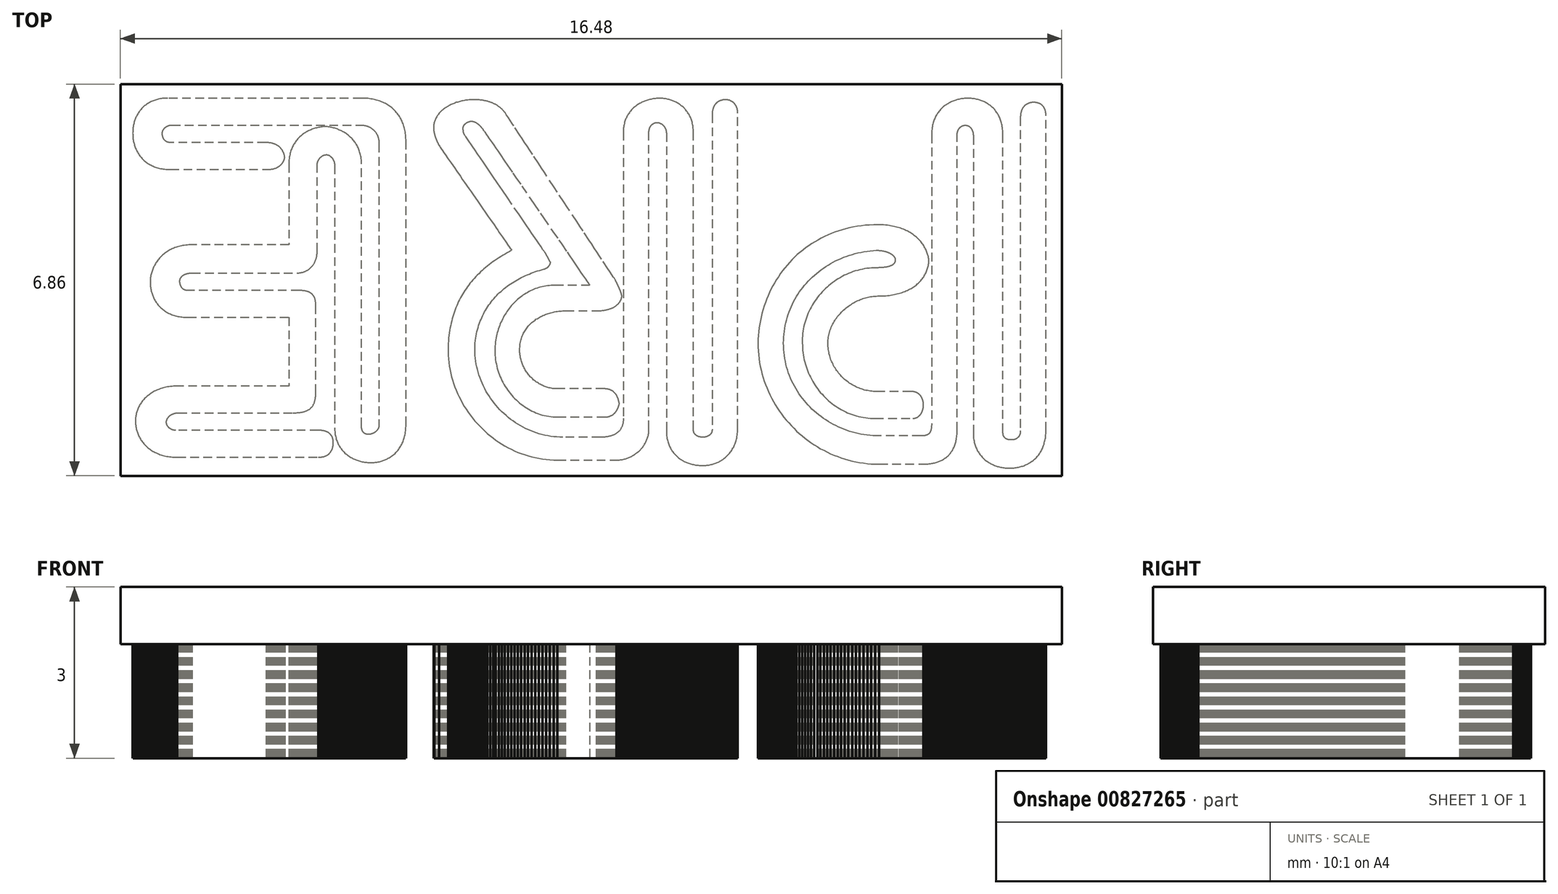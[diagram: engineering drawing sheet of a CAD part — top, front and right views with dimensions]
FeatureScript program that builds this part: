
annotation { "Feature Type Name" : "Feature", "Feature Type Description" : "" }
export const myFeature = defineFeature(function(context is Context, id is Id, definition is map)
    precondition{}
    {
        {
            var Q0;
            Q0=qCreatedBy(makeId("Top.planeOp"),FACE);
            var sketch = newSketch(context, id + "F0", { "sketchPlane" : qUnion([Q0])});
            skLineSegment(sketch, "E0", {"start": v(0.77, -0.53) * mm, "end": v(0.77, -0.53) * mm});
            skLineSegment(sketch, "E1", {"start": v(0.77, -0.53) * mm, "end": v(0.78, -0.54) * mm});
            skLineSegment(sketch, "E2", {"start": v(0.78, -0.54) * mm, "end": v(0.79, -0.55) * mm});
            skLineSegment(sketch, "E3", {"start": v(0.79, -0.55) * mm, "end": v(0.8, -0.57) * mm});
            skLineSegment(sketch, "E4", {"start": v(0.8, -0.57) * mm, "end": v(0.81, -0.59) * mm});
            skLineSegment(sketch, "E5", {"start": v(0.81, -0.59) * mm, "end": v(0.83, -0.61) * mm});
            skLineSegment(sketch, "E6", {"start": v(0.83, -0.61) * mm, "end": v(0.85, -0.64) * mm});
            skLineSegment(sketch, "E7", {"start": v(0.85, -0.64) * mm, "end": v(0.87, -0.67) * mm});
            skLineSegment(sketch, "E8", {"start": v(0.87, -0.67) * mm, "end": v(0.9, -0.7) * mm});
            skLineSegment(sketch, "E9", {"start": v(0.9, -0.7) * mm, "end": v(0.92, -0.74) * mm});
            skLineSegment(sketch, "E10", {"start": v(0.92, -0.74) * mm, "end": v(0.95, -0.79) * mm});
            skLineSegment(sketch, "E11", {"start": v(0.95, -0.79) * mm, "end": v(0.98, -0.83) * mm});
            skLineSegment(sketch, "E12", {"start": v(0.98, -0.83) * mm, "end": v(1, -0.88) * mm});
            skLineSegment(sketch, "E13", {"start": v(1, -0.88) * mm, "end": v(1.04, -0.93) * mm});
            skLineSegment(sketch, "E14", {"start": v(1.04, -0.93) * mm, "end": v(1.08, -0.98) * mm});
            skLineSegment(sketch, "E15", {"start": v(1.08, -0.98) * mm, "end": v(1.11, -1.03) * mm});
            skLineSegment(sketch, "E16", {"start": v(1.11, -1.03) * mm, "end": v(1.15, -1.08) * mm});
            skLineSegment(sketch, "E17", {"start": v(1.15, -1.08) * mm, "end": v(1.19, -1.14) * mm});
            skLineSegment(sketch, "E18", {"start": v(1.19, -1.14) * mm, "end": v(1.23, -1.2) * mm});
            skLineSegment(sketch, "E19", {"start": v(1.23, -1.2) * mm, "end": v(1.27, -1.26) * mm});
            skLineSegment(sketch, "E20", {"start": v(1.27, -1.26) * mm, "end": v(1.31, -1.32) * mm});
            skLineSegment(sketch, "E21", {"start": v(1.31, -1.32) * mm, "end": v(1.35, -1.38) * mm});
            skLineSegment(sketch, "E22", {"start": v(1.35, -1.38) * mm, "end": v(1.4, -1.44) * mm});
            skLineSegment(sketch, "E23", {"start": v(1.4, -1.44) * mm, "end": v(1.44, -1.5) * mm});
            skLineSegment(sketch, "E24", {"start": v(1.44, -1.5) * mm, "end": v(1.48, -1.57) * mm});
            skLineSegment(sketch, "E25", {"start": v(1.48, -1.57) * mm, "end": v(1.52, -1.63) * mm});
            skLineSegment(sketch, "E26", {"start": v(1.52, -1.63) * mm, "end": v(1.56, -1.69) * mm});
            skLineSegment(sketch, "E27", {"start": v(1.56, -1.69) * mm, "end": v(1.6, -1.75) * mm});
            skLineSegment(sketch, "E28", {"start": v(1.6, -1.75) * mm, "end": v(1.65, -1.81) * mm});
            skLineSegment(sketch, "E29", {"start": v(1.65, -1.81) * mm, "end": v(1.69, -1.87) * mm});
            skLineSegment(sketch, "E30", {"start": v(1.69, -1.87) * mm, "end": v(1.73, -1.93) * mm});
            skLineSegment(sketch, "E31", {"start": v(1.73, -1.93) * mm, "end": v(1.77, -1.99) * mm});
            skLineSegment(sketch, "E32", {"start": v(1.77, -1.99) * mm, "end": v(1.8, -2.05) * mm});
            skLineSegment(sketch, "E33", {"start": v(1.8, -2.05) * mm, "end": v(1.84, -2.1) * mm});
            skLineSegment(sketch, "E34", {"start": v(1.84, -2.1) * mm, "end": v(1.88, -2.15) * mm});
            skLineSegment(sketch, "E35", {"start": v(1.88, -2.15) * mm, "end": v(1.91, -2.2) * mm});
            skLineSegment(sketch, "E36", {"start": v(1.91, -2.2) * mm, "end": v(1.95, -2.25) * mm});
            skLineSegment(sketch, "E37", {"start": v(1.95, -2.25) * mm, "end": v(1.98, -2.3) * mm});
            skLineSegment(sketch, "E38", {"start": v(1.98, -2.3) * mm, "end": v(2, -2.35) * mm});
            skLineSegment(sketch, "E39", {"start": v(2, -2.35) * mm, "end": v(2.04, -2.39) * mm});
            skLineSegment(sketch, "E40", {"start": v(2.04, -2.39) * mm, "end": v(2.06, -2.42) * mm});
            skLineSegment(sketch, "E41", {"start": v(2.06, -2.42) * mm, "end": v(2.09, -2.46) * mm});
            skLineSegment(sketch, "E42", {"start": v(2.09, -2.46) * mm, "end": v(2.1, -2.5) * mm});
            skLineSegment(sketch, "E43", {"start": v(2.1, -2.5) * mm, "end": v(2.13, -2.52) * mm});
            skLineSegment(sketch, "E44", {"start": v(2.13, -2.52) * mm, "end": v(2.15, -2.54) * mm});
            skLineSegment(sketch, "E45", {"start": v(2.15, -2.54) * mm, "end": v(2.16, -2.56) * mm});
            skLineSegment(sketch, "E46", {"start": v(2.16, -2.56) * mm, "end": v(2.17, -2.58) * mm});
            skLineSegment(sketch, "E47", {"start": v(2.17, -2.58) * mm, "end": v(2.18, -2.6) * mm});
            skLineSegment(sketch, "E48", {"start": v(2.18, -2.6) * mm, "end": v(2.18, -2.6) * mm});
            skLineSegment(sketch, "E49", {"start": v(2.18, -2.6) * mm, "end": v(2.19, -2.6) * mm});
            skLineSegment(sketch, "E50", {"start": v(2.19, -2.6) * mm, "end": v(2.19, -2.6) * mm});
            skLineSegment(sketch, "E51", {"start": v(2.19, -2.6) * mm, "end": v(2.19, -2.61) * mm});
            skLineSegment(sketch, "E52", {"start": v(2.19, -2.61) * mm, "end": v(2.2, -2.61) * mm});
            skLineSegment(sketch, "E53", {"start": v(2.2, -2.61) * mm, "end": v(2.2, -2.62) * mm});
            skLineSegment(sketch, "E54", {"start": v(2.2, -2.62) * mm, "end": v(2.2, -2.62) * mm});
            skLineSegment(sketch, "E55", {"start": v(2.2, -2.62) * mm, "end": v(2.2, -2.63) * mm});
            skLineSegment(sketch, "E56", {"start": v(2.2, -2.63) * mm, "end": v(2.2, -2.63) * mm});
            skLineSegment(sketch, "E57", {"start": v(2.2, -2.63) * mm, "end": v(2.2, -2.64) * mm});
            skLineSegment(sketch, "E58", {"start": v(2.2, -2.64) * mm, "end": v(2.2, -2.64) * mm});
            skLineSegment(sketch, "E59", {"start": v(2.2, -2.64) * mm, "end": v(2.2, -2.65) * mm});
            skLineSegment(sketch, "E60", {"start": v(2.2, -2.65) * mm, "end": v(2.2, -2.65) * mm});
            skLineSegment(sketch, "E61", {"start": v(2.2, -2.65) * mm, "end": v(2.2, -2.66) * mm});
            skLineSegment(sketch, "E62", {"start": v(2.2, -2.66) * mm, "end": v(2.2, -2.66) * mm});
            skLineSegment(sketch, "E63", {"start": v(2.2, -2.66) * mm, "end": v(2.2, -2.67) * mm});
            skLineSegment(sketch, "E64", {"start": v(2.2, -2.67) * mm, "end": v(2.2, -2.67) * mm});
            skLineSegment(sketch, "E65", {"start": v(2.2, -2.67) * mm, "end": v(2.2, -2.68) * mm});
            skLineSegment(sketch, "E66", {"start": v(2.2, -2.68) * mm, "end": v(2.2, -2.68) * mm});
            skLineSegment(sketch, "E67", {"start": v(2.2, -2.68) * mm, "end": v(2.2, -2.69) * mm});
            skLineSegment(sketch, "E68", {"start": v(2.2, -2.69) * mm, "end": v(2.2, -2.69) * mm});
            skLineSegment(sketch, "E69", {"start": v(2.2, -2.69) * mm, "end": v(2.2, -2.7) * mm});
            skLineSegment(sketch, "E70", {"start": v(2.2, -2.7) * mm, "end": v(2.2, -2.7) * mm});
            skLineSegment(sketch, "E71", {"start": v(2.2, -2.7) * mm, "end": v(2.2, -2.71) * mm});
            skLineSegment(sketch, "E72", {"start": v(2.2, -2.71) * mm, "end": v(2.2, -2.71) * mm});
            skLineSegment(sketch, "E73", {"start": v(2.2, -2.71) * mm, "end": v(2.2, -2.72) * mm});
            skLineSegment(sketch, "E74", {"start": v(2.2, -2.72) * mm, "end": v(2.2, -2.72) * mm});
            skLineSegment(sketch, "E75", {"start": v(2.2, -2.72) * mm, "end": v(2.2, -2.73) * mm});
            skLineSegment(sketch, "E76", {"start": v(2.2, -2.73) * mm, "end": v(2.2, -2.73) * mm});
            skLineSegment(sketch, "E77", {"start": v(2.2, -2.73) * mm, "end": v(2.2, -2.74) * mm});
            skLineSegment(sketch, "E78", {"start": v(2.2, -2.74) * mm, "end": v(2.2, -2.74) * mm});
            skLineSegment(sketch, "E79", {"start": v(2.2, -2.74) * mm, "end": v(2.2, -2.75) * mm});
            skLineSegment(sketch, "E80", {"start": v(2.2, -2.75) * mm, "end": v(2.2, -2.75) * mm});
            skLineSegment(sketch, "E81", {"start": v(2.2, -2.75) * mm, "end": v(2.2, -2.76) * mm});
            skLineSegment(sketch, "E82", {"start": v(2.2, -2.76) * mm, "end": v(2.2, -2.76) * mm});
            skLineSegment(sketch, "E83", {"start": v(2.2, -2.76) * mm, "end": v(2.2, -2.77) * mm});
            skLineSegment(sketch, "E84", {"start": v(2.2, -2.77) * mm, "end": v(2.2, -2.77) * mm});
            skLineSegment(sketch, "E85", {"start": v(2.2, -2.77) * mm, "end": v(2.19, -2.77) * mm});
            skLineSegment(sketch, "E86", {"start": v(2.19, -2.77) * mm, "end": v(2.19, -2.78) * mm});
            skLineSegment(sketch, "E87", {"start": v(2.19, -2.78) * mm, "end": v(2.18, -2.78) * mm});
            skLineSegment(sketch, "E88", {"start": v(2.18, -2.78) * mm, "end": v(2.18, -2.78) * mm});
            skLineSegment(sketch, "E89", {"start": v(2.18, -2.78) * mm, "end": v(2.18, -2.79) * mm});
            skLineSegment(sketch, "E90", {"start": v(2.18, -2.79) * mm, "end": v(2.18, -2.79) * mm});
            skLineSegment(sketch, "E91", {"start": v(2.18, -2.79) * mm, "end": v(2.17, -2.8) * mm});
            skLineSegment(sketch, "E92", {"start": v(2.17, -2.8) * mm, "end": v(2.17, -2.8) * mm});
            skLineSegment(sketch, "E93", {"start": v(2.17, -2.8) * mm, "end": v(2.16, -2.8) * mm});
            skLineSegment(sketch, "E94", {"start": v(2.16, -2.8) * mm, "end": v(2.16, -2.8) * mm});
            skLineSegment(sketch, "E95", {"start": v(2.16, -2.8) * mm, "end": v(2.15, -2.8) * mm});
            skLineSegment(sketch, "E96", {"start": v(2.15, -2.8) * mm, "end": v(2.15, -2.81) * mm});
            skLineSegment(sketch, "E97", {"start": v(2.15, -2.81) * mm, "end": v(2.14, -2.81) * mm});
            skLineSegment(sketch, "E98", {"start": v(2.14, -2.81) * mm, "end": v(2.14, -2.81) * mm});
            skLineSegment(sketch, "E99", {"start": v(2.14, -2.81) * mm, "end": v(2.14, -2.82) * mm});
            skLineSegment(sketch, "E100", {"start": v(2.14, -2.82) * mm, "end": v(2.13, -2.82) * mm});
            skLineSegment(sketch, "E101", {"start": v(2.13, -2.82) * mm, "end": v(2.13, -2.82) * mm});
            skLineSegment(sketch, "E102", {"start": v(2.13, -2.82) * mm, "end": v(2.12, -2.82) * mm});
            skLineSegment(sketch, "E103", {"start": v(2.12, -2.82) * mm, "end": v(2.12, -2.83) * mm});
            skLineSegment(sketch, "E104", {"start": v(2.12, -2.83) * mm, "end": v(2.11, -2.83) * mm});
            skLineSegment(sketch, "E105", {"start": v(2.11, -2.83) * mm, "end": v(2.11, -2.83) * mm});
            skLineSegment(sketch, "E106", {"start": v(2.11, -2.83) * mm, "end": v(2.1, -2.83) * mm});
            skLineSegment(sketch, "E107", {"start": v(2.1, -2.83) * mm, "end": v(2.1, -2.83) * mm});
            skLineSegment(sketch, "E108", {"start": v(2.1, -2.83) * mm, "end": v(2.09, -2.83) * mm});
            skLineSegment(sketch, "E109", {"start": v(2.09, -2.83) * mm, "end": v(2.09, -2.84) * mm});
            skLineSegment(sketch, "E110", {"start": v(2.09, -2.84) * mm, "end": v(2.08, -2.84) * mm});
            skLineSegment(sketch, "E111", {"start": v(2.08, -2.84) * mm, "end": v(2.08, -2.84) * mm});
            skLineSegment(sketch, "E112", {"start": v(2.08, -2.84) * mm, "end": v(2.07, -2.84) * mm});
            skLineSegment(sketch, "E113", {"start": v(2.07, -2.84) * mm, "end": v(2.07, -2.84) * mm});
            skLineSegment(sketch, "E114", {"start": v(2.07, -2.84) * mm, "end": v(2.06, -2.84) * mm});
            skLineSegment(sketch, "E115", {"start": v(2.06, -2.84) * mm, "end": v(2.06, -2.84) * mm});
            skLineSegment(sketch, "E116", {"start": v(2.06, -2.84) * mm, "end": v(2.05, -2.84) * mm});
            skLineSegment(sketch, "E117", {"start": v(2.05, -2.84) * mm, "end": v(2.05, -2.84) * mm});
            skLineSegment(sketch, "E118", {"start": v(2.05, -2.84) * mm, "end": v(2.04, -2.84) * mm});
            skLineSegment(sketch, "E119", {"start": v(2.04, -2.84) * mm, "end": v(2.04, -2.83) * mm});
            skLineSegment(sketch, "E120", {"start": v(2.04, -2.83) * mm, "end": v(2.03, -2.83) * mm});
            skLineSegment(sketch, "E121", {"start": v(2.03, -2.83) * mm, "end": v(2.03, -2.83) * mm});
            skLineSegment(sketch, "E122", {"start": v(2.03, -2.83) * mm, "end": v(2.02, -2.83) * mm});
            skLineSegment(sketch, "E123", {"start": v(2.02, -2.83) * mm, "end": v(2.02, -2.83) * mm});
            skLineSegment(sketch, "E124", {"start": v(2.02, -2.83) * mm, "end": v(2.01, -2.83) * mm});
            skLineSegment(sketch, "E125", {"start": v(2.01, -2.83) * mm, "end": v(2, -2.83) * mm});
            skLineSegment(sketch, "E126", {"start": v(2, -2.83) * mm, "end": v(2, -2.82) * mm});
            skLineSegment(sketch, "E127", {"start": v(2, -2.82) * mm, "end": v(2, -2.82) * mm});
            skLineSegment(sketch, "E128", {"start": v(2, -2.82) * mm, "end": v(1.99, -2.82) * mm});
            skLineSegment(sketch, "E129", {"start": v(1.99, -2.82) * mm, "end": v(1.99, -2.81) * mm});
            skLineSegment(sketch, "E130", {"start": v(1.99, -2.81) * mm, "end": v(1.98, -2.81) * mm});
            skLineSegment(sketch, "E131", {"start": v(1.98, -2.81) * mm, "end": v(1.98, -2.8) * mm});
            skLineSegment(sketch, "E132", {"start": v(1.98, -2.8) * mm, "end": v(1.97, -2.8) * mm});
            skLineSegment(sketch, "E133", {"start": v(1.97, -2.8) * mm, "end": v(1.97, -2.8) * mm});
            skLineSegment(sketch, "E134", {"start": v(1.97, -2.8) * mm, "end": v(1.96, -2.8) * mm});
            skLineSegment(sketch, "E135", {"start": v(1.96, -2.8) * mm, "end": v(1.96, -2.8) * mm});
            skLineSegment(sketch, "E136", {"start": v(1.96, -2.8) * mm, "end": v(1.95, -2.8) * mm});
            skLineSegment(sketch, "E137", {"start": v(1.95, -2.8) * mm, "end": v(1.95, -2.79) * mm});
            skLineSegment(sketch, "E138", {"start": v(1.95, -2.79) * mm, "end": v(1.94, -2.79) * mm});
            skLineSegment(sketch, "E139", {"start": v(1.94, -2.79) * mm, "end": v(1.94, -2.78) * mm});
            skLineSegment(sketch, "E140", {"start": v(1.94, -2.78) * mm, "end": v(1.93, -2.78) * mm});
            skLineSegment(sketch, "E141", {"start": v(1.93, -2.78) * mm, "end": v(1.93, -2.77) * mm});
            skLineSegment(sketch, "E142", {"start": v(1.93, -2.77) * mm, "end": v(1.93, -2.77) * mm});
            skLineSegment(sketch, "E143", {"start": v(1.93, -2.77) * mm, "end": v(1.92, -2.76) * mm});
            skLineSegment(sketch, "E144", {"start": v(1.92, -2.76) * mm, "end": v(1.92, -2.76) * mm});
            skLineSegment(sketch, "E145", {"start": v(1.92, -2.76) * mm, "end": v(1.91, -2.75) * mm});
            skLineSegment(sketch, "E146", {"start": v(1.91, -2.75) * mm, "end": v(1.9, -2.75) * mm});
            skLineSegment(sketch, "E147", {"start": v(1.9, -2.75) * mm, "end": v(1.9, -2.74) * mm});
            skLineSegment(sketch, "E148", {"start": v(1.9, -2.74) * mm, "end": v(1.9, -2.74) * mm});
            skLineSegment(sketch, "E149", {"start": v(1.9, -2.74) * mm, "end": v(1.9, -2.73) * mm});
            skLineSegment(sketch, "E150", {"start": v(1.9, -2.73) * mm, "end": v(1.89, -2.72) * mm});
            skLineSegment(sketch, "E151", {"start": v(1.89, -2.72) * mm, "end": v(1.88, -2.72) * mm});
            skLineSegment(sketch, "E152", {"start": v(1.88, -2.72) * mm, "end": v(1.88, -2.7) * mm});
            skLineSegment(sketch, "E153", {"start": v(1.88, -2.7) * mm, "end": v(1.87, -2.7) * mm});
            skLineSegment(sketch, "E154", {"start": v(1.87, -2.7) * mm, "end": v(1.86, -2.7) * mm});
            skLineSegment(sketch, "E155", {"start": v(1.86, -2.7) * mm, "end": v(1.86, -2.69) * mm});
            skLineSegment(sketch, "E156", {"start": v(1.86, -2.69) * mm, "end": v(1.85, -2.68) * mm});
            skLineSegment(sketch, "E157", {"start": v(1.85, -2.68) * mm, "end": v(1.85, -2.67) * mm});
            skLineSegment(sketch, "E158", {"start": v(1.85, -2.67) * mm, "end": v(1.84, -2.67) * mm});
            skLineSegment(sketch, "E159", {"start": v(1.84, -2.67) * mm, "end": v(1.84, -2.66) * mm});
            skLineSegment(sketch, "E160", {"start": v(1.84, -2.66) * mm, "end": v(1.83, -2.65) * mm});
            skLineSegment(sketch, "E161", {"start": v(1.83, -2.65) * mm, "end": v(1.83, -2.65) * mm});
            skLineSegment(sketch, "E162", {"start": v(1.83, -2.65) * mm, "end": v(1.82, -2.64) * mm});
            skLineSegment(sketch, "E163", {"start": v(1.82, -2.64) * mm, "end": v(1.81, -2.62) * mm});
            skLineSegment(sketch, "E164", {"start": v(1.81, -2.62) * mm, "end": v(1.8, -2.6) * mm});
            skLineSegment(sketch, "E165", {"start": v(1.8, -2.6) * mm, "end": v(1.78, -2.57) * mm});
            skLineSegment(sketch, "E166", {"start": v(1.78, -2.57) * mm, "end": v(1.76, -2.54) * mm});
            skLineSegment(sketch, "E167", {"start": v(1.76, -2.54) * mm, "end": v(1.73, -2.5) * mm});
            skLineSegment(sketch, "E168", {"start": v(1.73, -2.5) * mm, "end": v(1.7, -2.46) * mm});
            skLineSegment(sketch, "E169", {"start": v(1.7, -2.46) * mm, "end": v(1.67, -2.42) * mm});
            skLineSegment(sketch, "E170", {"start": v(1.67, -2.42) * mm, "end": v(1.64, -2.37) * mm});
            skLineSegment(sketch, "E171", {"start": v(1.64, -2.37) * mm, "end": v(1.6, -2.32) * mm});
            skLineSegment(sketch, "E172", {"start": v(1.6, -2.32) * mm, "end": v(1.56, -2.26) * mm});
            skLineSegment(sketch, "E173", {"start": v(1.56, -2.26) * mm, "end": v(1.52, -2.2) * mm});
            skLineSegment(sketch, "E174", {"start": v(1.52, -2.2) * mm, "end": v(1.48, -2.14) * mm});
            skLineSegment(sketch, "E175", {"start": v(1.48, -2.14) * mm, "end": v(1.43, -2.07) * mm});
            skLineSegment(sketch, "E176", {"start": v(1.43, -2.07) * mm, "end": v(1.39, -2) * mm});
            skLineSegment(sketch, "E177", {"start": v(1.39, -2) * mm, "end": v(1.34, -1.93) * mm});
            skLineSegment(sketch, "E178", {"start": v(1.34, -1.93) * mm, "end": v(1.29, -1.86) * mm});
            skLineSegment(sketch, "E179", {"start": v(1.29, -1.86) * mm, "end": v(1.24, -1.78) * mm});
            skLineSegment(sketch, "E180", {"start": v(1.24, -1.78) * mm, "end": v(1.18, -1.7) * mm});
            skLineSegment(sketch, "E181", {"start": v(1.18, -1.7) * mm, "end": v(1.13, -1.63) * mm});
            skLineSegment(sketch, "E182", {"start": v(1.13, -1.63) * mm, "end": v(1.08, -1.55) * mm});
            skLineSegment(sketch, "E183", {"start": v(1.08, -1.55) * mm, "end": v(1.02, -1.47) * mm});
            skLineSegment(sketch, "E184", {"start": v(1.02, -1.47) * mm, "end": v(0.97, -1.39) * mm});
            skLineSegment(sketch, "E185", {"start": v(0.97, -1.39) * mm, "end": v(0.91, -1.3) * mm});
            skLineSegment(sketch, "E186", {"start": v(0.91, -1.3) * mm, "end": v(0.86, -1.23) * mm});
            skLineSegment(sketch, "E187", {"start": v(0.86, -1.23) * mm, "end": v(0.8, -1.15) * mm});
            skLineSegment(sketch, "E188", {"start": v(0.8, -1.15) * mm, "end": v(0.75, -1.07) * mm});
            skLineSegment(sketch, "E189", {"start": v(0.75, -1.07) * mm, "end": v(0.7, -0.99) * mm});
            skLineSegment(sketch, "E190", {"start": v(0.7, -0.99) * mm, "end": v(0.64, -0.9) * mm});
            skLineSegment(sketch, "E191", {"start": v(0.64, -0.9) * mm, "end": v(0.59, -0.83) * mm});
            skLineSegment(sketch, "E192", {"start": v(0.59, -0.83) * mm, "end": v(0.54, -0.76) * mm});
            skLineSegment(sketch, "E193", {"start": v(0.54, -0.76) * mm, "end": v(0.49, -0.68) * mm});
            skLineSegment(sketch, "E194", {"start": v(0.49, -0.68) * mm, "end": v(0.44, -0.61) * mm});
            skLineSegment(sketch, "E195", {"start": v(0.44, -0.61) * mm, "end": v(0.4, -0.54) * mm});
            skLineSegment(sketch, "E196", {"start": v(0.4, -0.54) * mm, "end": v(0.35, -0.48) * mm});
            skLineSegment(sketch, "E197", {"start": v(0.35, -0.48) * mm, "end": v(0.3, -0.41) * mm});
            skLineSegment(sketch, "E198", {"start": v(0.3, -0.41) * mm, "end": v(0.26, -0.35) * mm});
            skLineSegment(sketch, "E199", {"start": v(0.26, -0.35) * mm, "end": v(0.22, -0.3) * mm});
            skLineSegment(sketch, "E200", {"start": v(0.22, -0.3) * mm, "end": v(0.19, -0.24) * mm});
            skLineSegment(sketch, "E201", {"start": v(0.19, -0.24) * mm, "end": v(0.15, -0.2) * mm});
            skLineSegment(sketch, "E202", {"start": v(0.15, -0.2) * mm, "end": v(0.12, -0.15) * mm});
            skLineSegment(sketch, "E203", {"start": v(0.12, -0.15) * mm, "end": v(0.1, -0.1) * mm});
            skLineSegment(sketch, "E204", {"start": v(0.1, -0.1) * mm, "end": v(0.07, -0.07) * mm});
            skLineSegment(sketch, "E205", {"start": v(0.07, -0.07) * mm, "end": v(0.05, -0.04) * mm});
            skLineSegment(sketch, "E206", {"start": v(0.05, -0.04) * mm, "end": v(0.03, -0.01) * mm});
            skLineSegment(sketch, "E207", {"start": v(0.03, -0.01) * mm, "end": v(0.01, 0) * mm});
            skLineSegment(sketch, "E208", {"start": v(0.01, 0) * mm, "end": v(0, 0.02) * mm});
            skLineSegment(sketch, "E209", {"start": v(0, 0.02) * mm, "end": v(0, 0.03) * mm});
            skLineSegment(sketch, "E210", {"start": v(0, 0.03) * mm, "end": v(0, 0.04) * mm});
            skLineSegment(sketch, "E211", {"start": v(0, 0.04) * mm, "end": v(0, 0.04) * mm});
            skLineSegment(sketch, "E212", {"start": v(0, 0.04) * mm, "end": v(0.01, 0.04) * mm});
            skLineSegment(sketch, "E213", {"start": v(0.01, 0.04) * mm, "end": v(0.02, 0.04) * mm});
            skLineSegment(sketch, "E214", {"start": v(0.02, 0.04) * mm, "end": v(0.03, 0.04) * mm});
            skLineSegment(sketch, "E215", {"start": v(0.03, 0.04) * mm, "end": v(0.04, 0.04) * mm});
            skLineSegment(sketch, "E216", {"start": v(0.04, 0.04) * mm, "end": v(0.05, 0.04) * mm});
            skLineSegment(sketch, "E217", {"start": v(0.05, 0.04) * mm, "end": v(0.06, 0.04) * mm});
            skLineSegment(sketch, "E218", {"start": v(0.06, 0.04) * mm, "end": v(0.07, 0.04) * mm});
            skLineSegment(sketch, "E219", {"start": v(0.07, 0.04) * mm, "end": v(0.08, 0.04) * mm});
            skLineSegment(sketch, "E220", {"start": v(0.08, 0.04) * mm, "end": v(0.1, 0.04) * mm});
            skLineSegment(sketch, "E221", {"start": v(0.1, 0.04) * mm, "end": v(0.11, 0.04) * mm});
            skLineSegment(sketch, "E222", {"start": v(0.11, 0.04) * mm, "end": v(0.13, 0.04) * mm});
            skLineSegment(sketch, "E223", {"start": v(0.13, 0.04) * mm, "end": v(0.14, 0.04) * mm});
            skLineSegment(sketch, "E224", {"start": v(0.14, 0.04) * mm, "end": v(0.16, 0.04) * mm});
            skLineSegment(sketch, "E225", {"start": v(0.16, 0.04) * mm, "end": v(0.17, 0.04) * mm});
            skLineSegment(sketch, "E226", {"start": v(0.17, 0.04) * mm, "end": v(0.2, 0.04) * mm});
            skLineSegment(sketch, "E227", {"start": v(0.2, 0.04) * mm, "end": v(0.2, 0.04) * mm});
            skLineSegment(sketch, "E228", {"start": v(0.2, 0.04) * mm, "end": v(0.23, 0.04) * mm});
            skLineSegment(sketch, "E229", {"start": v(0.23, 0.04) * mm, "end": v(0.25, 0.04) * mm});
            skLineSegment(sketch, "E230", {"start": v(0.25, 0.04) * mm, "end": v(0.26, 0.04) * mm});
            skLineSegment(sketch, "E231", {"start": v(0.26, 0.04) * mm, "end": v(0.28, 0.04) * mm});
            skLineSegment(sketch, "E232", {"start": v(0.28, 0.04) * mm, "end": v(0.3, 0.04) * mm});
            skLineSegment(sketch, "E233", {"start": v(0.3, 0.04) * mm, "end": v(0.32, 0.04) * mm});
            skLineSegment(sketch, "E234", {"start": v(0.32, 0.04) * mm, "end": v(0.34, 0.04) * mm});
            skLineSegment(sketch, "E235", {"start": v(0.34, 0.04) * mm, "end": v(0.36, 0.04) * mm});
            skLineSegment(sketch, "E236", {"start": v(0.36, 0.04) * mm, "end": v(0.37, 0.04) * mm});
            skLineSegment(sketch, "E237", {"start": v(0.37, 0.04) * mm, "end": v(0.4, 0.04) * mm});
            skLineSegment(sketch, "E238", {"start": v(0.4, 0.04) * mm, "end": v(0.4, 0.04) * mm});
            skLineSegment(sketch, "E239", {"start": v(0.4, 0.04) * mm, "end": v(0.43, 0.04) * mm});
            skLineSegment(sketch, "E240", {"start": v(0.43, 0.04) * mm, "end": v(0.44, 0.04) * mm});
            skLineSegment(sketch, "E241", {"start": v(0.44, 0.04) * mm, "end": v(0.46, 0.04) * mm});
            skLineSegment(sketch, "E242", {"start": v(0.46, 0.04) * mm, "end": v(0.47, 0.04) * mm});
            skLineSegment(sketch, "E243", {"start": v(0.47, 0.04) * mm, "end": v(0.49, 0.04) * mm});
            skLineSegment(sketch, "E244", {"start": v(0.49, 0.04) * mm, "end": v(0.5, 0.04) * mm});
            skLineSegment(sketch, "E245", {"start": v(0.5, 0.04) * mm, "end": v(0.52, 0.04) * mm});
            skLineSegment(sketch, "E246", {"start": v(0.52, 0.04) * mm, "end": v(0.53, 0.04) * mm});
            skLineSegment(sketch, "E247", {"start": v(0.53, 0.04) * mm, "end": v(0.54, 0.04) * mm});
            skLineSegment(sketch, "E248", {"start": v(0.54, 0.04) * mm, "end": v(0.55, 0.04) * mm});
            skLineSegment(sketch, "E249", {"start": v(0.55, 0.04) * mm, "end": v(0.56, 0.04) * mm});
            skLineSegment(sketch, "E250", {"start": v(0.56, 0.04) * mm, "end": v(0.57, 0.04) * mm});
            skLineSegment(sketch, "E251", {"start": v(0.57, 0.04) * mm, "end": v(0.58, 0.04) * mm});
            skLineSegment(sketch, "E252", {"start": v(0.58, 0.04) * mm, "end": v(0.59, 0.04) * mm});
            skLineSegment(sketch, "E253", {"start": v(0.59, 0.04) * mm, "end": v(0.6, 0.04) * mm});
            skLineSegment(sketch, "E254", {"start": v(0.6, 0.04) * mm, "end": v(0.6, 0.04) * mm});
            skLineSegment(sketch, "E255", {"start": v(0.6, 0.04) * mm, "end": v(0.64, 0.04) * mm});
            skLineSegment(sketch, "E256", {"start": v(0.64, 0.04) * mm, "end": v(0.67, 0.04) * mm});
            skLineSegment(sketch, "E257", {"start": v(0.67, 0.04) * mm, "end": v(0.7, 0.04) * mm});
            skLineSegment(sketch, "E258", {"start": v(0.7, 0.04) * mm, "end": v(0.73, 0.05) * mm});
            skLineSegment(sketch, "E259", {"start": v(0.73, 0.05) * mm, "end": v(0.77, 0.05) * mm});
            skLineSegment(sketch, "E260", {"start": v(0.77, 0.05) * mm, "end": v(0.8, 0.06) * mm});
            skLineSegment(sketch, "E261", {"start": v(0.8, 0.06) * mm, "end": v(0.83, 0.06) * mm});
            skLineSegment(sketch, "E262", {"start": v(0.83, 0.06) * mm, "end": v(0.86, 0.07) * mm});
            skLineSegment(sketch, "E263", {"start": v(0.86, 0.07) * mm, "end": v(0.89, 0.08) * mm});
            skLineSegment(sketch, "E264", {"start": v(0.89, 0.08) * mm, "end": v(0.92, 0.09) * mm});
            skLineSegment(sketch, "E265", {"start": v(0.92, 0.09) * mm, "end": v(0.94, 0.1) * mm});
            skLineSegment(sketch, "E266", {"start": v(0.94, 0.1) * mm, "end": v(0.97, 0.1) * mm});
            skLineSegment(sketch, "E267", {"start": v(0.97, 0.1) * mm, "end": v(1, 0.12) * mm});
            skLineSegment(sketch, "E268", {"start": v(1, 0.12) * mm, "end": v(1.03, 0.13) * mm});
            skLineSegment(sketch, "E269", {"start": v(1.03, 0.13) * mm, "end": v(1.06, 0.15) * mm});
            skLineSegment(sketch, "E270", {"start": v(1.06, 0.15) * mm, "end": v(1.08, 0.16) * mm});
            skLineSegment(sketch, "E271", {"start": v(1.08, 0.16) * mm, "end": v(1.1, 0.18) * mm});
            skLineSegment(sketch, "E272", {"start": v(1.1, 0.18) * mm, "end": v(1.13, 0.2) * mm});
            skLineSegment(sketch, "E273", {"start": v(1.13, 0.2) * mm, "end": v(1.16, 0.21) * mm});
            skLineSegment(sketch, "E274", {"start": v(1.16, 0.21) * mm, "end": v(1.19, 0.23) * mm});
            skLineSegment(sketch, "E275", {"start": v(1.19, 0.23) * mm, "end": v(1.2, 0.25) * mm});
            skLineSegment(sketch, "E276", {"start": v(1.2, 0.25) * mm, "end": v(1.23, 0.27) * mm});
            skLineSegment(sketch, "E277", {"start": v(1.23, 0.27) * mm, "end": v(1.26, 0.29) * mm});
            skLineSegment(sketch, "E278", {"start": v(1.26, 0.29) * mm, "end": v(1.28, 0.3) * mm});
            skLineSegment(sketch, "E279", {"start": v(1.28, 0.3) * mm, "end": v(1.3, 0.33) * mm});
            skLineSegment(sketch, "E280", {"start": v(1.3, 0.33) * mm, "end": v(1.32, 0.35) * mm});
            skLineSegment(sketch, "E281", {"start": v(1.32, 0.35) * mm, "end": v(1.34, 0.37) * mm});
            skLineSegment(sketch, "E282", {"start": v(1.34, 0.37) * mm, "end": v(1.36, 0.4) * mm});
            skLineSegment(sketch, "E283", {"start": v(1.36, 0.4) * mm, "end": v(1.38, 0.42) * mm});
            skLineSegment(sketch, "E284", {"start": v(1.38, 0.42) * mm, "end": v(1.4, 0.44) * mm});
            skLineSegment(sketch, "E285", {"start": v(1.4, 0.44) * mm, "end": v(1.42, 0.47) * mm});
            skLineSegment(sketch, "E286", {"start": v(1.42, 0.47) * mm, "end": v(1.44, 0.5) * mm});
            skLineSegment(sketch, "E287", {"start": v(1.44, 0.5) * mm, "end": v(1.46, 0.52) * mm});
            skLineSegment(sketch, "E288", {"start": v(1.46, 0.52) * mm, "end": v(1.47, 0.55) * mm});
            skLineSegment(sketch, "E289", {"start": v(1.47, 0.55) * mm, "end": v(1.5, 0.57) * mm});
            skLineSegment(sketch, "E290", {"start": v(1.5, 0.57) * mm, "end": v(1.5, 0.6) * mm});
            skLineSegment(sketch, "E291", {"start": v(1.5, 0.6) * mm, "end": v(1.52, 0.63) * mm});
            skLineSegment(sketch, "E292", {"start": v(1.52, 0.63) * mm, "end": v(1.53, 0.66) * mm});
            skLineSegment(sketch, "E293", {"start": v(1.53, 0.66) * mm, "end": v(1.55, 0.69) * mm});
            skLineSegment(sketch, "E294", {"start": v(1.55, 0.69) * mm, "end": v(1.56, 0.72) * mm});
            skLineSegment(sketch, "E295", {"start": v(1.56, 0.72) * mm, "end": v(1.57, 0.74) * mm});
            skLineSegment(sketch, "E296", {"start": v(1.57, 0.74) * mm, "end": v(1.58, 0.77) * mm});
            skLineSegment(sketch, "E297", {"start": v(1.58, 0.77) * mm, "end": v(1.6, 0.8) * mm});
            skLineSegment(sketch, "E298", {"start": v(1.6, 0.8) * mm, "end": v(1.6, 0.84) * mm});
            skLineSegment(sketch, "E299", {"start": v(1.6, 0.84) * mm, "end": v(1.61, 0.87) * mm});
            skLineSegment(sketch, "E300", {"start": v(1.61, 0.87) * mm, "end": v(1.62, 0.9) * mm});
            skLineSegment(sketch, "E301", {"start": v(1.62, 0.9) * mm, "end": v(1.63, 0.93) * mm});
            skLineSegment(sketch, "E302", {"start": v(1.63, 0.93) * mm, "end": v(1.63, 0.96) * mm});
            skLineSegment(sketch, "E303", {"start": v(1.63, 0.96) * mm, "end": v(1.64, 1) * mm});
            skLineSegment(sketch, "E304", {"start": v(1.64, 1) * mm, "end": v(1.64, 1.03) * mm});
            skLineSegment(sketch, "E305", {"start": v(1.64, 1.03) * mm, "end": v(1.65, 1.07) * mm});
            skLineSegment(sketch, "E306", {"start": v(1.65, 1.07) * mm, "end": v(1.65, 1.1) * mm});
            skLineSegment(sketch, "E307", {"start": v(1.65, 1.1) * mm, "end": v(1.65, 1.14) * mm});
            skLineSegment(sketch, "E308", {"start": v(1.65, 1.14) * mm, "end": v(1.65, 1.18) * mm});
            skLineSegment(sketch, "E309", {"start": v(1.65, 1.18) * mm, "end": v(1.65, 1.22) * mm});
            skLineSegment(sketch, "E310", {"start": v(1.65, 1.22) * mm, "end": v(1.65, 1.26) * mm});
            skLineSegment(sketch, "E311", {"start": v(1.65, 1.26) * mm, "end": v(1.65, 1.3) * mm});
            skLineSegment(sketch, "E312", {"start": v(1.65, 1.3) * mm, "end": v(1.64, 1.34) * mm});
            skLineSegment(sketch, "E313", {"start": v(1.64, 1.34) * mm, "end": v(1.64, 1.38) * mm});
            skLineSegment(sketch, "E314", {"start": v(1.64, 1.38) * mm, "end": v(1.63, 1.42) * mm});
            skLineSegment(sketch, "E315", {"start": v(1.63, 1.42) * mm, "end": v(1.62, 1.45) * mm});
            skLineSegment(sketch, "E316", {"start": v(1.62, 1.45) * mm, "end": v(1.61, 1.5) * mm});
            skLineSegment(sketch, "E317", {"start": v(1.61, 1.5) * mm, "end": v(1.6, 1.53) * mm});
            skLineSegment(sketch, "E318", {"start": v(1.6, 1.53) * mm, "end": v(1.59, 1.57) * mm});
            skLineSegment(sketch, "E319", {"start": v(1.59, 1.57) * mm, "end": v(1.58, 1.6) * mm});
            skLineSegment(sketch, "E320", {"start": v(1.58, 1.6) * mm, "end": v(1.56, 1.64) * mm});
            skLineSegment(sketch, "E321", {"start": v(1.56, 1.64) * mm, "end": v(1.55, 1.67) * mm});
            skLineSegment(sketch, "E322", {"start": v(1.55, 1.67) * mm, "end": v(1.53, 1.7) * mm});
            skLineSegment(sketch, "E323", {"start": v(1.53, 1.7) * mm, "end": v(1.51, 1.74) * mm});
            skLineSegment(sketch, "E324", {"start": v(1.51, 1.74) * mm, "end": v(1.5, 1.78) * mm});
            skLineSegment(sketch, "E325", {"start": v(1.5, 1.78) * mm, "end": v(1.47, 1.8) * mm});
            skLineSegment(sketch, "E326", {"start": v(1.47, 1.8) * mm, "end": v(1.45, 1.84) * mm});
            skLineSegment(sketch, "E327", {"start": v(1.45, 1.84) * mm, "end": v(1.43, 1.87) * mm});
            skLineSegment(sketch, "E328", {"start": v(1.43, 1.87) * mm, "end": v(1.4, 1.9) * mm});
            skLineSegment(sketch, "E329", {"start": v(1.4, 1.9) * mm, "end": v(1.38, 1.93) * mm});
            skLineSegment(sketch, "E330", {"start": v(1.38, 1.93) * mm, "end": v(1.36, 1.96) * mm});
            skLineSegment(sketch, "E331", {"start": v(1.36, 1.96) * mm, "end": v(1.33, 2) * mm});
            skLineSegment(sketch, "E332", {"start": v(1.33, 2) * mm, "end": v(1.3, 2.02) * mm});
            skLineSegment(sketch, "E333", {"start": v(1.3, 2.02) * mm, "end": v(1.28, 2.05) * mm});
            skLineSegment(sketch, "E334", {"start": v(1.28, 2.05) * mm, "end": v(1.25, 2.07) * mm});
            skLineSegment(sketch, "E335", {"start": v(1.25, 2.07) * mm, "end": v(1.22, 2.1) * mm});
            skLineSegment(sketch, "E336", {"start": v(1.22, 2.1) * mm, "end": v(1.2, 2.12) * mm});
            skLineSegment(sketch, "E337", {"start": v(1.2, 2.12) * mm, "end": v(1.16, 2.14) * mm});
            skLineSegment(sketch, "E338", {"start": v(1.16, 2.14) * mm, "end": v(1.13, 2.16) * mm});
            skLineSegment(sketch, "E339", {"start": v(1.13, 2.16) * mm, "end": v(1.1, 2.19) * mm});
            skLineSegment(sketch, "E340", {"start": v(1.1, 2.19) * mm, "end": v(1.07, 2.2) * mm});
            skLineSegment(sketch, "E341", {"start": v(1.07, 2.2) * mm, "end": v(1.04, 2.22) * mm});
            skLineSegment(sketch, "E342", {"start": v(1.04, 2.22) * mm, "end": v(1, 2.24) * mm});
            skLineSegment(sketch, "E343", {"start": v(1, 2.24) * mm, "end": v(0.97, 2.26) * mm});
            skLineSegment(sketch, "E344", {"start": v(0.97, 2.26) * mm, "end": v(0.93, 2.27) * mm});
            skLineSegment(sketch, "E345", {"start": v(0.93, 2.27) * mm, "end": v(0.9, 2.29) * mm});
            skLineSegment(sketch, "E346", {"start": v(0.9, 2.29) * mm, "end": v(0.86, 2.3) * mm});
            skLineSegment(sketch, "E347", {"start": v(0.86, 2.3) * mm, "end": v(0.83, 2.3) * mm});
            skLineSegment(sketch, "E348", {"start": v(0.83, 2.3) * mm, "end": v(0.79, 2.32) * mm});
            skLineSegment(sketch, "E349", {"start": v(0.79, 2.32) * mm, "end": v(0.75, 2.33) * mm});
            skLineSegment(sketch, "E350", {"start": v(0.75, 2.33) * mm, "end": v(0.71, 2.33) * mm});
            skLineSegment(sketch, "E351", {"start": v(0.71, 2.33) * mm, "end": v(0.68, 2.34) * mm});
            skLineSegment(sketch, "E352", {"start": v(0.68, 2.34) * mm, "end": v(0.64, 2.34) * mm});
            skLineSegment(sketch, "E353", {"start": v(0.64, 2.34) * mm, "end": v(0.6, 2.34) * mm});
            skLineSegment(sketch, "E354", {"start": v(0.6, 2.34) * mm, "end": v(0.56, 2.35) * mm});
            skLineSegment(sketch, "E355", {"start": v(0.56, 2.35) * mm, "end": v(0.56, 2.35) * mm});
            skLineSegment(sketch, "E356", {"start": v(0.56, 2.35) * mm, "end": v(0.55, 2.35) * mm});
            skLineSegment(sketch, "E357", {"start": v(0.55, 2.35) * mm, "end": v(0.54, 2.35) * mm});
            skLineSegment(sketch, "E358", {"start": v(0.54, 2.35) * mm, "end": v(0.54, 2.35) * mm});
            skLineSegment(sketch, "E359", {"start": v(0.54, 2.35) * mm, "end": v(0.53, 2.35) * mm});
            skLineSegment(sketch, "E360", {"start": v(0.53, 2.35) * mm, "end": v(0.52, 2.35) * mm});
            skLineSegment(sketch, "E361", {"start": v(0.52, 2.35) * mm, "end": v(0.5, 2.35) * mm});
            skLineSegment(sketch, "E362", {"start": v(0.5, 2.35) * mm, "end": v(0.49, 2.35) * mm});
            skLineSegment(sketch, "E363", {"start": v(0.49, 2.35) * mm, "end": v(0.47, 2.35) * mm});
            skLineSegment(sketch, "E364", {"start": v(0.47, 2.35) * mm, "end": v(0.46, 2.35) * mm});
            skLineSegment(sketch, "E365", {"start": v(0.46, 2.35) * mm, "end": v(0.44, 2.35) * mm});
            skLineSegment(sketch, "E366", {"start": v(0.44, 2.35) * mm, "end": v(0.42, 2.35) * mm});
            skLineSegment(sketch, "E367", {"start": v(0.42, 2.35) * mm, "end": v(0.4, 2.35) * mm});
            skLineSegment(sketch, "E368", {"start": v(0.4, 2.35) * mm, "end": v(0.38, 2.35) * mm});
            skLineSegment(sketch, "E369", {"start": v(0.38, 2.35) * mm, "end": v(0.36, 2.35) * mm});
            skLineSegment(sketch, "E370", {"start": v(0.36, 2.35) * mm, "end": v(0.34, 2.35) * mm});
            skLineSegment(sketch, "E371", {"start": v(0.34, 2.35) * mm, "end": v(0.32, 2.35) * mm});
            skLineSegment(sketch, "E372", {"start": v(0.32, 2.35) * mm, "end": v(0.3, 2.35) * mm});
            skLineSegment(sketch, "E373", {"start": v(0.3, 2.35) * mm, "end": v(0.27, 2.35) * mm});
            skLineSegment(sketch, "E374", {"start": v(0.27, 2.35) * mm, "end": v(0.25, 2.35) * mm});
            skLineSegment(sketch, "E375", {"start": v(0.25, 2.35) * mm, "end": v(0.22, 2.35) * mm});
            skLineSegment(sketch, "E376", {"start": v(0.22, 2.35) * mm, "end": v(0.2, 2.35) * mm});
            skLineSegment(sketch, "E377", {"start": v(0.2, 2.35) * mm, "end": v(0.17, 2.35) * mm});
            skLineSegment(sketch, "E378", {"start": v(0.17, 2.35) * mm, "end": v(0.15, 2.35) * mm});
            skLineSegment(sketch, "E379", {"start": v(0.15, 2.35) * mm, "end": v(0.12, 2.35) * mm});
            skLineSegment(sketch, "E380", {"start": v(0.12, 2.35) * mm, "end": v(0.1, 2.35) * mm});
            skLineSegment(sketch, "E381", {"start": v(0.1, 2.35) * mm, "end": v(0.07, 2.35) * mm});
            skLineSegment(sketch, "E382", {"start": v(0.07, 2.35) * mm, "end": v(0.05, 2.35) * mm});
            skLineSegment(sketch, "E383", {"start": v(0.05, 2.35) * mm, "end": v(0.03, 2.35) * mm});
            skLineSegment(sketch, "E384", {"start": v(0.03, 2.35) * mm, "end": v(0, 2.35) * mm});
            skLineSegment(sketch, "E385", {"start": v(0, 2.35) * mm, "end": v(-0.02, 2.35) * mm});
            skLineSegment(sketch, "E386", {"start": v(-0.02, 2.35) * mm, "end": v(-0.04, 2.35) * mm});
            skLineSegment(sketch, "E387", {"start": v(-0.04, 2.35) * mm, "end": v(-0.07, 2.35) * mm});
            skLineSegment(sketch, "E388", {"start": v(-0.07, 2.35) * mm, "end": v(-0.09, 2.35) * mm});
            skLineSegment(sketch, "E389", {"start": v(-0.09, 2.35) * mm, "end": v(-0.1, 2.35) * mm});
            skLineSegment(sketch, "E390", {"start": v(-0.1, 2.35) * mm, "end": v(-0.13, 2.35) * mm});
            skLineSegment(sketch, "E391", {"start": v(-0.13, 2.35) * mm, "end": v(-0.15, 2.35) * mm});
            skLineSegment(sketch, "E392", {"start": v(-0.15, 2.35) * mm, "end": v(-0.16, 2.35) * mm});
            skLineSegment(sketch, "E393", {"start": v(-0.16, 2.35) * mm, "end": v(-0.18, 2.35) * mm});
            skLineSegment(sketch, "E394", {"start": v(-0.18, 2.35) * mm, "end": v(-0.2, 2.35) * mm});
            skLineSegment(sketch, "E395", {"start": v(-0.2, 2.35) * mm, "end": v(-0.2, 2.35) * mm});
            skLineSegment(sketch, "E396", {"start": v(-0.2, 2.35) * mm, "end": v(-0.22, 2.35) * mm});
            skLineSegment(sketch, "E397", {"start": v(-0.22, 2.35) * mm, "end": v(-0.23, 2.35) * mm});
            skLineSegment(sketch, "E398", {"start": v(-0.23, 2.35) * mm, "end": v(-0.24, 2.35) * mm});
            skLineSegment(sketch, "E399", {"start": v(-0.24, 2.35) * mm, "end": v(-0.25, 2.35) * mm});
            skLineSegment(sketch, "E400", {"start": v(-0.25, 2.35) * mm, "end": v(-0.26, 2.35) * mm});
            skLineSegment(sketch, "E401", {"start": v(-0.26, 2.35) * mm, "end": v(-0.26, 2.35) * mm});
            skLineSegment(sketch, "E402", {"start": v(-0.26, 2.35) * mm, "end": v(-0.27, 2.35) * mm});
            skLineSegment(sketch, "E403", {"start": v(-0.27, 2.35) * mm, "end": v(-0.28, 2.35) * mm});
            skLineSegment(sketch, "E404", {"start": v(-0.28, 2.35) * mm, "end": v(-0.28, 2.35) * mm});
            skLineSegment(sketch, "E405", {"start": v(-0.28, 2.35) * mm, "end": v(-0.3, 2.34) * mm});
            skLineSegment(sketch, "E406", {"start": v(-0.3, 2.34) * mm, "end": v(-0.3, 2.34) * mm});
            skLineSegment(sketch, "E407", {"start": v(-0.3, 2.34) * mm, "end": v(-0.31, 2.34) * mm});
            skLineSegment(sketch, "E408", {"start": v(-0.31, 2.34) * mm, "end": v(-0.32, 2.34) * mm});
            skLineSegment(sketch, "E409", {"start": v(-0.32, 2.34) * mm, "end": v(-0.33, 2.34) * mm});
            skLineSegment(sketch, "E410", {"start": v(-0.33, 2.34) * mm, "end": v(-0.34, 2.34) * mm});
            skLineSegment(sketch, "E411", {"start": v(-0.34, 2.34) * mm, "end": v(-0.35, 2.33) * mm});
            skLineSegment(sketch, "E412", {"start": v(-0.35, 2.33) * mm, "end": v(-0.35, 2.33) * mm});
            skLineSegment(sketch, "E413", {"start": v(-0.35, 2.33) * mm, "end": v(-0.36, 2.33) * mm});
            skLineSegment(sketch, "E414", {"start": v(-0.36, 2.33) * mm, "end": v(-0.37, 2.33) * mm});
            skLineSegment(sketch, "E415", {"start": v(-0.37, 2.33) * mm, "end": v(-0.38, 2.32) * mm});
            skLineSegment(sketch, "E416", {"start": v(-0.38, 2.32) * mm, "end": v(-0.38, 2.32) * mm});
            skLineSegment(sketch, "E417", {"start": v(-0.38, 2.32) * mm, "end": v(-0.39, 2.32) * mm});
            skLineSegment(sketch, "E418", {"start": v(-0.39, 2.32) * mm, "end": v(-0.4, 2.31) * mm});
            skLineSegment(sketch, "E419", {"start": v(-0.4, 2.31) * mm, "end": v(-0.4, 2.3) * mm});
            skLineSegment(sketch, "E420", {"start": v(-0.4, 2.3) * mm, "end": v(-0.4, 2.3) * mm});
            skLineSegment(sketch, "E421", {"start": v(-0.4, 2.3) * mm, "end": v(-0.41, 2.3) * mm});
            skLineSegment(sketch, "E422", {"start": v(-0.41, 2.3) * mm, "end": v(-0.42, 2.3) * mm});
            skLineSegment(sketch, "E423", {"start": v(-0.42, 2.3) * mm, "end": v(-0.43, 2.3) * mm});
            skLineSegment(sketch, "E424", {"start": v(-0.43, 2.3) * mm, "end": v(-0.43, 2.29) * mm});
            skLineSegment(sketch, "E425", {"start": v(-0.43, 2.29) * mm, "end": v(-0.44, 2.28) * mm});
            skLineSegment(sketch, "E426", {"start": v(-0.44, 2.28) * mm, "end": v(-0.44, 2.28) * mm});
            skLineSegment(sketch, "E427", {"start": v(-0.44, 2.28) * mm, "end": v(-0.45, 2.27) * mm});
            skLineSegment(sketch, "E428", {"start": v(-0.45, 2.27) * mm, "end": v(-0.45, 2.27) * mm});
            skLineSegment(sketch, "E429", {"start": v(-0.45, 2.27) * mm, "end": v(-0.46, 2.26) * mm});
            skLineSegment(sketch, "E430", {"start": v(-0.46, 2.26) * mm, "end": v(-0.46, 2.26) * mm});
            skLineSegment(sketch, "E431", {"start": v(-0.46, 2.26) * mm, "end": v(-0.47, 2.25) * mm});
            skLineSegment(sketch, "E432", {"start": v(-0.47, 2.25) * mm, "end": v(-0.47, 2.24) * mm});
            skLineSegment(sketch, "E433", {"start": v(-0.47, 2.24) * mm, "end": v(-0.47, 2.24) * mm});
            skLineSegment(sketch, "E434", {"start": v(-0.47, 2.24) * mm, "end": v(-0.48, 2.23) * mm});
            skLineSegment(sketch, "E435", {"start": v(-0.48, 2.23) * mm, "end": v(-0.48, 2.23) * mm});
            skLineSegment(sketch, "E436", {"start": v(-0.48, 2.23) * mm, "end": v(-0.49, 2.22) * mm});
            skLineSegment(sketch, "E437", {"start": v(-0.49, 2.22) * mm, "end": v(-0.49, 2.21) * mm});
            skLineSegment(sketch, "E438", {"start": v(-0.49, 2.21) * mm, "end": v(-0.5, 2.2) * mm});
            skLineSegment(sketch, "E439", {"start": v(-0.5, 2.2) * mm, "end": v(-0.5, 2.2) * mm});
            skLineSegment(sketch, "E440", {"start": v(-0.5, 2.2) * mm, "end": v(-0.5, 2.19) * mm});
            skLineSegment(sketch, "E441", {"start": v(-0.5, 2.19) * mm, "end": v(-0.5, 2.18) * mm});
            skLineSegment(sketch, "E442", {"start": v(-0.5, 2.18) * mm, "end": v(-0.5, 2.17) * mm});
            skLineSegment(sketch, "E443", {"start": v(-0.5, 2.17) * mm, "end": v(-0.5, 2.17) * mm});
            skLineSegment(sketch, "E444", {"start": v(-0.5, 2.17) * mm, "end": v(-0.51, 2.16) * mm});
            skLineSegment(sketch, "E445", {"start": v(-0.51, 2.16) * mm, "end": v(-0.51, 2.15) * mm});
            skLineSegment(sketch, "E446", {"start": v(-0.51, 2.15) * mm, "end": v(-0.52, 2.15) * mm});
            skLineSegment(sketch, "E447", {"start": v(-0.52, 2.15) * mm, "end": v(-0.52, 2.14) * mm});
            skLineSegment(sketch, "E448", {"start": v(-0.52, 2.14) * mm, "end": v(-0.52, 2.13) * mm});
            skLineSegment(sketch, "E449", {"start": v(-0.52, 2.13) * mm, "end": v(-0.52, 2.12) * mm});
            skLineSegment(sketch, "E450", {"start": v(-0.52, 2.12) * mm, "end": v(-0.52, 2.12) * mm});
            skLineSegment(sketch, "E451", {"start": v(-0.52, 2.12) * mm, "end": v(-0.52, 2.11) * mm});
            skLineSegment(sketch, "E452", {"start": v(-0.52, 2.11) * mm, "end": v(-0.52, 2.1) * mm});
            skLineSegment(sketch, "E453", {"start": v(-0.52, 2.1) * mm, "end": v(-0.52, 2.1) * mm});
            skLineSegment(sketch, "E454", {"start": v(-0.52, 2.1) * mm, "end": v(-0.52, 2.08) * mm});
            skLineSegment(sketch, "E455", {"start": v(-0.52, 2.08) * mm, "end": v(-0.52, 2.08) * mm});
            skLineSegment(sketch, "E456", {"start": v(-0.52, 2.08) * mm, "end": v(-0.52, 2.07) * mm});
            skLineSegment(sketch, "E457", {"start": v(-0.52, 2.07) * mm, "end": v(-0.51, 2.06) * mm});
            skLineSegment(sketch, "E458", {"start": v(-0.51, 2.06) * mm, "end": v(-0.51, 2.05) * mm});
            skLineSegment(sketch, "E459", {"start": v(-0.51, 2.05) * mm, "end": v(-0.5, 2.04) * mm});
            skLineSegment(sketch, "E460", {"start": v(-0.5, 2.04) * mm, "end": v(-0.5, 2.04) * mm});
            skLineSegment(sketch, "E461", {"start": v(-0.5, 2.04) * mm, "end": v(-0.5, 2.03) * mm});
            skLineSegment(sketch, "E462", {"start": v(-0.5, 2.03) * mm, "end": v(-0.5, 2.02) * mm});
            skLineSegment(sketch, "E463", {"start": v(-0.5, 2.02) * mm, "end": v(-0.5, 2.01) * mm});
            skLineSegment(sketch, "E464", {"start": v(-0.5, 2.01) * mm, "end": v(-0.5, 2) * mm});
            skLineSegment(sketch, "E465", {"start": v(-0.5, 2) * mm, "end": v(-0.5, 2) * mm});
            skLineSegment(sketch, "E466", {"start": v(-0.5, 2) * mm, "end": v(-0.49, 2) * mm});
            skLineSegment(sketch, "E467", {"start": v(-0.49, 2) * mm, "end": v(-0.49, 1.98) * mm});
            skLineSegment(sketch, "E468", {"start": v(-0.49, 1.98) * mm, "end": v(-0.48, 1.98) * mm});
            skLineSegment(sketch, "E469", {"start": v(-0.48, 1.98) * mm, "end": v(-0.48, 1.97) * mm});
            skLineSegment(sketch, "E470", {"start": v(-0.48, 1.97) * mm, "end": v(-0.47, 1.96) * mm});
            skLineSegment(sketch, "E471", {"start": v(-0.47, 1.96) * mm, "end": v(-0.47, 1.96) * mm});
            skLineSegment(sketch, "E472", {"start": v(-0.47, 1.96) * mm, "end": v(-0.47, 1.95) * mm});
            skLineSegment(sketch, "E473", {"start": v(-0.47, 1.95) * mm, "end": v(-0.46, 1.95) * mm});
            skLineSegment(sketch, "E474", {"start": v(-0.46, 1.95) * mm, "end": v(-0.46, 1.94) * mm});
            skLineSegment(sketch, "E475", {"start": v(-0.46, 1.94) * mm, "end": v(-0.45, 1.93) * mm});
            skLineSegment(sketch, "E476", {"start": v(-0.45, 1.93) * mm, "end": v(-0.45, 1.93) * mm});
            skLineSegment(sketch, "E477", {"start": v(-0.45, 1.93) * mm, "end": v(-0.44, 1.92) * mm});
            skLineSegment(sketch, "E478", {"start": v(-0.44, 1.92) * mm, "end": v(-0.44, 1.92) * mm});
            skLineSegment(sketch, "E479", {"start": v(-0.44, 1.92) * mm, "end": v(-0.43, 1.91) * mm});
            skLineSegment(sketch, "E480", {"start": v(-0.43, 1.91) * mm, "end": v(-0.43, 1.9) * mm});
            skLineSegment(sketch, "E481", {"start": v(-0.43, 1.9) * mm, "end": v(-0.42, 1.9) * mm});
            skLineSegment(sketch, "E482", {"start": v(-0.42, 1.9) * mm, "end": v(-0.41, 1.9) * mm});
            skLineSegment(sketch, "E483", {"start": v(-0.41, 1.9) * mm, "end": v(-0.4, 1.9) * mm});
            skLineSegment(sketch, "E484", {"start": v(-0.4, 1.9) * mm, "end": v(-0.4, 1.89) * mm});
            skLineSegment(sketch, "E485", {"start": v(-0.4, 1.89) * mm, "end": v(-0.4, 1.88) * mm});
            skLineSegment(sketch, "E486", {"start": v(-0.4, 1.88) * mm, "end": v(-0.39, 1.88) * mm});
            skLineSegment(sketch, "E487", {"start": v(-0.39, 1.88) * mm, "end": v(-0.38, 1.88) * mm});
            skLineSegment(sketch, "E488", {"start": v(-0.38, 1.88) * mm, "end": v(-0.38, 1.87) * mm});
            skLineSegment(sketch, "E489", {"start": v(-0.38, 1.87) * mm, "end": v(-0.37, 1.87) * mm});
            skLineSegment(sketch, "E490", {"start": v(-0.37, 1.87) * mm, "end": v(-0.36, 1.87) * mm});
            skLineSegment(sketch, "E491", {"start": v(-0.36, 1.87) * mm, "end": v(-0.35, 1.86) * mm});
            skLineSegment(sketch, "E492", {"start": v(-0.35, 1.86) * mm, "end": v(-0.35, 1.86) * mm});
            skLineSegment(sketch, "E493", {"start": v(-0.35, 1.86) * mm, "end": v(-0.34, 1.86) * mm});
            skLineSegment(sketch, "E494", {"start": v(-0.34, 1.86) * mm, "end": v(-0.33, 1.86) * mm});
            skLineSegment(sketch, "E495", {"start": v(-0.33, 1.86) * mm, "end": v(-0.32, 1.86) * mm});
            skLineSegment(sketch, "E496", {"start": v(-0.32, 1.86) * mm, "end": v(-0.31, 1.85) * mm});
            skLineSegment(sketch, "E497", {"start": v(-0.31, 1.85) * mm, "end": v(-0.3, 1.85) * mm});
            skLineSegment(sketch, "E498", {"start": v(-0.3, 1.85) * mm, "end": v(-0.3, 1.85) * mm});
            skLineSegment(sketch, "E499", {"start": v(-0.3, 1.85) * mm, "end": v(-0.28, 1.85) * mm});
            skLineSegment(sketch, "E500", {"start": v(-0.28, 1.85) * mm, "end": v(-0.28, 1.85) * mm});
            skLineSegment(sketch, "E501", {"start": v(-0.28, 1.85) * mm, "end": v(-0.27, 1.85) * mm});
            skLineSegment(sketch, "E502", {"start": v(-0.27, 1.85) * mm, "end": v(-0.26, 1.85) * mm});
            skLineSegment(sketch, "E503", {"start": v(-0.26, 1.85) * mm, "end": v(-0.26, 1.85) * mm});
            skLineSegment(sketch, "E504", {"start": v(-0.26, 1.85) * mm, "end": v(-0.25, 1.85) * mm});
            skLineSegment(sketch, "E505", {"start": v(-0.25, 1.85) * mm, "end": v(-0.24, 1.85) * mm});
            skLineSegment(sketch, "E506", {"start": v(-0.24, 1.85) * mm, "end": v(-0.23, 1.85) * mm});
            skLineSegment(sketch, "E507", {"start": v(-0.23, 1.85) * mm, "end": v(-0.22, 1.85) * mm});
            skLineSegment(sketch, "E508", {"start": v(-0.22, 1.85) * mm, "end": v(-0.2, 1.85) * mm});
            skLineSegment(sketch, "E509", {"start": v(-0.2, 1.85) * mm, "end": v(-0.2, 1.85) * mm});
            skLineSegment(sketch, "E510", {"start": v(-0.2, 1.85) * mm, "end": v(-0.18, 1.85) * mm});
            skLineSegment(sketch, "E511", {"start": v(-0.18, 1.85) * mm, "end": v(-0.16, 1.85) * mm});
            skLineSegment(sketch, "E512", {"start": v(-0.16, 1.85) * mm, "end": v(-0.15, 1.85) * mm});
            skLineSegment(sketch, "E513", {"start": v(-0.15, 1.85) * mm, "end": v(-0.13, 1.85) * mm});
            skLineSegment(sketch, "E514", {"start": v(-0.13, 1.85) * mm, "end": v(-0.1, 1.85) * mm});
            skLineSegment(sketch, "E515", {"start": v(-0.1, 1.85) * mm, "end": v(-0.09, 1.85) * mm});
            skLineSegment(sketch, "E516", {"start": v(-0.09, 1.85) * mm, "end": v(-0.07, 1.85) * mm});
            skLineSegment(sketch, "E517", {"start": v(-0.07, 1.85) * mm, "end": v(-0.04, 1.85) * mm});
            skLineSegment(sketch, "E518", {"start": v(-0.04, 1.85) * mm, "end": v(-0.02, 1.85) * mm});
            skLineSegment(sketch, "E519", {"start": v(-0.02, 1.85) * mm, "end": v(0, 1.85) * mm});
            skLineSegment(sketch, "E520", {"start": v(0, 1.85) * mm, "end": v(0.03, 1.85) * mm});
            skLineSegment(sketch, "E521", {"start": v(0.03, 1.85) * mm, "end": v(0.05, 1.85) * mm});
            skLineSegment(sketch, "E522", {"start": v(0.05, 1.85) * mm, "end": v(0.07, 1.85) * mm});
            skLineSegment(sketch, "E523", {"start": v(0.07, 1.85) * mm, "end": v(0.1, 1.85) * mm});
            skLineSegment(sketch, "E524", {"start": v(0.1, 1.85) * mm, "end": v(0.12, 1.85) * mm});
            skLineSegment(sketch, "E525", {"start": v(0.12, 1.85) * mm, "end": v(0.15, 1.85) * mm});
            skLineSegment(sketch, "E526", {"start": v(0.15, 1.85) * mm, "end": v(0.17, 1.85) * mm});
            skLineSegment(sketch, "E527", {"start": v(0.17, 1.85) * mm, "end": v(0.2, 1.85) * mm});
            skLineSegment(sketch, "E528", {"start": v(0.2, 1.85) * mm, "end": v(0.22, 1.85) * mm});
            skLineSegment(sketch, "E529", {"start": v(0.22, 1.85) * mm, "end": v(0.25, 1.85) * mm});
            skLineSegment(sketch, "E530", {"start": v(0.25, 1.85) * mm, "end": v(0.27, 1.85) * mm});
            skLineSegment(sketch, "E531", {"start": v(0.27, 1.85) * mm, "end": v(0.3, 1.85) * mm});
            skLineSegment(sketch, "E532", {"start": v(0.3, 1.85) * mm, "end": v(0.32, 1.85) * mm});
            skLineSegment(sketch, "E533", {"start": v(0.32, 1.85) * mm, "end": v(0.34, 1.85) * mm});
            skLineSegment(sketch, "E534", {"start": v(0.34, 1.85) * mm, "end": v(0.36, 1.85) * mm});
            skLineSegment(sketch, "E535", {"start": v(0.36, 1.85) * mm, "end": v(0.38, 1.85) * mm});
            skLineSegment(sketch, "E536", {"start": v(0.38, 1.85) * mm, "end": v(0.4, 1.85) * mm});
            skLineSegment(sketch, "E537", {"start": v(0.4, 1.85) * mm, "end": v(0.42, 1.85) * mm});
            skLineSegment(sketch, "E538", {"start": v(0.42, 1.85) * mm, "end": v(0.44, 1.85) * mm});
            skLineSegment(sketch, "E539", {"start": v(0.44, 1.85) * mm, "end": v(0.46, 1.85) * mm});
            skLineSegment(sketch, "E540", {"start": v(0.46, 1.85) * mm, "end": v(0.47, 1.85) * mm});
            skLineSegment(sketch, "E541", {"start": v(0.47, 1.85) * mm, "end": v(0.49, 1.85) * mm});
            skLineSegment(sketch, "E542", {"start": v(0.49, 1.85) * mm, "end": v(0.5, 1.85) * mm});
            skLineSegment(sketch, "E543", {"start": v(0.5, 1.85) * mm, "end": v(0.52, 1.85) * mm});
            skLineSegment(sketch, "E544", {"start": v(0.52, 1.85) * mm, "end": v(0.53, 1.85) * mm});
            skLineSegment(sketch, "E545", {"start": v(0.53, 1.85) * mm, "end": v(0.54, 1.85) * mm});
            skLineSegment(sketch, "E546", {"start": v(0.54, 1.85) * mm, "end": v(0.54, 1.85) * mm});
            skLineSegment(sketch, "E547", {"start": v(0.54, 1.85) * mm, "end": v(0.55, 1.85) * mm});
            skLineSegment(sketch, "E548", {"start": v(0.55, 1.85) * mm, "end": v(0.56, 1.85) * mm});
            skLineSegment(sketch, "E549", {"start": v(0.56, 1.85) * mm, "end": v(0.56, 1.85) * mm});
            skLineSegment(sketch, "E550", {"start": v(0.56, 1.85) * mm, "end": v(0.58, 1.85) * mm});
            skLineSegment(sketch, "E551", {"start": v(0.58, 1.85) * mm, "end": v(0.6, 1.85) * mm});
            skLineSegment(sketch, "E552", {"start": v(0.6, 1.85) * mm, "end": v(0.62, 1.85) * mm});
            skLineSegment(sketch, "E553", {"start": v(0.62, 1.85) * mm, "end": v(0.64, 1.85) * mm});
            skLineSegment(sketch, "E554", {"start": v(0.64, 1.85) * mm, "end": v(0.66, 1.84) * mm});
            skLineSegment(sketch, "E555", {"start": v(0.66, 1.84) * mm, "end": v(0.68, 1.84) * mm});
            skLineSegment(sketch, "E556", {"start": v(0.68, 1.84) * mm, "end": v(0.7, 1.83) * mm});
            skLineSegment(sketch, "E557", {"start": v(0.7, 1.83) * mm, "end": v(0.72, 1.83) * mm});
            skLineSegment(sketch, "E558", {"start": v(0.72, 1.83) * mm, "end": v(0.74, 1.82) * mm});
            skLineSegment(sketch, "E559", {"start": v(0.74, 1.82) * mm, "end": v(0.76, 1.82) * mm});
            skLineSegment(sketch, "E560", {"start": v(0.76, 1.82) * mm, "end": v(0.78, 1.8) * mm});
            skLineSegment(sketch, "E561", {"start": v(0.78, 1.8) * mm, "end": v(0.8, 1.8) * mm});
            skLineSegment(sketch, "E562", {"start": v(0.8, 1.8) * mm, "end": v(0.82, 1.8) * mm});
            skLineSegment(sketch, "E563", {"start": v(0.82, 1.8) * mm, "end": v(0.84, 1.78) * mm});
            skLineSegment(sketch, "E564", {"start": v(0.84, 1.78) * mm, "end": v(0.86, 1.77) * mm});
            skLineSegment(sketch, "E565", {"start": v(0.86, 1.77) * mm, "end": v(0.88, 1.76) * mm});
            skLineSegment(sketch, "E566", {"start": v(0.88, 1.76) * mm, "end": v(0.9, 1.75) * mm});
            skLineSegment(sketch, "E567", {"start": v(0.9, 1.75) * mm, "end": v(0.91, 1.74) * mm});
            skLineSegment(sketch, "E568", {"start": v(0.91, 1.74) * mm, "end": v(0.93, 1.73) * mm});
            skLineSegment(sketch, "E569", {"start": v(0.93, 1.73) * mm, "end": v(0.94, 1.72) * mm});
            skLineSegment(sketch, "E570", {"start": v(0.94, 1.72) * mm, "end": v(0.96, 1.7) * mm});
            skLineSegment(sketch, "E571", {"start": v(0.96, 1.7) * mm, "end": v(0.98, 1.7) * mm});
            skLineSegment(sketch, "E572", {"start": v(0.98, 1.7) * mm, "end": v(1, 1.68) * mm});
            skLineSegment(sketch, "E573", {"start": v(1, 1.68) * mm, "end": v(1, 1.67) * mm});
            skLineSegment(sketch, "E574", {"start": v(1, 1.67) * mm, "end": v(1.02, 1.65) * mm});
            skLineSegment(sketch, "E575", {"start": v(1.02, 1.65) * mm, "end": v(1.04, 1.64) * mm});
            skLineSegment(sketch, "E576", {"start": v(1.04, 1.64) * mm, "end": v(1.05, 1.62) * mm});
            skLineSegment(sketch, "E577", {"start": v(1.05, 1.62) * mm, "end": v(1.06, 1.6) * mm});
            skLineSegment(sketch, "E578", {"start": v(1.06, 1.6) * mm, "end": v(1.08, 1.59) * mm});
            skLineSegment(sketch, "E579", {"start": v(1.08, 1.59) * mm, "end": v(1.09, 1.57) * mm});
            skLineSegment(sketch, "E580", {"start": v(1.09, 1.57) * mm, "end": v(1.1, 1.55) * mm});
            skLineSegment(sketch, "E581", {"start": v(1.1, 1.55) * mm, "end": v(1.11, 1.54) * mm});
            skLineSegment(sketch, "E582", {"start": v(1.11, 1.54) * mm, "end": v(1.12, 1.52) * mm});
            skLineSegment(sketch, "E583", {"start": v(1.12, 1.52) * mm, "end": v(1.13, 1.5) * mm});
            skLineSegment(sketch, "E584", {"start": v(1.13, 1.5) * mm, "end": v(1.14, 1.48) * mm});
            skLineSegment(sketch, "E585", {"start": v(1.14, 1.48) * mm, "end": v(1.15, 1.46) * mm});
            skLineSegment(sketch, "E586", {"start": v(1.15, 1.46) * mm, "end": v(1.16, 1.44) * mm});
            skLineSegment(sketch, "E587", {"start": v(1.16, 1.44) * mm, "end": v(1.17, 1.42) * mm});
            skLineSegment(sketch, "E588", {"start": v(1.17, 1.42) * mm, "end": v(1.18, 1.4) * mm});
            skLineSegment(sketch, "E589", {"start": v(1.18, 1.4) * mm, "end": v(1.18, 1.38) * mm});
            skLineSegment(sketch, "E590", {"start": v(1.18, 1.38) * mm, "end": v(1.2, 1.36) * mm});
            skLineSegment(sketch, "E591", {"start": v(1.2, 1.36) * mm, "end": v(1.2, 1.34) * mm});
            skLineSegment(sketch, "E592", {"start": v(1.2, 1.34) * mm, "end": v(1.2, 1.32) * mm});
            skLineSegment(sketch, "E593", {"start": v(1.2, 1.32) * mm, "end": v(1.2, 1.3) * mm});
            skLineSegment(sketch, "E594", {"start": v(1.2, 1.3) * mm, "end": v(1.21, 1.28) * mm});
            skLineSegment(sketch, "E595", {"start": v(1.21, 1.28) * mm, "end": v(1.21, 1.26) * mm});
            skLineSegment(sketch, "E596", {"start": v(1.21, 1.26) * mm, "end": v(1.22, 1.23) * mm});
            skLineSegment(sketch, "E597", {"start": v(1.22, 1.23) * mm, "end": v(1.22, 1.21) * mm});
            skLineSegment(sketch, "E598", {"start": v(1.22, 1.21) * mm, "end": v(1.22, 1.2) * mm});
            skLineSegment(sketch, "E599", {"start": v(1.22, 1.2) * mm, "end": v(1.22, 1.17) * mm});
            skLineSegment(sketch, "E600", {"start": v(1.22, 1.17) * mm, "end": v(1.22, 1.14) * mm});
            skLineSegment(sketch, "E601", {"start": v(1.22, 1.14) * mm, "end": v(1.22, 1.11) * mm});
            skLineSegment(sketch, "E602", {"start": v(1.22, 1.11) * mm, "end": v(1.21, 1.09) * mm});
            skLineSegment(sketch, "E603", {"start": v(1.21, 1.09) * mm, "end": v(1.21, 1.06) * mm});
            skLineSegment(sketch, "E604", {"start": v(1.21, 1.06) * mm, "end": v(1.2, 1.04) * mm});
            skLineSegment(sketch, "E605", {"start": v(1.2, 1.04) * mm, "end": v(1.2, 1.02) * mm});
            skLineSegment(sketch, "E606", {"start": v(1.2, 1.02) * mm, "end": v(1.2, 1) * mm});
            skLineSegment(sketch, "E607", {"start": v(1.2, 1) * mm, "end": v(1.19, 0.97) * mm});
            skLineSegment(sketch, "E608", {"start": v(1.19, 0.97) * mm, "end": v(1.18, 0.95) * mm});
            skLineSegment(sketch, "E609", {"start": v(1.18, 0.95) * mm, "end": v(1.17, 0.92) * mm});
            skLineSegment(sketch, "E610", {"start": v(1.17, 0.92) * mm, "end": v(1.17, 0.9) * mm});
            skLineSegment(sketch, "E611", {"start": v(1.17, 0.9) * mm, "end": v(1.16, 0.88) * mm});
            skLineSegment(sketch, "E612", {"start": v(1.16, 0.88) * mm, "end": v(1.14, 0.86) * mm});
            skLineSegment(sketch, "E613", {"start": v(1.14, 0.86) * mm, "end": v(1.13, 0.84) * mm});
            skLineSegment(sketch, "E614", {"start": v(1.13, 0.84) * mm, "end": v(1.12, 0.82) * mm});
            skLineSegment(sketch, "E615", {"start": v(1.12, 0.82) * mm, "end": v(1.1, 0.8) * mm});
            skLineSegment(sketch, "E616", {"start": v(1.1, 0.8) * mm, "end": v(1.1, 0.79) * mm});
            skLineSegment(sketch, "E617", {"start": v(1.1, 0.79) * mm, "end": v(1.08, 0.77) * mm});
            skLineSegment(sketch, "E618", {"start": v(1.08, 0.77) * mm, "end": v(1.07, 0.75) * mm});
            skLineSegment(sketch, "E619", {"start": v(1.07, 0.75) * mm, "end": v(1.05, 0.73) * mm});
            skLineSegment(sketch, "E620", {"start": v(1.05, 0.73) * mm, "end": v(1.04, 0.72) * mm});
            skLineSegment(sketch, "E621", {"start": v(1.04, 0.72) * mm, "end": v(1.02, 0.7) * mm});
            skLineSegment(sketch, "E622", {"start": v(1.02, 0.7) * mm, "end": v(1, 0.69) * mm});
            skLineSegment(sketch, "E623", {"start": v(1, 0.69) * mm, "end": v(0.99, 0.67) * mm});
            skLineSegment(sketch, "E624", {"start": v(0.99, 0.67) * mm, "end": v(0.97, 0.66) * mm});
            skLineSegment(sketch, "E625", {"start": v(0.97, 0.66) * mm, "end": v(0.95, 0.64) * mm});
            skLineSegment(sketch, "E626", {"start": v(0.95, 0.64) * mm, "end": v(0.93, 0.63) * mm});
            skLineSegment(sketch, "E627", {"start": v(0.93, 0.63) * mm, "end": v(0.91, 0.62) * mm});
            skLineSegment(sketch, "E628", {"start": v(0.91, 0.62) * mm, "end": v(0.9, 0.6) * mm});
            skLineSegment(sketch, "E629", {"start": v(0.9, 0.6) * mm, "end": v(0.87, 0.6) * mm});
            skLineSegment(sketch, "E630", {"start": v(0.87, 0.6) * mm, "end": v(0.85, 0.59) * mm});
            skLineSegment(sketch, "E631", {"start": v(0.85, 0.59) * mm, "end": v(0.83, 0.57) * mm});
            skLineSegment(sketch, "E632", {"start": v(0.83, 0.57) * mm, "end": v(0.81, 0.57) * mm});
            skLineSegment(sketch, "E633", {"start": v(0.81, 0.57) * mm, "end": v(0.79, 0.56) * mm});
            skLineSegment(sketch, "E634", {"start": v(0.79, 0.56) * mm, "end": v(0.77, 0.55) * mm});
            skLineSegment(sketch, "E635", {"start": v(0.77, 0.55) * mm, "end": v(0.75, 0.54) * mm});
            skLineSegment(sketch, "E636", {"start": v(0.75, 0.54) * mm, "end": v(0.72, 0.53) * mm});
            skLineSegment(sketch, "E637", {"start": v(0.72, 0.53) * mm, "end": v(0.7, 0.52) * mm});
            skLineSegment(sketch, "E638", {"start": v(0.7, 0.52) * mm, "end": v(0.68, 0.52) * mm});
            skLineSegment(sketch, "E639", {"start": v(0.68, 0.52) * mm, "end": v(0.66, 0.51) * mm});
            skLineSegment(sketch, "E640", {"start": v(0.66, 0.51) * mm, "end": v(0.63, 0.5) * mm});
            skLineSegment(sketch, "E641", {"start": v(0.63, 0.5) * mm, "end": v(0.6, 0.5) * mm});
            skLineSegment(sketch, "E642", {"start": v(0.6, 0.5) * mm, "end": v(0.59, 0.5) * mm});
            skLineSegment(sketch, "E643", {"start": v(0.59, 0.5) * mm, "end": v(0.56, 0.5) * mm});
            skLineSegment(sketch, "E644", {"start": v(0.56, 0.5) * mm, "end": v(0.54, 0.5) * mm});
            skLineSegment(sketch, "E645", {"start": v(0.54, 0.5) * mm, "end": v(0.51, 0.49) * mm});
            skLineSegment(sketch, "E646", {"start": v(0.51, 0.49) * mm, "end": v(0.5, 0.49) * mm});
            skLineSegment(sketch, "E647", {"start": v(0.5, 0.49) * mm, "end": v(0.47, 0.49) * mm});
            skLineSegment(sketch, "E648", {"start": v(0.47, 0.49) * mm, "end": v(0.44, 0.48) * mm});
            skLineSegment(sketch, "E649", {"start": v(0.44, 0.48) * mm, "end": v(0.42, 0.48) * mm});
            skLineSegment(sketch, "E650", {"start": v(0.42, 0.48) * mm, "end": v(0.42, 0.48) * mm});
            skLineSegment(sketch, "E651", {"start": v(0.42, 0.48) * mm, "end": v(0.41, 0.48) * mm});
            skLineSegment(sketch, "E652", {"start": v(0.41, 0.48) * mm, "end": v(0.4, 0.48) * mm});
            skLineSegment(sketch, "E653", {"start": v(0.4, 0.48) * mm, "end": v(0.4, 0.48) * mm});
            skLineSegment(sketch, "E654", {"start": v(0.4, 0.48) * mm, "end": v(0.38, 0.48) * mm});
            skLineSegment(sketch, "E655", {"start": v(0.38, 0.48) * mm, "end": v(0.37, 0.48) * mm});
            skLineSegment(sketch, "E656", {"start": v(0.37, 0.48) * mm, "end": v(0.36, 0.48) * mm});
            skLineSegment(sketch, "E657", {"start": v(0.36, 0.48) * mm, "end": v(0.35, 0.48) * mm});
            skLineSegment(sketch, "E658", {"start": v(0.35, 0.48) * mm, "end": v(0.34, 0.48) * mm});
            skLineSegment(sketch, "E659", {"start": v(0.34, 0.48) * mm, "end": v(0.33, 0.48) * mm});
            skLineSegment(sketch, "E660", {"start": v(0.33, 0.48) * mm, "end": v(0.32, 0.48) * mm});
            skLineSegment(sketch, "E661", {"start": v(0.32, 0.48) * mm, "end": v(0.3, 0.48) * mm});
            skLineSegment(sketch, "E662", {"start": v(0.3, 0.48) * mm, "end": v(0.3, 0.48) * mm});
            skLineSegment(sketch, "E663", {"start": v(0.3, 0.48) * mm, "end": v(0.28, 0.48) * mm});
            skLineSegment(sketch, "E664", {"start": v(0.28, 0.48) * mm, "end": v(0.26, 0.48) * mm});
            skLineSegment(sketch, "E665", {"start": v(0.26, 0.48) * mm, "end": v(0.25, 0.48) * mm});
            skLineSegment(sketch, "E666", {"start": v(0.25, 0.48) * mm, "end": v(0.24, 0.48) * mm});
            skLineSegment(sketch, "E667", {"start": v(0.24, 0.48) * mm, "end": v(0.22, 0.48) * mm});
            skLineSegment(sketch, "E668", {"start": v(0.22, 0.48) * mm, "end": v(0.2, 0.48) * mm});
            skLineSegment(sketch, "E669", {"start": v(0.2, 0.48) * mm, "end": v(0.19, 0.48) * mm});
            skLineSegment(sketch, "E670", {"start": v(0.19, 0.48) * mm, "end": v(0.17, 0.48) * mm});
            skLineSegment(sketch, "E671", {"start": v(0.17, 0.48) * mm, "end": v(0.16, 0.48) * mm});
            skLineSegment(sketch, "E672", {"start": v(0.16, 0.48) * mm, "end": v(0.14, 0.48) * mm});
            skLineSegment(sketch, "E673", {"start": v(0.14, 0.48) * mm, "end": v(0.13, 0.48) * mm});
            skLineSegment(sketch, "E674", {"start": v(0.13, 0.48) * mm, "end": v(0.11, 0.48) * mm});
            skLineSegment(sketch, "E675", {"start": v(0.11, 0.48) * mm, "end": v(0.1, 0.48) * mm});
            skLineSegment(sketch, "E676", {"start": v(0.1, 0.48) * mm, "end": v(0.08, 0.48) * mm});
            skLineSegment(sketch, "E677", {"start": v(0.08, 0.48) * mm, "end": v(0.07, 0.48) * mm});
            skLineSegment(sketch, "E678", {"start": v(0.07, 0.48) * mm, "end": v(0.05, 0.48) * mm});
            skLineSegment(sketch, "E679", {"start": v(0.05, 0.48) * mm, "end": v(0.04, 0.48) * mm});
            skLineSegment(sketch, "E680", {"start": v(0.04, 0.48) * mm, "end": v(0.02, 0.48) * mm});
            skLineSegment(sketch, "E681", {"start": v(0.02, 0.48) * mm, "end": v(0.01, 0.48) * mm});
            skLineSegment(sketch, "E682", {"start": v(0.01, 0.48) * mm, "end": v(0, 0.48) * mm});
            skLineSegment(sketch, "E683", {"start": v(0, 0.48) * mm, "end": v(-0.01, 0.48) * mm});
            skLineSegment(sketch, "E684", {"start": v(-0.01, 0.48) * mm, "end": v(-0.03, 0.48) * mm});
            skLineSegment(sketch, "E685", {"start": v(-0.03, 0.48) * mm, "end": v(-0.04, 0.48) * mm});
            skLineSegment(sketch, "E686", {"start": v(-0.04, 0.48) * mm, "end": v(-0.05, 0.48) * mm});
            skLineSegment(sketch, "E687", {"start": v(-0.05, 0.48) * mm, "end": v(-0.06, 0.48) * mm});
            skLineSegment(sketch, "E688", {"start": v(-0.06, 0.48) * mm, "end": v(-0.06, 0.48) * mm});
            skLineSegment(sketch, "E689", {"start": v(-0.06, 0.48) * mm, "end": v(-0.07, 0.48) * mm});
            skLineSegment(sketch, "E690", {"start": v(-0.07, 0.48) * mm, "end": v(-0.08, 0.48) * mm});
            skLineSegment(sketch, "E691", {"start": v(-0.08, 0.48) * mm, "end": v(-0.09, 0.48) * mm});
            skLineSegment(sketch, "E692", {"start": v(-0.09, 0.48) * mm, "end": v(-0.1, 0.48) * mm});
            skLineSegment(sketch, "E693", {"start": v(-0.1, 0.48) * mm, "end": v(-0.1, 0.48) * mm});
            skLineSegment(sketch, "E694", {"start": v(-0.1, 0.48) * mm, "end": v(-0.12, 0.48) * mm});
            skLineSegment(sketch, "E695", {"start": v(-0.12, 0.48) * mm, "end": v(-0.14, 0.48) * mm});
            skLineSegment(sketch, "E696", {"start": v(-0.14, 0.48) * mm, "end": v(-0.16, 0.48) * mm});
            skLineSegment(sketch, "E697", {"start": v(-0.16, 0.48) * mm, "end": v(-0.18, 0.48) * mm});
            skLineSegment(sketch, "E698", {"start": v(-0.18, 0.48) * mm, "end": v(-0.2, 0.48) * mm});
            skLineSegment(sketch, "E699", {"start": v(-0.2, 0.48) * mm, "end": v(-0.21, 0.48) * mm});
            skLineSegment(sketch, "E700", {"start": v(-0.21, 0.48) * mm, "end": v(-0.23, 0.48) * mm});
            skLineSegment(sketch, "E701", {"start": v(-0.23, 0.48) * mm, "end": v(-0.24, 0.48) * mm});
            skLineSegment(sketch, "E702", {"start": v(-0.24, 0.48) * mm, "end": v(-0.26, 0.47) * mm});
            skLineSegment(sketch, "E703", {"start": v(-0.26, 0.47) * mm, "end": v(-0.27, 0.47) * mm});
            skLineSegment(sketch, "E704", {"start": v(-0.27, 0.47) * mm, "end": v(-0.29, 0.47) * mm});
            skLineSegment(sketch, "E705", {"start": v(-0.29, 0.47) * mm, "end": v(-0.3, 0.47) * mm});
            skLineSegment(sketch, "E706", {"start": v(-0.3, 0.47) * mm, "end": v(-0.32, 0.46) * mm});
            skLineSegment(sketch, "E707", {"start": v(-0.32, 0.46) * mm, "end": v(-0.33, 0.46) * mm});
            skLineSegment(sketch, "E708", {"start": v(-0.33, 0.46) * mm, "end": v(-0.34, 0.46) * mm});
            skLineSegment(sketch, "E709", {"start": v(-0.34, 0.46) * mm, "end": v(-0.36, 0.45) * mm});
            skLineSegment(sketch, "E710", {"start": v(-0.36, 0.45) * mm, "end": v(-0.37, 0.45) * mm});
            skLineSegment(sketch, "E711", {"start": v(-0.37, 0.45) * mm, "end": v(-0.38, 0.44) * mm});
            skLineSegment(sketch, "E712", {"start": v(-0.38, 0.44) * mm, "end": v(-0.4, 0.44) * mm});
            skLineSegment(sketch, "E713", {"start": v(-0.4, 0.44) * mm, "end": v(-0.4, 0.43) * mm});
            skLineSegment(sketch, "E714", {"start": v(-0.4, 0.43) * mm, "end": v(-0.41, 0.43) * mm});
            skLineSegment(sketch, "E715", {"start": v(-0.41, 0.43) * mm, "end": v(-0.42, 0.42) * mm});
            skLineSegment(sketch, "E716", {"start": v(-0.42, 0.42) * mm, "end": v(-0.43, 0.42) * mm});
            skLineSegment(sketch, "E717", {"start": v(-0.43, 0.42) * mm, "end": v(-0.44, 0.41) * mm});
            skLineSegment(sketch, "E718", {"start": v(-0.44, 0.41) * mm, "end": v(-0.45, 0.4) * mm});
            skLineSegment(sketch, "E719", {"start": v(-0.45, 0.4) * mm, "end": v(-0.46, 0.4) * mm});
            skLineSegment(sketch, "E720", {"start": v(-0.46, 0.4) * mm, "end": v(-0.47, 0.4) * mm});
            skLineSegment(sketch, "E721", {"start": v(-0.47, 0.4) * mm, "end": v(-0.48, 0.4) * mm});
            skLineSegment(sketch, "E722", {"start": v(-0.48, 0.4) * mm, "end": v(-0.48, 0.38) * mm});
            skLineSegment(sketch, "E723", {"start": v(-0.48, 0.38) * mm, "end": v(-0.5, 0.38) * mm});
            skLineSegment(sketch, "E724", {"start": v(-0.5, 0.38) * mm, "end": v(-0.5, 0.37) * mm});
            skLineSegment(sketch, "E725", {"start": v(-0.5, 0.37) * mm, "end": v(-0.5, 0.36) * mm});
            skLineSegment(sketch, "E726", {"start": v(-0.5, 0.36) * mm, "end": v(-0.51, 0.36) * mm});
            skLineSegment(sketch, "E727", {"start": v(-0.51, 0.36) * mm, "end": v(-0.52, 0.35) * mm});
            skLineSegment(sketch, "E728", {"start": v(-0.52, 0.35) * mm, "end": v(-0.52, 0.34) * mm});
            skLineSegment(sketch, "E729", {"start": v(-0.52, 0.34) * mm, "end": v(-0.53, 0.34) * mm});
            skLineSegment(sketch, "E730", {"start": v(-0.53, 0.34) * mm, "end": v(-0.53, 0.33) * mm});
            skLineSegment(sketch, "E731", {"start": v(-0.53, 0.33) * mm, "end": v(-0.54, 0.32) * mm});
            skLineSegment(sketch, "E732", {"start": v(-0.54, 0.32) * mm, "end": v(-0.54, 0.31) * mm});
            skLineSegment(sketch, "E733", {"start": v(-0.54, 0.31) * mm, "end": v(-0.55, 0.3) * mm});
            skLineSegment(sketch, "E734", {"start": v(-0.55, 0.3) * mm, "end": v(-0.55, 0.3) * mm});
            skLineSegment(sketch, "E735", {"start": v(-0.55, 0.3) * mm, "end": v(-0.56, 0.28) * mm});
            skLineSegment(sketch, "E736", {"start": v(-0.56, 0.28) * mm, "end": v(-0.56, 0.27) * mm});
            skLineSegment(sketch, "E737", {"start": v(-0.56, 0.27) * mm, "end": v(-0.56, 0.27) * mm});
            skLineSegment(sketch, "E738", {"start": v(-0.56, 0.27) * mm, "end": v(-0.56, 0.26) * mm});
            skLineSegment(sketch, "E739", {"start": v(-0.56, 0.26) * mm, "end": v(-0.57, 0.25) * mm});
            skLineSegment(sketch, "E740", {"start": v(-0.57, 0.25) * mm, "end": v(-0.57, 0.24) * mm});
            skLineSegment(sketch, "E741", {"start": v(-0.57, 0.24) * mm, "end": v(-0.57, 0.23) * mm});
            skLineSegment(sketch, "E742", {"start": v(-0.57, 0.23) * mm, "end": v(-0.57, 0.23) * mm});
            skLineSegment(sketch, "E743", {"start": v(-0.57, 0.23) * mm, "end": v(-0.57, 0.22) * mm});
            skLineSegment(sketch, "E744", {"start": v(-0.57, 0.22) * mm, "end": v(-0.57, 0.21) * mm});
            skLineSegment(sketch, "E745", {"start": v(-0.57, 0.21) * mm, "end": v(-0.57, 0.2) * mm});
            skLineSegment(sketch, "E746", {"start": v(-0.57, 0.2) * mm, "end": v(-0.57, 0.2) * mm});
            skLineSegment(sketch, "E747", {"start": v(-0.57, 0.2) * mm, "end": v(-0.56, 0.2) * mm});
            skLineSegment(sketch, "E748", {"start": v(-0.56, 0.2) * mm, "end": v(-0.56, 0.2) * mm});
            skLineSegment(sketch, "E749", {"start": v(-0.56, 0.2) * mm, "end": v(-0.56, 0.19) * mm});
            skLineSegment(sketch, "E750", {"start": v(-0.56, 0.19) * mm, "end": v(-0.56, 0.18) * mm});
            skLineSegment(sketch, "E751", {"start": v(-0.56, 0.18) * mm, "end": v(-0.56, 0.17) * mm});
            skLineSegment(sketch, "E752", {"start": v(-0.56, 0.17) * mm, "end": v(-0.55, 0.17) * mm});
            skLineSegment(sketch, "E753", {"start": v(-0.55, 0.17) * mm, "end": v(-0.55, 0.16) * mm});
            skLineSegment(sketch, "E754", {"start": v(-0.55, 0.16) * mm, "end": v(-0.55, 0.16) * mm});
            skLineSegment(sketch, "E755", {"start": v(-0.55, 0.16) * mm, "end": v(-0.55, 0.15) * mm});
            skLineSegment(sketch, "E756", {"start": v(-0.55, 0.15) * mm, "end": v(-0.55, 0.15) * mm});
            skLineSegment(sketch, "E757", {"start": v(-0.55, 0.15) * mm, "end": v(-0.54, 0.14) * mm});
            skLineSegment(sketch, "E758", {"start": v(-0.54, 0.14) * mm, "end": v(-0.54, 0.13) * mm});
            skLineSegment(sketch, "E759", {"start": v(-0.54, 0.13) * mm, "end": v(-0.54, 0.13) * mm});
            skLineSegment(sketch, "E760", {"start": v(-0.54, 0.13) * mm, "end": v(-0.54, 0.12) * mm});
            skLineSegment(sketch, "E761", {"start": v(-0.54, 0.12) * mm, "end": v(-0.54, 0.12) * mm});
            skLineSegment(sketch, "E762", {"start": v(-0.54, 0.12) * mm, "end": v(-0.53, 0.11) * mm});
            skLineSegment(sketch, "E763", {"start": v(-0.53, 0.11) * mm, "end": v(-0.53, 0.1) * mm});
            skLineSegment(sketch, "E764", {"start": v(-0.53, 0.1) * mm, "end": v(-0.53, 0.1) * mm});
            skLineSegment(sketch, "E765", {"start": v(-0.53, 0.1) * mm, "end": v(-0.52, 0.09) * mm});
            skLineSegment(sketch, "E766", {"start": v(-0.52, 0.09) * mm, "end": v(-0.52, 0.08) * mm});
            skLineSegment(sketch, "E767", {"start": v(-0.52, 0.08) * mm, "end": v(-0.52, 0.08) * mm});
            skLineSegment(sketch, "E768", {"start": v(-0.52, 0.08) * mm, "end": v(-0.52, 0.07) * mm});
            skLineSegment(sketch, "E769", {"start": v(-0.52, 0.07) * mm, "end": v(-0.51, 0.07) * mm});
            skLineSegment(sketch, "E770", {"start": v(-0.51, 0.07) * mm, "end": v(-0.51, 0.06) * mm});
            skLineSegment(sketch, "E771", {"start": v(-0.51, 0.06) * mm, "end": v(-0.5, 0.06) * mm});
            skLineSegment(sketch, "E772", {"start": v(-0.5, 0.06) * mm, "end": v(-0.5, 0.05) * mm});
            skLineSegment(sketch, "E773", {"start": v(-0.5, 0.05) * mm, "end": v(-0.5, 0.04) * mm});
            skLineSegment(sketch, "E774", {"start": v(-0.5, 0.04) * mm, "end": v(-0.5, 0.04) * mm});
            skLineSegment(sketch, "E775", {"start": v(-0.5, 0.04) * mm, "end": v(-0.5, 0.03) * mm});
            skLineSegment(sketch, "E776", {"start": v(-0.5, 0.03) * mm, "end": v(-0.5, 0.03) * mm});
            skLineSegment(sketch, "E777", {"start": v(-0.5, 0.03) * mm, "end": v(-0.5, 0.02) * mm});
            skLineSegment(sketch, "E778", {"start": v(-0.5, 0.02) * mm, "end": v(-0.5, 0.02) * mm});
            skLineSegment(sketch, "E779", {"start": v(-0.5, 0.02) * mm, "end": v(-0.49, 0.01) * mm});
            skLineSegment(sketch, "E780", {"start": v(-0.49, 0.01) * mm, "end": v(-0.48, 0) * mm});
            skLineSegment(sketch, "E781", {"start": v(-0.48, 0) * mm, "end": v(-0.48, 0) * mm});
            skLineSegment(sketch, "E782", {"start": v(-0.48, 0) * mm, "end": v(-0.48, -0.01) * mm});
            skLineSegment(sketch, "E783", {"start": v(-0.48, -0.01) * mm, "end": v(-0.47, -0.02) * mm});
            skLineSegment(sketch, "E784", {"start": v(-0.47, -0.02) * mm, "end": v(-0.47, -0.02) * mm});
            skLineSegment(sketch, "E785", {"start": v(-0.47, -0.02) * mm, "end": v(-0.47, -0.03) * mm});
            skLineSegment(sketch, "E786", {"start": v(-0.47, -0.03) * mm, "end": v(-0.47, -0.03) * mm});
            skLineSegment(sketch, "E787", {"start": v(-0.47, -0.03) * mm, "end": v(-0.46, -0.04) * mm});
            skLineSegment(sketch, "E788", {"start": v(-0.46, -0.04) * mm, "end": v(-0.46, -0.05) * mm});
            skLineSegment(sketch, "E789", {"start": v(-0.46, -0.05) * mm, "end": v(-0.46, -0.05) * mm});
            skLineSegment(sketch, "E790", {"start": v(-0.46, -0.05) * mm, "end": v(-0.45, -0.06) * mm});
            skLineSegment(sketch, "E791", {"start": v(-0.45, -0.06) * mm, "end": v(-0.45, -0.06) * mm});
            skLineSegment(sketch, "E792", {"start": v(-0.45, -0.06) * mm, "end": v(-0.44, -0.07) * mm});
            skLineSegment(sketch, "E793", {"start": v(-0.44, -0.07) * mm, "end": v(-0.43, -0.09) * mm});
            skLineSegment(sketch, "E794", {"start": v(-0.43, -0.09) * mm, "end": v(-0.42, -0.11) * mm});
            skLineSegment(sketch, "E795", {"start": v(-0.42, -0.11) * mm, "end": v(-0.4, -0.14) * mm});
            skLineSegment(sketch, "E796", {"start": v(-0.4, -0.14) * mm, "end": v(-0.38, -0.17) * mm});
            skLineSegment(sketch, "E797", {"start": v(-0.38, -0.17) * mm, "end": v(-0.35, -0.21) * mm});
            skLineSegment(sketch, "E798", {"start": v(-0.35, -0.21) * mm, "end": v(-0.32, -0.26) * mm});
            skLineSegment(sketch, "E799", {"start": v(-0.32, -0.26) * mm, "end": v(-0.3, -0.3) * mm});
            skLineSegment(sketch, "E800", {"start": v(-0.3, -0.3) * mm, "end": v(-0.26, -0.36) * mm});
            skLineSegment(sketch, "E801", {"start": v(-0.26, -0.36) * mm, "end": v(-0.22, -0.42) * mm});
            skLineSegment(sketch, "E802", {"start": v(-0.22, -0.42) * mm, "end": v(-0.18, -0.48) * mm});
            skLineSegment(sketch, "E803", {"start": v(-0.18, -0.48) * mm, "end": v(-0.13, -0.54) * mm});
            skLineSegment(sketch, "E804", {"start": v(-0.13, -0.54) * mm, "end": v(-0.09, -0.61) * mm});
            skLineSegment(sketch, "E805", {"start": v(-0.09, -0.61) * mm, "end": v(-0.04, -0.68) * mm});
            skLineSegment(sketch, "E806", {"start": v(-0.04, -0.68) * mm, "end": v(0, -0.76) * mm});
            skLineSegment(sketch, "E807", {"start": v(0, -0.76) * mm, "end": v(0.06, -0.83) * mm});
            skLineSegment(sketch, "E808", {"start": v(0.06, -0.83) * mm, "end": v(0.11, -0.91) * mm});
            skLineSegment(sketch, "E809", {"start": v(0.11, -0.91) * mm, "end": v(0.16, -1) * mm});
            skLineSegment(sketch, "E810", {"start": v(0.16, -1) * mm, "end": v(0.22, -1.08) * mm});
            skLineSegment(sketch, "E811", {"start": v(0.22, -1.08) * mm, "end": v(0.27, -1.16) * mm});
            skLineSegment(sketch, "E812", {"start": v(0.27, -1.16) * mm, "end": v(0.33, -1.25) * mm});
            skLineSegment(sketch, "E813", {"start": v(0.33, -1.25) * mm, "end": v(0.39, -1.33) * mm});
            skLineSegment(sketch, "E814", {"start": v(0.39, -1.33) * mm, "end": v(0.44, -1.42) * mm});
            skLineSegment(sketch, "E815", {"start": v(0.44, -1.42) * mm, "end": v(0.5, -1.5) * mm});
            skLineSegment(sketch, "E816", {"start": v(0.5, -1.5) * mm, "end": v(0.56, -1.6) * mm});
            skLineSegment(sketch, "E817", {"start": v(0.56, -1.6) * mm, "end": v(0.61, -1.68) * mm});
            skLineSegment(sketch, "E818", {"start": v(0.61, -1.68) * mm, "end": v(0.67, -1.77) * mm});
            skLineSegment(sketch, "E819", {"start": v(0.67, -1.77) * mm, "end": v(0.73, -1.85) * mm});
            skLineSegment(sketch, "E820", {"start": v(0.73, -1.85) * mm, "end": v(0.78, -1.94) * mm});
            skLineSegment(sketch, "E821", {"start": v(0.78, -1.94) * mm, "end": v(0.84, -2.02) * mm});
            skLineSegment(sketch, "E822", {"start": v(0.84, -2.02) * mm, "end": v(0.9, -2.1) * mm});
            skLineSegment(sketch, "E823", {"start": v(0.9, -2.1) * mm, "end": v(0.94, -2.18) * mm});
            skLineSegment(sketch, "E824", {"start": v(0.94, -2.18) * mm, "end": v(1, -2.26) * mm});
            skLineSegment(sketch, "E825", {"start": v(1, -2.26) * mm, "end": v(1.04, -2.33) * mm});
            skLineSegment(sketch, "E826", {"start": v(1.04, -2.33) * mm, "end": v(1.09, -2.4) * mm});
            skLineSegment(sketch, "E827", {"start": v(1.09, -2.4) * mm, "end": v(1.13, -2.47) * mm});
            skLineSegment(sketch, "E828", {"start": v(1.13, -2.47) * mm, "end": v(1.18, -2.53) * mm});
            skLineSegment(sketch, "E829", {"start": v(1.18, -2.53) * mm, "end": v(1.22, -2.6) * mm});
            skLineSegment(sketch, "E830", {"start": v(1.22, -2.6) * mm, "end": v(1.26, -2.65) * mm});
            skLineSegment(sketch, "E831", {"start": v(1.26, -2.65) * mm, "end": v(1.3, -2.7) * mm});
            skLineSegment(sketch, "E832", {"start": v(1.3, -2.7) * mm, "end": v(1.32, -2.76) * mm});
            skLineSegment(sketch, "E833", {"start": v(1.32, -2.76) * mm, "end": v(1.35, -2.8) * mm});
            skLineSegment(sketch, "E834", {"start": v(1.35, -2.8) * mm, "end": v(1.38, -2.84) * mm});
            skLineSegment(sketch, "E835", {"start": v(1.38, -2.84) * mm, "end": v(1.4, -2.87) * mm});
            skLineSegment(sketch, "E836", {"start": v(1.4, -2.87) * mm, "end": v(1.42, -2.9) * mm});
            skLineSegment(sketch, "E837", {"start": v(1.42, -2.9) * mm, "end": v(1.43, -2.93) * mm});
            skLineSegment(sketch, "E838", {"start": v(1.43, -2.93) * mm, "end": v(1.45, -2.94) * mm});
            skLineSegment(sketch, "E839", {"start": v(1.45, -2.94) * mm, "end": v(1.45, -2.95) * mm});
            skLineSegment(sketch, "E840", {"start": v(1.45, -2.95) * mm, "end": v(1.45, -2.96) * mm});
            skLineSegment(sketch, "E841", {"start": v(1.45, -2.96) * mm, "end": v(1.46, -2.97) * mm});
            skLineSegment(sketch, "E842", {"start": v(1.46, -2.97) * mm, "end": v(1.47, -2.98) * mm});
            skLineSegment(sketch, "E843", {"start": v(1.47, -2.98) * mm, "end": v(1.48, -2.99) * mm});
            skLineSegment(sketch, "E844", {"start": v(1.48, -2.99) * mm, "end": v(1.48, -3) * mm});
            skLineSegment(sketch, "E845", {"start": v(1.48, -3) * mm, "end": v(1.5, -3) * mm});
            skLineSegment(sketch, "E846", {"start": v(1.5, -3) * mm, "end": v(1.5, -3.02) * mm});
            skLineSegment(sketch, "E847", {"start": v(1.5, -3.02) * mm, "end": v(1.5, -3.03) * mm});
            skLineSegment(sketch, "E848", {"start": v(1.5, -3.03) * mm, "end": v(1.52, -3.04) * mm});
            skLineSegment(sketch, "E849", {"start": v(1.52, -3.04) * mm, "end": v(1.53, -3.05) * mm});
            skLineSegment(sketch, "E850", {"start": v(1.53, -3.05) * mm, "end": v(1.54, -3.05) * mm});
            skLineSegment(sketch, "E851", {"start": v(1.54, -3.05) * mm, "end": v(1.55, -3.06) * mm});
            skLineSegment(sketch, "E852", {"start": v(1.55, -3.06) * mm, "end": v(1.55, -3.07) * mm});
            skLineSegment(sketch, "E853", {"start": v(1.55, -3.07) * mm, "end": v(1.56, -3.08) * mm});
            skLineSegment(sketch, "E854", {"start": v(1.56, -3.08) * mm, "end": v(1.57, -3.09) * mm});
            skLineSegment(sketch, "E855", {"start": v(1.57, -3.09) * mm, "end": v(1.58, -3.1) * mm});
            skLineSegment(sketch, "E856", {"start": v(1.58, -3.1) * mm, "end": v(1.6, -3.1) * mm});
            skLineSegment(sketch, "E857", {"start": v(1.6, -3.1) * mm, "end": v(1.6, -3.1) * mm});
            skLineSegment(sketch, "E858", {"start": v(1.6, -3.1) * mm, "end": v(1.62, -3.12) * mm});
            skLineSegment(sketch, "E859", {"start": v(1.62, -3.12) * mm, "end": v(1.63, -3.12) * mm});
            skLineSegment(sketch, "E860", {"start": v(1.63, -3.12) * mm, "end": v(1.64, -3.13) * mm});
            skLineSegment(sketch, "E861", {"start": v(1.64, -3.13) * mm, "end": v(1.65, -3.13) * mm});
            skLineSegment(sketch, "E862", {"start": v(1.65, -3.13) * mm, "end": v(1.66, -3.14) * mm});
            skLineSegment(sketch, "E863", {"start": v(1.66, -3.14) * mm, "end": v(1.67, -3.15) * mm});
            skLineSegment(sketch, "E864", {"start": v(1.67, -3.15) * mm, "end": v(1.68, -3.15) * mm});
            skLineSegment(sketch, "E865", {"start": v(1.68, -3.15) * mm, "end": v(1.7, -3.16) * mm});
            skLineSegment(sketch, "E866", {"start": v(1.7, -3.16) * mm, "end": v(1.7, -3.16) * mm});
            skLineSegment(sketch, "E867", {"start": v(1.7, -3.16) * mm, "end": v(1.72, -3.17) * mm});
            skLineSegment(sketch, "E868", {"start": v(1.72, -3.17) * mm, "end": v(1.73, -3.17) * mm});
            skLineSegment(sketch, "E869", {"start": v(1.73, -3.17) * mm, "end": v(1.74, -3.17) * mm});
            skLineSegment(sketch, "E870", {"start": v(1.74, -3.17) * mm, "end": v(1.75, -3.18) * mm});
            skLineSegment(sketch, "E871", {"start": v(1.75, -3.18) * mm, "end": v(1.77, -3.18) * mm});
            skLineSegment(sketch, "E872", {"start": v(1.77, -3.18) * mm, "end": v(1.78, -3.18) * mm});
            skLineSegment(sketch, "E873", {"start": v(1.78, -3.18) * mm, "end": v(1.8, -3.19) * mm});
            skLineSegment(sketch, "E874", {"start": v(1.8, -3.19) * mm, "end": v(1.8, -3.2) * mm});
            skLineSegment(sketch, "E875", {"start": v(1.8, -3.2) * mm, "end": v(1.82, -3.2) * mm});
            skLineSegment(sketch, "E876", {"start": v(1.82, -3.2) * mm, "end": v(1.83, -3.2) * mm});
            skLineSegment(sketch, "E877", {"start": v(1.83, -3.2) * mm, "end": v(1.84, -3.2) * mm});
            skLineSegment(sketch, "E878", {"start": v(1.84, -3.2) * mm, "end": v(1.86, -3.2) * mm});
            skLineSegment(sketch, "E879", {"start": v(1.86, -3.2) * mm, "end": v(1.87, -3.2) * mm});
            skLineSegment(sketch, "E880", {"start": v(1.87, -3.2) * mm, "end": v(1.88, -3.2) * mm});
            skLineSegment(sketch, "E881", {"start": v(1.88, -3.2) * mm, "end": v(1.9, -3.2) * mm});
            skLineSegment(sketch, "E882", {"start": v(1.9, -3.2) * mm, "end": v(1.9, -3.2) * mm});
            skLineSegment(sketch, "E883", {"start": v(1.9, -3.2) * mm, "end": v(1.92, -3.21) * mm});
            skLineSegment(sketch, "E884", {"start": v(1.92, -3.21) * mm, "end": v(1.94, -3.21) * mm});
            skLineSegment(sketch, "E885", {"start": v(1.94, -3.21) * mm, "end": v(1.95, -3.21) * mm});
            skLineSegment(sketch, "E886", {"start": v(1.95, -3.21) * mm, "end": v(1.96, -3.21) * mm});
            skLineSegment(sketch, "E887", {"start": v(1.96, -3.21) * mm, "end": v(1.98, -3.21) * mm});
            skLineSegment(sketch, "E888", {"start": v(1.98, -3.21) * mm, "end": v(2, -3.21) * mm});
            skLineSegment(sketch, "E889", {"start": v(2, -3.21) * mm, "end": v(2, -3.21) * mm});
            skLineSegment(sketch, "E890", {"start": v(2, -3.21) * mm, "end": v(2.02, -3.21) * mm});
            skLineSegment(sketch, "E891", {"start": v(2.02, -3.21) * mm, "end": v(2.04, -3.21) * mm});
            skLineSegment(sketch, "E892", {"start": v(2.04, -3.21) * mm, "end": v(2.06, -3.21) * mm});
            skLineSegment(sketch, "E893", {"start": v(2.06, -3.21) * mm, "end": v(2.08, -3.21) * mm});
            skLineSegment(sketch, "E894", {"start": v(2.08, -3.21) * mm, "end": v(2.1, -3.21) * mm});
            skLineSegment(sketch, "E895", {"start": v(2.1, -3.21) * mm, "end": v(2.13, -3.2) * mm});
            skLineSegment(sketch, "E896", {"start": v(2.13, -3.2) * mm, "end": v(2.15, -3.2) * mm});
            skLineSegment(sketch, "E897", {"start": v(2.15, -3.2) * mm, "end": v(2.17, -3.2) * mm});
            skLineSegment(sketch, "E898", {"start": v(2.17, -3.2) * mm, "end": v(2.19, -3.2) * mm});
            skLineSegment(sketch, "E899", {"start": v(2.19, -3.2) * mm, "end": v(2.2, -3.2) * mm});
            skLineSegment(sketch, "E900", {"start": v(2.2, -3.2) * mm, "end": v(2.23, -3.2) * mm});
            skLineSegment(sketch, "E901", {"start": v(2.23, -3.2) * mm, "end": v(2.25, -3.19) * mm});
            skLineSegment(sketch, "E902", {"start": v(2.25, -3.19) * mm, "end": v(2.27, -3.18) * mm});
            skLineSegment(sketch, "E903", {"start": v(2.27, -3.18) * mm, "end": v(2.29, -3.18) * mm});
            skLineSegment(sketch, "E904", {"start": v(2.29, -3.18) * mm, "end": v(2.3, -3.17) * mm});
            skLineSegment(sketch, "E905", {"start": v(2.3, -3.17) * mm, "end": v(2.33, -3.17) * mm});
            skLineSegment(sketch, "E906", {"start": v(2.33, -3.17) * mm, "end": v(2.35, -3.16) * mm});
            skLineSegment(sketch, "E907", {"start": v(2.35, -3.16) * mm, "end": v(2.37, -3.15) * mm});
            skLineSegment(sketch, "E908", {"start": v(2.37, -3.15) * mm, "end": v(2.39, -3.14) * mm});
            skLineSegment(sketch, "E909", {"start": v(2.39, -3.14) * mm, "end": v(2.4, -3.14) * mm});
            skLineSegment(sketch, "E910", {"start": v(2.4, -3.14) * mm, "end": v(2.42, -3.13) * mm});
            skLineSegment(sketch, "E911", {"start": v(2.42, -3.13) * mm, "end": v(2.44, -3.12) * mm});
            skLineSegment(sketch, "E912", {"start": v(2.44, -3.12) * mm, "end": v(2.46, -3.11) * mm});
            skLineSegment(sketch, "E913", {"start": v(2.46, -3.11) * mm, "end": v(2.47, -3.1) * mm});
            skLineSegment(sketch, "E914", {"start": v(2.47, -3.1) * mm, "end": v(2.49, -3.1) * mm});
            skLineSegment(sketch, "E915", {"start": v(2.49, -3.1) * mm, "end": v(2.5, -3.08) * mm});
            skLineSegment(sketch, "E916", {"start": v(2.5, -3.08) * mm, "end": v(2.52, -3.07) * mm});
            skLineSegment(sketch, "E917", {"start": v(2.52, -3.07) * mm, "end": v(2.54, -3.06) * mm});
            skLineSegment(sketch, "E918", {"start": v(2.54, -3.06) * mm, "end": v(2.55, -3.05) * mm});
            skLineSegment(sketch, "E919", {"start": v(2.55, -3.05) * mm, "end": v(2.57, -3.04) * mm});
            skLineSegment(sketch, "E920", {"start": v(2.57, -3.04) * mm, "end": v(2.58, -3.03) * mm});
            skLineSegment(sketch, "E921", {"start": v(2.58, -3.03) * mm, "end": v(2.6, -3.01) * mm});
            skLineSegment(sketch, "E922", {"start": v(2.6, -3.01) * mm, "end": v(2.6, -3) * mm});
            skLineSegment(sketch, "E923", {"start": v(2.6, -3) * mm, "end": v(2.62, -2.99) * mm});
            skLineSegment(sketch, "E924", {"start": v(2.62, -2.99) * mm, "end": v(2.63, -2.98) * mm});
            skLineSegment(sketch, "E925", {"start": v(2.63, -2.98) * mm, "end": v(2.64, -2.96) * mm});
            skLineSegment(sketch, "E926", {"start": v(2.64, -2.96) * mm, "end": v(2.65, -2.95) * mm});
            skLineSegment(sketch, "E927", {"start": v(2.65, -2.95) * mm, "end": v(2.66, -2.93) * mm});
            skLineSegment(sketch, "E928", {"start": v(2.66, -2.93) * mm, "end": v(2.67, -2.92) * mm});
            skLineSegment(sketch, "E929", {"start": v(2.67, -2.92) * mm, "end": v(2.68, -2.9) * mm});
            skLineSegment(sketch, "E930", {"start": v(2.68, -2.9) * mm, "end": v(2.69, -2.89) * mm});
            skLineSegment(sketch, "E931", {"start": v(2.69, -2.89) * mm, "end": v(2.7, -2.87) * mm});
            skLineSegment(sketch, "E932", {"start": v(2.7, -2.87) * mm, "end": v(2.7, -2.86) * mm});
            skLineSegment(sketch, "E933", {"start": v(2.7, -2.86) * mm, "end": v(2.7, -2.84) * mm});
            skLineSegment(sketch, "E934", {"start": v(2.7, -2.84) * mm, "end": v(2.71, -2.82) * mm});
            skLineSegment(sketch, "E935", {"start": v(2.71, -2.82) * mm, "end": v(2.72, -2.8) * mm});
            skLineSegment(sketch, "E936", {"start": v(2.72, -2.8) * mm, "end": v(2.72, -2.8) * mm});
            skLineSegment(sketch, "E937", {"start": v(2.72, -2.8) * mm, "end": v(2.72, -2.77) * mm});
            skLineSegment(sketch, "E938", {"start": v(2.72, -2.77) * mm, "end": v(2.73, -2.76) * mm});
            skLineSegment(sketch, "E939", {"start": v(2.73, -2.76) * mm, "end": v(2.73, -2.74) * mm});
            skLineSegment(sketch, "E940", {"start": v(2.73, -2.74) * mm, "end": v(2.73, -2.72) * mm});
            skLineSegment(sketch, "E941", {"start": v(2.73, -2.72) * mm, "end": v(2.73, -2.71) * mm});
            skLineSegment(sketch, "E942", {"start": v(2.73, -2.71) * mm, "end": v(2.73, -2.7) * mm});
            skLineSegment(sketch, "E943", {"start": v(2.73, -2.7) * mm, "end": v(2.73, -2.7) * mm});
            skLineSegment(sketch, "E944", {"start": v(2.73, -2.7) * mm, "end": v(2.73, -2.68) * mm});
            skLineSegment(sketch, "E945", {"start": v(2.73, -2.68) * mm, "end": v(2.72, -2.68) * mm});
            skLineSegment(sketch, "E946", {"start": v(2.72, -2.68) * mm, "end": v(2.72, -2.67) * mm});
            skLineSegment(sketch, "E947", {"start": v(2.72, -2.67) * mm, "end": v(2.72, -2.67) * mm});
            skLineSegment(sketch, "E948", {"start": v(2.72, -2.67) * mm, "end": v(2.72, -2.66) * mm});
            skLineSegment(sketch, "E949", {"start": v(2.72, -2.66) * mm, "end": v(2.72, -2.65) * mm});
            skLineSegment(sketch, "E950", {"start": v(2.72, -2.65) * mm, "end": v(2.72, -2.65) * mm});
            skLineSegment(sketch, "E951", {"start": v(2.72, -2.65) * mm, "end": v(2.72, -2.64) * mm});
            skLineSegment(sketch, "E952", {"start": v(2.72, -2.64) * mm, "end": v(2.72, -2.64) * mm});
            skLineSegment(sketch, "E953", {"start": v(2.72, -2.64) * mm, "end": v(2.72, -2.63) * mm});
            skLineSegment(sketch, "E954", {"start": v(2.72, -2.63) * mm, "end": v(2.71, -2.62) * mm});
            skLineSegment(sketch, "E955", {"start": v(2.71, -2.62) * mm, "end": v(2.71, -2.62) * mm});
            skLineSegment(sketch, "E956", {"start": v(2.71, -2.62) * mm, "end": v(2.71, -2.61) * mm});
            skLineSegment(sketch, "E957", {"start": v(2.71, -2.61) * mm, "end": v(2.7, -2.6) * mm});
            skLineSegment(sketch, "E958", {"start": v(2.7, -2.6) * mm, "end": v(2.7, -2.6) * mm});
            skLineSegment(sketch, "E959", {"start": v(2.7, -2.6) * mm, "end": v(2.7, -2.59) * mm});
            skLineSegment(sketch, "E960", {"start": v(2.7, -2.59) * mm, "end": v(2.7, -2.58) * mm});
            skLineSegment(sketch, "E961", {"start": v(2.7, -2.58) * mm, "end": v(2.7, -2.57) * mm});
            skLineSegment(sketch, "E962", {"start": v(2.7, -2.57) * mm, "end": v(2.7, -2.57) * mm});
            skLineSegment(sketch, "E963", {"start": v(2.7, -2.57) * mm, "end": v(2.7, -2.56) * mm});
            skLineSegment(sketch, "E964", {"start": v(2.7, -2.56) * mm, "end": v(2.7, -2.55) * mm});
            skLineSegment(sketch, "E965", {"start": v(2.7, -2.55) * mm, "end": v(2.7, -2.55) * mm});
            skLineSegment(sketch, "E966", {"start": v(2.7, -2.55) * mm, "end": v(2.69, -2.54) * mm});
            skLineSegment(sketch, "E967", {"start": v(2.69, -2.54) * mm, "end": v(2.69, -2.53) * mm});
            skLineSegment(sketch, "E968", {"start": v(2.69, -2.53) * mm, "end": v(2.68, -2.53) * mm});
            skLineSegment(sketch, "E969", {"start": v(2.68, -2.53) * mm, "end": v(2.68, -2.52) * mm});
            skLineSegment(sketch, "E970", {"start": v(2.68, -2.52) * mm, "end": v(2.68, -2.52) * mm});
            skLineSegment(sketch, "E971", {"start": v(2.68, -2.52) * mm, "end": v(2.68, -2.5) * mm});
            skLineSegment(sketch, "E972", {"start": v(2.68, -2.5) * mm, "end": v(2.67, -2.5) * mm});
            skLineSegment(sketch, "E973", {"start": v(2.67, -2.5) * mm, "end": v(2.67, -2.5) * mm});
            skLineSegment(sketch, "E974", {"start": v(2.67, -2.5) * mm, "end": v(2.67, -2.48) * mm});
            skLineSegment(sketch, "E975", {"start": v(2.67, -2.48) * mm, "end": v(2.66, -2.48) * mm});
            skLineSegment(sketch, "E976", {"start": v(2.66, -2.48) * mm, "end": v(2.66, -2.47) * mm});
            skLineSegment(sketch, "E977", {"start": v(2.66, -2.47) * mm, "end": v(2.66, -2.47) * mm});
            skLineSegment(sketch, "E978", {"start": v(2.66, -2.47) * mm, "end": v(2.66, -2.46) * mm});
            skLineSegment(sketch, "E979", {"start": v(2.66, -2.46) * mm, "end": v(2.65, -2.45) * mm});
            skLineSegment(sketch, "E980", {"start": v(2.65, -2.45) * mm, "end": v(2.65, -2.45) * mm});
            skLineSegment(sketch, "E981", {"start": v(2.65, -2.45) * mm, "end": v(2.65, -2.44) * mm});
            skLineSegment(sketch, "E982", {"start": v(2.65, -2.44) * mm, "end": v(2.64, -2.44) * mm});
            skLineSegment(sketch, "E983", {"start": v(2.64, -2.44) * mm, "end": v(2.64, -2.43) * mm});
            skLineSegment(sketch, "E984", {"start": v(2.64, -2.43) * mm, "end": v(2.64, -2.42) * mm});
            skLineSegment(sketch, "E985", {"start": v(2.64, -2.42) * mm, "end": v(2.64, -2.42) * mm});
            skLineSegment(sketch, "E986", {"start": v(2.64, -2.42) * mm, "end": v(2.63, -2.41) * mm});
            skLineSegment(sketch, "E987", {"start": v(2.63, -2.41) * mm, "end": v(2.63, -2.41) * mm});
            skLineSegment(sketch, "E988", {"start": v(2.63, -2.41) * mm, "end": v(2.63, -2.4) * mm});
            skLineSegment(sketch, "E989", {"start": v(2.63, -2.4) * mm, "end": v(2.62, -2.4) * mm});
            skLineSegment(sketch, "E990", {"start": v(2.62, -2.4) * mm, "end": v(2.6, -2.38) * mm});
            skLineSegment(sketch, "E991", {"start": v(2.6, -2.38) * mm, "end": v(2.6, -2.36) * mm});
            skLineSegment(sketch, "E992", {"start": v(2.6, -2.36) * mm, "end": v(2.58, -2.34) * mm});
            skLineSegment(sketch, "E993", {"start": v(2.58, -2.34) * mm, "end": v(2.56, -2.32) * mm});
            skLineSegment(sketch, "E994", {"start": v(2.56, -2.32) * mm, "end": v(2.55, -2.29) * mm});
            skLineSegment(sketch, "E995", {"start": v(2.55, -2.29) * mm, "end": v(2.52, -2.26) * mm});
            skLineSegment(sketch, "E996", {"start": v(2.52, -2.26) * mm, "end": v(2.5, -2.22) * mm});
            skLineSegment(sketch, "E997", {"start": v(2.5, -2.22) * mm, "end": v(2.48, -2.19) * mm});
            skLineSegment(sketch, "E998", {"start": v(2.48, -2.19) * mm, "end": v(2.45, -2.15) * mm});
            skLineSegment(sketch, "E999", {"start": v(2.45, -2.15) * mm, "end": v(2.42, -2.1) * mm});
            skLineSegment(sketch, "E1000", {"start": v(2.42, -2.1) * mm, "end": v(2.39, -2.06) * mm});
            skLineSegment(sketch, "E1001", {"start": v(2.39, -2.06) * mm, "end": v(2.36, -2.02) * mm});
            skLineSegment(sketch, "E1002", {"start": v(2.36, -2.02) * mm, "end": v(2.33, -1.97) * mm});
            skLineSegment(sketch, "E1003", {"start": v(2.33, -1.97) * mm, "end": v(2.3, -1.92) * mm});
            skLineSegment(sketch, "E1004", {"start": v(2.3, -1.92) * mm, "end": v(2.26, -1.87) * mm});
            skLineSegment(sketch, "E1005", {"start": v(2.26, -1.87) * mm, "end": v(2.22, -1.82) * mm});
            skLineSegment(sketch, "E1006", {"start": v(2.22, -1.82) * mm, "end": v(2.18, -1.77) * mm});
            skLineSegment(sketch, "E1007", {"start": v(2.18, -1.77) * mm, "end": v(2.15, -1.71) * mm});
            skLineSegment(sketch, "E1008", {"start": v(2.15, -1.71) * mm, "end": v(2.11, -1.66) * mm});
            skLineSegment(sketch, "E1009", {"start": v(2.11, -1.66) * mm, "end": v(2.07, -1.6) * mm});
            skLineSegment(sketch, "E1010", {"start": v(2.07, -1.6) * mm, "end": v(2.03, -1.55) * mm});
            skLineSegment(sketch, "E1011", {"start": v(2.03, -1.55) * mm, "end": v(2, -1.5) * mm});
            skLineSegment(sketch, "E1012", {"start": v(2, -1.5) * mm, "end": v(1.96, -1.44) * mm});
            skLineSegment(sketch, "E1013", {"start": v(1.96, -1.44) * mm, "end": v(1.92, -1.38) * mm});
            skLineSegment(sketch, "E1014", {"start": v(1.92, -1.38) * mm, "end": v(1.88, -1.33) * mm});
            skLineSegment(sketch, "E1015", {"start": v(1.88, -1.33) * mm, "end": v(1.85, -1.28) * mm});
            skLineSegment(sketch, "E1016", {"start": v(1.85, -1.28) * mm, "end": v(1.8, -1.22) * mm});
            skLineSegment(sketch, "E1017", {"start": v(1.8, -1.22) * mm, "end": v(1.77, -1.17) * mm});
            skLineSegment(sketch, "E1018", {"start": v(1.77, -1.17) * mm, "end": v(1.74, -1.12) * mm});
            skLineSegment(sketch, "E1019", {"start": v(1.74, -1.12) * mm, "end": v(1.7, -1.07) * mm});
            skLineSegment(sketch, "E1020", {"start": v(1.7, -1.07) * mm, "end": v(1.67, -1.02) * mm});
            skLineSegment(sketch, "E1021", {"start": v(1.67, -1.02) * mm, "end": v(1.64, -0.97) * mm});
            skLineSegment(sketch, "E1022", {"start": v(1.64, -0.97) * mm, "end": v(1.6, -0.93) * mm});
            skLineSegment(sketch, "E1023", {"start": v(1.6, -0.93) * mm, "end": v(1.57, -0.88) * mm});
            skLineSegment(sketch, "E1024", {"start": v(1.57, -0.88) * mm, "end": v(1.55, -0.84) * mm});
            skLineSegment(sketch, "E1025", {"start": v(1.55, -0.84) * mm, "end": v(1.52, -0.8) * mm});
            skLineSegment(sketch, "E1026", {"start": v(1.52, -0.8) * mm, "end": v(1.5, -0.77) * mm});
            skLineSegment(sketch, "E1027", {"start": v(1.5, -0.77) * mm, "end": v(1.47, -0.73) * mm});
            skLineSegment(sketch, "E1028", {"start": v(1.47, -0.73) * mm, "end": v(1.45, -0.7) * mm});
            skLineSegment(sketch, "E1029", {"start": v(1.45, -0.7) * mm, "end": v(1.43, -0.67) * mm});
            skLineSegment(sketch, "E1030", {"start": v(1.43, -0.67) * mm, "end": v(1.41, -0.65) * mm});
            skLineSegment(sketch, "E1031", {"start": v(1.41, -0.65) * mm, "end": v(1.4, -0.63) * mm});
            skLineSegment(sketch, "E1032", {"start": v(1.4, -0.63) * mm, "end": v(1.38, -0.6) * mm});
            skLineSegment(sketch, "E1033", {"start": v(1.38, -0.6) * mm, "end": v(1.37, -0.6) * mm});
            skLineSegment(sketch, "E1034", {"start": v(1.37, -0.6) * mm, "end": v(1.37, -0.58) * mm});
            skLineSegment(sketch, "E1035", {"start": v(1.37, -0.58) * mm, "end": v(1.36, -0.58) * mm});
            skLineSegment(sketch, "E1036", {"start": v(1.36, -0.58) * mm, "end": v(1.36, -0.58) * mm});
            skLineSegment(sketch, "E1037", {"start": v(1.36, -0.58) * mm, "end": v(1.4, -0.55) * mm});
            skLineSegment(sketch, "E1038", {"start": v(1.4, -0.55) * mm, "end": v(1.44, -0.53) * mm});
            skLineSegment(sketch, "E1039", {"start": v(1.44, -0.53) * mm, "end": v(1.48, -0.51) * mm});
            skLineSegment(sketch, "E1040", {"start": v(1.48, -0.51) * mm, "end": v(1.51, -0.49) * mm});
            skLineSegment(sketch, "E1041", {"start": v(1.51, -0.49) * mm, "end": v(1.55, -0.47) * mm});
            skLineSegment(sketch, "E1042", {"start": v(1.55, -0.47) * mm, "end": v(1.59, -0.44) * mm});
            skLineSegment(sketch, "E1043", {"start": v(1.59, -0.44) * mm, "end": v(1.62, -0.42) * mm});
            skLineSegment(sketch, "E1044", {"start": v(1.62, -0.42) * mm, "end": v(1.66, -0.4) * mm});
            skLineSegment(sketch, "E1045", {"start": v(1.66, -0.4) * mm, "end": v(1.69, -0.37) * mm});
            skLineSegment(sketch, "E1046", {"start": v(1.69, -0.37) * mm, "end": v(1.72, -0.35) * mm});
            skLineSegment(sketch, "E1047", {"start": v(1.72, -0.35) * mm, "end": v(1.75, -0.32) * mm});
            skLineSegment(sketch, "E1048", {"start": v(1.75, -0.32) * mm, "end": v(1.79, -0.3) * mm});
            skLineSegment(sketch, "E1049", {"start": v(1.79, -0.3) * mm, "end": v(1.82, -0.27) * mm});
            skLineSegment(sketch, "E1050", {"start": v(1.82, -0.27) * mm, "end": v(1.85, -0.25) * mm});
            skLineSegment(sketch, "E1051", {"start": v(1.85, -0.25) * mm, "end": v(1.88, -0.22) * mm});
            skLineSegment(sketch, "E1052", {"start": v(1.88, -0.22) * mm, "end": v(1.9, -0.2) * mm});
            skLineSegment(sketch, "E1053", {"start": v(1.9, -0.2) * mm, "end": v(1.93, -0.17) * mm});
            skLineSegment(sketch, "E1054", {"start": v(1.93, -0.17) * mm, "end": v(1.96, -0.14) * mm});
            skLineSegment(sketch, "E1055", {"start": v(1.96, -0.14) * mm, "end": v(1.99, -0.11) * mm});
            skLineSegment(sketch, "E1056", {"start": v(1.99, -0.11) * mm, "end": v(2.01, -0.08) * mm});
            skLineSegment(sketch, "E1057", {"start": v(2.01, -0.08) * mm, "end": v(2.04, -0.06) * mm});
            skLineSegment(sketch, "E1058", {"start": v(2.04, -0.06) * mm, "end": v(2.07, -0.03) * mm});
            skLineSegment(sketch, "E1059", {"start": v(2.07, -0.03) * mm, "end": v(2.09, 0) * mm});
            skLineSegment(sketch, "E1060", {"start": v(2.09, 0) * mm, "end": v(2.11, 0.03) * mm});
            skLineSegment(sketch, "E1061", {"start": v(2.11, 0.03) * mm, "end": v(2.14, 0.06) * mm});
            skLineSegment(sketch, "E1062", {"start": v(2.14, 0.06) * mm, "end": v(2.16, 0.1) * mm});
            skLineSegment(sketch, "E1063", {"start": v(2.16, 0.1) * mm, "end": v(2.18, 0.13) * mm});
            skLineSegment(sketch, "E1064", {"start": v(2.18, 0.13) * mm, "end": v(2.2, 0.16) * mm});
            skLineSegment(sketch, "E1065", {"start": v(2.2, 0.16) * mm, "end": v(2.22, 0.2) * mm});
            skLineSegment(sketch, "E1066", {"start": v(2.22, 0.2) * mm, "end": v(2.24, 0.22) * mm});
            skLineSegment(sketch, "E1067", {"start": v(2.24, 0.22) * mm, "end": v(2.26, 0.26) * mm});
            skLineSegment(sketch, "E1068", {"start": v(2.26, 0.26) * mm, "end": v(2.27, 0.3) * mm});
            skLineSegment(sketch, "E1069", {"start": v(2.27, 0.3) * mm, "end": v(2.3, 0.33) * mm});
            skLineSegment(sketch, "E1070", {"start": v(2.3, 0.33) * mm, "end": v(2.3, 0.36) * mm});
            skLineSegment(sketch, "E1071", {"start": v(2.3, 0.36) * mm, "end": v(2.32, 0.4) * mm});
            skLineSegment(sketch, "E1072", {"start": v(2.32, 0.4) * mm, "end": v(2.34, 0.43) * mm});
            skLineSegment(sketch, "E1073", {"start": v(2.34, 0.43) * mm, "end": v(2.35, 0.47) * mm});
            skLineSegment(sketch, "E1074", {"start": v(2.35, 0.47) * mm, "end": v(2.36, 0.5) * mm});
            skLineSegment(sketch, "E1075", {"start": v(2.36, 0.5) * mm, "end": v(2.38, 0.54) * mm});
            skLineSegment(sketch, "E1076", {"start": v(2.38, 0.54) * mm, "end": v(2.39, 0.58) * mm});
            skLineSegment(sketch, "E1077", {"start": v(2.39, 0.58) * mm, "end": v(2.4, 0.62) * mm});
            skLineSegment(sketch, "E1078", {"start": v(2.4, 0.62) * mm, "end": v(2.41, 0.66) * mm});
            skLineSegment(sketch, "E1079", {"start": v(2.41, 0.66) * mm, "end": v(2.42, 0.7) * mm});
            skLineSegment(sketch, "E1080", {"start": v(2.42, 0.7) * mm, "end": v(2.43, 0.74) * mm});
            skLineSegment(sketch, "E1081", {"start": v(2.43, 0.74) * mm, "end": v(2.44, 0.78) * mm});
            skLineSegment(sketch, "E1082", {"start": v(2.44, 0.78) * mm, "end": v(2.44, 0.83) * mm});
            skLineSegment(sketch, "E1083", {"start": v(2.44, 0.83) * mm, "end": v(2.45, 0.87) * mm});
            skLineSegment(sketch, "E1084", {"start": v(2.45, 0.87) * mm, "end": v(2.46, 0.91) * mm});
            skLineSegment(sketch, "E1085", {"start": v(2.46, 0.91) * mm, "end": v(2.46, 0.96) * mm});
            skLineSegment(sketch, "E1086", {"start": v(2.46, 0.96) * mm, "end": v(2.47, 1) * mm});
            skLineSegment(sketch, "E1087", {"start": v(2.47, 1) * mm, "end": v(2.47, 1.07) * mm});
            skLineSegment(sketch, "E1088", {"start": v(2.47, 1.07) * mm, "end": v(2.47, 1.13) * mm});
            skLineSegment(sketch, "E1089", {"start": v(2.47, 1.13) * mm, "end": v(2.47, 1.2) * mm});
            skLineSegment(sketch, "E1090", {"start": v(2.47, 1.2) * mm, "end": v(2.47, 1.26) * mm});
            skLineSegment(sketch, "E1091", {"start": v(2.47, 1.26) * mm, "end": v(2.47, 1.32) * mm});
            skLineSegment(sketch, "E1092", {"start": v(2.47, 1.32) * mm, "end": v(2.46, 1.39) * mm});
            skLineSegment(sketch, "E1093", {"start": v(2.46, 1.39) * mm, "end": v(2.45, 1.45) * mm});
            skLineSegment(sketch, "E1094", {"start": v(2.45, 1.45) * mm, "end": v(2.44, 1.51) * mm});
            skLineSegment(sketch, "E1095", {"start": v(2.44, 1.51) * mm, "end": v(2.43, 1.58) * mm});
            skLineSegment(sketch, "E1096", {"start": v(2.43, 1.58) * mm, "end": v(2.41, 1.64) * mm});
            skLineSegment(sketch, "E1097", {"start": v(2.41, 1.64) * mm, "end": v(2.4, 1.7) * mm});
            skLineSegment(sketch, "E1098", {"start": v(2.4, 1.7) * mm, "end": v(2.38, 1.76) * mm});
            skLineSegment(sketch, "E1099", {"start": v(2.38, 1.76) * mm, "end": v(2.35, 1.82) * mm});
            skLineSegment(sketch, "E1100", {"start": v(2.35, 1.82) * mm, "end": v(2.33, 1.88) * mm});
            skLineSegment(sketch, "E1101", {"start": v(2.33, 1.88) * mm, "end": v(2.3, 1.93) * mm});
            skLineSegment(sketch, "E1102", {"start": v(2.3, 1.93) * mm, "end": v(2.28, 2) * mm});
            skLineSegment(sketch, "E1103", {"start": v(2.28, 2) * mm, "end": v(2.25, 2.05) * mm});
            skLineSegment(sketch, "E1104", {"start": v(2.25, 2.05) * mm, "end": v(2.22, 2.1) * mm});
            skLineSegment(sketch, "E1105", {"start": v(2.22, 2.1) * mm, "end": v(2.19, 2.16) * mm});
            skLineSegment(sketch, "E1106", {"start": v(2.19, 2.16) * mm, "end": v(2.16, 2.2) * mm});
            skLineSegment(sketch, "E1107", {"start": v(2.16, 2.2) * mm, "end": v(2.12, 2.26) * mm});
            skLineSegment(sketch, "E1108", {"start": v(2.12, 2.26) * mm, "end": v(2.08, 2.31) * mm});
            skLineSegment(sketch, "E1109", {"start": v(2.08, 2.31) * mm, "end": v(2.05, 2.36) * mm});
            skLineSegment(sketch, "E1110", {"start": v(2.05, 2.36) * mm, "end": v(2, 2.41) * mm});
            skLineSegment(sketch, "E1111", {"start": v(2, 2.41) * mm, "end": v(1.96, 2.46) * mm});
            skLineSegment(sketch, "E1112", {"start": v(1.96, 2.46) * mm, "end": v(1.92, 2.5) * mm});
            skLineSegment(sketch, "E1113", {"start": v(1.92, 2.5) * mm, "end": v(1.88, 2.55) * mm});
            skLineSegment(sketch, "E1114", {"start": v(1.88, 2.55) * mm, "end": v(1.83, 2.6) * mm});
            skLineSegment(sketch, "E1115", {"start": v(1.83, 2.6) * mm, "end": v(1.78, 2.63) * mm});
            skLineSegment(sketch, "E1116", {"start": v(1.78, 2.63) * mm, "end": v(1.74, 2.67) * mm});
            skLineSegment(sketch, "E1117", {"start": v(1.74, 2.67) * mm, "end": v(1.69, 2.71) * mm});
            skLineSegment(sketch, "E1118", {"start": v(1.69, 2.71) * mm, "end": v(1.64, 2.75) * mm});
            skLineSegment(sketch, "E1119", {"start": v(1.64, 2.75) * mm, "end": v(1.58, 2.79) * mm});
            skLineSegment(sketch, "E1120", {"start": v(1.58, 2.79) * mm, "end": v(1.53, 2.82) * mm});
            skLineSegment(sketch, "E1121", {"start": v(1.53, 2.82) * mm, "end": v(1.48, 2.85) * mm});
            skLineSegment(sketch, "E1122", {"start": v(1.48, 2.85) * mm, "end": v(1.42, 2.88) * mm});
            skLineSegment(sketch, "E1123", {"start": v(1.42, 2.88) * mm, "end": v(1.37, 2.91) * mm});
            skLineSegment(sketch, "E1124", {"start": v(1.37, 2.91) * mm, "end": v(1.3, 2.94) * mm});
            skLineSegment(sketch, "E1125", {"start": v(1.3, 2.94) * mm, "end": v(1.25, 2.96) * mm});
            skLineSegment(sketch, "E1126", {"start": v(1.25, 2.96) * mm, "end": v(1.2, 2.99) * mm});
            skLineSegment(sketch, "E1127", {"start": v(1.2, 2.99) * mm, "end": v(1.13, 3) * mm});
            skLineSegment(sketch, "E1128", {"start": v(1.13, 3) * mm, "end": v(1.07, 3.03) * mm});
            skLineSegment(sketch, "E1129", {"start": v(1.07, 3.03) * mm, "end": v(1, 3.04) * mm});
            skLineSegment(sketch, "E1130", {"start": v(1, 3.04) * mm, "end": v(0.95, 3.06) * mm});
            skLineSegment(sketch, "E1131", {"start": v(0.95, 3.06) * mm, "end": v(0.88, 3.07) * mm});
            skLineSegment(sketch, "E1132", {"start": v(0.88, 3.07) * mm, "end": v(0.82, 3.08) * mm});
            skLineSegment(sketch, "E1133", {"start": v(0.82, 3.08) * mm, "end": v(0.76, 3.09) * mm});
            skLineSegment(sketch, "E1134", {"start": v(0.76, 3.09) * mm, "end": v(0.7, 3.1) * mm});
            skLineSegment(sketch, "E1135", {"start": v(0.7, 3.1) * mm, "end": v(0.63, 3.1) * mm});
            skLineSegment(sketch, "E1136", {"start": v(0.63, 3.1) * mm, "end": v(0.56, 3.1) * mm});
            skLineSegment(sketch, "E1137", {"start": v(0.56, 3.1) * mm, "end": v(0.56, 3.1) * mm});
            skLineSegment(sketch, "E1138", {"start": v(0.56, 3.1) * mm, "end": v(0.55, 3.1) * mm});
            skLineSegment(sketch, "E1139", {"start": v(0.55, 3.1) * mm, "end": v(0.55, 3.1) * mm});
            skLineSegment(sketch, "E1140", {"start": v(0.55, 3.1) * mm, "end": v(0.54, 3.1) * mm});
            skLineSegment(sketch, "E1141", {"start": v(0.54, 3.1) * mm, "end": v(0.53, 3.1) * mm});
            skLineSegment(sketch, "E1142", {"start": v(0.53, 3.1) * mm, "end": v(0.52, 3.1) * mm});
            skLineSegment(sketch, "E1143", {"start": v(0.52, 3.1) * mm, "end": v(0.5, 3.1) * mm});
            skLineSegment(sketch, "E1144", {"start": v(0.5, 3.1) * mm, "end": v(0.49, 3.1) * mm});
            skLineSegment(sketch, "E1145", {"start": v(0.49, 3.1) * mm, "end": v(0.47, 3.1) * mm});
            skLineSegment(sketch, "E1146", {"start": v(0.47, 3.1) * mm, "end": v(0.45, 3.1) * mm});
            skLineSegment(sketch, "E1147", {"start": v(0.45, 3.1) * mm, "end": v(0.43, 3.1) * mm});
            skLineSegment(sketch, "E1148", {"start": v(0.43, 3.1) * mm, "end": v(0.4, 3.1) * mm});
            skLineSegment(sketch, "E1149", {"start": v(0.4, 3.1) * mm, "end": v(0.39, 3.1) * mm});
            skLineSegment(sketch, "E1150", {"start": v(0.39, 3.1) * mm, "end": v(0.36, 3.1) * mm});
            skLineSegment(sketch, "E1151", {"start": v(0.36, 3.1) * mm, "end": v(0.34, 3.1) * mm});
            skLineSegment(sketch, "E1152", {"start": v(0.34, 3.1) * mm, "end": v(0.3, 3.1) * mm});
            skLineSegment(sketch, "E1153", {"start": v(0.3, 3.1) * mm, "end": v(0.28, 3.1) * mm});
            skLineSegment(sketch, "E1154", {"start": v(0.28, 3.1) * mm, "end": v(0.25, 3.1) * mm});
            skLineSegment(sketch, "E1155", {"start": v(0.25, 3.1) * mm, "end": v(0.22, 3.1) * mm});
            skLineSegment(sketch, "E1156", {"start": v(0.22, 3.1) * mm, "end": v(0.2, 3.1) * mm});
            skLineSegment(sketch, "E1157", {"start": v(0.2, 3.1) * mm, "end": v(0.16, 3.1) * mm});
            skLineSegment(sketch, "E1158", {"start": v(0.16, 3.1) * mm, "end": v(0.13, 3.1) * mm});
            skLineSegment(sketch, "E1159", {"start": v(0.13, 3.1) * mm, "end": v(0.1, 3.1) * mm});
            skLineSegment(sketch, "E1160", {"start": v(0.1, 3.1) * mm, "end": v(0.07, 3.1) * mm});
            skLineSegment(sketch, "E1161", {"start": v(0.07, 3.1) * mm, "end": v(0.04, 3.1) * mm});
            skLineSegment(sketch, "E1162", {"start": v(0.04, 3.1) * mm, "end": v(0, 3.1) * mm});
            skLineSegment(sketch, "E1163", {"start": v(0, 3.1) * mm, "end": v(-0.02, 3.1) * mm});
            skLineSegment(sketch, "E1164", {"start": v(-0.02, 3.1) * mm, "end": v(-0.05, 3.1) * mm});
            skLineSegment(sketch, "E1165", {"start": v(-0.05, 3.1) * mm, "end": v(-0.08, 3.1) * mm});
            skLineSegment(sketch, "E1166", {"start": v(-0.08, 3.1) * mm, "end": v(-0.11, 3.1) * mm});
            skLineSegment(sketch, "E1167", {"start": v(-0.11, 3.1) * mm, "end": v(-0.14, 3.1) * mm});
            skLineSegment(sketch, "E1168", {"start": v(-0.14, 3.1) * mm, "end": v(-0.17, 3.1) * mm});
            skLineSegment(sketch, "E1169", {"start": v(-0.17, 3.1) * mm, "end": v(-0.2, 3.1) * mm});
            skLineSegment(sketch, "E1170", {"start": v(-0.2, 3.1) * mm, "end": v(-0.23, 3.1) * mm});
            skLineSegment(sketch, "E1171", {"start": v(-0.23, 3.1) * mm, "end": v(-0.25, 3.1) * mm});
            skLineSegment(sketch, "E1172", {"start": v(-0.25, 3.1) * mm, "end": v(-0.28, 3.1) * mm});
            skLineSegment(sketch, "E1173", {"start": v(-0.28, 3.1) * mm, "end": v(-0.3, 3.1) * mm});
            skLineSegment(sketch, "E1174", {"start": v(-0.3, 3.1) * mm, "end": v(-0.33, 3.1) * mm});
            skLineSegment(sketch, "E1175", {"start": v(-0.33, 3.1) * mm, "end": v(-0.35, 3.1) * mm});
            skLineSegment(sketch, "E1176", {"start": v(-0.35, 3.1) * mm, "end": v(-0.37, 3.1) * mm});
            skLineSegment(sketch, "E1177", {"start": v(-0.37, 3.1) * mm, "end": v(-0.39, 3.1) * mm});
            skLineSegment(sketch, "E1178", {"start": v(-0.39, 3.1) * mm, "end": v(-0.4, 3.1) * mm});
            skLineSegment(sketch, "E1179", {"start": v(-0.4, 3.1) * mm, "end": v(-0.42, 3.1) * mm});
            skLineSegment(sketch, "E1180", {"start": v(-0.42, 3.1) * mm, "end": v(-0.44, 3.1) * mm});
            skLineSegment(sketch, "E1181", {"start": v(-0.44, 3.1) * mm, "end": v(-0.45, 3.1) * mm});
            skLineSegment(sketch, "E1182", {"start": v(-0.45, 3.1) * mm, "end": v(-0.46, 3.1) * mm});
            skLineSegment(sketch, "E1183", {"start": v(-0.46, 3.1) * mm, "end": v(-0.47, 3.1) * mm});
            skLineSegment(sketch, "E1184", {"start": v(-0.47, 3.1) * mm, "end": v(-0.47, 3.1) * mm});
            skLineSegment(sketch, "E1185", {"start": v(-0.47, 3.1) * mm, "end": v(-0.48, 3.1) * mm});
            skLineSegment(sketch, "E1186", {"start": v(-0.48, 3.1) * mm, "end": v(-0.48, 3.1) * mm});
            skLineSegment(sketch, "E1187", {"start": v(-0.48, 3.1) * mm, "end": v(-0.5, 3.1) * mm});
            skLineSegment(sketch, "E1188", {"start": v(-0.5, 3.1) * mm, "end": v(-0.51, 3.1) * mm});
            skLineSegment(sketch, "E1189", {"start": v(-0.51, 3.1) * mm, "end": v(-0.53, 3.1) * mm});
            skLineSegment(sketch, "E1190", {"start": v(-0.53, 3.1) * mm, "end": v(-0.54, 3.1) * mm});
            skLineSegment(sketch, "E1191", {"start": v(-0.54, 3.1) * mm, "end": v(-0.56, 3.1) * mm});
            skLineSegment(sketch, "E1192", {"start": v(-0.56, 3.1) * mm, "end": v(-0.58, 3.09) * mm});
            skLineSegment(sketch, "E1193", {"start": v(-0.58, 3.09) * mm, "end": v(-0.6, 3.09) * mm});
            skLineSegment(sketch, "E1194", {"start": v(-0.6, 3.09) * mm, "end": v(-0.61, 3.08) * mm});
            skLineSegment(sketch, "E1195", {"start": v(-0.61, 3.08) * mm, "end": v(-0.63, 3.08) * mm});
            skLineSegment(sketch, "E1196", {"start": v(-0.63, 3.08) * mm, "end": v(-0.64, 3.07) * mm});
            skLineSegment(sketch, "E1197", {"start": v(-0.64, 3.07) * mm, "end": v(-0.66, 3.07) * mm});
            skLineSegment(sketch, "E1198", {"start": v(-0.66, 3.07) * mm, "end": v(-0.68, 3.06) * mm});
            skLineSegment(sketch, "E1199", {"start": v(-0.68, 3.06) * mm, "end": v(-0.7, 3.05) * mm});
            skLineSegment(sketch, "E1200", {"start": v(-0.7, 3.05) * mm, "end": v(-0.7, 3.05) * mm});
            skLineSegment(sketch, "E1201", {"start": v(-0.7, 3.05) * mm, "end": v(-0.72, 3.04) * mm});
            skLineSegment(sketch, "E1202", {"start": v(-0.72, 3.04) * mm, "end": v(-0.74, 3.03) * mm});
            skLineSegment(sketch, "E1203", {"start": v(-0.74, 3.03) * mm, "end": v(-0.75, 3.02) * mm});
            skLineSegment(sketch, "E1204", {"start": v(-0.75, 3.02) * mm, "end": v(-0.77, 3.02) * mm});
            skLineSegment(sketch, "E1205", {"start": v(-0.77, 3.02) * mm, "end": v(-0.78, 3) * mm});
            skLineSegment(sketch, "E1206", {"start": v(-0.78, 3) * mm, "end": v(-0.8, 3) * mm});
            skLineSegment(sketch, "E1207", {"start": v(-0.8, 3) * mm, "end": v(-0.81, 2.99) * mm});
            skLineSegment(sketch, "E1208", {"start": v(-0.81, 2.99) * mm, "end": v(-0.83, 2.98) * mm});
            skLineSegment(sketch, "E1209", {"start": v(-0.83, 2.98) * mm, "end": v(-0.84, 2.97) * mm});
            skLineSegment(sketch, "E1210", {"start": v(-0.84, 2.97) * mm, "end": v(-0.85, 2.95) * mm});
            skLineSegment(sketch, "E1211", {"start": v(-0.85, 2.95) * mm, "end": v(-0.87, 2.94) * mm});
            skLineSegment(sketch, "E1212", {"start": v(-0.87, 2.94) * mm, "end": v(-0.88, 2.93) * mm});
            skLineSegment(sketch, "E1213", {"start": v(-0.88, 2.93) * mm, "end": v(-0.9, 2.92) * mm});
            skLineSegment(sketch, "E1214", {"start": v(-0.9, 2.92) * mm, "end": v(-0.9, 2.9) * mm});
            skLineSegment(sketch, "E1215", {"start": v(-0.9, 2.9) * mm, "end": v(-0.91, 2.9) * mm});
            skLineSegment(sketch, "E1216", {"start": v(-0.91, 2.9) * mm, "end": v(-0.93, 2.88) * mm});
            skLineSegment(sketch, "E1217", {"start": v(-0.93, 2.88) * mm, "end": v(-0.94, 2.87) * mm});
            skLineSegment(sketch, "E1218", {"start": v(-0.94, 2.87) * mm, "end": v(-0.95, 2.85) * mm});
            skLineSegment(sketch, "E1219", {"start": v(-0.95, 2.85) * mm, "end": v(-0.96, 2.84) * mm});
            skLineSegment(sketch, "E1220", {"start": v(-0.96, 2.84) * mm, "end": v(-0.97, 2.82) * mm});
            skLineSegment(sketch, "E1221", {"start": v(-0.97, 2.82) * mm, "end": v(-0.97, 2.8) * mm});
            skLineSegment(sketch, "E1222", {"start": v(-0.97, 2.8) * mm, "end": v(-0.98, 2.8) * mm});
            skLineSegment(sketch, "E1223", {"start": v(-0.98, 2.8) * mm, "end": v(-1, 2.78) * mm});
            skLineSegment(sketch, "E1224", {"start": v(-1, 2.78) * mm, "end": v(-1, 2.76) * mm});
            skLineSegment(sketch, "E1225", {"start": v(-1, 2.76) * mm, "end": v(-1, 2.75) * mm});
            skLineSegment(sketch, "E1226", {"start": v(-1, 2.75) * mm, "end": v(-1.01, 2.73) * mm});
            skLineSegment(sketch, "E1227", {"start": v(-1.01, 2.73) * mm, "end": v(-1.02, 2.72) * mm});
            skLineSegment(sketch, "E1228", {"start": v(-1.02, 2.72) * mm, "end": v(-1.02, 2.7) * mm});
            skLineSegment(sketch, "E1229", {"start": v(-1.02, 2.7) * mm, "end": v(-1.03, 2.68) * mm});
            skLineSegment(sketch, "E1230", {"start": v(-1.03, 2.68) * mm, "end": v(-1.03, 2.66) * mm});
            skLineSegment(sketch, "E1231", {"start": v(-1.03, 2.66) * mm, "end": v(-1.03, 2.65) * mm});
            skLineSegment(sketch, "E1232", {"start": v(-1.03, 2.65) * mm, "end": v(-1.04, 2.63) * mm});
            skLineSegment(sketch, "E1233", {"start": v(-1.04, 2.63) * mm, "end": v(-1.04, 2.61) * mm});
            skLineSegment(sketch, "E1234", {"start": v(-1.04, 2.61) * mm, "end": v(-1.04, 2.6) * mm});
            skLineSegment(sketch, "E1235", {"start": v(-1.04, 2.6) * mm, "end": v(-1.04, 2.58) * mm});
            skLineSegment(sketch, "E1236", {"start": v(-1.04, 2.58) * mm, "end": v(-1.04, 2.56) * mm});
            skLineSegment(sketch, "E1237", {"start": v(-1.04, 2.56) * mm, "end": v(-1.04, 2.55) * mm});
            skLineSegment(sketch, "E1238", {"start": v(-1.04, 2.55) * mm, "end": v(-1.04, 2.53) * mm});
            skLineSegment(sketch, "E1239", {"start": v(-1.04, 2.53) * mm, "end": v(-1.04, 2.5) * mm});
            skLineSegment(sketch, "E1240", {"start": v(-1.04, 2.5) * mm, "end": v(-1.04, 2.46) * mm});
            skLineSegment(sketch, "E1241", {"start": v(-1.04, 2.46) * mm, "end": v(-1.04, 2.41) * mm});
            skLineSegment(sketch, "E1242", {"start": v(-1.04, 2.41) * mm, "end": v(-1.04, 2.35) * mm});
            skLineSegment(sketch, "E1243", {"start": v(-1.04, 2.35) * mm, "end": v(-1.04, 2.28) * mm});
            skLineSegment(sketch, "E1244", {"start": v(-1.04, 2.28) * mm, "end": v(-1.04, 2.2) * mm});
            skLineSegment(sketch, "E1245", {"start": v(-1.04, 2.2) * mm, "end": v(-1.04, 2.11) * mm});
            skLineSegment(sketch, "E1246", {"start": v(-1.04, 2.11) * mm, "end": v(-1.04, 2.02) * mm});
            skLineSegment(sketch, "E1247", {"start": v(-1.04, 2.02) * mm, "end": v(-1.04, 1.91) * mm});
            skLineSegment(sketch, "E1248", {"start": v(-1.04, 1.91) * mm, "end": v(-1.04, 1.8) * mm});
            skLineSegment(sketch, "E1249", {"start": v(-1.04, 1.8) * mm, "end": v(-1.04, 1.68) * mm});
            skLineSegment(sketch, "E1250", {"start": v(-1.04, 1.68) * mm, "end": v(-1.04, 1.56) * mm});
            skLineSegment(sketch, "E1251", {"start": v(-1.04, 1.56) * mm, "end": v(-1.04, 1.43) * mm});
            skLineSegment(sketch, "E1252", {"start": v(-1.04, 1.43) * mm, "end": v(-1.04, 1.3) * mm});
            skLineSegment(sketch, "E1253", {"start": v(-1.04, 1.3) * mm, "end": v(-1.04, 1.16) * mm});
            skLineSegment(sketch, "E1254", {"start": v(-1.04, 1.16) * mm, "end": v(-1.04, 1.02) * mm});
            skLineSegment(sketch, "E1255", {"start": v(-1.04, 1.02) * mm, "end": v(-1.04, 0.87) * mm});
            skLineSegment(sketch, "E1256", {"start": v(-1.04, 0.87) * mm, "end": v(-1.04, 0.72) * mm});
            skLineSegment(sketch, "E1257", {"start": v(-1.04, 0.72) * mm, "end": v(-1.04, 0.57) * mm});
            skLineSegment(sketch, "E1258", {"start": v(-1.04, 0.57) * mm, "end": v(-1.04, 0.42) * mm});
            skLineSegment(sketch, "E1259", {"start": v(-1.04, 0.42) * mm, "end": v(-1.04, 0.27) * mm});
            skLineSegment(sketch, "E1260", {"start": v(-1.04, 0.27) * mm, "end": v(-1.04, 0.11) * mm});
            skLineSegment(sketch, "E1261", {"start": v(-1.04, 0.11) * mm, "end": v(-1.04, -0.05) * mm});
            skLineSegment(sketch, "E1262", {"start": v(-1.04, -0.05) * mm, "end": v(-1.04, -0.2) * mm});
            skLineSegment(sketch, "E1263", {"start": v(-1.04, -0.2) * mm, "end": v(-1.04, -0.36) * mm});
            skLineSegment(sketch, "E1264", {"start": v(-1.04, -0.36) * mm, "end": v(-1.04, -0.51) * mm});
            skLineSegment(sketch, "E1265", {"start": v(-1.04, -0.51) * mm, "end": v(-1.04, -0.67) * mm});
            skLineSegment(sketch, "E1266", {"start": v(-1.04, -0.67) * mm, "end": v(-1.04, -0.82) * mm});
            skLineSegment(sketch, "E1267", {"start": v(-1.04, -0.82) * mm, "end": v(-1.04, -0.96) * mm});
            skLineSegment(sketch, "E1268", {"start": v(-1.04, -0.96) * mm, "end": v(-1.04, -1.11) * mm});
            skLineSegment(sketch, "E1269", {"start": v(-1.04, -1.11) * mm, "end": v(-1.04, -1.25) * mm});
            skLineSegment(sketch, "E1270", {"start": v(-1.04, -1.25) * mm, "end": v(-1.04, -1.4) * mm});
            skLineSegment(sketch, "E1271", {"start": v(-1.04, -1.4) * mm, "end": v(-1.04, -1.52) * mm});
            skLineSegment(sketch, "E1272", {"start": v(-1.04, -1.52) * mm, "end": v(-1.04, -1.65) * mm});
            skLineSegment(sketch, "E1273", {"start": v(-1.04, -1.65) * mm, "end": v(-1.04, -1.78) * mm});
            skLineSegment(sketch, "E1274", {"start": v(-1.04, -1.78) * mm, "end": v(-1.04, -1.9) * mm});
            skLineSegment(sketch, "E1275", {"start": v(-1.04, -1.9) * mm, "end": v(-1.04, -2) * mm});
            skLineSegment(sketch, "E1276", {"start": v(-1.04, -2) * mm, "end": v(-1.04, -2.1) * mm});
            skLineSegment(sketch, "E1277", {"start": v(-1.04, -2.1) * mm, "end": v(-1.04, -2.2) * mm});
            skLineSegment(sketch, "E1278", {"start": v(-1.04, -2.2) * mm, "end": v(-1.04, -2.3) * mm});
            skLineSegment(sketch, "E1279", {"start": v(-1.04, -2.3) * mm, "end": v(-1.04, -2.37) * mm});
            skLineSegment(sketch, "E1280", {"start": v(-1.04, -2.37) * mm, "end": v(-1.04, -2.44) * mm});
            skLineSegment(sketch, "E1281", {"start": v(-1.04, -2.44) * mm, "end": v(-1.04, -2.5) * mm});
            skLineSegment(sketch, "E1282", {"start": v(-1.04, -2.5) * mm, "end": v(-1.04, -2.55) * mm});
            skLineSegment(sketch, "E1283", {"start": v(-1.04, -2.55) * mm, "end": v(-1.04, -2.6) * mm});
            skLineSegment(sketch, "E1284", {"start": v(-1.04, -2.6) * mm, "end": v(-1.04, -2.62) * mm});
            skLineSegment(sketch, "E1285", {"start": v(-1.04, -2.62) * mm, "end": v(-1.04, -2.64) * mm});
            skLineSegment(sketch, "E1286", {"start": v(-1.04, -2.64) * mm, "end": v(-1.04, -2.65) * mm});
            skLineSegment(sketch, "E1287", {"start": v(-1.04, -2.65) * mm, "end": v(-1.04, -2.65) * mm});
            skLineSegment(sketch, "E1288", {"start": v(-1.04, -2.65) * mm, "end": v(-1.04, -2.66) * mm});
            skLineSegment(sketch, "E1289", {"start": v(-1.04, -2.66) * mm, "end": v(-1.04, -2.66) * mm});
            skLineSegment(sketch, "E1290", {"start": v(-1.04, -2.66) * mm, "end": v(-1.04, -2.67) * mm});
            skLineSegment(sketch, "E1291", {"start": v(-1.04, -2.67) * mm, "end": v(-1.04, -2.67) * mm});
            skLineSegment(sketch, "E1292", {"start": v(-1.04, -2.67) * mm, "end": v(-1.04, -2.68) * mm});
            skLineSegment(sketch, "E1293", {"start": v(-1.04, -2.68) * mm, "end": v(-1.05, -2.68) * mm});
            skLineSegment(sketch, "E1294", {"start": v(-1.05, -2.68) * mm, "end": v(-1.05, -2.68) * mm});
            skLineSegment(sketch, "E1295", {"start": v(-1.05, -2.68) * mm, "end": v(-1.05, -2.69) * mm});
            skLineSegment(sketch, "E1296", {"start": v(-1.05, -2.69) * mm, "end": v(-1.05, -2.7) * mm});
            skLineSegment(sketch, "E1297", {"start": v(-1.05, -2.7) * mm, "end": v(-1.05, -2.7) * mm});
            skLineSegment(sketch, "E1298", {"start": v(-1.05, -2.7) * mm, "end": v(-1.05, -2.71) * mm});
            skLineSegment(sketch, "E1299", {"start": v(-1.05, -2.71) * mm, "end": v(-1.06, -2.72) * mm});
            skLineSegment(sketch, "E1300", {"start": v(-1.06, -2.72) * mm, "end": v(-1.06, -2.72) * mm});
            skLineSegment(sketch, "E1301", {"start": v(-1.06, -2.72) * mm, "end": v(-1.06, -2.73) * mm});
            skLineSegment(sketch, "E1302", {"start": v(-1.06, -2.73) * mm, "end": v(-1.06, -2.73) * mm});
            skLineSegment(sketch, "E1303", {"start": v(-1.06, -2.73) * mm, "end": v(-1.07, -2.74) * mm});
            skLineSegment(sketch, "E1304", {"start": v(-1.07, -2.74) * mm, "end": v(-1.07, -2.74) * mm});
            skLineSegment(sketch, "E1305", {"start": v(-1.07, -2.74) * mm, "end": v(-1.07, -2.75) * mm});
            skLineSegment(sketch, "E1306", {"start": v(-1.07, -2.75) * mm, "end": v(-1.07, -2.75) * mm});
            skLineSegment(sketch, "E1307", {"start": v(-1.07, -2.75) * mm, "end": v(-1.08, -2.75) * mm});
            skLineSegment(sketch, "E1308", {"start": v(-1.08, -2.75) * mm, "end": v(-1.08, -2.76) * mm});
            skLineSegment(sketch, "E1309", {"start": v(-1.08, -2.76) * mm, "end": v(-1.08, -2.76) * mm});
            skLineSegment(sketch, "E1310", {"start": v(-1.08, -2.76) * mm, "end": v(-1.08, -2.77) * mm});
            skLineSegment(sketch, "E1311", {"start": v(-1.08, -2.77) * mm, "end": v(-1.09, -2.77) * mm});
            skLineSegment(sketch, "E1312", {"start": v(-1.09, -2.77) * mm, "end": v(-1.1, -2.77) * mm});
            skLineSegment(sketch, "E1313", {"start": v(-1.1, -2.77) * mm, "end": v(-1.1, -2.78) * mm});
            skLineSegment(sketch, "E1314", {"start": v(-1.1, -2.78) * mm, "end": v(-1.1, -2.78) * mm});
            skLineSegment(sketch, "E1315", {"start": v(-1.1, -2.78) * mm, "end": v(-1.1, -2.79) * mm});
            skLineSegment(sketch, "E1316", {"start": v(-1.1, -2.79) * mm, "end": v(-1.1, -2.79) * mm});
            skLineSegment(sketch, "E1317", {"start": v(-1.1, -2.79) * mm, "end": v(-1.11, -2.8) * mm});
            skLineSegment(sketch, "E1318", {"start": v(-1.11, -2.8) * mm, "end": v(-1.12, -2.8) * mm});
            skLineSegment(sketch, "E1319", {"start": v(-1.12, -2.8) * mm, "end": v(-1.12, -2.8) * mm});
            skLineSegment(sketch, "E1320", {"start": v(-1.12, -2.8) * mm, "end": v(-1.13, -2.8) * mm});
            skLineSegment(sketch, "E1321", {"start": v(-1.13, -2.8) * mm, "end": v(-1.13, -2.8) * mm});
            skLineSegment(sketch, "E1322", {"start": v(-1.13, -2.8) * mm, "end": v(-1.14, -2.8) * mm});
            skLineSegment(sketch, "E1323", {"start": v(-1.14, -2.8) * mm, "end": v(-1.14, -2.8) * mm});
            skLineSegment(sketch, "E1324", {"start": v(-1.14, -2.8) * mm, "end": v(-1.15, -2.8) * mm});
            skLineSegment(sketch, "E1325", {"start": v(-1.15, -2.8) * mm, "end": v(-1.15, -2.81) * mm});
            skLineSegment(sketch, "E1326", {"start": v(-1.15, -2.81) * mm, "end": v(-1.16, -2.81) * mm});
            skLineSegment(sketch, "E1327", {"start": v(-1.16, -2.81) * mm, "end": v(-1.16, -2.81) * mm});
            skLineSegment(sketch, "E1328", {"start": v(-1.16, -2.81) * mm, "end": v(-1.17, -2.81) * mm});
            skLineSegment(sketch, "E1329", {"start": v(-1.17, -2.81) * mm, "end": v(-1.17, -2.81) * mm});
            skLineSegment(sketch, "E1330", {"start": v(-1.17, -2.81) * mm, "end": v(-1.18, -2.81) * mm});
            skLineSegment(sketch, "E1331", {"start": v(-1.18, -2.81) * mm, "end": v(-1.18, -2.81) * mm});
            skLineSegment(sketch, "E1332", {"start": v(-1.18, -2.81) * mm, "end": v(-1.19, -2.81) * mm});
            skLineSegment(sketch, "E1333", {"start": v(-1.19, -2.81) * mm, "end": v(-1.2, -2.81) * mm});
            skLineSegment(sketch, "E1334", {"start": v(-1.2, -2.81) * mm, "end": v(-1.2, -2.81) * mm});
            skLineSegment(sketch, "E1335", {"start": v(-1.2, -2.81) * mm, "end": v(-1.21, -2.81) * mm});
            skLineSegment(sketch, "E1336", {"start": v(-1.21, -2.81) * mm, "end": v(-1.22, -2.81) * mm});
            skLineSegment(sketch, "E1337", {"start": v(-1.22, -2.81) * mm, "end": v(-1.22, -2.8) * mm});
            skLineSegment(sketch, "E1338", {"start": v(-1.22, -2.8) * mm, "end": v(-1.23, -2.8) * mm});
            skLineSegment(sketch, "E1339", {"start": v(-1.23, -2.8) * mm, "end": v(-1.23, -2.8) * mm});
            skLineSegment(sketch, "E1340", {"start": v(-1.23, -2.8) * mm, "end": v(-1.24, -2.8) * mm});
            skLineSegment(sketch, "E1341", {"start": v(-1.24, -2.8) * mm, "end": v(-1.24, -2.8) * mm});
            skLineSegment(sketch, "E1342", {"start": v(-1.24, -2.8) * mm, "end": v(-1.25, -2.8) * mm});
            skLineSegment(sketch, "E1343", {"start": v(-1.25, -2.8) * mm, "end": v(-1.25, -2.8) * mm});
            skLineSegment(sketch, "E1344", {"start": v(-1.25, -2.8) * mm, "end": v(-1.26, -2.8) * mm});
            skLineSegment(sketch, "E1345", {"start": v(-1.26, -2.8) * mm, "end": v(-1.26, -2.8) * mm});
            skLineSegment(sketch, "E1346", {"start": v(-1.26, -2.8) * mm, "end": v(-1.27, -2.79) * mm});
            skLineSegment(sketch, "E1347", {"start": v(-1.27, -2.79) * mm, "end": v(-1.27, -2.79) * mm});
            skLineSegment(sketch, "E1348", {"start": v(-1.27, -2.79) * mm, "end": v(-1.27, -2.78) * mm});
            skLineSegment(sketch, "E1349", {"start": v(-1.27, -2.78) * mm, "end": v(-1.28, -2.78) * mm});
            skLineSegment(sketch, "E1350", {"start": v(-1.28, -2.78) * mm, "end": v(-1.28, -2.77) * mm});
            skLineSegment(sketch, "E1351", {"start": v(-1.28, -2.77) * mm, "end": v(-1.29, -2.77) * mm});
            skLineSegment(sketch, "E1352", {"start": v(-1.29, -2.77) * mm, "end": v(-1.3, -2.77) * mm});
            skLineSegment(sketch, "E1353", {"start": v(-1.3, -2.77) * mm, "end": v(-1.3, -2.76) * mm});
            skLineSegment(sketch, "E1354", {"start": v(-1.3, -2.76) * mm, "end": v(-1.3, -2.76) * mm});
            skLineSegment(sketch, "E1355", {"start": v(-1.3, -2.76) * mm, "end": v(-1.3, -2.75) * mm});
            skLineSegment(sketch, "E1356", {"start": v(-1.3, -2.75) * mm, "end": v(-1.3, -2.75) * mm});
            skLineSegment(sketch, "E1357", {"start": v(-1.3, -2.75) * mm, "end": v(-1.31, -2.74) * mm});
            skLineSegment(sketch, "E1358", {"start": v(-1.31, -2.74) * mm, "end": v(-1.32, -2.74) * mm});
            skLineSegment(sketch, "E1359", {"start": v(-1.32, -2.74) * mm, "end": v(-1.32, -2.73) * mm});
            skLineSegment(sketch, "E1360", {"start": v(-1.32, -2.73) * mm, "end": v(-1.32, -2.73) * mm});
            skLineSegment(sketch, "E1361", {"start": v(-1.32, -2.73) * mm, "end": v(-1.32, -2.72) * mm});
            skLineSegment(sketch, "E1362", {"start": v(-1.32, -2.72) * mm, "end": v(-1.33, -2.72) * mm});
            skLineSegment(sketch, "E1363", {"start": v(-1.33, -2.72) * mm, "end": v(-1.33, -2.71) * mm});
            skLineSegment(sketch, "E1364", {"start": v(-1.33, -2.71) * mm, "end": v(-1.33, -2.7) * mm});
            skLineSegment(sketch, "E1365", {"start": v(-1.33, -2.7) * mm, "end": v(-1.33, -2.7) * mm});
            skLineSegment(sketch, "E1366", {"start": v(-1.33, -2.7) * mm, "end": v(-1.34, -2.7) * mm});
            skLineSegment(sketch, "E1367", {"start": v(-1.34, -2.7) * mm, "end": v(-1.34, -2.7) * mm});
            skLineSegment(sketch, "E1368", {"start": v(-1.34, -2.7) * mm, "end": v(-1.34, -2.69) * mm});
            skLineSegment(sketch, "E1369", {"start": v(-1.34, -2.69) * mm, "end": v(-1.34, -2.68) * mm});
            skLineSegment(sketch, "E1370", {"start": v(-1.34, -2.68) * mm, "end": v(-1.34, -2.68) * mm});
            skLineSegment(sketch, "E1371", {"start": v(-1.34, -2.68) * mm, "end": v(-1.34, -2.67) * mm});
            skLineSegment(sketch, "E1372", {"start": v(-1.34, -2.67) * mm, "end": v(-1.34, -2.66) * mm});
            skLineSegment(sketch, "E1373", {"start": v(-1.34, -2.66) * mm, "end": v(-1.35, -2.66) * mm});
            skLineSegment(sketch, "E1374", {"start": v(-1.35, -2.66) * mm, "end": v(-1.35, -2.65) * mm});
            skLineSegment(sketch, "E1375", {"start": v(-1.35, -2.65) * mm, "end": v(-1.35, -2.65) * mm});
            skLineSegment(sketch, "E1376", {"start": v(-1.35, -2.65) * mm, "end": v(-1.35, -2.64) * mm});
            skLineSegment(sketch, "E1377", {"start": v(-1.35, -2.64) * mm, "end": v(-1.35, -2.64) * mm});
            skLineSegment(sketch, "E1378", {"start": v(-1.35, -2.64) * mm, "end": v(-1.35, -2.63) * mm});
            skLineSegment(sketch, "E1379", {"start": v(-1.35, -2.63) * mm, "end": v(-1.35, -2.63) * mm});
            skLineSegment(sketch, "E1380", {"start": v(-1.35, -2.63) * mm, "end": v(-1.35, -2.62) * mm});
            skLineSegment(sketch, "E1381", {"start": v(-1.35, -2.62) * mm, "end": v(-1.35, -2.6) * mm});
            skLineSegment(sketch, "E1382", {"start": v(-1.35, -2.6) * mm, "end": v(-1.35, -2.57) * mm});
            skLineSegment(sketch, "E1383", {"start": v(-1.35, -2.57) * mm, "end": v(-1.35, -2.53) * mm});
            skLineSegment(sketch, "E1384", {"start": v(-1.35, -2.53) * mm, "end": v(-1.35, -2.48) * mm});
            skLineSegment(sketch, "E1385", {"start": v(-1.35, -2.48) * mm, "end": v(-1.35, -2.42) * mm});
            skLineSegment(sketch, "E1386", {"start": v(-1.35, -2.42) * mm, "end": v(-1.35, -2.35) * mm});
            skLineSegment(sketch, "E1387", {"start": v(-1.35, -2.35) * mm, "end": v(-1.35, -2.27) * mm});
            skLineSegment(sketch, "E1388", {"start": v(-1.35, -2.27) * mm, "end": v(-1.35, -2.18) * mm});
            skLineSegment(sketch, "E1389", {"start": v(-1.35, -2.18) * mm, "end": v(-1.35, -2.08) * mm});
            skLineSegment(sketch, "E1390", {"start": v(-1.35, -2.08) * mm, "end": v(-1.35, -1.98) * mm});
            skLineSegment(sketch, "E1391", {"start": v(-1.35, -1.98) * mm, "end": v(-1.35, -1.87) * mm});
            skLineSegment(sketch, "E1392", {"start": v(-1.35, -1.87) * mm, "end": v(-1.35, -1.75) * mm});
            skLineSegment(sketch, "E1393", {"start": v(-1.35, -1.75) * mm, "end": v(-1.35, -1.63) * mm});
            skLineSegment(sketch, "E1394", {"start": v(-1.35, -1.63) * mm, "end": v(-1.35, -1.5) * mm});
            skLineSegment(sketch, "E1395", {"start": v(-1.35, -1.5) * mm, "end": v(-1.35, -1.37) * mm});
            skLineSegment(sketch, "E1396", {"start": v(-1.35, -1.37) * mm, "end": v(-1.35, -1.23) * mm});
            skLineSegment(sketch, "E1397", {"start": v(-1.35, -1.23) * mm, "end": v(-1.35, -1.09) * mm});
            skLineSegment(sketch, "E1398", {"start": v(-1.35, -1.09) * mm, "end": v(-1.35, -0.94) * mm});
            skLineSegment(sketch, "E1399", {"start": v(-1.35, -0.94) * mm, "end": v(-1.35, -0.8) * mm});
            skLineSegment(sketch, "E1400", {"start": v(-1.35, -0.8) * mm, "end": v(-1.35, -0.64) * mm});
            skLineSegment(sketch, "E1401", {"start": v(-1.35, -0.64) * mm, "end": v(-1.35, -0.49) * mm});
            skLineSegment(sketch, "E1402", {"start": v(-1.35, -0.49) * mm, "end": v(-1.35, -0.33) * mm});
            skLineSegment(sketch, "E1403", {"start": v(-1.35, -0.33) * mm, "end": v(-1.35, -0.18) * mm});
            skLineSegment(sketch, "E1404", {"start": v(-1.35, -0.18) * mm, "end": v(-1.35, -0.02) * mm});
            skLineSegment(sketch, "E1405", {"start": v(-1.35, -0.02) * mm, "end": v(-1.35, 0.13) * mm});
            skLineSegment(sketch, "E1406", {"start": v(-1.35, 0.13) * mm, "end": v(-1.35, 0.29) * mm});
            skLineSegment(sketch, "E1407", {"start": v(-1.35, 0.29) * mm, "end": v(-1.35, 0.44) * mm});
            skLineSegment(sketch, "E1408", {"start": v(-1.35, 0.44) * mm, "end": v(-1.35, 0.6) * mm});
            skLineSegment(sketch, "E1409", {"start": v(-1.35, 0.6) * mm, "end": v(-1.35, 0.75) * mm});
            skLineSegment(sketch, "E1410", {"start": v(-1.35, 0.75) * mm, "end": v(-1.35, 0.9) * mm});
            skLineSegment(sketch, "E1411", {"start": v(-1.35, 0.9) * mm, "end": v(-1.35, 1.04) * mm});
            skLineSegment(sketch, "E1412", {"start": v(-1.35, 1.04) * mm, "end": v(-1.35, 1.18) * mm});
            skLineSegment(sketch, "E1413", {"start": v(-1.35, 1.18) * mm, "end": v(-1.35, 1.32) * mm});
            skLineSegment(sketch, "E1414", {"start": v(-1.35, 1.32) * mm, "end": v(-1.35, 1.46) * mm});
            skLineSegment(sketch, "E1415", {"start": v(-1.35, 1.46) * mm, "end": v(-1.35, 1.59) * mm});
            skLineSegment(sketch, "E1416", {"start": v(-1.35, 1.59) * mm, "end": v(-1.35, 1.7) * mm});
            skLineSegment(sketch, "E1417", {"start": v(-1.35, 1.7) * mm, "end": v(-1.35, 1.83) * mm});
            skLineSegment(sketch, "E1418", {"start": v(-1.35, 1.83) * mm, "end": v(-1.35, 1.94) * mm});
            skLineSegment(sketch, "E1419", {"start": v(-1.35, 1.94) * mm, "end": v(-1.35, 2.04) * mm});
            skLineSegment(sketch, "E1420", {"start": v(-1.35, 2.04) * mm, "end": v(-1.35, 2.14) * mm});
            skLineSegment(sketch, "E1421", {"start": v(-1.35, 2.14) * mm, "end": v(-1.35, 2.22) * mm});
            skLineSegment(sketch, "E1422", {"start": v(-1.35, 2.22) * mm, "end": v(-1.35, 2.3) * mm});
            skLineSegment(sketch, "E1423", {"start": v(-1.35, 2.3) * mm, "end": v(-1.35, 2.37) * mm});
            skLineSegment(sketch, "E1424", {"start": v(-1.35, 2.37) * mm, "end": v(-1.35, 2.44) * mm});
            skLineSegment(sketch, "E1425", {"start": v(-1.35, 2.44) * mm, "end": v(-1.35, 2.49) * mm});
            skLineSegment(sketch, "E1426", {"start": v(-1.35, 2.49) * mm, "end": v(-1.35, 2.53) * mm});
            skLineSegment(sketch, "E1427", {"start": v(-1.35, 2.53) * mm, "end": v(-1.35, 2.56) * mm});
            skLineSegment(sketch, "E1428", {"start": v(-1.35, 2.56) * mm, "end": v(-1.35, 2.58) * mm});
            skLineSegment(sketch, "E1429", {"start": v(-1.35, 2.58) * mm, "end": v(-1.35, 2.58) * mm});
            skLineSegment(sketch, "E1430", {"start": v(-1.35, 2.58) * mm, "end": v(-1.35, 2.6) * mm});
            skLineSegment(sketch, "E1431", {"start": v(-1.35, 2.6) * mm, "end": v(-1.35, 2.63) * mm});
            skLineSegment(sketch, "E1432", {"start": v(-1.35, 2.63) * mm, "end": v(-1.35, 2.65) * mm});
            skLineSegment(sketch, "E1433", {"start": v(-1.35, 2.65) * mm, "end": v(-1.35, 2.67) * mm});
            skLineSegment(sketch, "E1434", {"start": v(-1.35, 2.67) * mm, "end": v(-1.36, 2.7) * mm});
            skLineSegment(sketch, "E1435", {"start": v(-1.36, 2.7) * mm, "end": v(-1.36, 2.72) * mm});
            skLineSegment(sketch, "E1436", {"start": v(-1.36, 2.72) * mm, "end": v(-1.37, 2.74) * mm});
            skLineSegment(sketch, "E1437", {"start": v(-1.37, 2.74) * mm, "end": v(-1.37, 2.76) * mm});
            skLineSegment(sketch, "E1438", {"start": v(-1.37, 2.76) * mm, "end": v(-1.38, 2.78) * mm});
            skLineSegment(sketch, "E1439", {"start": v(-1.38, 2.78) * mm, "end": v(-1.38, 2.8) * mm});
            skLineSegment(sketch, "E1440", {"start": v(-1.38, 2.8) * mm, "end": v(-1.39, 2.82) * mm});
            skLineSegment(sketch, "E1441", {"start": v(-1.39, 2.82) * mm, "end": v(-1.4, 2.84) * mm});
            skLineSegment(sketch, "E1442", {"start": v(-1.4, 2.84) * mm, "end": v(-1.4, 2.86) * mm});
            skLineSegment(sketch, "E1443", {"start": v(-1.4, 2.86) * mm, "end": v(-1.41, 2.87) * mm});
            skLineSegment(sketch, "E1444", {"start": v(-1.41, 2.87) * mm, "end": v(-1.42, 2.9) * mm});
            skLineSegment(sketch, "E1445", {"start": v(-1.42, 2.9) * mm, "end": v(-1.43, 2.9) * mm});
            skLineSegment(sketch, "E1446", {"start": v(-1.43, 2.9) * mm, "end": v(-1.44, 2.92) * mm});
            skLineSegment(sketch, "E1447", {"start": v(-1.44, 2.92) * mm, "end": v(-1.45, 2.94) * mm});
            skLineSegment(sketch, "E1448", {"start": v(-1.45, 2.94) * mm, "end": v(-1.46, 2.95) * mm});
            skLineSegment(sketch, "E1449", {"start": v(-1.46, 2.95) * mm, "end": v(-1.47, 2.97) * mm});
            skLineSegment(sketch, "E1450", {"start": v(-1.47, 2.97) * mm, "end": v(-1.48, 2.98) * mm});
            skLineSegment(sketch, "E1451", {"start": v(-1.48, 2.98) * mm, "end": v(-1.5, 3) * mm});
            skLineSegment(sketch, "E1452", {"start": v(-1.5, 3) * mm, "end": v(-1.5, 3.01) * mm});
            skLineSegment(sketch, "E1453", {"start": v(-1.5, 3.01) * mm, "end": v(-1.52, 3.03) * mm});
            skLineSegment(sketch, "E1454", {"start": v(-1.52, 3.03) * mm, "end": v(-1.53, 3.04) * mm});
            skLineSegment(sketch, "E1455", {"start": v(-1.53, 3.04) * mm, "end": v(-1.55, 3.05) * mm});
            skLineSegment(sketch, "E1456", {"start": v(-1.55, 3.05) * mm, "end": v(-1.56, 3.06) * mm});
            skLineSegment(sketch, "E1457", {"start": v(-1.56, 3.06) * mm, "end": v(-1.58, 3.07) * mm});
            skLineSegment(sketch, "E1458", {"start": v(-1.58, 3.07) * mm, "end": v(-1.6, 3.08) * mm});
            skLineSegment(sketch, "E1459", {"start": v(-1.6, 3.08) * mm, "end": v(-1.6, 3.1) * mm});
            skLineSegment(sketch, "E1460", {"start": v(-1.6, 3.1) * mm, "end": v(-1.62, 3.1) * mm});
            skLineSegment(sketch, "E1461", {"start": v(-1.62, 3.1) * mm, "end": v(-1.64, 3.11) * mm});
            skLineSegment(sketch, "E1462", {"start": v(-1.64, 3.11) * mm, "end": v(-1.66, 3.12) * mm});
            skLineSegment(sketch, "E1463", {"start": v(-1.66, 3.12) * mm, "end": v(-1.67, 3.13) * mm});
            skLineSegment(sketch, "E1464", {"start": v(-1.67, 3.13) * mm, "end": v(-1.7, 3.14) * mm});
            skLineSegment(sketch, "E1465", {"start": v(-1.7, 3.14) * mm, "end": v(-1.7, 3.14) * mm});
            skLineSegment(sketch, "E1466", {"start": v(-1.7, 3.14) * mm, "end": v(-1.73, 3.15) * mm});
            skLineSegment(sketch, "E1467", {"start": v(-1.73, 3.15) * mm, "end": v(-1.75, 3.16) * mm});
            skLineSegment(sketch, "E1468", {"start": v(-1.75, 3.16) * mm, "end": v(-1.76, 3.16) * mm});
            skLineSegment(sketch, "E1469", {"start": v(-1.76, 3.16) * mm, "end": v(-1.78, 3.17) * mm});
            skLineSegment(sketch, "E1470", {"start": v(-1.78, 3.17) * mm, "end": v(-1.8, 3.17) * mm});
            skLineSegment(sketch, "E1471", {"start": v(-1.8, 3.17) * mm, "end": v(-1.82, 3.18) * mm});
            skLineSegment(sketch, "E1472", {"start": v(-1.82, 3.18) * mm, "end": v(-1.84, 3.18) * mm});
            skLineSegment(sketch, "E1473", {"start": v(-1.84, 3.18) * mm, "end": v(-1.86, 3.18) * mm});
            skLineSegment(sketch, "E1474", {"start": v(-1.86, 3.18) * mm, "end": v(-1.88, 3.19) * mm});
            skLineSegment(sketch, "E1475", {"start": v(-1.88, 3.19) * mm, "end": v(-1.9, 3.19) * mm});
            skLineSegment(sketch, "E1476", {"start": v(-1.9, 3.19) * mm, "end": v(-1.92, 3.2) * mm});
            skLineSegment(sketch, "E1477", {"start": v(-1.92, 3.2) * mm, "end": v(-1.94, 3.2) * mm});
            skLineSegment(sketch, "E1478", {"start": v(-1.94, 3.2) * mm, "end": v(-1.96, 3.2) * mm});
            skLineSegment(sketch, "E1479", {"start": v(-1.96, 3.2) * mm, "end": v(-1.99, 3.2) * mm});
            skLineSegment(sketch, "E1480", {"start": v(-1.99, 3.2) * mm, "end": v(-2, 3.2) * mm});
            skLineSegment(sketch, "E1481", {"start": v(-2, 3.2) * mm, "end": v(-2.02, 3.2) * mm});
            skLineSegment(sketch, "E1482", {"start": v(-2.02, 3.2) * mm, "end": v(-2.04, 3.2) * mm});
            skLineSegment(sketch, "E1483", {"start": v(-2.04, 3.2) * mm, "end": v(-2.06, 3.19) * mm});
            skLineSegment(sketch, "E1484", {"start": v(-2.06, 3.19) * mm, "end": v(-2.08, 3.19) * mm});
            skLineSegment(sketch, "E1485", {"start": v(-2.08, 3.19) * mm, "end": v(-2.1, 3.18) * mm});
            skLineSegment(sketch, "E1486", {"start": v(-2.1, 3.18) * mm, "end": v(-2.11, 3.18) * mm});
            skLineSegment(sketch, "E1487", {"start": v(-2.11, 3.18) * mm, "end": v(-2.13, 3.18) * mm});
            skLineSegment(sketch, "E1488", {"start": v(-2.13, 3.18) * mm, "end": v(-2.15, 3.17) * mm});
            skLineSegment(sketch, "E1489", {"start": v(-2.15, 3.17) * mm, "end": v(-2.17, 3.17) * mm});
            skLineSegment(sketch, "E1490", {"start": v(-2.17, 3.17) * mm, "end": v(-2.18, 3.16) * mm});
            skLineSegment(sketch, "E1491", {"start": v(-2.18, 3.16) * mm, "end": v(-2.2, 3.16) * mm});
            skLineSegment(sketch, "E1492", {"start": v(-2.2, 3.16) * mm, "end": v(-2.22, 3.15) * mm});
            skLineSegment(sketch, "E1493", {"start": v(-2.22, 3.15) * mm, "end": v(-2.24, 3.14) * mm});
            skLineSegment(sketch, "E1494", {"start": v(-2.24, 3.14) * mm, "end": v(-2.25, 3.14) * mm});
            skLineSegment(sketch, "E1495", {"start": v(-2.25, 3.14) * mm, "end": v(-2.27, 3.13) * mm});
            skLineSegment(sketch, "E1496", {"start": v(-2.27, 3.13) * mm, "end": v(-2.29, 3.12) * mm});
            skLineSegment(sketch, "E1497", {"start": v(-2.29, 3.12) * mm, "end": v(-2.3, 3.11) * mm});
            skLineSegment(sketch, "E1498", {"start": v(-2.3, 3.11) * mm, "end": v(-2.32, 3.1) * mm});
            skLineSegment(sketch, "E1499", {"start": v(-2.32, 3.1) * mm, "end": v(-2.33, 3.1) * mm});
            skLineSegment(sketch, "E1500", {"start": v(-2.33, 3.1) * mm, "end": v(-2.35, 3.08) * mm});
            skLineSegment(sketch, "E1501", {"start": v(-2.35, 3.08) * mm, "end": v(-2.36, 3.07) * mm});
            skLineSegment(sketch, "E1502", {"start": v(-2.36, 3.07) * mm, "end": v(-2.38, 3.06) * mm});
            skLineSegment(sketch, "E1503", {"start": v(-2.38, 3.06) * mm, "end": v(-2.4, 3.04) * mm});
            skLineSegment(sketch, "E1504", {"start": v(-2.4, 3.04) * mm, "end": v(-2.4, 3.03) * mm});
            skLineSegment(sketch, "E1505", {"start": v(-2.4, 3.03) * mm, "end": v(-2.42, 3.02) * mm});
            skLineSegment(sketch, "E1506", {"start": v(-2.42, 3.02) * mm, "end": v(-2.43, 3) * mm});
            skLineSegment(sketch, "E1507", {"start": v(-2.43, 3) * mm, "end": v(-2.45, 3) * mm});
            skLineSegment(sketch, "E1508", {"start": v(-2.45, 3) * mm, "end": v(-2.46, 2.98) * mm});
            skLineSegment(sketch, "E1509", {"start": v(-2.46, 2.98) * mm, "end": v(-2.47, 2.96) * mm});
            skLineSegment(sketch, "E1510", {"start": v(-2.47, 2.96) * mm, "end": v(-2.48, 2.94) * mm});
            skLineSegment(sketch, "E1511", {"start": v(-2.48, 2.94) * mm, "end": v(-2.5, 2.93) * mm});
            skLineSegment(sketch, "E1512", {"start": v(-2.5, 2.93) * mm, "end": v(-2.5, 2.9) * mm});
            skLineSegment(sketch, "E1513", {"start": v(-2.5, 2.9) * mm, "end": v(-2.51, 2.9) * mm});
            skLineSegment(sketch, "E1514", {"start": v(-2.51, 2.9) * mm, "end": v(-2.52, 2.87) * mm});
            skLineSegment(sketch, "E1515", {"start": v(-2.52, 2.87) * mm, "end": v(-2.53, 2.86) * mm});
            skLineSegment(sketch, "E1516", {"start": v(-2.53, 2.86) * mm, "end": v(-2.54, 2.84) * mm});
            skLineSegment(sketch, "E1517", {"start": v(-2.54, 2.84) * mm, "end": v(-2.55, 2.82) * mm});
            skLineSegment(sketch, "E1518", {"start": v(-2.55, 2.82) * mm, "end": v(-2.56, 2.8) * mm});
            skLineSegment(sketch, "E1519", {"start": v(-2.56, 2.8) * mm, "end": v(-2.56, 2.77) * mm});
            skLineSegment(sketch, "E1520", {"start": v(-2.56, 2.77) * mm, "end": v(-2.57, 2.75) * mm});
            skLineSegment(sketch, "E1521", {"start": v(-2.57, 2.75) * mm, "end": v(-2.58, 2.73) * mm});
            skLineSegment(sketch, "E1522", {"start": v(-2.58, 2.73) * mm, "end": v(-2.58, 2.7) * mm});
            skLineSegment(sketch, "E1523", {"start": v(-2.58, 2.7) * mm, "end": v(-2.59, 2.69) * mm});
            skLineSegment(sketch, "E1524", {"start": v(-2.59, 2.69) * mm, "end": v(-2.59, 2.66) * mm});
            skLineSegment(sketch, "E1525", {"start": v(-2.59, 2.66) * mm, "end": v(-2.6, 2.64) * mm});
            skLineSegment(sketch, "E1526", {"start": v(-2.6, 2.64) * mm, "end": v(-2.6, 2.61) * mm});
            skLineSegment(sketch, "E1527", {"start": v(-2.6, 2.61) * mm, "end": v(-2.6, 2.59) * mm});
            skLineSegment(sketch, "E1528", {"start": v(-2.6, 2.59) * mm, "end": v(-2.6, 2.56) * mm});
            skLineSegment(sketch, "E1529", {"start": v(-2.6, 2.56) * mm, "end": v(-2.6, 2.53) * mm});
            skLineSegment(sketch, "E1530", {"start": v(-2.6, 2.53) * mm, "end": v(-2.6, 2.53) * mm});
            skLineSegment(sketch, "E1531", {"start": v(-2.6, 2.53) * mm, "end": v(-2.6, 2.5) * mm});
            skLineSegment(sketch, "E1532", {"start": v(-2.6, 2.5) * mm, "end": v(-2.6, 2.48) * mm});
            skLineSegment(sketch, "E1533", {"start": v(-2.6, 2.48) * mm, "end": v(-2.6, 2.43) * mm});
            skLineSegment(sketch, "E1534", {"start": v(-2.6, 2.43) * mm, "end": v(-2.6, 2.38) * mm});
            skLineSegment(sketch, "E1535", {"start": v(-2.6, 2.38) * mm, "end": v(-2.6, 2.32) * mm});
            skLineSegment(sketch, "E1536", {"start": v(-2.6, 2.32) * mm, "end": v(-2.6, 2.24) * mm});
            skLineSegment(sketch, "E1537", {"start": v(-2.6, 2.24) * mm, "end": v(-2.6, 2.16) * mm});
            skLineSegment(sketch, "E1538", {"start": v(-2.6, 2.16) * mm, "end": v(-2.6, 2.06) * mm});
            skLineSegment(sketch, "E1539", {"start": v(-2.6, 2.06) * mm, "end": v(-2.6, 1.96) * mm});
            skLineSegment(sketch, "E1540", {"start": v(-2.6, 1.96) * mm, "end": v(-2.6, 1.85) * mm});
            skLineSegment(sketch, "E1541", {"start": v(-2.6, 1.85) * mm, "end": v(-2.6, 1.73) * mm});
            skLineSegment(sketch, "E1542", {"start": v(-2.6, 1.73) * mm, "end": v(-2.6, 1.6) * mm});
            skLineSegment(sketch, "E1543", {"start": v(-2.6, 1.6) * mm, "end": v(-2.6, 1.48) * mm});
            skLineSegment(sketch, "E1544", {"start": v(-2.6, 1.48) * mm, "end": v(-2.6, 1.34) * mm});
            skLineSegment(sketch, "E1545", {"start": v(-2.6, 1.34) * mm, "end": v(-2.6, 1.2) * mm});
            skLineSegment(sketch, "E1546", {"start": v(-2.6, 1.2) * mm, "end": v(-2.6, 1.06) * mm});
            skLineSegment(sketch, "E1547", {"start": v(-2.6, 1.06) * mm, "end": v(-2.6, 0.9) * mm});
            skLineSegment(sketch, "E1548", {"start": v(-2.6, 0.9) * mm, "end": v(-2.6, 0.75) * mm});
            skLineSegment(sketch, "E1549", {"start": v(-2.6, 0.75) * mm, "end": v(-2.6, 0.6) * mm});
            skLineSegment(sketch, "E1550", {"start": v(-2.6, 0.6) * mm, "end": v(-2.6, 0.43) * mm});
            skLineSegment(sketch, "E1551", {"start": v(-2.6, 0.43) * mm, "end": v(-2.6, 0.27) * mm});
            skLineSegment(sketch, "E1552", {"start": v(-2.6, 0.27) * mm, "end": v(-2.6, 0.1) * mm});
            skLineSegment(sketch, "E1553", {"start": v(-2.6, 0.1) * mm, "end": v(-2.6, -0.06) * mm});
            skLineSegment(sketch, "E1554", {"start": v(-2.6, -0.06) * mm, "end": v(-2.6, -0.22) * mm});
            skLineSegment(sketch, "E1555", {"start": v(-2.6, -0.22) * mm, "end": v(-2.6, -0.39) * mm});
            skLineSegment(sketch, "E1556", {"start": v(-2.6, -0.39) * mm, "end": v(-2.6, -0.55) * mm});
            skLineSegment(sketch, "E1557", {"start": v(-2.6, -0.55) * mm, "end": v(-2.6, -0.72) * mm});
            skLineSegment(sketch, "E1558", {"start": v(-2.6, -0.72) * mm, "end": v(-2.6, -0.88) * mm});
            skLineSegment(sketch, "E1559", {"start": v(-2.6, -0.88) * mm, "end": v(-2.6, -1.04) * mm});
            skLineSegment(sketch, "E1560", {"start": v(-2.6, -1.04) * mm, "end": v(-2.6, -1.2) * mm});
            skLineSegment(sketch, "E1561", {"start": v(-2.6, -1.2) * mm, "end": v(-2.6, -1.35) * mm});
            skLineSegment(sketch, "E1562", {"start": v(-2.6, -1.35) * mm, "end": v(-2.6, -1.5) * mm});
            skLineSegment(sketch, "E1563", {"start": v(-2.6, -1.5) * mm, "end": v(-2.6, -1.65) * mm});
            skLineSegment(sketch, "E1564", {"start": v(-2.6, -1.65) * mm, "end": v(-2.6, -1.79) * mm});
            skLineSegment(sketch, "E1565", {"start": v(-2.6, -1.79) * mm, "end": v(-2.6, -1.92) * mm});
            skLineSegment(sketch, "E1566", {"start": v(-2.6, -1.92) * mm, "end": v(-2.6, -2.05) * mm});
            skLineSegment(sketch, "E1567", {"start": v(-2.6, -2.05) * mm, "end": v(-2.6, -2.18) * mm});
            skLineSegment(sketch, "E1568", {"start": v(-2.6, -2.18) * mm, "end": v(-2.6, -2.3) * mm});
            skLineSegment(sketch, "E1569", {"start": v(-2.6, -2.3) * mm, "end": v(-2.6, -2.4) * mm});
            skLineSegment(sketch, "E1570", {"start": v(-2.6, -2.4) * mm, "end": v(-2.6, -2.5) * mm});
            skLineSegment(sketch, "E1571", {"start": v(-2.6, -2.5) * mm, "end": v(-2.6, -2.6) * mm});
            skLineSegment(sketch, "E1572", {"start": v(-2.6, -2.6) * mm, "end": v(-2.6, -2.69) * mm});
            skLineSegment(sketch, "E1573", {"start": v(-2.6, -2.69) * mm, "end": v(-2.6, -2.76) * mm});
            skLineSegment(sketch, "E1574", {"start": v(-2.6, -2.76) * mm, "end": v(-2.6, -2.82) * mm});
            skLineSegment(sketch, "E1575", {"start": v(-2.6, -2.82) * mm, "end": v(-2.6, -2.88) * mm});
            skLineSegment(sketch, "E1576", {"start": v(-2.6, -2.88) * mm, "end": v(-2.6, -2.92) * mm});
            skLineSegment(sketch, "E1577", {"start": v(-2.6, -2.92) * mm, "end": v(-2.6, -2.95) * mm});
            skLineSegment(sketch, "E1578", {"start": v(-2.6, -2.95) * mm, "end": v(-2.6, -2.97) * mm});
            skLineSegment(sketch, "E1579", {"start": v(-2.6, -2.97) * mm, "end": v(-2.6, -2.98) * mm});
            skLineSegment(sketch, "E1580", {"start": v(-2.6, -2.98) * mm, "end": v(-2.6, -2.99) * mm});
            skLineSegment(sketch, "E1581", {"start": v(-2.6, -2.99) * mm, "end": v(-2.6, -3) * mm});
            skLineSegment(sketch, "E1582", {"start": v(-2.6, -3) * mm, "end": v(-2.6, -3) * mm});
            skLineSegment(sketch, "E1583", {"start": v(-2.6, -3) * mm, "end": v(-2.6, -3.01) * mm});
            skLineSegment(sketch, "E1584", {"start": v(-2.6, -3.01) * mm, "end": v(-2.6, -3.02) * mm});
            skLineSegment(sketch, "E1585", {"start": v(-2.6, -3.02) * mm, "end": v(-2.6, -3.03) * mm});
            skLineSegment(sketch, "E1586", {"start": v(-2.6, -3.03) * mm, "end": v(-2.6, -3.04) * mm});
            skLineSegment(sketch, "E1587", {"start": v(-2.6, -3.04) * mm, "end": v(-2.6, -3.04) * mm});
            skLineSegment(sketch, "E1588", {"start": v(-2.6, -3.04) * mm, "end": v(-2.59, -3.05) * mm});
            skLineSegment(sketch, "E1589", {"start": v(-2.59, -3.05) * mm, "end": v(-2.59, -3.06) * mm});
            skLineSegment(sketch, "E1590", {"start": v(-2.59, -3.06) * mm, "end": v(-2.58, -3.06) * mm});
            skLineSegment(sketch, "E1591", {"start": v(-2.58, -3.06) * mm, "end": v(-2.58, -3.07) * mm});
            skLineSegment(sketch, "E1592", {"start": v(-2.58, -3.07) * mm, "end": v(-2.58, -3.08) * mm});
            skLineSegment(sketch, "E1593", {"start": v(-2.58, -3.08) * mm, "end": v(-2.58, -3.09) * mm});
            skLineSegment(sketch, "E1594", {"start": v(-2.58, -3.09) * mm, "end": v(-2.57, -3.1) * mm});
            skLineSegment(sketch, "E1595", {"start": v(-2.57, -3.1) * mm, "end": v(-2.57, -3.1) * mm});
            skLineSegment(sketch, "E1596", {"start": v(-2.57, -3.1) * mm, "end": v(-2.56, -3.11) * mm});
            skLineSegment(sketch, "E1597", {"start": v(-2.56, -3.11) * mm, "end": v(-2.56, -3.12) * mm});
            skLineSegment(sketch, "E1598", {"start": v(-2.56, -3.12) * mm, "end": v(-2.56, -3.12) * mm});
            skLineSegment(sketch, "E1599", {"start": v(-2.56, -3.12) * mm, "end": v(-2.55, -3.13) * mm});
            skLineSegment(sketch, "E1600", {"start": v(-2.55, -3.13) * mm, "end": v(-2.55, -3.13) * mm});
            skLineSegment(sketch, "E1601", {"start": v(-2.55, -3.13) * mm, "end": v(-2.54, -3.14) * mm});
            skLineSegment(sketch, "E1602", {"start": v(-2.54, -3.14) * mm, "end": v(-2.54, -3.14) * mm});
            skLineSegment(sketch, "E1603", {"start": v(-2.54, -3.14) * mm, "end": v(-2.54, -3.15) * mm});
            skLineSegment(sketch, "E1604", {"start": v(-2.54, -3.15) * mm, "end": v(-2.53, -3.15) * mm});
            skLineSegment(sketch, "E1605", {"start": v(-2.53, -3.15) * mm, "end": v(-2.53, -3.16) * mm});
            skLineSegment(sketch, "E1606", {"start": v(-2.53, -3.16) * mm, "end": v(-2.52, -3.16) * mm});
            skLineSegment(sketch, "E1607", {"start": v(-2.52, -3.16) * mm, "end": v(-2.52, -3.17) * mm});
            skLineSegment(sketch, "E1608", {"start": v(-2.52, -3.17) * mm, "end": v(-2.51, -3.17) * mm});
            skLineSegment(sketch, "E1609", {"start": v(-2.51, -3.17) * mm, "end": v(-2.5, -3.18) * mm});
            skLineSegment(sketch, "E1610", {"start": v(-2.5, -3.18) * mm, "end": v(-2.5, -3.18) * mm});
            skLineSegment(sketch, "E1611", {"start": v(-2.5, -3.18) * mm, "end": v(-2.49, -3.19) * mm});
            skLineSegment(sketch, "E1612", {"start": v(-2.49, -3.19) * mm, "end": v(-2.48, -3.2) * mm});
            skLineSegment(sketch, "E1613", {"start": v(-2.48, -3.2) * mm, "end": v(-2.48, -3.2) * mm});
            skLineSegment(sketch, "E1614", {"start": v(-2.48, -3.2) * mm, "end": v(-2.47, -3.2) * mm});
            skLineSegment(sketch, "E1615", {"start": v(-2.47, -3.2) * mm, "end": v(-2.47, -3.2) * mm});
            skLineSegment(sketch, "E1616", {"start": v(-2.47, -3.2) * mm, "end": v(-2.46, -3.2) * mm});
            skLineSegment(sketch, "E1617", {"start": v(-2.46, -3.2) * mm, "end": v(-2.45, -3.2) * mm});
            skLineSegment(sketch, "E1618", {"start": v(-2.45, -3.2) * mm, "end": v(-2.45, -3.2) * mm});
            skLineSegment(sketch, "E1619", {"start": v(-2.45, -3.2) * mm, "end": v(-2.44, -3.2) * mm});
            skLineSegment(sketch, "E1620", {"start": v(-2.44, -3.2) * mm, "end": v(-2.43, -3.2) * mm});
            skLineSegment(sketch, "E1621", {"start": v(-2.43, -3.2) * mm, "end": v(-2.43, -3.21) * mm});
            skLineSegment(sketch, "E1622", {"start": v(-2.43, -3.21) * mm, "end": v(-2.42, -3.21) * mm});
            skLineSegment(sketch, "E1623", {"start": v(-2.42, -3.21) * mm, "end": v(-2.41, -3.21) * mm});
            skLineSegment(sketch, "E1624", {"start": v(-2.41, -3.21) * mm, "end": v(-2.4, -3.21) * mm});
            skLineSegment(sketch, "E1625", {"start": v(-2.4, -3.21) * mm, "end": v(-2.4, -3.21) * mm});
            skLineSegment(sketch, "E1626", {"start": v(-2.4, -3.21) * mm, "end": v(-2.39, -3.21) * mm});
            skLineSegment(sketch, "E1627", {"start": v(-2.39, -3.21) * mm, "end": v(-2.38, -3.21) * mm});
            skLineSegment(sketch, "E1628", {"start": v(-2.38, -3.21) * mm, "end": v(-2.37, -3.21) * mm});
            skLineSegment(sketch, "E1629", {"start": v(-2.37, -3.21) * mm, "end": v(-2.36, -3.21) * mm});
            skLineSegment(sketch, "E1630", {"start": v(-2.36, -3.21) * mm, "end": v(-2.35, -3.21) * mm});
            skLineSegment(sketch, "E1631", {"start": v(-2.35, -3.21) * mm, "end": v(-2.34, -3.21) * mm});
            skLineSegment(sketch, "E1632", {"start": v(-2.34, -3.21) * mm, "end": v(-2.34, -3.21) * mm});
            skLineSegment(sketch, "E1633", {"start": v(-2.34, -3.21) * mm, "end": v(-2.33, -3.2) * mm});
            skLineSegment(sketch, "E1634", {"start": v(-2.33, -3.2) * mm, "end": v(-2.32, -3.2) * mm});
            skLineSegment(sketch, "E1635", {"start": v(-2.32, -3.2) * mm, "end": v(-2.31, -3.2) * mm});
            skLineSegment(sketch, "E1636", {"start": v(-2.31, -3.2) * mm, "end": v(-2.3, -3.2) * mm});
            skLineSegment(sketch, "E1637", {"start": v(-2.3, -3.2) * mm, "end": v(-2.3, -3.2) * mm});
            skLineSegment(sketch, "E1638", {"start": v(-2.3, -3.2) * mm, "end": v(-2.29, -3.2) * mm});
            skLineSegment(sketch, "E1639", {"start": v(-2.29, -3.2) * mm, "end": v(-2.28, -3.2) * mm});
            skLineSegment(sketch, "E1640", {"start": v(-2.28, -3.2) * mm, "end": v(-2.27, -3.19) * mm});
            skLineSegment(sketch, "E1641", {"start": v(-2.27, -3.19) * mm, "end": v(-2.27, -3.19) * mm});
            skLineSegment(sketch, "E1642", {"start": v(-2.27, -3.19) * mm, "end": v(-2.26, -3.18) * mm});
            skLineSegment(sketch, "E1643", {"start": v(-2.26, -3.18) * mm, "end": v(-2.25, -3.18) * mm});
            skLineSegment(sketch, "E1644", {"start": v(-2.25, -3.18) * mm, "end": v(-2.25, -3.18) * mm});
            skLineSegment(sketch, "E1645", {"start": v(-2.25, -3.18) * mm, "end": v(-2.24, -3.17) * mm});
            skLineSegment(sketch, "E1646", {"start": v(-2.24, -3.17) * mm, "end": v(-2.24, -3.17) * mm});
            skLineSegment(sketch, "E1647", {"start": v(-2.24, -3.17) * mm, "end": v(-2.23, -3.16) * mm});
            skLineSegment(sketch, "E1648", {"start": v(-2.23, -3.16) * mm, "end": v(-2.23, -3.16) * mm});
            skLineSegment(sketch, "E1649", {"start": v(-2.23, -3.16) * mm, "end": v(-2.22, -3.15) * mm});
            skLineSegment(sketch, "E1650", {"start": v(-2.22, -3.15) * mm, "end": v(-2.21, -3.15) * mm});
            skLineSegment(sketch, "E1651", {"start": v(-2.21, -3.15) * mm, "end": v(-2.2, -3.14) * mm});
            skLineSegment(sketch, "E1652", {"start": v(-2.2, -3.14) * mm, "end": v(-2.2, -3.14) * mm});
            skLineSegment(sketch, "E1653", {"start": v(-2.2, -3.14) * mm, "end": v(-2.2, -3.13) * mm});
            skLineSegment(sketch, "E1654", {"start": v(-2.2, -3.13) * mm, "end": v(-2.2, -3.12) * mm});
            skLineSegment(sketch, "E1655", {"start": v(-2.2, -3.12) * mm, "end": v(-2.2, -3.12) * mm});
            skLineSegment(sketch, "E1656", {"start": v(-2.2, -3.12) * mm, "end": v(-2.19, -3.11) * mm});
            skLineSegment(sketch, "E1657", {"start": v(-2.19, -3.11) * mm, "end": v(-2.18, -3.1) * mm});
            skLineSegment(sketch, "E1658", {"start": v(-2.18, -3.1) * mm, "end": v(-2.18, -3.1) * mm});
            skLineSegment(sketch, "E1659", {"start": v(-2.18, -3.1) * mm, "end": v(-2.17, -3.08) * mm});
            skLineSegment(sketch, "E1660", {"start": v(-2.17, -3.08) * mm, "end": v(-2.17, -3.08) * mm});
            skLineSegment(sketch, "E1661", {"start": v(-2.17, -3.08) * mm, "end": v(-2.17, -3.07) * mm});
            skLineSegment(sketch, "E1662", {"start": v(-2.17, -3.07) * mm, "end": v(-2.17, -3.06) * mm});
            skLineSegment(sketch, "E1663", {"start": v(-2.17, -3.06) * mm, "end": v(-2.16, -3.05) * mm});
            skLineSegment(sketch, "E1664", {"start": v(-2.16, -3.05) * mm, "end": v(-2.16, -3.05) * mm});
            skLineSegment(sketch, "E1665", {"start": v(-2.16, -3.05) * mm, "end": v(-2.16, -3.04) * mm});
            skLineSegment(sketch, "E1666", {"start": v(-2.16, -3.04) * mm, "end": v(-2.16, -3.03) * mm});
            skLineSegment(sketch, "E1667", {"start": v(-2.16, -3.03) * mm, "end": v(-2.16, -3.02) * mm});
            skLineSegment(sketch, "E1668", {"start": v(-2.16, -3.02) * mm, "end": v(-2.15, -3.01) * mm});
            skLineSegment(sketch, "E1669", {"start": v(-2.15, -3.01) * mm, "end": v(-2.15, -3) * mm});
            skLineSegment(sketch, "E1670", {"start": v(-2.15, -3) * mm, "end": v(-2.15, -3) * mm});
            skLineSegment(sketch, "E1671", {"start": v(-2.15, -3) * mm, "end": v(-2.15, -2.98) * mm});
            skLineSegment(sketch, "E1672", {"start": v(-2.15, -2.98) * mm, "end": v(-2.15, -2.97) * mm});
            skLineSegment(sketch, "E1673", {"start": v(-2.15, -2.97) * mm, "end": v(-2.15, -2.97) * mm});
            skLineSegment(sketch, "E1674", {"start": v(-2.15, -2.97) * mm, "end": v(-2.15, -2.96) * mm});
            skLineSegment(sketch, "E1675", {"start": v(-2.15, -2.96) * mm, "end": v(-2.15, -2.95) * mm});
            skLineSegment(sketch, "E1676", {"start": v(-2.15, -2.95) * mm, "end": v(-2.15, -2.93) * mm});
            skLineSegment(sketch, "E1677", {"start": v(-2.15, -2.93) * mm, "end": v(-2.15, -2.9) * mm});
            skLineSegment(sketch, "E1678", {"start": v(-2.15, -2.9) * mm, "end": v(-2.15, -2.86) * mm});
            skLineSegment(sketch, "E1679", {"start": v(-2.15, -2.86) * mm, "end": v(-2.15, -2.8) * mm});
            skLineSegment(sketch, "E1680", {"start": v(-2.15, -2.8) * mm, "end": v(-2.15, -2.74) * mm});
            skLineSegment(sketch, "E1681", {"start": v(-2.15, -2.74) * mm, "end": v(-2.15, -2.66) * mm});
            skLineSegment(sketch, "E1682", {"start": v(-2.15, -2.66) * mm, "end": v(-2.15, -2.58) * mm});
            skLineSegment(sketch, "E1683", {"start": v(-2.15, -2.58) * mm, "end": v(-2.15, -2.48) * mm});
            skLineSegment(sketch, "E1684", {"start": v(-2.15, -2.48) * mm, "end": v(-2.15, -2.38) * mm});
            skLineSegment(sketch, "E1685", {"start": v(-2.15, -2.38) * mm, "end": v(-2.15, -2.27) * mm});
            skLineSegment(sketch, "E1686", {"start": v(-2.15, -2.27) * mm, "end": v(-2.15, -2.16) * mm});
            skLineSegment(sketch, "E1687", {"start": v(-2.15, -2.16) * mm, "end": v(-2.15, -2.03) * mm});
            skLineSegment(sketch, "E1688", {"start": v(-2.15, -2.03) * mm, "end": v(-2.15, -1.9) * mm});
            skLineSegment(sketch, "E1689", {"start": v(-2.15, -1.9) * mm, "end": v(-2.15, -1.76) * mm});
            skLineSegment(sketch, "E1690", {"start": v(-2.15, -1.76) * mm, "end": v(-2.15, -1.62) * mm});
            skLineSegment(sketch, "E1691", {"start": v(-2.15, -1.62) * mm, "end": v(-2.15, -1.48) * mm});
            skLineSegment(sketch, "E1692", {"start": v(-2.15, -1.48) * mm, "end": v(-2.15, -1.33) * mm});
            skLineSegment(sketch, "E1693", {"start": v(-2.15, -1.33) * mm, "end": v(-2.15, -1.17) * mm});
            skLineSegment(sketch, "E1694", {"start": v(-2.15, -1.17) * mm, "end": v(-2.15, -1.01) * mm});
            skLineSegment(sketch, "E1695", {"start": v(-2.15, -1.01) * mm, "end": v(-2.15, -0.85) * mm});
            skLineSegment(sketch, "E1696", {"start": v(-2.15, -0.85) * mm, "end": v(-2.15, -0.7) * mm});
            skLineSegment(sketch, "E1697", {"start": v(-2.15, -0.7) * mm, "end": v(-2.15, -0.53) * mm});
            skLineSegment(sketch, "E1698", {"start": v(-2.15, -0.53) * mm, "end": v(-2.15, -0.36) * mm});
            skLineSegment(sketch, "E1699", {"start": v(-2.15, -0.36) * mm, "end": v(-2.15, -0.2) * mm});
            skLineSegment(sketch, "E1700", {"start": v(-2.15, -0.2) * mm, "end": v(-2.15, -0.03) * mm});
            skLineSegment(sketch, "E1701", {"start": v(-2.15, -0.03) * mm, "end": v(-2.15, 0.13) * mm});
            skLineSegment(sketch, "E1702", {"start": v(-2.15, 0.13) * mm, "end": v(-2.15, 0.3) * mm});
            skLineSegment(sketch, "E1703", {"start": v(-2.15, 0.3) * mm, "end": v(-2.15, 0.46) * mm});
            skLineSegment(sketch, "E1704", {"start": v(-2.15, 0.46) * mm, "end": v(-2.15, 0.62) * mm});
            skLineSegment(sketch, "E1705", {"start": v(-2.15, 0.62) * mm, "end": v(-2.15, 0.77) * mm});
            skLineSegment(sketch, "E1706", {"start": v(-2.15, 0.77) * mm, "end": v(-2.15, 0.93) * mm});
            skLineSegment(sketch, "E1707", {"start": v(-2.15, 0.93) * mm, "end": v(-2.15, 1.08) * mm});
            skLineSegment(sketch, "E1708", {"start": v(-2.15, 1.08) * mm, "end": v(-2.15, 1.23) * mm});
            skLineSegment(sketch, "E1709", {"start": v(-2.15, 1.23) * mm, "end": v(-2.15, 1.37) * mm});
            skLineSegment(sketch, "E1710", {"start": v(-2.15, 1.37) * mm, "end": v(-2.15, 1.5) * mm});
            skLineSegment(sketch, "E1711", {"start": v(-2.15, 1.5) * mm, "end": v(-2.15, 1.63) * mm});
            skLineSegment(sketch, "E1712", {"start": v(-2.15, 1.63) * mm, "end": v(-2.15, 1.76) * mm});
            skLineSegment(sketch, "E1713", {"start": v(-2.15, 1.76) * mm, "end": v(-2.15, 1.87) * mm});
            skLineSegment(sketch, "E1714", {"start": v(-2.15, 1.87) * mm, "end": v(-2.15, 1.98) * mm});
            skLineSegment(sketch, "E1715", {"start": v(-2.15, 1.98) * mm, "end": v(-2.15, 2.09) * mm});
            skLineSegment(sketch, "E1716", {"start": v(-2.15, 2.09) * mm, "end": v(-2.15, 2.18) * mm});
            skLineSegment(sketch, "E1717", {"start": v(-2.15, 2.18) * mm, "end": v(-2.15, 2.26) * mm});
            skLineSegment(sketch, "E1718", {"start": v(-2.15, 2.26) * mm, "end": v(-2.15, 2.34) * mm});
            skLineSegment(sketch, "E1719", {"start": v(-2.15, 2.34) * mm, "end": v(-2.15, 2.4) * mm});
            skLineSegment(sketch, "E1720", {"start": v(-2.15, 2.4) * mm, "end": v(-2.15, 2.46) * mm});
            skLineSegment(sketch, "E1721", {"start": v(-2.15, 2.46) * mm, "end": v(-2.15, 2.5) * mm});
            skLineSegment(sketch, "E1722", {"start": v(-2.15, 2.5) * mm, "end": v(-2.15, 2.53) * mm});
            skLineSegment(sketch, "E1723", {"start": v(-2.15, 2.53) * mm, "end": v(-2.15, 2.55) * mm});
            skLineSegment(sketch, "E1724", {"start": v(-2.15, 2.55) * mm, "end": v(-2.15, 2.56) * mm});
            skLineSegment(sketch, "E1725", {"start": v(-2.15, 2.56) * mm, "end": v(-2.15, 2.56) * mm});
            skLineSegment(sketch, "E1726", {"start": v(-2.15, 2.56) * mm, "end": v(-2.15, 2.57) * mm});
            skLineSegment(sketch, "E1727", {"start": v(-2.15, 2.57) * mm, "end": v(-2.15, 2.57) * mm});
            skLineSegment(sketch, "E1728", {"start": v(-2.15, 2.57) * mm, "end": v(-2.15, 2.58) * mm});
            skLineSegment(sketch, "E1729", {"start": v(-2.15, 2.58) * mm, "end": v(-2.15, 2.58) * mm});
            skLineSegment(sketch, "E1730", {"start": v(-2.15, 2.58) * mm, "end": v(-2.15, 2.59) * mm});
            skLineSegment(sketch, "E1731", {"start": v(-2.15, 2.59) * mm, "end": v(-2.15, 2.6) * mm});
            skLineSegment(sketch, "E1732", {"start": v(-2.15, 2.6) * mm, "end": v(-2.14, 2.6) * mm});
            skLineSegment(sketch, "E1733", {"start": v(-2.14, 2.6) * mm, "end": v(-2.14, 2.6) * mm});
            skLineSegment(sketch, "E1734", {"start": v(-2.14, 2.6) * mm, "end": v(-2.14, 2.61) * mm});
            skLineSegment(sketch, "E1735", {"start": v(-2.14, 2.61) * mm, "end": v(-2.14, 2.62) * mm});
            skLineSegment(sketch, "E1736", {"start": v(-2.14, 2.62) * mm, "end": v(-2.14, 2.62) * mm});
            skLineSegment(sketch, "E1737", {"start": v(-2.14, 2.62) * mm, "end": v(-2.13, 2.63) * mm});
            skLineSegment(sketch, "E1738", {"start": v(-2.13, 2.63) * mm, "end": v(-2.13, 2.63) * mm});
            skLineSegment(sketch, "E1739", {"start": v(-2.13, 2.63) * mm, "end": v(-2.13, 2.64) * mm});
            skLineSegment(sketch, "E1740", {"start": v(-2.13, 2.64) * mm, "end": v(-2.12, 2.64) * mm});
            skLineSegment(sketch, "E1741", {"start": v(-2.12, 2.64) * mm, "end": v(-2.12, 2.64) * mm});
            skLineSegment(sketch, "E1742", {"start": v(-2.12, 2.64) * mm, "end": v(-2.12, 2.65) * mm});
            skLineSegment(sketch, "E1743", {"start": v(-2.12, 2.65) * mm, "end": v(-2.12, 2.65) * mm});
            skLineSegment(sketch, "E1744", {"start": v(-2.12, 2.65) * mm, "end": v(-2.11, 2.65) * mm});
            skLineSegment(sketch, "E1745", {"start": v(-2.11, 2.65) * mm, "end": v(-2.1, 2.66) * mm});
            skLineSegment(sketch, "E1746", {"start": v(-2.1, 2.66) * mm, "end": v(-2.1, 2.66) * mm});
            skLineSegment(sketch, "E1747", {"start": v(-2.1, 2.66) * mm, "end": v(-2.1, 2.67) * mm});
            skLineSegment(sketch, "E1748", {"start": v(-2.1, 2.67) * mm, "end": v(-2.1, 2.67) * mm});
            skLineSegment(sketch, "E1749", {"start": v(-2.1, 2.67) * mm, "end": v(-2.09, 2.67) * mm});
            skLineSegment(sketch, "E1750", {"start": v(-2.09, 2.67) * mm, "end": v(-2.08, 2.68) * mm});
            skLineSegment(sketch, "E1751", {"start": v(-2.08, 2.68) * mm, "end": v(-2.08, 2.68) * mm});
            skLineSegment(sketch, "E1752", {"start": v(-2.08, 2.68) * mm, "end": v(-2.07, 2.68) * mm});
            skLineSegment(sketch, "E1753", {"start": v(-2.07, 2.68) * mm, "end": v(-2.07, 2.68) * mm});
            skLineSegment(sketch, "E1754", {"start": v(-2.07, 2.68) * mm, "end": v(-2.06, 2.69) * mm});
            skLineSegment(sketch, "E1755", {"start": v(-2.06, 2.69) * mm, "end": v(-2.06, 2.69) * mm});
            skLineSegment(sketch, "E1756", {"start": v(-2.06, 2.69) * mm, "end": v(-2.05, 2.69) * mm});
            skLineSegment(sketch, "E1757", {"start": v(-2.05, 2.69) * mm, "end": v(-2.05, 2.7) * mm});
            skLineSegment(sketch, "E1758", {"start": v(-2.05, 2.7) * mm, "end": v(-2.04, 2.7) * mm});
            skLineSegment(sketch, "E1759", {"start": v(-2.04, 2.7) * mm, "end": v(-2.04, 2.7) * mm});
            skLineSegment(sketch, "E1760", {"start": v(-2.04, 2.7) * mm, "end": v(-2.03, 2.7) * mm});
            skLineSegment(sketch, "E1761", {"start": v(-2.03, 2.7) * mm, "end": v(-2.03, 2.7) * mm});
            skLineSegment(sketch, "E1762", {"start": v(-2.03, 2.7) * mm, "end": v(-2.02, 2.7) * mm});
            skLineSegment(sketch, "E1763", {"start": v(-2.02, 2.7) * mm, "end": v(-2.02, 2.7) * mm});
            skLineSegment(sketch, "E1764", {"start": v(-2.02, 2.7) * mm, "end": v(-2.01, 2.7) * mm});
            skLineSegment(sketch, "E1765", {"start": v(-2.01, 2.7) * mm, "end": v(-2, 2.7) * mm});
            skLineSegment(sketch, "E1766", {"start": v(-2, 2.7) * mm, "end": v(-2, 2.7) * mm});
            skLineSegment(sketch, "E1767", {"start": v(-2, 2.7) * mm, "end": v(-1.99, 2.7) * mm});
            skLineSegment(sketch, "E1768", {"start": v(-1.99, 2.7) * mm, "end": v(-1.98, 2.7) * mm});
            skLineSegment(sketch, "E1769", {"start": v(-1.98, 2.7) * mm, "end": v(-1.97, 2.7) * mm});
            skLineSegment(sketch, "E1770", {"start": v(-1.97, 2.7) * mm, "end": v(-1.97, 2.7) * mm});
            skLineSegment(sketch, "E1771", {"start": v(-1.97, 2.7) * mm, "end": v(-1.96, 2.7) * mm});
            skLineSegment(sketch, "E1772", {"start": v(-1.96, 2.7) * mm, "end": v(-1.96, 2.7) * mm});
            skLineSegment(sketch, "E1773", {"start": v(-1.96, 2.7) * mm, "end": v(-1.95, 2.7) * mm});
            skLineSegment(sketch, "E1774", {"start": v(-1.95, 2.7) * mm, "end": v(-1.95, 2.7) * mm});
            skLineSegment(sketch, "E1775", {"start": v(-1.95, 2.7) * mm, "end": v(-1.94, 2.7) * mm});
            skLineSegment(sketch, "E1776", {"start": v(-1.94, 2.7) * mm, "end": v(-1.94, 2.7) * mm});
            skLineSegment(sketch, "E1777", {"start": v(-1.94, 2.7) * mm, "end": v(-1.93, 2.7) * mm});
            skLineSegment(sketch, "E1778", {"start": v(-1.93, 2.7) * mm, "end": v(-1.93, 2.7) * mm});
            skLineSegment(sketch, "E1779", {"start": v(-1.93, 2.7) * mm, "end": v(-1.92, 2.7) * mm});
            skLineSegment(sketch, "E1780", {"start": v(-1.92, 2.7) * mm, "end": v(-1.92, 2.69) * mm});
            skLineSegment(sketch, "E1781", {"start": v(-1.92, 2.69) * mm, "end": v(-1.91, 2.69) * mm});
            skLineSegment(sketch, "E1782", {"start": v(-1.91, 2.69) * mm, "end": v(-1.9, 2.69) * mm});
            skLineSegment(sketch, "E1783", {"start": v(-1.9, 2.69) * mm, "end": v(-1.9, 2.68) * mm});
            skLineSegment(sketch, "E1784", {"start": v(-1.9, 2.68) * mm, "end": v(-1.9, 2.68) * mm});
            skLineSegment(sketch, "E1785", {"start": v(-1.9, 2.68) * mm, "end": v(-1.89, 2.68) * mm});
            skLineSegment(sketch, "E1786", {"start": v(-1.89, 2.68) * mm, "end": v(-1.88, 2.67) * mm});
            skLineSegment(sketch, "E1787", {"start": v(-1.88, 2.67) * mm, "end": v(-1.88, 2.67) * mm});
            skLineSegment(sketch, "E1788", {"start": v(-1.88, 2.67) * mm, "end": v(-1.87, 2.67) * mm});
            skLineSegment(sketch, "E1789", {"start": v(-1.87, 2.67) * mm, "end": v(-1.87, 2.67) * mm});
            skLineSegment(sketch, "E1790", {"start": v(-1.87, 2.67) * mm, "end": v(-1.87, 2.66) * mm});
            skLineSegment(sketch, "E1791", {"start": v(-1.87, 2.66) * mm, "end": v(-1.86, 2.66) * mm});
            skLineSegment(sketch, "E1792", {"start": v(-1.86, 2.66) * mm, "end": v(-1.86, 2.66) * mm});
            skLineSegment(sketch, "E1793", {"start": v(-1.86, 2.66) * mm, "end": v(-1.86, 2.65) * mm});
            skLineSegment(sketch, "E1794", {"start": v(-1.86, 2.65) * mm, "end": v(-1.85, 2.65) * mm});
            skLineSegment(sketch, "E1795", {"start": v(-1.85, 2.65) * mm, "end": v(-1.85, 2.65) * mm});
            skLineSegment(sketch, "E1796", {"start": v(-1.85, 2.65) * mm, "end": v(-1.85, 2.64) * mm});
            skLineSegment(sketch, "E1797", {"start": v(-1.85, 2.64) * mm, "end": v(-1.85, 2.64) * mm});
            skLineSegment(sketch, "E1798", {"start": v(-1.85, 2.64) * mm, "end": v(-1.84, 2.64) * mm});
            skLineSegment(sketch, "E1799", {"start": v(-1.84, 2.64) * mm, "end": v(-1.84, 2.63) * mm});
            skLineSegment(sketch, "E1800", {"start": v(-1.84, 2.63) * mm, "end": v(-1.84, 2.63) * mm});
            skLineSegment(sketch, "E1801", {"start": v(-1.84, 2.63) * mm, "end": v(-1.83, 2.62) * mm});
            skLineSegment(sketch, "E1802", {"start": v(-1.83, 2.62) * mm, "end": v(-1.83, 2.62) * mm});
            skLineSegment(sketch, "E1803", {"start": v(-1.83, 2.62) * mm, "end": v(-1.83, 2.61) * mm});
            skLineSegment(sketch, "E1804", {"start": v(-1.83, 2.61) * mm, "end": v(-1.83, 2.6) * mm});
            skLineSegment(sketch, "E1805", {"start": v(-1.83, 2.6) * mm, "end": v(-1.83, 2.6) * mm});
            skLineSegment(sketch, "E1806", {"start": v(-1.83, 2.6) * mm, "end": v(-1.82, 2.6) * mm});
            skLineSegment(sketch, "E1807", {"start": v(-1.82, 2.6) * mm, "end": v(-1.82, 2.59) * mm});
            skLineSegment(sketch, "E1808", {"start": v(-1.82, 2.59) * mm, "end": v(-1.82, 2.58) * mm});
            skLineSegment(sketch, "E1809", {"start": v(-1.82, 2.58) * mm, "end": v(-1.82, 2.58) * mm});
            skLineSegment(sketch, "E1810", {"start": v(-1.82, 2.58) * mm, "end": v(-1.82, 2.57) * mm});
            skLineSegment(sketch, "E1811", {"start": v(-1.82, 2.57) * mm, "end": v(-1.82, 2.57) * mm});
            skLineSegment(sketch, "E1812", {"start": v(-1.82, 2.57) * mm, "end": v(-1.82, 2.56) * mm});
            skLineSegment(sketch, "E1813", {"start": v(-1.82, 2.56) * mm, "end": v(-1.82, 2.56) * mm});
            skLineSegment(sketch, "E1814", {"start": v(-1.82, 2.56) * mm, "end": v(-1.82, 2.55) * mm});
            skLineSegment(sketch, "E1815", {"start": v(-1.82, 2.55) * mm, "end": v(-1.82, 2.53) * mm});
            skLineSegment(sketch, "E1816", {"start": v(-1.82, 2.53) * mm, "end": v(-1.82, 2.5) * mm});
            skLineSegment(sketch, "E1817", {"start": v(-1.82, 2.5) * mm, "end": v(-1.82, 2.46) * mm});
            skLineSegment(sketch, "E1818", {"start": v(-1.82, 2.46) * mm, "end": v(-1.82, 2.41) * mm});
            skLineSegment(sketch, "E1819", {"start": v(-1.82, 2.41) * mm, "end": v(-1.82, 2.35) * mm});
            skLineSegment(sketch, "E1820", {"start": v(-1.82, 2.35) * mm, "end": v(-1.82, 2.28) * mm});
            skLineSegment(sketch, "E1821", {"start": v(-1.82, 2.28) * mm, "end": v(-1.82, 2.2) * mm});
            skLineSegment(sketch, "E1822", {"start": v(-1.82, 2.2) * mm, "end": v(-1.82, 2.11) * mm});
            skLineSegment(sketch, "E1823", {"start": v(-1.82, 2.11) * mm, "end": v(-1.82, 2.02) * mm});
            skLineSegment(sketch, "E1824", {"start": v(-1.82, 2.02) * mm, "end": v(-1.82, 1.91) * mm});
            skLineSegment(sketch, "E1825", {"start": v(-1.82, 1.91) * mm, "end": v(-1.82, 1.8) * mm});
            skLineSegment(sketch, "E1826", {"start": v(-1.82, 1.8) * mm, "end": v(-1.82, 1.68) * mm});
            skLineSegment(sketch, "E1827", {"start": v(-1.82, 1.68) * mm, "end": v(-1.82, 1.56) * mm});
            skLineSegment(sketch, "E1828", {"start": v(-1.82, 1.56) * mm, "end": v(-1.82, 1.43) * mm});
            skLineSegment(sketch, "E1829", {"start": v(-1.82, 1.43) * mm, "end": v(-1.82, 1.3) * mm});
            skLineSegment(sketch, "E1830", {"start": v(-1.82, 1.3) * mm, "end": v(-1.82, 1.16) * mm});
            skLineSegment(sketch, "E1831", {"start": v(-1.82, 1.16) * mm, "end": v(-1.82, 1.02) * mm});
            skLineSegment(sketch, "E1832", {"start": v(-1.82, 1.02) * mm, "end": v(-1.82, 0.87) * mm});
            skLineSegment(sketch, "E1833", {"start": v(-1.82, 0.87) * mm, "end": v(-1.82, 0.72) * mm});
            skLineSegment(sketch, "E1834", {"start": v(-1.82, 0.72) * mm, "end": v(-1.82, 0.57) * mm});
            skLineSegment(sketch, "E1835", {"start": v(-1.82, 0.57) * mm, "end": v(-1.82, 0.42) * mm});
            skLineSegment(sketch, "E1836", {"start": v(-1.82, 0.42) * mm, "end": v(-1.82, 0.27) * mm});
            skLineSegment(sketch, "E1837", {"start": v(-1.82, 0.27) * mm, "end": v(-1.82, 0.11) * mm});
            skLineSegment(sketch, "E1838", {"start": v(-1.82, 0.11) * mm, "end": v(-1.82, -0.05) * mm});
            skLineSegment(sketch, "E1839", {"start": v(-1.82, -0.05) * mm, "end": v(-1.82, -0.2) * mm});
            skLineSegment(sketch, "E1840", {"start": v(-1.82, -0.2) * mm, "end": v(-1.82, -0.36) * mm});
            skLineSegment(sketch, "E1841", {"start": v(-1.82, -0.36) * mm, "end": v(-1.82, -0.51) * mm});
            skLineSegment(sketch, "E1842", {"start": v(-1.82, -0.51) * mm, "end": v(-1.82, -0.67) * mm});
            skLineSegment(sketch, "E1843", {"start": v(-1.82, -0.67) * mm, "end": v(-1.82, -0.82) * mm});
            skLineSegment(sketch, "E1844", {"start": v(-1.82, -0.82) * mm, "end": v(-1.82, -0.96) * mm});
            skLineSegment(sketch, "E1845", {"start": v(-1.82, -0.96) * mm, "end": v(-1.82, -1.11) * mm});
            skLineSegment(sketch, "E1846", {"start": v(-1.82, -1.11) * mm, "end": v(-1.82, -1.25) * mm});
            skLineSegment(sketch, "E1847", {"start": v(-1.82, -1.25) * mm, "end": v(-1.82, -1.4) * mm});
            skLineSegment(sketch, "E1848", {"start": v(-1.82, -1.4) * mm, "end": v(-1.82, -1.52) * mm});
            skLineSegment(sketch, "E1849", {"start": v(-1.82, -1.52) * mm, "end": v(-1.82, -1.65) * mm});
            skLineSegment(sketch, "E1850", {"start": v(-1.82, -1.65) * mm, "end": v(-1.82, -1.78) * mm});
            skLineSegment(sketch, "E1851", {"start": v(-1.82, -1.78) * mm, "end": v(-1.82, -1.9) * mm});
            skLineSegment(sketch, "E1852", {"start": v(-1.82, -1.9) * mm, "end": v(-1.82, -2) * mm});
            skLineSegment(sketch, "E1853", {"start": v(-1.82, -2) * mm, "end": v(-1.82, -2.1) * mm});
            skLineSegment(sketch, "E1854", {"start": v(-1.82, -2.1) * mm, "end": v(-1.82, -2.2) * mm});
            skLineSegment(sketch, "E1855", {"start": v(-1.82, -2.2) * mm, "end": v(-1.82, -2.3) * mm});
            skLineSegment(sketch, "E1856", {"start": v(-1.82, -2.3) * mm, "end": v(-1.82, -2.37) * mm});
            skLineSegment(sketch, "E1857", {"start": v(-1.82, -2.37) * mm, "end": v(-1.82, -2.44) * mm});
            skLineSegment(sketch, "E1858", {"start": v(-1.82, -2.44) * mm, "end": v(-1.82, -2.5) * mm});
            skLineSegment(sketch, "E1859", {"start": v(-1.82, -2.5) * mm, "end": v(-1.82, -2.55) * mm});
            skLineSegment(sketch, "E1860", {"start": v(-1.82, -2.55) * mm, "end": v(-1.82, -2.6) * mm});
            skLineSegment(sketch, "E1861", {"start": v(-1.82, -2.6) * mm, "end": v(-1.82, -2.62) * mm});
            skLineSegment(sketch, "E1862", {"start": v(-1.82, -2.62) * mm, "end": v(-1.82, -2.64) * mm});
            skLineSegment(sketch, "E1863", {"start": v(-1.82, -2.64) * mm, "end": v(-1.82, -2.65) * mm});
            skLineSegment(sketch, "E1864", {"start": v(-1.82, -2.65) * mm, "end": v(-1.82, -2.67) * mm});
            skLineSegment(sketch, "E1865", {"start": v(-1.82, -2.67) * mm, "end": v(-1.82, -2.7) * mm});
            skLineSegment(sketch, "E1866", {"start": v(-1.82, -2.7) * mm, "end": v(-1.82, -2.72) * mm});
            skLineSegment(sketch, "E1867", {"start": v(-1.82, -2.72) * mm, "end": v(-1.81, -2.74) * mm});
            skLineSegment(sketch, "E1868", {"start": v(-1.81, -2.74) * mm, "end": v(-1.81, -2.76) * mm});
            skLineSegment(sketch, "E1869", {"start": v(-1.81, -2.76) * mm, "end": v(-1.8, -2.78) * mm});
            skLineSegment(sketch, "E1870", {"start": v(-1.8, -2.78) * mm, "end": v(-1.8, -2.8) * mm});
            skLineSegment(sketch, "E1871", {"start": v(-1.8, -2.8) * mm, "end": v(-1.8, -2.82) * mm});
            skLineSegment(sketch, "E1872", {"start": v(-1.8, -2.82) * mm, "end": v(-1.8, -2.84) * mm});
            skLineSegment(sketch, "E1873", {"start": v(-1.8, -2.84) * mm, "end": v(-1.79, -2.86) * mm});
            skLineSegment(sketch, "E1874", {"start": v(-1.79, -2.86) * mm, "end": v(-1.78, -2.87) * mm});
            skLineSegment(sketch, "E1875", {"start": v(-1.78, -2.87) * mm, "end": v(-1.77, -2.9) * mm});
            skLineSegment(sketch, "E1876", {"start": v(-1.77, -2.9) * mm, "end": v(-1.77, -2.9) * mm});
            skLineSegment(sketch, "E1877", {"start": v(-1.77, -2.9) * mm, "end": v(-1.76, -2.93) * mm});
            skLineSegment(sketch, "E1878", {"start": v(-1.76, -2.93) * mm, "end": v(-1.75, -2.94) * mm});
            skLineSegment(sketch, "E1879", {"start": v(-1.75, -2.94) * mm, "end": v(-1.74, -2.96) * mm});
            skLineSegment(sketch, "E1880", {"start": v(-1.74, -2.96) * mm, "end": v(-1.73, -2.97) * mm});
            skLineSegment(sketch, "E1881", {"start": v(-1.73, -2.97) * mm, "end": v(-1.72, -2.99) * mm});
            skLineSegment(sketch, "E1882", {"start": v(-1.72, -2.99) * mm, "end": v(-1.71, -3) * mm});
            skLineSegment(sketch, "E1883", {"start": v(-1.71, -3) * mm, "end": v(-1.7, -3.02) * mm});
            skLineSegment(sketch, "E1884", {"start": v(-1.7, -3.02) * mm, "end": v(-1.69, -3.03) * mm});
            skLineSegment(sketch, "E1885", {"start": v(-1.69, -3.03) * mm, "end": v(-1.68, -3.05) * mm});
            skLineSegment(sketch, "E1886", {"start": v(-1.68, -3.05) * mm, "end": v(-1.67, -3.06) * mm});
            skLineSegment(sketch, "E1887", {"start": v(-1.67, -3.06) * mm, "end": v(-1.65, -3.07) * mm});
            skLineSegment(sketch, "E1888", {"start": v(-1.65, -3.07) * mm, "end": v(-1.64, -3.09) * mm});
            skLineSegment(sketch, "E1889", {"start": v(-1.64, -3.09) * mm, "end": v(-1.63, -3.1) * mm});
            skLineSegment(sketch, "E1890", {"start": v(-1.63, -3.1) * mm, "end": v(-1.61, -3.1) * mm});
            skLineSegment(sketch, "E1891", {"start": v(-1.61, -3.1) * mm, "end": v(-1.6, -3.12) * mm});
            skLineSegment(sketch, "E1892", {"start": v(-1.6, -3.12) * mm, "end": v(-1.59, -3.13) * mm});
            skLineSegment(sketch, "E1893", {"start": v(-1.59, -3.13) * mm, "end": v(-1.57, -3.14) * mm});
            skLineSegment(sketch, "E1894", {"start": v(-1.57, -3.14) * mm, "end": v(-1.56, -3.15) * mm});
            skLineSegment(sketch, "E1895", {"start": v(-1.56, -3.15) * mm, "end": v(-1.54, -3.16) * mm});
            skLineSegment(sketch, "E1896", {"start": v(-1.54, -3.16) * mm, "end": v(-1.53, -3.17) * mm});
            skLineSegment(sketch, "E1897", {"start": v(-1.53, -3.17) * mm, "end": v(-1.5, -3.17) * mm});
            skLineSegment(sketch, "E1898", {"start": v(-1.5, -3.17) * mm, "end": v(-1.5, -3.18) * mm});
            skLineSegment(sketch, "E1899", {"start": v(-1.5, -3.18) * mm, "end": v(-1.48, -3.19) * mm});
            skLineSegment(sketch, "E1900", {"start": v(-1.48, -3.19) * mm, "end": v(-1.46, -3.2) * mm});
            skLineSegment(sketch, "E1901", {"start": v(-1.46, -3.2) * mm, "end": v(-1.44, -3.2) * mm});
            skLineSegment(sketch, "E1902", {"start": v(-1.44, -3.2) * mm, "end": v(-1.43, -3.2) * mm});
            skLineSegment(sketch, "E1903", {"start": v(-1.43, -3.2) * mm, "end": v(-1.41, -3.21) * mm});
            skLineSegment(sketch, "E1904", {"start": v(-1.41, -3.21) * mm, "end": v(-1.4, -3.22) * mm});
            skLineSegment(sketch, "E1905", {"start": v(-1.4, -3.22) * mm, "end": v(-1.38, -3.22) * mm});
            skLineSegment(sketch, "E1906", {"start": v(-1.38, -3.22) * mm, "end": v(-1.36, -3.23) * mm});
            skLineSegment(sketch, "E1907", {"start": v(-1.36, -3.23) * mm, "end": v(-1.34, -3.23) * mm});
            skLineSegment(sketch, "E1908", {"start": v(-1.34, -3.23) * mm, "end": v(-1.32, -3.23) * mm});
            skLineSegment(sketch, "E1909", {"start": v(-1.32, -3.23) * mm, "end": v(-1.3, -3.23) * mm});
            skLineSegment(sketch, "E1910", {"start": v(-1.3, -3.23) * mm, "end": v(-1.29, -3.24) * mm});
            skLineSegment(sketch, "E1911", {"start": v(-1.29, -3.24) * mm, "end": v(-1.27, -3.24) * mm});
            skLineSegment(sketch, "E1912", {"start": v(-1.27, -3.24) * mm, "end": v(-1.25, -3.24) * mm});
            skLineSegment(sketch, "E1913", {"start": v(-1.25, -3.24) * mm, "end": v(-1.23, -3.24) * mm});
            skLineSegment(sketch, "E1914", {"start": v(-1.23, -3.24) * mm, "end": v(-1.21, -3.24) * mm});
            skLineSegment(sketch, "E1915", {"start": v(-1.21, -3.24) * mm, "end": v(-1.2, -3.24) * mm});
            skLineSegment(sketch, "E1916", {"start": v(-1.2, -3.24) * mm, "end": v(-1.17, -3.24) * mm});
            skLineSegment(sketch, "E1917", {"start": v(-1.17, -3.24) * mm, "end": v(-1.15, -3.23) * mm});
            skLineSegment(sketch, "E1918", {"start": v(-1.15, -3.23) * mm, "end": v(-1.13, -3.23) * mm});
            skLineSegment(sketch, "E1919", {"start": v(-1.13, -3.23) * mm, "end": v(-1.11, -3.23) * mm});
            skLineSegment(sketch, "E1920", {"start": v(-1.11, -3.23) * mm, "end": v(-1.1, -3.23) * mm});
            skLineSegment(sketch, "E1921", {"start": v(-1.1, -3.23) * mm, "end": v(-1.08, -3.22) * mm});
            skLineSegment(sketch, "E1922", {"start": v(-1.08, -3.22) * mm, "end": v(-1.06, -3.22) * mm});
            skLineSegment(sketch, "E1923", {"start": v(-1.06, -3.22) * mm, "end": v(-1.04, -3.21) * mm});
            skLineSegment(sketch, "E1924", {"start": v(-1.04, -3.21) * mm, "end": v(-1.02, -3.2) * mm});
            skLineSegment(sketch, "E1925", {"start": v(-1.02, -3.2) * mm, "end": v(-1, -3.2) * mm});
            skLineSegment(sketch, "E1926", {"start": v(-1, -3.2) * mm, "end": v(-0.98, -3.2) * mm});
            skLineSegment(sketch, "E1927", {"start": v(-0.98, -3.2) * mm, "end": v(-0.97, -3.19) * mm});
            skLineSegment(sketch, "E1928", {"start": v(-0.97, -3.19) * mm, "end": v(-0.95, -3.18) * mm});
            skLineSegment(sketch, "E1929", {"start": v(-0.95, -3.18) * mm, "end": v(-0.93, -3.17) * mm});
            skLineSegment(sketch, "E1930", {"start": v(-0.93, -3.17) * mm, "end": v(-0.91, -3.17) * mm});
            skLineSegment(sketch, "E1931", {"start": v(-0.91, -3.17) * mm, "end": v(-0.9, -3.16) * mm});
            skLineSegment(sketch, "E1932", {"start": v(-0.9, -3.16) * mm, "end": v(-0.88, -3.15) * mm});
            skLineSegment(sketch, "E1933", {"start": v(-0.88, -3.15) * mm, "end": v(-0.86, -3.14) * mm});
            skLineSegment(sketch, "E1934", {"start": v(-0.86, -3.14) * mm, "end": v(-0.85, -3.13) * mm});
            skLineSegment(sketch, "E1935", {"start": v(-0.85, -3.13) * mm, "end": v(-0.83, -3.12) * mm});
            skLineSegment(sketch, "E1936", {"start": v(-0.83, -3.12) * mm, "end": v(-0.82, -3.1) * mm});
            skLineSegment(sketch, "E1937", {"start": v(-0.82, -3.1) * mm, "end": v(-0.8, -3.1) * mm});
            skLineSegment(sketch, "E1938", {"start": v(-0.8, -3.1) * mm, "end": v(-0.79, -3.09) * mm});
            skLineSegment(sketch, "E1939", {"start": v(-0.79, -3.09) * mm, "end": v(-0.78, -3.07) * mm});
            skLineSegment(sketch, "E1940", {"start": v(-0.78, -3.07) * mm, "end": v(-0.76, -3.06) * mm});
            skLineSegment(sketch, "E1941", {"start": v(-0.76, -3.06) * mm, "end": v(-0.75, -3.05) * mm});
            skLineSegment(sketch, "E1942", {"start": v(-0.75, -3.05) * mm, "end": v(-0.74, -3.03) * mm});
            skLineSegment(sketch, "E1943", {"start": v(-0.74, -3.03) * mm, "end": v(-0.72, -3.02) * mm});
            skLineSegment(sketch, "E1944", {"start": v(-0.72, -3.02) * mm, "end": v(-0.71, -3) * mm});
            skLineSegment(sketch, "E1945", {"start": v(-0.71, -3) * mm, "end": v(-0.7, -2.99) * mm});
            skLineSegment(sketch, "E1946", {"start": v(-0.7, -2.99) * mm, "end": v(-0.7, -2.97) * mm});
            skLineSegment(sketch, "E1947", {"start": v(-0.7, -2.97) * mm, "end": v(-0.68, -2.96) * mm});
            skLineSegment(sketch, "E1948", {"start": v(-0.68, -2.96) * mm, "end": v(-0.67, -2.94) * mm});
            skLineSegment(sketch, "E1949", {"start": v(-0.67, -2.94) * mm, "end": v(-0.66, -2.93) * mm});
            skLineSegment(sketch, "E1950", {"start": v(-0.66, -2.93) * mm, "end": v(-0.65, -2.9) * mm});
            skLineSegment(sketch, "E1951", {"start": v(-0.65, -2.9) * mm, "end": v(-0.64, -2.9) * mm});
            skLineSegment(sketch, "E1952", {"start": v(-0.64, -2.9) * mm, "end": v(-0.64, -2.87) * mm});
            skLineSegment(sketch, "E1953", {"start": v(-0.64, -2.87) * mm, "end": v(-0.63, -2.86) * mm});
            skLineSegment(sketch, "E1954", {"start": v(-0.63, -2.86) * mm, "end": v(-0.62, -2.84) * mm});
            skLineSegment(sketch, "E1955", {"start": v(-0.62, -2.84) * mm, "end": v(-0.62, -2.82) * mm});
            skLineSegment(sketch, "E1956", {"start": v(-0.62, -2.82) * mm, "end": v(-0.61, -2.8) * mm});
            skLineSegment(sketch, "E1957", {"start": v(-0.61, -2.8) * mm, "end": v(-0.6, -2.78) * mm});
            skLineSegment(sketch, "E1958", {"start": v(-0.6, -2.78) * mm, "end": v(-0.6, -2.76) * mm});
            skLineSegment(sketch, "E1959", {"start": v(-0.6, -2.76) * mm, "end": v(-0.6, -2.74) * mm});
            skLineSegment(sketch, "E1960", {"start": v(-0.6, -2.74) * mm, "end": v(-0.6, -2.72) * mm});
            skLineSegment(sketch, "E1961", {"start": v(-0.6, -2.72) * mm, "end": v(-0.6, -2.7) * mm});
            skLineSegment(sketch, "E1962", {"start": v(-0.6, -2.7) * mm, "end": v(-0.6, -2.67) * mm});
            skLineSegment(sketch, "E1963", {"start": v(-0.6, -2.67) * mm, "end": v(-0.6, -2.65) * mm});
            skLineSegment(sketch, "E1964", {"start": v(-0.6, -2.65) * mm, "end": v(-0.6, -2.64) * mm});
            skLineSegment(sketch, "E1965", {"start": v(-0.6, -2.64) * mm, "end": v(-0.6, -2.63) * mm});
            skLineSegment(sketch, "E1966", {"start": v(-0.6, -2.63) * mm, "end": v(-0.6, -2.6) * mm});
            skLineSegment(sketch, "E1967", {"start": v(-0.6, -2.6) * mm, "end": v(-0.6, -2.56) * mm});
            skLineSegment(sketch, "E1968", {"start": v(-0.6, -2.56) * mm, "end": v(-0.6, -2.5) * mm});
            skLineSegment(sketch, "E1969", {"start": v(-0.6, -2.5) * mm, "end": v(-0.6, -2.45) * mm});
            skLineSegment(sketch, "E1970", {"start": v(-0.6, -2.45) * mm, "end": v(-0.6, -2.38) * mm});
            skLineSegment(sketch, "E1971", {"start": v(-0.6, -2.38) * mm, "end": v(-0.6, -2.3) * mm});
            skLineSegment(sketch, "E1972", {"start": v(-0.6, -2.3) * mm, "end": v(-0.6, -2.22) * mm});
            skLineSegment(sketch, "E1973", {"start": v(-0.6, -2.22) * mm, "end": v(-0.6, -2.13) * mm});
            skLineSegment(sketch, "E1974", {"start": v(-0.6, -2.13) * mm, "end": v(-0.6, -2.03) * mm});
            skLineSegment(sketch, "E1975", {"start": v(-0.6, -2.03) * mm, "end": v(-0.6, -1.92) * mm});
            skLineSegment(sketch, "E1976", {"start": v(-0.6, -1.92) * mm, "end": v(-0.6, -1.8) * mm});
            skLineSegment(sketch, "E1977", {"start": v(-0.6, -1.8) * mm, "end": v(-0.6, -1.69) * mm});
            skLineSegment(sketch, "E1978", {"start": v(-0.6, -1.69) * mm, "end": v(-0.6, -1.57) * mm});
            skLineSegment(sketch, "E1979", {"start": v(-0.6, -1.57) * mm, "end": v(-0.6, -1.44) * mm});
            skLineSegment(sketch, "E1980", {"start": v(-0.6, -1.44) * mm, "end": v(-0.6, -1.3) * mm});
            skLineSegment(sketch, "E1981", {"start": v(-0.6, -1.3) * mm, "end": v(-0.6, -1.17) * mm});
            skLineSegment(sketch, "E1982", {"start": v(-0.6, -1.17) * mm, "end": v(-0.6, -1.03) * mm});
            skLineSegment(sketch, "E1983", {"start": v(-0.6, -1.03) * mm, "end": v(-0.6, -0.88) * mm});
            skLineSegment(sketch, "E1984", {"start": v(-0.6, -0.88) * mm, "end": v(-0.6, -0.74) * mm});
            skLineSegment(sketch, "E1985", {"start": v(-0.6, -0.74) * mm, "end": v(-0.6, -0.59) * mm});
            skLineSegment(sketch, "E1986", {"start": v(-0.6, -0.59) * mm, "end": v(-0.6, -0.44) * mm});
            skLineSegment(sketch, "E1987", {"start": v(-0.6, -0.44) * mm, "end": v(-0.6, -0.3) * mm});
            skLineSegment(sketch, "E1988", {"start": v(-0.6, -0.3) * mm, "end": v(-0.6, -0.14) * mm});
            skLineSegment(sketch, "E1989", {"start": v(-0.6, -0.14) * mm, "end": v(-0.6, 0.01) * mm});
            skLineSegment(sketch, "E1990", {"start": v(-0.6, 0.01) * mm, "end": v(-0.6, 0.16) * mm});
            skLineSegment(sketch, "E1991", {"start": v(-0.6, 0.16) * mm, "end": v(-0.6, 0.3) * mm});
            skLineSegment(sketch, "E1992", {"start": v(-0.6, 0.3) * mm, "end": v(-0.6, 0.46) * mm});
            skLineSegment(sketch, "E1993", {"start": v(-0.6, 0.46) * mm, "end": v(-0.6, 0.6) * mm});
            skLineSegment(sketch, "E1994", {"start": v(-0.6, 0.6) * mm, "end": v(-0.6, 0.75) * mm});
            skLineSegment(sketch, "E1995", {"start": v(-0.6, 0.75) * mm, "end": v(-0.6, 0.89) * mm});
            skLineSegment(sketch, "E1996", {"start": v(-0.6, 0.89) * mm, "end": v(-0.6, 1.02) * mm});
            skLineSegment(sketch, "E1997", {"start": v(-0.6, 1.02) * mm, "end": v(-0.6, 1.16) * mm});
            skLineSegment(sketch, "E1998", {"start": v(-0.6, 1.16) * mm, "end": v(-0.6, 1.29) * mm});
            skLineSegment(sketch, "E1999", {"start": v(-0.6, 1.29) * mm, "end": v(-0.6, 1.4) * mm});
            skLineSegment(sketch, "E2000", {"start": v(-0.6, 1.4) * mm, "end": v(-0.6, 1.53) * mm});
            skLineSegment(sketch, "E2001", {"start": v(-0.6, 1.53) * mm, "end": v(-0.6, 1.64) * mm});
            skLineSegment(sketch, "E2002", {"start": v(-0.6, 1.64) * mm, "end": v(-0.6, 1.75) * mm});
            skLineSegment(sketch, "E2003", {"start": v(-0.6, 1.75) * mm, "end": v(-0.6, 1.85) * mm});
            skLineSegment(sketch, "E2004", {"start": v(-0.6, 1.85) * mm, "end": v(-0.6, 1.94) * mm});
            skLineSegment(sketch, "E2005", {"start": v(-0.6, 1.94) * mm, "end": v(-0.6, 2.02) * mm});
            skLineSegment(sketch, "E2006", {"start": v(-0.6, 2.02) * mm, "end": v(-0.6, 2.1) * mm});
            skLineSegment(sketch, "E2007", {"start": v(-0.6, 2.1) * mm, "end": v(-0.6, 2.17) * mm});
            skLineSegment(sketch, "E2008", {"start": v(-0.6, 2.17) * mm, "end": v(-0.6, 2.23) * mm});
            skLineSegment(sketch, "E2009", {"start": v(-0.6, 2.23) * mm, "end": v(-0.6, 2.28) * mm});
            skLineSegment(sketch, "E2010", {"start": v(-0.6, 2.28) * mm, "end": v(-0.6, 2.32) * mm});
            skLineSegment(sketch, "E2011", {"start": v(-0.6, 2.32) * mm, "end": v(-0.6, 2.35) * mm});
            skLineSegment(sketch, "E2012", {"start": v(-0.6, 2.35) * mm, "end": v(-0.6, 2.36) * mm});
            skLineSegment(sketch, "E2013", {"start": v(-0.6, 2.36) * mm, "end": v(-0.6, 2.37) * mm});
            skLineSegment(sketch, "E2014", {"start": v(-0.6, 2.37) * mm, "end": v(-0.6, 2.38) * mm});
            skLineSegment(sketch, "E2015", {"start": v(-0.6, 2.38) * mm, "end": v(-0.6, 2.4) * mm});
            skLineSegment(sketch, "E2016", {"start": v(-0.6, 2.4) * mm, "end": v(-0.6, 2.41) * mm});
            skLineSegment(sketch, "E2017", {"start": v(-0.6, 2.41) * mm, "end": v(-0.6, 2.43) * mm});
            skLineSegment(sketch, "E2018", {"start": v(-0.6, 2.43) * mm, "end": v(-0.59, 2.44) * mm});
            skLineSegment(sketch, "E2019", {"start": v(-0.59, 2.44) * mm, "end": v(-0.59, 2.45) * mm});
            skLineSegment(sketch, "E2020", {"start": v(-0.59, 2.45) * mm, "end": v(-0.58, 2.47) * mm});
            skLineSegment(sketch, "E2021", {"start": v(-0.58, 2.47) * mm, "end": v(-0.58, 2.48) * mm});
            skLineSegment(sketch, "E2022", {"start": v(-0.58, 2.48) * mm, "end": v(-0.58, 2.5) * mm});
            skLineSegment(sketch, "E2023", {"start": v(-0.58, 2.5) * mm, "end": v(-0.57, 2.5) * mm});
            skLineSegment(sketch, "E2024", {"start": v(-0.57, 2.5) * mm, "end": v(-0.57, 2.51) * mm});
            skLineSegment(sketch, "E2025", {"start": v(-0.57, 2.51) * mm, "end": v(-0.56, 2.52) * mm});
            skLineSegment(sketch, "E2026", {"start": v(-0.56, 2.52) * mm, "end": v(-0.56, 2.54) * mm});
            skLineSegment(sketch, "E2027", {"start": v(-0.56, 2.54) * mm, "end": v(-0.55, 2.55) * mm});
            skLineSegment(sketch, "E2028", {"start": v(-0.55, 2.55) * mm, "end": v(-0.55, 2.55) * mm});
            skLineSegment(sketch, "E2029", {"start": v(-0.55, 2.55) * mm, "end": v(-0.54, 2.56) * mm});
            skLineSegment(sketch, "E2030", {"start": v(-0.54, 2.56) * mm, "end": v(-0.54, 2.57) * mm});
            skLineSegment(sketch, "E2031", {"start": v(-0.54, 2.57) * mm, "end": v(-0.53, 2.58) * mm});
            skLineSegment(sketch, "E2032", {"start": v(-0.53, 2.58) * mm, "end": v(-0.52, 2.59) * mm});
            skLineSegment(sketch, "E2033", {"start": v(-0.52, 2.59) * mm, "end": v(-0.52, 2.6) * mm});
            skLineSegment(sketch, "E2034", {"start": v(-0.52, 2.6) * mm, "end": v(-0.5, 2.6) * mm});
            skLineSegment(sketch, "E2035", {"start": v(-0.5, 2.6) * mm, "end": v(-0.5, 2.61) * mm});
            skLineSegment(sketch, "E2036", {"start": v(-0.5, 2.61) * mm, "end": v(-0.5, 2.62) * mm});
            skLineSegment(sketch, "E2037", {"start": v(-0.5, 2.62) * mm, "end": v(-0.48, 2.63) * mm});
            skLineSegment(sketch, "E2038", {"start": v(-0.48, 2.63) * mm, "end": v(-0.47, 2.63) * mm});
            skLineSegment(sketch, "E2039", {"start": v(-0.47, 2.63) * mm, "end": v(-0.47, 2.64) * mm});
            skLineSegment(sketch, "E2040", {"start": v(-0.47, 2.64) * mm, "end": v(-0.46, 2.64) * mm});
            skLineSegment(sketch, "E2041", {"start": v(-0.46, 2.64) * mm, "end": v(-0.45, 2.65) * mm});
            skLineSegment(sketch, "E2042", {"start": v(-0.45, 2.65) * mm, "end": v(-0.44, 2.65) * mm});
            skLineSegment(sketch, "E2043", {"start": v(-0.44, 2.65) * mm, "end": v(-0.43, 2.66) * mm});
            skLineSegment(sketch, "E2044", {"start": v(-0.43, 2.66) * mm, "end": v(-0.42, 2.66) * mm});
            skLineSegment(sketch, "E2045", {"start": v(-0.42, 2.66) * mm, "end": v(-0.4, 2.67) * mm});
            skLineSegment(sketch, "E2046", {"start": v(-0.4, 2.67) * mm, "end": v(-0.4, 2.67) * mm});
            skLineSegment(sketch, "E2047", {"start": v(-0.4, 2.67) * mm, "end": v(-0.39, 2.67) * mm});
            skLineSegment(sketch, "E2048", {"start": v(-0.39, 2.67) * mm, "end": v(-0.37, 2.68) * mm});
            skLineSegment(sketch, "E2049", {"start": v(-0.37, 2.68) * mm, "end": v(-0.36, 2.68) * mm});
            skLineSegment(sketch, "E2050", {"start": v(-0.36, 2.68) * mm, "end": v(-0.35, 2.68) * mm});
            skLineSegment(sketch, "E2051", {"start": v(-0.35, 2.68) * mm, "end": v(-0.34, 2.69) * mm});
            skLineSegment(sketch, "E2052", {"start": v(-0.34, 2.69) * mm, "end": v(-0.33, 2.69) * mm});
            skLineSegment(sketch, "E2053", {"start": v(-0.33, 2.69) * mm, "end": v(-0.32, 2.69) * mm});
            skLineSegment(sketch, "E2054", {"start": v(-0.32, 2.69) * mm, "end": v(-0.3, 2.7) * mm});
            skLineSegment(sketch, "E2055", {"start": v(-0.3, 2.7) * mm, "end": v(-0.3, 2.7) * mm});
            skLineSegment(sketch, "E2056", {"start": v(-0.3, 2.7) * mm, "end": v(-0.28, 2.7) * mm});
            skLineSegment(sketch, "E2057", {"start": v(-0.28, 2.7) * mm, "end": v(-0.27, 2.7) * mm});
            skLineSegment(sketch, "E2058", {"start": v(-0.27, 2.7) * mm, "end": v(-0.26, 2.7) * mm});
            skLineSegment(sketch, "E2059", {"start": v(-0.26, 2.7) * mm, "end": v(-0.24, 2.7) * mm});
            skLineSegment(sketch, "E2060", {"start": v(-0.24, 2.7) * mm, "end": v(-0.23, 2.7) * mm});
            skLineSegment(sketch, "E2061", {"start": v(-0.23, 2.7) * mm, "end": v(-0.22, 2.7) * mm});
            skLineSegment(sketch, "E2062", {"start": v(-0.22, 2.7) * mm, "end": v(-0.2, 2.7) * mm});
            skLineSegment(sketch, "E2063", {"start": v(-0.2, 2.7) * mm, "end": v(-0.2, 2.7) * mm});
            skLineSegment(sketch, "E2064", {"start": v(-0.2, 2.7) * mm, "end": v(-0.19, 2.7) * mm});
            skLineSegment(sketch, "E2065", {"start": v(-0.19, 2.7) * mm, "end": v(-0.18, 2.7) * mm});
            skLineSegment(sketch, "E2066", {"start": v(-0.18, 2.7) * mm, "end": v(-0.18, 2.7) * mm});
            skLineSegment(sketch, "E2067", {"start": v(-0.18, 2.7) * mm, "end": v(-0.17, 2.7) * mm});
            skLineSegment(sketch, "E2068", {"start": v(-0.17, 2.7) * mm, "end": v(-0.16, 2.7) * mm});
            skLineSegment(sketch, "E2069", {"start": v(-0.16, 2.7) * mm, "end": v(-0.15, 2.7) * mm});
            skLineSegment(sketch, "E2070", {"start": v(-0.15, 2.7) * mm, "end": v(-0.14, 2.7) * mm});
            skLineSegment(sketch, "E2071", {"start": v(-0.14, 2.7) * mm, "end": v(-0.13, 2.7) * mm});
            skLineSegment(sketch, "E2072", {"start": v(-0.13, 2.7) * mm, "end": v(-0.11, 2.7) * mm});
            skLineSegment(sketch, "E2073", {"start": v(-0.11, 2.7) * mm, "end": v(-0.1, 2.7) * mm});
            skLineSegment(sketch, "E2074", {"start": v(-0.1, 2.7) * mm, "end": v(-0.08, 2.7) * mm});
            skLineSegment(sketch, "E2075", {"start": v(-0.08, 2.7) * mm, "end": v(-0.07, 2.7) * mm});
            skLineSegment(sketch, "E2076", {"start": v(-0.07, 2.7) * mm, "end": v(-0.05, 2.7) * mm});
            skLineSegment(sketch, "E2077", {"start": v(-0.05, 2.7) * mm, "end": v(-0.04, 2.7) * mm});
            skLineSegment(sketch, "E2078", {"start": v(-0.04, 2.7) * mm, "end": v(-0.02, 2.7) * mm});
            skLineSegment(sketch, "E2079", {"start": v(-0.02, 2.7) * mm, "end": v(0, 2.7) * mm});
            skLineSegment(sketch, "E2080", {"start": v(0, 2.7) * mm, "end": v(0.02, 2.7) * mm});
            skLineSegment(sketch, "E2081", {"start": v(0.02, 2.7) * mm, "end": v(0.04, 2.7) * mm});
            skLineSegment(sketch, "E2082", {"start": v(0.04, 2.7) * mm, "end": v(0.06, 2.7) * mm});
            skLineSegment(sketch, "E2083", {"start": v(0.06, 2.7) * mm, "end": v(0.08, 2.7) * mm});
            skLineSegment(sketch, "E2084", {"start": v(0.08, 2.7) * mm, "end": v(0.1, 2.7) * mm});
            skLineSegment(sketch, "E2085", {"start": v(0.1, 2.7) * mm, "end": v(0.12, 2.7) * mm});
            skLineSegment(sketch, "E2086", {"start": v(0.12, 2.7) * mm, "end": v(0.14, 2.7) * mm});
            skLineSegment(sketch, "E2087", {"start": v(0.14, 2.7) * mm, "end": v(0.16, 2.7) * mm});
            skLineSegment(sketch, "E2088", {"start": v(0.16, 2.7) * mm, "end": v(0.17, 2.7) * mm});
            skLineSegment(sketch, "E2089", {"start": v(0.17, 2.7) * mm, "end": v(0.2, 2.7) * mm});
            skLineSegment(sketch, "E2090", {"start": v(0.2, 2.7) * mm, "end": v(0.21, 2.7) * mm});
            skLineSegment(sketch, "E2091", {"start": v(0.21, 2.7) * mm, "end": v(0.23, 2.7) * mm});
            skLineSegment(sketch, "E2092", {"start": v(0.23, 2.7) * mm, "end": v(0.25, 2.7) * mm});
            skLineSegment(sketch, "E2093", {"start": v(0.25, 2.7) * mm, "end": v(0.27, 2.7) * mm});
            skLineSegment(sketch, "E2094", {"start": v(0.27, 2.7) * mm, "end": v(0.29, 2.7) * mm});
            skLineSegment(sketch, "E2095", {"start": v(0.29, 2.7) * mm, "end": v(0.3, 2.7) * mm});
            skLineSegment(sketch, "E2096", {"start": v(0.3, 2.7) * mm, "end": v(0.32, 2.7) * mm});
            skLineSegment(sketch, "E2097", {"start": v(0.32, 2.7) * mm, "end": v(0.34, 2.7) * mm});
            skLineSegment(sketch, "E2098", {"start": v(0.34, 2.7) * mm, "end": v(0.35, 2.7) * mm});
            skLineSegment(sketch, "E2099", {"start": v(0.35, 2.7) * mm, "end": v(0.37, 2.7) * mm});
            skLineSegment(sketch, "E2100", {"start": v(0.37, 2.7) * mm, "end": v(0.38, 2.7) * mm});
            skLineSegment(sketch, "E2101", {"start": v(0.38, 2.7) * mm, "end": v(0.4, 2.7) * mm});
            skLineSegment(sketch, "E2102", {"start": v(0.4, 2.7) * mm, "end": v(0.4, 2.7) * mm});
            skLineSegment(sketch, "E2103", {"start": v(0.4, 2.7) * mm, "end": v(0.42, 2.7) * mm});
            skLineSegment(sketch, "E2104", {"start": v(0.42, 2.7) * mm, "end": v(0.43, 2.7) * mm});
            skLineSegment(sketch, "E2105", {"start": v(0.43, 2.7) * mm, "end": v(0.44, 2.7) * mm});
            skLineSegment(sketch, "E2106", {"start": v(0.44, 2.7) * mm, "end": v(0.45, 2.7) * mm});
            skLineSegment(sketch, "E2107", {"start": v(0.45, 2.7) * mm, "end": v(0.45, 2.7) * mm});
            skLineSegment(sketch, "E2108", {"start": v(0.45, 2.7) * mm, "end": v(0.46, 2.7) * mm});
            skLineSegment(sketch, "E2109", {"start": v(0.46, 2.7) * mm, "end": v(0.46, 2.7) * mm});
            skLineSegment(sketch, "E2110", {"start": v(0.46, 2.7) * mm, "end": v(0.47, 2.7) * mm});
            skLineSegment(sketch, "E2111", {"start": v(0.47, 2.7) * mm, "end": v(0.52, 2.7) * mm});
            skLineSegment(sketch, "E2112", {"start": v(0.52, 2.7) * mm, "end": v(0.57, 2.7) * mm});
            skLineSegment(sketch, "E2113", {"start": v(0.57, 2.7) * mm, "end": v(0.62, 2.7) * mm});
            skLineSegment(sketch, "E2114", {"start": v(0.62, 2.7) * mm, "end": v(0.68, 2.68) * mm});
            skLineSegment(sketch, "E2115", {"start": v(0.68, 2.68) * mm, "end": v(0.73, 2.68) * mm});
            skLineSegment(sketch, "E2116", {"start": v(0.73, 2.68) * mm, "end": v(0.78, 2.66) * mm});
            skLineSegment(sketch, "E2117", {"start": v(0.78, 2.66) * mm, "end": v(0.83, 2.65) * mm});
            skLineSegment(sketch, "E2118", {"start": v(0.83, 2.65) * mm, "end": v(0.88, 2.64) * mm});
            skLineSegment(sketch, "E2119", {"start": v(0.88, 2.64) * mm, "end": v(0.93, 2.62) * mm});
            skLineSegment(sketch, "E2120", {"start": v(0.93, 2.62) * mm, "end": v(0.98, 2.6) * mm});
            skLineSegment(sketch, "E2121", {"start": v(0.98, 2.6) * mm, "end": v(1.03, 2.59) * mm});
            skLineSegment(sketch, "E2122", {"start": v(1.03, 2.59) * mm, "end": v(1.07, 2.57) * mm});
            skLineSegment(sketch, "E2123", {"start": v(1.07, 2.57) * mm, "end": v(1.12, 2.55) * mm});
            skLineSegment(sketch, "E2124", {"start": v(1.12, 2.55) * mm, "end": v(1.16, 2.52) * mm});
            skLineSegment(sketch, "E2125", {"start": v(1.16, 2.52) * mm, "end": v(1.2, 2.5) * mm});
            skLineSegment(sketch, "E2126", {"start": v(1.2, 2.5) * mm, "end": v(1.25, 2.47) * mm});
            skLineSegment(sketch, "E2127", {"start": v(1.25, 2.47) * mm, "end": v(1.3, 2.44) * mm});
            skLineSegment(sketch, "E2128", {"start": v(1.3, 2.44) * mm, "end": v(1.34, 2.41) * mm});
            skLineSegment(sketch, "E2129", {"start": v(1.34, 2.41) * mm, "end": v(1.38, 2.38) * mm});
            skLineSegment(sketch, "E2130", {"start": v(1.38, 2.38) * mm, "end": v(1.42, 2.35) * mm});
            skLineSegment(sketch, "E2131", {"start": v(1.42, 2.35) * mm, "end": v(1.46, 2.32) * mm});
            skLineSegment(sketch, "E2132", {"start": v(1.46, 2.32) * mm, "end": v(1.5, 2.29) * mm});
            skLineSegment(sketch, "E2133", {"start": v(1.5, 2.29) * mm, "end": v(1.53, 2.25) * mm});
            skLineSegment(sketch, "E2134", {"start": v(1.53, 2.25) * mm, "end": v(1.57, 2.22) * mm});
            skLineSegment(sketch, "E2135", {"start": v(1.57, 2.22) * mm, "end": v(1.6, 2.18) * mm});
            skLineSegment(sketch, "E2136", {"start": v(1.6, 2.18) * mm, "end": v(1.64, 2.14) * mm});
            skLineSegment(sketch, "E2137", {"start": v(1.64, 2.14) * mm, "end": v(1.67, 2.1) * mm});
            skLineSegment(sketch, "E2138", {"start": v(1.67, 2.1) * mm, "end": v(1.7, 2.06) * mm});
            skLineSegment(sketch, "E2139", {"start": v(1.7, 2.06) * mm, "end": v(1.73, 2.02) * mm});
            skLineSegment(sketch, "E2140", {"start": v(1.73, 2.02) * mm, "end": v(1.76, 1.98) * mm});
            skLineSegment(sketch, "E2141", {"start": v(1.76, 1.98) * mm, "end": v(1.78, 1.93) * mm});
            skLineSegment(sketch, "E2142", {"start": v(1.78, 1.93) * mm, "end": v(1.8, 1.89) * mm});
            skLineSegment(sketch, "E2143", {"start": v(1.8, 1.89) * mm, "end": v(1.83, 1.84) * mm});
            skLineSegment(sketch, "E2144", {"start": v(1.83, 1.84) * mm, "end": v(1.86, 1.8) * mm});
            skLineSegment(sketch, "E2145", {"start": v(1.86, 1.8) * mm, "end": v(1.88, 1.75) * mm});
            skLineSegment(sketch, "E2146", {"start": v(1.88, 1.75) * mm, "end": v(1.9, 1.7) * mm});
            skLineSegment(sketch, "E2147", {"start": v(1.9, 1.7) * mm, "end": v(1.91, 1.66) * mm});
            skLineSegment(sketch, "E2148", {"start": v(1.91, 1.66) * mm, "end": v(1.93, 1.61) * mm});
            skLineSegment(sketch, "E2149", {"start": v(1.93, 1.61) * mm, "end": v(1.95, 1.56) * mm});
            skLineSegment(sketch, "E2150", {"start": v(1.95, 1.56) * mm, "end": v(1.96, 1.51) * mm});
            skLineSegment(sketch, "E2151", {"start": v(1.96, 1.51) * mm, "end": v(1.97, 1.46) * mm});
            skLineSegment(sketch, "E2152", {"start": v(1.97, 1.46) * mm, "end": v(1.98, 1.41) * mm});
            skLineSegment(sketch, "E2153", {"start": v(1.98, 1.41) * mm, "end": v(1.99, 1.36) * mm});
            skLineSegment(sketch, "E2154", {"start": v(1.99, 1.36) * mm, "end": v(2, 1.31) * mm});
            skLineSegment(sketch, "E2155", {"start": v(2, 1.31) * mm, "end": v(2, 1.26) * mm});
            skLineSegment(sketch, "E2156", {"start": v(2, 1.26) * mm, "end": v(2, 1.21) * mm});
            skLineSegment(sketch, "E2157", {"start": v(2, 1.21) * mm, "end": v(2, 1.16) * mm});
            skLineSegment(sketch, "E2158", {"start": v(2, 1.16) * mm, "end": v(2, 1.1) * mm});
            skLineSegment(sketch, "E2159", {"start": v(2, 1.1) * mm, "end": v(2, 1.05) * mm});
            skLineSegment(sketch, "E2160", {"start": v(2, 1.05) * mm, "end": v(2, 1) * mm});
            skLineSegment(sketch, "E2161", {"start": v(2, 1) * mm, "end": v(2, 0.96) * mm});
            skLineSegment(sketch, "E2162", {"start": v(2, 0.96) * mm, "end": v(1.98, 0.92) * mm});
            skLineSegment(sketch, "E2163", {"start": v(1.98, 0.92) * mm, "end": v(1.98, 0.89) * mm});
            skLineSegment(sketch, "E2164", {"start": v(1.98, 0.89) * mm, "end": v(1.97, 0.85) * mm});
            skLineSegment(sketch, "E2165", {"start": v(1.97, 0.85) * mm, "end": v(1.96, 0.81) * mm});
            skLineSegment(sketch, "E2166", {"start": v(1.96, 0.81) * mm, "end": v(1.95, 0.78) * mm});
            skLineSegment(sketch, "E2167", {"start": v(1.95, 0.78) * mm, "end": v(1.94, 0.74) * mm});
            skLineSegment(sketch, "E2168", {"start": v(1.94, 0.74) * mm, "end": v(1.92, 0.7) * mm});
            skLineSegment(sketch, "E2169", {"start": v(1.92, 0.7) * mm, "end": v(1.91, 0.67) * mm});
            skLineSegment(sketch, "E2170", {"start": v(1.91, 0.67) * mm, "end": v(1.9, 0.64) * mm});
            skLineSegment(sketch, "E2171", {"start": v(1.9, 0.64) * mm, "end": v(1.88, 0.6) * mm});
            skLineSegment(sketch, "E2172", {"start": v(1.88, 0.6) * mm, "end": v(1.87, 0.57) * mm});
            skLineSegment(sketch, "E2173", {"start": v(1.87, 0.57) * mm, "end": v(1.85, 0.54) * mm});
            skLineSegment(sketch, "E2174", {"start": v(1.85, 0.54) * mm, "end": v(1.83, 0.5) * mm});
            skLineSegment(sketch, "E2175", {"start": v(1.83, 0.5) * mm, "end": v(1.82, 0.47) * mm});
            skLineSegment(sketch, "E2176", {"start": v(1.82, 0.47) * mm, "end": v(1.8, 0.44) * mm});
            skLineSegment(sketch, "E2177", {"start": v(1.8, 0.44) * mm, "end": v(1.78, 0.41) * mm});
            skLineSegment(sketch, "E2178", {"start": v(1.78, 0.41) * mm, "end": v(1.76, 0.38) * mm});
            skLineSegment(sketch, "E2179", {"start": v(1.76, 0.38) * mm, "end": v(1.74, 0.35) * mm});
            skLineSegment(sketch, "E2180", {"start": v(1.74, 0.35) * mm, "end": v(1.72, 0.33) * mm});
            skLineSegment(sketch, "E2181", {"start": v(1.72, 0.33) * mm, "end": v(1.7, 0.3) * mm});
            skLineSegment(sketch, "E2182", {"start": v(1.7, 0.3) * mm, "end": v(1.67, 0.27) * mm});
            skLineSegment(sketch, "E2183", {"start": v(1.67, 0.27) * mm, "end": v(1.65, 0.24) * mm});
            skLineSegment(sketch, "E2184", {"start": v(1.65, 0.24) * mm, "end": v(1.62, 0.22) * mm});
            skLineSegment(sketch, "E2185", {"start": v(1.62, 0.22) * mm, "end": v(1.6, 0.2) * mm});
            skLineSegment(sketch, "E2186", {"start": v(1.6, 0.2) * mm, "end": v(1.57, 0.17) * mm});
            skLineSegment(sketch, "E2187", {"start": v(1.57, 0.17) * mm, "end": v(1.55, 0.14) * mm});
            skLineSegment(sketch, "E2188", {"start": v(1.55, 0.14) * mm, "end": v(1.52, 0.12) * mm});
            skLineSegment(sketch, "E2189", {"start": v(1.52, 0.12) * mm, "end": v(1.5, 0.1) * mm});
            skLineSegment(sketch, "E2190", {"start": v(1.5, 0.1) * mm, "end": v(1.47, 0.07) * mm});
            skLineSegment(sketch, "E2191", {"start": v(1.47, 0.07) * mm, "end": v(1.44, 0.05) * mm});
            skLineSegment(sketch, "E2192", {"start": v(1.44, 0.05) * mm, "end": v(1.4, 0.03) * mm});
            skLineSegment(sketch, "E2193", {"start": v(1.4, 0.03) * mm, "end": v(1.38, 0.01) * mm});
            skLineSegment(sketch, "E2194", {"start": v(1.38, 0.01) * mm, "end": v(1.35, 0) * mm});
            skLineSegment(sketch, "E2195", {"start": v(1.35, 0) * mm, "end": v(1.32, -0.03) * mm});
            skLineSegment(sketch, "E2196", {"start": v(1.32, -0.03) * mm, "end": v(1.29, -0.05) * mm});
            skLineSegment(sketch, "E2197", {"start": v(1.29, -0.05) * mm, "end": v(1.25, -0.07) * mm});
            skLineSegment(sketch, "E2198", {"start": v(1.25, -0.07) * mm, "end": v(1.22, -0.08) * mm});
            skLineSegment(sketch, "E2199", {"start": v(1.22, -0.08) * mm, "end": v(1.19, -0.1) * mm});
            skLineSegment(sketch, "E2200", {"start": v(1.19, -0.1) * mm, "end": v(1.16, -0.12) * mm});
            skLineSegment(sketch, "E2201", {"start": v(1.16, -0.12) * mm, "end": v(1.12, -0.13) * mm});
            skLineSegment(sketch, "E2202", {"start": v(1.12, -0.13) * mm, "end": v(1.09, -0.15) * mm});
            skLineSegment(sketch, "E2203", {"start": v(1.09, -0.15) * mm, "end": v(1.05, -0.16) * mm});
            skLineSegment(sketch, "E2204", {"start": v(1.05, -0.16) * mm, "end": v(1.02, -0.18) * mm});
            skLineSegment(sketch, "E2205", {"start": v(1.02, -0.18) * mm, "end": v(0.98, -0.19) * mm});
            skLineSegment(sketch, "E2206", {"start": v(0.98, -0.19) * mm, "end": v(0.94, -0.2) * mm});
            skLineSegment(sketch, "E2207", {"start": v(0.94, -0.2) * mm, "end": v(0.9, -0.21) * mm});
            skLineSegment(sketch, "E2208", {"start": v(0.9, -0.21) * mm, "end": v(0.87, -0.22) * mm});
            skLineSegment(sketch, "E2209", {"start": v(0.87, -0.22) * mm, "end": v(0.83, -0.24) * mm});
            skLineSegment(sketch, "E2210", {"start": v(0.83, -0.24) * mm, "end": v(0.8, -0.25) * mm});
            skLineSegment(sketch, "E2211", {"start": v(0.8, -0.25) * mm, "end": v(0.8, -0.25) * mm});
            skLineSegment(sketch, "E2212", {"start": v(0.8, -0.25) * mm, "end": v(0.79, -0.25) * mm});
            skLineSegment(sketch, "E2213", {"start": v(0.79, -0.25) * mm, "end": v(0.78, -0.25) * mm});
            skLineSegment(sketch, "E2214", {"start": v(0.78, -0.25) * mm, "end": v(0.78, -0.25) * mm});
            skLineSegment(sketch, "E2215", {"start": v(0.78, -0.25) * mm, "end": v(0.77, -0.25) * mm});
            skLineSegment(sketch, "E2216", {"start": v(0.77, -0.25) * mm, "end": v(0.77, -0.26) * mm});
            skLineSegment(sketch, "E2217", {"start": v(0.77, -0.26) * mm, "end": v(0.76, -0.26) * mm});
            skLineSegment(sketch, "E2218", {"start": v(0.76, -0.26) * mm, "end": v(0.76, -0.26) * mm});
            skLineSegment(sketch, "E2219", {"start": v(0.76, -0.26) * mm, "end": v(0.75, -0.26) * mm});
            skLineSegment(sketch, "E2220", {"start": v(0.75, -0.26) * mm, "end": v(0.75, -0.26) * mm});
            skLineSegment(sketch, "E2221", {"start": v(0.75, -0.26) * mm, "end": v(0.75, -0.27) * mm});
            skLineSegment(sketch, "E2222", {"start": v(0.75, -0.27) * mm, "end": v(0.75, -0.27) * mm});
            skLineSegment(sketch, "E2223", {"start": v(0.75, -0.27) * mm, "end": v(0.74, -0.27) * mm});
            skLineSegment(sketch, "E2224", {"start": v(0.74, -0.27) * mm, "end": v(0.74, -0.27) * mm});
            skLineSegment(sketch, "E2225", {"start": v(0.74, -0.27) * mm, "end": v(0.73, -0.27) * mm});
            skLineSegment(sketch, "E2226", {"start": v(0.73, -0.27) * mm, "end": v(0.73, -0.28) * mm});
            skLineSegment(sketch, "E2227", {"start": v(0.73, -0.28) * mm, "end": v(0.73, -0.28) * mm});
            skLineSegment(sketch, "E2228", {"start": v(0.73, -0.28) * mm, "end": v(0.72, -0.28) * mm});
            skLineSegment(sketch, "E2229", {"start": v(0.72, -0.28) * mm, "end": v(0.72, -0.29) * mm});
            skLineSegment(sketch, "E2230", {"start": v(0.72, -0.29) * mm, "end": v(0.72, -0.29) * mm});
            skLineSegment(sketch, "E2231", {"start": v(0.72, -0.29) * mm, "end": v(0.71, -0.3) * mm});
            skLineSegment(sketch, "E2232", {"start": v(0.71, -0.3) * mm, "end": v(0.71, -0.3) * mm});
            skLineSegment(sketch, "E2233", {"start": v(0.71, -0.3) * mm, "end": v(0.7, -0.3) * mm});
            skLineSegment(sketch, "E2234", {"start": v(0.7, -0.3) * mm, "end": v(0.7, -0.3) * mm});
            skLineSegment(sketch, "E2235", {"start": v(0.7, -0.3) * mm, "end": v(0.7, -0.31) * mm});
            skLineSegment(sketch, "E2236", {"start": v(0.7, -0.31) * mm, "end": v(0.7, -0.31) * mm});
            skLineSegment(sketch, "E2237", {"start": v(0.7, -0.31) * mm, "end": v(0.7, -0.32) * mm});
            skLineSegment(sketch, "E2238", {"start": v(0.7, -0.32) * mm, "end": v(0.7, -0.32) * mm});
            skLineSegment(sketch, "E2239", {"start": v(0.7, -0.32) * mm, "end": v(0.7, -0.33) * mm});
            skLineSegment(sketch, "E2240", {"start": v(0.7, -0.33) * mm, "end": v(0.7, -0.33) * mm});
            skLineSegment(sketch, "E2241", {"start": v(0.7, -0.33) * mm, "end": v(0.69, -0.33) * mm});
            skLineSegment(sketch, "E2242", {"start": v(0.69, -0.33) * mm, "end": v(0.69, -0.34) * mm});
            skLineSegment(sketch, "E2243", {"start": v(0.69, -0.34) * mm, "end": v(0.69, -0.34) * mm});
            skLineSegment(sketch, "E2244", {"start": v(0.69, -0.34) * mm, "end": v(0.68, -0.34) * mm});
            skLineSegment(sketch, "E2245", {"start": v(0.68, -0.34) * mm, "end": v(0.68, -0.35) * mm});
            skLineSegment(sketch, "E2246", {"start": v(0.68, -0.35) * mm, "end": v(0.68, -0.35) * mm});
            skLineSegment(sketch, "E2247", {"start": v(0.68, -0.35) * mm, "end": v(0.68, -0.36) * mm});
            skLineSegment(sketch, "E2248", {"start": v(0.68, -0.36) * mm, "end": v(0.68, -0.36) * mm});
            skLineSegment(sketch, "E2249", {"start": v(0.68, -0.36) * mm, "end": v(0.68, -0.37) * mm});
            skLineSegment(sketch, "E2250", {"start": v(0.68, -0.37) * mm, "end": v(0.68, -0.37) * mm});
            skLineSegment(sketch, "E2251", {"start": v(0.68, -0.37) * mm, "end": v(0.69, -0.37) * mm});
            skLineSegment(sketch, "E2252", {"start": v(0.69, -0.37) * mm, "end": v(0.69, -0.38) * mm});
            skLineSegment(sketch, "E2253", {"start": v(0.69, -0.38) * mm, "end": v(0.69, -0.38) * mm});
            skLineSegment(sketch, "E2254", {"start": v(0.69, -0.38) * mm, "end": v(0.7, -0.38) * mm});
            skLineSegment(sketch, "E2255", {"start": v(0.7, -0.38) * mm, "end": v(0.7, -0.38) * mm});
            skLineSegment(sketch, "E2256", {"start": v(0.7, -0.38) * mm, "end": v(0.7, -0.39) * mm});
            skLineSegment(sketch, "E2257", {"start": v(0.7, -0.39) * mm, "end": v(0.7, -0.39) * mm});
            skLineSegment(sketch, "E2258", {"start": v(0.7, -0.39) * mm, "end": v(0.7, -0.4) * mm});
            skLineSegment(sketch, "E2259", {"start": v(0.7, -0.4) * mm, "end": v(0.7, -0.4) * mm});
            skLineSegment(sketch, "E2260", {"start": v(0.7, -0.4) * mm, "end": v(0.7, -0.41) * mm});
            skLineSegment(sketch, "E2261", {"start": v(0.7, -0.41) * mm, "end": v(0.7, -0.41) * mm});
            skLineSegment(sketch, "E2262", {"start": v(0.7, -0.41) * mm, "end": v(0.71, -0.42) * mm});
            skLineSegment(sketch, "E2263", {"start": v(0.71, -0.42) * mm, "end": v(0.71, -0.42) * mm});
            skLineSegment(sketch, "E2264", {"start": v(0.71, -0.42) * mm, "end": v(0.71, -0.43) * mm});
            skLineSegment(sketch, "E2265", {"start": v(0.71, -0.43) * mm, "end": v(0.72, -0.43) * mm});
            skLineSegment(sketch, "E2266", {"start": v(0.72, -0.43) * mm, "end": v(0.72, -0.43) * mm});
            skLineSegment(sketch, "E2267", {"start": v(0.72, -0.43) * mm, "end": v(0.72, -0.44) * mm});
            skLineSegment(sketch, "E2268", {"start": v(0.72, -0.44) * mm, "end": v(0.72, -0.44) * mm});
            skLineSegment(sketch, "E2269", {"start": v(0.72, -0.44) * mm, "end": v(0.72, -0.45) * mm});
            skLineSegment(sketch, "E2270", {"start": v(0.72, -0.45) * mm, "end": v(0.73, -0.45) * mm});
            skLineSegment(sketch, "E2271", {"start": v(0.73, -0.45) * mm, "end": v(0.73, -0.45) * mm});
            skLineSegment(sketch, "E2272", {"start": v(0.73, -0.45) * mm, "end": v(0.73, -0.46) * mm});
            skLineSegment(sketch, "E2273", {"start": v(0.73, -0.46) * mm, "end": v(0.73, -0.46) * mm});
            skLineSegment(sketch, "E2274", {"start": v(0.73, -0.46) * mm, "end": v(0.73, -0.47) * mm});
            skLineSegment(sketch, "E2275", {"start": v(0.73, -0.47) * mm, "end": v(0.74, -0.47) * mm});
            skLineSegment(sketch, "E2276", {"start": v(0.74, -0.47) * mm, "end": v(0.74, -0.47) * mm});
            skLineSegment(sketch, "E2277", {"start": v(0.74, -0.47) * mm, "end": v(0.74, -0.48) * mm});
            skLineSegment(sketch, "E2278", {"start": v(0.74, -0.48) * mm, "end": v(0.74, -0.48) * mm});
            skLineSegment(sketch, "E2279", {"start": v(0.74, -0.48) * mm, "end": v(0.75, -0.49) * mm});
            skLineSegment(sketch, "E2280", {"start": v(0.75, -0.49) * mm, "end": v(0.75, -0.5) * mm});
            skLineSegment(sketch, "E2281", {"start": v(0.75, -0.5) * mm, "end": v(0.75, -0.5) * mm});
            skLineSegment(sketch, "E2282", {"start": v(0.75, -0.5) * mm, "end": v(0.76, -0.5) * mm});
            skLineSegment(sketch, "E2283", {"start": v(0.76, -0.5) * mm, "end": v(0.76, -0.5) * mm});
            skLineSegment(sketch, "E2284", {"start": v(0.76, -0.5) * mm, "end": v(0.76, -0.51) * mm});
            skLineSegment(sketch, "E2285", {"start": v(0.76, -0.51) * mm, "end": v(0.76, -0.52) * mm});
            skLineSegment(sketch, "E2286", {"start": v(0.76, -0.52) * mm, "end": v(0.77, -0.52) * mm});
            skLineSegment(sketch, "E2287", {"start": v(0.77, -0.52) * mm, "end": v(0.77, -0.52) * mm});
            skLineSegment(sketch, "E2288", {"start": v(0.77, -0.52) * mm, "end": v(0.77, -0.53) * mm});
            skLineSegment(sketch, "E2289", {"start": v(-6.44, 2.58) * mm, "end": v(-6.44, 2.58) * mm});
            skLineSegment(sketch, "E2290", {"start": v(-6.44, 2.58) * mm, "end": v(-6.44, 2.56) * mm});
            skLineSegment(sketch, "E2291", {"start": v(-6.44, 2.56) * mm, "end": v(-6.44, 2.53) * mm});
            skLineSegment(sketch, "E2292", {"start": v(-6.44, 2.53) * mm, "end": v(-6.44, 2.49) * mm});
            skLineSegment(sketch, "E2293", {"start": v(-6.44, 2.49) * mm, "end": v(-6.44, 2.44) * mm});
            skLineSegment(sketch, "E2294", {"start": v(-6.44, 2.44) * mm, "end": v(-6.44, 2.38) * mm});
            skLineSegment(sketch, "E2295", {"start": v(-6.44, 2.38) * mm, "end": v(-6.44, 2.3) * mm});
            skLineSegment(sketch, "E2296", {"start": v(-6.44, 2.3) * mm, "end": v(-6.44, 2.23) * mm});
            skLineSegment(sketch, "E2297", {"start": v(-6.44, 2.23) * mm, "end": v(-6.44, 2.14) * mm});
            skLineSegment(sketch, "E2298", {"start": v(-6.44, 2.14) * mm, "end": v(-6.44, 2.04) * mm});
            skLineSegment(sketch, "E2299", {"start": v(-6.44, 2.04) * mm, "end": v(-6.44, 1.94) * mm});
            skLineSegment(sketch, "E2300", {"start": v(-6.44, 1.94) * mm, "end": v(-6.44, 1.83) * mm});
            skLineSegment(sketch, "E2301", {"start": v(-6.44, 1.83) * mm, "end": v(-6.44, 1.71) * mm});
            skLineSegment(sketch, "E2302", {"start": v(-6.44, 1.71) * mm, "end": v(-6.44, 1.59) * mm});
            skLineSegment(sketch, "E2303", {"start": v(-6.44, 1.59) * mm, "end": v(-6.44, 1.46) * mm});
            skLineSegment(sketch, "E2304", {"start": v(-6.44, 1.46) * mm, "end": v(-6.44, 1.33) * mm});
            skLineSegment(sketch, "E2305", {"start": v(-6.44, 1.33) * mm, "end": v(-6.44, 1.2) * mm});
            skLineSegment(sketch, "E2306", {"start": v(-6.44, 1.2) * mm, "end": v(-6.44, 1.05) * mm});
            skLineSegment(sketch, "E2307", {"start": v(-6.44, 1.05) * mm, "end": v(-6.44, 0.9) * mm});
            skLineSegment(sketch, "E2308", {"start": v(-6.44, 0.9) * mm, "end": v(-6.44, 0.76) * mm});
            skLineSegment(sketch, "E2309", {"start": v(-6.44, 0.76) * mm, "end": v(-6.44, 0.6) * mm});
            skLineSegment(sketch, "E2310", {"start": v(-6.44, 0.6) * mm, "end": v(-6.44, 0.45) * mm});
            skLineSegment(sketch, "E2311", {"start": v(-6.44, 0.45) * mm, "end": v(-6.44, 0.3) * mm});
            skLineSegment(sketch, "E2312", {"start": v(-6.44, 0.3) * mm, "end": v(-6.44, 0.15) * mm});
            skLineSegment(sketch, "E2313", {"start": v(-6.44, 0.15) * mm, "end": v(-6.44, -0.01) * mm});
            skLineSegment(sketch, "E2314", {"start": v(-6.44, -0.01) * mm, "end": v(-6.44, -0.17) * mm});
            skLineSegment(sketch, "E2315", {"start": v(-6.44, -0.17) * mm, "end": v(-6.44, -0.32) * mm});
            skLineSegment(sketch, "E2316", {"start": v(-6.44, -0.32) * mm, "end": v(-6.44, -0.47) * mm});
            skLineSegment(sketch, "E2317", {"start": v(-6.44, -0.47) * mm, "end": v(-6.44, -0.63) * mm});
            skLineSegment(sketch, "E2318", {"start": v(-6.44, -0.63) * mm, "end": v(-6.44, -0.78) * mm});
            skLineSegment(sketch, "E2319", {"start": v(-6.44, -0.78) * mm, "end": v(-6.44, -0.93) * mm});
            skLineSegment(sketch, "E2320", {"start": v(-6.44, -0.93) * mm, "end": v(-6.44, -1.07) * mm});
            skLineSegment(sketch, "E2321", {"start": v(-6.44, -1.07) * mm, "end": v(-6.44, -1.21) * mm});
            skLineSegment(sketch, "E2322", {"start": v(-6.44, -1.21) * mm, "end": v(-6.44, -1.35) * mm});
            skLineSegment(sketch, "E2323", {"start": v(-6.44, -1.35) * mm, "end": v(-6.44, -1.48) * mm});
            skLineSegment(sketch, "E2324", {"start": v(-6.44, -1.48) * mm, "end": v(-6.44, -1.61) * mm});
            skLineSegment(sketch, "E2325", {"start": v(-6.44, -1.61) * mm, "end": v(-6.44, -1.73) * mm});
            skLineSegment(sketch, "E2326", {"start": v(-6.44, -1.73) * mm, "end": v(-6.44, -1.85) * mm});
            skLineSegment(sketch, "E2327", {"start": v(-6.44, -1.85) * mm, "end": v(-6.44, -1.96) * mm});
            skLineSegment(sketch, "E2328", {"start": v(-6.44, -1.96) * mm, "end": v(-6.44, -2.06) * mm});
            skLineSegment(sketch, "E2329", {"start": v(-6.44, -2.06) * mm, "end": v(-6.44, -2.16) * mm});
            skLineSegment(sketch, "E2330", {"start": v(-6.44, -2.16) * mm, "end": v(-6.44, -2.25) * mm});
            skLineSegment(sketch, "E2331", {"start": v(-6.44, -2.25) * mm, "end": v(-6.44, -2.33) * mm});
            skLineSegment(sketch, "E2332", {"start": v(-6.44, -2.33) * mm, "end": v(-6.44, -2.4) * mm});
            skLineSegment(sketch, "E2333", {"start": v(-6.44, -2.4) * mm, "end": v(-6.44, -2.46) * mm});
            skLineSegment(sketch, "E2334", {"start": v(-6.44, -2.46) * mm, "end": v(-6.44, -2.5) * mm});
            skLineSegment(sketch, "E2335", {"start": v(-6.44, -2.5) * mm, "end": v(-6.44, -2.55) * mm});
            skLineSegment(sketch, "E2336", {"start": v(-6.44, -2.55) * mm, "end": v(-6.44, -2.58) * mm});
            skLineSegment(sketch, "E2337", {"start": v(-6.44, -2.58) * mm, "end": v(-6.44, -2.6) * mm});
            skLineSegment(sketch, "E2338", {"start": v(-6.44, -2.6) * mm, "end": v(-6.44, -2.6) * mm});
            skLineSegment(sketch, "E2339", {"start": v(-6.44, -2.6) * mm, "end": v(-6.44, -2.61) * mm});
            skLineSegment(sketch, "E2340", {"start": v(-6.44, -2.61) * mm, "end": v(-6.44, -2.61) * mm});
            skLineSegment(sketch, "E2341", {"start": v(-6.44, -2.61) * mm, "end": v(-6.44, -2.62) * mm});
            skLineSegment(sketch, "E2342", {"start": v(-6.44, -2.62) * mm, "end": v(-6.44, -2.62) * mm});
            skLineSegment(sketch, "E2343", {"start": v(-6.44, -2.62) * mm, "end": v(-6.44, -2.63) * mm});
            skLineSegment(sketch, "E2344", {"start": v(-6.44, -2.63) * mm, "end": v(-6.44, -2.63) * mm});
            skLineSegment(sketch, "E2345", {"start": v(-6.44, -2.63) * mm, "end": v(-6.44, -2.64) * mm});
            skLineSegment(sketch, "E2346", {"start": v(-6.44, -2.64) * mm, "end": v(-6.44, -2.64) * mm});
            skLineSegment(sketch, "E2347", {"start": v(-6.44, -2.64) * mm, "end": v(-6.44, -2.65) * mm});
            skLineSegment(sketch, "E2348", {"start": v(-6.44, -2.65) * mm, "end": v(-6.44, -2.65) * mm});
            skLineSegment(sketch, "E2349", {"start": v(-6.44, -2.65) * mm, "end": v(-6.45, -2.66) * mm});
            skLineSegment(sketch, "E2350", {"start": v(-6.45, -2.66) * mm, "end": v(-6.45, -2.66) * mm});
            skLineSegment(sketch, "E2351", {"start": v(-6.45, -2.66) * mm, "end": v(-6.45, -2.67) * mm});
            skLineSegment(sketch, "E2352", {"start": v(-6.45, -2.67) * mm, "end": v(-6.45, -2.67) * mm});
            skLineSegment(sketch, "E2353", {"start": v(-6.45, -2.67) * mm, "end": v(-6.45, -2.68) * mm});
            skLineSegment(sketch, "E2354", {"start": v(-6.45, -2.68) * mm, "end": v(-6.46, -2.68) * mm});
            skLineSegment(sketch, "E2355", {"start": v(-6.46, -2.68) * mm, "end": v(-6.46, -2.69) * mm});
            skLineSegment(sketch, "E2356", {"start": v(-6.46, -2.69) * mm, "end": v(-6.46, -2.7) * mm});
            skLineSegment(sketch, "E2357", {"start": v(-6.46, -2.7) * mm, "end": v(-6.46, -2.7) * mm});
            skLineSegment(sketch, "E2358", {"start": v(-6.46, -2.7) * mm, "end": v(-6.47, -2.7) * mm});
            skLineSegment(sketch, "E2359", {"start": v(-6.47, -2.7) * mm, "end": v(-6.47, -2.7) * mm});
            skLineSegment(sketch, "E2360", {"start": v(-6.47, -2.7) * mm, "end": v(-6.47, -2.71) * mm});
            skLineSegment(sketch, "E2361", {"start": v(-6.47, -2.71) * mm, "end": v(-6.48, -2.71) * mm});
            skLineSegment(sketch, "E2362", {"start": v(-6.48, -2.71) * mm, "end": v(-6.48, -2.72) * mm});
            skLineSegment(sketch, "E2363", {"start": v(-6.48, -2.72) * mm, "end": v(-6.48, -2.72) * mm});
            skLineSegment(sketch, "E2364", {"start": v(-6.48, -2.72) * mm, "end": v(-6.49, -2.73) * mm});
            skLineSegment(sketch, "E2365", {"start": v(-6.49, -2.73) * mm, "end": v(-6.49, -2.73) * mm});
            skLineSegment(sketch, "E2366", {"start": v(-6.49, -2.73) * mm, "end": v(-6.5, -2.73) * mm});
            skLineSegment(sketch, "E2367", {"start": v(-6.5, -2.73) * mm, "end": v(-6.5, -2.74) * mm});
            skLineSegment(sketch, "E2368", {"start": v(-6.5, -2.74) * mm, "end": v(-6.5, -2.74) * mm});
            skLineSegment(sketch, "E2369", {"start": v(-6.5, -2.74) * mm, "end": v(-6.51, -2.75) * mm});
            skLineSegment(sketch, "E2370", {"start": v(-6.51, -2.75) * mm, "end": v(-6.52, -2.75) * mm});
            skLineSegment(sketch, "E2371", {"start": v(-6.52, -2.75) * mm, "end": v(-6.52, -2.75) * mm});
            skLineSegment(sketch, "E2372", {"start": v(-6.52, -2.75) * mm, "end": v(-6.53, -2.76) * mm});
            skLineSegment(sketch, "E2373", {"start": v(-6.53, -2.76) * mm, "end": v(-6.53, -2.76) * mm});
            skLineSegment(sketch, "E2374", {"start": v(-6.53, -2.76) * mm, "end": v(-6.54, -2.76) * mm});
            skLineSegment(sketch, "E2375", {"start": v(-6.54, -2.76) * mm, "end": v(-6.54, -2.76) * mm});
            skLineSegment(sketch, "E2376", {"start": v(-6.54, -2.76) * mm, "end": v(-6.55, -2.76) * mm});
            skLineSegment(sketch, "E2377", {"start": v(-6.55, -2.76) * mm, "end": v(-6.55, -2.76) * mm});
            skLineSegment(sketch, "E2378", {"start": v(-6.55, -2.76) * mm, "end": v(-6.56, -2.77) * mm});
            skLineSegment(sketch, "E2379", {"start": v(-6.56, -2.77) * mm, "end": v(-6.56, -2.77) * mm});
            skLineSegment(sketch, "E2380", {"start": v(-6.56, -2.77) * mm, "end": v(-6.57, -2.77) * mm});
            skLineSegment(sketch, "E2381", {"start": v(-6.57, -2.77) * mm, "end": v(-6.57, -2.77) * mm});
            skLineSegment(sketch, "E2382", {"start": v(-6.57, -2.77) * mm, "end": v(-6.58, -2.77) * mm});
            skLineSegment(sketch, "E2383", {"start": v(-6.58, -2.77) * mm, "end": v(-6.59, -2.77) * mm});
            skLineSegment(sketch, "E2384", {"start": v(-6.59, -2.77) * mm, "end": v(-6.6, -2.77) * mm});
            skLineSegment(sketch, "E2385", {"start": v(-6.6, -2.77) * mm, "end": v(-6.6, -2.77) * mm});
            skLineSegment(sketch, "E2386", {"start": v(-6.6, -2.77) * mm, "end": v(-6.6, -2.76) * mm});
            skLineSegment(sketch, "E2387", {"start": v(-6.6, -2.76) * mm, "end": v(-6.61, -2.76) * mm});
            skLineSegment(sketch, "E2388", {"start": v(-6.61, -2.76) * mm, "end": v(-6.62, -2.76) * mm});
            skLineSegment(sketch, "E2389", {"start": v(-6.62, -2.76) * mm, "end": v(-6.62, -2.76) * mm});
            skLineSegment(sketch, "E2390", {"start": v(-6.62, -2.76) * mm, "end": v(-6.63, -2.76) * mm});
            skLineSegment(sketch, "E2391", {"start": v(-6.63, -2.76) * mm, "end": v(-6.63, -2.76) * mm});
            skLineSegment(sketch, "E2392", {"start": v(-6.63, -2.76) * mm, "end": v(-6.63, -2.75) * mm});
            skLineSegment(sketch, "E2393", {"start": v(-6.63, -2.75) * mm, "end": v(-6.64, -2.75) * mm});
            skLineSegment(sketch, "E2394", {"start": v(-6.64, -2.75) * mm, "end": v(-6.64, -2.75) * mm});
            skLineSegment(sketch, "E2395", {"start": v(-6.64, -2.75) * mm, "end": v(-6.65, -2.75) * mm});
            skLineSegment(sketch, "E2396", {"start": v(-6.65, -2.75) * mm, "end": v(-6.65, -2.74) * mm});
            skLineSegment(sketch, "E2397", {"start": v(-6.65, -2.74) * mm, "end": v(-6.66, -2.74) * mm});
            skLineSegment(sketch, "E2398", {"start": v(-6.66, -2.74) * mm, "end": v(-6.66, -2.74) * mm});
            skLineSegment(sketch, "E2399", {"start": v(-6.66, -2.74) * mm, "end": v(-6.66, -2.73) * mm});
            skLineSegment(sketch, "E2400", {"start": v(-6.66, -2.73) * mm, "end": v(-6.67, -2.73) * mm});
            skLineSegment(sketch, "E2401", {"start": v(-6.67, -2.73) * mm, "end": v(-6.67, -2.73) * mm});
            skLineSegment(sketch, "E2402", {"start": v(-6.67, -2.73) * mm, "end": v(-6.67, -2.72) * mm});
            skLineSegment(sketch, "E2403", {"start": v(-6.67, -2.72) * mm, "end": v(-6.68, -2.72) * mm});
            skLineSegment(sketch, "E2404", {"start": v(-6.68, -2.72) * mm, "end": v(-6.68, -2.72) * mm});
            skLineSegment(sketch, "E2405", {"start": v(-6.68, -2.72) * mm, "end": v(-6.68, -2.71) * mm});
            skLineSegment(sketch, "E2406", {"start": v(-6.68, -2.71) * mm, "end": v(-6.69, -2.7) * mm});
            skLineSegment(sketch, "E2407", {"start": v(-6.69, -2.7) * mm, "end": v(-6.69, -2.7) * mm});
            skLineSegment(sketch, "E2408", {"start": v(-6.69, -2.7) * mm, "end": v(-6.7, -2.7) * mm});
            skLineSegment(sketch, "E2409", {"start": v(-6.7, -2.7) * mm, "end": v(-6.7, -2.7) * mm});
            skLineSegment(sketch, "E2410", {"start": v(-6.7, -2.7) * mm, "end": v(-6.7, -2.69) * mm});
            skLineSegment(sketch, "E2411", {"start": v(-6.7, -2.69) * mm, "end": v(-6.7, -2.68) * mm});
            skLineSegment(sketch, "E2412", {"start": v(-6.7, -2.68) * mm, "end": v(-6.7, -2.68) * mm});
            skLineSegment(sketch, "E2413", {"start": v(-6.7, -2.68) * mm, "end": v(-6.7, -2.67) * mm});
            skLineSegment(sketch, "E2414", {"start": v(-6.7, -2.67) * mm, "end": v(-6.7, -2.67) * mm});
            skLineSegment(sketch, "E2415", {"start": v(-6.7, -2.67) * mm, "end": v(-6.7, -2.66) * mm});
            skLineSegment(sketch, "E2416", {"start": v(-6.7, -2.66) * mm, "end": v(-6.7, -2.66) * mm});
            skLineSegment(sketch, "E2417", {"start": v(-6.7, -2.66) * mm, "end": v(-6.71, -2.65) * mm});
            skLineSegment(sketch, "E2418", {"start": v(-6.71, -2.65) * mm, "end": v(-6.71, -2.65) * mm});
            skLineSegment(sketch, "E2419", {"start": v(-6.71, -2.65) * mm, "end": v(-6.71, -2.64) * mm});
            skLineSegment(sketch, "E2420", {"start": v(-6.71, -2.64) * mm, "end": v(-6.72, -2.63) * mm});
            skLineSegment(sketch, "E2421", {"start": v(-6.72, -2.63) * mm, "end": v(-6.72, -2.63) * mm});
            skLineSegment(sketch, "E2422", {"start": v(-6.72, -2.63) * mm, "end": v(-6.72, -2.62) * mm});
            skLineSegment(sketch, "E2423", {"start": v(-6.72, -2.62) * mm, "end": v(-6.72, -2.62) * mm});
            skLineSegment(sketch, "E2424", {"start": v(-6.72, -2.62) * mm, "end": v(-6.72, -2.61) * mm});
            skLineSegment(sketch, "E2425", {"start": v(-6.72, -2.61) * mm, "end": v(-6.72, -2.6) * mm});
            skLineSegment(sketch, "E2426", {"start": v(-6.72, -2.6) * mm, "end": v(-6.72, -2.6) * mm});
            skLineSegment(sketch, "E2427", {"start": v(-6.72, -2.6) * mm, "end": v(-6.72, -2.59) * mm});
            skLineSegment(sketch, "E2428", {"start": v(-6.72, -2.59) * mm, "end": v(-6.72, -2.58) * mm});
            skLineSegment(sketch, "E2429", {"start": v(-6.72, -2.58) * mm, "end": v(-6.72, -2.58) * mm});
            skLineSegment(sketch, "E2430", {"start": v(-6.72, -2.58) * mm, "end": v(-6.72, -2.57) * mm});
            skLineSegment(sketch, "E2431", {"start": v(-6.72, -2.57) * mm, "end": v(-6.72, -2.55) * mm});
            skLineSegment(sketch, "E2432", {"start": v(-6.72, -2.55) * mm, "end": v(-6.72, -2.52) * mm});
            skLineSegment(sketch, "E2433", {"start": v(-6.72, -2.52) * mm, "end": v(-6.72, -2.48) * mm});
            skLineSegment(sketch, "E2434", {"start": v(-6.72, -2.48) * mm, "end": v(-6.72, -2.43) * mm});
            skLineSegment(sketch, "E2435", {"start": v(-6.72, -2.43) * mm, "end": v(-6.72, -2.37) * mm});
            skLineSegment(sketch, "E2436", {"start": v(-6.72, -2.37) * mm, "end": v(-6.72, -2.3) * mm});
            skLineSegment(sketch, "E2437", {"start": v(-6.72, -2.3) * mm, "end": v(-6.72, -2.22) * mm});
            skLineSegment(sketch, "E2438", {"start": v(-6.72, -2.22) * mm, "end": v(-6.72, -2.13) * mm});
            skLineSegment(sketch, "E2439", {"start": v(-6.72, -2.13) * mm, "end": v(-6.72, -2.04) * mm});
            skLineSegment(sketch, "E2440", {"start": v(-6.72, -2.04) * mm, "end": v(-6.72, -1.93) * mm});
            skLineSegment(sketch, "E2441", {"start": v(-6.72, -1.93) * mm, "end": v(-6.72, -1.82) * mm});
            skLineSegment(sketch, "E2442", {"start": v(-6.72, -1.82) * mm, "end": v(-6.72, -1.7) * mm});
            skLineSegment(sketch, "E2443", {"start": v(-6.72, -1.7) * mm, "end": v(-6.72, -1.58) * mm});
            skLineSegment(sketch, "E2444", {"start": v(-6.72, -1.58) * mm, "end": v(-6.72, -1.45) * mm});
            skLineSegment(sketch, "E2445", {"start": v(-6.72, -1.45) * mm, "end": v(-6.72, -1.32) * mm});
            skLineSegment(sketch, "E2446", {"start": v(-6.72, -1.32) * mm, "end": v(-6.72, -1.18) * mm});
            skLineSegment(sketch, "E2447", {"start": v(-6.72, -1.18) * mm, "end": v(-6.72, -1.04) * mm});
            skLineSegment(sketch, "E2448", {"start": v(-6.72, -1.04) * mm, "end": v(-6.72, -0.9) * mm});
            skLineSegment(sketch, "E2449", {"start": v(-6.72, -0.9) * mm, "end": v(-6.72, -0.75) * mm});
            skLineSegment(sketch, "E2450", {"start": v(-6.72, -0.75) * mm, "end": v(-6.72, -0.6) * mm});
            skLineSegment(sketch, "E2451", {"start": v(-6.72, -0.6) * mm, "end": v(-6.72, -0.44) * mm});
            skLineSegment(sketch, "E2452", {"start": v(-6.72, -0.44) * mm, "end": v(-6.72, -0.29) * mm});
            skLineSegment(sketch, "E2453", {"start": v(-6.72, -0.29) * mm, "end": v(-6.72, -0.13) * mm});
            skLineSegment(sketch, "E2454", {"start": v(-6.72, -0.13) * mm, "end": v(-6.72, 0.02) * mm});
            skLineSegment(sketch, "E2455", {"start": v(-6.72, 0.02) * mm, "end": v(-6.72, 0.18) * mm});
            skLineSegment(sketch, "E2456", {"start": v(-6.72, 0.18) * mm, "end": v(-6.72, 0.34) * mm});
            skLineSegment(sketch, "E2457", {"start": v(-6.72, 0.34) * mm, "end": v(-6.72, 0.5) * mm});
            skLineSegment(sketch, "E2458", {"start": v(-6.72, 0.5) * mm, "end": v(-6.72, 0.64) * mm});
            skLineSegment(sketch, "E2459", {"start": v(-6.72, 0.64) * mm, "end": v(-6.72, 0.8) * mm});
            skLineSegment(sketch, "E2460", {"start": v(-6.72, 0.8) * mm, "end": v(-6.72, 0.94) * mm});
            skLineSegment(sketch, "E2461", {"start": v(-6.72, 0.94) * mm, "end": v(-6.72, 1.09) * mm});
            skLineSegment(sketch, "E2462", {"start": v(-6.72, 1.09) * mm, "end": v(-6.72, 1.23) * mm});
            skLineSegment(sketch, "E2463", {"start": v(-6.72, 1.23) * mm, "end": v(-6.72, 1.37) * mm});
            skLineSegment(sketch, "E2464", {"start": v(-6.72, 1.37) * mm, "end": v(-6.72, 1.5) * mm});
            skLineSegment(sketch, "E2465", {"start": v(-6.72, 1.5) * mm, "end": v(-6.72, 1.63) * mm});
            skLineSegment(sketch, "E2466", {"start": v(-6.72, 1.63) * mm, "end": v(-6.72, 1.76) * mm});
            skLineSegment(sketch, "E2467", {"start": v(-6.72, 1.76) * mm, "end": v(-6.72, 1.87) * mm});
            skLineSegment(sketch, "E2468", {"start": v(-6.72, 1.87) * mm, "end": v(-6.72, 1.98) * mm});
            skLineSegment(sketch, "E2469", {"start": v(-6.72, 1.98) * mm, "end": v(-6.72, 2.09) * mm});
            skLineSegment(sketch, "E2470", {"start": v(-6.72, 2.09) * mm, "end": v(-6.72, 2.18) * mm});
            skLineSegment(sketch, "E2471", {"start": v(-6.72, 2.18) * mm, "end": v(-6.72, 2.27) * mm});
            skLineSegment(sketch, "E2472", {"start": v(-6.72, 2.27) * mm, "end": v(-6.72, 2.35) * mm});
            skLineSegment(sketch, "E2473", {"start": v(-6.72, 2.35) * mm, "end": v(-6.72, 2.42) * mm});
            skLineSegment(sketch, "E2474", {"start": v(-6.72, 2.42) * mm, "end": v(-6.72, 2.48) * mm});
            skLineSegment(sketch, "E2475", {"start": v(-6.72, 2.48) * mm, "end": v(-6.72, 2.53) * mm});
            skLineSegment(sketch, "E2476", {"start": v(-6.72, 2.53) * mm, "end": v(-6.72, 2.57) * mm});
            skLineSegment(sketch, "E2477", {"start": v(-6.72, 2.57) * mm, "end": v(-6.72, 2.6) * mm});
            skLineSegment(sketch, "E2478", {"start": v(-6.72, 2.6) * mm, "end": v(-6.72, 2.62) * mm});
            skLineSegment(sketch, "E2479", {"start": v(-6.72, 2.62) * mm, "end": v(-6.72, 2.63) * mm});
            skLineSegment(sketch, "E2480", {"start": v(-6.72, 2.63) * mm, "end": v(-6.72, 2.65) * mm});
            skLineSegment(sketch, "E2481", {"start": v(-6.72, 2.65) * mm, "end": v(-6.72, 2.68) * mm});
            skLineSegment(sketch, "E2482", {"start": v(-6.72, 2.68) * mm, "end": v(-6.72, 2.7) * mm});
            skLineSegment(sketch, "E2483", {"start": v(-6.72, 2.7) * mm, "end": v(-6.73, 2.72) * mm});
            skLineSegment(sketch, "E2484", {"start": v(-6.73, 2.72) * mm, "end": v(-6.73, 2.74) * mm});
            skLineSegment(sketch, "E2485", {"start": v(-6.73, 2.74) * mm, "end": v(-6.73, 2.76) * mm});
            skLineSegment(sketch, "E2486", {"start": v(-6.73, 2.76) * mm, "end": v(-6.74, 2.79) * mm});
            skLineSegment(sketch, "E2487", {"start": v(-6.74, 2.79) * mm, "end": v(-6.74, 2.8) * mm});
            skLineSegment(sketch, "E2488", {"start": v(-6.74, 2.8) * mm, "end": v(-6.75, 2.83) * mm});
            skLineSegment(sketch, "E2489", {"start": v(-6.75, 2.83) * mm, "end": v(-6.76, 2.85) * mm});
            skLineSegment(sketch, "E2490", {"start": v(-6.76, 2.85) * mm, "end": v(-6.76, 2.87) * mm});
            skLineSegment(sketch, "E2491", {"start": v(-6.76, 2.87) * mm, "end": v(-6.77, 2.88) * mm});
            skLineSegment(sketch, "E2492", {"start": v(-6.77, 2.88) * mm, "end": v(-6.78, 2.9) * mm});
            skLineSegment(sketch, "E2493", {"start": v(-6.78, 2.9) * mm, "end": v(-6.79, 2.92) * mm});
            skLineSegment(sketch, "E2494", {"start": v(-6.79, 2.92) * mm, "end": v(-6.8, 2.94) * mm});
            skLineSegment(sketch, "E2495", {"start": v(-6.8, 2.94) * mm, "end": v(-6.8, 2.95) * mm});
            skLineSegment(sketch, "E2496", {"start": v(-6.8, 2.95) * mm, "end": v(-6.82, 2.97) * mm});
            skLineSegment(sketch, "E2497", {"start": v(-6.82, 2.97) * mm, "end": v(-6.83, 2.99) * mm});
            skLineSegment(sketch, "E2498", {"start": v(-6.83, 2.99) * mm, "end": v(-6.84, 3) * mm});
            skLineSegment(sketch, "E2499", {"start": v(-6.84, 3) * mm, "end": v(-6.85, 3.02) * mm});
            skLineSegment(sketch, "E2500", {"start": v(-6.85, 3.02) * mm, "end": v(-6.86, 3.03) * mm});
            skLineSegment(sketch, "E2501", {"start": v(-6.86, 3.03) * mm, "end": v(-6.87, 3.05) * mm});
            skLineSegment(sketch, "E2502", {"start": v(-6.87, 3.05) * mm, "end": v(-6.89, 3.06) * mm});
            skLineSegment(sketch, "E2503", {"start": v(-6.89, 3.06) * mm, "end": v(-6.9, 3.07) * mm});
            skLineSegment(sketch, "E2504", {"start": v(-6.9, 3.07) * mm, "end": v(-6.92, 3.08) * mm});
            skLineSegment(sketch, "E2505", {"start": v(-6.92, 3.08) * mm, "end": v(-6.93, 3.1) * mm});
            skLineSegment(sketch, "E2506", {"start": v(-6.93, 3.1) * mm, "end": v(-6.94, 3.1) * mm});
            skLineSegment(sketch, "E2507", {"start": v(-6.94, 3.1) * mm, "end": v(-6.96, 3.12) * mm});
            skLineSegment(sketch, "E2508", {"start": v(-6.96, 3.12) * mm, "end": v(-6.97, 3.13) * mm});
            skLineSegment(sketch, "E2509", {"start": v(-6.97, 3.13) * mm, "end": v(-7, 3.14) * mm});
            skLineSegment(sketch, "E2510", {"start": v(-7, 3.14) * mm, "end": v(-7, 3.15) * mm});
            skLineSegment(sketch, "E2511", {"start": v(-7, 3.15) * mm, "end": v(-7.02, 3.16) * mm});
            skLineSegment(sketch, "E2512", {"start": v(-7.02, 3.16) * mm, "end": v(-7.04, 3.17) * mm});
            skLineSegment(sketch, "E2513", {"start": v(-7.04, 3.17) * mm, "end": v(-7.06, 3.18) * mm});
            skLineSegment(sketch, "E2514", {"start": v(-7.06, 3.18) * mm, "end": v(-7.07, 3.18) * mm});
            skLineSegment(sketch, "E2515", {"start": v(-7.07, 3.18) * mm, "end": v(-7.1, 3.2) * mm});
            skLineSegment(sketch, "E2516", {"start": v(-7.1, 3.2) * mm, "end": v(-7.1, 3.2) * mm});
            skLineSegment(sketch, "E2517", {"start": v(-7.1, 3.2) * mm, "end": v(-7.13, 3.2) * mm});
            skLineSegment(sketch, "E2518", {"start": v(-7.13, 3.2) * mm, "end": v(-7.15, 3.21) * mm});
            skLineSegment(sketch, "E2519", {"start": v(-7.15, 3.21) * mm, "end": v(-7.16, 3.22) * mm});
            skLineSegment(sketch, "E2520", {"start": v(-7.16, 3.22) * mm, "end": v(-7.18, 3.22) * mm});
            skLineSegment(sketch, "E2521", {"start": v(-7.18, 3.22) * mm, "end": v(-7.2, 3.22) * mm});
            skLineSegment(sketch, "E2522", {"start": v(-7.2, 3.22) * mm, "end": v(-7.22, 3.23) * mm});
            skLineSegment(sketch, "E2523", {"start": v(-7.22, 3.23) * mm, "end": v(-7.24, 3.23) * mm});
            skLineSegment(sketch, "E2524", {"start": v(-7.24, 3.23) * mm, "end": v(-7.26, 3.23) * mm});
            skLineSegment(sketch, "E2525", {"start": v(-7.26, 3.23) * mm, "end": v(-7.28, 3.24) * mm});
            skLineSegment(sketch, "E2526", {"start": v(-7.28, 3.24) * mm, "end": v(-7.3, 3.24) * mm});
            skLineSegment(sketch, "E2527", {"start": v(-7.3, 3.24) * mm, "end": v(-7.32, 3.24) * mm});
            skLineSegment(sketch, "E2528", {"start": v(-7.32, 3.24) * mm, "end": v(-7.34, 3.24) * mm});
            skLineSegment(sketch, "E2529", {"start": v(-7.34, 3.24) * mm, "end": v(-7.36, 3.24) * mm});
            skLineSegment(sketch, "E2530", {"start": v(-7.36, 3.24) * mm, "end": v(-7.38, 3.24) * mm});
            skLineSegment(sketch, "E2531", {"start": v(-7.38, 3.24) * mm, "end": v(-7.4, 3.24) * mm});
            skLineSegment(sketch, "E2532", {"start": v(-7.4, 3.24) * mm, "end": v(-7.42, 3.24) * mm});
            skLineSegment(sketch, "E2533", {"start": v(-7.42, 3.24) * mm, "end": v(-7.44, 3.24) * mm});
            skLineSegment(sketch, "E2534", {"start": v(-7.44, 3.24) * mm, "end": v(-7.45, 3.23) * mm});
            skLineSegment(sketch, "E2535", {"start": v(-7.45, 3.23) * mm, "end": v(-7.47, 3.23) * mm});
            skLineSegment(sketch, "E2536", {"start": v(-7.47, 3.23) * mm, "end": v(-7.5, 3.23) * mm});
            skLineSegment(sketch, "E2537", {"start": v(-7.5, 3.23) * mm, "end": v(-7.51, 3.22) * mm});
            skLineSegment(sketch, "E2538", {"start": v(-7.51, 3.22) * mm, "end": v(-7.53, 3.22) * mm});
            skLineSegment(sketch, "E2539", {"start": v(-7.53, 3.22) * mm, "end": v(-7.55, 3.22) * mm});
            skLineSegment(sketch, "E2540", {"start": v(-7.55, 3.22) * mm, "end": v(-7.57, 3.2) * mm});
            skLineSegment(sketch, "E2541", {"start": v(-7.57, 3.2) * mm, "end": v(-7.59, 3.2) * mm});
            skLineSegment(sketch, "E2542", {"start": v(-7.59, 3.2) * mm, "end": v(-7.6, 3.2) * mm});
            skLineSegment(sketch, "E2543", {"start": v(-7.6, 3.2) * mm, "end": v(-7.62, 3.2) * mm});
            skLineSegment(sketch, "E2544", {"start": v(-7.62, 3.2) * mm, "end": v(-7.64, 3.18) * mm});
            skLineSegment(sketch, "E2545", {"start": v(-7.64, 3.18) * mm, "end": v(-7.66, 3.18) * mm});
            skLineSegment(sketch, "E2546", {"start": v(-7.66, 3.18) * mm, "end": v(-7.67, 3.17) * mm});
            skLineSegment(sketch, "E2547", {"start": v(-7.67, 3.17) * mm, "end": v(-7.7, 3.16) * mm});
            skLineSegment(sketch, "E2548", {"start": v(-7.7, 3.16) * mm, "end": v(-7.7, 3.15) * mm});
            skLineSegment(sketch, "E2549", {"start": v(-7.7, 3.15) * mm, "end": v(-7.72, 3.14) * mm});
            skLineSegment(sketch, "E2550", {"start": v(-7.72, 3.14) * mm, "end": v(-7.74, 3.13) * mm});
            skLineSegment(sketch, "E2551", {"start": v(-7.74, 3.13) * mm, "end": v(-7.75, 3.12) * mm});
            skLineSegment(sketch, "E2552", {"start": v(-7.75, 3.12) * mm, "end": v(-7.77, 3.1) * mm});
            skLineSegment(sketch, "E2553", {"start": v(-7.77, 3.1) * mm, "end": v(-7.78, 3.1) * mm});
            skLineSegment(sketch, "E2554", {"start": v(-7.78, 3.1) * mm, "end": v(-7.8, 3.08) * mm});
            skLineSegment(sketch, "E2555", {"start": v(-7.8, 3.08) * mm, "end": v(-7.81, 3.07) * mm});
            skLineSegment(sketch, "E2556", {"start": v(-7.81, 3.07) * mm, "end": v(-7.83, 3.05) * mm});
            skLineSegment(sketch, "E2557", {"start": v(-7.83, 3.05) * mm, "end": v(-7.84, 3.04) * mm});
            skLineSegment(sketch, "E2558", {"start": v(-7.84, 3.04) * mm, "end": v(-7.85, 3.02) * mm});
            skLineSegment(sketch, "E2559", {"start": v(-7.85, 3.02) * mm, "end": v(-7.86, 3) * mm});
            skLineSegment(sketch, "E2560", {"start": v(-7.86, 3) * mm, "end": v(-7.88, 3) * mm});
            skLineSegment(sketch, "E2561", {"start": v(-7.88, 3) * mm, "end": v(-7.89, 2.97) * mm});
            skLineSegment(sketch, "E2562", {"start": v(-7.89, 2.97) * mm, "end": v(-7.9, 2.96) * mm});
            skLineSegment(sketch, "E2563", {"start": v(-7.9, 2.96) * mm, "end": v(-7.9, 2.94) * mm});
            skLineSegment(sketch, "E2564", {"start": v(-7.9, 2.94) * mm, "end": v(-7.92, 2.92) * mm});
            skLineSegment(sketch, "E2565", {"start": v(-7.92, 2.92) * mm, "end": v(-7.93, 2.9) * mm});
            skLineSegment(sketch, "E2566", {"start": v(-7.93, 2.9) * mm, "end": v(-7.94, 2.88) * mm});
            skLineSegment(sketch, "E2567", {"start": v(-7.94, 2.88) * mm, "end": v(-7.94, 2.86) * mm});
            skLineSegment(sketch, "E2568", {"start": v(-7.94, 2.86) * mm, "end": v(-7.95, 2.84) * mm});
            skLineSegment(sketch, "E2569", {"start": v(-7.95, 2.84) * mm, "end": v(-7.96, 2.82) * mm});
            skLineSegment(sketch, "E2570", {"start": v(-7.96, 2.82) * mm, "end": v(-7.96, 2.8) * mm});
            skLineSegment(sketch, "E2571", {"start": v(-7.96, 2.8) * mm, "end": v(-7.97, 2.78) * mm});
            skLineSegment(sketch, "E2572", {"start": v(-7.97, 2.78) * mm, "end": v(-7.98, 2.76) * mm});
            skLineSegment(sketch, "E2573", {"start": v(-7.98, 2.76) * mm, "end": v(-7.98, 2.73) * mm});
            skLineSegment(sketch, "E2574", {"start": v(-7.98, 2.73) * mm, "end": v(-7.98, 2.7) * mm});
            skLineSegment(sketch, "E2575", {"start": v(-7.98, 2.7) * mm, "end": v(-7.99, 2.68) * mm});
            skLineSegment(sketch, "E2576", {"start": v(-7.99, 2.68) * mm, "end": v(-7.99, 2.66) * mm});
            skLineSegment(sketch, "E2577", {"start": v(-7.99, 2.66) * mm, "end": v(-8, 2.63) * mm});
            skLineSegment(sketch, "E2578", {"start": v(-8, 2.63) * mm, "end": v(-8, 2.6) * mm});
            skLineSegment(sketch, "E2579", {"start": v(-8, 2.6) * mm, "end": v(-8, 2.58) * mm});
            skLineSegment(sketch, "E2580", {"start": v(-8, 2.58) * mm, "end": v(-8, 2.57) * mm});
            skLineSegment(sketch, "E2581", {"start": v(-8, 2.57) * mm, "end": v(-8, 2.56) * mm});
            skLineSegment(sketch, "E2582", {"start": v(-8, 2.56) * mm, "end": v(-8, 2.52) * mm});
            skLineSegment(sketch, "E2583", {"start": v(-8, 2.52) * mm, "end": v(-8, 2.48) * mm});
            skLineSegment(sketch, "E2584", {"start": v(-8, 2.48) * mm, "end": v(-8, 2.43) * mm});
            skLineSegment(sketch, "E2585", {"start": v(-8, 2.43) * mm, "end": v(-8, 2.36) * mm});
            skLineSegment(sketch, "E2586", {"start": v(-8, 2.36) * mm, "end": v(-8, 2.29) * mm});
            skLineSegment(sketch, "E2587", {"start": v(-8, 2.29) * mm, "end": v(-8, 2.2) * mm});
            skLineSegment(sketch, "E2588", {"start": v(-8, 2.2) * mm, "end": v(-8, 2.1) * mm});
            skLineSegment(sketch, "E2589", {"start": v(-8, 2.1) * mm, "end": v(-8, 2) * mm});
            skLineSegment(sketch, "E2590", {"start": v(-8, 2) * mm, "end": v(-8, 1.9) * mm});
            skLineSegment(sketch, "E2591", {"start": v(-8, 1.9) * mm, "end": v(-8, 1.78) * mm});
            skLineSegment(sketch, "E2592", {"start": v(-8, 1.78) * mm, "end": v(-8, 1.66) * mm});
            skLineSegment(sketch, "E2593", {"start": v(-8, 1.66) * mm, "end": v(-8, 1.53) * mm});
            skLineSegment(sketch, "E2594", {"start": v(-8, 1.53) * mm, "end": v(-8, 1.4) * mm});
            skLineSegment(sketch, "E2595", {"start": v(-8, 1.4) * mm, "end": v(-8, 1.25) * mm});
            skLineSegment(sketch, "E2596", {"start": v(-8, 1.25) * mm, "end": v(-8, 1.1) * mm});
            skLineSegment(sketch, "E2597", {"start": v(-8, 1.1) * mm, "end": v(-8, 0.95) * mm});
            skLineSegment(sketch, "E2598", {"start": v(-8, 0.95) * mm, "end": v(-8, 0.8) * mm});
            skLineSegment(sketch, "E2599", {"start": v(-8, 0.8) * mm, "end": v(-8, 0.64) * mm});
            skLineSegment(sketch, "E2600", {"start": v(-8, 0.64) * mm, "end": v(-8, 0.48) * mm});
            skLineSegment(sketch, "E2601", {"start": v(-8, 0.48) * mm, "end": v(-8, 0.32) * mm});
            skLineSegment(sketch, "E2602", {"start": v(-8, 0.32) * mm, "end": v(-8, 0.15) * mm});
            skLineSegment(sketch, "E2603", {"start": v(-8, 0.15) * mm, "end": v(-8, -0.01) * mm});
            skLineSegment(sketch, "E2604", {"start": v(-8, -0.01) * mm, "end": v(-8, -0.18) * mm});
            skLineSegment(sketch, "E2605", {"start": v(-8, -0.18) * mm, "end": v(-8, -0.34) * mm});
            skLineSegment(sketch, "E2606", {"start": v(-8, -0.34) * mm, "end": v(-8, -0.5) * mm});
            skLineSegment(sketch, "E2607", {"start": v(-8, -0.5) * mm, "end": v(-8, -0.67) * mm});
            skLineSegment(sketch, "E2608", {"start": v(-8, -0.67) * mm, "end": v(-8, -0.83) * mm});
            skLineSegment(sketch, "E2609", {"start": v(-8, -0.83) * mm, "end": v(-8, -1) * mm});
            skLineSegment(sketch, "E2610", {"start": v(-8, -1) * mm, "end": v(-8, -1.15) * mm});
            skLineSegment(sketch, "E2611", {"start": v(-8, -1.15) * mm, "end": v(-8, -1.3) * mm});
            skLineSegment(sketch, "E2612", {"start": v(-8, -1.3) * mm, "end": v(-8, -1.45) * mm});
            skLineSegment(sketch, "E2613", {"start": v(-8, -1.45) * mm, "end": v(-8, -1.6) * mm});
            skLineSegment(sketch, "E2614", {"start": v(-8, -1.6) * mm, "end": v(-8, -1.74) * mm});
            skLineSegment(sketch, "E2615", {"start": v(-8, -1.74) * mm, "end": v(-8, -1.88) * mm});
            skLineSegment(sketch, "E2616", {"start": v(-8, -1.88) * mm, "end": v(-8, -2) * mm});
            skLineSegment(sketch, "E2617", {"start": v(-8, -2) * mm, "end": v(-8, -2.13) * mm});
            skLineSegment(sketch, "E2618", {"start": v(-8, -2.13) * mm, "end": v(-8, -2.25) * mm});
            skLineSegment(sketch, "E2619", {"start": v(-8, -2.25) * mm, "end": v(-8, -2.36) * mm});
            skLineSegment(sketch, "E2620", {"start": v(-8, -2.36) * mm, "end": v(-8, -2.46) * mm});
            skLineSegment(sketch, "E2621", {"start": v(-8, -2.46) * mm, "end": v(-8, -2.55) * mm});
            skLineSegment(sketch, "E2622", {"start": v(-8, -2.55) * mm, "end": v(-8, -2.64) * mm});
            skLineSegment(sketch, "E2623", {"start": v(-8, -2.64) * mm, "end": v(-8, -2.71) * mm});
            skLineSegment(sketch, "E2624", {"start": v(-8, -2.71) * mm, "end": v(-8, -2.78) * mm});
            skLineSegment(sketch, "E2625", {"start": v(-8, -2.78) * mm, "end": v(-8, -2.83) * mm});
            skLineSegment(sketch, "E2626", {"start": v(-8, -2.83) * mm, "end": v(-8, -2.87) * mm});
            skLineSegment(sketch, "E2627", {"start": v(-8, -2.87) * mm, "end": v(-8, -2.9) * mm});
            skLineSegment(sketch, "E2628", {"start": v(-8, -2.9) * mm, "end": v(-8, -2.93) * mm});
            skLineSegment(sketch, "E2629", {"start": v(-8, -2.93) * mm, "end": v(-8, -2.93) * mm});
            skLineSegment(sketch, "E2630", {"start": v(-8, -2.93) * mm, "end": v(-8, -2.94) * mm});
            skLineSegment(sketch, "E2631", {"start": v(-8, -2.94) * mm, "end": v(-8, -2.95) * mm});
            skLineSegment(sketch, "E2632", {"start": v(-8, -2.95) * mm, "end": v(-8, -2.96) * mm});
            skLineSegment(sketch, "E2633", {"start": v(-8, -2.96) * mm, "end": v(-8, -2.97) * mm});
            skLineSegment(sketch, "E2634", {"start": v(-8, -2.97) * mm, "end": v(-8, -2.98) * mm});
            skLineSegment(sketch, "E2635", {"start": v(-8, -2.98) * mm, "end": v(-7.99, -2.99) * mm});
            skLineSegment(sketch, "E2636", {"start": v(-7.99, -2.99) * mm, "end": v(-7.99, -3) * mm});
            skLineSegment(sketch, "E2637", {"start": v(-7.99, -3) * mm, "end": v(-7.99, -3) * mm});
            skLineSegment(sketch, "E2638", {"start": v(-7.99, -3) * mm, "end": v(-7.98, -3.01) * mm});
            skLineSegment(sketch, "E2639", {"start": v(-7.98, -3.01) * mm, "end": v(-7.98, -3.02) * mm});
            skLineSegment(sketch, "E2640", {"start": v(-7.98, -3.02) * mm, "end": v(-7.98, -3.03) * mm});
            skLineSegment(sketch, "E2641", {"start": v(-7.98, -3.03) * mm, "end": v(-7.98, -3.03) * mm});
            skLineSegment(sketch, "E2642", {"start": v(-7.98, -3.03) * mm, "end": v(-7.98, -3.04) * mm});
            skLineSegment(sketch, "E2643", {"start": v(-7.98, -3.04) * mm, "end": v(-7.97, -3.05) * mm});
            skLineSegment(sketch, "E2644", {"start": v(-7.97, -3.05) * mm, "end": v(-7.97, -3.06) * mm});
            skLineSegment(sketch, "E2645", {"start": v(-7.97, -3.06) * mm, "end": v(-7.97, -3.06) * mm});
            skLineSegment(sketch, "E2646", {"start": v(-7.97, -3.06) * mm, "end": v(-7.96, -3.07) * mm});
            skLineSegment(sketch, "E2647", {"start": v(-7.96, -3.07) * mm, "end": v(-7.96, -3.07) * mm});
            skLineSegment(sketch, "E2648", {"start": v(-7.96, -3.07) * mm, "end": v(-7.96, -3.08) * mm});
            skLineSegment(sketch, "E2649", {"start": v(-7.96, -3.08) * mm, "end": v(-7.95, -3.09) * mm});
            skLineSegment(sketch, "E2650", {"start": v(-7.95, -3.09) * mm, "end": v(-7.95, -3.1) * mm});
            skLineSegment(sketch, "E2651", {"start": v(-7.95, -3.1) * mm, "end": v(-7.94, -3.1) * mm});
            skLineSegment(sketch, "E2652", {"start": v(-7.94, -3.1) * mm, "end": v(-7.94, -3.1) * mm});
            skLineSegment(sketch, "E2653", {"start": v(-7.94, -3.1) * mm, "end": v(-7.93, -3.11) * mm});
            skLineSegment(sketch, "E2654", {"start": v(-7.93, -3.11) * mm, "end": v(-7.93, -3.12) * mm});
            skLineSegment(sketch, "E2655", {"start": v(-7.93, -3.12) * mm, "end": v(-7.92, -3.12) * mm});
            skLineSegment(sketch, "E2656", {"start": v(-7.92, -3.12) * mm, "end": v(-7.92, -3.12) * mm});
            skLineSegment(sketch, "E2657", {"start": v(-7.92, -3.12) * mm, "end": v(-7.91, -3.13) * mm});
            skLineSegment(sketch, "E2658", {"start": v(-7.91, -3.13) * mm, "end": v(-7.9, -3.13) * mm});
            skLineSegment(sketch, "E2659", {"start": v(-7.9, -3.13) * mm, "end": v(-7.9, -3.14) * mm});
            skLineSegment(sketch, "E2660", {"start": v(-7.9, -3.14) * mm, "end": v(-7.9, -3.14) * mm});
            skLineSegment(sketch, "E2661", {"start": v(-7.9, -3.14) * mm, "end": v(-7.88, -3.14) * mm});
            skLineSegment(sketch, "E2662", {"start": v(-7.88, -3.14) * mm, "end": v(-7.88, -3.15) * mm});
            skLineSegment(sketch, "E2663", {"start": v(-7.88, -3.15) * mm, "end": v(-7.87, -3.15) * mm});
            skLineSegment(sketch, "E2664", {"start": v(-7.87, -3.15) * mm, "end": v(-7.87, -3.15) * mm});
            skLineSegment(sketch, "E2665", {"start": v(-7.87, -3.15) * mm, "end": v(-7.86, -3.15) * mm});
            skLineSegment(sketch, "E2666", {"start": v(-7.86, -3.15) * mm, "end": v(-7.85, -3.16) * mm});
            skLineSegment(sketch, "E2667", {"start": v(-7.85, -3.16) * mm, "end": v(-7.85, -3.16) * mm});
            skLineSegment(sketch, "E2668", {"start": v(-7.85, -3.16) * mm, "end": v(-7.84, -3.16) * mm});
            skLineSegment(sketch, "E2669", {"start": v(-7.84, -3.16) * mm, "end": v(-7.84, -3.16) * mm});
            skLineSegment(sketch, "E2670", {"start": v(-7.84, -3.16) * mm, "end": v(-7.83, -3.16) * mm});
            skLineSegment(sketch, "E2671", {"start": v(-7.83, -3.16) * mm, "end": v(-7.82, -3.16) * mm});
            skLineSegment(sketch, "E2672", {"start": v(-7.82, -3.16) * mm, "end": v(-7.82, -3.17) * mm});
            skLineSegment(sketch, "E2673", {"start": v(-7.82, -3.17) * mm, "end": v(-7.8, -3.17) * mm});
            skLineSegment(sketch, "E2674", {"start": v(-7.8, -3.17) * mm, "end": v(-7.8, -3.17) * mm});
            skLineSegment(sketch, "E2675", {"start": v(-7.8, -3.17) * mm, "end": v(-7.79, -3.17) * mm});
            skLineSegment(sketch, "E2676", {"start": v(-7.79, -3.17) * mm, "end": v(-7.78, -3.17) * mm});
            skLineSegment(sketch, "E2677", {"start": v(-7.78, -3.17) * mm, "end": v(-7.77, -3.17) * mm});
            skLineSegment(sketch, "E2678", {"start": v(-7.77, -3.17) * mm, "end": v(-7.76, -3.17) * mm});
            skLineSegment(sketch, "E2679", {"start": v(-7.76, -3.17) * mm, "end": v(-7.76, -3.17) * mm});
            skLineSegment(sketch, "E2680", {"start": v(-7.76, -3.17) * mm, "end": v(-7.75, -3.17) * mm});
            skLineSegment(sketch, "E2681", {"start": v(-7.75, -3.17) * mm, "end": v(-7.74, -3.16) * mm});
            skLineSegment(sketch, "E2682", {"start": v(-7.74, -3.16) * mm, "end": v(-7.73, -3.16) * mm});
            skLineSegment(sketch, "E2683", {"start": v(-7.73, -3.16) * mm, "end": v(-7.72, -3.16) * mm});
            skLineSegment(sketch, "E2684", {"start": v(-7.72, -3.16) * mm, "end": v(-7.72, -3.16) * mm});
            skLineSegment(sketch, "E2685", {"start": v(-7.72, -3.16) * mm, "end": v(-7.7, -3.16) * mm});
            skLineSegment(sketch, "E2686", {"start": v(-7.7, -3.16) * mm, "end": v(-7.7, -3.16) * mm});
            skLineSegment(sketch, "E2687", {"start": v(-7.7, -3.16) * mm, "end": v(-7.7, -3.15) * mm});
            skLineSegment(sketch, "E2688", {"start": v(-7.7, -3.15) * mm, "end": v(-7.69, -3.15) * mm});
            skLineSegment(sketch, "E2689", {"start": v(-7.69, -3.15) * mm, "end": v(-7.68, -3.15) * mm});
            skLineSegment(sketch, "E2690", {"start": v(-7.68, -3.15) * mm, "end": v(-7.67, -3.15) * mm});
            skLineSegment(sketch, "E2691", {"start": v(-7.67, -3.15) * mm, "end": v(-7.67, -3.14) * mm});
            skLineSegment(sketch, "E2692", {"start": v(-7.67, -3.14) * mm, "end": v(-7.66, -3.14) * mm});
            skLineSegment(sketch, "E2693", {"start": v(-7.66, -3.14) * mm, "end": v(-7.66, -3.14) * mm});
            skLineSegment(sketch, "E2694", {"start": v(-7.66, -3.14) * mm, "end": v(-7.65, -3.13) * mm});
            skLineSegment(sketch, "E2695", {"start": v(-7.65, -3.13) * mm, "end": v(-7.64, -3.13) * mm});
            skLineSegment(sketch, "E2696", {"start": v(-7.64, -3.13) * mm, "end": v(-7.64, -3.12) * mm});
            skLineSegment(sketch, "E2697", {"start": v(-7.64, -3.12) * mm, "end": v(-7.63, -3.12) * mm});
            skLineSegment(sketch, "E2698", {"start": v(-7.63, -3.12) * mm, "end": v(-7.63, -3.11) * mm});
            skLineSegment(sketch, "E2699", {"start": v(-7.63, -3.11) * mm, "end": v(-7.62, -3.1) * mm});
            skLineSegment(sketch, "E2700", {"start": v(-7.62, -3.1) * mm, "end": v(-7.62, -3.1) * mm});
            skLineSegment(sketch, "E2701", {"start": v(-7.62, -3.1) * mm, "end": v(-7.61, -3.1) * mm});
            skLineSegment(sketch, "E2702", {"start": v(-7.61, -3.1) * mm, "end": v(-7.6, -3.1) * mm});
            skLineSegment(sketch, "E2703", {"start": v(-7.6, -3.1) * mm, "end": v(-7.6, -3.09) * mm});
            skLineSegment(sketch, "E2704", {"start": v(-7.6, -3.09) * mm, "end": v(-7.6, -3.08) * mm});
            skLineSegment(sketch, "E2705", {"start": v(-7.6, -3.08) * mm, "end": v(-7.6, -3.08) * mm});
            skLineSegment(sketch, "E2706", {"start": v(-7.6, -3.08) * mm, "end": v(-7.59, -3.07) * mm});
            skLineSegment(sketch, "E2707", {"start": v(-7.59, -3.07) * mm, "end": v(-7.58, -3.06) * mm});
            skLineSegment(sketch, "E2708", {"start": v(-7.58, -3.06) * mm, "end": v(-7.58, -3.06) * mm});
            skLineSegment(sketch, "E2709", {"start": v(-7.58, -3.06) * mm, "end": v(-7.58, -3.05) * mm});
            skLineSegment(sketch, "E2710", {"start": v(-7.58, -3.05) * mm, "end": v(-7.57, -3.04) * mm});
            skLineSegment(sketch, "E2711", {"start": v(-7.57, -3.04) * mm, "end": v(-7.57, -3.04) * mm});
            skLineSegment(sketch, "E2712", {"start": v(-7.57, -3.04) * mm, "end": v(-7.57, -3.03) * mm});
            skLineSegment(sketch, "E2713", {"start": v(-7.57, -3.03) * mm, "end": v(-7.56, -3.02) * mm});
            skLineSegment(sketch, "E2714", {"start": v(-7.56, -3.02) * mm, "end": v(-7.56, -3.01) * mm});
            skLineSegment(sketch, "E2715", {"start": v(-7.56, -3.01) * mm, "end": v(-7.56, -3) * mm});
            skLineSegment(sketch, "E2716", {"start": v(-7.56, -3) * mm, "end": v(-7.56, -3) * mm});
            skLineSegment(sketch, "E2717", {"start": v(-7.56, -3) * mm, "end": v(-7.55, -3) * mm});
            skLineSegment(sketch, "E2718", {"start": v(-7.55, -3) * mm, "end": v(-7.55, -2.98) * mm});
            skLineSegment(sketch, "E2719", {"start": v(-7.55, -2.98) * mm, "end": v(-7.55, -2.97) * mm});
            skLineSegment(sketch, "E2720", {"start": v(-7.55, -2.97) * mm, "end": v(-7.55, -2.96) * mm});
            skLineSegment(sketch, "E2721", {"start": v(-7.55, -2.96) * mm, "end": v(-7.55, -2.96) * mm});
            skLineSegment(sketch, "E2722", {"start": v(-7.55, -2.96) * mm, "end": v(-7.55, -2.95) * mm});
            skLineSegment(sketch, "E2723", {"start": v(-7.55, -2.95) * mm, "end": v(-7.55, -2.94) * mm});
            skLineSegment(sketch, "E2724", {"start": v(-7.55, -2.94) * mm, "end": v(-7.55, -2.93) * mm});
            skLineSegment(sketch, "E2725", {"start": v(-7.55, -2.93) * mm, "end": v(-7.55, -2.92) * mm});
            skLineSegment(sketch, "E2726", {"start": v(-7.55, -2.92) * mm, "end": v(-7.55, -2.9) * mm});
            skLineSegment(sketch, "E2727", {"start": v(-7.55, -2.9) * mm, "end": v(-7.55, -2.9) * mm});
            skLineSegment(sketch, "E2728", {"start": v(-7.55, -2.9) * mm, "end": v(-7.55, -2.88) * mm});
            skLineSegment(sketch, "E2729", {"start": v(-7.55, -2.88) * mm, "end": v(-7.55, -2.85) * mm});
            skLineSegment(sketch, "E2730", {"start": v(-7.55, -2.85) * mm, "end": v(-7.55, -2.8) * mm});
            skLineSegment(sketch, "E2731", {"start": v(-7.55, -2.8) * mm, "end": v(-7.55, -2.75) * mm});
            skLineSegment(sketch, "E2732", {"start": v(-7.55, -2.75) * mm, "end": v(-7.55, -2.7) * mm});
            skLineSegment(sketch, "E2733", {"start": v(-7.55, -2.7) * mm, "end": v(-7.55, -2.62) * mm});
            skLineSegment(sketch, "E2734", {"start": v(-7.55, -2.62) * mm, "end": v(-7.55, -2.53) * mm});
            skLineSegment(sketch, "E2735", {"start": v(-7.55, -2.53) * mm, "end": v(-7.55, -2.44) * mm});
            skLineSegment(sketch, "E2736", {"start": v(-7.55, -2.44) * mm, "end": v(-7.55, -2.34) * mm});
            skLineSegment(sketch, "E2737", {"start": v(-7.55, -2.34) * mm, "end": v(-7.55, -2.23) * mm});
            skLineSegment(sketch, "E2738", {"start": v(-7.55, -2.23) * mm, "end": v(-7.55, -2.11) * mm});
            skLineSegment(sketch, "E2739", {"start": v(-7.55, -2.11) * mm, "end": v(-7.55, -1.99) * mm});
            skLineSegment(sketch, "E2740", {"start": v(-7.55, -1.99) * mm, "end": v(-7.55, -1.86) * mm});
            skLineSegment(sketch, "E2741", {"start": v(-7.55, -1.86) * mm, "end": v(-7.55, -1.72) * mm});
            skLineSegment(sketch, "E2742", {"start": v(-7.55, -1.72) * mm, "end": v(-7.55, -1.58) * mm});
            skLineSegment(sketch, "E2743", {"start": v(-7.55, -1.58) * mm, "end": v(-7.55, -1.44) * mm});
            skLineSegment(sketch, "E2744", {"start": v(-7.55, -1.44) * mm, "end": v(-7.55, -1.29) * mm});
            skLineSegment(sketch, "E2745", {"start": v(-7.55, -1.29) * mm, "end": v(-7.55, -1.13) * mm});
            skLineSegment(sketch, "E2746", {"start": v(-7.55, -1.13) * mm, "end": v(-7.55, -0.98) * mm});
            skLineSegment(sketch, "E2747", {"start": v(-7.55, -0.98) * mm, "end": v(-7.55, -0.82) * mm});
            skLineSegment(sketch, "E2748", {"start": v(-7.55, -0.82) * mm, "end": v(-7.55, -0.66) * mm});
            skLineSegment(sketch, "E2749", {"start": v(-7.55, -0.66) * mm, "end": v(-7.55, -0.5) * mm});
            skLineSegment(sketch, "E2750", {"start": v(-7.55, -0.5) * mm, "end": v(-7.55, -0.33) * mm});
            skLineSegment(sketch, "E2751", {"start": v(-7.55, -0.33) * mm, "end": v(-7.55, -0.16) * mm});
            skLineSegment(sketch, "E2752", {"start": v(-7.55, -0.16) * mm, "end": v(-7.55, 0) * mm});
            skLineSegment(sketch, "E2753", {"start": v(-7.55, 0) * mm, "end": v(-7.55, 0.17) * mm});
            skLineSegment(sketch, "E2754", {"start": v(-7.55, 0.17) * mm, "end": v(-7.55, 0.33) * mm});
            skLineSegment(sketch, "E2755", {"start": v(-7.55, 0.33) * mm, "end": v(-7.55, 0.49) * mm});
            skLineSegment(sketch, "E2756", {"start": v(-7.55, 0.49) * mm, "end": v(-7.55, 0.65) * mm});
            skLineSegment(sketch, "E2757", {"start": v(-7.55, 0.65) * mm, "end": v(-7.55, 0.8) * mm});
            skLineSegment(sketch, "E2758", {"start": v(-7.55, 0.8) * mm, "end": v(-7.55, 0.96) * mm});
            skLineSegment(sketch, "E2759", {"start": v(-7.55, 0.96) * mm, "end": v(-7.55, 1.1) * mm});
            skLineSegment(sketch, "E2760", {"start": v(-7.55, 1.1) * mm, "end": v(-7.55, 1.25) * mm});
            skLineSegment(sketch, "E2761", {"start": v(-7.55, 1.25) * mm, "end": v(-7.55, 1.4) * mm});
            skLineSegment(sketch, "E2762", {"start": v(-7.55, 1.4) * mm, "end": v(-7.55, 1.53) * mm});
            skLineSegment(sketch, "E2763", {"start": v(-7.55, 1.53) * mm, "end": v(-7.55, 1.66) * mm});
            skLineSegment(sketch, "E2764", {"start": v(-7.55, 1.66) * mm, "end": v(-7.55, 1.78) * mm});
            skLineSegment(sketch, "E2765", {"start": v(-7.55, 1.78) * mm, "end": v(-7.55, 1.9) * mm});
            skLineSegment(sketch, "E2766", {"start": v(-7.55, 1.9) * mm, "end": v(-7.55, 2.01) * mm});
            skLineSegment(sketch, "E2767", {"start": v(-7.55, 2.01) * mm, "end": v(-7.55, 2.11) * mm});
            skLineSegment(sketch, "E2768", {"start": v(-7.55, 2.11) * mm, "end": v(-7.55, 2.2) * mm});
            skLineSegment(sketch, "E2769", {"start": v(-7.55, 2.2) * mm, "end": v(-7.55, 2.29) * mm});
            skLineSegment(sketch, "E2770", {"start": v(-7.55, 2.29) * mm, "end": v(-7.55, 2.36) * mm});
            skLineSegment(sketch, "E2771", {"start": v(-7.55, 2.36) * mm, "end": v(-7.55, 2.43) * mm});
            skLineSegment(sketch, "E2772", {"start": v(-7.55, 2.43) * mm, "end": v(-7.55, 2.48) * mm});
            skLineSegment(sketch, "E2773", {"start": v(-7.55, 2.48) * mm, "end": v(-7.55, 2.52) * mm});
            skLineSegment(sketch, "E2774", {"start": v(-7.55, 2.52) * mm, "end": v(-7.55, 2.56) * mm});
            skLineSegment(sketch, "E2775", {"start": v(-7.55, 2.56) * mm, "end": v(-7.55, 2.57) * mm});
            skLineSegment(sketch, "E2776", {"start": v(-7.55, 2.57) * mm, "end": v(-7.55, 2.58) * mm});
            skLineSegment(sketch, "E2777", {"start": v(-7.55, 2.58) * mm, "end": v(-7.55, 2.59) * mm});
            skLineSegment(sketch, "E2778", {"start": v(-7.55, 2.59) * mm, "end": v(-7.55, 2.6) * mm});
            skLineSegment(sketch, "E2779", {"start": v(-7.55, 2.6) * mm, "end": v(-7.54, 2.6) * mm});
            skLineSegment(sketch, "E2780", {"start": v(-7.54, 2.6) * mm, "end": v(-7.54, 2.6) * mm});
            skLineSegment(sketch, "E2781", {"start": v(-7.54, 2.6) * mm, "end": v(-7.54, 2.61) * mm});
            skLineSegment(sketch, "E2782", {"start": v(-7.54, 2.61) * mm, "end": v(-7.54, 2.62) * mm});
            skLineSegment(sketch, "E2783", {"start": v(-7.54, 2.62) * mm, "end": v(-7.54, 2.63) * mm});
            skLineSegment(sketch, "E2784", {"start": v(-7.54, 2.63) * mm, "end": v(-7.54, 2.63) * mm});
            skLineSegment(sketch, "E2785", {"start": v(-7.54, 2.63) * mm, "end": v(-7.54, 2.64) * mm});
            skLineSegment(sketch, "E2786", {"start": v(-7.54, 2.64) * mm, "end": v(-7.54, 2.64) * mm});
            skLineSegment(sketch, "E2787", {"start": v(-7.54, 2.64) * mm, "end": v(-7.54, 2.65) * mm});
            skLineSegment(sketch, "E2788", {"start": v(-7.54, 2.65) * mm, "end": v(-7.53, 2.65) * mm});
            skLineSegment(sketch, "E2789", {"start": v(-7.53, 2.65) * mm, "end": v(-7.53, 2.66) * mm});
            skLineSegment(sketch, "E2790", {"start": v(-7.53, 2.66) * mm, "end": v(-7.53, 2.66) * mm});
            skLineSegment(sketch, "E2791", {"start": v(-7.53, 2.66) * mm, "end": v(-7.53, 2.67) * mm});
            skLineSegment(sketch, "E2792", {"start": v(-7.53, 2.67) * mm, "end": v(-7.53, 2.67) * mm});
            skLineSegment(sketch, "E2793", {"start": v(-7.53, 2.67) * mm, "end": v(-7.52, 2.68) * mm});
            skLineSegment(sketch, "E2794", {"start": v(-7.52, 2.68) * mm, "end": v(-7.52, 2.68) * mm});
            skLineSegment(sketch, "E2795", {"start": v(-7.52, 2.68) * mm, "end": v(-7.52, 2.69) * mm});
            skLineSegment(sketch, "E2796", {"start": v(-7.52, 2.69) * mm, "end": v(-7.51, 2.7) * mm});
            skLineSegment(sketch, "E2797", {"start": v(-7.51, 2.7) * mm, "end": v(-7.51, 2.7) * mm});
            skLineSegment(sketch, "E2798", {"start": v(-7.51, 2.7) * mm, "end": v(-7.5, 2.7) * mm});
            skLineSegment(sketch, "E2799", {"start": v(-7.5, 2.7) * mm, "end": v(-7.5, 2.7) * mm});
            skLineSegment(sketch, "E2800", {"start": v(-7.5, 2.7) * mm, "end": v(-7.5, 2.71) * mm});
            skLineSegment(sketch, "E2801", {"start": v(-7.5, 2.71) * mm, "end": v(-7.5, 2.71) * mm});
            skLineSegment(sketch, "E2802", {"start": v(-7.5, 2.71) * mm, "end": v(-7.49, 2.72) * mm});
            skLineSegment(sketch, "E2803", {"start": v(-7.49, 2.72) * mm, "end": v(-7.48, 2.72) * mm});
            skLineSegment(sketch, "E2804", {"start": v(-7.48, 2.72) * mm, "end": v(-7.48, 2.72) * mm});
            skLineSegment(sketch, "E2805", {"start": v(-7.48, 2.72) * mm, "end": v(-7.47, 2.73) * mm});
            skLineSegment(sketch, "E2806", {"start": v(-7.47, 2.73) * mm, "end": v(-7.47, 2.73) * mm});
            skLineSegment(sketch, "E2807", {"start": v(-7.47, 2.73) * mm, "end": v(-7.46, 2.73) * mm});
            skLineSegment(sketch, "E2808", {"start": v(-7.46, 2.73) * mm, "end": v(-7.46, 2.73) * mm});
            skLineSegment(sketch, "E2809", {"start": v(-7.46, 2.73) * mm, "end": v(-7.45, 2.73) * mm});
            skLineSegment(sketch, "E2810", {"start": v(-7.45, 2.73) * mm, "end": v(-7.45, 2.74) * mm});
            skLineSegment(sketch, "E2811", {"start": v(-7.45, 2.74) * mm, "end": v(-7.44, 2.74) * mm});
            skLineSegment(sketch, "E2812", {"start": v(-7.44, 2.74) * mm, "end": v(-7.44, 2.74) * mm});
            skLineSegment(sketch, "E2813", {"start": v(-7.44, 2.74) * mm, "end": v(-7.43, 2.74) * mm});
            skLineSegment(sketch, "E2814", {"start": v(-7.43, 2.74) * mm, "end": v(-7.43, 2.74) * mm});
            skLineSegment(sketch, "E2815", {"start": v(-7.43, 2.74) * mm, "end": v(-7.42, 2.74) * mm});
            skLineSegment(sketch, "E2816", {"start": v(-7.42, 2.74) * mm, "end": v(-7.42, 2.74) * mm});
            skLineSegment(sketch, "E2817", {"start": v(-7.42, 2.74) * mm, "end": v(-7.41, 2.74) * mm});
            skLineSegment(sketch, "E2818", {"start": v(-7.41, 2.74) * mm, "end": v(-7.4, 2.74) * mm});
            skLineSegment(sketch, "E2819", {"start": v(-7.4, 2.74) * mm, "end": v(-7.4, 2.75) * mm});
            skLineSegment(sketch, "E2820", {"start": v(-7.4, 2.75) * mm, "end": v(-7.4, 2.75) * mm});
            skLineSegment(sketch, "E2821", {"start": v(-7.4, 2.75) * mm, "end": v(-7.39, 2.75) * mm});
            skLineSegment(sketch, "E2822", {"start": v(-7.39, 2.75) * mm, "end": v(-7.38, 2.75) * mm});
            skLineSegment(sketch, "E2823", {"start": v(-7.38, 2.75) * mm, "end": v(-7.37, 2.75) * mm});
            skLineSegment(sketch, "E2824", {"start": v(-7.37, 2.75) * mm, "end": v(-7.37, 2.75) * mm});
            skLineSegment(sketch, "E2825", {"start": v(-7.37, 2.75) * mm, "end": v(-7.36, 2.75) * mm});
            skLineSegment(sketch, "E2826", {"start": v(-7.36, 2.75) * mm, "end": v(-7.36, 2.75) * mm});
            skLineSegment(sketch, "E2827", {"start": v(-7.36, 2.75) * mm, "end": v(-7.35, 2.74) * mm});
            skLineSegment(sketch, "E2828", {"start": v(-7.35, 2.74) * mm, "end": v(-7.35, 2.74) * mm});
            skLineSegment(sketch, "E2829", {"start": v(-7.35, 2.74) * mm, "end": v(-7.34, 2.74) * mm});
            skLineSegment(sketch, "E2830", {"start": v(-7.34, 2.74) * mm, "end": v(-7.34, 2.74) * mm});
            skLineSegment(sketch, "E2831", {"start": v(-7.34, 2.74) * mm, "end": v(-7.33, 2.74) * mm});
            skLineSegment(sketch, "E2832", {"start": v(-7.33, 2.74) * mm, "end": v(-7.33, 2.74) * mm});
            skLineSegment(sketch, "E2833", {"start": v(-7.33, 2.74) * mm, "end": v(-7.32, 2.74) * mm});
            skLineSegment(sketch, "E2834", {"start": v(-7.32, 2.74) * mm, "end": v(-7.32, 2.74) * mm});
            skLineSegment(sketch, "E2835", {"start": v(-7.32, 2.74) * mm, "end": v(-7.31, 2.74) * mm});
            skLineSegment(sketch, "E2836", {"start": v(-7.31, 2.74) * mm, "end": v(-7.3, 2.73) * mm});
            skLineSegment(sketch, "E2837", {"start": v(-7.3, 2.73) * mm, "end": v(-7.3, 2.73) * mm});
            skLineSegment(sketch, "E2838", {"start": v(-7.3, 2.73) * mm, "end": v(-7.3, 2.72) * mm});
            skLineSegment(sketch, "E2839", {"start": v(-7.3, 2.72) * mm, "end": v(-7.29, 2.72) * mm});
            skLineSegment(sketch, "E2840", {"start": v(-7.29, 2.72) * mm, "end": v(-7.28, 2.72) * mm});
            skLineSegment(sketch, "E2841", {"start": v(-7.28, 2.72) * mm, "end": v(-7.28, 2.72) * mm});
            skLineSegment(sketch, "E2842", {"start": v(-7.28, 2.72) * mm, "end": v(-7.28, 2.71) * mm});
            skLineSegment(sketch, "E2843", {"start": v(-7.28, 2.71) * mm, "end": v(-7.27, 2.71) * mm});
            skLineSegment(sketch, "E2844", {"start": v(-7.27, 2.71) * mm, "end": v(-7.27, 2.7) * mm});
            skLineSegment(sketch, "E2845", {"start": v(-7.27, 2.7) * mm, "end": v(-7.27, 2.7) * mm});
            skLineSegment(sketch, "E2846", {"start": v(-7.27, 2.7) * mm, "end": v(-7.26, 2.7) * mm});
            skLineSegment(sketch, "E2847", {"start": v(-7.26, 2.7) * mm, "end": v(-7.26, 2.7) * mm});
            skLineSegment(sketch, "E2848", {"start": v(-7.26, 2.7) * mm, "end": v(-7.26, 2.69) * mm});
            skLineSegment(sketch, "E2849", {"start": v(-7.26, 2.69) * mm, "end": v(-7.26, 2.68) * mm});
            skLineSegment(sketch, "E2850", {"start": v(-7.26, 2.68) * mm, "end": v(-7.25, 2.68) * mm});
            skLineSegment(sketch, "E2851", {"start": v(-7.25, 2.68) * mm, "end": v(-7.25, 2.68) * mm});
            skLineSegment(sketch, "E2852", {"start": v(-7.25, 2.68) * mm, "end": v(-7.25, 2.67) * mm});
            skLineSegment(sketch, "E2853", {"start": v(-7.25, 2.67) * mm, "end": v(-7.25, 2.67) * mm});
            skLineSegment(sketch, "E2854", {"start": v(-7.25, 2.67) * mm, "end": v(-7.25, 2.66) * mm});
            skLineSegment(sketch, "E2855", {"start": v(-7.25, 2.66) * mm, "end": v(-7.25, 2.66) * mm});
            skLineSegment(sketch, "E2856", {"start": v(-7.25, 2.66) * mm, "end": v(-7.24, 2.66) * mm});
            skLineSegment(sketch, "E2857", {"start": v(-7.24, 2.66) * mm, "end": v(-7.24, 2.65) * mm});
            skLineSegment(sketch, "E2858", {"start": v(-7.24, 2.65) * mm, "end": v(-7.24, 2.65) * mm});
            skLineSegment(sketch, "E2859", {"start": v(-7.24, 2.65) * mm, "end": v(-7.24, 2.64) * mm});
            skLineSegment(sketch, "E2860", {"start": v(-7.24, 2.64) * mm, "end": v(-7.24, 2.64) * mm});
            skLineSegment(sketch, "E2861", {"start": v(-7.24, 2.64) * mm, "end": v(-7.24, 2.63) * mm});
            skLineSegment(sketch, "E2862", {"start": v(-7.24, 2.63) * mm, "end": v(-7.24, 2.63) * mm});
            skLineSegment(sketch, "E2863", {"start": v(-7.24, 2.63) * mm, "end": v(-7.24, 2.62) * mm});
            skLineSegment(sketch, "E2864", {"start": v(-7.24, 2.62) * mm, "end": v(-7.24, 2.62) * mm});
            skLineSegment(sketch, "E2865", {"start": v(-7.24, 2.62) * mm, "end": v(-7.24, 2.61) * mm});
            skLineSegment(sketch, "E2866", {"start": v(-7.24, 2.61) * mm, "end": v(-7.24, 2.6) * mm});
            skLineSegment(sketch, "E2867", {"start": v(-7.24, 2.6) * mm, "end": v(-7.24, 2.6) * mm});
            skLineSegment(sketch, "E2868", {"start": v(-7.24, 2.6) * mm, "end": v(-7.24, 2.58) * mm});
            skLineSegment(sketch, "E2869", {"start": v(-7.24, 2.58) * mm, "end": v(-7.24, 2.55) * mm});
            skLineSegment(sketch, "E2870", {"start": v(-7.24, 2.55) * mm, "end": v(-7.24, 2.51) * mm});
            skLineSegment(sketch, "E2871", {"start": v(-7.24, 2.51) * mm, "end": v(-7.24, 2.46) * mm});
            skLineSegment(sketch, "E2872", {"start": v(-7.24, 2.46) * mm, "end": v(-7.24, 2.4) * mm});
            skLineSegment(sketch, "E2873", {"start": v(-7.24, 2.4) * mm, "end": v(-7.24, 2.33) * mm});
            skLineSegment(sketch, "E2874", {"start": v(-7.24, 2.33) * mm, "end": v(-7.24, 2.25) * mm});
            skLineSegment(sketch, "E2875", {"start": v(-7.24, 2.25) * mm, "end": v(-7.24, 2.16) * mm});
            skLineSegment(sketch, "E2876", {"start": v(-7.24, 2.16) * mm, "end": v(-7.24, 2.06) * mm});
            skLineSegment(sketch, "E2877", {"start": v(-7.24, 2.06) * mm, "end": v(-7.24, 1.96) * mm});
            skLineSegment(sketch, "E2878", {"start": v(-7.24, 1.96) * mm, "end": v(-7.24, 1.85) * mm});
            skLineSegment(sketch, "E2879", {"start": v(-7.24, 1.85) * mm, "end": v(-7.24, 1.73) * mm});
            skLineSegment(sketch, "E2880", {"start": v(-7.24, 1.73) * mm, "end": v(-7.24, 1.6) * mm});
            skLineSegment(sketch, "E2881", {"start": v(-7.24, 1.6) * mm, "end": v(-7.24, 1.48) * mm});
            skLineSegment(sketch, "E2882", {"start": v(-7.24, 1.48) * mm, "end": v(-7.24, 1.35) * mm});
            skLineSegment(sketch, "E2883", {"start": v(-7.24, 1.35) * mm, "end": v(-7.24, 1.2) * mm});
            skLineSegment(sketch, "E2884", {"start": v(-7.24, 1.2) * mm, "end": v(-7.24, 1.07) * mm});
            skLineSegment(sketch, "E2885", {"start": v(-7.24, 1.07) * mm, "end": v(-7.24, 0.92) * mm});
            skLineSegment(sketch, "E2886", {"start": v(-7.24, 0.92) * mm, "end": v(-7.24, 0.77) * mm});
            skLineSegment(sketch, "E2887", {"start": v(-7.24, 0.77) * mm, "end": v(-7.24, 0.62) * mm});
            skLineSegment(sketch, "E2888", {"start": v(-7.24, 0.62) * mm, "end": v(-7.24, 0.47) * mm});
            skLineSegment(sketch, "E2889", {"start": v(-7.24, 0.47) * mm, "end": v(-7.24, 0.31) * mm});
            skLineSegment(sketch, "E2890", {"start": v(-7.24, 0.31) * mm, "end": v(-7.24, 0.16) * mm});
            skLineSegment(sketch, "E2891", {"start": v(-7.24, 0.16) * mm, "end": v(-7.24, 0) * mm});
            skLineSegment(sketch, "E2892", {"start": v(-7.24, 0) * mm, "end": v(-7.24, -0.15) * mm});
            skLineSegment(sketch, "E2893", {"start": v(-7.24, -0.15) * mm, "end": v(-7.24, -0.31) * mm});
            skLineSegment(sketch, "E2894", {"start": v(-7.24, -0.31) * mm, "end": v(-7.24, -0.46) * mm});
            skLineSegment(sketch, "E2895", {"start": v(-7.24, -0.46) * mm, "end": v(-7.24, -0.62) * mm});
            skLineSegment(sketch, "E2896", {"start": v(-7.24, -0.62) * mm, "end": v(-7.24, -0.77) * mm});
            skLineSegment(sketch, "E2897", {"start": v(-7.24, -0.77) * mm, "end": v(-7.24, -0.92) * mm});
            skLineSegment(sketch, "E2898", {"start": v(-7.24, -0.92) * mm, "end": v(-7.24, -1.06) * mm});
            skLineSegment(sketch, "E2899", {"start": v(-7.24, -1.06) * mm, "end": v(-7.24, -1.2) * mm});
            skLineSegment(sketch, "E2900", {"start": v(-7.24, -1.2) * mm, "end": v(-7.24, -1.34) * mm});
            skLineSegment(sketch, "E2901", {"start": v(-7.24, -1.34) * mm, "end": v(-7.24, -1.48) * mm});
            skLineSegment(sketch, "E2902", {"start": v(-7.24, -1.48) * mm, "end": v(-7.24, -1.6) * mm});
            skLineSegment(sketch, "E2903", {"start": v(-7.24, -1.6) * mm, "end": v(-7.24, -1.73) * mm});
            skLineSegment(sketch, "E2904", {"start": v(-7.24, -1.73) * mm, "end": v(-7.24, -1.85) * mm});
            skLineSegment(sketch, "E2905", {"start": v(-7.24, -1.85) * mm, "end": v(-7.24, -1.96) * mm});
            skLineSegment(sketch, "E2906", {"start": v(-7.24, -1.96) * mm, "end": v(-7.24, -2.06) * mm});
            skLineSegment(sketch, "E2907", {"start": v(-7.24, -2.06) * mm, "end": v(-7.24, -2.16) * mm});
            skLineSegment(sketch, "E2908", {"start": v(-7.24, -2.16) * mm, "end": v(-7.24, -2.24) * mm});
            skLineSegment(sketch, "E2909", {"start": v(-7.24, -2.24) * mm, "end": v(-7.24, -2.32) * mm});
            skLineSegment(sketch, "E2910", {"start": v(-7.24, -2.32) * mm, "end": v(-7.24, -2.4) * mm});
            skLineSegment(sketch, "E2911", {"start": v(-7.24, -2.4) * mm, "end": v(-7.24, -2.46) * mm});
            skLineSegment(sketch, "E2912", {"start": v(-7.24, -2.46) * mm, "end": v(-7.24, -2.5) * mm});
            skLineSegment(sketch, "E2913", {"start": v(-7.24, -2.5) * mm, "end": v(-7.24, -2.55) * mm});
            skLineSegment(sketch, "E2914", {"start": v(-7.24, -2.55) * mm, "end": v(-7.24, -2.58) * mm});
            skLineSegment(sketch, "E2915", {"start": v(-7.24, -2.58) * mm, "end": v(-7.24, -2.6) * mm});
            skLineSegment(sketch, "E2916", {"start": v(-7.24, -2.6) * mm, "end": v(-7.24, -2.6) * mm});
            skLineSegment(sketch, "E2917", {"start": v(-7.24, -2.6) * mm, "end": v(-7.24, -2.63) * mm});
            skLineSegment(sketch, "E2918", {"start": v(-7.24, -2.63) * mm, "end": v(-7.24, -2.65) * mm});
            skLineSegment(sketch, "E2919", {"start": v(-7.24, -2.65) * mm, "end": v(-7.24, -2.68) * mm});
            skLineSegment(sketch, "E2920", {"start": v(-7.24, -2.68) * mm, "end": v(-7.23, -2.7) * mm});
            skLineSegment(sketch, "E2921", {"start": v(-7.23, -2.7) * mm, "end": v(-7.23, -2.72) * mm});
            skLineSegment(sketch, "E2922", {"start": v(-7.23, -2.72) * mm, "end": v(-7.23, -2.75) * mm});
            skLineSegment(sketch, "E2923", {"start": v(-7.23, -2.75) * mm, "end": v(-7.22, -2.77) * mm});
            skLineSegment(sketch, "E2924", {"start": v(-7.22, -2.77) * mm, "end": v(-7.22, -2.79) * mm});
            skLineSegment(sketch, "E2925", {"start": v(-7.22, -2.79) * mm, "end": v(-7.21, -2.81) * mm});
            skLineSegment(sketch, "E2926", {"start": v(-7.21, -2.81) * mm, "end": v(-7.2, -2.83) * mm});
            skLineSegment(sketch, "E2927", {"start": v(-7.2, -2.83) * mm, "end": v(-7.2, -2.85) * mm});
            skLineSegment(sketch, "E2928", {"start": v(-7.2, -2.85) * mm, "end": v(-7.2, -2.87) * mm});
            skLineSegment(sketch, "E2929", {"start": v(-7.2, -2.87) * mm, "end": v(-7.19, -2.89) * mm});
            skLineSegment(sketch, "E2930", {"start": v(-7.19, -2.89) * mm, "end": v(-7.18, -2.9) * mm});
            skLineSegment(sketch, "E2931", {"start": v(-7.18, -2.9) * mm, "end": v(-7.17, -2.93) * mm});
            skLineSegment(sketch, "E2932", {"start": v(-7.17, -2.93) * mm, "end": v(-7.16, -2.94) * mm});
            skLineSegment(sketch, "E2933", {"start": v(-7.16, -2.94) * mm, "end": v(-7.15, -2.96) * mm});
            skLineSegment(sketch, "E2934", {"start": v(-7.15, -2.96) * mm, "end": v(-7.14, -2.98) * mm});
            skLineSegment(sketch, "E2935", {"start": v(-7.14, -2.98) * mm, "end": v(-7.13, -3) * mm});
            skLineSegment(sketch, "E2936", {"start": v(-7.13, -3) * mm, "end": v(-7.12, -3) * mm});
            skLineSegment(sketch, "E2937", {"start": v(-7.12, -3) * mm, "end": v(-7.1, -3.02) * mm});
            skLineSegment(sketch, "E2938", {"start": v(-7.1, -3.02) * mm, "end": v(-7.1, -3.04) * mm});
            skLineSegment(sketch, "E2939", {"start": v(-7.1, -3.04) * mm, "end": v(-7.08, -3.05) * mm});
            skLineSegment(sketch, "E2940", {"start": v(-7.08, -3.05) * mm, "end": v(-7.07, -3.07) * mm});
            skLineSegment(sketch, "E2941", {"start": v(-7.07, -3.07) * mm, "end": v(-7.06, -3.08) * mm});
            skLineSegment(sketch, "E2942", {"start": v(-7.06, -3.08) * mm, "end": v(-7.04, -3.1) * mm});
            skLineSegment(sketch, "E2943", {"start": v(-7.04, -3.1) * mm, "end": v(-7.03, -3.1) * mm});
            skLineSegment(sketch, "E2944", {"start": v(-7.03, -3.1) * mm, "end": v(-7.01, -3.11) * mm});
            skLineSegment(sketch, "E2945", {"start": v(-7.01, -3.11) * mm, "end": v(-7, -3.13) * mm});
            skLineSegment(sketch, "E2946", {"start": v(-7, -3.13) * mm, "end": v(-6.98, -3.14) * mm});
            skLineSegment(sketch, "E2947", {"start": v(-6.98, -3.14) * mm, "end": v(-6.97, -3.15) * mm});
            skLineSegment(sketch, "E2948", {"start": v(-6.97, -3.15) * mm, "end": v(-6.95, -3.16) * mm});
            skLineSegment(sketch, "E2949", {"start": v(-6.95, -3.16) * mm, "end": v(-6.94, -3.16) * mm});
            skLineSegment(sketch, "E2950", {"start": v(-6.94, -3.16) * mm, "end": v(-6.92, -3.17) * mm});
            skLineSegment(sketch, "E2951", {"start": v(-6.92, -3.17) * mm, "end": v(-6.9, -3.18) * mm});
            skLineSegment(sketch, "E2952", {"start": v(-6.9, -3.18) * mm, "end": v(-6.89, -3.19) * mm});
            skLineSegment(sketch, "E2953", {"start": v(-6.89, -3.19) * mm, "end": v(-6.87, -3.2) * mm});
            skLineSegment(sketch, "E2954", {"start": v(-6.87, -3.2) * mm, "end": v(-6.85, -3.2) * mm});
            skLineSegment(sketch, "E2955", {"start": v(-6.85, -3.2) * mm, "end": v(-6.83, -3.2) * mm});
            skLineSegment(sketch, "E2956", {"start": v(-6.83, -3.2) * mm, "end": v(-6.82, -3.21) * mm});
            skLineSegment(sketch, "E2957", {"start": v(-6.82, -3.21) * mm, "end": v(-6.8, -3.22) * mm});
            skLineSegment(sketch, "E2958", {"start": v(-6.8, -3.22) * mm, "end": v(-6.78, -3.22) * mm});
            skLineSegment(sketch, "E2959", {"start": v(-6.78, -3.22) * mm, "end": v(-6.76, -3.23) * mm});
            skLineSegment(sketch, "E2960", {"start": v(-6.76, -3.23) * mm, "end": v(-6.74, -3.23) * mm});
            skLineSegment(sketch, "E2961", {"start": v(-6.74, -3.23) * mm, "end": v(-6.72, -3.23) * mm});
            skLineSegment(sketch, "E2962", {"start": v(-6.72, -3.23) * mm, "end": v(-6.7, -3.23) * mm});
            skLineSegment(sketch, "E2963", {"start": v(-6.7, -3.23) * mm, "end": v(-6.69, -3.24) * mm});
            skLineSegment(sketch, "E2964", {"start": v(-6.69, -3.24) * mm, "end": v(-6.67, -3.24) * mm});
            skLineSegment(sketch, "E2965", {"start": v(-6.67, -3.24) * mm, "end": v(-6.65, -3.24) * mm});
            skLineSegment(sketch, "E2966", {"start": v(-6.65, -3.24) * mm, "end": v(-6.63, -3.24) * mm});
            skLineSegment(sketch, "E2967", {"start": v(-6.63, -3.24) * mm, "end": v(-6.6, -3.24) * mm});
            skLineSegment(sketch, "E2968", {"start": v(-6.6, -3.24) * mm, "end": v(-6.59, -3.24) * mm});
            skLineSegment(sketch, "E2969", {"start": v(-6.59, -3.24) * mm, "end": v(-6.57, -3.24) * mm});
            skLineSegment(sketch, "E2970", {"start": v(-6.57, -3.24) * mm, "end": v(-6.55, -3.23) * mm});
            skLineSegment(sketch, "E2971", {"start": v(-6.55, -3.23) * mm, "end": v(-6.53, -3.23) * mm});
            skLineSegment(sketch, "E2972", {"start": v(-6.53, -3.23) * mm, "end": v(-6.5, -3.23) * mm});
            skLineSegment(sketch, "E2973", {"start": v(-6.5, -3.23) * mm, "end": v(-6.5, -3.23) * mm});
            skLineSegment(sketch, "E2974", {"start": v(-6.5, -3.23) * mm, "end": v(-6.47, -3.22) * mm});
            skLineSegment(sketch, "E2975", {"start": v(-6.47, -3.22) * mm, "end": v(-6.45, -3.22) * mm});
            skLineSegment(sketch, "E2976", {"start": v(-6.45, -3.22) * mm, "end": v(-6.43, -3.21) * mm});
            skLineSegment(sketch, "E2977", {"start": v(-6.43, -3.21) * mm, "end": v(-6.42, -3.2) * mm});
            skLineSegment(sketch, "E2978", {"start": v(-6.42, -3.2) * mm, "end": v(-6.4, -3.2) * mm});
            skLineSegment(sketch, "E2979", {"start": v(-6.4, -3.2) * mm, "end": v(-6.38, -3.2) * mm});
            skLineSegment(sketch, "E2980", {"start": v(-6.38, -3.2) * mm, "end": v(-6.36, -3.19) * mm});
            skLineSegment(sketch, "E2981", {"start": v(-6.36, -3.19) * mm, "end": v(-6.34, -3.18) * mm});
            skLineSegment(sketch, "E2982", {"start": v(-6.34, -3.18) * mm, "end": v(-6.33, -3.17) * mm});
            skLineSegment(sketch, "E2983", {"start": v(-6.33, -3.17) * mm, "end": v(-6.3, -3.16) * mm});
            skLineSegment(sketch, "E2984", {"start": v(-6.3, -3.16) * mm, "end": v(-6.3, -3.16) * mm});
            skLineSegment(sketch, "E2985", {"start": v(-6.3, -3.16) * mm, "end": v(-6.28, -3.15) * mm});
            skLineSegment(sketch, "E2986", {"start": v(-6.28, -3.15) * mm, "end": v(-6.26, -3.14) * mm});
            skLineSegment(sketch, "E2987", {"start": v(-6.26, -3.14) * mm, "end": v(-6.24, -3.13) * mm});
            skLineSegment(sketch, "E2988", {"start": v(-6.24, -3.13) * mm, "end": v(-6.23, -3.11) * mm});
            skLineSegment(sketch, "E2989", {"start": v(-6.23, -3.11) * mm, "end": v(-6.21, -3.1) * mm});
            skLineSegment(sketch, "E2990", {"start": v(-6.21, -3.1) * mm, "end": v(-6.2, -3.1) * mm});
            skLineSegment(sketch, "E2991", {"start": v(-6.2, -3.1) * mm, "end": v(-6.18, -3.08) * mm});
            skLineSegment(sketch, "E2992", {"start": v(-6.18, -3.08) * mm, "end": v(-6.17, -3.07) * mm});
            skLineSegment(sketch, "E2993", {"start": v(-6.17, -3.07) * mm, "end": v(-6.16, -3.05) * mm});
            skLineSegment(sketch, "E2994", {"start": v(-6.16, -3.05) * mm, "end": v(-6.14, -3.04) * mm});
            skLineSegment(sketch, "E2995", {"start": v(-6.14, -3.04) * mm, "end": v(-6.13, -3.02) * mm});
            skLineSegment(sketch, "E2996", {"start": v(-6.13, -3.02) * mm, "end": v(-6.12, -3) * mm});
            skLineSegment(sketch, "E2997", {"start": v(-6.12, -3) * mm, "end": v(-6.1, -3) * mm});
            skLineSegment(sketch, "E2998", {"start": v(-6.1, -3) * mm, "end": v(-6.1, -2.98) * mm});
            skLineSegment(sketch, "E2999", {"start": v(-6.1, -2.98) * mm, "end": v(-6.09, -2.96) * mm});
            skLineSegment(sketch, "E3000", {"start": v(-6.09, -2.96) * mm, "end": v(-6.08, -2.94) * mm});
            skLineSegment(sketch, "E3001", {"start": v(-6.08, -2.94) * mm, "end": v(-6.07, -2.93) * mm});
            skLineSegment(sketch, "E3002", {"start": v(-6.07, -2.93) * mm, "end": v(-6.06, -2.9) * mm});
            skLineSegment(sketch, "E3003", {"start": v(-6.06, -2.9) * mm, "end": v(-6.05, -2.89) * mm});
            skLineSegment(sketch, "E3004", {"start": v(-6.05, -2.89) * mm, "end": v(-6.04, -2.87) * mm});
            skLineSegment(sketch, "E3005", {"start": v(-6.04, -2.87) * mm, "end": v(-6.03, -2.85) * mm});
            skLineSegment(sketch, "E3006", {"start": v(-6.03, -2.85) * mm, "end": v(-6.02, -2.83) * mm});
            skLineSegment(sketch, "E3007", {"start": v(-6.02, -2.83) * mm, "end": v(-6.02, -2.81) * mm});
            skLineSegment(sketch, "E3008", {"start": v(-6.02, -2.81) * mm, "end": v(-6.01, -2.79) * mm});
            skLineSegment(sketch, "E3009", {"start": v(-6.01, -2.79) * mm, "end": v(-6, -2.77) * mm});
            skLineSegment(sketch, "E3010", {"start": v(-6, -2.77) * mm, "end": v(-6, -2.75) * mm});
            skLineSegment(sketch, "E3011", {"start": v(-6, -2.75) * mm, "end": v(-6, -2.72) * mm});
            skLineSegment(sketch, "E3012", {"start": v(-6, -2.72) * mm, "end": v(-6, -2.7) * mm});
            skLineSegment(sketch, "E3013", {"start": v(-6, -2.7) * mm, "end": v(-6, -2.68) * mm});
            skLineSegment(sketch, "E3014", {"start": v(-6, -2.68) * mm, "end": v(-6, -2.65) * mm});
            skLineSegment(sketch, "E3015", {"start": v(-6, -2.65) * mm, "end": v(-6, -2.63) * mm});
            skLineSegment(sketch, "E3016", {"start": v(-6, -2.63) * mm, "end": v(-6, -2.6) * mm});
            skLineSegment(sketch, "E3017", {"start": v(-6, -2.6) * mm, "end": v(-6, -2.6) * mm});
            skLineSegment(sketch, "E3018", {"start": v(-6, -2.6) * mm, "end": v(-6, -2.58) * mm});
            skLineSegment(sketch, "E3019", {"start": v(-6, -2.58) * mm, "end": v(-6, -2.55) * mm});
            skLineSegment(sketch, "E3020", {"start": v(-6, -2.55) * mm, "end": v(-6, -2.5) * mm});
            skLineSegment(sketch, "E3021", {"start": v(-6, -2.5) * mm, "end": v(-6, -2.46) * mm});
            skLineSegment(sketch, "E3022", {"start": v(-6, -2.46) * mm, "end": v(-6, -2.4) * mm});
            skLineSegment(sketch, "E3023", {"start": v(-6, -2.4) * mm, "end": v(-6, -2.33) * mm});
            skLineSegment(sketch, "E3024", {"start": v(-6, -2.33) * mm, "end": v(-6, -2.25) * mm});
            skLineSegment(sketch, "E3025", {"start": v(-6, -2.25) * mm, "end": v(-6, -2.17) * mm});
            skLineSegment(sketch, "E3026", {"start": v(-6, -2.17) * mm, "end": v(-6, -2.08) * mm});
            skLineSegment(sketch, "E3027", {"start": v(-6, -2.08) * mm, "end": v(-6, -1.97) * mm});
            skLineSegment(sketch, "E3028", {"start": v(-6, -1.97) * mm, "end": v(-6, -1.87) * mm});
            skLineSegment(sketch, "E3029", {"start": v(-6, -1.87) * mm, "end": v(-6, -1.75) * mm});
            skLineSegment(sketch, "E3030", {"start": v(-6, -1.75) * mm, "end": v(-6, -1.63) * mm});
            skLineSegment(sketch, "E3031", {"start": v(-6, -1.63) * mm, "end": v(-6, -1.5) * mm});
            skLineSegment(sketch, "E3032", {"start": v(-6, -1.5) * mm, "end": v(-6, -1.38) * mm});
            skLineSegment(sketch, "E3033", {"start": v(-6, -1.38) * mm, "end": v(-6, -1.24) * mm});
            skLineSegment(sketch, "E3034", {"start": v(-6, -1.24) * mm, "end": v(-6, -1.1) * mm});
            skLineSegment(sketch, "E3035", {"start": v(-6, -1.1) * mm, "end": v(-6, -0.96) * mm});
            skLineSegment(sketch, "E3036", {"start": v(-6, -0.96) * mm, "end": v(-6, -0.82) * mm});
            skLineSegment(sketch, "E3037", {"start": v(-6, -0.82) * mm, "end": v(-6, -0.67) * mm});
            skLineSegment(sketch, "E3038", {"start": v(-6, -0.67) * mm, "end": v(-6, -0.52) * mm});
            skLineSegment(sketch, "E3039", {"start": v(-6, -0.52) * mm, "end": v(-6, -0.37) * mm});
            skLineSegment(sketch, "E3040", {"start": v(-6, -0.37) * mm, "end": v(-6, -0.22) * mm});
            skLineSegment(sketch, "E3041", {"start": v(-6, -0.22) * mm, "end": v(-6, -0.07) * mm});
            skLineSegment(sketch, "E3042", {"start": v(-6, -0.07) * mm, "end": v(-6, 0.08) * mm});
            skLineSegment(sketch, "E3043", {"start": v(-6, 0.08) * mm, "end": v(-6, 0.23) * mm});
            skLineSegment(sketch, "E3044", {"start": v(-6, 0.23) * mm, "end": v(-6, 0.38) * mm});
            skLineSegment(sketch, "E3045", {"start": v(-6, 0.38) * mm, "end": v(-6, 0.53) * mm});
            skLineSegment(sketch, "E3046", {"start": v(-6, 0.53) * mm, "end": v(-6, 0.68) * mm});
            skLineSegment(sketch, "E3047", {"start": v(-6, 0.68) * mm, "end": v(-6, 0.82) * mm});
            skLineSegment(sketch, "E3048", {"start": v(-6, 0.82) * mm, "end": v(-6, 0.97) * mm});
            skLineSegment(sketch, "E3049", {"start": v(-6, 0.97) * mm, "end": v(-6, 1.1) * mm});
            skLineSegment(sketch, "E3050", {"start": v(-6, 1.1) * mm, "end": v(-6, 1.24) * mm});
            skLineSegment(sketch, "E3051", {"start": v(-6, 1.24) * mm, "end": v(-6, 1.37) * mm});
            skLineSegment(sketch, "E3052", {"start": v(-6, 1.37) * mm, "end": v(-6, 1.5) * mm});
            skLineSegment(sketch, "E3053", {"start": v(-6, 1.5) * mm, "end": v(-6, 1.61) * mm});
            skLineSegment(sketch, "E3054", {"start": v(-6, 1.61) * mm, "end": v(-6, 1.73) * mm});
            skLineSegment(sketch, "E3055", {"start": v(-6, 1.73) * mm, "end": v(-6, 1.84) * mm});
            skLineSegment(sketch, "E3056", {"start": v(-6, 1.84) * mm, "end": v(-6, 1.94) * mm});
            skLineSegment(sketch, "E3057", {"start": v(-6, 1.94) * mm, "end": v(-6, 2.03) * mm});
            skLineSegment(sketch, "E3058", {"start": v(-6, 2.03) * mm, "end": v(-6, 2.12) * mm});
            skLineSegment(sketch, "E3059", {"start": v(-6, 2.12) * mm, "end": v(-6, 2.2) * mm});
            skLineSegment(sketch, "E3060", {"start": v(-6, 2.2) * mm, "end": v(-6, 2.26) * mm});
            skLineSegment(sketch, "E3061", {"start": v(-6, 2.26) * mm, "end": v(-6, 2.32) * mm});
            skLineSegment(sketch, "E3062", {"start": v(-6, 2.32) * mm, "end": v(-6, 2.37) * mm});
            skLineSegment(sketch, "E3063", {"start": v(-6, 2.37) * mm, "end": v(-6, 2.41) * mm});
            skLineSegment(sketch, "E3064", {"start": v(-6, 2.41) * mm, "end": v(-6, 2.44) * mm});
            skLineSegment(sketch, "E3065", {"start": v(-6, 2.44) * mm, "end": v(-6, 2.46) * mm});
            skLineSegment(sketch, "E3066", {"start": v(-6, 2.46) * mm, "end": v(-6, 2.46) * mm});
            skLineSegment(sketch, "E3067", {"start": v(-6, 2.46) * mm, "end": v(-6, 2.47) * mm});
            skLineSegment(sketch, "E3068", {"start": v(-6, 2.47) * mm, "end": v(-6, 2.48) * mm});
            skLineSegment(sketch, "E3069", {"start": v(-6, 2.48) * mm, "end": v(-5.99, 2.5) * mm});
            skLineSegment(sketch, "E3070", {"start": v(-5.99, 2.5) * mm, "end": v(-5.99, 2.5) * mm});
            skLineSegment(sketch, "E3071", {"start": v(-5.99, 2.5) * mm, "end": v(-5.99, 2.52) * mm});
            skLineSegment(sketch, "E3072", {"start": v(-5.99, 2.52) * mm, "end": v(-5.99, 2.53) * mm});
            skLineSegment(sketch, "E3073", {"start": v(-5.99, 2.53) * mm, "end": v(-5.99, 2.53) * mm});
            skLineSegment(sketch, "E3074", {"start": v(-5.99, 2.53) * mm, "end": v(-5.99, 2.54) * mm});
            skLineSegment(sketch, "E3075", {"start": v(-5.99, 2.54) * mm, "end": v(-5.98, 2.55) * mm});
            skLineSegment(sketch, "E3076", {"start": v(-5.98, 2.55) * mm, "end": v(-5.98, 2.56) * mm});
            skLineSegment(sketch, "E3077", {"start": v(-5.98, 2.56) * mm, "end": v(-5.98, 2.56) * mm});
            skLineSegment(sketch, "E3078", {"start": v(-5.98, 2.56) * mm, "end": v(-5.98, 2.57) * mm});
            skLineSegment(sketch, "E3079", {"start": v(-5.98, 2.57) * mm, "end": v(-5.98, 2.58) * mm});
            skLineSegment(sketch, "E3080", {"start": v(-5.98, 2.58) * mm, "end": v(-5.98, 2.58) * mm});
            skLineSegment(sketch, "E3081", {"start": v(-5.98, 2.58) * mm, "end": v(-5.97, 2.59) * mm});
            skLineSegment(sketch, "E3082", {"start": v(-5.97, 2.59) * mm, "end": v(-5.97, 2.6) * mm});
            skLineSegment(sketch, "E3083", {"start": v(-5.97, 2.6) * mm, "end": v(-5.97, 2.6) * mm});
            skLineSegment(sketch, "E3084", {"start": v(-5.97, 2.6) * mm, "end": v(-5.96, 2.6) * mm});
            skLineSegment(sketch, "E3085", {"start": v(-5.96, 2.6) * mm, "end": v(-5.96, 2.61) * mm});
            skLineSegment(sketch, "E3086", {"start": v(-5.96, 2.61) * mm, "end": v(-5.96, 2.62) * mm});
            skLineSegment(sketch, "E3087", {"start": v(-5.96, 2.62) * mm, "end": v(-5.96, 2.62) * mm});
            skLineSegment(sketch, "E3088", {"start": v(-5.96, 2.62) * mm, "end": v(-5.95, 2.63) * mm});
            skLineSegment(sketch, "E3089", {"start": v(-5.95, 2.63) * mm, "end": v(-5.95, 2.63) * mm});
            skLineSegment(sketch, "E3090", {"start": v(-5.95, 2.63) * mm, "end": v(-5.95, 2.64) * mm});
            skLineSegment(sketch, "E3091", {"start": v(-5.95, 2.64) * mm, "end": v(-5.94, 2.64) * mm});
            skLineSegment(sketch, "E3092", {"start": v(-5.94, 2.64) * mm, "end": v(-5.94, 2.64) * mm});
            skLineSegment(sketch, "E3093", {"start": v(-5.94, 2.64) * mm, "end": v(-5.93, 2.65) * mm});
            skLineSegment(sketch, "E3094", {"start": v(-5.93, 2.65) * mm, "end": v(-5.93, 2.65) * mm});
            skLineSegment(sketch, "E3095", {"start": v(-5.93, 2.65) * mm, "end": v(-5.92, 2.65) * mm});
            skLineSegment(sketch, "E3096", {"start": v(-5.92, 2.65) * mm, "end": v(-5.92, 2.65) * mm});
            skLineSegment(sketch, "E3097", {"start": v(-5.92, 2.65) * mm, "end": v(-5.92, 2.66) * mm});
            skLineSegment(sketch, "E3098", {"start": v(-5.92, 2.66) * mm, "end": v(-5.91, 2.66) * mm});
            skLineSegment(sketch, "E3099", {"start": v(-5.91, 2.66) * mm, "end": v(-5.9, 2.66) * mm});
            skLineSegment(sketch, "E3100", {"start": v(-5.9, 2.66) * mm, "end": v(-5.9, 2.66) * mm});
            skLineSegment(sketch, "E3101", {"start": v(-5.9, 2.66) * mm, "end": v(-5.89, 2.67) * mm});
            skLineSegment(sketch, "E3102", {"start": v(-5.89, 2.67) * mm, "end": v(-5.88, 2.67) * mm});
            skLineSegment(sketch, "E3103", {"start": v(-5.88, 2.67) * mm, "end": v(-5.88, 2.67) * mm});
            skLineSegment(sketch, "E3104", {"start": v(-5.88, 2.67) * mm, "end": v(-5.87, 2.67) * mm});
            skLineSegment(sketch, "E3105", {"start": v(-5.87, 2.67) * mm, "end": v(-5.86, 2.67) * mm});
            skLineSegment(sketch, "E3106", {"start": v(-5.86, 2.67) * mm, "end": v(-5.86, 2.67) * mm});
            skLineSegment(sketch, "E3107", {"start": v(-5.86, 2.67) * mm, "end": v(-5.85, 2.67) * mm});
            skLineSegment(sketch, "E3108", {"start": v(-5.85, 2.67) * mm, "end": v(-5.84, 2.67) * mm});
            skLineSegment(sketch, "E3109", {"start": v(-5.84, 2.67) * mm, "end": v(-5.83, 2.67) * mm});
            skLineSegment(sketch, "E3110", {"start": v(-5.83, 2.67) * mm, "end": v(-5.83, 2.67) * mm});
            skLineSegment(sketch, "E3111", {"start": v(-5.83, 2.67) * mm, "end": v(-5.82, 2.68) * mm});
            skLineSegment(sketch, "E3112", {"start": v(-5.82, 2.68) * mm, "end": v(-5.81, 2.68) * mm});
            skLineSegment(sketch, "E3113", {"start": v(-5.81, 2.68) * mm, "end": v(-5.8, 2.68) * mm});
            skLineSegment(sketch, "E3114", {"start": v(-5.8, 2.68) * mm, "end": v(-5.8, 2.68) * mm});
            skLineSegment(sketch, "E3115", {"start": v(-5.8, 2.68) * mm, "end": v(-5.79, 2.68) * mm});
            skLineSegment(sketch, "E3116", {"start": v(-5.79, 2.68) * mm, "end": v(-5.78, 2.68) * mm});
            skLineSegment(sketch, "E3117", {"start": v(-5.78, 2.68) * mm, "end": v(-5.77, 2.68) * mm});
            skLineSegment(sketch, "E3118", {"start": v(-5.77, 2.68) * mm, "end": v(-5.76, 2.68) * mm});
            skLineSegment(sketch, "E3119", {"start": v(-5.76, 2.68) * mm, "end": v(-5.75, 2.68) * mm});
            skLineSegment(sketch, "E3120", {"start": v(-5.75, 2.68) * mm, "end": v(-5.74, 2.68) * mm});
            skLineSegment(sketch, "E3121", {"start": v(-5.74, 2.68) * mm, "end": v(-5.73, 2.68) * mm});
            skLineSegment(sketch, "E3122", {"start": v(-5.73, 2.68) * mm, "end": v(-5.71, 2.68) * mm});
            skLineSegment(sketch, "E3123", {"start": v(-5.71, 2.68) * mm, "end": v(-5.7, 2.68) * mm});
            skLineSegment(sketch, "E3124", {"start": v(-5.7, 2.68) * mm, "end": v(-5.68, 2.68) * mm});
            skLineSegment(sketch, "E3125", {"start": v(-5.68, 2.68) * mm, "end": v(-5.66, 2.68) * mm});
            skLineSegment(sketch, "E3126", {"start": v(-5.66, 2.68) * mm, "end": v(-5.64, 2.68) * mm});
            skLineSegment(sketch, "E3127", {"start": v(-5.64, 2.68) * mm, "end": v(-5.63, 2.68) * mm});
            skLineSegment(sketch, "E3128", {"start": v(-5.63, 2.68) * mm, "end": v(-5.6, 2.68) * mm});
            skLineSegment(sketch, "E3129", {"start": v(-5.6, 2.68) * mm, "end": v(-5.59, 2.68) * mm});
            skLineSegment(sketch, "E3130", {"start": v(-5.59, 2.68) * mm, "end": v(-5.57, 2.68) * mm});
            skLineSegment(sketch, "E3131", {"start": v(-5.57, 2.68) * mm, "end": v(-5.54, 2.68) * mm});
            skLineSegment(sketch, "E3132", {"start": v(-5.54, 2.68) * mm, "end": v(-5.52, 2.68) * mm});
            skLineSegment(sketch, "E3133", {"start": v(-5.52, 2.68) * mm, "end": v(-5.5, 2.68) * mm});
            skLineSegment(sketch, "E3134", {"start": v(-5.5, 2.68) * mm, "end": v(-5.48, 2.68) * mm});
            skLineSegment(sketch, "E3135", {"start": v(-5.48, 2.68) * mm, "end": v(-5.46, 2.68) * mm});
            skLineSegment(sketch, "E3136", {"start": v(-5.46, 2.68) * mm, "end": v(-5.44, 2.68) * mm});
            skLineSegment(sketch, "E3137", {"start": v(-5.44, 2.68) * mm, "end": v(-5.41, 2.68) * mm});
            skLineSegment(sketch, "E3138", {"start": v(-5.41, 2.68) * mm, "end": v(-5.4, 2.68) * mm});
            skLineSegment(sketch, "E3139", {"start": v(-5.4, 2.68) * mm, "end": v(-5.37, 2.68) * mm});
            skLineSegment(sketch, "E3140", {"start": v(-5.37, 2.68) * mm, "end": v(-5.35, 2.68) * mm});
            skLineSegment(sketch, "E3141", {"start": v(-5.35, 2.68) * mm, "end": v(-5.33, 2.68) * mm});
            skLineSegment(sketch, "E3142", {"start": v(-5.33, 2.68) * mm, "end": v(-5.3, 2.68) * mm});
            skLineSegment(sketch, "E3143", {"start": v(-5.3, 2.68) * mm, "end": v(-5.29, 2.68) * mm});
            skLineSegment(sketch, "E3144", {"start": v(-5.29, 2.68) * mm, "end": v(-5.27, 2.68) * mm});
            skLineSegment(sketch, "E3145", {"start": v(-5.27, 2.68) * mm, "end": v(-5.25, 2.68) * mm});
            skLineSegment(sketch, "E3146", {"start": v(-5.25, 2.68) * mm, "end": v(-5.23, 2.68) * mm});
            skLineSegment(sketch, "E3147", {"start": v(-5.23, 2.68) * mm, "end": v(-5.21, 2.68) * mm});
            skLineSegment(sketch, "E3148", {"start": v(-5.21, 2.68) * mm, "end": v(-5.2, 2.68) * mm});
            skLineSegment(sketch, "E3149", {"start": v(-5.2, 2.68) * mm, "end": v(-5.18, 2.68) * mm});
            skLineSegment(sketch, "E3150", {"start": v(-5.18, 2.68) * mm, "end": v(-5.16, 2.68) * mm});
            skLineSegment(sketch, "E3151", {"start": v(-5.16, 2.68) * mm, "end": v(-5.15, 2.68) * mm});
            skLineSegment(sketch, "E3152", {"start": v(-5.15, 2.68) * mm, "end": v(-5.13, 2.68) * mm});
            skLineSegment(sketch, "E3153", {"start": v(-5.13, 2.68) * mm, "end": v(-5.12, 2.68) * mm});
            skLineSegment(sketch, "E3154", {"start": v(-5.12, 2.68) * mm, "end": v(-5.11, 2.68) * mm});
            skLineSegment(sketch, "E3155", {"start": v(-5.11, 2.68) * mm, "end": v(-5.1, 2.68) * mm});
            skLineSegment(sketch, "E3156", {"start": v(-5.1, 2.68) * mm, "end": v(-5.1, 2.68) * mm});
            skLineSegment(sketch, "E3157", {"start": v(-5.1, 2.68) * mm, "end": v(-5.08, 2.68) * mm});
            skLineSegment(sketch, "E3158", {"start": v(-5.08, 2.68) * mm, "end": v(-5.08, 2.68) * mm});
            skLineSegment(sketch, "E3159", {"start": v(-5.08, 2.68) * mm, "end": v(-5.07, 2.68) * mm});
            skLineSegment(sketch, "E3160", {"start": v(-5.07, 2.68) * mm, "end": v(-5.07, 2.68) * mm});
            skLineSegment(sketch, "E3161", {"start": v(-5.07, 2.68) * mm, "end": v(-5.02, 2.67) * mm});
            skLineSegment(sketch, "E3162", {"start": v(-5.02, 2.67) * mm, "end": v(-4.96, 2.67) * mm});
            skLineSegment(sketch, "E3163", {"start": v(-4.96, 2.67) * mm, "end": v(-4.91, 2.67) * mm});
            skLineSegment(sketch, "E3164", {"start": v(-4.91, 2.67) * mm, "end": v(-4.86, 2.66) * mm});
            skLineSegment(sketch, "E3165", {"start": v(-4.86, 2.66) * mm, "end": v(-4.8, 2.65) * mm});
            skLineSegment(sketch, "E3166", {"start": v(-4.8, 2.65) * mm, "end": v(-4.76, 2.65) * mm});
            skLineSegment(sketch, "E3167", {"start": v(-4.76, 2.65) * mm, "end": v(-4.7, 2.64) * mm});
            skLineSegment(sketch, "E3168", {"start": v(-4.7, 2.64) * mm, "end": v(-4.65, 2.62) * mm});
            skLineSegment(sketch, "E3169", {"start": v(-4.65, 2.62) * mm, "end": v(-4.6, 2.6) * mm});
            skLineSegment(sketch, "E3170", {"start": v(-4.6, 2.6) * mm, "end": v(-4.55, 2.6) * mm});
            skLineSegment(sketch, "E3171", {"start": v(-4.55, 2.6) * mm, "end": v(-4.5, 2.58) * mm});
            skLineSegment(sketch, "E3172", {"start": v(-4.5, 2.58) * mm, "end": v(-4.46, 2.56) * mm});
            skLineSegment(sketch, "E3173", {"start": v(-4.46, 2.56) * mm, "end": v(-4.4, 2.54) * mm});
            skLineSegment(sketch, "E3174", {"start": v(-4.4, 2.54) * mm, "end": v(-4.36, 2.52) * mm});
            skLineSegment(sketch, "E3175", {"start": v(-4.36, 2.52) * mm, "end": v(-4.32, 2.5) * mm});
            skLineSegment(sketch, "E3176", {"start": v(-4.32, 2.5) * mm, "end": v(-4.27, 2.47) * mm});
            skLineSegment(sketch, "E3177", {"start": v(-4.27, 2.47) * mm, "end": v(-4.23, 2.45) * mm});
            skLineSegment(sketch, "E3178", {"start": v(-4.23, 2.45) * mm, "end": v(-4.18, 2.42) * mm});
            skLineSegment(sketch, "E3179", {"start": v(-4.18, 2.42) * mm, "end": v(-4.14, 2.4) * mm});
            skLineSegment(sketch, "E3180", {"start": v(-4.14, 2.4) * mm, "end": v(-4.1, 2.37) * mm});
            skLineSegment(sketch, "E3181", {"start": v(-4.1, 2.37) * mm, "end": v(-4.05, 2.34) * mm});
            skLineSegment(sketch, "E3182", {"start": v(-4.05, 2.34) * mm, "end": v(-4.01, 2.3) * mm});
            skLineSegment(sketch, "E3183", {"start": v(-4.01, 2.3) * mm, "end": v(-3.98, 2.27) * mm});
            skLineSegment(sketch, "E3184", {"start": v(-3.98, 2.27) * mm, "end": v(-3.94, 2.24) * mm});
            skLineSegment(sketch, "E3185", {"start": v(-3.94, 2.24) * mm, "end": v(-3.9, 2.2) * mm});
            skLineSegment(sketch, "E3186", {"start": v(-3.9, 2.2) * mm, "end": v(-3.86, 2.17) * mm});
            skLineSegment(sketch, "E3187", {"start": v(-3.86, 2.17) * mm, "end": v(-3.83, 2.14) * mm});
            skLineSegment(sketch, "E3188", {"start": v(-3.83, 2.14) * mm, "end": v(-3.8, 2.1) * mm});
            skLineSegment(sketch, "E3189", {"start": v(-3.8, 2.1) * mm, "end": v(-3.76, 2.06) * mm});
            skLineSegment(sketch, "E3190", {"start": v(-3.76, 2.06) * mm, "end": v(-3.73, 2.02) * mm});
            skLineSegment(sketch, "E3191", {"start": v(-3.73, 2.02) * mm, "end": v(-3.7, 1.98) * mm});
            skLineSegment(sketch, "E3192", {"start": v(-3.7, 1.98) * mm, "end": v(-3.67, 1.94) * mm});
            skLineSegment(sketch, "E3193", {"start": v(-3.67, 1.94) * mm, "end": v(-3.64, 1.9) * mm});
            skLineSegment(sketch, "E3194", {"start": v(-3.64, 1.9) * mm, "end": v(-3.62, 1.85) * mm});
            skLineSegment(sketch, "E3195", {"start": v(-3.62, 1.85) * mm, "end": v(-3.6, 1.8) * mm});
            skLineSegment(sketch, "E3196", {"start": v(-3.6, 1.8) * mm, "end": v(-3.57, 1.76) * mm});
            skLineSegment(sketch, "E3197", {"start": v(-3.57, 1.76) * mm, "end": v(-3.54, 1.71) * mm});
            skLineSegment(sketch, "E3198", {"start": v(-3.54, 1.71) * mm, "end": v(-3.52, 1.67) * mm});
            skLineSegment(sketch, "E3199", {"start": v(-3.52, 1.67) * mm, "end": v(-3.5, 1.62) * mm});
            skLineSegment(sketch, "E3200", {"start": v(-3.5, 1.62) * mm, "end": v(-3.49, 1.57) * mm});
            skLineSegment(sketch, "E3201", {"start": v(-3.49, 1.57) * mm, "end": v(-3.47, 1.52) * mm});
            skLineSegment(sketch, "E3202", {"start": v(-3.47, 1.52) * mm, "end": v(-3.46, 1.47) * mm});
            skLineSegment(sketch, "E3203", {"start": v(-3.46, 1.47) * mm, "end": v(-3.44, 1.42) * mm});
            skLineSegment(sketch, "E3204", {"start": v(-3.44, 1.42) * mm, "end": v(-3.43, 1.37) * mm});
            skLineSegment(sketch, "E3205", {"start": v(-3.43, 1.37) * mm, "end": v(-3.42, 1.32) * mm});
            skLineSegment(sketch, "E3206", {"start": v(-3.42, 1.32) * mm, "end": v(-3.41, 1.27) * mm});
            skLineSegment(sketch, "E3207", {"start": v(-3.41, 1.27) * mm, "end": v(-3.4, 1.21) * mm});
            skLineSegment(sketch, "E3208", {"start": v(-3.4, 1.21) * mm, "end": v(-3.4, 1.16) * mm});
            skLineSegment(sketch, "E3209", {"start": v(-3.4, 1.16) * mm, "end": v(-3.4, 1.1) * mm});
            skLineSegment(sketch, "E3210", {"start": v(-3.4, 1.1) * mm, "end": v(-3.4, 1.05) * mm});
            skLineSegment(sketch, "E3211", {"start": v(-3.4, 1.05) * mm, "end": v(-3.4, 1) * mm});
            skLineSegment(sketch, "E3212", {"start": v(-3.4, 1) * mm, "end": v(-3.4, 0.95) * mm});
            skLineSegment(sketch, "E3213", {"start": v(-3.4, 0.95) * mm, "end": v(-3.4, 0.9) * mm});
            skLineSegment(sketch, "E3214", {"start": v(-3.4, 0.9) * mm, "end": v(-3.41, 0.84) * mm});
            skLineSegment(sketch, "E3215", {"start": v(-3.41, 0.84) * mm, "end": v(-3.42, 0.8) * mm});
            skLineSegment(sketch, "E3216", {"start": v(-3.42, 0.8) * mm, "end": v(-3.43, 0.74) * mm});
            skLineSegment(sketch, "E3217", {"start": v(-3.43, 0.74) * mm, "end": v(-3.44, 0.7) * mm});
            skLineSegment(sketch, "E3218", {"start": v(-3.44, 0.7) * mm, "end": v(-3.45, 0.65) * mm});
            skLineSegment(sketch, "E3219", {"start": v(-3.45, 0.65) * mm, "end": v(-3.46, 0.6) * mm});
            skLineSegment(sketch, "E3220", {"start": v(-3.46, 0.6) * mm, "end": v(-3.48, 0.55) * mm});
            skLineSegment(sketch, "E3221", {"start": v(-3.48, 0.55) * mm, "end": v(-3.5, 0.5) * mm});
            skLineSegment(sketch, "E3222", {"start": v(-3.5, 0.5) * mm, "end": v(-3.51, 0.46) * mm});
            skLineSegment(sketch, "E3223", {"start": v(-3.51, 0.46) * mm, "end": v(-3.53, 0.41) * mm});
            skLineSegment(sketch, "E3224", {"start": v(-3.53, 0.41) * mm, "end": v(-3.55, 0.37) * mm});
            skLineSegment(sketch, "E3225", {"start": v(-3.55, 0.37) * mm, "end": v(-3.58, 0.32) * mm});
            skLineSegment(sketch, "E3226", {"start": v(-3.58, 0.32) * mm, "end": v(-3.6, 0.28) * mm});
            skLineSegment(sketch, "E3227", {"start": v(-3.6, 0.28) * mm, "end": v(-3.62, 0.24) * mm});
            skLineSegment(sketch, "E3228", {"start": v(-3.62, 0.24) * mm, "end": v(-3.65, 0.2) * mm});
            skLineSegment(sketch, "E3229", {"start": v(-3.65, 0.2) * mm, "end": v(-3.68, 0.15) * mm});
            skLineSegment(sketch, "E3230", {"start": v(-3.68, 0.15) * mm, "end": v(-3.7, 0.11) * mm});
            skLineSegment(sketch, "E3231", {"start": v(-3.7, 0.11) * mm, "end": v(-3.74, 0.08) * mm});
            skLineSegment(sketch, "E3232", {"start": v(-3.74, 0.08) * mm, "end": v(-3.77, 0.04) * mm});
            skLineSegment(sketch, "E3233", {"start": v(-3.77, 0.04) * mm, "end": v(-3.8, 0) * mm});
            skLineSegment(sketch, "E3234", {"start": v(-3.8, 0) * mm, "end": v(-3.83, -0.04) * mm});
            skLineSegment(sketch, "E3235", {"start": v(-3.83, -0.04) * mm, "end": v(-3.87, -0.07) * mm});
            skLineSegment(sketch, "E3236", {"start": v(-3.87, -0.07) * mm, "end": v(-3.9, -0.1) * mm});
            skLineSegment(sketch, "E3237", {"start": v(-3.9, -0.1) * mm, "end": v(-3.94, -0.14) * mm});
            skLineSegment(sketch, "E3238", {"start": v(-3.94, -0.14) * mm, "end": v(-3.98, -0.17) * mm});
            skLineSegment(sketch, "E3239", {"start": v(-3.98, -0.17) * mm, "end": v(-4.02, -0.2) * mm});
            skLineSegment(sketch, "E3240", {"start": v(-4.02, -0.2) * mm, "end": v(-4.06, -0.23) * mm});
            skLineSegment(sketch, "E3241", {"start": v(-4.06, -0.23) * mm, "end": v(-4.1, -0.26) * mm});
            skLineSegment(sketch, "E3242", {"start": v(-4.1, -0.26) * mm, "end": v(-4.14, -0.3) * mm});
            skLineSegment(sketch, "E3243", {"start": v(-4.14, -0.3) * mm, "end": v(-4.18, -0.32) * mm});
            skLineSegment(sketch, "E3244", {"start": v(-4.18, -0.32) * mm, "end": v(-4.22, -0.34) * mm});
            skLineSegment(sketch, "E3245", {"start": v(-4.22, -0.34) * mm, "end": v(-4.27, -0.37) * mm});
            skLineSegment(sketch, "E3246", {"start": v(-4.27, -0.37) * mm, "end": v(-4.31, -0.4) * mm});
            skLineSegment(sketch, "E3247", {"start": v(-4.31, -0.4) * mm, "end": v(-4.36, -0.41) * mm});
            skLineSegment(sketch, "E3248", {"start": v(-4.36, -0.41) * mm, "end": v(-4.4, -0.43) * mm});
            skLineSegment(sketch, "E3249", {"start": v(-4.4, -0.43) * mm, "end": v(-4.45, -0.45) * mm});
            skLineSegment(sketch, "E3250", {"start": v(-4.45, -0.45) * mm, "end": v(-4.5, -0.47) * mm});
            skLineSegment(sketch, "E3251", {"start": v(-4.5, -0.47) * mm, "end": v(-4.55, -0.49) * mm});
            skLineSegment(sketch, "E3252", {"start": v(-4.55, -0.49) * mm, "end": v(-4.6, -0.5) * mm});
            skLineSegment(sketch, "E3253", {"start": v(-4.6, -0.5) * mm, "end": v(-4.65, -0.52) * mm});
            skLineSegment(sketch, "E3254", {"start": v(-4.65, -0.52) * mm, "end": v(-4.7, -0.53) * mm});
            skLineSegment(sketch, "E3255", {"start": v(-4.7, -0.53) * mm, "end": v(-4.76, -0.54) * mm});
            skLineSegment(sketch, "E3256", {"start": v(-4.76, -0.54) * mm, "end": v(-4.8, -0.55) * mm});
            skLineSegment(sketch, "E3257", {"start": v(-4.8, -0.55) * mm, "end": v(-4.86, -0.56) * mm});
            skLineSegment(sketch, "E3258", {"start": v(-4.86, -0.56) * mm, "end": v(-4.92, -0.57) * mm});
            skLineSegment(sketch, "E3259", {"start": v(-4.92, -0.57) * mm, "end": v(-4.97, -0.57) * mm});
            skLineSegment(sketch, "E3260", {"start": v(-4.97, -0.57) * mm, "end": v(-5.02, -0.58) * mm});
            skLineSegment(sketch, "E3261", {"start": v(-5.02, -0.58) * mm, "end": v(-5.04, -0.58) * mm});
            skLineSegment(sketch, "E3262", {"start": v(-5.04, -0.58) * mm, "end": v(-5.05, -0.58) * mm});
            skLineSegment(sketch, "E3263", {"start": v(-5.05, -0.58) * mm, "end": v(-5.06, -0.57) * mm});
            skLineSegment(sketch, "E3264", {"start": v(-5.06, -0.57) * mm, "end": v(-5.07, -0.57) * mm});
            skLineSegment(sketch, "E3265", {"start": v(-5.07, -0.57) * mm, "end": v(-5.09, -0.57) * mm});
            skLineSegment(sketch, "E3266", {"start": v(-5.09, -0.57) * mm, "end": v(-5.1, -0.57) * mm});
            skLineSegment(sketch, "E3267", {"start": v(-5.1, -0.57) * mm, "end": v(-5.1, -0.57) * mm});
            skLineSegment(sketch, "E3268", {"start": v(-5.1, -0.57) * mm, "end": v(-5.12, -0.57) * mm});
            skLineSegment(sketch, "E3269", {"start": v(-5.12, -0.57) * mm, "end": v(-5.13, -0.57) * mm});
            skLineSegment(sketch, "E3270", {"start": v(-5.13, -0.57) * mm, "end": v(-5.14, -0.57) * mm});
            skLineSegment(sketch, "E3271", {"start": v(-5.14, -0.57) * mm, "end": v(-5.15, -0.56) * mm});
            skLineSegment(sketch, "E3272", {"start": v(-5.15, -0.56) * mm, "end": v(-5.16, -0.56) * mm});
            skLineSegment(sketch, "E3273", {"start": v(-5.16, -0.56) * mm, "end": v(-5.17, -0.56) * mm});
            skLineSegment(sketch, "E3274", {"start": v(-5.17, -0.56) * mm, "end": v(-5.18, -0.56) * mm});
            skLineSegment(sketch, "E3275", {"start": v(-5.18, -0.56) * mm, "end": v(-5.19, -0.55) * mm});
            skLineSegment(sketch, "E3276", {"start": v(-5.19, -0.55) * mm, "end": v(-5.2, -0.55) * mm});
            skLineSegment(sketch, "E3277", {"start": v(-5.2, -0.55) * mm, "end": v(-5.2, -0.55) * mm});
            skLineSegment(sketch, "E3278", {"start": v(-5.2, -0.55) * mm, "end": v(-5.22, -0.54) * mm});
            skLineSegment(sketch, "E3279", {"start": v(-5.22, -0.54) * mm, "end": v(-5.22, -0.54) * mm});
            skLineSegment(sketch, "E3280", {"start": v(-5.22, -0.54) * mm, "end": v(-5.23, -0.54) * mm});
            skLineSegment(sketch, "E3281", {"start": v(-5.23, -0.54) * mm, "end": v(-5.24, -0.53) * mm});
            skLineSegment(sketch, "E3282", {"start": v(-5.24, -0.53) * mm, "end": v(-5.25, -0.53) * mm});
            skLineSegment(sketch, "E3283", {"start": v(-5.25, -0.53) * mm, "end": v(-5.25, -0.53) * mm});
            skLineSegment(sketch, "E3284", {"start": v(-5.25, -0.53) * mm, "end": v(-5.26, -0.52) * mm});
            skLineSegment(sketch, "E3285", {"start": v(-5.26, -0.52) * mm, "end": v(-5.27, -0.52) * mm});
            skLineSegment(sketch, "E3286", {"start": v(-5.27, -0.52) * mm, "end": v(-5.28, -0.52) * mm});
            skLineSegment(sketch, "E3287", {"start": v(-5.28, -0.52) * mm, "end": v(-5.28, -0.51) * mm});
            skLineSegment(sketch, "E3288", {"start": v(-5.28, -0.51) * mm, "end": v(-5.29, -0.5) * mm});
            skLineSegment(sketch, "E3289", {"start": v(-5.29, -0.5) * mm, "end": v(-5.3, -0.5) * mm});
            skLineSegment(sketch, "E3290", {"start": v(-5.3, -0.5) * mm, "end": v(-5.3, -0.5) * mm});
            skLineSegment(sketch, "E3291", {"start": v(-5.3, -0.5) * mm, "end": v(-5.31, -0.49) * mm});
            skLineSegment(sketch, "E3292", {"start": v(-5.31, -0.49) * mm, "end": v(-5.32, -0.48) * mm});
            skLineSegment(sketch, "E3293", {"start": v(-5.32, -0.48) * mm, "end": v(-5.32, -0.48) * mm});
            skLineSegment(sketch, "E3294", {"start": v(-5.32, -0.48) * mm, "end": v(-5.33, -0.47) * mm});
            skLineSegment(sketch, "E3295", {"start": v(-5.33, -0.47) * mm, "end": v(-5.33, -0.47) * mm});
            skLineSegment(sketch, "E3296", {"start": v(-5.33, -0.47) * mm, "end": v(-5.33, -0.46) * mm});
            skLineSegment(sketch, "E3297", {"start": v(-5.33, -0.46) * mm, "end": v(-5.34, -0.46) * mm});
            skLineSegment(sketch, "E3298", {"start": v(-5.34, -0.46) * mm, "end": v(-5.34, -0.46) * mm});
            skLineSegment(sketch, "E3299", {"start": v(-5.34, -0.46) * mm, "end": v(-5.34, -0.45) * mm});
            skLineSegment(sketch, "E3300", {"start": v(-5.34, -0.45) * mm, "end": v(-5.35, -0.45) * mm});
            skLineSegment(sketch, "E3301", {"start": v(-5.35, -0.45) * mm, "end": v(-5.35, -0.44) * mm});
            skLineSegment(sketch, "E3302", {"start": v(-5.35, -0.44) * mm, "end": v(-5.35, -0.44) * mm});
            skLineSegment(sketch, "E3303", {"start": v(-5.35, -0.44) * mm, "end": v(-5.35, -0.43) * mm});
            skLineSegment(sketch, "E3304", {"start": v(-5.35, -0.43) * mm, "end": v(-5.35, -0.43) * mm});
            skLineSegment(sketch, "E3305", {"start": v(-5.35, -0.43) * mm, "end": v(-5.35, -0.42) * mm});
            skLineSegment(sketch, "E3306", {"start": v(-5.35, -0.42) * mm, "end": v(-5.35, -0.42) * mm});
            skLineSegment(sketch, "E3307", {"start": v(-5.35, -0.42) * mm, "end": v(-5.35, -0.41) * mm});
            skLineSegment(sketch, "E3308", {"start": v(-5.35, -0.41) * mm, "end": v(-5.35, -0.4) * mm});
            skLineSegment(sketch, "E3309", {"start": v(-5.35, -0.4) * mm, "end": v(-5.35, -0.4) * mm});
            skLineSegment(sketch, "E3310", {"start": v(-5.35, -0.4) * mm, "end": v(-5.35, -0.39) * mm});
            skLineSegment(sketch, "E3311", {"start": v(-5.35, -0.39) * mm, "end": v(-5.35, -0.38) * mm});
            skLineSegment(sketch, "E3312", {"start": v(-5.35, -0.38) * mm, "end": v(-5.35, -0.38) * mm});
            skLineSegment(sketch, "E3313", {"start": v(-5.35, -0.38) * mm, "end": v(-5.35, -0.37) * mm});
            skLineSegment(sketch, "E3314", {"start": v(-5.35, -0.37) * mm, "end": v(-5.35, -0.37) * mm});
            skLineSegment(sketch, "E3315", {"start": v(-5.35, -0.37) * mm, "end": v(-5.34, -0.36) * mm});
            skLineSegment(sketch, "E3316", {"start": v(-5.34, -0.36) * mm, "end": v(-5.34, -0.36) * mm});
            skLineSegment(sketch, "E3317", {"start": v(-5.34, -0.36) * mm, "end": v(-5.34, -0.35) * mm});
            skLineSegment(sketch, "E3318", {"start": v(-5.34, -0.35) * mm, "end": v(-5.33, -0.35) * mm});
            skLineSegment(sketch, "E3319", {"start": v(-5.33, -0.35) * mm, "end": v(-5.33, -0.34) * mm});
            skLineSegment(sketch, "E3320", {"start": v(-5.33, -0.34) * mm, "end": v(-5.33, -0.34) * mm});
            skLineSegment(sketch, "E3321", {"start": v(-5.33, -0.34) * mm, "end": v(-5.32, -0.33) * mm});
            skLineSegment(sketch, "E3322", {"start": v(-5.32, -0.33) * mm, "end": v(-5.32, -0.33) * mm});
            skLineSegment(sketch, "E3323", {"start": v(-5.32, -0.33) * mm, "end": v(-5.31, -0.32) * mm});
            skLineSegment(sketch, "E3324", {"start": v(-5.31, -0.32) * mm, "end": v(-5.3, -0.32) * mm});
            skLineSegment(sketch, "E3325", {"start": v(-5.3, -0.32) * mm, "end": v(-5.3, -0.32) * mm});
            skLineSegment(sketch, "E3326", {"start": v(-5.3, -0.32) * mm, "end": v(-5.3, -0.31) * mm});
            skLineSegment(sketch, "E3327", {"start": v(-5.3, -0.31) * mm, "end": v(-5.29, -0.31) * mm});
            skLineSegment(sketch, "E3328", {"start": v(-5.29, -0.31) * mm, "end": v(-5.28, -0.3) * mm});
            skLineSegment(sketch, "E3329", {"start": v(-5.28, -0.3) * mm, "end": v(-5.28, -0.3) * mm});
            skLineSegment(sketch, "E3330", {"start": v(-5.28, -0.3) * mm, "end": v(-5.27, -0.3) * mm});
            skLineSegment(sketch, "E3331", {"start": v(-5.27, -0.3) * mm, "end": v(-5.26, -0.3) * mm});
            skLineSegment(sketch, "E3332", {"start": v(-5.26, -0.3) * mm, "end": v(-5.26, -0.3) * mm});
            skLineSegment(sketch, "E3333", {"start": v(-5.26, -0.3) * mm, "end": v(-5.25, -0.3) * mm});
            skLineSegment(sketch, "E3334", {"start": v(-5.25, -0.3) * mm, "end": v(-5.24, -0.3) * mm});
            skLineSegment(sketch, "E3335", {"start": v(-5.24, -0.3) * mm, "end": v(-5.23, -0.29) * mm});
            skLineSegment(sketch, "E3336", {"start": v(-5.23, -0.29) * mm, "end": v(-5.23, -0.29) * mm});
            skLineSegment(sketch, "E3337", {"start": v(-5.23, -0.29) * mm, "end": v(-5.22, -0.29) * mm});
            skLineSegment(sketch, "E3338", {"start": v(-5.22, -0.29) * mm, "end": v(-5.2, -0.28) * mm});
            skLineSegment(sketch, "E3339", {"start": v(-5.2, -0.28) * mm, "end": v(-5.2, -0.28) * mm});
            skLineSegment(sketch, "E3340", {"start": v(-5.2, -0.28) * mm, "end": v(-5.18, -0.28) * mm});
            skLineSegment(sketch, "E3341", {"start": v(-5.18, -0.28) * mm, "end": v(-5.17, -0.28) * mm});
            skLineSegment(sketch, "E3342", {"start": v(-5.17, -0.28) * mm, "end": v(-5.16, -0.28) * mm});
            skLineSegment(sketch, "E3343", {"start": v(-5.16, -0.28) * mm, "end": v(-5.15, -0.28) * mm});
            skLineSegment(sketch, "E3344", {"start": v(-5.15, -0.28) * mm, "end": v(-5.14, -0.27) * mm});
            skLineSegment(sketch, "E3345", {"start": v(-5.14, -0.27) * mm, "end": v(-5.13, -0.27) * mm});
            skLineSegment(sketch, "E3346", {"start": v(-5.13, -0.27) * mm, "end": v(-5.12, -0.27) * mm});
            skLineSegment(sketch, "E3347", {"start": v(-5.12, -0.27) * mm, "end": v(-5.1, -0.27) * mm});
            skLineSegment(sketch, "E3348", {"start": v(-5.1, -0.27) * mm, "end": v(-5.1, -0.27) * mm});
            skLineSegment(sketch, "E3349", {"start": v(-5.1, -0.27) * mm, "end": v(-5.08, -0.27) * mm});
            skLineSegment(sketch, "E3350", {"start": v(-5.08, -0.27) * mm, "end": v(-5.07, -0.27) * mm});
            skLineSegment(sketch, "E3351", {"start": v(-5.07, -0.27) * mm, "end": v(-5.05, -0.27) * mm});
            skLineSegment(sketch, "E3352", {"start": v(-5.05, -0.27) * mm, "end": v(-5.04, -0.27) * mm});
            skLineSegment(sketch, "E3353", {"start": v(-5.04, -0.27) * mm, "end": v(-5.02, -0.27) * mm});
            skLineSegment(sketch, "E3354", {"start": v(-5.02, -0.27) * mm, "end": v(-4.98, -0.27) * mm});
            skLineSegment(sketch, "E3355", {"start": v(-4.98, -0.27) * mm, "end": v(-4.94, -0.27) * mm});
            skLineSegment(sketch, "E3356", {"start": v(-4.94, -0.27) * mm, "end": v(-4.9, -0.26) * mm});
            skLineSegment(sketch, "E3357", {"start": v(-4.9, -0.26) * mm, "end": v(-4.86, -0.26) * mm});
            skLineSegment(sketch, "E3358", {"start": v(-4.86, -0.26) * mm, "end": v(-4.82, -0.25) * mm});
            skLineSegment(sketch, "E3359", {"start": v(-4.82, -0.25) * mm, "end": v(-4.78, -0.24) * mm});
            skLineSegment(sketch, "E3360", {"start": v(-4.78, -0.24) * mm, "end": v(-4.73, -0.23) * mm});
            skLineSegment(sketch, "E3361", {"start": v(-4.73, -0.23) * mm, "end": v(-4.7, -0.22) * mm});
            skLineSegment(sketch, "E3362", {"start": v(-4.7, -0.22) * mm, "end": v(-4.66, -0.21) * mm});
            skLineSegment(sketch, "E3363", {"start": v(-4.66, -0.21) * mm, "end": v(-4.62, -0.2) * mm});
            skLineSegment(sketch, "E3364", {"start": v(-4.62, -0.2) * mm, "end": v(-4.58, -0.19) * mm});
            skLineSegment(sketch, "E3365", {"start": v(-4.58, -0.19) * mm, "end": v(-4.54, -0.17) * mm});
            skLineSegment(sketch, "E3366", {"start": v(-4.54, -0.17) * mm, "end": v(-4.5, -0.15) * mm});
            skLineSegment(sketch, "E3367", {"start": v(-4.5, -0.15) * mm, "end": v(-4.46, -0.14) * mm});
            skLineSegment(sketch, "E3368", {"start": v(-4.46, -0.14) * mm, "end": v(-4.43, -0.12) * mm});
            skLineSegment(sketch, "E3369", {"start": v(-4.43, -0.12) * mm, "end": v(-4.4, -0.1) * mm});
            skLineSegment(sketch, "E3370", {"start": v(-4.4, -0.1) * mm, "end": v(-4.36, -0.08) * mm});
            skLineSegment(sketch, "E3371", {"start": v(-4.36, -0.08) * mm, "end": v(-4.32, -0.06) * mm});
            skLineSegment(sketch, "E3372", {"start": v(-4.32, -0.06) * mm, "end": v(-4.29, -0.03) * mm});
            skLineSegment(sketch, "E3373", {"start": v(-4.29, -0.03) * mm, "end": v(-4.26, 0) * mm});
            skLineSegment(sketch, "E3374", {"start": v(-4.26, 0) * mm, "end": v(-4.22, 0.02) * mm});
            skLineSegment(sketch, "E3375", {"start": v(-4.22, 0.02) * mm, "end": v(-4.2, 0.04) * mm});
            skLineSegment(sketch, "E3376", {"start": v(-4.2, 0.04) * mm, "end": v(-4.16, 0.07) * mm});
            skLineSegment(sketch, "E3377", {"start": v(-4.16, 0.07) * mm, "end": v(-4.13, 0.1) * mm});
            skLineSegment(sketch, "E3378", {"start": v(-4.13, 0.1) * mm, "end": v(-4.1, 0.13) * mm});
            skLineSegment(sketch, "E3379", {"start": v(-4.1, 0.13) * mm, "end": v(-4.07, 0.15) * mm});
            skLineSegment(sketch, "E3380", {"start": v(-4.07, 0.15) * mm, "end": v(-4.05, 0.18) * mm});
            skLineSegment(sketch, "E3381", {"start": v(-4.05, 0.18) * mm, "end": v(-4.02, 0.22) * mm});
            skLineSegment(sketch, "E3382", {"start": v(-4.02, 0.22) * mm, "end": v(-4, 0.25) * mm});
            skLineSegment(sketch, "E3383", {"start": v(-4, 0.25) * mm, "end": v(-3.97, 0.28) * mm});
            skLineSegment(sketch, "E3384", {"start": v(-3.97, 0.28) * mm, "end": v(-3.95, 0.31) * mm});
            skLineSegment(sketch, "E3385", {"start": v(-3.95, 0.31) * mm, "end": v(-3.93, 0.35) * mm});
            skLineSegment(sketch, "E3386", {"start": v(-3.93, 0.35) * mm, "end": v(-3.9, 0.38) * mm});
            skLineSegment(sketch, "E3387", {"start": v(-3.9, 0.38) * mm, "end": v(-3.88, 0.42) * mm});
            skLineSegment(sketch, "E3388", {"start": v(-3.88, 0.42) * mm, "end": v(-3.86, 0.45) * mm});
            skLineSegment(sketch, "E3389", {"start": v(-3.86, 0.45) * mm, "end": v(-3.85, 0.49) * mm});
            skLineSegment(sketch, "E3390", {"start": v(-3.85, 0.49) * mm, "end": v(-3.83, 0.53) * mm});
            skLineSegment(sketch, "E3391", {"start": v(-3.83, 0.53) * mm, "end": v(-3.81, 0.56) * mm});
            skLineSegment(sketch, "E3392", {"start": v(-3.81, 0.56) * mm, "end": v(-3.8, 0.6) * mm});
            skLineSegment(sketch, "E3393", {"start": v(-3.8, 0.6) * mm, "end": v(-3.79, 0.64) * mm});
            skLineSegment(sketch, "E3394", {"start": v(-3.79, 0.64) * mm, "end": v(-3.77, 0.68) * mm});
            skLineSegment(sketch, "E3395", {"start": v(-3.77, 0.68) * mm, "end": v(-3.76, 0.72) * mm});
            skLineSegment(sketch, "E3396", {"start": v(-3.76, 0.72) * mm, "end": v(-3.75, 0.76) * mm});
            skLineSegment(sketch, "E3397", {"start": v(-3.75, 0.76) * mm, "end": v(-3.75, 0.8) * mm});
            skLineSegment(sketch, "E3398", {"start": v(-3.75, 0.8) * mm, "end": v(-3.74, 0.84) * mm});
            skLineSegment(sketch, "E3399", {"start": v(-3.74, 0.84) * mm, "end": v(-3.73, 0.88) * mm});
            skLineSegment(sketch, "E3400", {"start": v(-3.73, 0.88) * mm, "end": v(-3.73, 0.92) * mm});
            skLineSegment(sketch, "E3401", {"start": v(-3.73, 0.92) * mm, "end": v(-3.73, 0.97) * mm});
            skLineSegment(sketch, "E3402", {"start": v(-3.73, 0.97) * mm, "end": v(-3.73, 1) * mm});
            skLineSegment(sketch, "E3403", {"start": v(-3.73, 1) * mm, "end": v(-3.73, 1.05) * mm});
            skLineSegment(sketch, "E3404", {"start": v(-3.73, 1.05) * mm, "end": v(-3.73, 1.1) * mm});
            skLineSegment(sketch, "E3405", {"start": v(-3.73, 1.1) * mm, "end": v(-3.73, 1.13) * mm});
            skLineSegment(sketch, "E3406", {"start": v(-3.73, 1.13) * mm, "end": v(-3.73, 1.18) * mm});
            skLineSegment(sketch, "E3407", {"start": v(-3.73, 1.18) * mm, "end": v(-3.74, 1.22) * mm});
            skLineSegment(sketch, "E3408", {"start": v(-3.74, 1.22) * mm, "end": v(-3.75, 1.26) * mm});
            skLineSegment(sketch, "E3409", {"start": v(-3.75, 1.26) * mm, "end": v(-3.75, 1.3) * mm});
            skLineSegment(sketch, "E3410", {"start": v(-3.75, 1.3) * mm, "end": v(-3.76, 1.34) * mm});
            skLineSegment(sketch, "E3411", {"start": v(-3.76, 1.34) * mm, "end": v(-3.77, 1.38) * mm});
            skLineSegment(sketch, "E3412", {"start": v(-3.77, 1.38) * mm, "end": v(-3.78, 1.42) * mm});
            skLineSegment(sketch, "E3413", {"start": v(-3.78, 1.42) * mm, "end": v(-3.8, 1.46) * mm});
            skLineSegment(sketch, "E3414", {"start": v(-3.8, 1.46) * mm, "end": v(-3.8, 1.5) * mm});
            skLineSegment(sketch, "E3415", {"start": v(-3.8, 1.5) * mm, "end": v(-3.82, 1.54) * mm});
            skLineSegment(sketch, "E3416", {"start": v(-3.82, 1.54) * mm, "end": v(-3.84, 1.57) * mm});
            skLineSegment(sketch, "E3417", {"start": v(-3.84, 1.57) * mm, "end": v(-3.85, 1.6) * mm});
            skLineSegment(sketch, "E3418", {"start": v(-3.85, 1.6) * mm, "end": v(-3.87, 1.65) * mm});
            skLineSegment(sketch, "E3419", {"start": v(-3.87, 1.65) * mm, "end": v(-3.89, 1.68) * mm});
            skLineSegment(sketch, "E3420", {"start": v(-3.89, 1.68) * mm, "end": v(-3.9, 1.72) * mm});
            skLineSegment(sketch, "E3421", {"start": v(-3.9, 1.72) * mm, "end": v(-3.93, 1.75) * mm});
            skLineSegment(sketch, "E3422", {"start": v(-3.93, 1.75) * mm, "end": v(-3.95, 1.79) * mm});
            skLineSegment(sketch, "E3423", {"start": v(-3.95, 1.79) * mm, "end": v(-3.97, 1.82) * mm});
            skLineSegment(sketch, "E3424", {"start": v(-3.97, 1.82) * mm, "end": v(-4, 1.85) * mm});
            skLineSegment(sketch, "E3425", {"start": v(-4, 1.85) * mm, "end": v(-4.02, 1.88) * mm});
            skLineSegment(sketch, "E3426", {"start": v(-4.02, 1.88) * mm, "end": v(-4.05, 1.91) * mm});
            skLineSegment(sketch, "E3427", {"start": v(-4.05, 1.91) * mm, "end": v(-4.07, 1.95) * mm});
            skLineSegment(sketch, "E3428", {"start": v(-4.07, 1.95) * mm, "end": v(-4.1, 1.97) * mm});
            skLineSegment(sketch, "E3429", {"start": v(-4.1, 1.97) * mm, "end": v(-4.13, 2) * mm});
            skLineSegment(sketch, "E3430", {"start": v(-4.13, 2) * mm, "end": v(-4.16, 2.03) * mm});
            skLineSegment(sketch, "E3431", {"start": v(-4.16, 2.03) * mm, "end": v(-4.19, 2.06) * mm});
            skLineSegment(sketch, "E3432", {"start": v(-4.19, 2.06) * mm, "end": v(-4.22, 2.08) * mm});
            skLineSegment(sketch, "E3433", {"start": v(-4.22, 2.08) * mm, "end": v(-4.25, 2.1) * mm});
            skLineSegment(sketch, "E3434", {"start": v(-4.25, 2.1) * mm, "end": v(-4.28, 2.13) * mm});
            skLineSegment(sketch, "E3435", {"start": v(-4.28, 2.13) * mm, "end": v(-4.31, 2.16) * mm});
            skLineSegment(sketch, "E3436", {"start": v(-4.31, 2.16) * mm, "end": v(-4.35, 2.18) * mm});
            skLineSegment(sketch, "E3437", {"start": v(-4.35, 2.18) * mm, "end": v(-4.38, 2.2) * mm});
            skLineSegment(sketch, "E3438", {"start": v(-4.38, 2.2) * mm, "end": v(-4.41, 2.22) * mm});
            skLineSegment(sketch, "E3439", {"start": v(-4.41, 2.22) * mm, "end": v(-4.45, 2.24) * mm});
            skLineSegment(sketch, "E3440", {"start": v(-4.45, 2.24) * mm, "end": v(-4.49, 2.25) * mm});
            skLineSegment(sketch, "E3441", {"start": v(-4.49, 2.25) * mm, "end": v(-4.52, 2.27) * mm});
            skLineSegment(sketch, "E3442", {"start": v(-4.52, 2.27) * mm, "end": v(-4.56, 2.29) * mm});
            skLineSegment(sketch, "E3443", {"start": v(-4.56, 2.29) * mm, "end": v(-4.6, 2.3) * mm});
            skLineSegment(sketch, "E3444", {"start": v(-4.6, 2.3) * mm, "end": v(-4.64, 2.31) * mm});
            skLineSegment(sketch, "E3445", {"start": v(-4.64, 2.31) * mm, "end": v(-4.67, 2.32) * mm});
            skLineSegment(sketch, "E3446", {"start": v(-4.67, 2.32) * mm, "end": v(-4.71, 2.33) * mm});
            skLineSegment(sketch, "E3447", {"start": v(-4.71, 2.33) * mm, "end": v(-4.75, 2.34) * mm});
            skLineSegment(sketch, "E3448", {"start": v(-4.75, 2.34) * mm, "end": v(-4.8, 2.35) * mm});
            skLineSegment(sketch, "E3449", {"start": v(-4.8, 2.35) * mm, "end": v(-4.83, 2.36) * mm});
            skLineSegment(sketch, "E3450", {"start": v(-4.83, 2.36) * mm, "end": v(-4.88, 2.36) * mm});
            skLineSegment(sketch, "E3451", {"start": v(-4.88, 2.36) * mm, "end": v(-4.92, 2.37) * mm});
            skLineSegment(sketch, "E3452", {"start": v(-4.92, 2.37) * mm, "end": v(-4.96, 2.37) * mm});
            skLineSegment(sketch, "E3453", {"start": v(-4.96, 2.37) * mm, "end": v(-5, 2.37) * mm});
            skLineSegment(sketch, "E3454", {"start": v(-5, 2.37) * mm, "end": v(-5, 2.37) * mm});
            skLineSegment(sketch, "E3455", {"start": v(-5, 2.37) * mm, "end": v(-5.01, 2.37) * mm});
            skLineSegment(sketch, "E3456", {"start": v(-5.01, 2.37) * mm, "end": v(-5.02, 2.37) * mm});
            skLineSegment(sketch, "E3457", {"start": v(-5.02, 2.37) * mm, "end": v(-5.03, 2.37) * mm});
            skLineSegment(sketch, "E3458", {"start": v(-5.03, 2.37) * mm, "end": v(-5.04, 2.37) * mm});
            skLineSegment(sketch, "E3459", {"start": v(-5.04, 2.37) * mm, "end": v(-5.05, 2.37) * mm});
            skLineSegment(sketch, "E3460", {"start": v(-5.05, 2.37) * mm, "end": v(-5.06, 2.37) * mm});
            skLineSegment(sketch, "E3461", {"start": v(-5.06, 2.37) * mm, "end": v(-5.07, 2.37) * mm});
            skLineSegment(sketch, "E3462", {"start": v(-5.07, 2.37) * mm, "end": v(-5.08, 2.37) * mm});
            skLineSegment(sketch, "E3463", {"start": v(-5.08, 2.37) * mm, "end": v(-5.1, 2.37) * mm});
            skLineSegment(sketch, "E3464", {"start": v(-5.1, 2.37) * mm, "end": v(-5.11, 2.37) * mm});
            skLineSegment(sketch, "E3465", {"start": v(-5.11, 2.37) * mm, "end": v(-5.13, 2.37) * mm});
            skLineSegment(sketch, "E3466", {"start": v(-5.13, 2.37) * mm, "end": v(-5.14, 2.37) * mm});
            skLineSegment(sketch, "E3467", {"start": v(-5.14, 2.37) * mm, "end": v(-5.16, 2.37) * mm});
            skLineSegment(sketch, "E3468", {"start": v(-5.16, 2.37) * mm, "end": v(-5.18, 2.37) * mm});
            skLineSegment(sketch, "E3469", {"start": v(-5.18, 2.37) * mm, "end": v(-5.2, 2.37) * mm});
            skLineSegment(sketch, "E3470", {"start": v(-5.2, 2.37) * mm, "end": v(-5.21, 2.37) * mm});
            skLineSegment(sketch, "E3471", {"start": v(-5.21, 2.37) * mm, "end": v(-5.23, 2.37) * mm});
            skLineSegment(sketch, "E3472", {"start": v(-5.23, 2.37) * mm, "end": v(-5.25, 2.37) * mm});
            skLineSegment(sketch, "E3473", {"start": v(-5.25, 2.37) * mm, "end": v(-5.27, 2.37) * mm});
            skLineSegment(sketch, "E3474", {"start": v(-5.27, 2.37) * mm, "end": v(-5.3, 2.37) * mm});
            skLineSegment(sketch, "E3475", {"start": v(-5.3, 2.37) * mm, "end": v(-5.31, 2.37) * mm});
            skLineSegment(sketch, "E3476", {"start": v(-5.31, 2.37) * mm, "end": v(-5.33, 2.37) * mm});
            skLineSegment(sketch, "E3477", {"start": v(-5.33, 2.37) * mm, "end": v(-5.35, 2.37) * mm});
            skLineSegment(sketch, "E3478", {"start": v(-5.35, 2.37) * mm, "end": v(-5.37, 2.37) * mm});
            skLineSegment(sketch, "E3479", {"start": v(-5.37, 2.37) * mm, "end": v(-5.39, 2.37) * mm});
            skLineSegment(sketch, "E3480", {"start": v(-5.39, 2.37) * mm, "end": v(-5.4, 2.37) * mm});
            skLineSegment(sketch, "E3481", {"start": v(-5.4, 2.37) * mm, "end": v(-5.43, 2.37) * mm});
            skLineSegment(sketch, "E3482", {"start": v(-5.43, 2.37) * mm, "end": v(-5.45, 2.37) * mm});
            skLineSegment(sketch, "E3483", {"start": v(-5.45, 2.37) * mm, "end": v(-5.47, 2.37) * mm});
            skLineSegment(sketch, "E3484", {"start": v(-5.47, 2.37) * mm, "end": v(-5.48, 2.37) * mm});
            skLineSegment(sketch, "E3485", {"start": v(-5.48, 2.37) * mm, "end": v(-5.5, 2.37) * mm});
            skLineSegment(sketch, "E3486", {"start": v(-5.5, 2.37) * mm, "end": v(-5.52, 2.37) * mm});
            skLineSegment(sketch, "E3487", {"start": v(-5.52, 2.37) * mm, "end": v(-5.53, 2.37) * mm});
            skLineSegment(sketch, "E3488", {"start": v(-5.53, 2.37) * mm, "end": v(-5.55, 2.37) * mm});
            skLineSegment(sketch, "E3489", {"start": v(-5.55, 2.37) * mm, "end": v(-5.56, 2.37) * mm});
            skLineSegment(sketch, "E3490", {"start": v(-5.56, 2.37) * mm, "end": v(-5.58, 2.37) * mm});
            skLineSegment(sketch, "E3491", {"start": v(-5.58, 2.37) * mm, "end": v(-5.6, 2.37) * mm});
            skLineSegment(sketch, "E3492", {"start": v(-5.6, 2.37) * mm, "end": v(-5.6, 2.37) * mm});
            skLineSegment(sketch, "E3493", {"start": v(-5.6, 2.37) * mm, "end": v(-5.62, 2.37) * mm});
            skLineSegment(sketch, "E3494", {"start": v(-5.62, 2.37) * mm, "end": v(-5.63, 2.37) * mm});
            skLineSegment(sketch, "E3495", {"start": v(-5.63, 2.37) * mm, "end": v(-5.63, 2.37) * mm});
            skLineSegment(sketch, "E3496", {"start": v(-5.63, 2.37) * mm, "end": v(-5.64, 2.37) * mm});
            skLineSegment(sketch, "E3497", {"start": v(-5.64, 2.37) * mm, "end": v(-5.65, 2.37) * mm});
            skLineSegment(sketch, "E3498", {"start": v(-5.65, 2.37) * mm, "end": v(-5.65, 2.37) * mm});
            skLineSegment(sketch, "E3499", {"start": v(-5.65, 2.37) * mm, "end": v(-5.66, 2.37) * mm});
            skLineSegment(sketch, "E3500", {"start": v(-5.66, 2.37) * mm, "end": v(-5.66, 2.37) * mm});
            skLineSegment(sketch, "E3501", {"start": v(-5.66, 2.37) * mm, "end": v(-5.67, 2.37) * mm});
            skLineSegment(sketch, "E3502", {"start": v(-5.67, 2.37) * mm, "end": v(-5.67, 2.37) * mm});
            skLineSegment(sketch, "E3503", {"start": v(-5.67, 2.37) * mm, "end": v(-5.68, 2.37) * mm});
            skLineSegment(sketch, "E3504", {"start": v(-5.68, 2.37) * mm, "end": v(-5.69, 2.37) * mm});
            skLineSegment(sketch, "E3505", {"start": v(-5.69, 2.37) * mm, "end": v(-5.7, 2.37) * mm});
            skLineSegment(sketch, "E3506", {"start": v(-5.7, 2.37) * mm, "end": v(-5.7, 2.36) * mm});
            skLineSegment(sketch, "E3507", {"start": v(-5.7, 2.36) * mm, "end": v(-5.7, 2.36) * mm});
            skLineSegment(sketch, "E3508", {"start": v(-5.7, 2.36) * mm, "end": v(-5.71, 2.36) * mm});
            skLineSegment(sketch, "E3509", {"start": v(-5.71, 2.36) * mm, "end": v(-5.72, 2.36) * mm});
            skLineSegment(sketch, "E3510", {"start": v(-5.72, 2.36) * mm, "end": v(-5.73, 2.36) * mm});
            skLineSegment(sketch, "E3511", {"start": v(-5.73, 2.36) * mm, "end": v(-5.73, 2.35) * mm});
            skLineSegment(sketch, "E3512", {"start": v(-5.73, 2.35) * mm, "end": v(-5.74, 2.35) * mm});
            skLineSegment(sketch, "E3513", {"start": v(-5.74, 2.35) * mm, "end": v(-5.74, 2.35) * mm});
            skLineSegment(sketch, "E3514", {"start": v(-5.74, 2.35) * mm, "end": v(-5.75, 2.34) * mm});
            skLineSegment(sketch, "E3515", {"start": v(-5.75, 2.34) * mm, "end": v(-5.75, 2.34) * mm});
            skLineSegment(sketch, "E3516", {"start": v(-5.75, 2.34) * mm, "end": v(-5.76, 2.34) * mm});
            skLineSegment(sketch, "E3517", {"start": v(-5.76, 2.34) * mm, "end": v(-5.76, 2.33) * mm});
            skLineSegment(sketch, "E3518", {"start": v(-5.76, 2.33) * mm, "end": v(-5.77, 2.33) * mm});
            skLineSegment(sketch, "E3519", {"start": v(-5.77, 2.33) * mm, "end": v(-5.77, 2.32) * mm});
            skLineSegment(sketch, "E3520", {"start": v(-5.77, 2.32) * mm, "end": v(-5.78, 2.32) * mm});
            skLineSegment(sketch, "E3521", {"start": v(-5.78, 2.32) * mm, "end": v(-5.78, 2.32) * mm});
            skLineSegment(sketch, "E3522", {"start": v(-5.78, 2.32) * mm, "end": v(-5.79, 2.31) * mm});
            skLineSegment(sketch, "E3523", {"start": v(-5.79, 2.31) * mm, "end": v(-5.8, 2.3) * mm});
            skLineSegment(sketch, "E3524", {"start": v(-5.8, 2.3) * mm, "end": v(-5.8, 2.3) * mm});
            skLineSegment(sketch, "E3525", {"start": v(-5.8, 2.3) * mm, "end": v(-5.8, 2.28) * mm});
            skLineSegment(sketch, "E3526", {"start": v(-5.8, 2.28) * mm, "end": v(-5.81, 2.28) * mm});
            skLineSegment(sketch, "E3527", {"start": v(-5.81, 2.28) * mm, "end": v(-5.81, 2.27) * mm});
            skLineSegment(sketch, "E3528", {"start": v(-5.81, 2.27) * mm, "end": v(-5.82, 2.27) * mm});
            skLineSegment(sketch, "E3529", {"start": v(-5.82, 2.27) * mm, "end": v(-5.82, 2.26) * mm});
            skLineSegment(sketch, "E3530", {"start": v(-5.82, 2.26) * mm, "end": v(-5.82, 2.26) * mm});
            skLineSegment(sketch, "E3531", {"start": v(-5.82, 2.26) * mm, "end": v(-5.83, 2.25) * mm});
            skLineSegment(sketch, "E3532", {"start": v(-5.83, 2.25) * mm, "end": v(-5.83, 2.24) * mm});
            skLineSegment(sketch, "E3533", {"start": v(-5.83, 2.24) * mm, "end": v(-5.83, 2.24) * mm});
            skLineSegment(sketch, "E3534", {"start": v(-5.83, 2.24) * mm, "end": v(-5.83, 2.23) * mm});
            skLineSegment(sketch, "E3535", {"start": v(-5.83, 2.23) * mm, "end": v(-5.84, 2.22) * mm});
            skLineSegment(sketch, "E3536", {"start": v(-5.84, 2.22) * mm, "end": v(-5.84, 2.22) * mm});
            skLineSegment(sketch, "E3537", {"start": v(-5.84, 2.22) * mm, "end": v(-5.84, 2.21) * mm});
            skLineSegment(sketch, "E3538", {"start": v(-5.84, 2.21) * mm, "end": v(-5.84, 2.2) * mm});
            skLineSegment(sketch, "E3539", {"start": v(-5.84, 2.2) * mm, "end": v(-5.84, 2.2) * mm});
            skLineSegment(sketch, "E3540", {"start": v(-5.84, 2.2) * mm, "end": v(-5.84, 2.19) * mm});
            skLineSegment(sketch, "E3541", {"start": v(-5.84, 2.19) * mm, "end": v(-5.84, 2.18) * mm});
            skLineSegment(sketch, "E3542", {"start": v(-5.84, 2.18) * mm, "end": v(-5.85, 2.18) * mm});
            skLineSegment(sketch, "E3543", {"start": v(-5.85, 2.18) * mm, "end": v(-5.85, 2.17) * mm});
            skLineSegment(sketch, "E3544", {"start": v(-5.85, 2.17) * mm, "end": v(-5.85, 2.16) * mm});
            skLineSegment(sketch, "E3545", {"start": v(-5.85, 2.16) * mm, "end": v(-5.85, 2.15) * mm});
            skLineSegment(sketch, "E3546", {"start": v(-5.85, 2.15) * mm, "end": v(-5.85, 2.15) * mm});
            skLineSegment(sketch, "E3547", {"start": v(-5.85, 2.15) * mm, "end": v(-5.85, 2.14) * mm});
            skLineSegment(sketch, "E3548", {"start": v(-5.85, 2.14) * mm, "end": v(-5.85, 2.13) * mm});
            skLineSegment(sketch, "E3549", {"start": v(-5.85, 2.13) * mm, "end": v(-5.85, 2.13) * mm});
            skLineSegment(sketch, "E3550", {"start": v(-5.85, 2.13) * mm, "end": v(-5.85, 2.12) * mm});
            skLineSegment(sketch, "E3551", {"start": v(-5.85, 2.12) * mm, "end": v(-5.85, 2.11) * mm});
            skLineSegment(sketch, "E3552", {"start": v(-5.85, 2.11) * mm, "end": v(-5.85, 2.1) * mm});
            skLineSegment(sketch, "E3553", {"start": v(-5.85, 2.1) * mm, "end": v(-5.85, 2.1) * mm});
            skLineSegment(sketch, "E3554", {"start": v(-5.85, 2.1) * mm, "end": v(-5.84, 2.08) * mm});
            skLineSegment(sketch, "E3555", {"start": v(-5.84, 2.08) * mm, "end": v(-5.84, 2.08) * mm});
            skLineSegment(sketch, "E3556", {"start": v(-5.84, 2.08) * mm, "end": v(-5.84, 2.07) * mm});
            skLineSegment(sketch, "E3557", {"start": v(-5.84, 2.07) * mm, "end": v(-5.84, 2.06) * mm});
            skLineSegment(sketch, "E3558", {"start": v(-5.84, 2.06) * mm, "end": v(-5.84, 2.06) * mm});
            skLineSegment(sketch, "E3559", {"start": v(-5.84, 2.06) * mm, "end": v(-5.84, 2.05) * mm});
            skLineSegment(sketch, "E3560", {"start": v(-5.84, 2.05) * mm, "end": v(-5.83, 2.04) * mm});
            skLineSegment(sketch, "E3561", {"start": v(-5.83, 2.04) * mm, "end": v(-5.83, 2.04) * mm});
            skLineSegment(sketch, "E3562", {"start": v(-5.83, 2.04) * mm, "end": v(-5.83, 2.03) * mm});
            skLineSegment(sketch, "E3563", {"start": v(-5.83, 2.03) * mm, "end": v(-5.83, 2.02) * mm});
            skLineSegment(sketch, "E3564", {"start": v(-5.83, 2.02) * mm, "end": v(-5.82, 2.02) * mm});
            skLineSegment(sketch, "E3565", {"start": v(-5.82, 2.02) * mm, "end": v(-5.82, 2.01) * mm});
            skLineSegment(sketch, "E3566", {"start": v(-5.82, 2.01) * mm, "end": v(-5.82, 2) * mm});
            skLineSegment(sketch, "E3567", {"start": v(-5.82, 2) * mm, "end": v(-5.82, 2) * mm});
            skLineSegment(sketch, "E3568", {"start": v(-5.82, 2) * mm, "end": v(-5.81, 2) * mm});
            skLineSegment(sketch, "E3569", {"start": v(-5.81, 2) * mm, "end": v(-5.8, 1.99) * mm});
            skLineSegment(sketch, "E3570", {"start": v(-5.8, 1.99) * mm, "end": v(-5.8, 1.98) * mm});
            skLineSegment(sketch, "E3571", {"start": v(-5.8, 1.98) * mm, "end": v(-5.8, 1.98) * mm});
            skLineSegment(sketch, "E3572", {"start": v(-5.8, 1.98) * mm, "end": v(-5.8, 1.97) * mm});
            skLineSegment(sketch, "E3573", {"start": v(-5.8, 1.97) * mm, "end": v(-5.8, 1.97) * mm});
            skLineSegment(sketch, "E3574", {"start": v(-5.8, 1.97) * mm, "end": v(-5.79, 1.96) * mm});
            skLineSegment(sketch, "E3575", {"start": v(-5.79, 1.96) * mm, "end": v(-5.78, 1.96) * mm});
            skLineSegment(sketch, "E3576", {"start": v(-5.78, 1.96) * mm, "end": v(-5.78, 1.95) * mm});
            skLineSegment(sketch, "E3577", {"start": v(-5.78, 1.95) * mm, "end": v(-5.77, 1.95) * mm});
            skLineSegment(sketch, "E3578", {"start": v(-5.77, 1.95) * mm, "end": v(-5.77, 1.94) * mm});
            skLineSegment(sketch, "E3579", {"start": v(-5.77, 1.94) * mm, "end": v(-5.76, 1.94) * mm});
            skLineSegment(sketch, "E3580", {"start": v(-5.76, 1.94) * mm, "end": v(-5.76, 1.93) * mm});
            skLineSegment(sketch, "E3581", {"start": v(-5.76, 1.93) * mm, "end": v(-5.75, 1.93) * mm});
            skLineSegment(sketch, "E3582", {"start": v(-5.75, 1.93) * mm, "end": v(-5.75, 1.93) * mm});
            skLineSegment(sketch, "E3583", {"start": v(-5.75, 1.93) * mm, "end": v(-5.74, 1.92) * mm});
            skLineSegment(sketch, "E3584", {"start": v(-5.74, 1.92) * mm, "end": v(-5.73, 1.92) * mm});
            skLineSegment(sketch, "E3585", {"start": v(-5.73, 1.92) * mm, "end": v(-5.73, 1.92) * mm});
            skLineSegment(sketch, "E3586", {"start": v(-5.73, 1.92) * mm, "end": v(-5.72, 1.91) * mm});
            skLineSegment(sketch, "E3587", {"start": v(-5.72, 1.91) * mm, "end": v(-5.71, 1.91) * mm});
            skLineSegment(sketch, "E3588", {"start": v(-5.71, 1.91) * mm, "end": v(-5.7, 1.9) * mm});
            skLineSegment(sketch, "E3589", {"start": v(-5.7, 1.9) * mm, "end": v(-5.7, 1.9) * mm});
            skLineSegment(sketch, "E3590", {"start": v(-5.7, 1.9) * mm, "end": v(-5.68, 1.9) * mm});
            skLineSegment(sketch, "E3591", {"start": v(-5.68, 1.9) * mm, "end": v(-5.68, 1.9) * mm});
            skLineSegment(sketch, "E3592", {"start": v(-5.68, 1.9) * mm, "end": v(-5.67, 1.9) * mm});
            skLineSegment(sketch, "E3593", {"start": v(-5.67, 1.9) * mm, "end": v(-5.66, 1.9) * mm});
            skLineSegment(sketch, "E3594", {"start": v(-5.66, 1.9) * mm, "end": v(-5.65, 1.9) * mm});
            skLineSegment(sketch, "E3595", {"start": v(-5.65, 1.9) * mm, "end": v(-5.65, 1.9) * mm});
            skLineSegment(sketch, "E3596", {"start": v(-5.65, 1.9) * mm, "end": v(-5.64, 1.9) * mm});
            skLineSegment(sketch, "E3597", {"start": v(-5.64, 1.9) * mm, "end": v(-5.64, 1.9) * mm});
            skLineSegment(sketch, "E3598", {"start": v(-5.64, 1.9) * mm, "end": v(-5.63, 1.9) * mm});
            skLineSegment(sketch, "E3599", {"start": v(-5.63, 1.9) * mm, "end": v(-5.63, 1.9) * mm});
            skLineSegment(sketch, "E3600", {"start": v(-5.63, 1.9) * mm, "end": v(-5.62, 1.9) * mm});
            skLineSegment(sketch, "E3601", {"start": v(-5.62, 1.9) * mm, "end": v(-5.61, 1.9) * mm});
            skLineSegment(sketch, "E3602", {"start": v(-5.61, 1.9) * mm, "end": v(-5.6, 1.9) * mm});
            skLineSegment(sketch, "E3603", {"start": v(-5.6, 1.9) * mm, "end": v(-5.6, 1.9) * mm});
            skLineSegment(sketch, "E3604", {"start": v(-5.6, 1.9) * mm, "end": v(-5.58, 1.9) * mm});
            skLineSegment(sketch, "E3605", {"start": v(-5.58, 1.9) * mm, "end": v(-5.57, 1.9) * mm});
            skLineSegment(sketch, "E3606", {"start": v(-5.57, 1.9) * mm, "end": v(-5.56, 1.9) * mm});
            skLineSegment(sketch, "E3607", {"start": v(-5.56, 1.9) * mm, "end": v(-5.55, 1.9) * mm});
            skLineSegment(sketch, "E3608", {"start": v(-5.55, 1.9) * mm, "end": v(-5.53, 1.9) * mm});
            skLineSegment(sketch, "E3609", {"start": v(-5.53, 1.9) * mm, "end": v(-5.52, 1.9) * mm});
            skLineSegment(sketch, "E3610", {"start": v(-5.52, 1.9) * mm, "end": v(-5.5, 1.9) * mm});
            skLineSegment(sketch, "E3611", {"start": v(-5.5, 1.9) * mm, "end": v(-5.49, 1.9) * mm});
            skLineSegment(sketch, "E3612", {"start": v(-5.49, 1.9) * mm, "end": v(-5.47, 1.9) * mm});
            skLineSegment(sketch, "E3613", {"start": v(-5.47, 1.9) * mm, "end": v(-5.46, 1.9) * mm});
            skLineSegment(sketch, "E3614", {"start": v(-5.46, 1.9) * mm, "end": v(-5.44, 1.9) * mm});
            skLineSegment(sketch, "E3615", {"start": v(-5.44, 1.9) * mm, "end": v(-5.42, 1.9) * mm});
            skLineSegment(sketch, "E3616", {"start": v(-5.42, 1.9) * mm, "end": v(-5.4, 1.9) * mm});
            skLineSegment(sketch, "E3617", {"start": v(-5.4, 1.9) * mm, "end": v(-5.39, 1.9) * mm});
            skLineSegment(sketch, "E3618", {"start": v(-5.39, 1.9) * mm, "end": v(-5.37, 1.9) * mm});
            skLineSegment(sketch, "E3619", {"start": v(-5.37, 1.9) * mm, "end": v(-5.35, 1.9) * mm});
            skLineSegment(sketch, "E3620", {"start": v(-5.35, 1.9) * mm, "end": v(-5.33, 1.9) * mm});
            skLineSegment(sketch, "E3621", {"start": v(-5.33, 1.9) * mm, "end": v(-5.31, 1.9) * mm});
            skLineSegment(sketch, "E3622", {"start": v(-5.31, 1.9) * mm, "end": v(-5.3, 1.9) * mm});
            skLineSegment(sketch, "E3623", {"start": v(-5.3, 1.9) * mm, "end": v(-5.28, 1.9) * mm});
            skLineSegment(sketch, "E3624", {"start": v(-5.28, 1.9) * mm, "end": v(-5.26, 1.9) * mm});
            skLineSegment(sketch, "E3625", {"start": v(-5.26, 1.9) * mm, "end": v(-5.24, 1.9) * mm});
            skLineSegment(sketch, "E3626", {"start": v(-5.24, 1.9) * mm, "end": v(-5.22, 1.9) * mm});
            skLineSegment(sketch, "E3627", {"start": v(-5.22, 1.9) * mm, "end": v(-5.2, 1.9) * mm});
            skLineSegment(sketch, "E3628", {"start": v(-5.2, 1.9) * mm, "end": v(-5.19, 1.9) * mm});
            skLineSegment(sketch, "E3629", {"start": v(-5.19, 1.9) * mm, "end": v(-5.17, 1.9) * mm});
            skLineSegment(sketch, "E3630", {"start": v(-5.17, 1.9) * mm, "end": v(-5.16, 1.9) * mm});
            skLineSegment(sketch, "E3631", {"start": v(-5.16, 1.9) * mm, "end": v(-5.14, 1.9) * mm});
            skLineSegment(sketch, "E3632", {"start": v(-5.14, 1.9) * mm, "end": v(-5.13, 1.9) * mm});
            skLineSegment(sketch, "E3633", {"start": v(-5.13, 1.9) * mm, "end": v(-5.11, 1.9) * mm});
            skLineSegment(sketch, "E3634", {"start": v(-5.11, 1.9) * mm, "end": v(-5.1, 1.9) * mm});
            skLineSegment(sketch, "E3635", {"start": v(-5.1, 1.9) * mm, "end": v(-5.09, 1.9) * mm});
            skLineSegment(sketch, "E3636", {"start": v(-5.09, 1.9) * mm, "end": v(-5.08, 1.9) * mm});
            skLineSegment(sketch, "E3637", {"start": v(-5.08, 1.9) * mm, "end": v(-5.07, 1.9) * mm});
            skLineSegment(sketch, "E3638", {"start": v(-5.07, 1.9) * mm, "end": v(-5.06, 1.9) * mm});
            skLineSegment(sketch, "E3639", {"start": v(-5.06, 1.9) * mm, "end": v(-5.05, 1.9) * mm});
            skLineSegment(sketch, "E3640", {"start": v(-5.05, 1.9) * mm, "end": v(-5.04, 1.9) * mm});
            skLineSegment(sketch, "E3641", {"start": v(-5.04, 1.9) * mm, "end": v(-5.04, 1.9) * mm});
            skLineSegment(sketch, "E3642", {"start": v(-5.04, 1.9) * mm, "end": v(-5.03, 1.9) * mm});
            skLineSegment(sketch, "E3643", {"start": v(-5.03, 1.9) * mm, "end": v(-5.03, 1.9) * mm});
            skLineSegment(sketch, "E3644", {"start": v(-5.03, 1.9) * mm, "end": v(-5.02, 1.9) * mm});
            skLineSegment(sketch, "E3645", {"start": v(-5.02, 1.9) * mm, "end": v(-5, 1.9) * mm});
            skLineSegment(sketch, "E3646", {"start": v(-5, 1.9) * mm, "end": v(-4.97, 1.9) * mm});
            skLineSegment(sketch, "E3647", {"start": v(-4.97, 1.9) * mm, "end": v(-4.94, 1.9) * mm});
            skLineSegment(sketch, "E3648", {"start": v(-4.94, 1.9) * mm, "end": v(-4.92, 1.9) * mm});
            skLineSegment(sketch, "E3649", {"start": v(-4.92, 1.9) * mm, "end": v(-4.9, 1.89) * mm});
            skLineSegment(sketch, "E3650", {"start": v(-4.9, 1.89) * mm, "end": v(-4.87, 1.88) * mm});
            skLineSegment(sketch, "E3651", {"start": v(-4.87, 1.88) * mm, "end": v(-4.84, 1.88) * mm});
            skLineSegment(sketch, "E3652", {"start": v(-4.84, 1.88) * mm, "end": v(-4.81, 1.87) * mm});
            skLineSegment(sketch, "E3653", {"start": v(-4.81, 1.87) * mm, "end": v(-4.79, 1.86) * mm});
            skLineSegment(sketch, "E3654", {"start": v(-4.79, 1.86) * mm, "end": v(-4.76, 1.86) * mm});
            skLineSegment(sketch, "E3655", {"start": v(-4.76, 1.86) * mm, "end": v(-4.74, 1.85) * mm});
            skLineSegment(sketch, "E3656", {"start": v(-4.74, 1.85) * mm, "end": v(-4.72, 1.84) * mm});
            skLineSegment(sketch, "E3657", {"start": v(-4.72, 1.84) * mm, "end": v(-4.7, 1.83) * mm});
            skLineSegment(sketch, "E3658", {"start": v(-4.7, 1.83) * mm, "end": v(-4.67, 1.82) * mm});
            skLineSegment(sketch, "E3659", {"start": v(-4.67, 1.82) * mm, "end": v(-4.64, 1.8) * mm});
            skLineSegment(sketch, "E3660", {"start": v(-4.64, 1.8) * mm, "end": v(-4.62, 1.8) * mm});
            skLineSegment(sketch, "E3661", {"start": v(-4.62, 1.8) * mm, "end": v(-4.6, 1.78) * mm});
            skLineSegment(sketch, "E3662", {"start": v(-4.6, 1.78) * mm, "end": v(-4.58, 1.76) * mm});
            skLineSegment(sketch, "E3663", {"start": v(-4.58, 1.76) * mm, "end": v(-4.55, 1.75) * mm});
            skLineSegment(sketch, "E3664", {"start": v(-4.55, 1.75) * mm, "end": v(-4.53, 1.74) * mm});
            skLineSegment(sketch, "E3665", {"start": v(-4.53, 1.74) * mm, "end": v(-4.51, 1.72) * mm});
            skLineSegment(sketch, "E3666", {"start": v(-4.51, 1.72) * mm, "end": v(-4.5, 1.7) * mm});
            skLineSegment(sketch, "E3667", {"start": v(-4.5, 1.7) * mm, "end": v(-4.47, 1.69) * mm});
            skLineSegment(sketch, "E3668", {"start": v(-4.47, 1.69) * mm, "end": v(-4.45, 1.67) * mm});
            skLineSegment(sketch, "E3669", {"start": v(-4.45, 1.67) * mm, "end": v(-4.43, 1.65) * mm});
            skLineSegment(sketch, "E3670", {"start": v(-4.43, 1.65) * mm, "end": v(-4.41, 1.63) * mm});
            skLineSegment(sketch, "E3671", {"start": v(-4.41, 1.63) * mm, "end": v(-4.4, 1.61) * mm});
            skLineSegment(sketch, "E3672", {"start": v(-4.4, 1.61) * mm, "end": v(-4.38, 1.6) * mm});
            skLineSegment(sketch, "E3673", {"start": v(-4.38, 1.6) * mm, "end": v(-4.36, 1.57) * mm});
            skLineSegment(sketch, "E3674", {"start": v(-4.36, 1.57) * mm, "end": v(-4.35, 1.55) * mm});
            skLineSegment(sketch, "E3675", {"start": v(-4.35, 1.55) * mm, "end": v(-4.33, 1.53) * mm});
            skLineSegment(sketch, "E3676", {"start": v(-4.33, 1.53) * mm, "end": v(-4.32, 1.5) * mm});
            skLineSegment(sketch, "E3677", {"start": v(-4.32, 1.5) * mm, "end": v(-4.3, 1.49) * mm});
            skLineSegment(sketch, "E3678", {"start": v(-4.3, 1.49) * mm, "end": v(-4.29, 1.46) * mm});
            skLineSegment(sketch, "E3679", {"start": v(-4.29, 1.46) * mm, "end": v(-4.27, 1.44) * mm});
            skLineSegment(sketch, "E3680", {"start": v(-4.27, 1.44) * mm, "end": v(-4.26, 1.42) * mm});
            skLineSegment(sketch, "E3681", {"start": v(-4.26, 1.42) * mm, "end": v(-4.25, 1.4) * mm});
            skLineSegment(sketch, "E3682", {"start": v(-4.25, 1.4) * mm, "end": v(-4.24, 1.37) * mm});
            skLineSegment(sketch, "E3683", {"start": v(-4.24, 1.37) * mm, "end": v(-4.23, 1.34) * mm});
            skLineSegment(sketch, "E3684", {"start": v(-4.23, 1.34) * mm, "end": v(-4.22, 1.32) * mm});
            skLineSegment(sketch, "E3685", {"start": v(-4.22, 1.32) * mm, "end": v(-4.21, 1.3) * mm});
            skLineSegment(sketch, "E3686", {"start": v(-4.21, 1.3) * mm, "end": v(-4.2, 1.27) * mm});
            skLineSegment(sketch, "E3687", {"start": v(-4.2, 1.27) * mm, "end": v(-4.2, 1.24) * mm});
            skLineSegment(sketch, "E3688", {"start": v(-4.2, 1.24) * mm, "end": v(-4.2, 1.21) * mm});
            skLineSegment(sketch, "E3689", {"start": v(-4.2, 1.21) * mm, "end": v(-4.19, 1.19) * mm});
            skLineSegment(sketch, "E3690", {"start": v(-4.19, 1.19) * mm, "end": v(-4.18, 1.16) * mm});
            skLineSegment(sketch, "E3691", {"start": v(-4.18, 1.16) * mm, "end": v(-4.18, 1.13) * mm});
            skLineSegment(sketch, "E3692", {"start": v(-4.18, 1.13) * mm, "end": v(-4.18, 1.1) * mm});
            skLineSegment(sketch, "E3693", {"start": v(-4.18, 1.1) * mm, "end": v(-4.18, 1.08) * mm});
            skLineSegment(sketch, "E3694", {"start": v(-4.18, 1.08) * mm, "end": v(-4.18, 1.05) * mm});
            skLineSegment(sketch, "E3695", {"start": v(-4.18, 1.05) * mm, "end": v(-4.18, 1.02) * mm});
            skLineSegment(sketch, "E3696", {"start": v(-4.18, 1.02) * mm, "end": v(-4.18, 1) * mm});
            skLineSegment(sketch, "E3697", {"start": v(-4.18, 1) * mm, "end": v(-4.18, 0.97) * mm});
            skLineSegment(sketch, "E3698", {"start": v(-4.18, 0.97) * mm, "end": v(-4.18, 0.94) * mm});
            skLineSegment(sketch, "E3699", {"start": v(-4.18, 0.94) * mm, "end": v(-4.19, 0.92) * mm});
            skLineSegment(sketch, "E3700", {"start": v(-4.19, 0.92) * mm, "end": v(-4.2, 0.9) * mm});
            skLineSegment(sketch, "E3701", {"start": v(-4.2, 0.9) * mm, "end": v(-4.2, 0.87) * mm});
            skLineSegment(sketch, "E3702", {"start": v(-4.2, 0.87) * mm, "end": v(-4.2, 0.84) * mm});
            skLineSegment(sketch, "E3703", {"start": v(-4.2, 0.84) * mm, "end": v(-4.22, 0.82) * mm});
            skLineSegment(sketch, "E3704", {"start": v(-4.22, 0.82) * mm, "end": v(-4.23, 0.8) * mm});
            skLineSegment(sketch, "E3705", {"start": v(-4.23, 0.8) * mm, "end": v(-4.24, 0.77) * mm});
            skLineSegment(sketch, "E3706", {"start": v(-4.24, 0.77) * mm, "end": v(-4.25, 0.74) * mm});
            skLineSegment(sketch, "E3707", {"start": v(-4.25, 0.74) * mm, "end": v(-4.26, 0.72) * mm});
            skLineSegment(sketch, "E3708", {"start": v(-4.26, 0.72) * mm, "end": v(-4.27, 0.7) * mm});
            skLineSegment(sketch, "E3709", {"start": v(-4.27, 0.7) * mm, "end": v(-4.28, 0.67) * mm});
            skLineSegment(sketch, "E3710", {"start": v(-4.28, 0.67) * mm, "end": v(-4.3, 0.65) * mm});
            skLineSegment(sketch, "E3711", {"start": v(-4.3, 0.65) * mm, "end": v(-4.31, 0.63) * mm});
            skLineSegment(sketch, "E3712", {"start": v(-4.31, 0.63) * mm, "end": v(-4.33, 0.6) * mm});
            skLineSegment(sketch, "E3713", {"start": v(-4.33, 0.6) * mm, "end": v(-4.34, 0.59) * mm});
            skLineSegment(sketch, "E3714", {"start": v(-4.34, 0.59) * mm, "end": v(-4.36, 0.57) * mm});
            skLineSegment(sketch, "E3715", {"start": v(-4.36, 0.57) * mm, "end": v(-4.38, 0.55) * mm});
            skLineSegment(sketch, "E3716", {"start": v(-4.38, 0.55) * mm, "end": v(-4.4, 0.53) * mm});
            skLineSegment(sketch, "E3717", {"start": v(-4.4, 0.53) * mm, "end": v(-4.41, 0.5) * mm});
            skLineSegment(sketch, "E3718", {"start": v(-4.41, 0.5) * mm, "end": v(-4.43, 0.49) * mm});
            skLineSegment(sketch, "E3719", {"start": v(-4.43, 0.49) * mm, "end": v(-4.45, 0.47) * mm});
            skLineSegment(sketch, "E3720", {"start": v(-4.45, 0.47) * mm, "end": v(-4.47, 0.45) * mm});
            skLineSegment(sketch, "E3721", {"start": v(-4.47, 0.45) * mm, "end": v(-4.5, 0.43) * mm});
            skLineSegment(sketch, "E3722", {"start": v(-4.5, 0.43) * mm, "end": v(-4.51, 0.42) * mm});
            skLineSegment(sketch, "E3723", {"start": v(-4.51, 0.42) * mm, "end": v(-4.54, 0.4) * mm});
            skLineSegment(sketch, "E3724", {"start": v(-4.54, 0.4) * mm, "end": v(-4.56, 0.39) * mm});
            skLineSegment(sketch, "E3725", {"start": v(-4.56, 0.39) * mm, "end": v(-4.58, 0.37) * mm});
            skLineSegment(sketch, "E3726", {"start": v(-4.58, 0.37) * mm, "end": v(-4.6, 0.36) * mm});
            skLineSegment(sketch, "E3727", {"start": v(-4.6, 0.36) * mm, "end": v(-4.63, 0.34) * mm});
            skLineSegment(sketch, "E3728", {"start": v(-4.63, 0.34) * mm, "end": v(-4.65, 0.33) * mm});
            skLineSegment(sketch, "E3729", {"start": v(-4.65, 0.33) * mm, "end": v(-4.67, 0.32) * mm});
            skLineSegment(sketch, "E3730", {"start": v(-4.67, 0.32) * mm, "end": v(-4.7, 0.3) * mm});
            skLineSegment(sketch, "E3731", {"start": v(-4.7, 0.3) * mm, "end": v(-4.72, 0.3) * mm});
            skLineSegment(sketch, "E3732", {"start": v(-4.72, 0.3) * mm, "end": v(-4.75, 0.29) * mm});
            skLineSegment(sketch, "E3733", {"start": v(-4.75, 0.29) * mm, "end": v(-4.77, 0.28) * mm});
            skLineSegment(sketch, "E3734", {"start": v(-4.77, 0.28) * mm, "end": v(-4.8, 0.27) * mm});
            skLineSegment(sketch, "E3735", {"start": v(-4.8, 0.27) * mm, "end": v(-4.82, 0.26) * mm});
            skLineSegment(sketch, "E3736", {"start": v(-4.82, 0.26) * mm, "end": v(-4.84, 0.25) * mm});
            skLineSegment(sketch, "E3737", {"start": v(-4.84, 0.25) * mm, "end": v(-4.87, 0.25) * mm});
            skLineSegment(sketch, "E3738", {"start": v(-4.87, 0.25) * mm, "end": v(-4.9, 0.24) * mm});
            skLineSegment(sketch, "E3739", {"start": v(-4.9, 0.24) * mm, "end": v(-4.92, 0.24) * mm});
            skLineSegment(sketch, "E3740", {"start": v(-4.92, 0.24) * mm, "end": v(-4.95, 0.23) * mm});
            skLineSegment(sketch, "E3741", {"start": v(-4.95, 0.23) * mm, "end": v(-4.97, 0.23) * mm});
            skLineSegment(sketch, "E3742", {"start": v(-4.97, 0.23) * mm, "end": v(-5, 0.23) * mm});
            skLineSegment(sketch, "E3743", {"start": v(-5, 0.23) * mm, "end": v(-5.02, 0.23) * mm});
            skLineSegment(sketch, "E3744", {"start": v(-5.02, 0.23) * mm, "end": v(-5.05, 0.23) * mm});
            skLineSegment(sketch, "E3745", {"start": v(-5.05, 0.23) * mm, "end": v(-5.08, 0.22) * mm});
            skLineSegment(sketch, "E3746", {"start": v(-5.08, 0.22) * mm, "end": v(-5.12, 0.22) * mm});
            skLineSegment(sketch, "E3747", {"start": v(-5.12, 0.22) * mm, "end": v(-5.15, 0.22) * mm});
            skLineSegment(sketch, "E3748", {"start": v(-5.15, 0.22) * mm, "end": v(-5.18, 0.22) * mm});
            skLineSegment(sketch, "E3749", {"start": v(-5.18, 0.22) * mm, "end": v(-5.22, 0.22) * mm});
            skLineSegment(sketch, "E3750", {"start": v(-5.22, 0.22) * mm, "end": v(-5.25, 0.21) * mm});
            skLineSegment(sketch, "E3751", {"start": v(-5.25, 0.21) * mm, "end": v(-5.28, 0.2) * mm});
            skLineSegment(sketch, "E3752", {"start": v(-5.28, 0.2) * mm, "end": v(-5.3, 0.2) * mm});
            skLineSegment(sketch, "E3753", {"start": v(-5.3, 0.2) * mm, "end": v(-5.34, 0.2) * mm});
            skLineSegment(sketch, "E3754", {"start": v(-5.34, 0.2) * mm, "end": v(-5.37, 0.2) * mm});
            skLineSegment(sketch, "E3755", {"start": v(-5.37, 0.2) * mm, "end": v(-5.4, 0.19) * mm});
            skLineSegment(sketch, "E3756", {"start": v(-5.4, 0.19) * mm, "end": v(-5.42, 0.18) * mm});
            skLineSegment(sketch, "E3757", {"start": v(-5.42, 0.18) * mm, "end": v(-5.45, 0.17) * mm});
            skLineSegment(sketch, "E3758", {"start": v(-5.45, 0.17) * mm, "end": v(-5.47, 0.16) * mm});
            skLineSegment(sketch, "E3759", {"start": v(-5.47, 0.16) * mm, "end": v(-5.5, 0.16) * mm});
            skLineSegment(sketch, "E3760", {"start": v(-5.5, 0.16) * mm, "end": v(-5.52, 0.15) * mm});
            skLineSegment(sketch, "E3761", {"start": v(-5.52, 0.15) * mm, "end": v(-5.54, 0.14) * mm});
            skLineSegment(sketch, "E3762", {"start": v(-5.54, 0.14) * mm, "end": v(-5.57, 0.13) * mm});
            skLineSegment(sketch, "E3763", {"start": v(-5.57, 0.13) * mm, "end": v(-5.59, 0.12) * mm});
            skLineSegment(sketch, "E3764", {"start": v(-5.59, 0.12) * mm, "end": v(-5.61, 0.1) * mm});
            skLineSegment(sketch, "E3765", {"start": v(-5.61, 0.1) * mm, "end": v(-5.63, 0.1) * mm});
            skLineSegment(sketch, "E3766", {"start": v(-5.63, 0.1) * mm, "end": v(-5.65, 0.08) * mm});
            skLineSegment(sketch, "E3767", {"start": v(-5.65, 0.08) * mm, "end": v(-5.67, 0.07) * mm});
            skLineSegment(sketch, "E3768", {"start": v(-5.67, 0.07) * mm, "end": v(-5.69, 0.06) * mm});
            skLineSegment(sketch, "E3769", {"start": v(-5.69, 0.06) * mm, "end": v(-5.7, 0.04) * mm});
            skLineSegment(sketch, "E3770", {"start": v(-5.7, 0.04) * mm, "end": v(-5.73, 0.03) * mm});
            skLineSegment(sketch, "E3771", {"start": v(-5.73, 0.03) * mm, "end": v(-5.74, 0.01) * mm});
            skLineSegment(sketch, "E3772", {"start": v(-5.74, 0.01) * mm, "end": v(-5.76, 0) * mm});
            skLineSegment(sketch, "E3773", {"start": v(-5.76, 0) * mm, "end": v(-5.77, -0.01) * mm});
            skLineSegment(sketch, "E3774", {"start": v(-5.77, -0.01) * mm, "end": v(-5.79, -0.03) * mm});
            skLineSegment(sketch, "E3775", {"start": v(-5.79, -0.03) * mm, "end": v(-5.8, -0.04) * mm});
            skLineSegment(sketch, "E3776", {"start": v(-5.8, -0.04) * mm, "end": v(-5.81, -0.06) * mm});
            skLineSegment(sketch, "E3777", {"start": v(-5.81, -0.06) * mm, "end": v(-5.83, -0.08) * mm});
            skLineSegment(sketch, "E3778", {"start": v(-5.83, -0.08) * mm, "end": v(-5.84, -0.1) * mm});
            skLineSegment(sketch, "E3779", {"start": v(-5.84, -0.1) * mm, "end": v(-5.85, -0.1) * mm});
            skLineSegment(sketch, "E3780", {"start": v(-5.85, -0.1) * mm, "end": v(-5.86, -0.13) * mm});
            skLineSegment(sketch, "E3781", {"start": v(-5.86, -0.13) * mm, "end": v(-5.87, -0.14) * mm});
            skLineSegment(sketch, "E3782", {"start": v(-5.87, -0.14) * mm, "end": v(-5.88, -0.16) * mm});
            skLineSegment(sketch, "E3783", {"start": v(-5.88, -0.16) * mm, "end": v(-5.89, -0.18) * mm});
            skLineSegment(sketch, "E3784", {"start": v(-5.89, -0.18) * mm, "end": v(-5.9, -0.2) * mm});
            skLineSegment(sketch, "E3785", {"start": v(-5.9, -0.2) * mm, "end": v(-5.9, -0.22) * mm});
            skLineSegment(sketch, "E3786", {"start": v(-5.9, -0.22) * mm, "end": v(-5.91, -0.23) * mm});
            skLineSegment(sketch, "E3787", {"start": v(-5.91, -0.23) * mm, "end": v(-5.92, -0.25) * mm});
            skLineSegment(sketch, "E3788", {"start": v(-5.92, -0.25) * mm, "end": v(-5.92, -0.27) * mm});
            skLineSegment(sketch, "E3789", {"start": v(-5.92, -0.27) * mm, "end": v(-5.93, -0.3) * mm});
            skLineSegment(sketch, "E3790", {"start": v(-5.93, -0.3) * mm, "end": v(-5.93, -0.3) * mm});
            skLineSegment(sketch, "E3791", {"start": v(-5.93, -0.3) * mm, "end": v(-5.94, -0.33) * mm});
            skLineSegment(sketch, "E3792", {"start": v(-5.94, -0.33) * mm, "end": v(-5.94, -0.35) * mm});
            skLineSegment(sketch, "E3793", {"start": v(-5.94, -0.35) * mm, "end": v(-5.94, -0.37) * mm});
            skLineSegment(sketch, "E3794", {"start": v(-5.94, -0.37) * mm, "end": v(-5.94, -0.39) * mm});
            skLineSegment(sketch, "E3795", {"start": v(-5.94, -0.39) * mm, "end": v(-5.94, -0.4) * mm});
            skLineSegment(sketch, "E3796", {"start": v(-5.94, -0.4) * mm, "end": v(-5.94, -0.42) * mm});
            skLineSegment(sketch, "E3797", {"start": v(-5.94, -0.42) * mm, "end": v(-5.94, -0.44) * mm});
            skLineSegment(sketch, "E3798", {"start": v(-5.94, -0.44) * mm, "end": v(-5.93, -0.46) * mm});
            skLineSegment(sketch, "E3799", {"start": v(-5.93, -0.46) * mm, "end": v(-5.93, -0.48) * mm});
            skLineSegment(sketch, "E3800", {"start": v(-5.93, -0.48) * mm, "end": v(-5.92, -0.5) * mm});
            skLineSegment(sketch, "E3801", {"start": v(-5.92, -0.5) * mm, "end": v(-5.92, -0.52) * mm});
            skLineSegment(sketch, "E3802", {"start": v(-5.92, -0.52) * mm, "end": v(-5.91, -0.53) * mm});
            skLineSegment(sketch, "E3803", {"start": v(-5.91, -0.53) * mm, "end": v(-5.9, -0.55) * mm});
            skLineSegment(sketch, "E3804", {"start": v(-5.9, -0.55) * mm, "end": v(-5.9, -0.57) * mm});
            skLineSegment(sketch, "E3805", {"start": v(-5.9, -0.57) * mm, "end": v(-5.89, -0.59) * mm});
            skLineSegment(sketch, "E3806", {"start": v(-5.89, -0.59) * mm, "end": v(-5.88, -0.6) * mm});
            skLineSegment(sketch, "E3807", {"start": v(-5.88, -0.6) * mm, "end": v(-5.87, -0.62) * mm});
            skLineSegment(sketch, "E3808", {"start": v(-5.87, -0.62) * mm, "end": v(-5.86, -0.64) * mm});
            skLineSegment(sketch, "E3809", {"start": v(-5.86, -0.64) * mm, "end": v(-5.85, -0.66) * mm});
            skLineSegment(sketch, "E3810", {"start": v(-5.85, -0.66) * mm, "end": v(-5.84, -0.68) * mm});
            skLineSegment(sketch, "E3811", {"start": v(-5.84, -0.68) * mm, "end": v(-5.83, -0.7) * mm});
            skLineSegment(sketch, "E3812", {"start": v(-5.83, -0.7) * mm, "end": v(-5.81, -0.71) * mm});
            skLineSegment(sketch, "E3813", {"start": v(-5.81, -0.71) * mm, "end": v(-5.8, -0.73) * mm});
            skLineSegment(sketch, "E3814", {"start": v(-5.8, -0.73) * mm, "end": v(-5.79, -0.74) * mm});
            skLineSegment(sketch, "E3815", {"start": v(-5.79, -0.74) * mm, "end": v(-5.77, -0.76) * mm});
            skLineSegment(sketch, "E3816", {"start": v(-5.77, -0.76) * mm, "end": v(-5.76, -0.78) * mm});
            skLineSegment(sketch, "E3817", {"start": v(-5.76, -0.78) * mm, "end": v(-5.74, -0.8) * mm});
            skLineSegment(sketch, "E3818", {"start": v(-5.74, -0.8) * mm, "end": v(-5.73, -0.8) * mm});
            skLineSegment(sketch, "E3819", {"start": v(-5.73, -0.8) * mm, "end": v(-5.7, -0.82) * mm});
            skLineSegment(sketch, "E3820", {"start": v(-5.7, -0.82) * mm, "end": v(-5.69, -0.83) * mm});
            skLineSegment(sketch, "E3821", {"start": v(-5.69, -0.83) * mm, "end": v(-5.67, -0.85) * mm});
            skLineSegment(sketch, "E3822", {"start": v(-5.67, -0.85) * mm, "end": v(-5.65, -0.86) * mm});
            skLineSegment(sketch, "E3823", {"start": v(-5.65, -0.86) * mm, "end": v(-5.63, -0.88) * mm});
            skLineSegment(sketch, "E3824", {"start": v(-5.63, -0.88) * mm, "end": v(-5.61, -0.89) * mm});
            skLineSegment(sketch, "E3825", {"start": v(-5.61, -0.89) * mm, "end": v(-5.59, -0.9) * mm});
            skLineSegment(sketch, "E3826", {"start": v(-5.59, -0.9) * mm, "end": v(-5.57, -0.91) * mm});
            skLineSegment(sketch, "E3827", {"start": v(-5.57, -0.91) * mm, "end": v(-5.54, -0.92) * mm});
            skLineSegment(sketch, "E3828", {"start": v(-5.54, -0.92) * mm, "end": v(-5.52, -0.93) * mm});
            skLineSegment(sketch, "E3829", {"start": v(-5.52, -0.93) * mm, "end": v(-5.5, -0.94) * mm});
            skLineSegment(sketch, "E3830", {"start": v(-5.5, -0.94) * mm, "end": v(-5.47, -0.95) * mm});
            skLineSegment(sketch, "E3831", {"start": v(-5.47, -0.95) * mm, "end": v(-5.45, -0.96) * mm});
            skLineSegment(sketch, "E3832", {"start": v(-5.45, -0.96) * mm, "end": v(-5.42, -0.97) * mm});
            skLineSegment(sketch, "E3833", {"start": v(-5.42, -0.97) * mm, "end": v(-5.4, -0.98) * mm});
            skLineSegment(sketch, "E3834", {"start": v(-5.4, -0.98) * mm, "end": v(-5.37, -0.99) * mm});
            skLineSegment(sketch, "E3835", {"start": v(-5.37, -0.99) * mm, "end": v(-5.34, -1) * mm});
            skLineSegment(sketch, "E3836", {"start": v(-5.34, -1) * mm, "end": v(-5.3, -1) * mm});
            skLineSegment(sketch, "E3837", {"start": v(-5.3, -1) * mm, "end": v(-5.28, -1) * mm});
            skLineSegment(sketch, "E3838", {"start": v(-5.28, -1) * mm, "end": v(-5.25, -1) * mm});
            skLineSegment(sketch, "E3839", {"start": v(-5.25, -1) * mm, "end": v(-5.22, -1.01) * mm});
            skLineSegment(sketch, "E3840", {"start": v(-5.22, -1.01) * mm, "end": v(-5.18, -1.02) * mm});
            skLineSegment(sketch, "E3841", {"start": v(-5.18, -1.02) * mm, "end": v(-5.15, -1.02) * mm});
            skLineSegment(sketch, "E3842", {"start": v(-5.15, -1.02) * mm, "end": v(-5.12, -1.02) * mm});
            skLineSegment(sketch, "E3843", {"start": v(-5.12, -1.02) * mm, "end": v(-5.08, -1.02) * mm});
            skLineSegment(sketch, "E3844", {"start": v(-5.08, -1.02) * mm, "end": v(-5.05, -1.02) * mm});
            skLineSegment(sketch, "E3845", {"start": v(-5.05, -1.02) * mm, "end": v(-4.97, -1.02) * mm});
            skLineSegment(sketch, "E3846", {"start": v(-4.97, -1.02) * mm, "end": v(-4.9, -1.02) * mm});
            skLineSegment(sketch, "E3847", {"start": v(-4.9, -1.02) * mm, "end": v(-4.83, -1.01) * mm});
            skLineSegment(sketch, "E3848", {"start": v(-4.83, -1.01) * mm, "end": v(-4.76, -1) * mm});
            skLineSegment(sketch, "E3849", {"start": v(-4.76, -1) * mm, "end": v(-4.7, -1) * mm});
            skLineSegment(sketch, "E3850", {"start": v(-4.7, -1) * mm, "end": v(-4.62, -0.98) * mm});
            skLineSegment(sketch, "E3851", {"start": v(-4.62, -0.98) * mm, "end": v(-4.56, -0.97) * mm});
            skLineSegment(sketch, "E3852", {"start": v(-4.56, -0.97) * mm, "end": v(-4.5, -0.95) * mm});
            skLineSegment(sketch, "E3853", {"start": v(-4.5, -0.95) * mm, "end": v(-4.43, -0.94) * mm});
            skLineSegment(sketch, "E3854", {"start": v(-4.43, -0.94) * mm, "end": v(-4.36, -0.92) * mm});
            skLineSegment(sketch, "E3855", {"start": v(-4.36, -0.92) * mm, "end": v(-4.3, -0.9) * mm});
            skLineSegment(sketch, "E3856", {"start": v(-4.3, -0.9) * mm, "end": v(-4.24, -0.87) * mm});
            skLineSegment(sketch, "E3857", {"start": v(-4.24, -0.87) * mm, "end": v(-4.18, -0.85) * mm});
            skLineSegment(sketch, "E3858", {"start": v(-4.18, -0.85) * mm, "end": v(-4.12, -0.82) * mm});
            skLineSegment(sketch, "E3859", {"start": v(-4.12, -0.82) * mm, "end": v(-4.06, -0.79) * mm});
            skLineSegment(sketch, "E3860", {"start": v(-4.06, -0.79) * mm, "end": v(-4, -0.76) * mm});
            skLineSegment(sketch, "E3861", {"start": v(-4, -0.76) * mm, "end": v(-3.95, -0.73) * mm});
            skLineSegment(sketch, "E3862", {"start": v(-3.95, -0.73) * mm, "end": v(-3.9, -0.7) * mm});
            skLineSegment(sketch, "E3863", {"start": v(-3.9, -0.7) * mm, "end": v(-3.84, -0.66) * mm});
            skLineSegment(sketch, "E3864", {"start": v(-3.84, -0.66) * mm, "end": v(-3.79, -0.62) * mm});
            skLineSegment(sketch, "E3865", {"start": v(-3.79, -0.62) * mm, "end": v(-3.74, -0.58) * mm});
            skLineSegment(sketch, "E3866", {"start": v(-3.74, -0.58) * mm, "end": v(-3.69, -0.54) * mm});
            skLineSegment(sketch, "E3867", {"start": v(-3.69, -0.54) * mm, "end": v(-3.64, -0.5) * mm});
            skLineSegment(sketch, "E3868", {"start": v(-3.64, -0.5) * mm, "end": v(-3.6, -0.46) * mm});
            skLineSegment(sketch, "E3869", {"start": v(-3.6, -0.46) * mm, "end": v(-3.55, -0.41) * mm});
            skLineSegment(sketch, "E3870", {"start": v(-3.55, -0.41) * mm, "end": v(-3.5, -0.37) * mm});
            skLineSegment(sketch, "E3871", {"start": v(-3.5, -0.37) * mm, "end": v(-3.46, -0.32) * mm});
            skLineSegment(sketch, "E3872", {"start": v(-3.46, -0.32) * mm, "end": v(-3.42, -0.27) * mm});
            skLineSegment(sketch, "E3873", {"start": v(-3.42, -0.27) * mm, "end": v(-3.38, -0.22) * mm});
            skLineSegment(sketch, "E3874", {"start": v(-3.38, -0.22) * mm, "end": v(-3.35, -0.17) * mm});
            skLineSegment(sketch, "E3875", {"start": v(-3.35, -0.17) * mm, "end": v(-3.31, -0.12) * mm});
            skLineSegment(sketch, "E3876", {"start": v(-3.31, -0.12) * mm, "end": v(-3.28, -0.06) * mm});
            skLineSegment(sketch, "E3877", {"start": v(-3.28, -0.06) * mm, "end": v(-3.24, 0) * mm});
            skLineSegment(sketch, "E3878", {"start": v(-3.24, 0) * mm, "end": v(-3.21, 0.05) * mm});
            skLineSegment(sketch, "E3879", {"start": v(-3.21, 0.05) * mm, "end": v(-3.18, 0.1) * mm});
            skLineSegment(sketch, "E3880", {"start": v(-3.18, 0.1) * mm, "end": v(-3.16, 0.16) * mm});
            skLineSegment(sketch, "E3881", {"start": v(-3.16, 0.16) * mm, "end": v(-3.13, 0.22) * mm});
            skLineSegment(sketch, "E3882", {"start": v(-3.13, 0.22) * mm, "end": v(-3.1, 0.28) * mm});
            skLineSegment(sketch, "E3883", {"start": v(-3.1, 0.28) * mm, "end": v(-3.08, 0.34) * mm});
            skLineSegment(sketch, "E3884", {"start": v(-3.08, 0.34) * mm, "end": v(-3.06, 0.4) * mm});
            skLineSegment(sketch, "E3885", {"start": v(-3.06, 0.4) * mm, "end": v(-3.04, 0.46) * mm});
            skLineSegment(sketch, "E3886", {"start": v(-3.04, 0.46) * mm, "end": v(-3.02, 0.52) * mm});
            skLineSegment(sketch, "E3887", {"start": v(-3.02, 0.52) * mm, "end": v(-3, 0.59) * mm});
            skLineSegment(sketch, "E3888", {"start": v(-3, 0.59) * mm, "end": v(-3, 0.65) * mm});
            skLineSegment(sketch, "E3889", {"start": v(-3, 0.65) * mm, "end": v(-2.98, 0.72) * mm});
            skLineSegment(sketch, "E3890", {"start": v(-2.98, 0.72) * mm, "end": v(-2.97, 0.78) * mm});
            skLineSegment(sketch, "E3891", {"start": v(-2.97, 0.78) * mm, "end": v(-2.96, 0.85) * mm});
            skLineSegment(sketch, "E3892", {"start": v(-2.96, 0.85) * mm, "end": v(-2.96, 0.92) * mm});
            skLineSegment(sketch, "E3893", {"start": v(-2.96, 0.92) * mm, "end": v(-2.95, 0.98) * mm});
            skLineSegment(sketch, "E3894", {"start": v(-2.95, 0.98) * mm, "end": v(-2.95, 1.05) * mm});
            skLineSegment(sketch, "E3895", {"start": v(-2.95, 1.05) * mm, "end": v(-2.95, 1.12) * mm});
            skLineSegment(sketch, "E3896", {"start": v(-2.95, 1.12) * mm, "end": v(-2.96, 1.19) * mm});
            skLineSegment(sketch, "E3897", {"start": v(-2.96, 1.19) * mm, "end": v(-2.96, 1.26) * mm});
            skLineSegment(sketch, "E3898", {"start": v(-2.96, 1.26) * mm, "end": v(-2.97, 1.32) * mm});
            skLineSegment(sketch, "E3899", {"start": v(-2.97, 1.32) * mm, "end": v(-2.98, 1.39) * mm});
            skLineSegment(sketch, "E3900", {"start": v(-2.98, 1.39) * mm, "end": v(-3, 1.46) * mm});
            skLineSegment(sketch, "E3901", {"start": v(-3, 1.46) * mm, "end": v(-3, 1.52) * mm});
            skLineSegment(sketch, "E3902", {"start": v(-3, 1.52) * mm, "end": v(-3.02, 1.59) * mm});
            skLineSegment(sketch, "E3903", {"start": v(-3.02, 1.59) * mm, "end": v(-3.04, 1.65) * mm});
            skLineSegment(sketch, "E3904", {"start": v(-3.04, 1.65) * mm, "end": v(-3.06, 1.71) * mm});
            skLineSegment(sketch, "E3905", {"start": v(-3.06, 1.71) * mm, "end": v(-3.08, 1.78) * mm});
            skLineSegment(sketch, "E3906", {"start": v(-3.08, 1.78) * mm, "end": v(-3.1, 1.84) * mm});
            skLineSegment(sketch, "E3907", {"start": v(-3.1, 1.84) * mm, "end": v(-3.13, 1.9) * mm});
            skLineSegment(sketch, "E3908", {"start": v(-3.13, 1.9) * mm, "end": v(-3.16, 1.96) * mm});
            skLineSegment(sketch, "E3909", {"start": v(-3.16, 1.96) * mm, "end": v(-3.2, 2.02) * mm});
            skLineSegment(sketch, "E3910", {"start": v(-3.2, 2.02) * mm, "end": v(-3.22, 2.07) * mm});
            skLineSegment(sketch, "E3911", {"start": v(-3.22, 2.07) * mm, "end": v(-3.26, 2.13) * mm});
            skLineSegment(sketch, "E3912", {"start": v(-3.26, 2.13) * mm, "end": v(-3.3, 2.19) * mm});
            skLineSegment(sketch, "E3913", {"start": v(-3.3, 2.19) * mm, "end": v(-3.33, 2.24) * mm});
            skLineSegment(sketch, "E3914", {"start": v(-3.33, 2.24) * mm, "end": v(-3.37, 2.3) * mm});
            skLineSegment(sketch, "E3915", {"start": v(-3.37, 2.3) * mm, "end": v(-3.4, 2.35) * mm});
            skLineSegment(sketch, "E3916", {"start": v(-3.4, 2.35) * mm, "end": v(-3.45, 2.4) * mm});
            skLineSegment(sketch, "E3917", {"start": v(-3.45, 2.4) * mm, "end": v(-3.49, 2.45) * mm});
            skLineSegment(sketch, "E3918", {"start": v(-3.49, 2.45) * mm, "end": v(-3.53, 2.5) * mm});
            skLineSegment(sketch, "E3919", {"start": v(-3.53, 2.5) * mm, "end": v(-3.58, 2.54) * mm});
            skLineSegment(sketch, "E3920", {"start": v(-3.58, 2.54) * mm, "end": v(-3.63, 2.59) * mm});
            skLineSegment(sketch, "E3921", {"start": v(-3.63, 2.59) * mm, "end": v(-3.67, 2.63) * mm});
            skLineSegment(sketch, "E3922", {"start": v(-3.67, 2.63) * mm, "end": v(-3.72, 2.68) * mm});
            skLineSegment(sketch, "E3923", {"start": v(-3.72, 2.68) * mm, "end": v(-3.77, 2.72) * mm});
            skLineSegment(sketch, "E3924", {"start": v(-3.77, 2.72) * mm, "end": v(-3.83, 2.76) * mm});
            skLineSegment(sketch, "E3925", {"start": v(-3.83, 2.76) * mm, "end": v(-3.88, 2.8) * mm});
            skLineSegment(sketch, "E3926", {"start": v(-3.88, 2.8) * mm, "end": v(-3.93, 2.83) * mm});
            skLineSegment(sketch, "E3927", {"start": v(-3.93, 2.83) * mm, "end": v(-3.99, 2.87) * mm});
            skLineSegment(sketch, "E3928", {"start": v(-3.99, 2.87) * mm, "end": v(-4.05, 2.9) * mm});
            skLineSegment(sketch, "E3929", {"start": v(-4.05, 2.9) * mm, "end": v(-4.1, 2.93) * mm});
            skLineSegment(sketch, "E3930", {"start": v(-4.1, 2.93) * mm, "end": v(-4.16, 2.96) * mm});
            skLineSegment(sketch, "E3931", {"start": v(-4.16, 2.96) * mm, "end": v(-4.22, 2.99) * mm});
            skLineSegment(sketch, "E3932", {"start": v(-4.22, 2.99) * mm, "end": v(-4.28, 3.01) * mm});
            skLineSegment(sketch, "E3933", {"start": v(-4.28, 3.01) * mm, "end": v(-4.35, 3.04) * mm});
            skLineSegment(sketch, "E3934", {"start": v(-4.35, 3.04) * mm, "end": v(-4.4, 3.06) * mm});
            skLineSegment(sketch, "E3935", {"start": v(-4.4, 3.06) * mm, "end": v(-4.47, 3.08) * mm});
            skLineSegment(sketch, "E3936", {"start": v(-4.47, 3.08) * mm, "end": v(-4.54, 3.1) * mm});
            skLineSegment(sketch, "E3937", {"start": v(-4.54, 3.1) * mm, "end": v(-4.6, 3.12) * mm});
            skLineSegment(sketch, "E3938", {"start": v(-4.6, 3.12) * mm, "end": v(-4.67, 3.13) * mm});
            skLineSegment(sketch, "E3939", {"start": v(-4.67, 3.13) * mm, "end": v(-4.73, 3.14) * mm});
            skLineSegment(sketch, "E3940", {"start": v(-4.73, 3.14) * mm, "end": v(-4.8, 3.15) * mm});
            skLineSegment(sketch, "E3941", {"start": v(-4.8, 3.15) * mm, "end": v(-4.87, 3.16) * mm});
            skLineSegment(sketch, "E3942", {"start": v(-4.87, 3.16) * mm, "end": v(-4.93, 3.17) * mm});
            skLineSegment(sketch, "E3943", {"start": v(-4.93, 3.17) * mm, "end": v(-5, 3.17) * mm});
            skLineSegment(sketch, "E3944", {"start": v(-5, 3.17) * mm, "end": v(-5.07, 3.17) * mm});
            skLineSegment(sketch, "E3945", {"start": v(-5.07, 3.17) * mm, "end": v(-5.07, 3.17) * mm});
            skLineSegment(sketch, "E3946", {"start": v(-5.07, 3.17) * mm, "end": v(-5.08, 3.17) * mm});
            skLineSegment(sketch, "E3947", {"start": v(-5.08, 3.17) * mm, "end": v(-5.08, 3.17) * mm});
            skLineSegment(sketch, "E3948", {"start": v(-5.08, 3.17) * mm, "end": v(-5.09, 3.17) * mm});
            skLineSegment(sketch, "E3949", {"start": v(-5.09, 3.17) * mm, "end": v(-5.1, 3.17) * mm});
            skLineSegment(sketch, "E3950", {"start": v(-5.1, 3.17) * mm, "end": v(-5.1, 3.17) * mm});
            skLineSegment(sketch, "E3951", {"start": v(-5.1, 3.17) * mm, "end": v(-5.11, 3.17) * mm});
            skLineSegment(sketch, "E3952", {"start": v(-5.11, 3.17) * mm, "end": v(-5.12, 3.17) * mm});
            skLineSegment(sketch, "E3953", {"start": v(-5.12, 3.17) * mm, "end": v(-5.14, 3.17) * mm});
            skLineSegment(sketch, "E3954", {"start": v(-5.14, 3.17) * mm, "end": v(-5.15, 3.17) * mm});
            skLineSegment(sketch, "E3955", {"start": v(-5.15, 3.17) * mm, "end": v(-5.17, 3.17) * mm});
            skLineSegment(sketch, "E3956", {"start": v(-5.17, 3.17) * mm, "end": v(-5.18, 3.17) * mm});
            skLineSegment(sketch, "E3957", {"start": v(-5.18, 3.17) * mm, "end": v(-5.2, 3.17) * mm});
            skLineSegment(sketch, "E3958", {"start": v(-5.2, 3.17) * mm, "end": v(-5.22, 3.17) * mm});
            skLineSegment(sketch, "E3959", {"start": v(-5.22, 3.17) * mm, "end": v(-5.24, 3.17) * mm});
            skLineSegment(sketch, "E3960", {"start": v(-5.24, 3.17) * mm, "end": v(-5.26, 3.17) * mm});
            skLineSegment(sketch, "E3961", {"start": v(-5.26, 3.17) * mm, "end": v(-5.28, 3.17) * mm});
            skLineSegment(sketch, "E3962", {"start": v(-5.28, 3.17) * mm, "end": v(-5.3, 3.17) * mm});
            skLineSegment(sketch, "E3963", {"start": v(-5.3, 3.17) * mm, "end": v(-5.32, 3.17) * mm});
            skLineSegment(sketch, "E3964", {"start": v(-5.32, 3.17) * mm, "end": v(-5.35, 3.17) * mm});
            skLineSegment(sketch, "E3965", {"start": v(-5.35, 3.17) * mm, "end": v(-5.37, 3.17) * mm});
            skLineSegment(sketch, "E3966", {"start": v(-5.37, 3.17) * mm, "end": v(-5.4, 3.17) * mm});
            skLineSegment(sketch, "E3967", {"start": v(-5.4, 3.17) * mm, "end": v(-5.41, 3.17) * mm});
            skLineSegment(sketch, "E3968", {"start": v(-5.41, 3.17) * mm, "end": v(-5.44, 3.17) * mm});
            skLineSegment(sketch, "E3969", {"start": v(-5.44, 3.17) * mm, "end": v(-5.46, 3.17) * mm});
            skLineSegment(sketch, "E3970", {"start": v(-5.46, 3.17) * mm, "end": v(-5.48, 3.17) * mm});
            skLineSegment(sketch, "E3971", {"start": v(-5.48, 3.17) * mm, "end": v(-5.5, 3.17) * mm});
            skLineSegment(sketch, "E3972", {"start": v(-5.5, 3.17) * mm, "end": v(-5.53, 3.17) * mm});
            skLineSegment(sketch, "E3973", {"start": v(-5.53, 3.17) * mm, "end": v(-5.55, 3.17) * mm});
            skLineSegment(sketch, "E3974", {"start": v(-5.55, 3.17) * mm, "end": v(-5.58, 3.17) * mm});
            skLineSegment(sketch, "E3975", {"start": v(-5.58, 3.17) * mm, "end": v(-5.6, 3.17) * mm});
            skLineSegment(sketch, "E3976", {"start": v(-5.6, 3.17) * mm, "end": v(-5.62, 3.17) * mm});
            skLineSegment(sketch, "E3977", {"start": v(-5.62, 3.17) * mm, "end": v(-5.64, 3.17) * mm});
            skLineSegment(sketch, "E3978", {"start": v(-5.64, 3.17) * mm, "end": v(-5.66, 3.17) * mm});
            skLineSegment(sketch, "E3979", {"start": v(-5.66, 3.17) * mm, "end": v(-5.68, 3.17) * mm});
            skLineSegment(sketch, "E3980", {"start": v(-5.68, 3.17) * mm, "end": v(-5.7, 3.17) * mm});
            skLineSegment(sketch, "E3981", {"start": v(-5.7, 3.17) * mm, "end": v(-5.72, 3.17) * mm});
            skLineSegment(sketch, "E3982", {"start": v(-5.72, 3.17) * mm, "end": v(-5.74, 3.17) * mm});
            skLineSegment(sketch, "E3983", {"start": v(-5.74, 3.17) * mm, "end": v(-5.75, 3.17) * mm});
            skLineSegment(sketch, "E3984", {"start": v(-5.75, 3.17) * mm, "end": v(-5.77, 3.17) * mm});
            skLineSegment(sketch, "E3985", {"start": v(-5.77, 3.17) * mm, "end": v(-5.78, 3.17) * mm});
            skLineSegment(sketch, "E3986", {"start": v(-5.78, 3.17) * mm, "end": v(-5.8, 3.17) * mm});
            skLineSegment(sketch, "E3987", {"start": v(-5.8, 3.17) * mm, "end": v(-5.8, 3.17) * mm});
            skLineSegment(sketch, "E3988", {"start": v(-5.8, 3.17) * mm, "end": v(-5.82, 3.17) * mm});
            skLineSegment(sketch, "E3989", {"start": v(-5.82, 3.17) * mm, "end": v(-5.83, 3.17) * mm});
            skLineSegment(sketch, "E3990", {"start": v(-5.83, 3.17) * mm, "end": v(-5.83, 3.17) * mm});
            skLineSegment(sketch, "E3991", {"start": v(-5.83, 3.17) * mm, "end": v(-5.84, 3.17) * mm});
            skLineSegment(sketch, "E3992", {"start": v(-5.84, 3.17) * mm, "end": v(-5.85, 3.17) * mm});
            skLineSegment(sketch, "E3993", {"start": v(-5.85, 3.17) * mm, "end": v(-5.85, 3.17) * mm});
            skLineSegment(sketch, "E3994", {"start": v(-5.85, 3.17) * mm, "end": v(-5.87, 3.17) * mm});
            skLineSegment(sketch, "E3995", {"start": v(-5.87, 3.17) * mm, "end": v(-5.9, 3.17) * mm});
            skLineSegment(sketch, "E3996", {"start": v(-5.9, 3.17) * mm, "end": v(-5.91, 3.17) * mm});
            skLineSegment(sketch, "E3997", {"start": v(-5.91, 3.17) * mm, "end": v(-5.93, 3.17) * mm});
            skLineSegment(sketch, "E3998", {"start": v(-5.93, 3.17) * mm, "end": v(-5.95, 3.16) * mm});
            skLineSegment(sketch, "E3999", {"start": v(-5.95, 3.16) * mm, "end": v(-5.97, 3.16) * mm});
            skLineSegment(sketch, "E4000", {"start": v(-5.97, 3.16) * mm, "end": v(-6, 3.16) * mm});
            skLineSegment(sketch, "E4001", {"start": v(-6, 3.16) * mm, "end": v(-6, 3.16) * mm});
            skLineSegment(sketch, "E4002", {"start": v(-6, 3.16) * mm, "end": v(-6.03, 3.15) * mm});
            skLineSegment(sketch, "E4003", {"start": v(-6.03, 3.15) * mm, "end": v(-6.05, 3.15) * mm});
            skLineSegment(sketch, "E4004", {"start": v(-6.05, 3.15) * mm, "end": v(-6.06, 3.14) * mm});
            skLineSegment(sketch, "E4005", {"start": v(-6.06, 3.14) * mm, "end": v(-6.08, 3.14) * mm});
            skLineSegment(sketch, "E4006", {"start": v(-6.08, 3.14) * mm, "end": v(-6.1, 3.13) * mm});
            skLineSegment(sketch, "E4007", {"start": v(-6.1, 3.13) * mm, "end": v(-6.12, 3.13) * mm});
            skLineSegment(sketch, "E4008", {"start": v(-6.12, 3.13) * mm, "end": v(-6.13, 3.12) * mm});
            skLineSegment(sketch, "E4009", {"start": v(-6.13, 3.12) * mm, "end": v(-6.15, 3.11) * mm});
            skLineSegment(sketch, "E4010", {"start": v(-6.15, 3.11) * mm, "end": v(-6.16, 3.1) * mm});
            skLineSegment(sketch, "E4011", {"start": v(-6.16, 3.1) * mm, "end": v(-6.18, 3.1) * mm});
            skLineSegment(sketch, "E4012", {"start": v(-6.18, 3.1) * mm, "end": v(-6.2, 3.09) * mm});
            skLineSegment(sketch, "E4013", {"start": v(-6.2, 3.09) * mm, "end": v(-6.2, 3.08) * mm});
            skLineSegment(sketch, "E4014", {"start": v(-6.2, 3.08) * mm, "end": v(-6.22, 3.07) * mm});
            skLineSegment(sketch, "E4015", {"start": v(-6.22, 3.07) * mm, "end": v(-6.24, 3.06) * mm});
            skLineSegment(sketch, "E4016", {"start": v(-6.24, 3.06) * mm, "end": v(-6.25, 3.05) * mm});
            skLineSegment(sketch, "E4017", {"start": v(-6.25, 3.05) * mm, "end": v(-6.26, 3.04) * mm});
            skLineSegment(sketch, "E4018", {"start": v(-6.26, 3.04) * mm, "end": v(-6.28, 3.03) * mm});
            skLineSegment(sketch, "E4019", {"start": v(-6.28, 3.03) * mm, "end": v(-6.29, 3.01) * mm});
            skLineSegment(sketch, "E4020", {"start": v(-6.29, 3.01) * mm, "end": v(-6.3, 3) * mm});
            skLineSegment(sketch, "E4021", {"start": v(-6.3, 3) * mm, "end": v(-6.31, 2.99) * mm});
            skLineSegment(sketch, "E4022", {"start": v(-6.31, 2.99) * mm, "end": v(-6.32, 2.98) * mm});
            skLineSegment(sketch, "E4023", {"start": v(-6.32, 2.98) * mm, "end": v(-6.33, 2.96) * mm});
            skLineSegment(sketch, "E4024", {"start": v(-6.33, 2.96) * mm, "end": v(-6.34, 2.95) * mm});
            skLineSegment(sketch, "E4025", {"start": v(-6.34, 2.95) * mm, "end": v(-6.35, 2.93) * mm});
            skLineSegment(sketch, "E4026", {"start": v(-6.35, 2.93) * mm, "end": v(-6.36, 2.92) * mm});
            skLineSegment(sketch, "E4027", {"start": v(-6.36, 2.92) * mm, "end": v(-6.37, 2.9) * mm});
            skLineSegment(sketch, "E4028", {"start": v(-6.37, 2.9) * mm, "end": v(-6.38, 2.89) * mm});
            skLineSegment(sketch, "E4029", {"start": v(-6.38, 2.89) * mm, "end": v(-6.39, 2.87) * mm});
            skLineSegment(sketch, "E4030", {"start": v(-6.39, 2.87) * mm, "end": v(-6.4, 2.85) * mm});
            skLineSegment(sketch, "E4031", {"start": v(-6.4, 2.85) * mm, "end": v(-6.4, 2.83) * mm});
            skLineSegment(sketch, "E4032", {"start": v(-6.4, 2.83) * mm, "end": v(-6.4, 2.82) * mm});
            skLineSegment(sketch, "E4033", {"start": v(-6.4, 2.82) * mm, "end": v(-6.41, 2.8) * mm});
            skLineSegment(sketch, "E4034", {"start": v(-6.41, 2.8) * mm, "end": v(-6.42, 2.78) * mm});
            skLineSegment(sketch, "E4035", {"start": v(-6.42, 2.78) * mm, "end": v(-6.42, 2.76) * mm});
            skLineSegment(sketch, "E4036", {"start": v(-6.42, 2.76) * mm, "end": v(-6.42, 2.74) * mm});
            skLineSegment(sketch, "E4037", {"start": v(-6.42, 2.74) * mm, "end": v(-6.43, 2.72) * mm});
            skLineSegment(sketch, "E4038", {"start": v(-6.43, 2.72) * mm, "end": v(-6.43, 2.7) * mm});
            skLineSegment(sketch, "E4039", {"start": v(-6.43, 2.7) * mm, "end": v(-6.43, 2.67) * mm});
            skLineSegment(sketch, "E4040", {"start": v(-6.43, 2.67) * mm, "end": v(-6.44, 2.65) * mm});
            skLineSegment(sketch, "E4041", {"start": v(-6.44, 2.65) * mm, "end": v(-6.44, 2.63) * mm});
            skLineSegment(sketch, "E4042", {"start": v(-6.44, 2.63) * mm, "end": v(-6.44, 2.6) * mm});
            skLineSegment(sketch, "E4043", {"start": v(-6.44, 2.6) * mm, "end": v(-6.44, 2.58) * mm});
            skLineSegment(sketch, "E4044", {"start": v(4.01, -2.77) * mm, "end": v(4, -2.77) * mm});
            skLineSegment(sketch, "E4045", {"start": v(4, -2.77) * mm, "end": v(3.99, -2.77) * mm});
            skLineSegment(sketch, "E4046", {"start": v(3.99, -2.77) * mm, "end": v(3.97, -2.77) * mm});
            skLineSegment(sketch, "E4047", {"start": v(3.97, -2.77) * mm, "end": v(3.96, -2.77) * mm});
            skLineSegment(sketch, "E4048", {"start": v(3.96, -2.77) * mm, "end": v(3.95, -2.77) * mm});
            skLineSegment(sketch, "E4049", {"start": v(3.95, -2.77) * mm, "end": v(3.94, -2.76) * mm});
            skLineSegment(sketch, "E4050", {"start": v(3.94, -2.76) * mm, "end": v(3.93, -2.76) * mm});
            skLineSegment(sketch, "E4051", {"start": v(3.93, -2.76) * mm, "end": v(3.92, -2.76) * mm});
            skLineSegment(sketch, "E4052", {"start": v(3.92, -2.76) * mm, "end": v(3.9, -2.76) * mm});
            skLineSegment(sketch, "E4053", {"start": v(3.9, -2.76) * mm, "end": v(3.9, -2.75) * mm});
            skLineSegment(sketch, "E4054", {"start": v(3.9, -2.75) * mm, "end": v(3.89, -2.75) * mm});
            skLineSegment(sketch, "E4055", {"start": v(3.89, -2.75) * mm, "end": v(3.88, -2.75) * mm});
            skLineSegment(sketch, "E4056", {"start": v(3.88, -2.75) * mm, "end": v(3.87, -2.74) * mm});
            skLineSegment(sketch, "E4057", {"start": v(3.87, -2.74) * mm, "end": v(3.86, -2.74) * mm});
            skLineSegment(sketch, "E4058", {"start": v(3.86, -2.74) * mm, "end": v(3.85, -2.73) * mm});
            skLineSegment(sketch, "E4059", {"start": v(3.85, -2.73) * mm, "end": v(3.84, -2.73) * mm});
            skLineSegment(sketch, "E4060", {"start": v(3.84, -2.73) * mm, "end": v(3.83, -2.72) * mm});
            skLineSegment(sketch, "E4061", {"start": v(3.83, -2.72) * mm, "end": v(3.82, -2.72) * mm});
            skLineSegment(sketch, "E4062", {"start": v(3.82, -2.72) * mm, "end": v(3.81, -2.71) * mm});
            skLineSegment(sketch, "E4063", {"start": v(3.81, -2.71) * mm, "end": v(3.8, -2.7) * mm});
            skLineSegment(sketch, "E4064", {"start": v(3.8, -2.7) * mm, "end": v(3.8, -2.7) * mm});
            skLineSegment(sketch, "E4065", {"start": v(3.8, -2.7) * mm, "end": v(3.79, -2.7) * mm});
            skLineSegment(sketch, "E4066", {"start": v(3.79, -2.7) * mm, "end": v(3.78, -2.69) * mm});
            skLineSegment(sketch, "E4067", {"start": v(3.78, -2.69) * mm, "end": v(3.77, -2.68) * mm});
            skLineSegment(sketch, "E4068", {"start": v(3.77, -2.68) * mm, "end": v(3.77, -2.68) * mm});
            skLineSegment(sketch, "E4069", {"start": v(3.77, -2.68) * mm, "end": v(3.76, -2.67) * mm});
            skLineSegment(sketch, "E4070", {"start": v(3.76, -2.67) * mm, "end": v(3.75, -2.66) * mm});
            skLineSegment(sketch, "E4071", {"start": v(3.75, -2.66) * mm, "end": v(3.75, -2.65) * mm});
            skLineSegment(sketch, "E4072", {"start": v(3.75, -2.65) * mm, "end": v(3.74, -2.65) * mm});
            skLineSegment(sketch, "E4073", {"start": v(3.74, -2.65) * mm, "end": v(3.74, -2.64) * mm});
            skLineSegment(sketch, "E4074", {"start": v(3.74, -2.64) * mm, "end": v(3.73, -2.63) * mm});
            skLineSegment(sketch, "E4075", {"start": v(3.73, -2.63) * mm, "end": v(3.73, -2.62) * mm});
            skLineSegment(sketch, "E4076", {"start": v(3.73, -2.62) * mm, "end": v(3.72, -2.61) * mm});
            skLineSegment(sketch, "E4077", {"start": v(3.72, -2.61) * mm, "end": v(3.72, -2.6) * mm});
            skLineSegment(sketch, "E4078", {"start": v(3.72, -2.6) * mm, "end": v(3.71, -2.6) * mm});
            skLineSegment(sketch, "E4079", {"start": v(3.71, -2.6) * mm, "end": v(3.7, -2.59) * mm});
            skLineSegment(sketch, "E4080", {"start": v(3.7, -2.59) * mm, "end": v(3.7, -2.58) * mm});
            skLineSegment(sketch, "E4081", {"start": v(3.7, -2.58) * mm, "end": v(3.7, -2.57) * mm});
            skLineSegment(sketch, "E4082", {"start": v(3.7, -2.57) * mm, "end": v(3.7, -2.56) * mm});
            skLineSegment(sketch, "E4083", {"start": v(3.7, -2.56) * mm, "end": v(3.7, -2.55) * mm});
            skLineSegment(sketch, "E4084", {"start": v(3.7, -2.55) * mm, "end": v(3.7, -2.54) * mm});
            skLineSegment(sketch, "E4085", {"start": v(3.7, -2.54) * mm, "end": v(3.7, -2.53) * mm});
            skLineSegment(sketch, "E4086", {"start": v(3.7, -2.53) * mm, "end": v(3.69, -2.52) * mm});
            skLineSegment(sketch, "E4087", {"start": v(3.69, -2.52) * mm, "end": v(3.69, -2.5) * mm});
            skLineSegment(sketch, "E4088", {"start": v(3.69, -2.5) * mm, "end": v(3.69, -2.5) * mm});
            skLineSegment(sketch, "E4089", {"start": v(3.69, -2.5) * mm, "end": v(3.68, -2.48) * mm});
            skLineSegment(sketch, "E4090", {"start": v(3.68, -2.48) * mm, "end": v(3.68, -2.47) * mm});
            skLineSegment(sketch, "E4091", {"start": v(3.68, -2.47) * mm, "end": v(3.68, -2.46) * mm});
            skLineSegment(sketch, "E4092", {"start": v(3.68, -2.46) * mm, "end": v(3.68, -2.45) * mm});
            skLineSegment(sketch, "E4093", {"start": v(3.68, -2.45) * mm, "end": v(3.68, -2.44) * mm});
            skLineSegment(sketch, "E4094", {"start": v(3.68, -2.44) * mm, "end": v(3.68, -2.43) * mm});
            skLineSegment(sketch, "E4095", {"start": v(3.68, -2.43) * mm, "end": v(3.68, -2.42) * mm});
            skLineSegment(sketch, "E4096", {"start": v(3.68, -2.42) * mm, "end": v(3.68, -2.39) * mm});
            skLineSegment(sketch, "E4097", {"start": v(3.68, -2.39) * mm, "end": v(3.68, -2.35) * mm});
            skLineSegment(sketch, "E4098", {"start": v(3.68, -2.35) * mm, "end": v(3.68, -2.3) * mm});
            skLineSegment(sketch, "E4099", {"start": v(3.68, -2.3) * mm, "end": v(3.68, -2.24) * mm});
            skLineSegment(sketch, "E4100", {"start": v(3.68, -2.24) * mm, "end": v(3.68, -2.18) * mm});
            skLineSegment(sketch, "E4101", {"start": v(3.68, -2.18) * mm, "end": v(3.68, -2.1) * mm});
            skLineSegment(sketch, "E4102", {"start": v(3.68, -2.1) * mm, "end": v(3.68, -2.02) * mm});
            skLineSegment(sketch, "E4103", {"start": v(3.68, -2.02) * mm, "end": v(3.68, -1.93) * mm});
            skLineSegment(sketch, "E4104", {"start": v(3.68, -1.93) * mm, "end": v(3.68, -1.83) * mm});
            skLineSegment(sketch, "E4105", {"start": v(3.68, -1.83) * mm, "end": v(3.68, -1.73) * mm});
            skLineSegment(sketch, "E4106", {"start": v(3.68, -1.73) * mm, "end": v(3.68, -1.61) * mm});
            skLineSegment(sketch, "E4107", {"start": v(3.68, -1.61) * mm, "end": v(3.68, -1.5) * mm});
            skLineSegment(sketch, "E4108", {"start": v(3.68, -1.5) * mm, "end": v(3.68, -1.38) * mm});
            skLineSegment(sketch, "E4109", {"start": v(3.68, -1.38) * mm, "end": v(3.68, -1.25) * mm});
            skLineSegment(sketch, "E4110", {"start": v(3.68, -1.25) * mm, "end": v(3.68, -1.12) * mm});
            skLineSegment(sketch, "E4111", {"start": v(3.68, -1.12) * mm, "end": v(3.68, -0.98) * mm});
            skLineSegment(sketch, "E4112", {"start": v(3.68, -0.98) * mm, "end": v(3.68, -0.85) * mm});
            skLineSegment(sketch, "E4113", {"start": v(3.68, -0.85) * mm, "end": v(3.68, -0.7) * mm});
            skLineSegment(sketch, "E4114", {"start": v(3.68, -0.7) * mm, "end": v(3.68, -0.56) * mm});
            skLineSegment(sketch, "E4115", {"start": v(3.68, -0.56) * mm, "end": v(3.68, -0.42) * mm});
            skLineSegment(sketch, "E4116", {"start": v(3.68, -0.42) * mm, "end": v(3.68, -0.27) * mm});
            skLineSegment(sketch, "E4117", {"start": v(3.68, -0.27) * mm, "end": v(3.68, -0.13) * mm});
            skLineSegment(sketch, "E4118", {"start": v(3.68, -0.13) * mm, "end": v(3.68, 0.02) * mm});
            skLineSegment(sketch, "E4119", {"start": v(3.68, 0.02) * mm, "end": v(3.68, 0.17) * mm});
            skLineSegment(sketch, "E4120", {"start": v(3.68, 0.17) * mm, "end": v(3.68, 0.32) * mm});
            skLineSegment(sketch, "E4121", {"start": v(3.68, 0.32) * mm, "end": v(3.68, 0.46) * mm});
            skLineSegment(sketch, "E4122", {"start": v(3.68, 0.46) * mm, "end": v(3.68, 0.6) * mm});
            skLineSegment(sketch, "E4123", {"start": v(3.68, 0.6) * mm, "end": v(3.68, 0.75) * mm});
            skLineSegment(sketch, "E4124", {"start": v(3.68, 0.75) * mm, "end": v(3.68, 0.9) * mm});
            skLineSegment(sketch, "E4125", {"start": v(3.68, 0.9) * mm, "end": v(3.68, 1.03) * mm});
            skLineSegment(sketch, "E4126", {"start": v(3.68, 1.03) * mm, "end": v(3.68, 1.16) * mm});
            skLineSegment(sketch, "E4127", {"start": v(3.68, 1.16) * mm, "end": v(3.68, 1.3) * mm});
            skLineSegment(sketch, "E4128", {"start": v(3.68, 1.3) * mm, "end": v(3.68, 1.42) * mm});
            skLineSegment(sketch, "E4129", {"start": v(3.68, 1.42) * mm, "end": v(3.68, 1.54) * mm});
            skLineSegment(sketch, "E4130", {"start": v(3.68, 1.54) * mm, "end": v(3.68, 1.66) * mm});
            skLineSegment(sketch, "E4131", {"start": v(3.68, 1.66) * mm, "end": v(3.68, 1.77) * mm});
            skLineSegment(sketch, "E4132", {"start": v(3.68, 1.77) * mm, "end": v(3.68, 1.87) * mm});
            skLineSegment(sketch, "E4133", {"start": v(3.68, 1.87) * mm, "end": v(3.68, 1.97) * mm});
            skLineSegment(sketch, "E4134", {"start": v(3.68, 1.97) * mm, "end": v(3.68, 2.06) * mm});
            skLineSegment(sketch, "E4135", {"start": v(3.68, 2.06) * mm, "end": v(3.68, 2.15) * mm});
            skLineSegment(sketch, "E4136", {"start": v(3.68, 2.15) * mm, "end": v(3.68, 2.22) * mm});
            skLineSegment(sketch, "E4137", {"start": v(3.68, 2.22) * mm, "end": v(3.68, 2.29) * mm});
            skLineSegment(sketch, "E4138", {"start": v(3.68, 2.29) * mm, "end": v(3.68, 2.35) * mm});
            skLineSegment(sketch, "E4139", {"start": v(3.68, 2.35) * mm, "end": v(3.68, 2.4) * mm});
            skLineSegment(sketch, "E4140", {"start": v(3.68, 2.4) * mm, "end": v(3.68, 2.43) * mm});
            skLineSegment(sketch, "E4141", {"start": v(3.68, 2.43) * mm, "end": v(3.68, 2.46) * mm});
            skLineSegment(sketch, "E4142", {"start": v(3.68, 2.46) * mm, "end": v(3.68, 2.48) * mm});
            skLineSegment(sketch, "E4143", {"start": v(3.68, 2.48) * mm, "end": v(3.68, 2.48) * mm});
            skLineSegment(sketch, "E4144", {"start": v(3.68, 2.48) * mm, "end": v(3.68, 2.49) * mm});
            skLineSegment(sketch, "E4145", {"start": v(3.68, 2.49) * mm, "end": v(3.68, 2.5) * mm});
            skLineSegment(sketch, "E4146", {"start": v(3.68, 2.5) * mm, "end": v(3.68, 2.5) * mm});
            skLineSegment(sketch, "E4147", {"start": v(3.68, 2.5) * mm, "end": v(3.68, 2.51) * mm});
            skLineSegment(sketch, "E4148", {"start": v(3.68, 2.51) * mm, "end": v(3.69, 2.52) * mm});
            skLineSegment(sketch, "E4149", {"start": v(3.69, 2.52) * mm, "end": v(3.69, 2.52) * mm});
            skLineSegment(sketch, "E4150", {"start": v(3.69, 2.52) * mm, "end": v(3.69, 2.53) * mm});
            skLineSegment(sketch, "E4151", {"start": v(3.69, 2.53) * mm, "end": v(3.7, 2.53) * mm});
            skLineSegment(sketch, "E4152", {"start": v(3.7, 2.53) * mm, "end": v(3.7, 2.54) * mm});
            skLineSegment(sketch, "E4153", {"start": v(3.7, 2.54) * mm, "end": v(3.7, 2.54) * mm});
            skLineSegment(sketch, "E4154", {"start": v(3.7, 2.54) * mm, "end": v(3.7, 2.55) * mm});
            skLineSegment(sketch, "E4155", {"start": v(3.7, 2.55) * mm, "end": v(3.7, 2.55) * mm});
            skLineSegment(sketch, "E4156", {"start": v(3.7, 2.55) * mm, "end": v(3.7, 2.56) * mm});
            skLineSegment(sketch, "E4157", {"start": v(3.7, 2.56) * mm, "end": v(3.7, 2.56) * mm});
            skLineSegment(sketch, "E4158", {"start": v(3.7, 2.56) * mm, "end": v(3.7, 2.57) * mm});
            skLineSegment(sketch, "E4159", {"start": v(3.7, 2.57) * mm, "end": v(3.71, 2.57) * mm});
            skLineSegment(sketch, "E4160", {"start": v(3.71, 2.57) * mm, "end": v(3.71, 2.57) * mm});
            skLineSegment(sketch, "E4161", {"start": v(3.71, 2.57) * mm, "end": v(3.72, 2.58) * mm});
            skLineSegment(sketch, "E4162", {"start": v(3.72, 2.58) * mm, "end": v(3.72, 2.58) * mm});
            skLineSegment(sketch, "E4163", {"start": v(3.72, 2.58) * mm, "end": v(3.72, 2.59) * mm});
            skLineSegment(sketch, "E4164", {"start": v(3.72, 2.59) * mm, "end": v(3.73, 2.6) * mm});
            skLineSegment(sketch, "E4165", {"start": v(3.73, 2.6) * mm, "end": v(3.73, 2.6) * mm});
            skLineSegment(sketch, "E4166", {"start": v(3.73, 2.6) * mm, "end": v(3.74, 2.6) * mm});
            skLineSegment(sketch, "E4167", {"start": v(3.74, 2.6) * mm, "end": v(3.74, 2.6) * mm});
            skLineSegment(sketch, "E4168", {"start": v(3.74, 2.6) * mm, "end": v(3.75, 2.6) * mm});
            skLineSegment(sketch, "E4169", {"start": v(3.75, 2.6) * mm, "end": v(3.75, 2.61) * mm});
            skLineSegment(sketch, "E4170", {"start": v(3.75, 2.61) * mm, "end": v(3.76, 2.62) * mm});
            skLineSegment(sketch, "E4171", {"start": v(3.76, 2.62) * mm, "end": v(3.76, 2.62) * mm});
            skLineSegment(sketch, "E4172", {"start": v(3.76, 2.62) * mm, "end": v(3.77, 2.62) * mm});
            skLineSegment(sketch, "E4173", {"start": v(3.77, 2.62) * mm, "end": v(3.77, 2.62) * mm});
            skLineSegment(sketch, "E4174", {"start": v(3.77, 2.62) * mm, "end": v(3.78, 2.63) * mm});
            skLineSegment(sketch, "E4175", {"start": v(3.78, 2.63) * mm, "end": v(3.78, 2.63) * mm});
            skLineSegment(sketch, "E4176", {"start": v(3.78, 2.63) * mm, "end": v(3.79, 2.63) * mm});
            skLineSegment(sketch, "E4177", {"start": v(3.79, 2.63) * mm, "end": v(3.8, 2.63) * mm});
            skLineSegment(sketch, "E4178", {"start": v(3.8, 2.63) * mm, "end": v(3.8, 2.64) * mm});
            skLineSegment(sketch, "E4179", {"start": v(3.8, 2.64) * mm, "end": v(3.8, 2.64) * mm});
            skLineSegment(sketch, "E4180", {"start": v(3.8, 2.64) * mm, "end": v(3.81, 2.64) * mm});
            skLineSegment(sketch, "E4181", {"start": v(3.81, 2.64) * mm, "end": v(3.82, 2.64) * mm});
            skLineSegment(sketch, "E4182", {"start": v(3.82, 2.64) * mm, "end": v(3.83, 2.64) * mm});
            skLineSegment(sketch, "E4183", {"start": v(3.83, 2.64) * mm, "end": v(3.83, 2.65) * mm});
            skLineSegment(sketch, "E4184", {"start": v(3.83, 2.65) * mm, "end": v(3.84, 2.65) * mm});
            skLineSegment(sketch, "E4185", {"start": v(3.84, 2.65) * mm, "end": v(3.84, 2.65) * mm});
            skLineSegment(sketch, "E4186", {"start": v(3.84, 2.65) * mm, "end": v(3.85, 2.65) * mm});
            skLineSegment(sketch, "E4187", {"start": v(3.85, 2.65) * mm, "end": v(3.85, 2.65) * mm});
            skLineSegment(sketch, "E4188", {"start": v(3.85, 2.65) * mm, "end": v(3.86, 2.65) * mm});
            skLineSegment(sketch, "E4189", {"start": v(3.86, 2.65) * mm, "end": v(3.86, 2.65) * mm});
            skLineSegment(sketch, "E4190", {"start": v(3.86, 2.65) * mm, "end": v(3.87, 2.65) * mm});
            skLineSegment(sketch, "E4191", {"start": v(3.87, 2.65) * mm, "end": v(3.87, 2.65) * mm});
            skLineSegment(sketch, "E4192", {"start": v(3.87, 2.65) * mm, "end": v(3.88, 2.65) * mm});
            skLineSegment(sketch, "E4193", {"start": v(3.88, 2.65) * mm, "end": v(3.88, 2.65) * mm});
            skLineSegment(sketch, "E4194", {"start": v(3.88, 2.65) * mm, "end": v(3.89, 2.65) * mm});
            skLineSegment(sketch, "E4195", {"start": v(3.89, 2.65) * mm, "end": v(3.9, 2.65) * mm});
            skLineSegment(sketch, "E4196", {"start": v(3.9, 2.65) * mm, "end": v(3.9, 2.65) * mm});
            skLineSegment(sketch, "E4197", {"start": v(3.9, 2.65) * mm, "end": v(3.9, 2.64) * mm});
            skLineSegment(sketch, "E4198", {"start": v(3.9, 2.64) * mm, "end": v(3.9, 2.64) * mm});
            skLineSegment(sketch, "E4199", {"start": v(3.9, 2.64) * mm, "end": v(3.91, 2.64) * mm});
            skLineSegment(sketch, "E4200", {"start": v(3.91, 2.64) * mm, "end": v(3.92, 2.64) * mm});
            skLineSegment(sketch, "E4201", {"start": v(3.92, 2.64) * mm, "end": v(3.92, 2.64) * mm});
            skLineSegment(sketch, "E4202", {"start": v(3.92, 2.64) * mm, "end": v(3.93, 2.64) * mm});
            skLineSegment(sketch, "E4203", {"start": v(3.93, 2.64) * mm, "end": v(3.93, 2.63) * mm});
            skLineSegment(sketch, "E4204", {"start": v(3.93, 2.63) * mm, "end": v(3.93, 2.63) * mm});
            skLineSegment(sketch, "E4205", {"start": v(3.93, 2.63) * mm, "end": v(3.94, 2.63) * mm});
            skLineSegment(sketch, "E4206", {"start": v(3.94, 2.63) * mm, "end": v(3.94, 2.63) * mm});
            skLineSegment(sketch, "E4207", {"start": v(3.94, 2.63) * mm, "end": v(3.94, 2.62) * mm});
            skLineSegment(sketch, "E4208", {"start": v(3.94, 2.62) * mm, "end": v(3.95, 2.62) * mm});
            skLineSegment(sketch, "E4209", {"start": v(3.95, 2.62) * mm, "end": v(3.95, 2.62) * mm});
            skLineSegment(sketch, "E4210", {"start": v(3.95, 2.62) * mm, "end": v(3.96, 2.61) * mm});
            skLineSegment(sketch, "E4211", {"start": v(3.96, 2.61) * mm, "end": v(3.96, 2.61) * mm});
            skLineSegment(sketch, "E4212", {"start": v(3.96, 2.61) * mm, "end": v(3.96, 2.6) * mm});
            skLineSegment(sketch, "E4213", {"start": v(3.96, 2.6) * mm, "end": v(3.96, 2.6) * mm});
            skLineSegment(sketch, "E4214", {"start": v(3.96, 2.6) * mm, "end": v(3.97, 2.6) * mm});
            skLineSegment(sketch, "E4215", {"start": v(3.97, 2.6) * mm, "end": v(3.97, 2.6) * mm});
            skLineSegment(sketch, "E4216", {"start": v(3.97, 2.6) * mm, "end": v(3.97, 2.59) * mm});
            skLineSegment(sketch, "E4217", {"start": v(3.97, 2.59) * mm, "end": v(3.97, 2.58) * mm});
            skLineSegment(sketch, "E4218", {"start": v(3.97, 2.58) * mm, "end": v(3.98, 2.58) * mm});
            skLineSegment(sketch, "E4219", {"start": v(3.98, 2.58) * mm, "end": v(3.98, 2.58) * mm});
            skLineSegment(sketch, "E4220", {"start": v(3.98, 2.58) * mm, "end": v(3.98, 2.57) * mm});
            skLineSegment(sketch, "E4221", {"start": v(3.98, 2.57) * mm, "end": v(3.98, 2.57) * mm});
            skLineSegment(sketch, "E4222", {"start": v(3.98, 2.57) * mm, "end": v(3.98, 2.56) * mm});
            skLineSegment(sketch, "E4223", {"start": v(3.98, 2.56) * mm, "end": v(3.98, 2.56) * mm});
            skLineSegment(sketch, "E4224", {"start": v(3.98, 2.56) * mm, "end": v(3.98, 2.55) * mm});
            skLineSegment(sketch, "E4225", {"start": v(3.98, 2.55) * mm, "end": v(3.98, 2.55) * mm});
            skLineSegment(sketch, "E4226", {"start": v(3.98, 2.55) * mm, "end": v(3.99, 2.54) * mm});
            skLineSegment(sketch, "E4227", {"start": v(3.99, 2.54) * mm, "end": v(3.99, 2.54) * mm});
            skLineSegment(sketch, "E4228", {"start": v(3.99, 2.54) * mm, "end": v(3.99, 2.53) * mm});
            skLineSegment(sketch, "E4229", {"start": v(3.99, 2.53) * mm, "end": v(3.99, 2.53) * mm});
            skLineSegment(sketch, "E4230", {"start": v(3.99, 2.53) * mm, "end": v(3.99, 2.52) * mm});
            skLineSegment(sketch, "E4231", {"start": v(3.99, 2.52) * mm, "end": v(3.99, 2.52) * mm});
            skLineSegment(sketch, "E4232", {"start": v(3.99, 2.52) * mm, "end": v(3.99, 2.51) * mm});
            skLineSegment(sketch, "E4233", {"start": v(3.99, 2.51) * mm, "end": v(3.99, 2.5) * mm});
            skLineSegment(sketch, "E4234", {"start": v(3.99, 2.5) * mm, "end": v(3.99, 2.5) * mm});
            skLineSegment(sketch, "E4235", {"start": v(3.99, 2.5) * mm, "end": v(3.99, 2.49) * mm});
            skLineSegment(sketch, "E4236", {"start": v(3.99, 2.49) * mm, "end": v(3.99, 2.46) * mm});
            skLineSegment(sketch, "E4237", {"start": v(3.99, 2.46) * mm, "end": v(3.99, 2.42) * mm});
            skLineSegment(sketch, "E4238", {"start": v(3.99, 2.42) * mm, "end": v(3.99, 2.38) * mm});
            skLineSegment(sketch, "E4239", {"start": v(3.99, 2.38) * mm, "end": v(3.99, 2.33) * mm});
            skLineSegment(sketch, "E4240", {"start": v(3.99, 2.33) * mm, "end": v(3.99, 2.26) * mm});
            skLineSegment(sketch, "E4241", {"start": v(3.99, 2.26) * mm, "end": v(3.99, 2.2) * mm});
            skLineSegment(sketch, "E4242", {"start": v(3.99, 2.2) * mm, "end": v(3.99, 2.11) * mm});
            skLineSegment(sketch, "E4243", {"start": v(3.99, 2.11) * mm, "end": v(3.99, 2.03) * mm});
            skLineSegment(sketch, "E4244", {"start": v(3.99, 2.03) * mm, "end": v(3.99, 1.94) * mm});
            skLineSegment(sketch, "E4245", {"start": v(3.99, 1.94) * mm, "end": v(3.99, 1.84) * mm});
            skLineSegment(sketch, "E4246", {"start": v(3.99, 1.84) * mm, "end": v(3.99, 1.74) * mm});
            skLineSegment(sketch, "E4247", {"start": v(3.99, 1.74) * mm, "end": v(3.99, 1.63) * mm});
            skLineSegment(sketch, "E4248", {"start": v(3.99, 1.63) * mm, "end": v(3.99, 1.52) * mm});
            skLineSegment(sketch, "E4249", {"start": v(3.99, 1.52) * mm, "end": v(3.99, 1.4) * mm});
            skLineSegment(sketch, "E4250", {"start": v(3.99, 1.4) * mm, "end": v(3.99, 1.28) * mm});
            skLineSegment(sketch, "E4251", {"start": v(3.99, 1.28) * mm, "end": v(3.99, 1.15) * mm});
            skLineSegment(sketch, "E4252", {"start": v(3.99, 1.15) * mm, "end": v(3.99, 1.02) * mm});
            skLineSegment(sketch, "E4253", {"start": v(3.99, 1.02) * mm, "end": v(3.99, 0.9) * mm});
            skLineSegment(sketch, "E4254", {"start": v(3.99, 0.9) * mm, "end": v(3.99, 0.76) * mm});
            skLineSegment(sketch, "E4255", {"start": v(3.99, 0.76) * mm, "end": v(3.99, 0.62) * mm});
            skLineSegment(sketch, "E4256", {"start": v(3.99, 0.62) * mm, "end": v(3.99, 0.49) * mm});
            skLineSegment(sketch, "E4257", {"start": v(3.99, 0.49) * mm, "end": v(3.99, 0.35) * mm});
            skLineSegment(sketch, "E4258", {"start": v(3.99, 0.35) * mm, "end": v(3.99, 0.21) * mm});
            skLineSegment(sketch, "E4259", {"start": v(3.99, 0.21) * mm, "end": v(3.99, 0.07) * mm});
            skLineSegment(sketch, "E4260", {"start": v(3.99, 0.07) * mm, "end": v(3.99, -0.06) * mm});
            skLineSegment(sketch, "E4261", {"start": v(3.99, -0.06) * mm, "end": v(3.99, -0.2) * mm});
            skLineSegment(sketch, "E4262", {"start": v(3.99, -0.2) * mm, "end": v(3.99, -0.34) * mm});
            skLineSegment(sketch, "E4263", {"start": v(3.99, -0.34) * mm, "end": v(3.99, -0.47) * mm});
            skLineSegment(sketch, "E4264", {"start": v(3.99, -0.47) * mm, "end": v(3.99, -0.6) * mm});
            skLineSegment(sketch, "E4265", {"start": v(3.99, -0.6) * mm, "end": v(3.99, -0.73) * mm});
            skLineSegment(sketch, "E4266", {"start": v(3.99, -0.73) * mm, "end": v(3.99, -0.85) * mm});
            skLineSegment(sketch, "E4267", {"start": v(3.99, -0.85) * mm, "end": v(3.99, -0.98) * mm});
            skLineSegment(sketch, "E4268", {"start": v(3.99, -0.98) * mm, "end": v(3.99, -1.1) * mm});
            skLineSegment(sketch, "E4269", {"start": v(3.99, -1.1) * mm, "end": v(3.99, -1.2) * mm});
            skLineSegment(sketch, "E4270", {"start": v(3.99, -1.2) * mm, "end": v(3.99, -1.32) * mm});
            skLineSegment(sketch, "E4271", {"start": v(3.99, -1.32) * mm, "end": v(3.99, -1.42) * mm});
            skLineSegment(sketch, "E4272", {"start": v(3.99, -1.42) * mm, "end": v(3.99, -1.52) * mm});
            skLineSegment(sketch, "E4273", {"start": v(3.99, -1.52) * mm, "end": v(3.99, -1.6) * mm});
            skLineSegment(sketch, "E4274", {"start": v(3.99, -1.6) * mm, "end": v(3.99, -1.7) * mm});
            skLineSegment(sketch, "E4275", {"start": v(3.99, -1.7) * mm, "end": v(3.99, -1.77) * mm});
            skLineSegment(sketch, "E4276", {"start": v(3.99, -1.77) * mm, "end": v(3.99, -1.84) * mm});
            skLineSegment(sketch, "E4277", {"start": v(3.99, -1.84) * mm, "end": v(3.99, -1.9) * mm});
            skLineSegment(sketch, "E4278", {"start": v(3.99, -1.9) * mm, "end": v(3.99, -1.96) * mm});
            skLineSegment(sketch, "E4279", {"start": v(3.99, -1.96) * mm, "end": v(3.99, -2) * mm});
            skLineSegment(sketch, "E4280", {"start": v(3.99, -2) * mm, "end": v(3.99, -2.04) * mm});
            skLineSegment(sketch, "E4281", {"start": v(3.99, -2.04) * mm, "end": v(3.99, -2.07) * mm});
            skLineSegment(sketch, "E4282", {"start": v(3.99, -2.07) * mm, "end": v(3.99, -2.08) * mm});
            skLineSegment(sketch, "E4283", {"start": v(3.99, -2.08) * mm, "end": v(3.99, -2.09) * mm});
            skLineSegment(sketch, "E4284", {"start": v(3.99, -2.09) * mm, "end": v(3.99, -2.11) * mm});
            skLineSegment(sketch, "E4285", {"start": v(3.99, -2.11) * mm, "end": v(3.99, -2.14) * mm});
            skLineSegment(sketch, "E4286", {"start": v(3.99, -2.14) * mm, "end": v(4, -2.16) * mm});
            skLineSegment(sketch, "E4287", {"start": v(4, -2.16) * mm, "end": v(4, -2.18) * mm});
            skLineSegment(sketch, "E4288", {"start": v(4, -2.18) * mm, "end": v(4, -2.2) * mm});
            skLineSegment(sketch, "E4289", {"start": v(4, -2.2) * mm, "end": v(4, -2.23) * mm});
            skLineSegment(sketch, "E4290", {"start": v(4, -2.23) * mm, "end": v(4, -2.25) * mm});
            skLineSegment(sketch, "E4291", {"start": v(4, -2.25) * mm, "end": v(4.01, -2.27) * mm});
            skLineSegment(sketch, "E4292", {"start": v(4.01, -2.27) * mm, "end": v(4.02, -2.3) * mm});
            skLineSegment(sketch, "E4293", {"start": v(4.02, -2.3) * mm, "end": v(4.02, -2.32) * mm});
            skLineSegment(sketch, "E4294", {"start": v(4.02, -2.32) * mm, "end": v(4.03, -2.34) * mm});
            skLineSegment(sketch, "E4295", {"start": v(4.03, -2.34) * mm, "end": v(4.04, -2.36) * mm});
            skLineSegment(sketch, "E4296", {"start": v(4.04, -2.36) * mm, "end": v(4.05, -2.37) * mm});
            skLineSegment(sketch, "E4297", {"start": v(4.05, -2.37) * mm, "end": v(4.06, -2.4) * mm});
            skLineSegment(sketch, "E4298", {"start": v(4.06, -2.4) * mm, "end": v(4.07, -2.41) * mm});
            skLineSegment(sketch, "E4299", {"start": v(4.07, -2.41) * mm, "end": v(4.08, -2.43) * mm});
            skLineSegment(sketch, "E4300", {"start": v(4.08, -2.43) * mm, "end": v(4.09, -2.45) * mm});
            skLineSegment(sketch, "E4301", {"start": v(4.09, -2.45) * mm, "end": v(4.1, -2.46) * mm});
            skLineSegment(sketch, "E4302", {"start": v(4.1, -2.46) * mm, "end": v(4.11, -2.48) * mm});
            skLineSegment(sketch, "E4303", {"start": v(4.11, -2.48) * mm, "end": v(4.12, -2.5) * mm});
            skLineSegment(sketch, "E4304", {"start": v(4.12, -2.5) * mm, "end": v(4.14, -2.51) * mm});
            skLineSegment(sketch, "E4305", {"start": v(4.14, -2.51) * mm, "end": v(4.15, -2.53) * mm});
            skLineSegment(sketch, "E4306", {"start": v(4.15, -2.53) * mm, "end": v(4.16, -2.54) * mm});
            skLineSegment(sketch, "E4307", {"start": v(4.16, -2.54) * mm, "end": v(4.18, -2.55) * mm});
            skLineSegment(sketch, "E4308", {"start": v(4.18, -2.55) * mm, "end": v(4.2, -2.57) * mm});
            skLineSegment(sketch, "E4309", {"start": v(4.2, -2.57) * mm, "end": v(4.2, -2.58) * mm});
            skLineSegment(sketch, "E4310", {"start": v(4.2, -2.58) * mm, "end": v(4.22, -2.6) * mm});
            skLineSegment(sketch, "E4311", {"start": v(4.22, -2.6) * mm, "end": v(4.24, -2.6) * mm});
            skLineSegment(sketch, "E4312", {"start": v(4.24, -2.6) * mm, "end": v(4.25, -2.61) * mm});
            skLineSegment(sketch, "E4313", {"start": v(4.25, -2.61) * mm, "end": v(4.27, -2.63) * mm});
            skLineSegment(sketch, "E4314", {"start": v(4.27, -2.63) * mm, "end": v(4.28, -2.64) * mm});
            skLineSegment(sketch, "E4315", {"start": v(4.28, -2.64) * mm, "end": v(4.3, -2.65) * mm});
            skLineSegment(sketch, "E4316", {"start": v(4.3, -2.65) * mm, "end": v(4.32, -2.66) * mm});
            skLineSegment(sketch, "E4317", {"start": v(4.32, -2.66) * mm, "end": v(4.33, -2.66) * mm});
            skLineSegment(sketch, "E4318", {"start": v(4.33, -2.66) * mm, "end": v(4.35, -2.67) * mm});
            skLineSegment(sketch, "E4319", {"start": v(4.35, -2.67) * mm, "end": v(4.37, -2.68) * mm});
            skLineSegment(sketch, "E4320", {"start": v(4.37, -2.68) * mm, "end": v(4.39, -2.69) * mm});
            skLineSegment(sketch, "E4321", {"start": v(4.39, -2.69) * mm, "end": v(4.4, -2.7) * mm});
            skLineSegment(sketch, "E4322", {"start": v(4.4, -2.7) * mm, "end": v(4.42, -2.7) * mm});
            skLineSegment(sketch, "E4323", {"start": v(4.42, -2.7) * mm, "end": v(4.44, -2.7) * mm});
            skLineSegment(sketch, "E4324", {"start": v(4.44, -2.7) * mm, "end": v(4.46, -2.71) * mm});
            skLineSegment(sketch, "E4325", {"start": v(4.46, -2.71) * mm, "end": v(4.48, -2.72) * mm});
            skLineSegment(sketch, "E4326", {"start": v(4.48, -2.72) * mm, "end": v(4.5, -2.73) * mm});
            skLineSegment(sketch, "E4327", {"start": v(4.5, -2.73) * mm, "end": v(4.51, -2.73) * mm});
            skLineSegment(sketch, "E4328", {"start": v(4.51, -2.73) * mm, "end": v(4.53, -2.73) * mm});
            skLineSegment(sketch, "E4329", {"start": v(4.53, -2.73) * mm, "end": v(4.55, -2.74) * mm});
            skLineSegment(sketch, "E4330", {"start": v(4.55, -2.74) * mm, "end": v(4.57, -2.74) * mm});
            skLineSegment(sketch, "E4331", {"start": v(4.57, -2.74) * mm, "end": v(4.59, -2.74) * mm});
            skLineSegment(sketch, "E4332", {"start": v(4.59, -2.74) * mm, "end": v(4.6, -2.74) * mm});
            skLineSegment(sketch, "E4333", {"start": v(4.6, -2.74) * mm, "end": v(4.62, -2.75) * mm});
            skLineSegment(sketch, "E4334", {"start": v(4.62, -2.75) * mm, "end": v(4.64, -2.74) * mm});
            skLineSegment(sketch, "E4335", {"start": v(4.64, -2.74) * mm, "end": v(4.66, -2.74) * mm});
            skLineSegment(sketch, "E4336", {"start": v(4.66, -2.74) * mm, "end": v(4.68, -2.74) * mm});
            skLineSegment(sketch, "E4337", {"start": v(4.68, -2.74) * mm, "end": v(4.7, -2.74) * mm});
            skLineSegment(sketch, "E4338", {"start": v(4.7, -2.74) * mm, "end": v(4.72, -2.73) * mm});
            skLineSegment(sketch, "E4339", {"start": v(4.72, -2.73) * mm, "end": v(4.74, -2.73) * mm});
            skLineSegment(sketch, "E4340", {"start": v(4.74, -2.73) * mm, "end": v(4.76, -2.73) * mm});
            skLineSegment(sketch, "E4341", {"start": v(4.76, -2.73) * mm, "end": v(4.78, -2.72) * mm});
            skLineSegment(sketch, "E4342", {"start": v(4.78, -2.72) * mm, "end": v(4.8, -2.71) * mm});
            skLineSegment(sketch, "E4343", {"start": v(4.8, -2.71) * mm, "end": v(4.82, -2.7) * mm});
            skLineSegment(sketch, "E4344", {"start": v(4.82, -2.7) * mm, "end": v(4.84, -2.7) * mm});
            skLineSegment(sketch, "E4345", {"start": v(4.84, -2.7) * mm, "end": v(4.85, -2.7) * mm});
            skLineSegment(sketch, "E4346", {"start": v(4.85, -2.7) * mm, "end": v(4.87, -2.69) * mm});
            skLineSegment(sketch, "E4347", {"start": v(4.87, -2.69) * mm, "end": v(4.89, -2.68) * mm});
            skLineSegment(sketch, "E4348", {"start": v(4.89, -2.68) * mm, "end": v(4.9, -2.67) * mm});
            skLineSegment(sketch, "E4349", {"start": v(4.9, -2.67) * mm, "end": v(4.92, -2.66) * mm});
            skLineSegment(sketch, "E4350", {"start": v(4.92, -2.66) * mm, "end": v(4.94, -2.66) * mm});
            skLineSegment(sketch, "E4351", {"start": v(4.94, -2.66) * mm, "end": v(4.96, -2.65) * mm});
            skLineSegment(sketch, "E4352", {"start": v(4.96, -2.65) * mm, "end": v(4.97, -2.64) * mm});
            skLineSegment(sketch, "E4353", {"start": v(4.97, -2.64) * mm, "end": v(5, -2.63) * mm});
            skLineSegment(sketch, "E4354", {"start": v(5, -2.63) * mm, "end": v(5, -2.61) * mm});
            skLineSegment(sketch, "E4355", {"start": v(5, -2.61) * mm, "end": v(5.02, -2.6) * mm});
            skLineSegment(sketch, "E4356", {"start": v(5.02, -2.6) * mm, "end": v(5.04, -2.6) * mm});
            skLineSegment(sketch, "E4357", {"start": v(5.04, -2.6) * mm, "end": v(5.05, -2.58) * mm});
            skLineSegment(sketch, "E4358", {"start": v(5.05, -2.58) * mm, "end": v(5.07, -2.57) * mm});
            skLineSegment(sketch, "E4359", {"start": v(5.07, -2.57) * mm, "end": v(5.08, -2.55) * mm});
            skLineSegment(sketch, "E4360", {"start": v(5.08, -2.55) * mm, "end": v(5.1, -2.54) * mm});
            skLineSegment(sketch, "E4361", {"start": v(5.1, -2.54) * mm, "end": v(5.1, -2.53) * mm});
            skLineSegment(sketch, "E4362", {"start": v(5.1, -2.53) * mm, "end": v(5.12, -2.51) * mm});
            skLineSegment(sketch, "E4363", {"start": v(5.12, -2.51) * mm, "end": v(5.13, -2.5) * mm});
            skLineSegment(sketch, "E4364", {"start": v(5.13, -2.5) * mm, "end": v(5.14, -2.48) * mm});
            skLineSegment(sketch, "E4365", {"start": v(5.14, -2.48) * mm, "end": v(5.15, -2.46) * mm});
            skLineSegment(sketch, "E4366", {"start": v(5.15, -2.46) * mm, "end": v(5.16, -2.45) * mm});
            skLineSegment(sketch, "E4367", {"start": v(5.16, -2.45) * mm, "end": v(5.18, -2.43) * mm});
            skLineSegment(sketch, "E4368", {"start": v(5.18, -2.43) * mm, "end": v(5.18, -2.41) * mm});
            skLineSegment(sketch, "E4369", {"start": v(5.18, -2.41) * mm, "end": v(5.2, -2.4) * mm});
            skLineSegment(sketch, "E4370", {"start": v(5.2, -2.4) * mm, "end": v(5.2, -2.37) * mm});
            skLineSegment(sketch, "E4371", {"start": v(5.2, -2.37) * mm, "end": v(5.21, -2.36) * mm});
            skLineSegment(sketch, "E4372", {"start": v(5.21, -2.36) * mm, "end": v(5.22, -2.34) * mm});
            skLineSegment(sketch, "E4373", {"start": v(5.22, -2.34) * mm, "end": v(5.23, -2.32) * mm});
            skLineSegment(sketch, "E4374", {"start": v(5.23, -2.32) * mm, "end": v(5.23, -2.3) * mm});
            skLineSegment(sketch, "E4375", {"start": v(5.23, -2.3) * mm, "end": v(5.24, -2.27) * mm});
            skLineSegment(sketch, "E4376", {"start": v(5.24, -2.27) * mm, "end": v(5.24, -2.25) * mm});
            skLineSegment(sketch, "E4377", {"start": v(5.24, -2.25) * mm, "end": v(5.25, -2.23) * mm});
            skLineSegment(sketch, "E4378", {"start": v(5.25, -2.23) * mm, "end": v(5.25, -2.2) * mm});
            skLineSegment(sketch, "E4379", {"start": v(5.25, -2.2) * mm, "end": v(5.25, -2.18) * mm});
            skLineSegment(sketch, "E4380", {"start": v(5.25, -2.18) * mm, "end": v(5.26, -2.16) * mm});
            skLineSegment(sketch, "E4381", {"start": v(5.26, -2.16) * mm, "end": v(5.26, -2.14) * mm});
            skLineSegment(sketch, "E4382", {"start": v(5.26, -2.14) * mm, "end": v(5.26, -2.11) * mm});
            skLineSegment(sketch, "E4383", {"start": v(5.26, -2.11) * mm, "end": v(5.26, -2.09) * mm});
            skLineSegment(sketch, "E4384", {"start": v(5.26, -2.09) * mm, "end": v(5.26, -2.08) * mm});
            skLineSegment(sketch, "E4385", {"start": v(5.26, -2.08) * mm, "end": v(5.26, -2.08) * mm});
            skLineSegment(sketch, "E4386", {"start": v(5.26, -2.08) * mm, "end": v(5.26, -2.07) * mm});
            skLineSegment(sketch, "E4387", {"start": v(5.26, -2.07) * mm, "end": v(5.26, -2.06) * mm});
            skLineSegment(sketch, "E4388", {"start": v(5.26, -2.06) * mm, "end": v(5.26, -2.05) * mm});
            skLineSegment(sketch, "E4389", {"start": v(5.26, -2.05) * mm, "end": v(5.26, -2.03) * mm});
            skLineSegment(sketch, "E4390", {"start": v(5.26, -2.03) * mm, "end": v(5.26, -2.01) * mm});
            skLineSegment(sketch, "E4391", {"start": v(5.26, -2.01) * mm, "end": v(5.26, -1.99) * mm});
            skLineSegment(sketch, "E4392", {"start": v(5.26, -1.99) * mm, "end": v(5.26, -1.97) * mm});
            skLineSegment(sketch, "E4393", {"start": v(5.26, -1.97) * mm, "end": v(5.26, -1.94) * mm});
            skLineSegment(sketch, "E4394", {"start": v(5.26, -1.94) * mm, "end": v(5.26, -1.91) * mm});
            skLineSegment(sketch, "E4395", {"start": v(5.26, -1.91) * mm, "end": v(5.26, -1.88) * mm});
            skLineSegment(sketch, "E4396", {"start": v(5.26, -1.88) * mm, "end": v(5.26, -1.85) * mm});
            skLineSegment(sketch, "E4397", {"start": v(5.26, -1.85) * mm, "end": v(5.26, -1.82) * mm});
            skLineSegment(sketch, "E4398", {"start": v(5.26, -1.82) * mm, "end": v(5.26, -1.78) * mm});
            skLineSegment(sketch, "E4399", {"start": v(5.26, -1.78) * mm, "end": v(5.26, -1.74) * mm});
            skLineSegment(sketch, "E4400", {"start": v(5.26, -1.74) * mm, "end": v(5.26, -1.7) * mm});
            skLineSegment(sketch, "E4401", {"start": v(5.26, -1.7) * mm, "end": v(5.26, -1.67) * mm});
            skLineSegment(sketch, "E4402", {"start": v(5.26, -1.67) * mm, "end": v(5.26, -1.63) * mm});
            skLineSegment(sketch, "E4403", {"start": v(5.26, -1.63) * mm, "end": v(5.26, -1.59) * mm});
            skLineSegment(sketch, "E4404", {"start": v(5.26, -1.59) * mm, "end": v(5.26, -1.55) * mm});
            skLineSegment(sketch, "E4405", {"start": v(5.26, -1.55) * mm, "end": v(5.26, -1.5) * mm});
            skLineSegment(sketch, "E4406", {"start": v(5.26, -1.5) * mm, "end": v(5.26, -1.46) * mm});
            skLineSegment(sketch, "E4407", {"start": v(5.26, -1.46) * mm, "end": v(5.26, -1.42) * mm});
            skLineSegment(sketch, "E4408", {"start": v(5.26, -1.42) * mm, "end": v(5.26, -1.38) * mm});
            skLineSegment(sketch, "E4409", {"start": v(5.26, -1.38) * mm, "end": v(5.26, -1.34) * mm});
            skLineSegment(sketch, "E4410", {"start": v(5.26, -1.34) * mm, "end": v(5.26, -1.3) * mm});
            skLineSegment(sketch, "E4411", {"start": v(5.26, -1.3) * mm, "end": v(5.26, -1.25) * mm});
            skLineSegment(sketch, "E4412", {"start": v(5.26, -1.25) * mm, "end": v(5.26, -1.21) * mm});
            skLineSegment(sketch, "E4413", {"start": v(5.26, -1.21) * mm, "end": v(5.26, -1.17) * mm});
            skLineSegment(sketch, "E4414", {"start": v(5.26, -1.17) * mm, "end": v(5.26, -1.13) * mm});
            skLineSegment(sketch, "E4415", {"start": v(5.26, -1.13) * mm, "end": v(5.26, -1.1) * mm});
            skLineSegment(sketch, "E4416", {"start": v(5.26, -1.1) * mm, "end": v(5.26, -1.05) * mm});
            skLineSegment(sketch, "E4417", {"start": v(5.26, -1.05) * mm, "end": v(5.26, -1.01) * mm});
            skLineSegment(sketch, "E4418", {"start": v(5.26, -1.01) * mm, "end": v(5.26, -0.98) * mm});
            skLineSegment(sketch, "E4419", {"start": v(5.26, -0.98) * mm, "end": v(5.26, -0.94) * mm});
            skLineSegment(sketch, "E4420", {"start": v(5.26, -0.94) * mm, "end": v(5.26, -0.9) * mm});
            skLineSegment(sketch, "E4421", {"start": v(5.26, -0.9) * mm, "end": v(5.26, -0.88) * mm});
            skLineSegment(sketch, "E4422", {"start": v(5.26, -0.88) * mm, "end": v(5.26, -0.85) * mm});
            skLineSegment(sketch, "E4423", {"start": v(5.26, -0.85) * mm, "end": v(5.26, -0.82) * mm});
            skLineSegment(sketch, "E4424", {"start": v(5.26, -0.82) * mm, "end": v(5.26, -0.8) * mm});
            skLineSegment(sketch, "E4425", {"start": v(5.26, -0.8) * mm, "end": v(5.26, -0.77) * mm});
            skLineSegment(sketch, "E4426", {"start": v(5.26, -0.77) * mm, "end": v(5.26, -0.75) * mm});
            skLineSegment(sketch, "E4427", {"start": v(5.26, -0.75) * mm, "end": v(5.26, -0.73) * mm});
            skLineSegment(sketch, "E4428", {"start": v(5.26, -0.73) * mm, "end": v(5.26, -0.71) * mm});
            skLineSegment(sketch, "E4429", {"start": v(5.26, -0.71) * mm, "end": v(5.26, -0.7) * mm});
            skLineSegment(sketch, "E4430", {"start": v(5.26, -0.7) * mm, "end": v(5.26, -0.69) * mm});
            skLineSegment(sketch, "E4431", {"start": v(5.26, -0.69) * mm, "end": v(5.26, -0.68) * mm});
            skLineSegment(sketch, "E4432", {"start": v(5.26, -0.68) * mm, "end": v(5.26, -0.67) * mm});
            skLineSegment(sketch, "E4433", {"start": v(5.26, -0.67) * mm, "end": v(5.26, -0.67) * mm});
            skLineSegment(sketch, "E4434", {"start": v(5.26, -0.67) * mm, "end": v(5.27, -0.67) * mm});
            skLineSegment(sketch, "E4435", {"start": v(5.27, -0.67) * mm, "end": v(5.28, -0.67) * mm});
            skLineSegment(sketch, "E4436", {"start": v(5.28, -0.67) * mm, "end": v(5.3, -0.67) * mm});
            skLineSegment(sketch, "E4437", {"start": v(5.3, -0.67) * mm, "end": v(5.3, -0.67) * mm});
            skLineSegment(sketch, "E4438", {"start": v(5.3, -0.67) * mm, "end": v(5.33, -0.67) * mm});
            skLineSegment(sketch, "E4439", {"start": v(5.33, -0.67) * mm, "end": v(5.35, -0.67) * mm});
            skLineSegment(sketch, "E4440", {"start": v(5.35, -0.67) * mm, "end": v(5.38, -0.67) * mm});
            skLineSegment(sketch, "E4441", {"start": v(5.38, -0.67) * mm, "end": v(5.4, -0.67) * mm});
            skLineSegment(sketch, "E4442", {"start": v(5.4, -0.67) * mm, "end": v(5.44, -0.67) * mm});
            skLineSegment(sketch, "E4443", {"start": v(5.44, -0.67) * mm, "end": v(5.47, -0.67) * mm});
            skLineSegment(sketch, "E4444", {"start": v(5.47, -0.67) * mm, "end": v(5.5, -0.67) * mm});
            skLineSegment(sketch, "E4445", {"start": v(5.5, -0.67) * mm, "end": v(5.54, -0.67) * mm});
            skLineSegment(sketch, "E4446", {"start": v(5.54, -0.67) * mm, "end": v(5.58, -0.67) * mm});
            skLineSegment(sketch, "E4447", {"start": v(5.58, -0.67) * mm, "end": v(5.63, -0.67) * mm});
            skLineSegment(sketch, "E4448", {"start": v(5.63, -0.67) * mm, "end": v(5.67, -0.67) * mm});
            skLineSegment(sketch, "E4449", {"start": v(5.67, -0.67) * mm, "end": v(5.71, -0.67) * mm});
            skLineSegment(sketch, "E4450", {"start": v(5.71, -0.67) * mm, "end": v(5.76, -0.67) * mm});
            skLineSegment(sketch, "E4451", {"start": v(5.76, -0.67) * mm, "end": v(5.8, -0.67) * mm});
            skLineSegment(sketch, "E4452", {"start": v(5.8, -0.67) * mm, "end": v(5.86, -0.67) * mm});
            skLineSegment(sketch, "E4453", {"start": v(5.86, -0.67) * mm, "end": v(5.9, -0.67) * mm});
            skLineSegment(sketch, "E4454", {"start": v(5.9, -0.67) * mm, "end": v(5.96, -0.67) * mm});
            skLineSegment(sketch, "E4455", {"start": v(5.96, -0.67) * mm, "end": v(6, -0.67) * mm});
            skLineSegment(sketch, "E4456", {"start": v(6, -0.67) * mm, "end": v(6.06, -0.67) * mm});
            skLineSegment(sketch, "E4457", {"start": v(6.06, -0.67) * mm, "end": v(6.1, -0.67) * mm});
            skLineSegment(sketch, "E4458", {"start": v(6.1, -0.67) * mm, "end": v(6.16, -0.67) * mm});
            skLineSegment(sketch, "E4459", {"start": v(6.16, -0.67) * mm, "end": v(6.2, -0.67) * mm});
            skLineSegment(sketch, "E4460", {"start": v(6.2, -0.67) * mm, "end": v(6.26, -0.67) * mm});
            skLineSegment(sketch, "E4461", {"start": v(6.26, -0.67) * mm, "end": v(6.31, -0.67) * mm});
            skLineSegment(sketch, "E4462", {"start": v(6.31, -0.67) * mm, "end": v(6.36, -0.67) * mm});
            skLineSegment(sketch, "E4463", {"start": v(6.36, -0.67) * mm, "end": v(6.4, -0.67) * mm});
            skLineSegment(sketch, "E4464", {"start": v(6.4, -0.67) * mm, "end": v(6.46, -0.67) * mm});
            skLineSegment(sketch, "E4465", {"start": v(6.46, -0.67) * mm, "end": v(6.5, -0.67) * mm});
            skLineSegment(sketch, "E4466", {"start": v(6.5, -0.67) * mm, "end": v(6.55, -0.67) * mm});
            skLineSegment(sketch, "E4467", {"start": v(6.55, -0.67) * mm, "end": v(6.59, -0.67) * mm});
            skLineSegment(sketch, "E4468", {"start": v(6.59, -0.67) * mm, "end": v(6.63, -0.67) * mm});
            skLineSegment(sketch, "E4469", {"start": v(6.63, -0.67) * mm, "end": v(6.67, -0.67) * mm});
            skLineSegment(sketch, "E4470", {"start": v(6.67, -0.67) * mm, "end": v(6.71, -0.67) * mm});
            skLineSegment(sketch, "E4471", {"start": v(6.71, -0.67) * mm, "end": v(6.75, -0.67) * mm});
            skLineSegment(sketch, "E4472", {"start": v(6.75, -0.67) * mm, "end": v(6.78, -0.67) * mm});
            skLineSegment(sketch, "E4473", {"start": v(6.78, -0.67) * mm, "end": v(6.81, -0.67) * mm});
            skLineSegment(sketch, "E4474", {"start": v(6.81, -0.67) * mm, "end": v(6.84, -0.67) * mm});
            skLineSegment(sketch, "E4475", {"start": v(6.84, -0.67) * mm, "end": v(6.87, -0.67) * mm});
            skLineSegment(sketch, "E4476", {"start": v(6.87, -0.67) * mm, "end": v(6.89, -0.67) * mm});
            skLineSegment(sketch, "E4477", {"start": v(6.89, -0.67) * mm, "end": v(6.9, -0.67) * mm});
            skLineSegment(sketch, "E4478", {"start": v(6.9, -0.67) * mm, "end": v(6.93, -0.67) * mm});
            skLineSegment(sketch, "E4479", {"start": v(6.93, -0.67) * mm, "end": v(6.94, -0.67) * mm});
            skLineSegment(sketch, "E4480", {"start": v(6.94, -0.67) * mm, "end": v(6.95, -0.67) * mm});
            skLineSegment(sketch, "E4481", {"start": v(6.95, -0.67) * mm, "end": v(6.95, -0.67) * mm});
            skLineSegment(sketch, "E4482", {"start": v(6.95, -0.67) * mm, "end": v(6.96, -0.67) * mm});
            skLineSegment(sketch, "E4483", {"start": v(6.96, -0.67) * mm, "end": v(6.98, -0.67) * mm});
            skLineSegment(sketch, "E4484", {"start": v(6.98, -0.67) * mm, "end": v(7.01, -0.67) * mm});
            skLineSegment(sketch, "E4485", {"start": v(7.01, -0.67) * mm, "end": v(7.04, -0.67) * mm});
            skLineSegment(sketch, "E4486", {"start": v(7.04, -0.67) * mm, "end": v(7.07, -0.67) * mm});
            skLineSegment(sketch, "E4487", {"start": v(7.07, -0.67) * mm, "end": v(7.1, -0.66) * mm});
            skLineSegment(sketch, "E4488", {"start": v(7.1, -0.66) * mm, "end": v(7.12, -0.66) * mm});
            skLineSegment(sketch, "E4489", {"start": v(7.12, -0.66) * mm, "end": v(7.14, -0.65) * mm});
            skLineSegment(sketch, "E4490", {"start": v(7.14, -0.65) * mm, "end": v(7.17, -0.65) * mm});
            skLineSegment(sketch, "E4491", {"start": v(7.17, -0.65) * mm, "end": v(7.19, -0.64) * mm});
            skLineSegment(sketch, "E4492", {"start": v(7.19, -0.64) * mm, "end": v(7.21, -0.64) * mm});
            skLineSegment(sketch, "E4493", {"start": v(7.21, -0.64) * mm, "end": v(7.24, -0.63) * mm});
            skLineSegment(sketch, "E4494", {"start": v(7.24, -0.63) * mm, "end": v(7.26, -0.62) * mm});
            skLineSegment(sketch, "E4495", {"start": v(7.26, -0.62) * mm, "end": v(7.28, -0.61) * mm});
            skLineSegment(sketch, "E4496", {"start": v(7.28, -0.61) * mm, "end": v(7.3, -0.6) * mm});
            skLineSegment(sketch, "E4497", {"start": v(7.3, -0.6) * mm, "end": v(7.32, -0.6) * mm});
            skLineSegment(sketch, "E4498", {"start": v(7.32, -0.6) * mm, "end": v(7.34, -0.58) * mm});
            skLineSegment(sketch, "E4499", {"start": v(7.34, -0.58) * mm, "end": v(7.36, -0.57) * mm});
            skLineSegment(sketch, "E4500", {"start": v(7.36, -0.57) * mm, "end": v(7.38, -0.56) * mm});
            skLineSegment(sketch, "E4501", {"start": v(7.38, -0.56) * mm, "end": v(7.4, -0.55) * mm});
            skLineSegment(sketch, "E4502", {"start": v(7.4, -0.55) * mm, "end": v(7.42, -0.54) * mm});
            skLineSegment(sketch, "E4503", {"start": v(7.42, -0.54) * mm, "end": v(7.43, -0.52) * mm});
            skLineSegment(sketch, "E4504", {"start": v(7.43, -0.52) * mm, "end": v(7.45, -0.5) * mm});
            skLineSegment(sketch, "E4505", {"start": v(7.45, -0.5) * mm, "end": v(7.47, -0.5) * mm});
            skLineSegment(sketch, "E4506", {"start": v(7.47, -0.5) * mm, "end": v(7.48, -0.48) * mm});
            skLineSegment(sketch, "E4507", {"start": v(7.48, -0.48) * mm, "end": v(7.5, -0.47) * mm});
            skLineSegment(sketch, "E4508", {"start": v(7.5, -0.47) * mm, "end": v(7.51, -0.45) * mm});
            skLineSegment(sketch, "E4509", {"start": v(7.51, -0.45) * mm, "end": v(7.53, -0.44) * mm});
            skLineSegment(sketch, "E4510", {"start": v(7.53, -0.44) * mm, "end": v(7.54, -0.42) * mm});
            skLineSegment(sketch, "E4511", {"start": v(7.54, -0.42) * mm, "end": v(7.55, -0.4) * mm});
            skLineSegment(sketch, "E4512", {"start": v(7.55, -0.4) * mm, "end": v(7.57, -0.39) * mm});
            skLineSegment(sketch, "E4513", {"start": v(7.57, -0.39) * mm, "end": v(7.58, -0.37) * mm});
            skLineSegment(sketch, "E4514", {"start": v(7.58, -0.37) * mm, "end": v(7.59, -0.35) * mm});
            skLineSegment(sketch, "E4515", {"start": v(7.59, -0.35) * mm, "end": v(7.6, -0.34) * mm});
            skLineSegment(sketch, "E4516", {"start": v(7.6, -0.34) * mm, "end": v(7.6, -0.32) * mm});
            skLineSegment(sketch, "E4517", {"start": v(7.6, -0.32) * mm, "end": v(7.62, -0.3) * mm});
            skLineSegment(sketch, "E4518", {"start": v(7.62, -0.3) * mm, "end": v(7.63, -0.28) * mm});
            skLineSegment(sketch, "E4519", {"start": v(7.63, -0.28) * mm, "end": v(7.64, -0.26) * mm});
            skLineSegment(sketch, "E4520", {"start": v(7.64, -0.26) * mm, "end": v(7.64, -0.25) * mm});
            skLineSegment(sketch, "E4521", {"start": v(7.64, -0.25) * mm, "end": v(7.65, -0.23) * mm});
            skLineSegment(sketch, "E4522", {"start": v(7.65, -0.23) * mm, "end": v(7.66, -0.2) * mm});
            skLineSegment(sketch, "E4523", {"start": v(7.66, -0.2) * mm, "end": v(7.66, -0.19) * mm});
            skLineSegment(sketch, "E4524", {"start": v(7.66, -0.19) * mm, "end": v(7.67, -0.17) * mm});
            skLineSegment(sketch, "E4525", {"start": v(7.67, -0.17) * mm, "end": v(7.67, -0.15) * mm});
            skLineSegment(sketch, "E4526", {"start": v(7.67, -0.15) * mm, "end": v(7.68, -0.13) * mm});
            skLineSegment(sketch, "E4527", {"start": v(7.68, -0.13) * mm, "end": v(7.68, -0.11) * mm});
            skLineSegment(sketch, "E4528", {"start": v(7.68, -0.11) * mm, "end": v(7.68, -0.1) * mm});
            skLineSegment(sketch, "E4529", {"start": v(7.68, -0.1) * mm, "end": v(7.68, -0.07) * mm});
            skLineSegment(sketch, "E4530", {"start": v(7.68, -0.07) * mm, "end": v(7.69, -0.05) * mm});
            skLineSegment(sketch, "E4531", {"start": v(7.69, -0.05) * mm, "end": v(7.69, -0.03) * mm});
            skLineSegment(sketch, "E4532", {"start": v(7.69, -0.03) * mm, "end": v(7.69, -0.01) * mm});
            skLineSegment(sketch, "E4533", {"start": v(7.69, -0.01) * mm, "end": v(7.69, 0) * mm});
            skLineSegment(sketch, "E4534", {"start": v(7.69, 0) * mm, "end": v(7.69, 0.02) * mm});
            skLineSegment(sketch, "E4535", {"start": v(7.69, 0.02) * mm, "end": v(7.68, 0.04) * mm});
            skLineSegment(sketch, "E4536", {"start": v(7.68, 0.04) * mm, "end": v(7.68, 0.06) * mm});
            skLineSegment(sketch, "E4537", {"start": v(7.68, 0.06) * mm, "end": v(7.68, 0.08) * mm});
            skLineSegment(sketch, "E4538", {"start": v(7.68, 0.08) * mm, "end": v(7.68, 0.1) * mm});
            skLineSegment(sketch, "E4539", {"start": v(7.68, 0.1) * mm, "end": v(7.67, 0.11) * mm});
            skLineSegment(sketch, "E4540", {"start": v(7.67, 0.11) * mm, "end": v(7.67, 0.13) * mm});
            skLineSegment(sketch, "E4541", {"start": v(7.67, 0.13) * mm, "end": v(7.67, 0.15) * mm});
            skLineSegment(sketch, "E4542", {"start": v(7.67, 0.15) * mm, "end": v(7.66, 0.17) * mm});
            skLineSegment(sketch, "E4543", {"start": v(7.66, 0.17) * mm, "end": v(7.66, 0.19) * mm});
            skLineSegment(sketch, "E4544", {"start": v(7.66, 0.19) * mm, "end": v(7.65, 0.2) * mm});
            skLineSegment(sketch, "E4545", {"start": v(7.65, 0.2) * mm, "end": v(7.64, 0.22) * mm});
            skLineSegment(sketch, "E4546", {"start": v(7.64, 0.22) * mm, "end": v(7.64, 0.24) * mm});
            skLineSegment(sketch, "E4547", {"start": v(7.64, 0.24) * mm, "end": v(7.63, 0.25) * mm});
            skLineSegment(sketch, "E4548", {"start": v(7.63, 0.25) * mm, "end": v(7.62, 0.27) * mm});
            skLineSegment(sketch, "E4549", {"start": v(7.62, 0.27) * mm, "end": v(7.61, 0.29) * mm});
            skLineSegment(sketch, "E4550", {"start": v(7.61, 0.29) * mm, "end": v(7.6, 0.3) * mm});
            skLineSegment(sketch, "E4551", {"start": v(7.6, 0.3) * mm, "end": v(7.6, 0.32) * mm});
            skLineSegment(sketch, "E4552", {"start": v(7.6, 0.32) * mm, "end": v(7.58, 0.33) * mm});
            skLineSegment(sketch, "E4553", {"start": v(7.58, 0.33) * mm, "end": v(7.57, 0.35) * mm});
            skLineSegment(sketch, "E4554", {"start": v(7.57, 0.35) * mm, "end": v(7.56, 0.37) * mm});
            skLineSegment(sketch, "E4555", {"start": v(7.56, 0.37) * mm, "end": v(7.55, 0.38) * mm});
            skLineSegment(sketch, "E4556", {"start": v(7.55, 0.38) * mm, "end": v(7.54, 0.4) * mm});
            skLineSegment(sketch, "E4557", {"start": v(7.54, 0.4) * mm, "end": v(7.52, 0.4) * mm});
            skLineSegment(sketch, "E4558", {"start": v(7.52, 0.4) * mm, "end": v(7.51, 0.42) * mm});
            skLineSegment(sketch, "E4559", {"start": v(7.51, 0.42) * mm, "end": v(7.5, 0.43) * mm});
            skLineSegment(sketch, "E4560", {"start": v(7.5, 0.43) * mm, "end": v(7.48, 0.45) * mm});
            skLineSegment(sketch, "E4561", {"start": v(7.48, 0.45) * mm, "end": v(7.47, 0.46) * mm});
            skLineSegment(sketch, "E4562", {"start": v(7.47, 0.46) * mm, "end": v(7.45, 0.47) * mm});
            skLineSegment(sketch, "E4563", {"start": v(7.45, 0.47) * mm, "end": v(7.44, 0.48) * mm});
            skLineSegment(sketch, "E4564", {"start": v(7.44, 0.48) * mm, "end": v(7.42, 0.5) * mm});
            skLineSegment(sketch, "E4565", {"start": v(7.42, 0.5) * mm, "end": v(7.4, 0.5) * mm});
            skLineSegment(sketch, "E4566", {"start": v(7.4, 0.5) * mm, "end": v(7.39, 0.52) * mm});
            skLineSegment(sketch, "E4567", {"start": v(7.39, 0.52) * mm, "end": v(7.37, 0.52) * mm});
            skLineSegment(sketch, "E4568", {"start": v(7.37, 0.52) * mm, "end": v(7.35, 0.53) * mm});
            skLineSegment(sketch, "E4569", {"start": v(7.35, 0.53) * mm, "end": v(7.33, 0.54) * mm});
            skLineSegment(sketch, "E4570", {"start": v(7.33, 0.54) * mm, "end": v(7.3, 0.55) * mm});
            skLineSegment(sketch, "E4571", {"start": v(7.3, 0.55) * mm, "end": v(7.29, 0.56) * mm});
            skLineSegment(sketch, "E4572", {"start": v(7.29, 0.56) * mm, "end": v(7.27, 0.57) * mm});
            skLineSegment(sketch, "E4573", {"start": v(7.27, 0.57) * mm, "end": v(7.25, 0.57) * mm});
            skLineSegment(sketch, "E4574", {"start": v(7.25, 0.57) * mm, "end": v(7.22, 0.58) * mm});
            skLineSegment(sketch, "E4575", {"start": v(7.22, 0.58) * mm, "end": v(7.2, 0.58) * mm});
            skLineSegment(sketch, "E4576", {"start": v(7.2, 0.58) * mm, "end": v(7.18, 0.59) * mm});
            skLineSegment(sketch, "E4577", {"start": v(7.18, 0.59) * mm, "end": v(7.15, 0.6) * mm});
            skLineSegment(sketch, "E4578", {"start": v(7.15, 0.6) * mm, "end": v(7.13, 0.6) * mm});
            skLineSegment(sketch, "E4579", {"start": v(7.13, 0.6) * mm, "end": v(7.1, 0.6) * mm});
            skLineSegment(sketch, "E4580", {"start": v(7.1, 0.6) * mm, "end": v(7.08, 0.6) * mm});
            skLineSegment(sketch, "E4581", {"start": v(7.08, 0.6) * mm, "end": v(7.05, 0.6) * mm});
            skLineSegment(sketch, "E4582", {"start": v(7.05, 0.6) * mm, "end": v(7.03, 0.6) * mm});
            skLineSegment(sketch, "E4583", {"start": v(7.03, 0.6) * mm, "end": v(7.02, 0.6) * mm});
            skLineSegment(sketch, "E4584", {"start": v(7.02, 0.6) * mm, "end": v(7.02, 0.6) * mm});
            skLineSegment(sketch, "E4585", {"start": v(7.02, 0.6) * mm, "end": v(7, 0.6) * mm});
            skLineSegment(sketch, "E4586", {"start": v(7, 0.6) * mm, "end": v(7, 0.6) * mm});
            skLineSegment(sketch, "E4587", {"start": v(7, 0.6) * mm, "end": v(6.98, 0.6) * mm});
            skLineSegment(sketch, "E4588", {"start": v(6.98, 0.6) * mm, "end": v(6.96, 0.6) * mm});
            skLineSegment(sketch, "E4589", {"start": v(6.96, 0.6) * mm, "end": v(6.93, 0.6) * mm});
            skLineSegment(sketch, "E4590", {"start": v(6.93, 0.6) * mm, "end": v(6.9, 0.6) * mm});
            skLineSegment(sketch, "E4591", {"start": v(6.9, 0.6) * mm, "end": v(6.88, 0.6) * mm});
            skLineSegment(sketch, "E4592", {"start": v(6.88, 0.6) * mm, "end": v(6.84, 0.6) * mm});
            skLineSegment(sketch, "E4593", {"start": v(6.84, 0.6) * mm, "end": v(6.8, 0.6) * mm});
            skLineSegment(sketch, "E4594", {"start": v(6.8, 0.6) * mm, "end": v(6.77, 0.6) * mm});
            skLineSegment(sketch, "E4595", {"start": v(6.77, 0.6) * mm, "end": v(6.73, 0.6) * mm});
            skLineSegment(sketch, "E4596", {"start": v(6.73, 0.6) * mm, "end": v(6.69, 0.6) * mm});
            skLineSegment(sketch, "E4597", {"start": v(6.69, 0.6) * mm, "end": v(6.65, 0.6) * mm});
            skLineSegment(sketch, "E4598", {"start": v(6.65, 0.6) * mm, "end": v(6.6, 0.6) * mm});
            skLineSegment(sketch, "E4599", {"start": v(6.6, 0.6) * mm, "end": v(6.55, 0.6) * mm});
            skLineSegment(sketch, "E4600", {"start": v(6.55, 0.6) * mm, "end": v(6.5, 0.6) * mm});
            skLineSegment(sketch, "E4601", {"start": v(6.5, 0.6) * mm, "end": v(6.46, 0.6) * mm});
            skLineSegment(sketch, "E4602", {"start": v(6.46, 0.6) * mm, "end": v(6.4, 0.6) * mm});
            skLineSegment(sketch, "E4603", {"start": v(6.4, 0.6) * mm, "end": v(6.35, 0.6) * mm});
            skLineSegment(sketch, "E4604", {"start": v(6.35, 0.6) * mm, "end": v(6.3, 0.6) * mm});
            skLineSegment(sketch, "E4605", {"start": v(6.3, 0.6) * mm, "end": v(6.25, 0.6) * mm});
            skLineSegment(sketch, "E4606", {"start": v(6.25, 0.6) * mm, "end": v(6.2, 0.6) * mm});
            skLineSegment(sketch, "E4607", {"start": v(6.2, 0.6) * mm, "end": v(6.14, 0.6) * mm});
            skLineSegment(sketch, "E4608", {"start": v(6.14, 0.6) * mm, "end": v(6.1, 0.6) * mm});
            skLineSegment(sketch, "E4609", {"start": v(6.1, 0.6) * mm, "end": v(6.04, 0.6) * mm});
            skLineSegment(sketch, "E4610", {"start": v(6.04, 0.6) * mm, "end": v(5.99, 0.6) * mm});
            skLineSegment(sketch, "E4611", {"start": v(5.99, 0.6) * mm, "end": v(5.93, 0.6) * mm});
            skLineSegment(sketch, "E4612", {"start": v(5.93, 0.6) * mm, "end": v(5.88, 0.6) * mm});
            skLineSegment(sketch, "E4613", {"start": v(5.88, 0.6) * mm, "end": v(5.83, 0.6) * mm});
            skLineSegment(sketch, "E4614", {"start": v(5.83, 0.6) * mm, "end": v(5.78, 0.6) * mm});
            skLineSegment(sketch, "E4615", {"start": v(5.78, 0.6) * mm, "end": v(5.73, 0.6) * mm});
            skLineSegment(sketch, "E4616", {"start": v(5.73, 0.6) * mm, "end": v(5.69, 0.6) * mm});
            skLineSegment(sketch, "E4617", {"start": v(5.69, 0.6) * mm, "end": v(5.64, 0.6) * mm});
            skLineSegment(sketch, "E4618", {"start": v(5.64, 0.6) * mm, "end": v(5.6, 0.6) * mm});
            skLineSegment(sketch, "E4619", {"start": v(5.6, 0.6) * mm, "end": v(5.56, 0.6) * mm});
            skLineSegment(sketch, "E4620", {"start": v(5.56, 0.6) * mm, "end": v(5.52, 0.6) * mm});
            skLineSegment(sketch, "E4621", {"start": v(5.52, 0.6) * mm, "end": v(5.48, 0.6) * mm});
            skLineSegment(sketch, "E4622", {"start": v(5.48, 0.6) * mm, "end": v(5.44, 0.6) * mm});
            skLineSegment(sketch, "E4623", {"start": v(5.44, 0.6) * mm, "end": v(5.41, 0.6) * mm});
            skLineSegment(sketch, "E4624", {"start": v(5.41, 0.6) * mm, "end": v(5.38, 0.6) * mm});
            skLineSegment(sketch, "E4625", {"start": v(5.38, 0.6) * mm, "end": v(5.35, 0.6) * mm});
            skLineSegment(sketch, "E4626", {"start": v(5.35, 0.6) * mm, "end": v(5.33, 0.6) * mm});
            skLineSegment(sketch, "E4627", {"start": v(5.33, 0.6) * mm, "end": v(5.3, 0.6) * mm});
            skLineSegment(sketch, "E4628", {"start": v(5.3, 0.6) * mm, "end": v(5.3, 0.6) * mm});
            skLineSegment(sketch, "E4629", {"start": v(5.3, 0.6) * mm, "end": v(5.28, 0.6) * mm});
            skLineSegment(sketch, "E4630", {"start": v(5.28, 0.6) * mm, "end": v(5.27, 0.6) * mm});
            skLineSegment(sketch, "E4631", {"start": v(5.27, 0.6) * mm, "end": v(5.26, 0.6) * mm});
            skLineSegment(sketch, "E4632", {"start": v(5.26, 0.6) * mm, "end": v(5.26, 0.6) * mm});
            skLineSegment(sketch, "E4633", {"start": v(5.26, 0.6) * mm, "end": v(5.26, 0.61) * mm});
            skLineSegment(sketch, "E4634", {"start": v(5.26, 0.61) * mm, "end": v(5.26, 0.62) * mm});
            skLineSegment(sketch, "E4635", {"start": v(5.26, 0.62) * mm, "end": v(5.26, 0.63) * mm});
            skLineSegment(sketch, "E4636", {"start": v(5.26, 0.63) * mm, "end": v(5.26, 0.65) * mm});
            skLineSegment(sketch, "E4637", {"start": v(5.26, 0.65) * mm, "end": v(5.26, 0.66) * mm});
            skLineSegment(sketch, "E4638", {"start": v(5.26, 0.66) * mm, "end": v(5.26, 0.68) * mm});
            skLineSegment(sketch, "E4639", {"start": v(5.26, 0.68) * mm, "end": v(5.26, 0.7) * mm});
            skLineSegment(sketch, "E4640", {"start": v(5.26, 0.7) * mm, "end": v(5.26, 0.72) * mm});
            skLineSegment(sketch, "E4641", {"start": v(5.26, 0.72) * mm, "end": v(5.26, 0.75) * mm});
            skLineSegment(sketch, "E4642", {"start": v(5.26, 0.75) * mm, "end": v(5.26, 0.77) * mm});
            skLineSegment(sketch, "E4643", {"start": v(5.26, 0.77) * mm, "end": v(5.26, 0.8) * mm});
            skLineSegment(sketch, "E4644", {"start": v(5.26, 0.8) * mm, "end": v(5.26, 0.83) * mm});
            skLineSegment(sketch, "E4645", {"start": v(5.26, 0.83) * mm, "end": v(5.26, 0.86) * mm});
            skLineSegment(sketch, "E4646", {"start": v(5.26, 0.86) * mm, "end": v(5.26, 0.89) * mm});
            skLineSegment(sketch, "E4647", {"start": v(5.26, 0.89) * mm, "end": v(5.26, 0.92) * mm});
            skLineSegment(sketch, "E4648", {"start": v(5.26, 0.92) * mm, "end": v(5.26, 0.95) * mm});
            skLineSegment(sketch, "E4649", {"start": v(5.26, 0.95) * mm, "end": v(5.26, 0.99) * mm});
            skLineSegment(sketch, "E4650", {"start": v(5.26, 0.99) * mm, "end": v(5.26, 1.02) * mm});
            skLineSegment(sketch, "E4651", {"start": v(5.26, 1.02) * mm, "end": v(5.26, 1.06) * mm});
            skLineSegment(sketch, "E4652", {"start": v(5.26, 1.06) * mm, "end": v(5.26, 1.1) * mm});
            skLineSegment(sketch, "E4653", {"start": v(5.26, 1.1) * mm, "end": v(5.26, 1.13) * mm});
            skLineSegment(sketch, "E4654", {"start": v(5.26, 1.13) * mm, "end": v(5.26, 1.16) * mm});
            skLineSegment(sketch, "E4655", {"start": v(5.26, 1.16) * mm, "end": v(5.26, 1.2) * mm});
            skLineSegment(sketch, "E4656", {"start": v(5.26, 1.2) * mm, "end": v(5.26, 1.24) * mm});
            skLineSegment(sketch, "E4657", {"start": v(5.26, 1.24) * mm, "end": v(5.26, 1.27) * mm});
            skLineSegment(sketch, "E4658", {"start": v(5.26, 1.27) * mm, "end": v(5.26, 1.3) * mm});
            skLineSegment(sketch, "E4659", {"start": v(5.26, 1.3) * mm, "end": v(5.26, 1.34) * mm});
            skLineSegment(sketch, "E4660", {"start": v(5.26, 1.34) * mm, "end": v(5.26, 1.38) * mm});
            skLineSegment(sketch, "E4661", {"start": v(5.26, 1.38) * mm, "end": v(5.26, 1.41) * mm});
            skLineSegment(sketch, "E4662", {"start": v(5.26, 1.41) * mm, "end": v(5.26, 1.45) * mm});
            skLineSegment(sketch, "E4663", {"start": v(5.26, 1.45) * mm, "end": v(5.26, 1.48) * mm});
            skLineSegment(sketch, "E4664", {"start": v(5.26, 1.48) * mm, "end": v(5.26, 1.51) * mm});
            skLineSegment(sketch, "E4665", {"start": v(5.26, 1.51) * mm, "end": v(5.26, 1.54) * mm});
            skLineSegment(sketch, "E4666", {"start": v(5.26, 1.54) * mm, "end": v(5.26, 1.57) * mm});
            skLineSegment(sketch, "E4667", {"start": v(5.26, 1.57) * mm, "end": v(5.26, 1.6) * mm});
            skLineSegment(sketch, "E4668", {"start": v(5.26, 1.6) * mm, "end": v(5.26, 1.63) * mm});
            skLineSegment(sketch, "E4669", {"start": v(5.26, 1.63) * mm, "end": v(5.26, 1.65) * mm});
            skLineSegment(sketch, "E4670", {"start": v(5.26, 1.65) * mm, "end": v(5.26, 1.68) * mm});
            skLineSegment(sketch, "E4671", {"start": v(5.26, 1.68) * mm, "end": v(5.26, 1.7) * mm});
            skLineSegment(sketch, "E4672", {"start": v(5.26, 1.7) * mm, "end": v(5.26, 1.72) * mm});
            skLineSegment(sketch, "E4673", {"start": v(5.26, 1.72) * mm, "end": v(5.26, 1.74) * mm});
            skLineSegment(sketch, "E4674", {"start": v(5.26, 1.74) * mm, "end": v(5.26, 1.75) * mm});
            skLineSegment(sketch, "E4675", {"start": v(5.26, 1.75) * mm, "end": v(5.26, 1.77) * mm});
            skLineSegment(sketch, "E4676", {"start": v(5.26, 1.77) * mm, "end": v(5.26, 1.78) * mm});
            skLineSegment(sketch, "E4677", {"start": v(5.26, 1.78) * mm, "end": v(5.26, 1.79) * mm});
            skLineSegment(sketch, "E4678", {"start": v(5.26, 1.79) * mm, "end": v(5.26, 1.8) * mm});
            skLineSegment(sketch, "E4679", {"start": v(5.26, 1.8) * mm, "end": v(5.26, 1.8) * mm});
            skLineSegment(sketch, "E4680", {"start": v(5.26, 1.8) * mm, "end": v(5.27, 1.8) * mm});
            skLineSegment(sketch, "E4681", {"start": v(5.27, 1.8) * mm, "end": v(5.28, 1.8) * mm});
            skLineSegment(sketch, "E4682", {"start": v(5.28, 1.8) * mm, "end": v(5.3, 1.8) * mm});
            skLineSegment(sketch, "E4683", {"start": v(5.3, 1.8) * mm, "end": v(5.31, 1.8) * mm});
            skLineSegment(sketch, "E4684", {"start": v(5.31, 1.8) * mm, "end": v(5.34, 1.8) * mm});
            skLineSegment(sketch, "E4685", {"start": v(5.34, 1.8) * mm, "end": v(5.36, 1.8) * mm});
            skLineSegment(sketch, "E4686", {"start": v(5.36, 1.8) * mm, "end": v(5.4, 1.8) * mm});
            skLineSegment(sketch, "E4687", {"start": v(5.4, 1.8) * mm, "end": v(5.43, 1.8) * mm});
            skLineSegment(sketch, "E4688", {"start": v(5.43, 1.8) * mm, "end": v(5.46, 1.8) * mm});
            skLineSegment(sketch, "E4689", {"start": v(5.46, 1.8) * mm, "end": v(5.5, 1.8) * mm});
            skLineSegment(sketch, "E4690", {"start": v(5.5, 1.8) * mm, "end": v(5.54, 1.8) * mm});
            skLineSegment(sketch, "E4691", {"start": v(5.54, 1.8) * mm, "end": v(5.58, 1.8) * mm});
            skLineSegment(sketch, "E4692", {"start": v(5.58, 1.8) * mm, "end": v(5.63, 1.8) * mm});
            skLineSegment(sketch, "E4693", {"start": v(5.63, 1.8) * mm, "end": v(5.68, 1.8) * mm});
            skLineSegment(sketch, "E4694", {"start": v(5.68, 1.8) * mm, "end": v(5.73, 1.8) * mm});
            skLineSegment(sketch, "E4695", {"start": v(5.73, 1.8) * mm, "end": v(5.78, 1.8) * mm});
            skLineSegment(sketch, "E4696", {"start": v(5.78, 1.8) * mm, "end": v(5.83, 1.8) * mm});
            skLineSegment(sketch, "E4697", {"start": v(5.83, 1.8) * mm, "end": v(5.88, 1.8) * mm});
            skLineSegment(sketch, "E4698", {"start": v(5.88, 1.8) * mm, "end": v(5.94, 1.8) * mm});
            skLineSegment(sketch, "E4699", {"start": v(5.94, 1.8) * mm, "end": v(6, 1.8) * mm});
            skLineSegment(sketch, "E4700", {"start": v(6, 1.8) * mm, "end": v(6.05, 1.8) * mm});
            skLineSegment(sketch, "E4701", {"start": v(6.05, 1.8) * mm, "end": v(6.11, 1.8) * mm});
            skLineSegment(sketch, "E4702", {"start": v(6.11, 1.8) * mm, "end": v(6.17, 1.8) * mm});
            skLineSegment(sketch, "E4703", {"start": v(6.17, 1.8) * mm, "end": v(6.23, 1.8) * mm});
            skLineSegment(sketch, "E4704", {"start": v(6.23, 1.8) * mm, "end": v(6.28, 1.8) * mm});
            skLineSegment(sketch, "E4705", {"start": v(6.28, 1.8) * mm, "end": v(6.34, 1.8) * mm});
            skLineSegment(sketch, "E4706", {"start": v(6.34, 1.8) * mm, "end": v(6.4, 1.8) * mm});
            skLineSegment(sketch, "E4707", {"start": v(6.4, 1.8) * mm, "end": v(6.46, 1.8) * mm});
            skLineSegment(sketch, "E4708", {"start": v(6.46, 1.8) * mm, "end": v(6.51, 1.8) * mm});
            skLineSegment(sketch, "E4709", {"start": v(6.51, 1.8) * mm, "end": v(6.57, 1.8) * mm});
            skLineSegment(sketch, "E4710", {"start": v(6.57, 1.8) * mm, "end": v(6.62, 1.8) * mm});
            skLineSegment(sketch, "E4711", {"start": v(6.62, 1.8) * mm, "end": v(6.67, 1.8) * mm});
            skLineSegment(sketch, "E4712", {"start": v(6.67, 1.8) * mm, "end": v(6.73, 1.8) * mm});
            skLineSegment(sketch, "E4713", {"start": v(6.73, 1.8) * mm, "end": v(6.77, 1.8) * mm});
            skLineSegment(sketch, "E4714", {"start": v(6.77, 1.8) * mm, "end": v(6.82, 1.8) * mm});
            skLineSegment(sketch, "E4715", {"start": v(6.82, 1.8) * mm, "end": v(6.87, 1.8) * mm});
            skLineSegment(sketch, "E4716", {"start": v(6.87, 1.8) * mm, "end": v(6.91, 1.8) * mm});
            skLineSegment(sketch, "E4717", {"start": v(6.91, 1.8) * mm, "end": v(6.95, 1.8) * mm});
            skLineSegment(sketch, "E4718", {"start": v(6.95, 1.8) * mm, "end": v(7, 1.8) * mm});
            skLineSegment(sketch, "E4719", {"start": v(7, 1.8) * mm, "end": v(7.03, 1.8) * mm});
            skLineSegment(sketch, "E4720", {"start": v(7.03, 1.8) * mm, "end": v(7.06, 1.8) * mm});
            skLineSegment(sketch, "E4721", {"start": v(7.06, 1.8) * mm, "end": v(7.09, 1.8) * mm});
            skLineSegment(sketch, "E4722", {"start": v(7.09, 1.8) * mm, "end": v(7.12, 1.8) * mm});
            skLineSegment(sketch, "E4723", {"start": v(7.12, 1.8) * mm, "end": v(7.14, 1.8) * mm});
            skLineSegment(sketch, "E4724", {"start": v(7.14, 1.8) * mm, "end": v(7.16, 1.8) * mm});
            skLineSegment(sketch, "E4725", {"start": v(7.16, 1.8) * mm, "end": v(7.17, 1.8) * mm});
            skLineSegment(sketch, "E4726", {"start": v(7.17, 1.8) * mm, "end": v(7.18, 1.8) * mm});
            skLineSegment(sketch, "E4727", {"start": v(7.18, 1.8) * mm, "end": v(7.19, 1.8) * mm});
            skLineSegment(sketch, "E4728", {"start": v(7.19, 1.8) * mm, "end": v(7.2, 1.8) * mm});
            skLineSegment(sketch, "E4729", {"start": v(7.2, 1.8) * mm, "end": v(7.22, 1.8) * mm});
            skLineSegment(sketch, "E4730", {"start": v(7.22, 1.8) * mm, "end": v(7.25, 1.8) * mm});
            skLineSegment(sketch, "E4731", {"start": v(7.25, 1.8) * mm, "end": v(7.28, 1.8) * mm});
            skLineSegment(sketch, "E4732", {"start": v(7.28, 1.8) * mm, "end": v(7.3, 1.8) * mm});
            skLineSegment(sketch, "E4733", {"start": v(7.3, 1.8) * mm, "end": v(7.33, 1.8) * mm});
            skLineSegment(sketch, "E4734", {"start": v(7.33, 1.8) * mm, "end": v(7.36, 1.81) * mm});
            skLineSegment(sketch, "E4735", {"start": v(7.36, 1.81) * mm, "end": v(7.39, 1.82) * mm});
            skLineSegment(sketch, "E4736", {"start": v(7.39, 1.82) * mm, "end": v(7.41, 1.82) * mm});
            skLineSegment(sketch, "E4737", {"start": v(7.41, 1.82) * mm, "end": v(7.44, 1.83) * mm});
            skLineSegment(sketch, "E4738", {"start": v(7.44, 1.83) * mm, "end": v(7.46, 1.84) * mm});
            skLineSegment(sketch, "E4739", {"start": v(7.46, 1.84) * mm, "end": v(7.48, 1.84) * mm});
            skLineSegment(sketch, "E4740", {"start": v(7.48, 1.84) * mm, "end": v(7.5, 1.85) * mm});
            skLineSegment(sketch, "E4741", {"start": v(7.5, 1.85) * mm, "end": v(7.53, 1.86) * mm});
            skLineSegment(sketch, "E4742", {"start": v(7.53, 1.86) * mm, "end": v(7.55, 1.87) * mm});
            skLineSegment(sketch, "E4743", {"start": v(7.55, 1.87) * mm, "end": v(7.57, 1.88) * mm});
            skLineSegment(sketch, "E4744", {"start": v(7.57, 1.88) * mm, "end": v(7.6, 1.89) * mm});
            skLineSegment(sketch, "E4745", {"start": v(7.6, 1.89) * mm, "end": v(7.61, 1.9) * mm});
            skLineSegment(sketch, "E4746", {"start": v(7.61, 1.9) * mm, "end": v(7.63, 1.9) * mm});
            skLineSegment(sketch, "E4747", {"start": v(7.63, 1.9) * mm, "end": v(7.65, 1.92) * mm});
            skLineSegment(sketch, "E4748", {"start": v(7.65, 1.92) * mm, "end": v(7.67, 1.93) * mm});
            skLineSegment(sketch, "E4749", {"start": v(7.67, 1.93) * mm, "end": v(7.69, 1.94) * mm});
            skLineSegment(sketch, "E4750", {"start": v(7.69, 1.94) * mm, "end": v(7.7, 1.95) * mm});
            skLineSegment(sketch, "E4751", {"start": v(7.7, 1.95) * mm, "end": v(7.72, 1.97) * mm});
            skLineSegment(sketch, "E4752", {"start": v(7.72, 1.97) * mm, "end": v(7.74, 1.98) * mm});
            skLineSegment(sketch, "E4753", {"start": v(7.74, 1.98) * mm, "end": v(7.75, 2) * mm});
            skLineSegment(sketch, "E4754", {"start": v(7.75, 2) * mm, "end": v(7.77, 2) * mm});
            skLineSegment(sketch, "E4755", {"start": v(7.77, 2) * mm, "end": v(7.78, 2.02) * mm});
            skLineSegment(sketch, "E4756", {"start": v(7.78, 2.02) * mm, "end": v(7.8, 2.04) * mm});
            skLineSegment(sketch, "E4757", {"start": v(7.8, 2.04) * mm, "end": v(7.81, 2.05) * mm});
            skLineSegment(sketch, "E4758", {"start": v(7.81, 2.05) * mm, "end": v(7.82, 2.07) * mm});
            skLineSegment(sketch, "E4759", {"start": v(7.82, 2.07) * mm, "end": v(7.83, 2.08) * mm});
            skLineSegment(sketch, "E4760", {"start": v(7.83, 2.08) * mm, "end": v(7.85, 2.1) * mm});
            skLineSegment(sketch, "E4761", {"start": v(7.85, 2.1) * mm, "end": v(7.86, 2.11) * mm});
            skLineSegment(sketch, "E4762", {"start": v(7.86, 2.11) * mm, "end": v(7.87, 2.13) * mm});
            skLineSegment(sketch, "E4763", {"start": v(7.87, 2.13) * mm, "end": v(7.88, 2.15) * mm});
            skLineSegment(sketch, "E4764", {"start": v(7.88, 2.15) * mm, "end": v(7.89, 2.16) * mm});
            skLineSegment(sketch, "E4765", {"start": v(7.89, 2.16) * mm, "end": v(7.9, 2.18) * mm});
            skLineSegment(sketch, "E4766", {"start": v(7.9, 2.18) * mm, "end": v(7.9, 2.2) * mm});
            skLineSegment(sketch, "E4767", {"start": v(7.9, 2.2) * mm, "end": v(7.9, 2.21) * mm});
            skLineSegment(sketch, "E4768", {"start": v(7.9, 2.21) * mm, "end": v(7.92, 2.23) * mm});
            skLineSegment(sketch, "E4769", {"start": v(7.92, 2.23) * mm, "end": v(7.92, 2.25) * mm});
            skLineSegment(sketch, "E4770", {"start": v(7.92, 2.25) * mm, "end": v(7.93, 2.27) * mm});
            skLineSegment(sketch, "E4771", {"start": v(7.93, 2.27) * mm, "end": v(7.93, 2.29) * mm});
            skLineSegment(sketch, "E4772", {"start": v(7.93, 2.29) * mm, "end": v(7.93, 2.3) * mm});
            skLineSegment(sketch, "E4773", {"start": v(7.93, 2.3) * mm, "end": v(7.94, 2.32) * mm});
            skLineSegment(sketch, "E4774", {"start": v(7.94, 2.32) * mm, "end": v(7.94, 2.34) * mm});
            skLineSegment(sketch, "E4775", {"start": v(7.94, 2.34) * mm, "end": v(7.94, 2.36) * mm});
            skLineSegment(sketch, "E4776", {"start": v(7.94, 2.36) * mm, "end": v(7.94, 2.38) * mm});
            skLineSegment(sketch, "E4777", {"start": v(7.94, 2.38) * mm, "end": v(7.95, 2.4) * mm});
            skLineSegment(sketch, "E4778", {"start": v(7.95, 2.4) * mm, "end": v(7.95, 2.41) * mm});
            skLineSegment(sketch, "E4779", {"start": v(7.95, 2.41) * mm, "end": v(7.95, 2.43) * mm});
            skLineSegment(sketch, "E4780", {"start": v(7.95, 2.43) * mm, "end": v(7.94, 2.45) * mm});
            skLineSegment(sketch, "E4781", {"start": v(7.94, 2.45) * mm, "end": v(7.94, 2.47) * mm});
            skLineSegment(sketch, "E4782", {"start": v(7.94, 2.47) * mm, "end": v(7.94, 2.5) * mm});
            skLineSegment(sketch, "E4783", {"start": v(7.94, 2.5) * mm, "end": v(7.94, 2.51) * mm});
            skLineSegment(sketch, "E4784", {"start": v(7.94, 2.51) * mm, "end": v(7.93, 2.53) * mm});
            skLineSegment(sketch, "E4785", {"start": v(7.93, 2.53) * mm, "end": v(7.93, 2.55) * mm});
            skLineSegment(sketch, "E4786", {"start": v(7.93, 2.55) * mm, "end": v(7.93, 2.57) * mm});
            skLineSegment(sketch, "E4787", {"start": v(7.93, 2.57) * mm, "end": v(7.92, 2.59) * mm});
            skLineSegment(sketch, "E4788", {"start": v(7.92, 2.59) * mm, "end": v(7.92, 2.6) * mm});
            skLineSegment(sketch, "E4789", {"start": v(7.92, 2.6) * mm, "end": v(7.9, 2.62) * mm});
            skLineSegment(sketch, "E4790", {"start": v(7.9, 2.62) * mm, "end": v(7.9, 2.64) * mm});
            skLineSegment(sketch, "E4791", {"start": v(7.9, 2.64) * mm, "end": v(7.9, 2.66) * mm});
            skLineSegment(sketch, "E4792", {"start": v(7.9, 2.66) * mm, "end": v(7.89, 2.68) * mm});
            skLineSegment(sketch, "E4793", {"start": v(7.89, 2.68) * mm, "end": v(7.88, 2.7) * mm});
            skLineSegment(sketch, "E4794", {"start": v(7.88, 2.7) * mm, "end": v(7.87, 2.71) * mm});
            skLineSegment(sketch, "E4795", {"start": v(7.87, 2.71) * mm, "end": v(7.86, 2.73) * mm});
            skLineSegment(sketch, "E4796", {"start": v(7.86, 2.73) * mm, "end": v(7.85, 2.75) * mm});
            skLineSegment(sketch, "E4797", {"start": v(7.85, 2.75) * mm, "end": v(7.84, 2.76) * mm});
            skLineSegment(sketch, "E4798", {"start": v(7.84, 2.76) * mm, "end": v(7.82, 2.78) * mm});
            skLineSegment(sketch, "E4799", {"start": v(7.82, 2.78) * mm, "end": v(7.81, 2.8) * mm});
            skLineSegment(sketch, "E4800", {"start": v(7.81, 2.8) * mm, "end": v(7.8, 2.81) * mm});
            skLineSegment(sketch, "E4801", {"start": v(7.8, 2.81) * mm, "end": v(7.79, 2.83) * mm});
            skLineSegment(sketch, "E4802", {"start": v(7.79, 2.83) * mm, "end": v(7.77, 2.84) * mm});
            skLineSegment(sketch, "E4803", {"start": v(7.77, 2.84) * mm, "end": v(7.76, 2.86) * mm});
            skLineSegment(sketch, "E4804", {"start": v(7.76, 2.86) * mm, "end": v(7.74, 2.87) * mm});
            skLineSegment(sketch, "E4805", {"start": v(7.74, 2.87) * mm, "end": v(7.73, 2.88) * mm});
            skLineSegment(sketch, "E4806", {"start": v(7.73, 2.88) * mm, "end": v(7.71, 2.9) * mm});
            skLineSegment(sketch, "E4807", {"start": v(7.71, 2.9) * mm, "end": v(7.7, 2.9) * mm});
            skLineSegment(sketch, "E4808", {"start": v(7.7, 2.9) * mm, "end": v(7.68, 2.92) * mm});
            skLineSegment(sketch, "E4809", {"start": v(7.68, 2.92) * mm, "end": v(7.66, 2.93) * mm});
            skLineSegment(sketch, "E4810", {"start": v(7.66, 2.93) * mm, "end": v(7.64, 2.94) * mm});
            skLineSegment(sketch, "E4811", {"start": v(7.64, 2.94) * mm, "end": v(7.62, 2.95) * mm});
            skLineSegment(sketch, "E4812", {"start": v(7.62, 2.95) * mm, "end": v(7.6, 2.96) * mm});
            skLineSegment(sketch, "E4813", {"start": v(7.6, 2.96) * mm, "end": v(7.58, 2.97) * mm});
            skLineSegment(sketch, "E4814", {"start": v(7.58, 2.97) * mm, "end": v(7.56, 2.98) * mm});
            skLineSegment(sketch, "E4815", {"start": v(7.56, 2.98) * mm, "end": v(7.54, 3) * mm});
            skLineSegment(sketch, "E4816", {"start": v(7.54, 3) * mm, "end": v(7.52, 3) * mm});
            skLineSegment(sketch, "E4817", {"start": v(7.52, 3) * mm, "end": v(7.5, 3) * mm});
            skLineSegment(sketch, "E4818", {"start": v(7.5, 3) * mm, "end": v(7.47, 3.02) * mm});
            skLineSegment(sketch, "E4819", {"start": v(7.47, 3.02) * mm, "end": v(7.45, 3.02) * mm});
            skLineSegment(sketch, "E4820", {"start": v(7.45, 3.02) * mm, "end": v(7.43, 3.03) * mm});
            skLineSegment(sketch, "E4821", {"start": v(7.43, 3.03) * mm, "end": v(7.4, 3.03) * mm});
            skLineSegment(sketch, "E4822", {"start": v(7.4, 3.03) * mm, "end": v(7.38, 3.04) * mm});
            skLineSegment(sketch, "E4823", {"start": v(7.38, 3.04) * mm, "end": v(7.35, 3.04) * mm});
            skLineSegment(sketch, "E4824", {"start": v(7.35, 3.04) * mm, "end": v(7.32, 3.04) * mm});
            skLineSegment(sketch, "E4825", {"start": v(7.32, 3.04) * mm, "end": v(7.3, 3.05) * mm});
            skLineSegment(sketch, "E4826", {"start": v(7.3, 3.05) * mm, "end": v(7.27, 3.05) * mm});
            skLineSegment(sketch, "E4827", {"start": v(7.27, 3.05) * mm, "end": v(7.24, 3.05) * mm});
            skLineSegment(sketch, "E4828", {"start": v(7.24, 3.05) * mm, "end": v(7.22, 3.05) * mm});
            skLineSegment(sketch, "E4829", {"start": v(7.22, 3.05) * mm, "end": v(7.21, 3.05) * mm});
            skLineSegment(sketch, "E4830", {"start": v(7.21, 3.05) * mm, "end": v(7.2, 3.05) * mm});
            skLineSegment(sketch, "E4831", {"start": v(7.2, 3.05) * mm, "end": v(7.19, 3.05) * mm});
            skLineSegment(sketch, "E4832", {"start": v(7.19, 3.05) * mm, "end": v(7.17, 3.05) * mm});
            skLineSegment(sketch, "E4833", {"start": v(7.17, 3.05) * mm, "end": v(7.15, 3.05) * mm});
            skLineSegment(sketch, "E4834", {"start": v(7.15, 3.05) * mm, "end": v(7.12, 3.05) * mm});
            skLineSegment(sketch, "E4835", {"start": v(7.12, 3.05) * mm, "end": v(7.08, 3.05) * mm});
            skLineSegment(sketch, "E4836", {"start": v(7.08, 3.05) * mm, "end": v(7.05, 3.05) * mm});
            skLineSegment(sketch, "E4837", {"start": v(7.05, 3.05) * mm, "end": v(7, 3.05) * mm});
            skLineSegment(sketch, "E4838", {"start": v(7, 3.05) * mm, "end": v(6.96, 3.05) * mm});
            skLineSegment(sketch, "E4839", {"start": v(6.96, 3.05) * mm, "end": v(6.9, 3.05) * mm});
            skLineSegment(sketch, "E4840", {"start": v(6.9, 3.05) * mm, "end": v(6.86, 3.05) * mm});
            skLineSegment(sketch, "E4841", {"start": v(6.86, 3.05) * mm, "end": v(6.8, 3.05) * mm});
            skLineSegment(sketch, "E4842", {"start": v(6.8, 3.05) * mm, "end": v(6.74, 3.05) * mm});
            skLineSegment(sketch, "E4843", {"start": v(6.74, 3.05) * mm, "end": v(6.68, 3.05) * mm});
            skLineSegment(sketch, "E4844", {"start": v(6.68, 3.05) * mm, "end": v(6.62, 3.05) * mm});
            skLineSegment(sketch, "E4845", {"start": v(6.62, 3.05) * mm, "end": v(6.55, 3.05) * mm});
            skLineSegment(sketch, "E4846", {"start": v(6.55, 3.05) * mm, "end": v(6.48, 3.05) * mm});
            skLineSegment(sketch, "E4847", {"start": v(6.48, 3.05) * mm, "end": v(6.42, 3.05) * mm});
            skLineSegment(sketch, "E4848", {"start": v(6.42, 3.05) * mm, "end": v(6.34, 3.05) * mm});
            skLineSegment(sketch, "E4849", {"start": v(6.34, 3.05) * mm, "end": v(6.27, 3.05) * mm});
            skLineSegment(sketch, "E4850", {"start": v(6.27, 3.05) * mm, "end": v(6.2, 3.05) * mm});
            skLineSegment(sketch, "E4851", {"start": v(6.2, 3.05) * mm, "end": v(6.13, 3.05) * mm});
            skLineSegment(sketch, "E4852", {"start": v(6.13, 3.05) * mm, "end": v(6.05, 3.05) * mm});
            skLineSegment(sketch, "E4853", {"start": v(6.05, 3.05) * mm, "end": v(5.98, 3.05) * mm});
            skLineSegment(sketch, "E4854", {"start": v(5.98, 3.05) * mm, "end": v(5.9, 3.05) * mm});
            skLineSegment(sketch, "E4855", {"start": v(5.9, 3.05) * mm, "end": v(5.83, 3.05) * mm});
            skLineSegment(sketch, "E4856", {"start": v(5.83, 3.05) * mm, "end": v(5.76, 3.05) * mm});
            skLineSegment(sketch, "E4857", {"start": v(5.76, 3.05) * mm, "end": v(5.68, 3.05) * mm});
            skLineSegment(sketch, "E4858", {"start": v(5.68, 3.05) * mm, "end": v(5.61, 3.05) * mm});
            skLineSegment(sketch, "E4859", {"start": v(5.61, 3.05) * mm, "end": v(5.54, 3.05) * mm});
            skLineSegment(sketch, "E4860", {"start": v(5.54, 3.05) * mm, "end": v(5.47, 3.05) * mm});
            skLineSegment(sketch, "E4861", {"start": v(5.47, 3.05) * mm, "end": v(5.4, 3.05) * mm});
            skLineSegment(sketch, "E4862", {"start": v(5.4, 3.05) * mm, "end": v(5.34, 3.05) * mm});
            skLineSegment(sketch, "E4863", {"start": v(5.34, 3.05) * mm, "end": v(5.28, 3.05) * mm});
            skLineSegment(sketch, "E4864", {"start": v(5.28, 3.05) * mm, "end": v(5.21, 3.05) * mm});
            skLineSegment(sketch, "E4865", {"start": v(5.21, 3.05) * mm, "end": v(5.16, 3.05) * mm});
            skLineSegment(sketch, "E4866", {"start": v(5.16, 3.05) * mm, "end": v(5.1, 3.05) * mm});
            skLineSegment(sketch, "E4867", {"start": v(5.1, 3.05) * mm, "end": v(5.05, 3.05) * mm});
            skLineSegment(sketch, "E4868", {"start": v(5.05, 3.05) * mm, "end": v(5, 3.05) * mm});
            skLineSegment(sketch, "E4869", {"start": v(5, 3.05) * mm, "end": v(4.95, 3.05) * mm});
            skLineSegment(sketch, "E4870", {"start": v(4.95, 3.05) * mm, "end": v(4.91, 3.05) * mm});
            skLineSegment(sketch, "E4871", {"start": v(4.91, 3.05) * mm, "end": v(4.87, 3.05) * mm});
            skLineSegment(sketch, "E4872", {"start": v(4.87, 3.05) * mm, "end": v(4.84, 3.05) * mm});
            skLineSegment(sketch, "E4873", {"start": v(4.84, 3.05) * mm, "end": v(4.81, 3.05) * mm});
            skLineSegment(sketch, "E4874", {"start": v(4.81, 3.05) * mm, "end": v(4.79, 3.05) * mm});
            skLineSegment(sketch, "E4875", {"start": v(4.79, 3.05) * mm, "end": v(4.77, 3.05) * mm});
            skLineSegment(sketch, "E4876", {"start": v(4.77, 3.05) * mm, "end": v(4.75, 3.05) * mm});
            skLineSegment(sketch, "E4877", {"start": v(4.75, 3.05) * mm, "end": v(4.74, 3.05) * mm});
            skLineSegment(sketch, "E4878", {"start": v(4.74, 3.05) * mm, "end": v(4.74, 3.05) * mm});
            skLineSegment(sketch, "E4879", {"start": v(4.74, 3.05) * mm, "end": v(4.73, 3.05) * mm});
            skLineSegment(sketch, "E4880", {"start": v(4.73, 3.05) * mm, "end": v(4.72, 3.05) * mm});
            skLineSegment(sketch, "E4881", {"start": v(4.72, 3.05) * mm, "end": v(4.7, 3.05) * mm});
            skLineSegment(sketch, "E4882", {"start": v(4.7, 3.05) * mm, "end": v(4.7, 3.05) * mm});
            skLineSegment(sketch, "E4883", {"start": v(4.7, 3.05) * mm, "end": v(4.69, 3.05) * mm});
            skLineSegment(sketch, "E4884", {"start": v(4.69, 3.05) * mm, "end": v(4.68, 3.04) * mm});
            skLineSegment(sketch, "E4885", {"start": v(4.68, 3.04) * mm, "end": v(4.67, 3.04) * mm});
            skLineSegment(sketch, "E4886", {"start": v(4.67, 3.04) * mm, "end": v(4.66, 3.04) * mm});
            skLineSegment(sketch, "E4887", {"start": v(4.66, 3.04) * mm, "end": v(4.65, 3.04) * mm});
            skLineSegment(sketch, "E4888", {"start": v(4.65, 3.04) * mm, "end": v(4.64, 3.04) * mm});
            skLineSegment(sketch, "E4889", {"start": v(4.64, 3.04) * mm, "end": v(4.63, 3.03) * mm});
            skLineSegment(sketch, "E4890", {"start": v(4.63, 3.03) * mm, "end": v(4.63, 3.03) * mm});
            skLineSegment(sketch, "E4891", {"start": v(4.63, 3.03) * mm, "end": v(4.62, 3.03) * mm});
            skLineSegment(sketch, "E4892", {"start": v(4.62, 3.03) * mm, "end": v(4.61, 3.02) * mm});
            skLineSegment(sketch, "E4893", {"start": v(4.61, 3.02) * mm, "end": v(4.6, 3.02) * mm});
            skLineSegment(sketch, "E4894", {"start": v(4.6, 3.02) * mm, "end": v(4.6, 3.02) * mm});
            skLineSegment(sketch, "E4895", {"start": v(4.6, 3.02) * mm, "end": v(4.59, 3.01) * mm});
            skLineSegment(sketch, "E4896", {"start": v(4.59, 3.01) * mm, "end": v(4.58, 3) * mm});
            skLineSegment(sketch, "E4897", {"start": v(4.58, 3) * mm, "end": v(4.58, 3) * mm});
            skLineSegment(sketch, "E4898", {"start": v(4.58, 3) * mm, "end": v(4.57, 3) * mm});
            skLineSegment(sketch, "E4899", {"start": v(4.57, 3) * mm, "end": v(4.56, 3) * mm});
            skLineSegment(sketch, "E4900", {"start": v(4.56, 3) * mm, "end": v(4.56, 2.99) * mm});
            skLineSegment(sketch, "E4901", {"start": v(4.56, 2.99) * mm, "end": v(4.55, 2.98) * mm});
            skLineSegment(sketch, "E4902", {"start": v(4.55, 2.98) * mm, "end": v(4.55, 2.98) * mm});
            skLineSegment(sketch, "E4903", {"start": v(4.55, 2.98) * mm, "end": v(4.54, 2.97) * mm});
            skLineSegment(sketch, "E4904", {"start": v(4.54, 2.97) * mm, "end": v(4.54, 2.97) * mm});
            skLineSegment(sketch, "E4905", {"start": v(4.54, 2.97) * mm, "end": v(4.53, 2.96) * mm});
            skLineSegment(sketch, "E4906", {"start": v(4.53, 2.96) * mm, "end": v(4.53, 2.96) * mm});
            skLineSegment(sketch, "E4907", {"start": v(4.53, 2.96) * mm, "end": v(4.52, 2.95) * mm});
            skLineSegment(sketch, "E4908", {"start": v(4.52, 2.95) * mm, "end": v(4.52, 2.94) * mm});
            skLineSegment(sketch, "E4909", {"start": v(4.52, 2.94) * mm, "end": v(4.52, 2.94) * mm});
            skLineSegment(sketch, "E4910", {"start": v(4.52, 2.94) * mm, "end": v(4.51, 2.93) * mm});
            skLineSegment(sketch, "E4911", {"start": v(4.51, 2.93) * mm, "end": v(4.5, 2.92) * mm});
            skLineSegment(sketch, "E4912", {"start": v(4.5, 2.92) * mm, "end": v(4.5, 2.92) * mm});
            skLineSegment(sketch, "E4913", {"start": v(4.5, 2.92) * mm, "end": v(4.5, 2.9) * mm});
            skLineSegment(sketch, "E4914", {"start": v(4.5, 2.9) * mm, "end": v(4.5, 2.9) * mm});
            skLineSegment(sketch, "E4915", {"start": v(4.5, 2.9) * mm, "end": v(4.5, 2.89) * mm});
            skLineSegment(sketch, "E4916", {"start": v(4.5, 2.89) * mm, "end": v(4.5, 2.88) * mm});
            skLineSegment(sketch, "E4917", {"start": v(4.5, 2.88) * mm, "end": v(4.5, 2.87) * mm});
            skLineSegment(sketch, "E4918", {"start": v(4.5, 2.87) * mm, "end": v(4.49, 2.86) * mm});
            skLineSegment(sketch, "E4919", {"start": v(4.49, 2.86) * mm, "end": v(4.49, 2.86) * mm});
            skLineSegment(sketch, "E4920", {"start": v(4.49, 2.86) * mm, "end": v(4.49, 2.85) * mm});
            skLineSegment(sketch, "E4921", {"start": v(4.49, 2.85) * mm, "end": v(4.49, 2.84) * mm});
            skLineSegment(sketch, "E4922", {"start": v(4.49, 2.84) * mm, "end": v(4.48, 2.83) * mm});
            skLineSegment(sketch, "E4923", {"start": v(4.48, 2.83) * mm, "end": v(4.48, 2.82) * mm});
            skLineSegment(sketch, "E4924", {"start": v(4.48, 2.82) * mm, "end": v(4.48, 2.82) * mm});
            skLineSegment(sketch, "E4925", {"start": v(4.48, 2.82) * mm, "end": v(4.48, 2.8) * mm});
            skLineSegment(sketch, "E4926", {"start": v(4.48, 2.8) * mm, "end": v(4.48, 2.8) * mm});
            skLineSegment(sketch, "E4927", {"start": v(4.48, 2.8) * mm, "end": v(4.48, 2.78) * mm});
            skLineSegment(sketch, "E4928", {"start": v(4.48, 2.78) * mm, "end": v(4.48, 2.78) * mm});
            skLineSegment(sketch, "E4929", {"start": v(4.48, 2.78) * mm, "end": v(4.48, 2.77) * mm});
            skLineSegment(sketch, "E4930", {"start": v(4.48, 2.77) * mm, "end": v(4.48, 2.76) * mm});
            skLineSegment(sketch, "E4931", {"start": v(4.48, 2.76) * mm, "end": v(4.48, 2.76) * mm});
            skLineSegment(sketch, "E4932", {"start": v(4.48, 2.76) * mm, "end": v(4.49, 2.75) * mm});
            skLineSegment(sketch, "E4933", {"start": v(4.49, 2.75) * mm, "end": v(4.49, 2.74) * mm});
            skLineSegment(sketch, "E4934", {"start": v(4.49, 2.74) * mm, "end": v(4.49, 2.74) * mm});
            skLineSegment(sketch, "E4935", {"start": v(4.49, 2.74) * mm, "end": v(4.49, 2.73) * mm});
            skLineSegment(sketch, "E4936", {"start": v(4.49, 2.73) * mm, "end": v(4.5, 2.72) * mm});
            skLineSegment(sketch, "E4937", {"start": v(4.5, 2.72) * mm, "end": v(4.5, 2.72) * mm});
            skLineSegment(sketch, "E4938", {"start": v(4.5, 2.72) * mm, "end": v(4.5, 2.71) * mm});
            skLineSegment(sketch, "E4939", {"start": v(4.5, 2.71) * mm, "end": v(4.5, 2.7) * mm});
            skLineSegment(sketch, "E4940", {"start": v(4.5, 2.7) * mm, "end": v(4.5, 2.7) * mm});
            skLineSegment(sketch, "E4941", {"start": v(4.5, 2.7) * mm, "end": v(4.5, 2.69) * mm});
            skLineSegment(sketch, "E4942", {"start": v(4.5, 2.69) * mm, "end": v(4.5, 2.68) * mm});
            skLineSegment(sketch, "E4943", {"start": v(4.5, 2.68) * mm, "end": v(4.51, 2.68) * mm});
            skLineSegment(sketch, "E4944", {"start": v(4.51, 2.68) * mm, "end": v(4.52, 2.67) * mm});
            skLineSegment(sketch, "E4945", {"start": v(4.52, 2.67) * mm, "end": v(4.52, 2.66) * mm});
            skLineSegment(sketch, "E4946", {"start": v(4.52, 2.66) * mm, "end": v(4.52, 2.66) * mm});
            skLineSegment(sketch, "E4947", {"start": v(4.52, 2.66) * mm, "end": v(4.53, 2.65) * mm});
            skLineSegment(sketch, "E4948", {"start": v(4.53, 2.65) * mm, "end": v(4.53, 2.65) * mm});
            skLineSegment(sketch, "E4949", {"start": v(4.53, 2.65) * mm, "end": v(4.54, 2.64) * mm});
            skLineSegment(sketch, "E4950", {"start": v(4.54, 2.64) * mm, "end": v(4.54, 2.64) * mm});
            skLineSegment(sketch, "E4951", {"start": v(4.54, 2.64) * mm, "end": v(4.55, 2.64) * mm});
            skLineSegment(sketch, "E4952", {"start": v(4.55, 2.64) * mm, "end": v(4.55, 2.63) * mm});
            skLineSegment(sketch, "E4953", {"start": v(4.55, 2.63) * mm, "end": v(4.56, 2.63) * mm});
            skLineSegment(sketch, "E4954", {"start": v(4.56, 2.63) * mm, "end": v(4.56, 2.62) * mm});
            skLineSegment(sketch, "E4955", {"start": v(4.56, 2.62) * mm, "end": v(4.57, 2.62) * mm});
            skLineSegment(sketch, "E4956", {"start": v(4.57, 2.62) * mm, "end": v(4.58, 2.62) * mm});
            skLineSegment(sketch, "E4957", {"start": v(4.58, 2.62) * mm, "end": v(4.58, 2.61) * mm});
            skLineSegment(sketch, "E4958", {"start": v(4.58, 2.61) * mm, "end": v(4.59, 2.6) * mm});
            skLineSegment(sketch, "E4959", {"start": v(4.59, 2.6) * mm, "end": v(4.6, 2.6) * mm});
            skLineSegment(sketch, "E4960", {"start": v(4.6, 2.6) * mm, "end": v(4.6, 2.6) * mm});
            skLineSegment(sketch, "E4961", {"start": v(4.6, 2.6) * mm, "end": v(4.61, 2.6) * mm});
            skLineSegment(sketch, "E4962", {"start": v(4.61, 2.6) * mm, "end": v(4.62, 2.6) * mm});
            skLineSegment(sketch, "E4963", {"start": v(4.62, 2.6) * mm, "end": v(4.63, 2.6) * mm});
            skLineSegment(sketch, "E4964", {"start": v(4.63, 2.6) * mm, "end": v(4.63, 2.6) * mm});
            skLineSegment(sketch, "E4965", {"start": v(4.63, 2.6) * mm, "end": v(4.64, 2.59) * mm});
            skLineSegment(sketch, "E4966", {"start": v(4.64, 2.59) * mm, "end": v(4.65, 2.59) * mm});
            skLineSegment(sketch, "E4967", {"start": v(4.65, 2.59) * mm, "end": v(4.66, 2.59) * mm});
            skLineSegment(sketch, "E4968", {"start": v(4.66, 2.59) * mm, "end": v(4.67, 2.58) * mm});
            skLineSegment(sketch, "E4969", {"start": v(4.67, 2.58) * mm, "end": v(4.68, 2.58) * mm});
            skLineSegment(sketch, "E4970", {"start": v(4.68, 2.58) * mm, "end": v(4.69, 2.58) * mm});
            skLineSegment(sketch, "E4971", {"start": v(4.69, 2.58) * mm, "end": v(4.7, 2.58) * mm});
            skLineSegment(sketch, "E4972", {"start": v(4.7, 2.58) * mm, "end": v(4.7, 2.58) * mm});
            skLineSegment(sketch, "E4973", {"start": v(4.7, 2.58) * mm, "end": v(4.72, 2.58) * mm});
            skLineSegment(sketch, "E4974", {"start": v(4.72, 2.58) * mm, "end": v(4.73, 2.58) * mm});
            skLineSegment(sketch, "E4975", {"start": v(4.73, 2.58) * mm, "end": v(4.74, 2.58) * mm});
            skLineSegment(sketch, "E4976", {"start": v(4.74, 2.58) * mm, "end": v(4.74, 2.58) * mm});
            skLineSegment(sketch, "E4977", {"start": v(4.74, 2.58) * mm, "end": v(4.75, 2.58) * mm});
            skLineSegment(sketch, "E4978", {"start": v(4.75, 2.58) * mm, "end": v(4.77, 2.58) * mm});
            skLineSegment(sketch, "E4979", {"start": v(4.77, 2.58) * mm, "end": v(4.79, 2.58) * mm});
            skLineSegment(sketch, "E4980", {"start": v(4.79, 2.58) * mm, "end": v(4.81, 2.58) * mm});
            skLineSegment(sketch, "E4981", {"start": v(4.81, 2.58) * mm, "end": v(4.84, 2.58) * mm});
            skLineSegment(sketch, "E4982", {"start": v(4.84, 2.58) * mm, "end": v(4.87, 2.58) * mm});
            skLineSegment(sketch, "E4983", {"start": v(4.87, 2.58) * mm, "end": v(4.91, 2.58) * mm});
            skLineSegment(sketch, "E4984", {"start": v(4.91, 2.58) * mm, "end": v(4.96, 2.58) * mm});
            skLineSegment(sketch, "E4985", {"start": v(4.96, 2.58) * mm, "end": v(5, 2.58) * mm});
            skLineSegment(sketch, "E4986", {"start": v(5, 2.58) * mm, "end": v(5.05, 2.58) * mm});
            skLineSegment(sketch, "E4987", {"start": v(5.05, 2.58) * mm, "end": v(5.1, 2.58) * mm});
            skLineSegment(sketch, "E4988", {"start": v(5.1, 2.58) * mm, "end": v(5.16, 2.58) * mm});
            skLineSegment(sketch, "E4989", {"start": v(5.16, 2.58) * mm, "end": v(5.22, 2.58) * mm});
            skLineSegment(sketch, "E4990", {"start": v(5.22, 2.58) * mm, "end": v(5.28, 2.58) * mm});
            skLineSegment(sketch, "E4991", {"start": v(5.28, 2.58) * mm, "end": v(5.35, 2.58) * mm});
            skLineSegment(sketch, "E4992", {"start": v(5.35, 2.58) * mm, "end": v(5.41, 2.58) * mm});
            skLineSegment(sketch, "E4993", {"start": v(5.41, 2.58) * mm, "end": v(5.48, 2.58) * mm});
            skLineSegment(sketch, "E4994", {"start": v(5.48, 2.58) * mm, "end": v(5.55, 2.58) * mm});
            skLineSegment(sketch, "E4995", {"start": v(5.55, 2.58) * mm, "end": v(5.62, 2.58) * mm});
            skLineSegment(sketch, "E4996", {"start": v(5.62, 2.58) * mm, "end": v(5.7, 2.58) * mm});
            skLineSegment(sketch, "E4997", {"start": v(5.7, 2.58) * mm, "end": v(5.77, 2.58) * mm});
            skLineSegment(sketch, "E4998", {"start": v(5.77, 2.58) * mm, "end": v(5.84, 2.58) * mm});
            skLineSegment(sketch, "E4999", {"start": v(5.84, 2.58) * mm, "end": v(5.92, 2.58) * mm});
            skLineSegment(sketch, "E5000", {"start": v(5.92, 2.58) * mm, "end": v(6, 2.58) * mm});
            skLineSegment(sketch, "E5001", {"start": v(6, 2.58) * mm, "end": v(6.07, 2.58) * mm});
            skLineSegment(sketch, "E5002", {"start": v(6.07, 2.58) * mm, "end": v(6.14, 2.58) * mm});
            skLineSegment(sketch, "E5003", {"start": v(6.14, 2.58) * mm, "end": v(6.21, 2.58) * mm});
            skLineSegment(sketch, "E5004", {"start": v(6.21, 2.58) * mm, "end": v(6.29, 2.58) * mm});
            skLineSegment(sketch, "E5005", {"start": v(6.29, 2.58) * mm, "end": v(6.36, 2.58) * mm});
            skLineSegment(sketch, "E5006", {"start": v(6.36, 2.58) * mm, "end": v(6.43, 2.58) * mm});
            skLineSegment(sketch, "E5007", {"start": v(6.43, 2.58) * mm, "end": v(6.5, 2.58) * mm});
            skLineSegment(sketch, "E5008", {"start": v(6.5, 2.58) * mm, "end": v(6.57, 2.58) * mm});
            skLineSegment(sketch, "E5009", {"start": v(6.57, 2.58) * mm, "end": v(6.64, 2.58) * mm});
            skLineSegment(sketch, "E5010", {"start": v(6.64, 2.58) * mm, "end": v(6.7, 2.58) * mm});
            skLineSegment(sketch, "E5011", {"start": v(6.7, 2.58) * mm, "end": v(6.76, 2.58) * mm});
            skLineSegment(sketch, "E5012", {"start": v(6.76, 2.58) * mm, "end": v(6.82, 2.58) * mm});
            skLineSegment(sketch, "E5013", {"start": v(6.82, 2.58) * mm, "end": v(6.88, 2.58) * mm});
            skLineSegment(sketch, "E5014", {"start": v(6.88, 2.58) * mm, "end": v(6.93, 2.58) * mm});
            skLineSegment(sketch, "E5015", {"start": v(6.93, 2.58) * mm, "end": v(6.98, 2.58) * mm});
            skLineSegment(sketch, "E5016", {"start": v(6.98, 2.58) * mm, "end": v(7.03, 2.58) * mm});
            skLineSegment(sketch, "E5017", {"start": v(7.03, 2.58) * mm, "end": v(7.07, 2.58) * mm});
            skLineSegment(sketch, "E5018", {"start": v(7.07, 2.58) * mm, "end": v(7.1, 2.58) * mm});
            skLineSegment(sketch, "E5019", {"start": v(7.1, 2.58) * mm, "end": v(7.14, 2.58) * mm});
            skLineSegment(sketch, "E5020", {"start": v(7.14, 2.58) * mm, "end": v(7.17, 2.58) * mm});
            skLineSegment(sketch, "E5021", {"start": v(7.17, 2.58) * mm, "end": v(7.2, 2.58) * mm});
            skLineSegment(sketch, "E5022", {"start": v(7.2, 2.58) * mm, "end": v(7.21, 2.58) * mm});
            skLineSegment(sketch, "E5023", {"start": v(7.21, 2.58) * mm, "end": v(7.23, 2.58) * mm});
            skLineSegment(sketch, "E5024", {"start": v(7.23, 2.58) * mm, "end": v(7.24, 2.58) * mm});
            skLineSegment(sketch, "E5025", {"start": v(7.24, 2.58) * mm, "end": v(7.24, 2.58) * mm});
            skLineSegment(sketch, "E5026", {"start": v(7.24, 2.58) * mm, "end": v(7.25, 2.58) * mm});
            skLineSegment(sketch, "E5027", {"start": v(7.25, 2.58) * mm, "end": v(7.26, 2.58) * mm});
            skLineSegment(sketch, "E5028", {"start": v(7.26, 2.58) * mm, "end": v(7.26, 2.58) * mm});
            skLineSegment(sketch, "E5029", {"start": v(7.26, 2.58) * mm, "end": v(7.27, 2.58) * mm});
            skLineSegment(sketch, "E5030", {"start": v(7.27, 2.58) * mm, "end": v(7.27, 2.58) * mm});
            skLineSegment(sketch, "E5031", {"start": v(7.27, 2.58) * mm, "end": v(7.28, 2.57) * mm});
            skLineSegment(sketch, "E5032", {"start": v(7.28, 2.57) * mm, "end": v(7.28, 2.57) * mm});
            skLineSegment(sketch, "E5033", {"start": v(7.28, 2.57) * mm, "end": v(7.29, 2.57) * mm});
            skLineSegment(sketch, "E5034", {"start": v(7.29, 2.57) * mm, "end": v(7.3, 2.57) * mm});
            skLineSegment(sketch, "E5035", {"start": v(7.3, 2.57) * mm, "end": v(7.3, 2.57) * mm});
            skLineSegment(sketch, "E5036", {"start": v(7.3, 2.57) * mm, "end": v(7.31, 2.56) * mm});
            skLineSegment(sketch, "E5037", {"start": v(7.31, 2.56) * mm, "end": v(7.32, 2.56) * mm});
            skLineSegment(sketch, "E5038", {"start": v(7.32, 2.56) * mm, "end": v(7.32, 2.56) * mm});
            skLineSegment(sketch, "E5039", {"start": v(7.32, 2.56) * mm, "end": v(7.33, 2.56) * mm});
            skLineSegment(sketch, "E5040", {"start": v(7.33, 2.56) * mm, "end": v(7.33, 2.55) * mm});
            skLineSegment(sketch, "E5041", {"start": v(7.33, 2.55) * mm, "end": v(7.33, 2.55) * mm});
            skLineSegment(sketch, "E5042", {"start": v(7.33, 2.55) * mm, "end": v(7.34, 2.55) * mm});
            skLineSegment(sketch, "E5043", {"start": v(7.34, 2.55) * mm, "end": v(7.34, 2.55) * mm});
            skLineSegment(sketch, "E5044", {"start": v(7.34, 2.55) * mm, "end": v(7.35, 2.54) * mm});
            skLineSegment(sketch, "E5045", {"start": v(7.35, 2.54) * mm, "end": v(7.35, 2.54) * mm});
            skLineSegment(sketch, "E5046", {"start": v(7.35, 2.54) * mm, "end": v(7.36, 2.53) * mm});
            skLineSegment(sketch, "E5047", {"start": v(7.36, 2.53) * mm, "end": v(7.36, 2.53) * mm});
            skLineSegment(sketch, "E5048", {"start": v(7.36, 2.53) * mm, "end": v(7.37, 2.52) * mm});
            skLineSegment(sketch, "E5049", {"start": v(7.37, 2.52) * mm, "end": v(7.37, 2.52) * mm});
            skLineSegment(sketch, "E5050", {"start": v(7.37, 2.52) * mm, "end": v(7.38, 2.51) * mm});
            skLineSegment(sketch, "E5051", {"start": v(7.38, 2.51) * mm, "end": v(7.38, 2.51) * mm});
            skLineSegment(sketch, "E5052", {"start": v(7.38, 2.51) * mm, "end": v(7.38, 2.5) * mm});
            skLineSegment(sketch, "E5053", {"start": v(7.38, 2.5) * mm, "end": v(7.38, 2.5) * mm});
            skLineSegment(sketch, "E5054", {"start": v(7.38, 2.5) * mm, "end": v(7.39, 2.5) * mm});
            skLineSegment(sketch, "E5055", {"start": v(7.39, 2.5) * mm, "end": v(7.39, 2.5) * mm});
            skLineSegment(sketch, "E5056", {"start": v(7.39, 2.5) * mm, "end": v(7.4, 2.5) * mm});
            skLineSegment(sketch, "E5057", {"start": v(7.4, 2.5) * mm, "end": v(7.4, 2.49) * mm});
            skLineSegment(sketch, "E5058", {"start": v(7.4, 2.49) * mm, "end": v(7.4, 2.48) * mm});
            skLineSegment(sketch, "E5059", {"start": v(7.4, 2.48) * mm, "end": v(7.4, 2.48) * mm});
            skLineSegment(sketch, "E5060", {"start": v(7.4, 2.48) * mm, "end": v(7.4, 2.47) * mm});
            skLineSegment(sketch, "E5061", {"start": v(7.4, 2.47) * mm, "end": v(7.4, 2.47) * mm});
            skLineSegment(sketch, "E5062", {"start": v(7.4, 2.47) * mm, "end": v(7.4, 2.46) * mm});
            skLineSegment(sketch, "E5063", {"start": v(7.4, 2.46) * mm, "end": v(7.4, 2.46) * mm});
            skLineSegment(sketch, "E5064", {"start": v(7.4, 2.46) * mm, "end": v(7.4, 2.45) * mm});
            skLineSegment(sketch, "E5065", {"start": v(7.4, 2.45) * mm, "end": v(7.4, 2.45) * mm});
            skLineSegment(sketch, "E5066", {"start": v(7.4, 2.45) * mm, "end": v(7.4, 2.44) * mm});
            skLineSegment(sketch, "E5067", {"start": v(7.4, 2.44) * mm, "end": v(7.4, 2.44) * mm});
            skLineSegment(sketch, "E5068", {"start": v(7.4, 2.44) * mm, "end": v(7.4, 2.43) * mm});
            skLineSegment(sketch, "E5069", {"start": v(7.4, 2.43) * mm, "end": v(7.4, 2.43) * mm});
            skLineSegment(sketch, "E5070", {"start": v(7.4, 2.43) * mm, "end": v(7.4, 2.42) * mm});
            skLineSegment(sketch, "E5071", {"start": v(7.4, 2.42) * mm, "end": v(7.4, 2.42) * mm});
            skLineSegment(sketch, "E5072", {"start": v(7.4, 2.42) * mm, "end": v(7.4, 2.41) * mm});
            skLineSegment(sketch, "E5073", {"start": v(7.4, 2.41) * mm, "end": v(7.4, 2.4) * mm});
            skLineSegment(sketch, "E5074", {"start": v(7.4, 2.4) * mm, "end": v(7.4, 2.4) * mm});
            skLineSegment(sketch, "E5075", {"start": v(7.4, 2.4) * mm, "end": v(7.4, 2.39) * mm});
            skLineSegment(sketch, "E5076", {"start": v(7.4, 2.39) * mm, "end": v(7.4, 2.38) * mm});
            skLineSegment(sketch, "E5077", {"start": v(7.4, 2.38) * mm, "end": v(7.39, 2.38) * mm});
            skLineSegment(sketch, "E5078", {"start": v(7.39, 2.38) * mm, "end": v(7.39, 2.37) * mm});
            skLineSegment(sketch, "E5079", {"start": v(7.39, 2.37) * mm, "end": v(7.38, 2.37) * mm});
            skLineSegment(sketch, "E5080", {"start": v(7.38, 2.37) * mm, "end": v(7.38, 2.37) * mm});
            skLineSegment(sketch, "E5081", {"start": v(7.38, 2.37) * mm, "end": v(7.38, 2.36) * mm});
            skLineSegment(sketch, "E5082", {"start": v(7.38, 2.36) * mm, "end": v(7.38, 2.36) * mm});
            skLineSegment(sketch, "E5083", {"start": v(7.38, 2.36) * mm, "end": v(7.37, 2.35) * mm});
            skLineSegment(sketch, "E5084", {"start": v(7.37, 2.35) * mm, "end": v(7.37, 2.35) * mm});
            skLineSegment(sketch, "E5085", {"start": v(7.37, 2.35) * mm, "end": v(7.37, 2.34) * mm});
            skLineSegment(sketch, "E5086", {"start": v(7.37, 2.34) * mm, "end": v(7.36, 2.34) * mm});
            skLineSegment(sketch, "E5087", {"start": v(7.36, 2.34) * mm, "end": v(7.36, 2.34) * mm});
            skLineSegment(sketch, "E5088", {"start": v(7.36, 2.34) * mm, "end": v(7.36, 2.33) * mm});
            skLineSegment(sketch, "E5089", {"start": v(7.36, 2.33) * mm, "end": v(7.35, 2.33) * mm});
            skLineSegment(sketch, "E5090", {"start": v(7.35, 2.33) * mm, "end": v(7.35, 2.32) * mm});
            skLineSegment(sketch, "E5091", {"start": v(7.35, 2.32) * mm, "end": v(7.34, 2.32) * mm});
            skLineSegment(sketch, "E5092", {"start": v(7.34, 2.32) * mm, "end": v(7.34, 2.32) * mm});
            skLineSegment(sketch, "E5093", {"start": v(7.34, 2.32) * mm, "end": v(7.33, 2.31) * mm});
            skLineSegment(sketch, "E5094", {"start": v(7.33, 2.31) * mm, "end": v(7.33, 2.3) * mm});
            skLineSegment(sketch, "E5095", {"start": v(7.33, 2.3) * mm, "end": v(7.32, 2.3) * mm});
            skLineSegment(sketch, "E5096", {"start": v(7.32, 2.3) * mm, "end": v(7.32, 2.3) * mm});
            skLineSegment(sketch, "E5097", {"start": v(7.32, 2.3) * mm, "end": v(7.31, 2.3) * mm});
            skLineSegment(sketch, "E5098", {"start": v(7.31, 2.3) * mm, "end": v(7.3, 2.3) * mm});
            skLineSegment(sketch, "E5099", {"start": v(7.3, 2.3) * mm, "end": v(7.3, 2.3) * mm});
            skLineSegment(sketch, "E5100", {"start": v(7.3, 2.3) * mm, "end": v(7.29, 2.29) * mm});
            skLineSegment(sketch, "E5101", {"start": v(7.29, 2.29) * mm, "end": v(7.28, 2.29) * mm});
            skLineSegment(sketch, "E5102", {"start": v(7.28, 2.29) * mm, "end": v(7.28, 2.28) * mm});
            skLineSegment(sketch, "E5103", {"start": v(7.28, 2.28) * mm, "end": v(7.27, 2.28) * mm});
            skLineSegment(sketch, "E5104", {"start": v(7.27, 2.28) * mm, "end": v(7.26, 2.28) * mm});
            skLineSegment(sketch, "E5105", {"start": v(7.26, 2.28) * mm, "end": v(7.25, 2.28) * mm});
            skLineSegment(sketch, "E5106", {"start": v(7.25, 2.28) * mm, "end": v(7.25, 2.28) * mm});
            skLineSegment(sketch, "E5107", {"start": v(7.25, 2.28) * mm, "end": v(7.24, 2.28) * mm});
            skLineSegment(sketch, "E5108", {"start": v(7.24, 2.28) * mm, "end": v(7.23, 2.27) * mm});
            skLineSegment(sketch, "E5109", {"start": v(7.23, 2.27) * mm, "end": v(7.22, 2.27) * mm});
            skLineSegment(sketch, "E5110", {"start": v(7.22, 2.27) * mm, "end": v(7.22, 2.27) * mm});
            skLineSegment(sketch, "E5111", {"start": v(7.22, 2.27) * mm, "end": v(7.2, 2.27) * mm});
            skLineSegment(sketch, "E5112", {"start": v(7.2, 2.27) * mm, "end": v(7.2, 2.27) * mm});
            skLineSegment(sketch, "E5113", {"start": v(7.2, 2.27) * mm, "end": v(7.19, 2.27) * mm});
            skLineSegment(sketch, "E5114", {"start": v(7.19, 2.27) * mm, "end": v(7.18, 2.27) * mm});
            skLineSegment(sketch, "E5115", {"start": v(7.18, 2.27) * mm, "end": v(7.17, 2.27) * mm});
            skLineSegment(sketch, "E5116", {"start": v(7.17, 2.27) * mm, "end": v(7.16, 2.27) * mm});
            skLineSegment(sketch, "E5117", {"start": v(7.16, 2.27) * mm, "end": v(7.14, 2.27) * mm});
            skLineSegment(sketch, "E5118", {"start": v(7.14, 2.27) * mm, "end": v(7.11, 2.27) * mm});
            skLineSegment(sketch, "E5119", {"start": v(7.11, 2.27) * mm, "end": v(7.09, 2.27) * mm});
            skLineSegment(sketch, "E5120", {"start": v(7.09, 2.27) * mm, "end": v(7.05, 2.27) * mm});
            skLineSegment(sketch, "E5121", {"start": v(7.05, 2.27) * mm, "end": v(7.02, 2.27) * mm});
            skLineSegment(sketch, "E5122", {"start": v(7.02, 2.27) * mm, "end": v(6.98, 2.27) * mm});
            skLineSegment(sketch, "E5123", {"start": v(6.98, 2.27) * mm, "end": v(6.94, 2.27) * mm});
            skLineSegment(sketch, "E5124", {"start": v(6.94, 2.27) * mm, "end": v(6.9, 2.27) * mm});
            skLineSegment(sketch, "E5125", {"start": v(6.9, 2.27) * mm, "end": v(6.86, 2.27) * mm});
            skLineSegment(sketch, "E5126", {"start": v(6.86, 2.27) * mm, "end": v(6.8, 2.27) * mm});
            skLineSegment(sketch, "E5127", {"start": v(6.8, 2.27) * mm, "end": v(6.76, 2.27) * mm});
            skLineSegment(sketch, "E5128", {"start": v(6.76, 2.27) * mm, "end": v(6.7, 2.27) * mm});
            skLineSegment(sketch, "E5129", {"start": v(6.7, 2.27) * mm, "end": v(6.65, 2.27) * mm});
            skLineSegment(sketch, "E5130", {"start": v(6.65, 2.27) * mm, "end": v(6.6, 2.27) * mm});
            skLineSegment(sketch, "E5131", {"start": v(6.6, 2.27) * mm, "end": v(6.54, 2.27) * mm});
            skLineSegment(sketch, "E5132", {"start": v(6.54, 2.27) * mm, "end": v(6.49, 2.27) * mm});
            skLineSegment(sketch, "E5133", {"start": v(6.49, 2.27) * mm, "end": v(6.43, 2.27) * mm});
            skLineSegment(sketch, "E5134", {"start": v(6.43, 2.27) * mm, "end": v(6.37, 2.27) * mm});
            skLineSegment(sketch, "E5135", {"start": v(6.37, 2.27) * mm, "end": v(6.31, 2.27) * mm});
            skLineSegment(sketch, "E5136", {"start": v(6.31, 2.27) * mm, "end": v(6.25, 2.27) * mm});
            skLineSegment(sketch, "E5137", {"start": v(6.25, 2.27) * mm, "end": v(6.2, 2.27) * mm});
            skLineSegment(sketch, "E5138", {"start": v(6.2, 2.27) * mm, "end": v(6.13, 2.27) * mm});
            skLineSegment(sketch, "E5139", {"start": v(6.13, 2.27) * mm, "end": v(6.07, 2.27) * mm});
            skLineSegment(sketch, "E5140", {"start": v(6.07, 2.27) * mm, "end": v(6.01, 2.27) * mm});
            skLineSegment(sketch, "E5141", {"start": v(6.01, 2.27) * mm, "end": v(5.95, 2.27) * mm});
            skLineSegment(sketch, "E5142", {"start": v(5.95, 2.27) * mm, "end": v(5.9, 2.27) * mm});
            skLineSegment(sketch, "E5143", {"start": v(5.9, 2.27) * mm, "end": v(5.84, 2.27) * mm});
            skLineSegment(sketch, "E5144", {"start": v(5.84, 2.27) * mm, "end": v(5.78, 2.27) * mm});
            skLineSegment(sketch, "E5145", {"start": v(5.78, 2.27) * mm, "end": v(5.73, 2.27) * mm});
            skLineSegment(sketch, "E5146", {"start": v(5.73, 2.27) * mm, "end": v(5.67, 2.27) * mm});
            skLineSegment(sketch, "E5147", {"start": v(5.67, 2.27) * mm, "end": v(5.62, 2.27) * mm});
            skLineSegment(sketch, "E5148", {"start": v(5.62, 2.27) * mm, "end": v(5.57, 2.27) * mm});
            skLineSegment(sketch, "E5149", {"start": v(5.57, 2.27) * mm, "end": v(5.53, 2.27) * mm});
            skLineSegment(sketch, "E5150", {"start": v(5.53, 2.27) * mm, "end": v(5.48, 2.27) * mm});
            skLineSegment(sketch, "E5151", {"start": v(5.48, 2.27) * mm, "end": v(5.44, 2.27) * mm});
            skLineSegment(sketch, "E5152", {"start": v(5.44, 2.27) * mm, "end": v(5.4, 2.27) * mm});
            skLineSegment(sketch, "E5153", {"start": v(5.4, 2.27) * mm, "end": v(5.36, 2.27) * mm});
            skLineSegment(sketch, "E5154", {"start": v(5.36, 2.27) * mm, "end": v(5.33, 2.27) * mm});
            skLineSegment(sketch, "E5155", {"start": v(5.33, 2.27) * mm, "end": v(5.3, 2.27) * mm});
            skLineSegment(sketch, "E5156", {"start": v(5.3, 2.27) * mm, "end": v(5.27, 2.27) * mm});
            skLineSegment(sketch, "E5157", {"start": v(5.27, 2.27) * mm, "end": v(5.25, 2.27) * mm});
            skLineSegment(sketch, "E5158", {"start": v(5.25, 2.27) * mm, "end": v(5.23, 2.27) * mm});
            skLineSegment(sketch, "E5159", {"start": v(5.23, 2.27) * mm, "end": v(5.21, 2.27) * mm});
            skLineSegment(sketch, "E5160", {"start": v(5.21, 2.27) * mm, "end": v(5.2, 2.27) * mm});
            skLineSegment(sketch, "E5161", {"start": v(5.2, 2.27) * mm, "end": v(5.2, 2.27) * mm});
            skLineSegment(sketch, "E5162", {"start": v(5.2, 2.27) * mm, "end": v(5.19, 2.27) * mm});
            skLineSegment(sketch, "E5163", {"start": v(5.19, 2.27) * mm, "end": v(5.17, 2.27) * mm});
            skLineSegment(sketch, "E5164", {"start": v(5.17, 2.27) * mm, "end": v(5.16, 2.27) * mm});
            skLineSegment(sketch, "E5165", {"start": v(5.16, 2.27) * mm, "end": v(5.14, 2.27) * mm});
            skLineSegment(sketch, "E5166", {"start": v(5.14, 2.27) * mm, "end": v(5.13, 2.27) * mm});
            skLineSegment(sketch, "E5167", {"start": v(5.13, 2.27) * mm, "end": v(5.12, 2.27) * mm});
            skLineSegment(sketch, "E5168", {"start": v(5.12, 2.27) * mm, "end": v(5.1, 2.27) * mm});
            skLineSegment(sketch, "E5169", {"start": v(5.1, 2.27) * mm, "end": v(5.09, 2.27) * mm});
            skLineSegment(sketch, "E5170", {"start": v(5.09, 2.27) * mm, "end": v(5.07, 2.27) * mm});
            skLineSegment(sketch, "E5171", {"start": v(5.07, 2.27) * mm, "end": v(5.06, 2.26) * mm});
            skLineSegment(sketch, "E5172", {"start": v(5.06, 2.26) * mm, "end": v(5.05, 2.26) * mm});
            skLineSegment(sketch, "E5173", {"start": v(5.05, 2.26) * mm, "end": v(5.04, 2.26) * mm});
            skLineSegment(sketch, "E5174", {"start": v(5.04, 2.26) * mm, "end": v(5.02, 2.26) * mm});
            skLineSegment(sketch, "E5175", {"start": v(5.02, 2.26) * mm, "end": v(5.01, 2.26) * mm});
            skLineSegment(sketch, "E5176", {"start": v(5.01, 2.26) * mm, "end": v(5, 2.25) * mm});
            skLineSegment(sketch, "E5177", {"start": v(5, 2.25) * mm, "end": v(4.99, 2.25) * mm});
            skLineSegment(sketch, "E5178", {"start": v(4.99, 2.25) * mm, "end": v(4.98, 2.25) * mm});
            skLineSegment(sketch, "E5179", {"start": v(4.98, 2.25) * mm, "end": v(4.97, 2.24) * mm});
            skLineSegment(sketch, "E5180", {"start": v(4.97, 2.24) * mm, "end": v(4.96, 2.24) * mm});
            skLineSegment(sketch, "E5181", {"start": v(4.96, 2.24) * mm, "end": v(4.95, 2.23) * mm});
            skLineSegment(sketch, "E5182", {"start": v(4.95, 2.23) * mm, "end": v(4.94, 2.23) * mm});
            skLineSegment(sketch, "E5183", {"start": v(4.94, 2.23) * mm, "end": v(4.93, 2.22) * mm});
            skLineSegment(sketch, "E5184", {"start": v(4.93, 2.22) * mm, "end": v(4.92, 2.22) * mm});
            skLineSegment(sketch, "E5185", {"start": v(4.92, 2.22) * mm, "end": v(4.9, 2.21) * mm});
            skLineSegment(sketch, "E5186", {"start": v(4.9, 2.21) * mm, "end": v(4.9, 2.2) * mm});
            skLineSegment(sketch, "E5187", {"start": v(4.9, 2.2) * mm, "end": v(4.9, 2.2) * mm});
            skLineSegment(sketch, "E5188", {"start": v(4.9, 2.2) * mm, "end": v(4.88, 2.2) * mm});
            skLineSegment(sketch, "E5189", {"start": v(4.88, 2.2) * mm, "end": v(4.88, 2.19) * mm});
            skLineSegment(sketch, "E5190", {"start": v(4.88, 2.19) * mm, "end": v(4.87, 2.18) * mm});
            skLineSegment(sketch, "E5191", {"start": v(4.87, 2.18) * mm, "end": v(4.86, 2.17) * mm});
            skLineSegment(sketch, "E5192", {"start": v(4.86, 2.17) * mm, "end": v(4.86, 2.17) * mm});
            skLineSegment(sketch, "E5193", {"start": v(4.86, 2.17) * mm, "end": v(4.85, 2.16) * mm});
            skLineSegment(sketch, "E5194", {"start": v(4.85, 2.16) * mm, "end": v(4.84, 2.15) * mm});
            skLineSegment(sketch, "E5195", {"start": v(4.84, 2.15) * mm, "end": v(4.84, 2.14) * mm});
            skLineSegment(sketch, "E5196", {"start": v(4.84, 2.14) * mm, "end": v(4.83, 2.13) * mm});
            skLineSegment(sketch, "E5197", {"start": v(4.83, 2.13) * mm, "end": v(4.83, 2.12) * mm});
            skLineSegment(sketch, "E5198", {"start": v(4.83, 2.12) * mm, "end": v(4.82, 2.1) * mm});
            skLineSegment(sketch, "E5199", {"start": v(4.82, 2.1) * mm, "end": v(4.82, 2.1) * mm});
            skLineSegment(sketch, "E5200", {"start": v(4.82, 2.1) * mm, "end": v(4.81, 2.09) * mm});
            skLineSegment(sketch, "E5201", {"start": v(4.81, 2.09) * mm, "end": v(4.8, 2.08) * mm});
            skLineSegment(sketch, "E5202", {"start": v(4.8, 2.08) * mm, "end": v(4.8, 2.06) * mm});
            skLineSegment(sketch, "E5203", {"start": v(4.8, 2.06) * mm, "end": v(4.8, 2.05) * mm});
            skLineSegment(sketch, "E5204", {"start": v(4.8, 2.05) * mm, "end": v(4.8, 2.04) * mm});
            skLineSegment(sketch, "E5205", {"start": v(4.8, 2.04) * mm, "end": v(4.8, 2.03) * mm});
            skLineSegment(sketch, "E5206", {"start": v(4.8, 2.03) * mm, "end": v(4.8, 2.01) * mm});
            skLineSegment(sketch, "E5207", {"start": v(4.8, 2.01) * mm, "end": v(4.8, 2) * mm});
            skLineSegment(sketch, "E5208", {"start": v(4.8, 2) * mm, "end": v(4.8, 1.98) * mm});
            skLineSegment(sketch, "E5209", {"start": v(4.8, 1.98) * mm, "end": v(4.8, 1.97) * mm});
            skLineSegment(sketch, "E5210", {"start": v(4.8, 1.97) * mm, "end": v(4.79, 1.95) * mm});
            skLineSegment(sketch, "E5211", {"start": v(4.79, 1.95) * mm, "end": v(4.79, 1.94) * mm});
            skLineSegment(sketch, "E5212", {"start": v(4.79, 1.94) * mm, "end": v(4.79, 1.92) * mm});
            skLineSegment(sketch, "E5213", {"start": v(4.79, 1.92) * mm, "end": v(4.79, 1.92) * mm});
            skLineSegment(sketch, "E5214", {"start": v(4.79, 1.92) * mm, "end": v(4.79, 1.91) * mm});
            skLineSegment(sketch, "E5215", {"start": v(4.79, 1.91) * mm, "end": v(4.79, 1.9) * mm});
            skLineSegment(sketch, "E5216", {"start": v(4.79, 1.9) * mm, "end": v(4.79, 1.9) * mm});
            skLineSegment(sketch, "E5217", {"start": v(4.79, 1.9) * mm, "end": v(4.79, 1.88) * mm});
            skLineSegment(sketch, "E5218", {"start": v(4.79, 1.88) * mm, "end": v(4.79, 1.86) * mm});
            skLineSegment(sketch, "E5219", {"start": v(4.79, 1.86) * mm, "end": v(4.79, 1.84) * mm});
            skLineSegment(sketch, "E5220", {"start": v(4.79, 1.84) * mm, "end": v(4.79, 1.81) * mm});
            skLineSegment(sketch, "E5221", {"start": v(4.79, 1.81) * mm, "end": v(4.79, 1.79) * mm});
            skLineSegment(sketch, "E5222", {"start": v(4.79, 1.79) * mm, "end": v(4.79, 1.76) * mm});
            skLineSegment(sketch, "E5223", {"start": v(4.79, 1.76) * mm, "end": v(4.79, 1.73) * mm});
            skLineSegment(sketch, "E5224", {"start": v(4.79, 1.73) * mm, "end": v(4.79, 1.7) * mm});
            skLineSegment(sketch, "E5225", {"start": v(4.79, 1.7) * mm, "end": v(4.79, 1.66) * mm});
            skLineSegment(sketch, "E5226", {"start": v(4.79, 1.66) * mm, "end": v(4.79, 1.63) * mm});
            skLineSegment(sketch, "E5227", {"start": v(4.79, 1.63) * mm, "end": v(4.79, 1.59) * mm});
            skLineSegment(sketch, "E5228", {"start": v(4.79, 1.59) * mm, "end": v(4.79, 1.55) * mm});
            skLineSegment(sketch, "E5229", {"start": v(4.79, 1.55) * mm, "end": v(4.79, 1.5) * mm});
            skLineSegment(sketch, "E5230", {"start": v(4.79, 1.5) * mm, "end": v(4.79, 1.47) * mm});
            skLineSegment(sketch, "E5231", {"start": v(4.79, 1.47) * mm, "end": v(4.79, 1.42) * mm});
            skLineSegment(sketch, "E5232", {"start": v(4.79, 1.42) * mm, "end": v(4.79, 1.38) * mm});
            skLineSegment(sketch, "E5233", {"start": v(4.79, 1.38) * mm, "end": v(4.79, 1.34) * mm});
            skLineSegment(sketch, "E5234", {"start": v(4.79, 1.34) * mm, "end": v(4.79, 1.3) * mm});
            skLineSegment(sketch, "E5235", {"start": v(4.79, 1.3) * mm, "end": v(4.79, 1.24) * mm});
            skLineSegment(sketch, "E5236", {"start": v(4.79, 1.24) * mm, "end": v(4.79, 1.2) * mm});
            skLineSegment(sketch, "E5237", {"start": v(4.79, 1.2) * mm, "end": v(4.79, 1.15) * mm});
            skLineSegment(sketch, "E5238", {"start": v(4.79, 1.15) * mm, "end": v(4.79, 1.1) * mm});
            skLineSegment(sketch, "E5239", {"start": v(4.79, 1.1) * mm, "end": v(4.79, 1.06) * mm});
            skLineSegment(sketch, "E5240", {"start": v(4.79, 1.06) * mm, "end": v(4.79, 1.02) * mm});
            skLineSegment(sketch, "E5241", {"start": v(4.79, 1.02) * mm, "end": v(4.79, 0.97) * mm});
            skLineSegment(sketch, "E5242", {"start": v(4.79, 0.97) * mm, "end": v(4.79, 0.93) * mm});
            skLineSegment(sketch, "E5243", {"start": v(4.79, 0.93) * mm, "end": v(4.79, 0.88) * mm});
            skLineSegment(sketch, "E5244", {"start": v(4.79, 0.88) * mm, "end": v(4.79, 0.84) * mm});
            skLineSegment(sketch, "E5245", {"start": v(4.79, 0.84) * mm, "end": v(4.79, 0.8) * mm});
            skLineSegment(sketch, "E5246", {"start": v(4.79, 0.8) * mm, "end": v(4.79, 0.76) * mm});
            skLineSegment(sketch, "E5247", {"start": v(4.79, 0.76) * mm, "end": v(4.79, 0.72) * mm});
            skLineSegment(sketch, "E5248", {"start": v(4.79, 0.72) * mm, "end": v(4.79, 0.68) * mm});
            skLineSegment(sketch, "E5249", {"start": v(4.79, 0.68) * mm, "end": v(4.79, 0.64) * mm});
            skLineSegment(sketch, "E5250", {"start": v(4.79, 0.64) * mm, "end": v(4.79, 0.6) * mm});
            skLineSegment(sketch, "E5251", {"start": v(4.79, 0.6) * mm, "end": v(4.79, 0.58) * mm});
            skLineSegment(sketch, "E5252", {"start": v(4.79, 0.58) * mm, "end": v(4.79, 0.55) * mm});
            skLineSegment(sketch, "E5253", {"start": v(4.79, 0.55) * mm, "end": v(4.79, 0.52) * mm});
            skLineSegment(sketch, "E5254", {"start": v(4.79, 0.52) * mm, "end": v(4.79, 0.5) * mm});
            skLineSegment(sketch, "E5255", {"start": v(4.79, 0.5) * mm, "end": v(4.79, 0.47) * mm});
            skLineSegment(sketch, "E5256", {"start": v(4.79, 0.47) * mm, "end": v(4.79, 0.45) * mm});
            skLineSegment(sketch, "E5257", {"start": v(4.79, 0.45) * mm, "end": v(4.79, 0.43) * mm});
            skLineSegment(sketch, "E5258", {"start": v(4.79, 0.43) * mm, "end": v(4.79, 0.42) * mm});
            skLineSegment(sketch, "E5259", {"start": v(4.79, 0.42) * mm, "end": v(4.79, 0.4) * mm});
            skLineSegment(sketch, "E5260", {"start": v(4.79, 0.4) * mm, "end": v(4.79, 0.4) * mm});
            skLineSegment(sketch, "E5261", {"start": v(4.79, 0.4) * mm, "end": v(4.79, 0.39) * mm});
            skLineSegment(sketch, "E5262", {"start": v(4.79, 0.39) * mm, "end": v(4.79, 0.39) * mm});
            skLineSegment(sketch, "E5263", {"start": v(4.79, 0.39) * mm, "end": v(4.79, 0.38) * mm});
            skLineSegment(sketch, "E5264", {"start": v(4.79, 0.38) * mm, "end": v(4.79, 0.37) * mm});
            skLineSegment(sketch, "E5265", {"start": v(4.79, 0.37) * mm, "end": v(4.79, 0.35) * mm});
            skLineSegment(sketch, "E5266", {"start": v(4.79, 0.35) * mm, "end": v(4.8, 0.34) * mm});
            skLineSegment(sketch, "E5267", {"start": v(4.8, 0.34) * mm, "end": v(4.8, 0.33) * mm});
            skLineSegment(sketch, "E5268", {"start": v(4.8, 0.33) * mm, "end": v(4.8, 0.32) * mm});
            skLineSegment(sketch, "E5269", {"start": v(4.8, 0.32) * mm, "end": v(4.8, 0.31) * mm});
            skLineSegment(sketch, "E5270", {"start": v(4.8, 0.31) * mm, "end": v(4.8, 0.3) * mm});
            skLineSegment(sketch, "E5271", {"start": v(4.8, 0.3) * mm, "end": v(4.8, 0.3) * mm});
            skLineSegment(sketch, "E5272", {"start": v(4.8, 0.3) * mm, "end": v(4.8, 0.29) * mm});
            skLineSegment(sketch, "E5273", {"start": v(4.8, 0.29) * mm, "end": v(4.8, 0.28) * mm});
            skLineSegment(sketch, "E5274", {"start": v(4.8, 0.28) * mm, "end": v(4.8, 0.27) * mm});
            skLineSegment(sketch, "E5275", {"start": v(4.8, 0.27) * mm, "end": v(4.8, 0.26) * mm});
            skLineSegment(sketch, "E5276", {"start": v(4.8, 0.26) * mm, "end": v(4.81, 0.26) * mm});
            skLineSegment(sketch, "E5277", {"start": v(4.81, 0.26) * mm, "end": v(4.81, 0.25) * mm});
            skLineSegment(sketch, "E5278", {"start": v(4.81, 0.25) * mm, "end": v(4.82, 0.24) * mm});
            skLineSegment(sketch, "E5279", {"start": v(4.82, 0.24) * mm, "end": v(4.82, 0.23) * mm});
            skLineSegment(sketch, "E5280", {"start": v(4.82, 0.23) * mm, "end": v(4.83, 0.23) * mm});
            skLineSegment(sketch, "E5281", {"start": v(4.83, 0.23) * mm, "end": v(4.83, 0.22) * mm});
            skLineSegment(sketch, "E5282", {"start": v(4.83, 0.22) * mm, "end": v(4.83, 0.21) * mm});
            skLineSegment(sketch, "E5283", {"start": v(4.83, 0.21) * mm, "end": v(4.84, 0.2) * mm});
            skLineSegment(sketch, "E5284", {"start": v(4.84, 0.2) * mm, "end": v(4.84, 0.2) * mm});
            skLineSegment(sketch, "E5285", {"start": v(4.84, 0.2) * mm, "end": v(4.85, 0.2) * mm});
            skLineSegment(sketch, "E5286", {"start": v(4.85, 0.2) * mm, "end": v(4.85, 0.2) * mm});
            skLineSegment(sketch, "E5287", {"start": v(4.85, 0.2) * mm, "end": v(4.86, 0.19) * mm});
            skLineSegment(sketch, "E5288", {"start": v(4.86, 0.19) * mm, "end": v(4.87, 0.18) * mm});
            skLineSegment(sketch, "E5289", {"start": v(4.87, 0.18) * mm, "end": v(4.87, 0.18) * mm});
            skLineSegment(sketch, "E5290", {"start": v(4.87, 0.18) * mm, "end": v(4.88, 0.17) * mm});
            skLineSegment(sketch, "E5291", {"start": v(4.88, 0.17) * mm, "end": v(4.88, 0.17) * mm});
            skLineSegment(sketch, "E5292", {"start": v(4.88, 0.17) * mm, "end": v(4.9, 0.17) * mm});
            skLineSegment(sketch, "E5293", {"start": v(4.9, 0.17) * mm, "end": v(4.9, 0.16) * mm});
            skLineSegment(sketch, "E5294", {"start": v(4.9, 0.16) * mm, "end": v(4.9, 0.16) * mm});
            skLineSegment(sketch, "E5295", {"start": v(4.9, 0.16) * mm, "end": v(4.91, 0.15) * mm});
            skLineSegment(sketch, "E5296", {"start": v(4.91, 0.15) * mm, "end": v(4.92, 0.15) * mm});
            skLineSegment(sketch, "E5297", {"start": v(4.92, 0.15) * mm, "end": v(4.93, 0.15) * mm});
            skLineSegment(sketch, "E5298", {"start": v(4.93, 0.15) * mm, "end": v(4.94, 0.15) * mm});
            skLineSegment(sketch, "E5299", {"start": v(4.94, 0.15) * mm, "end": v(4.94, 0.14) * mm});
            skLineSegment(sketch, "E5300", {"start": v(4.94, 0.14) * mm, "end": v(4.95, 0.14) * mm});
            skLineSegment(sketch, "E5301", {"start": v(4.95, 0.14) * mm, "end": v(4.96, 0.14) * mm});
            skLineSegment(sketch, "E5302", {"start": v(4.96, 0.14) * mm, "end": v(4.97, 0.14) * mm});
            skLineSegment(sketch, "E5303", {"start": v(4.97, 0.14) * mm, "end": v(4.98, 0.14) * mm});
            skLineSegment(sketch, "E5304", {"start": v(4.98, 0.14) * mm, "end": v(4.99, 0.13) * mm});
            skLineSegment(sketch, "E5305", {"start": v(4.99, 0.13) * mm, "end": v(5, 0.13) * mm});
            skLineSegment(sketch, "E5306", {"start": v(5, 0.13) * mm, "end": v(5, 0.13) * mm});
            skLineSegment(sketch, "E5307", {"start": v(5, 0.13) * mm, "end": v(5.02, 0.13) * mm});
            skLineSegment(sketch, "E5308", {"start": v(5.02, 0.13) * mm, "end": v(5.03, 0.13) * mm});
            skLineSegment(sketch, "E5309", {"start": v(5.03, 0.13) * mm, "end": v(5.04, 0.13) * mm});
            skLineSegment(sketch, "E5310", {"start": v(5.04, 0.13) * mm, "end": v(5.05, 0.13) * mm});
            skLineSegment(sketch, "E5311", {"start": v(5.05, 0.13) * mm, "end": v(5.06, 0.13) * mm});
            skLineSegment(sketch, "E5312", {"start": v(5.06, 0.13) * mm, "end": v(5.07, 0.13) * mm});
            skLineSegment(sketch, "E5313", {"start": v(5.07, 0.13) * mm, "end": v(5.07, 0.13) * mm});
            skLineSegment(sketch, "E5314", {"start": v(5.07, 0.13) * mm, "end": v(5.08, 0.13) * mm});
            skLineSegment(sketch, "E5315", {"start": v(5.08, 0.13) * mm, "end": v(5.1, 0.13) * mm});
            skLineSegment(sketch, "E5316", {"start": v(5.1, 0.13) * mm, "end": v(5.1, 0.13) * mm});
            skLineSegment(sketch, "E5317", {"start": v(5.1, 0.13) * mm, "end": v(5.13, 0.13) * mm});
            skLineSegment(sketch, "E5318", {"start": v(5.13, 0.13) * mm, "end": v(5.15, 0.13) * mm});
            skLineSegment(sketch, "E5319", {"start": v(5.15, 0.13) * mm, "end": v(5.18, 0.13) * mm});
            skLineSegment(sketch, "E5320", {"start": v(5.18, 0.13) * mm, "end": v(5.2, 0.13) * mm});
            skLineSegment(sketch, "E5321", {"start": v(5.2, 0.13) * mm, "end": v(5.24, 0.13) * mm});
            skLineSegment(sketch, "E5322", {"start": v(5.24, 0.13) * mm, "end": v(5.27, 0.13) * mm});
            skLineSegment(sketch, "E5323", {"start": v(5.27, 0.13) * mm, "end": v(5.31, 0.13) * mm});
            skLineSegment(sketch, "E5324", {"start": v(5.31, 0.13) * mm, "end": v(5.36, 0.13) * mm});
            skLineSegment(sketch, "E5325", {"start": v(5.36, 0.13) * mm, "end": v(5.4, 0.13) * mm});
            skLineSegment(sketch, "E5326", {"start": v(5.4, 0.13) * mm, "end": v(5.45, 0.13) * mm});
            skLineSegment(sketch, "E5327", {"start": v(5.45, 0.13) * mm, "end": v(5.5, 0.13) * mm});
            skLineSegment(sketch, "E5328", {"start": v(5.5, 0.13) * mm, "end": v(5.54, 0.13) * mm});
            skLineSegment(sketch, "E5329", {"start": v(5.54, 0.13) * mm, "end": v(5.6, 0.13) * mm});
            skLineSegment(sketch, "E5330", {"start": v(5.6, 0.13) * mm, "end": v(5.65, 0.13) * mm});
            skLineSegment(sketch, "E5331", {"start": v(5.65, 0.13) * mm, "end": v(5.7, 0.13) * mm});
            skLineSegment(sketch, "E5332", {"start": v(5.7, 0.13) * mm, "end": v(5.76, 0.13) * mm});
            skLineSegment(sketch, "E5333", {"start": v(5.76, 0.13) * mm, "end": v(5.82, 0.13) * mm});
            skLineSegment(sketch, "E5334", {"start": v(5.82, 0.13) * mm, "end": v(5.87, 0.13) * mm});
            skLineSegment(sketch, "E5335", {"start": v(5.87, 0.13) * mm, "end": v(5.93, 0.13) * mm});
            skLineSegment(sketch, "E5336", {"start": v(5.93, 0.13) * mm, "end": v(6, 0.13) * mm});
            skLineSegment(sketch, "E5337", {"start": v(6, 0.13) * mm, "end": v(6.05, 0.13) * mm});
            skLineSegment(sketch, "E5338", {"start": v(6.05, 0.13) * mm, "end": v(6.1, 0.13) * mm});
            skLineSegment(sketch, "E5339", {"start": v(6.1, 0.13) * mm, "end": v(6.17, 0.13) * mm});
            skLineSegment(sketch, "E5340", {"start": v(6.17, 0.13) * mm, "end": v(6.22, 0.13) * mm});
            skLineSegment(sketch, "E5341", {"start": v(6.22, 0.13) * mm, "end": v(6.28, 0.13) * mm});
            skLineSegment(sketch, "E5342", {"start": v(6.28, 0.13) * mm, "end": v(6.34, 0.13) * mm});
            skLineSegment(sketch, "E5343", {"start": v(6.34, 0.13) * mm, "end": v(6.4, 0.13) * mm});
            skLineSegment(sketch, "E5344", {"start": v(6.4, 0.13) * mm, "end": v(6.45, 0.13) * mm});
            skLineSegment(sketch, "E5345", {"start": v(6.45, 0.13) * mm, "end": v(6.5, 0.13) * mm});
            skLineSegment(sketch, "E5346", {"start": v(6.5, 0.13) * mm, "end": v(6.55, 0.13) * mm});
            skLineSegment(sketch, "E5347", {"start": v(6.55, 0.13) * mm, "end": v(6.6, 0.13) * mm});
            skLineSegment(sketch, "E5348", {"start": v(6.6, 0.13) * mm, "end": v(6.65, 0.13) * mm});
            skLineSegment(sketch, "E5349", {"start": v(6.65, 0.13) * mm, "end": v(6.7, 0.13) * mm});
            skLineSegment(sketch, "E5350", {"start": v(6.7, 0.13) * mm, "end": v(6.74, 0.13) * mm});
            skLineSegment(sketch, "E5351", {"start": v(6.74, 0.13) * mm, "end": v(6.78, 0.13) * mm});
            skLineSegment(sketch, "E5352", {"start": v(6.78, 0.13) * mm, "end": v(6.82, 0.13) * mm});
            skLineSegment(sketch, "E5353", {"start": v(6.82, 0.13) * mm, "end": v(6.86, 0.13) * mm});
            skLineSegment(sketch, "E5354", {"start": v(6.86, 0.13) * mm, "end": v(6.9, 0.13) * mm});
            skLineSegment(sketch, "E5355", {"start": v(6.9, 0.13) * mm, "end": v(6.92, 0.13) * mm});
            skLineSegment(sketch, "E5356", {"start": v(6.92, 0.13) * mm, "end": v(6.95, 0.13) * mm});
            skLineSegment(sketch, "E5357", {"start": v(6.95, 0.13) * mm, "end": v(6.97, 0.13) * mm});
            skLineSegment(sketch, "E5358", {"start": v(6.97, 0.13) * mm, "end": v(7, 0.13) * mm});
            skLineSegment(sketch, "E5359", {"start": v(7, 0.13) * mm, "end": v(7, 0.13) * mm});
            skLineSegment(sketch, "E5360", {"start": v(7, 0.13) * mm, "end": v(7.02, 0.13) * mm});
            skLineSegment(sketch, "E5361", {"start": v(7.02, 0.13) * mm, "end": v(7.02, 0.13) * mm});
            skLineSegment(sketch, "E5362", {"start": v(7.02, 0.13) * mm, "end": v(7.03, 0.13) * mm});
            skLineSegment(sketch, "E5363", {"start": v(7.03, 0.13) * mm, "end": v(7.03, 0.13) * mm});
            skLineSegment(sketch, "E5364", {"start": v(7.03, 0.13) * mm, "end": v(7.04, 0.13) * mm});
            skLineSegment(sketch, "E5365", {"start": v(7.04, 0.13) * mm, "end": v(7.04, 0.13) * mm});
            skLineSegment(sketch, "E5366", {"start": v(7.04, 0.13) * mm, "end": v(7.05, 0.13) * mm});
            skLineSegment(sketch, "E5367", {"start": v(7.05, 0.13) * mm, "end": v(7.05, 0.13) * mm});
            skLineSegment(sketch, "E5368", {"start": v(7.05, 0.13) * mm, "end": v(7.06, 0.13) * mm});
            skLineSegment(sketch, "E5369", {"start": v(7.06, 0.13) * mm, "end": v(7.06, 0.12) * mm});
            skLineSegment(sketch, "E5370", {"start": v(7.06, 0.12) * mm, "end": v(7.07, 0.12) * mm});
            skLineSegment(sketch, "E5371", {"start": v(7.07, 0.12) * mm, "end": v(7.07, 0.12) * mm});
            skLineSegment(sketch, "E5372", {"start": v(7.07, 0.12) * mm, "end": v(7.08, 0.12) * mm});
            skLineSegment(sketch, "E5373", {"start": v(7.08, 0.12) * mm, "end": v(7.08, 0.12) * mm});
            skLineSegment(sketch, "E5374", {"start": v(7.08, 0.12) * mm, "end": v(7.09, 0.12) * mm});
            skLineSegment(sketch, "E5375", {"start": v(7.09, 0.12) * mm, "end": v(7.1, 0.11) * mm});
            skLineSegment(sketch, "E5376", {"start": v(7.1, 0.11) * mm, "end": v(7.1, 0.11) * mm});
            skLineSegment(sketch, "E5377", {"start": v(7.1, 0.11) * mm, "end": v(7.1, 0.1) * mm});
            skLineSegment(sketch, "E5378", {"start": v(7.1, 0.1) * mm, "end": v(7.1, 0.1) * mm});
            skLineSegment(sketch, "E5379", {"start": v(7.1, 0.1) * mm, "end": v(7.11, 0.1) * mm});
            skLineSegment(sketch, "E5380", {"start": v(7.11, 0.1) * mm, "end": v(7.11, 0.1) * mm});
            skLineSegment(sketch, "E5381", {"start": v(7.11, 0.1) * mm, "end": v(7.12, 0.1) * mm});
            skLineSegment(sketch, "E5382", {"start": v(7.12, 0.1) * mm, "end": v(7.12, 0.1) * mm});
            skLineSegment(sketch, "E5383", {"start": v(7.12, 0.1) * mm, "end": v(7.13, 0.09) * mm});
            skLineSegment(sketch, "E5384", {"start": v(7.13, 0.09) * mm, "end": v(7.13, 0.08) * mm});
            skLineSegment(sketch, "E5385", {"start": v(7.13, 0.08) * mm, "end": v(7.13, 0.08) * mm});
            skLineSegment(sketch, "E5386", {"start": v(7.13, 0.08) * mm, "end": v(7.14, 0.08) * mm});
            skLineSegment(sketch, "E5387", {"start": v(7.14, 0.08) * mm, "end": v(7.14, 0.07) * mm});
            skLineSegment(sketch, "E5388", {"start": v(7.14, 0.07) * mm, "end": v(7.14, 0.07) * mm});
            skLineSegment(sketch, "E5389", {"start": v(7.14, 0.07) * mm, "end": v(7.15, 0.06) * mm});
            skLineSegment(sketch, "E5390", {"start": v(7.15, 0.06) * mm, "end": v(7.15, 0.06) * mm});
            skLineSegment(sketch, "E5391", {"start": v(7.15, 0.06) * mm, "end": v(7.15, 0.05) * mm});
            skLineSegment(sketch, "E5392", {"start": v(7.15, 0.05) * mm, "end": v(7.15, 0.05) * mm});
            skLineSegment(sketch, "E5393", {"start": v(7.15, 0.05) * mm, "end": v(7.15, 0.04) * mm});
            skLineSegment(sketch, "E5394", {"start": v(7.15, 0.04) * mm, "end": v(7.16, 0.04) * mm});
            skLineSegment(sketch, "E5395", {"start": v(7.16, 0.04) * mm, "end": v(7.16, 0.04) * mm});
            skLineSegment(sketch, "E5396", {"start": v(7.16, 0.04) * mm, "end": v(7.16, 0.03) * mm});
            skLineSegment(sketch, "E5397", {"start": v(7.16, 0.03) * mm, "end": v(7.16, 0.03) * mm});
            skLineSegment(sketch, "E5398", {"start": v(7.16, 0.03) * mm, "end": v(7.16, 0.02) * mm});
            skLineSegment(sketch, "E5399", {"start": v(7.16, 0.02) * mm, "end": v(7.16, 0.02) * mm});
            skLineSegment(sketch, "E5400", {"start": v(7.16, 0.02) * mm, "end": v(7.16, 0.01) * mm});
            skLineSegment(sketch, "E5401", {"start": v(7.16, 0.01) * mm, "end": v(7.16, 0) * mm});
            skLineSegment(sketch, "E5402", {"start": v(7.16, 0) * mm, "end": v(7.17, 0) * mm});
            skLineSegment(sketch, "E5403", {"start": v(7.17, 0) * mm, "end": v(7.17, 0) * mm});
            skLineSegment(sketch, "E5404", {"start": v(7.17, 0) * mm, "end": v(7.17, -0.01) * mm});
            skLineSegment(sketch, "E5405", {"start": v(7.17, -0.01) * mm, "end": v(7.17, -0.02) * mm});
            skLineSegment(sketch, "E5406", {"start": v(7.17, -0.02) * mm, "end": v(7.17, -0.03) * mm});
            skLineSegment(sketch, "E5407", {"start": v(7.17, -0.03) * mm, "end": v(7.17, -0.03) * mm});
            skLineSegment(sketch, "E5408", {"start": v(7.17, -0.03) * mm, "end": v(7.17, -0.04) * mm});
            skLineSegment(sketch, "E5409", {"start": v(7.17, -0.04) * mm, "end": v(7.17, -0.04) * mm});
            skLineSegment(sketch, "E5410", {"start": v(7.17, -0.04) * mm, "end": v(7.17, -0.05) * mm});
            skLineSegment(sketch, "E5411", {"start": v(7.17, -0.05) * mm, "end": v(7.17, -0.05) * mm});
            skLineSegment(sketch, "E5412", {"start": v(7.17, -0.05) * mm, "end": v(7.17, -0.06) * mm});
            skLineSegment(sketch, "E5413", {"start": v(7.17, -0.06) * mm, "end": v(7.17, -0.06) * mm});
            skLineSegment(sketch, "E5414", {"start": v(7.17, -0.06) * mm, "end": v(7.16, -0.07) * mm});
            skLineSegment(sketch, "E5415", {"start": v(7.16, -0.07) * mm, "end": v(7.16, -0.07) * mm});
            skLineSegment(sketch, "E5416", {"start": v(7.16, -0.07) * mm, "end": v(7.16, -0.08) * mm});
            skLineSegment(sketch, "E5417", {"start": v(7.16, -0.08) * mm, "end": v(7.16, -0.08) * mm});
            skLineSegment(sketch, "E5418", {"start": v(7.16, -0.08) * mm, "end": v(7.16, -0.09) * mm});
            skLineSegment(sketch, "E5419", {"start": v(7.16, -0.09) * mm, "end": v(7.15, -0.1) * mm});
            skLineSegment(sketch, "E5420", {"start": v(7.15, -0.1) * mm, "end": v(7.15, -0.1) * mm});
            skLineSegment(sketch, "E5421", {"start": v(7.15, -0.1) * mm, "end": v(7.14, -0.1) * mm});
            skLineSegment(sketch, "E5422", {"start": v(7.14, -0.1) * mm, "end": v(7.14, -0.1) * mm});
            skLineSegment(sketch, "E5423", {"start": v(7.14, -0.1) * mm, "end": v(7.14, -0.11) * mm});
            skLineSegment(sketch, "E5424", {"start": v(7.14, -0.11) * mm, "end": v(7.13, -0.12) * mm});
            skLineSegment(sketch, "E5425", {"start": v(7.13, -0.12) * mm, "end": v(7.13, -0.12) * mm});
            skLineSegment(sketch, "E5426", {"start": v(7.13, -0.12) * mm, "end": v(7.12, -0.13) * mm});
            skLineSegment(sketch, "E5427", {"start": v(7.12, -0.13) * mm, "end": v(7.12, -0.13) * mm});
            skLineSegment(sketch, "E5428", {"start": v(7.12, -0.13) * mm, "end": v(7.11, -0.14) * mm});
            skLineSegment(sketch, "E5429", {"start": v(7.11, -0.14) * mm, "end": v(7.1, -0.14) * mm});
            skLineSegment(sketch, "E5430", {"start": v(7.1, -0.14) * mm, "end": v(7.1, -0.14) * mm});
            skLineSegment(sketch, "E5431", {"start": v(7.1, -0.14) * mm, "end": v(7.1, -0.15) * mm});
            skLineSegment(sketch, "E5432", {"start": v(7.1, -0.15) * mm, "end": v(7.1, -0.15) * mm});
            skLineSegment(sketch, "E5433", {"start": v(7.1, -0.15) * mm, "end": v(7.09, -0.15) * mm});
            skLineSegment(sketch, "E5434", {"start": v(7.09, -0.15) * mm, "end": v(7.08, -0.15) * mm});
            skLineSegment(sketch, "E5435", {"start": v(7.08, -0.15) * mm, "end": v(7.08, -0.16) * mm});
            skLineSegment(sketch, "E5436", {"start": v(7.08, -0.16) * mm, "end": v(7.07, -0.16) * mm});
            skLineSegment(sketch, "E5437", {"start": v(7.07, -0.16) * mm, "end": v(7.06, -0.16) * mm});
            skLineSegment(sketch, "E5438", {"start": v(7.06, -0.16) * mm, "end": v(7.06, -0.16) * mm});
            skLineSegment(sketch, "E5439", {"start": v(7.06, -0.16) * mm, "end": v(7.05, -0.17) * mm});
            skLineSegment(sketch, "E5440", {"start": v(7.05, -0.17) * mm, "end": v(7.05, -0.17) * mm});
            skLineSegment(sketch, "E5441", {"start": v(7.05, -0.17) * mm, "end": v(7.04, -0.17) * mm});
            skLineSegment(sketch, "E5442", {"start": v(7.04, -0.17) * mm, "end": v(7.03, -0.17) * mm});
            skLineSegment(sketch, "E5443", {"start": v(7.03, -0.17) * mm, "end": v(7.03, -0.17) * mm});
            skLineSegment(sketch, "E5444", {"start": v(7.03, -0.17) * mm, "end": v(7.02, -0.17) * mm});
            skLineSegment(sketch, "E5445", {"start": v(7.02, -0.17) * mm, "end": v(7.01, -0.17) * mm});
            skLineSegment(sketch, "E5446", {"start": v(7.01, -0.17) * mm, "end": v(7, -0.18) * mm});
            skLineSegment(sketch, "E5447", {"start": v(7, -0.18) * mm, "end": v(7, -0.18) * mm});
            skLineSegment(sketch, "E5448", {"start": v(7, -0.18) * mm, "end": v(6.99, -0.18) * mm});
            skLineSegment(sketch, "E5449", {"start": v(6.99, -0.18) * mm, "end": v(6.98, -0.18) * mm});
            skLineSegment(sketch, "E5450", {"start": v(6.98, -0.18) * mm, "end": v(6.97, -0.18) * mm});
            skLineSegment(sketch, "E5451", {"start": v(6.97, -0.18) * mm, "end": v(6.96, -0.18) * mm});
            skLineSegment(sketch, "E5452", {"start": v(6.96, -0.18) * mm, "end": v(6.96, -0.18) * mm});
            skLineSegment(sketch, "E5453", {"start": v(6.96, -0.18) * mm, "end": v(6.95, -0.18) * mm});
            skLineSegment(sketch, "E5454", {"start": v(6.95, -0.18) * mm, "end": v(6.95, -0.18) * mm});
            skLineSegment(sketch, "E5455", {"start": v(6.95, -0.18) * mm, "end": v(6.94, -0.18) * mm});
            skLineSegment(sketch, "E5456", {"start": v(6.94, -0.18) * mm, "end": v(6.92, -0.18) * mm});
            skLineSegment(sketch, "E5457", {"start": v(6.92, -0.18) * mm, "end": v(6.9, -0.18) * mm});
            skLineSegment(sketch, "E5458", {"start": v(6.9, -0.18) * mm, "end": v(6.88, -0.18) * mm});
            skLineSegment(sketch, "E5459", {"start": v(6.88, -0.18) * mm, "end": v(6.86, -0.18) * mm});
            skLineSegment(sketch, "E5460", {"start": v(6.86, -0.18) * mm, "end": v(6.83, -0.18) * mm});
            skLineSegment(sketch, "E5461", {"start": v(6.83, -0.18) * mm, "end": v(6.8, -0.18) * mm});
            skLineSegment(sketch, "E5462", {"start": v(6.8, -0.18) * mm, "end": v(6.77, -0.18) * mm});
            skLineSegment(sketch, "E5463", {"start": v(6.77, -0.18) * mm, "end": v(6.73, -0.18) * mm});
            skLineSegment(sketch, "E5464", {"start": v(6.73, -0.18) * mm, "end": v(6.69, -0.18) * mm});
            skLineSegment(sketch, "E5465", {"start": v(6.69, -0.18) * mm, "end": v(6.65, -0.18) * mm});
            skLineSegment(sketch, "E5466", {"start": v(6.65, -0.18) * mm, "end": v(6.6, -0.18) * mm});
            skLineSegment(sketch, "E5467", {"start": v(6.6, -0.18) * mm, "end": v(6.56, -0.18) * mm});
            skLineSegment(sketch, "E5468", {"start": v(6.56, -0.18) * mm, "end": v(6.51, -0.18) * mm});
            skLineSegment(sketch, "E5469", {"start": v(6.51, -0.18) * mm, "end": v(6.46, -0.18) * mm});
            skLineSegment(sketch, "E5470", {"start": v(6.46, -0.18) * mm, "end": v(6.41, -0.18) * mm});
            skLineSegment(sketch, "E5471", {"start": v(6.41, -0.18) * mm, "end": v(6.36, -0.18) * mm});
            skLineSegment(sketch, "E5472", {"start": v(6.36, -0.18) * mm, "end": v(6.3, -0.18) * mm});
            skLineSegment(sketch, "E5473", {"start": v(6.3, -0.18) * mm, "end": v(6.26, -0.18) * mm});
            skLineSegment(sketch, "E5474", {"start": v(6.26, -0.18) * mm, "end": v(6.2, -0.18) * mm});
            skLineSegment(sketch, "E5475", {"start": v(6.2, -0.18) * mm, "end": v(6.15, -0.18) * mm});
            skLineSegment(sketch, "E5476", {"start": v(6.15, -0.18) * mm, "end": v(6.1, -0.18) * mm});
            skLineSegment(sketch, "E5477", {"start": v(6.1, -0.18) * mm, "end": v(6.04, -0.18) * mm});
            skLineSegment(sketch, "E5478", {"start": v(6.04, -0.18) * mm, "end": v(5.98, -0.18) * mm});
            skLineSegment(sketch, "E5479", {"start": v(5.98, -0.18) * mm, "end": v(5.93, -0.18) * mm});
            skLineSegment(sketch, "E5480", {"start": v(5.93, -0.18) * mm, "end": v(5.87, -0.18) * mm});
            skLineSegment(sketch, "E5481", {"start": v(5.87, -0.18) * mm, "end": v(5.82, -0.18) * mm});
            skLineSegment(sketch, "E5482", {"start": v(5.82, -0.18) * mm, "end": v(5.77, -0.18) * mm});
            skLineSegment(sketch, "E5483", {"start": v(5.77, -0.18) * mm, "end": v(5.71, -0.18) * mm});
            skLineSegment(sketch, "E5484", {"start": v(5.71, -0.18) * mm, "end": v(5.66, -0.18) * mm});
            skLineSegment(sketch, "E5485", {"start": v(5.66, -0.18) * mm, "end": v(5.61, -0.18) * mm});
            skLineSegment(sketch, "E5486", {"start": v(5.61, -0.18) * mm, "end": v(5.56, -0.18) * mm});
            skLineSegment(sketch, "E5487", {"start": v(5.56, -0.18) * mm, "end": v(5.52, -0.18) * mm});
            skLineSegment(sketch, "E5488", {"start": v(5.52, -0.18) * mm, "end": v(5.47, -0.18) * mm});
            skLineSegment(sketch, "E5489", {"start": v(5.47, -0.18) * mm, "end": v(5.43, -0.18) * mm});
            skLineSegment(sketch, "E5490", {"start": v(5.43, -0.18) * mm, "end": v(5.39, -0.18) * mm});
            skLineSegment(sketch, "E5491", {"start": v(5.39, -0.18) * mm, "end": v(5.35, -0.18) * mm});
            skLineSegment(sketch, "E5492", {"start": v(5.35, -0.18) * mm, "end": v(5.3, -0.18) * mm});
            skLineSegment(sketch, "E5493", {"start": v(5.3, -0.18) * mm, "end": v(5.28, -0.18) * mm});
            skLineSegment(sketch, "E5494", {"start": v(5.28, -0.18) * mm, "end": v(5.24, -0.18) * mm});
            skLineSegment(sketch, "E5495", {"start": v(5.24, -0.18) * mm, "end": v(5.22, -0.18) * mm});
            skLineSegment(sketch, "E5496", {"start": v(5.22, -0.18) * mm, "end": v(5.2, -0.18) * mm});
            skLineSegment(sketch, "E5497", {"start": v(5.2, -0.18) * mm, "end": v(5.17, -0.18) * mm});
            skLineSegment(sketch, "E5498", {"start": v(5.17, -0.18) * mm, "end": v(5.15, -0.18) * mm});
            skLineSegment(sketch, "E5499", {"start": v(5.15, -0.18) * mm, "end": v(5.14, -0.18) * mm});
            skLineSegment(sketch, "E5500", {"start": v(5.14, -0.18) * mm, "end": v(5.13, -0.18) * mm});
            skLineSegment(sketch, "E5501", {"start": v(5.13, -0.18) * mm, "end": v(5.12, -0.18) * mm});
            skLineSegment(sketch, "E5502", {"start": v(5.12, -0.18) * mm, "end": v(5.12, -0.18) * mm});
            skLineSegment(sketch, "E5503", {"start": v(5.12, -0.18) * mm, "end": v(5.1, -0.18) * mm});
            skLineSegment(sketch, "E5504", {"start": v(5.1, -0.18) * mm, "end": v(5.1, -0.18) * mm});
            skLineSegment(sketch, "E5505", {"start": v(5.1, -0.18) * mm, "end": v(5.08, -0.18) * mm});
            skLineSegment(sketch, "E5506", {"start": v(5.08, -0.18) * mm, "end": v(5.07, -0.18) * mm});
            skLineSegment(sketch, "E5507", {"start": v(5.07, -0.18) * mm, "end": v(5.06, -0.18) * mm});
            skLineSegment(sketch, "E5508", {"start": v(5.06, -0.18) * mm, "end": v(5.05, -0.19) * mm});
            skLineSegment(sketch, "E5509", {"start": v(5.05, -0.19) * mm, "end": v(5.03, -0.19) * mm});
            skLineSegment(sketch, "E5510", {"start": v(5.03, -0.19) * mm, "end": v(5.02, -0.2) * mm});
            skLineSegment(sketch, "E5511", {"start": v(5.02, -0.2) * mm, "end": v(5.01, -0.2) * mm});
            skLineSegment(sketch, "E5512", {"start": v(5.01, -0.2) * mm, "end": v(5, -0.2) * mm});
            skLineSegment(sketch, "E5513", {"start": v(5, -0.2) * mm, "end": v(4.99, -0.2) * mm});
            skLineSegment(sketch, "E5514", {"start": v(4.99, -0.2) * mm, "end": v(4.98, -0.2) * mm});
            skLineSegment(sketch, "E5515", {"start": v(4.98, -0.2) * mm, "end": v(4.97, -0.2) * mm});
            skLineSegment(sketch, "E5516", {"start": v(4.97, -0.2) * mm, "end": v(4.96, -0.21) * mm});
            skLineSegment(sketch, "E5517", {"start": v(4.96, -0.21) * mm, "end": v(4.95, -0.22) * mm});
            skLineSegment(sketch, "E5518", {"start": v(4.95, -0.22) * mm, "end": v(4.94, -0.22) * mm});
            skLineSegment(sketch, "E5519", {"start": v(4.94, -0.22) * mm, "end": v(4.93, -0.23) * mm});
            skLineSegment(sketch, "E5520", {"start": v(4.93, -0.23) * mm, "end": v(4.92, -0.24) * mm});
            skLineSegment(sketch, "E5521", {"start": v(4.92, -0.24) * mm, "end": v(4.91, -0.24) * mm});
            skLineSegment(sketch, "E5522", {"start": v(4.91, -0.24) * mm, "end": v(4.9, -0.25) * mm});
            skLineSegment(sketch, "E5523", {"start": v(4.9, -0.25) * mm, "end": v(4.9, -0.26) * mm});
            skLineSegment(sketch, "E5524", {"start": v(4.9, -0.26) * mm, "end": v(4.89, -0.26) * mm});
            skLineSegment(sketch, "E5525", {"start": v(4.89, -0.26) * mm, "end": v(4.88, -0.27) * mm});
            skLineSegment(sketch, "E5526", {"start": v(4.88, -0.27) * mm, "end": v(4.87, -0.28) * mm});
            skLineSegment(sketch, "E5527", {"start": v(4.87, -0.28) * mm, "end": v(4.86, -0.29) * mm});
            skLineSegment(sketch, "E5528", {"start": v(4.86, -0.29) * mm, "end": v(4.86, -0.3) * mm});
            skLineSegment(sketch, "E5529", {"start": v(4.86, -0.3) * mm, "end": v(4.85, -0.3) * mm});
            skLineSegment(sketch, "E5530", {"start": v(4.85, -0.3) * mm, "end": v(4.84, -0.31) * mm});
            skLineSegment(sketch, "E5531", {"start": v(4.84, -0.31) * mm, "end": v(4.83, -0.32) * mm});
            skLineSegment(sketch, "E5532", {"start": v(4.83, -0.32) * mm, "end": v(4.83, -0.33) * mm});
            skLineSegment(sketch, "E5533", {"start": v(4.83, -0.33) * mm, "end": v(4.82, -0.34) * mm});
            skLineSegment(sketch, "E5534", {"start": v(4.82, -0.34) * mm, "end": v(4.82, -0.35) * mm});
            skLineSegment(sketch, "E5535", {"start": v(4.82, -0.35) * mm, "end": v(4.81, -0.36) * mm});
            skLineSegment(sketch, "E5536", {"start": v(4.81, -0.36) * mm, "end": v(4.8, -0.37) * mm});
            skLineSegment(sketch, "E5537", {"start": v(4.8, -0.37) * mm, "end": v(4.8, -0.38) * mm});
            skLineSegment(sketch, "E5538", {"start": v(4.8, -0.38) * mm, "end": v(4.8, -0.4) * mm});
            skLineSegment(sketch, "E5539", {"start": v(4.8, -0.4) * mm, "end": v(4.8, -0.4) * mm});
            skLineSegment(sketch, "E5540", {"start": v(4.8, -0.4) * mm, "end": v(4.79, -0.41) * mm});
            skLineSegment(sketch, "E5541", {"start": v(4.79, -0.41) * mm, "end": v(4.79, -0.42) * mm});
            skLineSegment(sketch, "E5542", {"start": v(4.79, -0.42) * mm, "end": v(4.78, -0.43) * mm});
            skLineSegment(sketch, "E5543", {"start": v(4.78, -0.43) * mm, "end": v(4.78, -0.45) * mm});
            skLineSegment(sketch, "E5544", {"start": v(4.78, -0.45) * mm, "end": v(4.78, -0.46) * mm});
            skLineSegment(sketch, "E5545", {"start": v(4.78, -0.46) * mm, "end": v(4.77, -0.47) * mm});
            skLineSegment(sketch, "E5546", {"start": v(4.77, -0.47) * mm, "end": v(4.77, -0.48) * mm});
            skLineSegment(sketch, "E5547", {"start": v(4.77, -0.48) * mm, "end": v(4.77, -0.5) * mm});
            skLineSegment(sketch, "E5548", {"start": v(4.77, -0.5) * mm, "end": v(4.77, -0.5) * mm});
            skLineSegment(sketch, "E5549", {"start": v(4.77, -0.5) * mm, "end": v(4.77, -0.52) * mm});
            skLineSegment(sketch, "E5550", {"start": v(4.77, -0.52) * mm, "end": v(4.77, -0.53) * mm});
            skLineSegment(sketch, "E5551", {"start": v(4.77, -0.53) * mm, "end": v(4.77, -0.54) * mm});
            skLineSegment(sketch, "E5552", {"start": v(4.77, -0.54) * mm, "end": v(4.77, -0.56) * mm});
            skLineSegment(sketch, "E5553", {"start": v(4.77, -0.56) * mm, "end": v(4.77, -0.56) * mm});
            skLineSegment(sketch, "E5554", {"start": v(4.77, -0.56) * mm, "end": v(4.77, -0.57) * mm});
            skLineSegment(sketch, "E5555", {"start": v(4.77, -0.57) * mm, "end": v(4.77, -0.58) * mm});
            skLineSegment(sketch, "E5556", {"start": v(4.77, -0.58) * mm, "end": v(4.77, -0.6) * mm});
            skLineSegment(sketch, "E5557", {"start": v(4.77, -0.6) * mm, "end": v(4.77, -0.61) * mm});
            skLineSegment(sketch, "E5558", {"start": v(4.77, -0.61) * mm, "end": v(4.77, -0.64) * mm});
            skLineSegment(sketch, "E5559", {"start": v(4.77, -0.64) * mm, "end": v(4.77, -0.66) * mm});
            skLineSegment(sketch, "E5560", {"start": v(4.77, -0.66) * mm, "end": v(4.77, -0.68) * mm});
            skLineSegment(sketch, "E5561", {"start": v(4.77, -0.68) * mm, "end": v(4.77, -0.71) * mm});
            skLineSegment(sketch, "E5562", {"start": v(4.77, -0.71) * mm, "end": v(4.77, -0.74) * mm});
            skLineSegment(sketch, "E5563", {"start": v(4.77, -0.74) * mm, "end": v(4.77, -0.77) * mm});
            skLineSegment(sketch, "E5564", {"start": v(4.77, -0.77) * mm, "end": v(4.77, -0.8) * mm});
            skLineSegment(sketch, "E5565", {"start": v(4.77, -0.8) * mm, "end": v(4.77, -0.84) * mm});
            skLineSegment(sketch, "E5566", {"start": v(4.77, -0.84) * mm, "end": v(4.77, -0.88) * mm});
            skLineSegment(sketch, "E5567", {"start": v(4.77, -0.88) * mm, "end": v(4.77, -0.92) * mm});
            skLineSegment(sketch, "E5568", {"start": v(4.77, -0.92) * mm, "end": v(4.77, -0.96) * mm});
            skLineSegment(sketch, "E5569", {"start": v(4.77, -0.96) * mm, "end": v(4.77, -1) * mm});
            skLineSegment(sketch, "E5570", {"start": v(4.77, -1) * mm, "end": v(4.77, -1.04) * mm});
            skLineSegment(sketch, "E5571", {"start": v(4.77, -1.04) * mm, "end": v(4.77, -1.09) * mm});
            skLineSegment(sketch, "E5572", {"start": v(4.77, -1.09) * mm, "end": v(4.77, -1.13) * mm});
            skLineSegment(sketch, "E5573", {"start": v(4.77, -1.13) * mm, "end": v(4.77, -1.17) * mm});
            skLineSegment(sketch, "E5574", {"start": v(4.77, -1.17) * mm, "end": v(4.77, -1.22) * mm});
            skLineSegment(sketch, "E5575", {"start": v(4.77, -1.22) * mm, "end": v(4.77, -1.26) * mm});
            skLineSegment(sketch, "E5576", {"start": v(4.77, -1.26) * mm, "end": v(4.77, -1.3) * mm});
            skLineSegment(sketch, "E5577", {"start": v(4.77, -1.3) * mm, "end": v(4.77, -1.35) * mm});
            skLineSegment(sketch, "E5578", {"start": v(4.77, -1.35) * mm, "end": v(4.77, -1.4) * mm});
            skLineSegment(sketch, "E5579", {"start": v(4.77, -1.4) * mm, "end": v(4.77, -1.44) * mm});
            skLineSegment(sketch, "E5580", {"start": v(4.77, -1.44) * mm, "end": v(4.77, -1.49) * mm});
            skLineSegment(sketch, "E5581", {"start": v(4.77, -1.49) * mm, "end": v(4.77, -1.53) * mm});
            skLineSegment(sketch, "E5582", {"start": v(4.77, -1.53) * mm, "end": v(4.77, -1.58) * mm});
            skLineSegment(sketch, "E5583", {"start": v(4.77, -1.58) * mm, "end": v(4.77, -1.62) * mm});
            skLineSegment(sketch, "E5584", {"start": v(4.77, -1.62) * mm, "end": v(4.77, -1.66) * mm});
            skLineSegment(sketch, "E5585", {"start": v(4.77, -1.66) * mm, "end": v(4.77, -1.7) * mm});
            skLineSegment(sketch, "E5586", {"start": v(4.77, -1.7) * mm, "end": v(4.77, -1.74) * mm});
            skLineSegment(sketch, "E5587", {"start": v(4.77, -1.74) * mm, "end": v(4.77, -1.77) * mm});
            skLineSegment(sketch, "E5588", {"start": v(4.77, -1.77) * mm, "end": v(4.77, -1.81) * mm});
            skLineSegment(sketch, "E5589", {"start": v(4.77, -1.81) * mm, "end": v(4.77, -1.84) * mm});
            skLineSegment(sketch, "E5590", {"start": v(4.77, -1.84) * mm, "end": v(4.77, -1.88) * mm});
            skLineSegment(sketch, "E5591", {"start": v(4.77, -1.88) * mm, "end": v(4.77, -1.9) * mm});
            skLineSegment(sketch, "E5592", {"start": v(4.77, -1.9) * mm, "end": v(4.77, -1.93) * mm});
            skLineSegment(sketch, "E5593", {"start": v(4.77, -1.93) * mm, "end": v(4.77, -1.96) * mm});
            skLineSegment(sketch, "E5594", {"start": v(4.77, -1.96) * mm, "end": v(4.77, -1.98) * mm});
            skLineSegment(sketch, "E5595", {"start": v(4.77, -1.98) * mm, "end": v(4.77, -2) * mm});
            skLineSegment(sketch, "E5596", {"start": v(4.77, -2) * mm, "end": v(4.77, -2.02) * mm});
            skLineSegment(sketch, "E5597", {"start": v(4.77, -2.02) * mm, "end": v(4.77, -2.04) * mm});
            skLineSegment(sketch, "E5598", {"start": v(4.77, -2.04) * mm, "end": v(4.77, -2.05) * mm});
            skLineSegment(sketch, "E5599", {"start": v(4.77, -2.05) * mm, "end": v(4.77, -2.06) * mm});
            skLineSegment(sketch, "E5600", {"start": v(4.77, -2.06) * mm, "end": v(4.77, -2.06) * mm});
            skLineSegment(sketch, "E5601", {"start": v(4.77, -2.06) * mm, "end": v(4.77, -2.07) * mm});
            skLineSegment(sketch, "E5602", {"start": v(4.77, -2.07) * mm, "end": v(4.76, -2.07) * mm});
            skLineSegment(sketch, "E5603", {"start": v(4.76, -2.07) * mm, "end": v(4.76, -2.08) * mm});
            skLineSegment(sketch, "E5604", {"start": v(4.76, -2.08) * mm, "end": v(4.76, -2.09) * mm});
            skLineSegment(sketch, "E5605", {"start": v(4.76, -2.09) * mm, "end": v(4.76, -2.1) * mm});
            skLineSegment(sketch, "E5606", {"start": v(4.76, -2.1) * mm, "end": v(4.76, -2.1) * mm});
            skLineSegment(sketch, "E5607", {"start": v(4.76, -2.1) * mm, "end": v(4.76, -2.11) * mm});
            skLineSegment(sketch, "E5608", {"start": v(4.76, -2.11) * mm, "end": v(4.76, -2.12) * mm});
            skLineSegment(sketch, "E5609", {"start": v(4.76, -2.12) * mm, "end": v(4.76, -2.12) * mm});
            skLineSegment(sketch, "E5610", {"start": v(4.76, -2.12) * mm, "end": v(4.75, -2.13) * mm});
            skLineSegment(sketch, "E5611", {"start": v(4.75, -2.13) * mm, "end": v(4.75, -2.13) * mm});
            skLineSegment(sketch, "E5612", {"start": v(4.75, -2.13) * mm, "end": v(4.75, -2.14) * mm});
            skLineSegment(sketch, "E5613", {"start": v(4.75, -2.14) * mm, "end": v(4.75, -2.15) * mm});
            skLineSegment(sketch, "E5614", {"start": v(4.75, -2.15) * mm, "end": v(4.75, -2.15) * mm});
            skLineSegment(sketch, "E5615", {"start": v(4.75, -2.15) * mm, "end": v(4.74, -2.16) * mm});
            skLineSegment(sketch, "E5616", {"start": v(4.74, -2.16) * mm, "end": v(4.74, -2.16) * mm});
            skLineSegment(sketch, "E5617", {"start": v(4.74, -2.16) * mm, "end": v(4.74, -2.17) * mm});
            skLineSegment(sketch, "E5618", {"start": v(4.74, -2.17) * mm, "end": v(4.73, -2.17) * mm});
            skLineSegment(sketch, "E5619", {"start": v(4.73, -2.17) * mm, "end": v(4.73, -2.17) * mm});
            skLineSegment(sketch, "E5620", {"start": v(4.73, -2.17) * mm, "end": v(4.73, -2.18) * mm});
            skLineSegment(sketch, "E5621", {"start": v(4.73, -2.18) * mm, "end": v(4.72, -2.18) * mm});
            skLineSegment(sketch, "E5622", {"start": v(4.72, -2.18) * mm, "end": v(4.72, -2.19) * mm});
            skLineSegment(sketch, "E5623", {"start": v(4.72, -2.19) * mm, "end": v(4.72, -2.2) * mm});
            skLineSegment(sketch, "E5624", {"start": v(4.72, -2.2) * mm, "end": v(4.71, -2.2) * mm});
            skLineSegment(sketch, "E5625", {"start": v(4.71, -2.2) * mm, "end": v(4.71, -2.2) * mm});
            skLineSegment(sketch, "E5626", {"start": v(4.71, -2.2) * mm, "end": v(4.7, -2.2) * mm});
            skLineSegment(sketch, "E5627", {"start": v(4.7, -2.2) * mm, "end": v(4.7, -2.2) * mm});
            skLineSegment(sketch, "E5628", {"start": v(4.7, -2.2) * mm, "end": v(4.7, -2.21) * mm});
            skLineSegment(sketch, "E5629", {"start": v(4.7, -2.21) * mm, "end": v(4.7, -2.22) * mm});
            skLineSegment(sketch, "E5630", {"start": v(4.7, -2.22) * mm, "end": v(4.7, -2.22) * mm});
            skLineSegment(sketch, "E5631", {"start": v(4.7, -2.22) * mm, "end": v(4.69, -2.22) * mm});
            skLineSegment(sketch, "E5632", {"start": v(4.69, -2.22) * mm, "end": v(4.68, -2.23) * mm});
            skLineSegment(sketch, "E5633", {"start": v(4.68, -2.23) * mm, "end": v(4.68, -2.23) * mm});
            skLineSegment(sketch, "E5634", {"start": v(4.68, -2.23) * mm, "end": v(4.67, -2.23) * mm});
            skLineSegment(sketch, "E5635", {"start": v(4.67, -2.23) * mm, "end": v(4.67, -2.23) * mm});
            skLineSegment(sketch, "E5636", {"start": v(4.67, -2.23) * mm, "end": v(4.66, -2.24) * mm});
            skLineSegment(sketch, "E5637", {"start": v(4.66, -2.24) * mm, "end": v(4.66, -2.24) * mm});
            skLineSegment(sketch, "E5638", {"start": v(4.66, -2.24) * mm, "end": v(4.65, -2.24) * mm});
            skLineSegment(sketch, "E5639", {"start": v(4.65, -2.24) * mm, "end": v(4.65, -2.24) * mm});
            skLineSegment(sketch, "E5640", {"start": v(4.65, -2.24) * mm, "end": v(4.64, -2.24) * mm});
            skLineSegment(sketch, "E5641", {"start": v(4.64, -2.24) * mm, "end": v(4.64, -2.25) * mm});
            skLineSegment(sketch, "E5642", {"start": v(4.64, -2.25) * mm, "end": v(4.63, -2.25) * mm});
            skLineSegment(sketch, "E5643", {"start": v(4.63, -2.25) * mm, "end": v(4.63, -2.25) * mm});
            skLineSegment(sketch, "E5644", {"start": v(4.63, -2.25) * mm, "end": v(4.62, -2.25) * mm});
            skLineSegment(sketch, "E5645", {"start": v(4.62, -2.25) * mm, "end": v(4.62, -2.25) * mm});
            skLineSegment(sketch, "E5646", {"start": v(4.62, -2.25) * mm, "end": v(4.61, -2.25) * mm});
            skLineSegment(sketch, "E5647", {"start": v(4.61, -2.25) * mm, "end": v(4.6, -2.25) * mm});
            skLineSegment(sketch, "E5648", {"start": v(4.6, -2.25) * mm, "end": v(4.6, -2.25) * mm});
            skLineSegment(sketch, "E5649", {"start": v(4.6, -2.25) * mm, "end": v(4.59, -2.25) * mm});
            skLineSegment(sketch, "E5650", {"start": v(4.59, -2.25) * mm, "end": v(4.58, -2.25) * mm});
            skLineSegment(sketch, "E5651", {"start": v(4.58, -2.25) * mm, "end": v(4.58, -2.25) * mm});
            skLineSegment(sketch, "E5652", {"start": v(4.58, -2.25) * mm, "end": v(4.57, -2.25) * mm});
            skLineSegment(sketch, "E5653", {"start": v(4.57, -2.25) * mm, "end": v(4.57, -2.24) * mm});
            skLineSegment(sketch, "E5654", {"start": v(4.57, -2.24) * mm, "end": v(4.56, -2.24) * mm});
            skLineSegment(sketch, "E5655", {"start": v(4.56, -2.24) * mm, "end": v(4.56, -2.24) * mm});
            skLineSegment(sketch, "E5656", {"start": v(4.56, -2.24) * mm, "end": v(4.55, -2.24) * mm});
            skLineSegment(sketch, "E5657", {"start": v(4.55, -2.24) * mm, "end": v(4.55, -2.24) * mm});
            skLineSegment(sketch, "E5658", {"start": v(4.55, -2.24) * mm, "end": v(4.55, -2.23) * mm});
            skLineSegment(sketch, "E5659", {"start": v(4.55, -2.23) * mm, "end": v(4.54, -2.23) * mm});
            skLineSegment(sketch, "E5660", {"start": v(4.54, -2.23) * mm, "end": v(4.54, -2.23) * mm});
            skLineSegment(sketch, "E5661", {"start": v(4.54, -2.23) * mm, "end": v(4.53, -2.23) * mm});
            skLineSegment(sketch, "E5662", {"start": v(4.53, -2.23) * mm, "end": v(4.53, -2.22) * mm});
            skLineSegment(sketch, "E5663", {"start": v(4.53, -2.22) * mm, "end": v(4.53, -2.22) * mm});
            skLineSegment(sketch, "E5664", {"start": v(4.53, -2.22) * mm, "end": v(4.52, -2.22) * mm});
            skLineSegment(sketch, "E5665", {"start": v(4.52, -2.22) * mm, "end": v(4.52, -2.21) * mm});
            skLineSegment(sketch, "E5666", {"start": v(4.52, -2.21) * mm, "end": v(4.52, -2.2) * mm});
            skLineSegment(sketch, "E5667", {"start": v(4.52, -2.2) * mm, "end": v(4.51, -2.2) * mm});
            skLineSegment(sketch, "E5668", {"start": v(4.51, -2.2) * mm, "end": v(4.5, -2.2) * mm});
            skLineSegment(sketch, "E5669", {"start": v(4.5, -2.2) * mm, "end": v(4.5, -2.2) * mm});
            skLineSegment(sketch, "E5670", {"start": v(4.5, -2.2) * mm, "end": v(4.5, -2.19) * mm});
            skLineSegment(sketch, "E5671", {"start": v(4.5, -2.19) * mm, "end": v(4.5, -2.18) * mm});
            skLineSegment(sketch, "E5672", {"start": v(4.5, -2.18) * mm, "end": v(4.5, -2.18) * mm});
            skLineSegment(sketch, "E5673", {"start": v(4.5, -2.18) * mm, "end": v(4.5, -2.17) * mm});
            skLineSegment(sketch, "E5674", {"start": v(4.5, -2.17) * mm, "end": v(4.49, -2.17) * mm});
            skLineSegment(sketch, "E5675", {"start": v(4.49, -2.17) * mm, "end": v(4.49, -2.17) * mm});
            skLineSegment(sketch, "E5676", {"start": v(4.49, -2.17) * mm, "end": v(4.48, -2.16) * mm});
            skLineSegment(sketch, "E5677", {"start": v(4.48, -2.16) * mm, "end": v(4.48, -2.16) * mm});
            skLineSegment(sketch, "E5678", {"start": v(4.48, -2.16) * mm, "end": v(4.48, -2.15) * mm});
            skLineSegment(sketch, "E5679", {"start": v(4.48, -2.15) * mm, "end": v(4.48, -2.15) * mm});
            skLineSegment(sketch, "E5680", {"start": v(4.48, -2.15) * mm, "end": v(4.47, -2.14) * mm});
            skLineSegment(sketch, "E5681", {"start": v(4.47, -2.14) * mm, "end": v(4.47, -2.13) * mm});
            skLineSegment(sketch, "E5682", {"start": v(4.47, -2.13) * mm, "end": v(4.47, -2.13) * mm});
            skLineSegment(sketch, "E5683", {"start": v(4.47, -2.13) * mm, "end": v(4.47, -2.12) * mm});
            skLineSegment(sketch, "E5684", {"start": v(4.47, -2.12) * mm, "end": v(4.47, -2.12) * mm});
            skLineSegment(sketch, "E5685", {"start": v(4.47, -2.12) * mm, "end": v(4.47, -2.11) * mm});
            skLineSegment(sketch, "E5686", {"start": v(4.47, -2.11) * mm, "end": v(4.46, -2.1) * mm});
            skLineSegment(sketch, "E5687", {"start": v(4.46, -2.1) * mm, "end": v(4.46, -2.1) * mm});
            skLineSegment(sketch, "E5688", {"start": v(4.46, -2.1) * mm, "end": v(4.46, -2.09) * mm});
            skLineSegment(sketch, "E5689", {"start": v(4.46, -2.09) * mm, "end": v(4.46, -2.08) * mm});
            skLineSegment(sketch, "E5690", {"start": v(4.46, -2.08) * mm, "end": v(4.46, -2.07) * mm});
            skLineSegment(sketch, "E5691", {"start": v(4.46, -2.07) * mm, "end": v(4.46, -2.07) * mm});
            skLineSegment(sketch, "E5692", {"start": v(4.46, -2.07) * mm, "end": v(4.46, -2.06) * mm});
            skLineSegment(sketch, "E5693", {"start": v(4.46, -2.06) * mm, "end": v(4.46, -2.06) * mm});
            skLineSegment(sketch, "E5694", {"start": v(4.46, -2.06) * mm, "end": v(4.46, -2.04) * mm});
            skLineSegment(sketch, "E5695", {"start": v(4.46, -2.04) * mm, "end": v(4.46, -2.02) * mm});
            skLineSegment(sketch, "E5696", {"start": v(4.46, -2.02) * mm, "end": v(4.46, -1.98) * mm});
            skLineSegment(sketch, "E5697", {"start": v(4.46, -1.98) * mm, "end": v(4.46, -1.93) * mm});
            skLineSegment(sketch, "E5698", {"start": v(4.46, -1.93) * mm, "end": v(4.46, -1.88) * mm});
            skLineSegment(sketch, "E5699", {"start": v(4.46, -1.88) * mm, "end": v(4.46, -1.82) * mm});
            skLineSegment(sketch, "E5700", {"start": v(4.46, -1.82) * mm, "end": v(4.46, -1.75) * mm});
            skLineSegment(sketch, "E5701", {"start": v(4.46, -1.75) * mm, "end": v(4.46, -1.67) * mm});
            skLineSegment(sketch, "E5702", {"start": v(4.46, -1.67) * mm, "end": v(4.46, -1.59) * mm});
            skLineSegment(sketch, "E5703", {"start": v(4.46, -1.59) * mm, "end": v(4.46, -1.5) * mm});
            skLineSegment(sketch, "E5704", {"start": v(4.46, -1.5) * mm, "end": v(4.46, -1.4) * mm});
            skLineSegment(sketch, "E5705", {"start": v(4.46, -1.4) * mm, "end": v(4.46, -1.3) * mm});
            skLineSegment(sketch, "E5706", {"start": v(4.46, -1.3) * mm, "end": v(4.46, -1.18) * mm});
            skLineSegment(sketch, "E5707", {"start": v(4.46, -1.18) * mm, "end": v(4.46, -1.07) * mm});
            skLineSegment(sketch, "E5708", {"start": v(4.46, -1.07) * mm, "end": v(4.46, -0.95) * mm});
            skLineSegment(sketch, "E5709", {"start": v(4.46, -0.95) * mm, "end": v(4.46, -0.83) * mm});
            skLineSegment(sketch, "E5710", {"start": v(4.46, -0.83) * mm, "end": v(4.46, -0.7) * mm});
            skLineSegment(sketch, "E5711", {"start": v(4.46, -0.7) * mm, "end": v(4.46, -0.58) * mm});
            skLineSegment(sketch, "E5712", {"start": v(4.46, -0.58) * mm, "end": v(4.46, -0.45) * mm});
            skLineSegment(sketch, "E5713", {"start": v(4.46, -0.45) * mm, "end": v(4.46, -0.31) * mm});
            skLineSegment(sketch, "E5714", {"start": v(4.46, -0.31) * mm, "end": v(4.46, -0.18) * mm});
            skLineSegment(sketch, "E5715", {"start": v(4.46, -0.18) * mm, "end": v(4.46, -0.04) * mm});
            skLineSegment(sketch, "E5716", {"start": v(4.46, -0.04) * mm, "end": v(4.46, 0.1) * mm});
            skLineSegment(sketch, "E5717", {"start": v(4.46, 0.1) * mm, "end": v(4.46, 0.23) * mm});
            skLineSegment(sketch, "E5718", {"start": v(4.46, 0.23) * mm, "end": v(4.46, 0.37) * mm});
            skLineSegment(sketch, "E5719", {"start": v(4.46, 0.37) * mm, "end": v(4.46, 0.5) * mm});
            skLineSegment(sketch, "E5720", {"start": v(4.46, 0.5) * mm, "end": v(4.46, 0.65) * mm});
            skLineSegment(sketch, "E5721", {"start": v(4.46, 0.65) * mm, "end": v(4.46, 0.78) * mm});
            skLineSegment(sketch, "E5722", {"start": v(4.46, 0.78) * mm, "end": v(4.46, 0.91) * mm});
            skLineSegment(sketch, "E5723", {"start": v(4.46, 0.91) * mm, "end": v(4.46, 1.05) * mm});
            skLineSegment(sketch, "E5724", {"start": v(4.46, 1.05) * mm, "end": v(4.46, 1.17) * mm});
            skLineSegment(sketch, "E5725", {"start": v(4.46, 1.17) * mm, "end": v(4.46, 1.3) * mm});
            skLineSegment(sketch, "E5726", {"start": v(4.46, 1.3) * mm, "end": v(4.46, 1.42) * mm});
            skLineSegment(sketch, "E5727", {"start": v(4.46, 1.42) * mm, "end": v(4.46, 1.54) * mm});
            skLineSegment(sketch, "E5728", {"start": v(4.46, 1.54) * mm, "end": v(4.46, 1.65) * mm});
            skLineSegment(sketch, "E5729", {"start": v(4.46, 1.65) * mm, "end": v(4.46, 1.76) * mm});
            skLineSegment(sketch, "E5730", {"start": v(4.46, 1.76) * mm, "end": v(4.46, 1.86) * mm});
            skLineSegment(sketch, "E5731", {"start": v(4.46, 1.86) * mm, "end": v(4.46, 1.96) * mm});
            skLineSegment(sketch, "E5732", {"start": v(4.46, 1.96) * mm, "end": v(4.46, 2.05) * mm});
            skLineSegment(sketch, "E5733", {"start": v(4.46, 2.05) * mm, "end": v(4.46, 2.14) * mm});
            skLineSegment(sketch, "E5734", {"start": v(4.46, 2.14) * mm, "end": v(4.46, 2.22) * mm});
            skLineSegment(sketch, "E5735", {"start": v(4.46, 2.22) * mm, "end": v(4.46, 2.29) * mm});
            skLineSegment(sketch, "E5736", {"start": v(4.46, 2.29) * mm, "end": v(4.46, 2.35) * mm});
            skLineSegment(sketch, "E5737", {"start": v(4.46, 2.35) * mm, "end": v(4.46, 2.4) * mm});
            skLineSegment(sketch, "E5738", {"start": v(4.46, 2.4) * mm, "end": v(4.46, 2.45) * mm});
            skLineSegment(sketch, "E5739", {"start": v(4.46, 2.45) * mm, "end": v(4.46, 2.48) * mm});
            skLineSegment(sketch, "E5740", {"start": v(4.46, 2.48) * mm, "end": v(4.46, 2.5) * mm});
            skLineSegment(sketch, "E5741", {"start": v(4.46, 2.5) * mm, "end": v(4.46, 2.53) * mm});
            skLineSegment(sketch, "E5742", {"start": v(4.46, 2.53) * mm, "end": v(4.46, 2.53) * mm});
            skLineSegment(sketch, "E5743", {"start": v(4.46, 2.53) * mm, "end": v(4.46, 2.56) * mm});
            skLineSegment(sketch, "E5744", {"start": v(4.46, 2.56) * mm, "end": v(4.46, 2.58) * mm});
            skLineSegment(sketch, "E5745", {"start": v(4.46, 2.58) * mm, "end": v(4.46, 2.6) * mm});
            skLineSegment(sketch, "E5746", {"start": v(4.46, 2.6) * mm, "end": v(4.45, 2.62) * mm});
            skLineSegment(sketch, "E5747", {"start": v(4.45, 2.62) * mm, "end": v(4.45, 2.65) * mm});
            skLineSegment(sketch, "E5748", {"start": v(4.45, 2.65) * mm, "end": v(4.45, 2.67) * mm});
            skLineSegment(sketch, "E5749", {"start": v(4.45, 2.67) * mm, "end": v(4.44, 2.69) * mm});
            skLineSegment(sketch, "E5750", {"start": v(4.44, 2.69) * mm, "end": v(4.44, 2.7) * mm});
            skLineSegment(sketch, "E5751", {"start": v(4.44, 2.7) * mm, "end": v(4.43, 2.73) * mm});
            skLineSegment(sketch, "E5752", {"start": v(4.43, 2.73) * mm, "end": v(4.42, 2.75) * mm});
            skLineSegment(sketch, "E5753", {"start": v(4.42, 2.75) * mm, "end": v(4.42, 2.77) * mm});
            skLineSegment(sketch, "E5754", {"start": v(4.42, 2.77) * mm, "end": v(4.4, 2.79) * mm});
            skLineSegment(sketch, "E5755", {"start": v(4.4, 2.79) * mm, "end": v(4.4, 2.8) * mm});
            skLineSegment(sketch, "E5756", {"start": v(4.4, 2.8) * mm, "end": v(4.4, 2.82) * mm});
            skLineSegment(sketch, "E5757", {"start": v(4.4, 2.82) * mm, "end": v(4.38, 2.84) * mm});
            skLineSegment(sketch, "E5758", {"start": v(4.38, 2.84) * mm, "end": v(4.37, 2.86) * mm});
            skLineSegment(sketch, "E5759", {"start": v(4.37, 2.86) * mm, "end": v(4.36, 2.87) * mm});
            skLineSegment(sketch, "E5760", {"start": v(4.36, 2.87) * mm, "end": v(4.35, 2.89) * mm});
            skLineSegment(sketch, "E5761", {"start": v(4.35, 2.89) * mm, "end": v(4.34, 2.9) * mm});
            skLineSegment(sketch, "E5762", {"start": v(4.34, 2.9) * mm, "end": v(4.33, 2.92) * mm});
            skLineSegment(sketch, "E5763", {"start": v(4.33, 2.92) * mm, "end": v(4.32, 2.93) * mm});
            skLineSegment(sketch, "E5764", {"start": v(4.32, 2.93) * mm, "end": v(4.3, 2.95) * mm});
            skLineSegment(sketch, "E5765", {"start": v(4.3, 2.95) * mm, "end": v(4.3, 2.96) * mm});
            skLineSegment(sketch, "E5766", {"start": v(4.3, 2.96) * mm, "end": v(4.28, 2.98) * mm});
            skLineSegment(sketch, "E5767", {"start": v(4.28, 2.98) * mm, "end": v(4.26, 2.99) * mm});
            skLineSegment(sketch, "E5768", {"start": v(4.26, 2.99) * mm, "end": v(4.25, 3) * mm});
            skLineSegment(sketch, "E5769", {"start": v(4.25, 3) * mm, "end": v(4.24, 3.01) * mm});
            skLineSegment(sketch, "E5770", {"start": v(4.24, 3.01) * mm, "end": v(4.22, 3.02) * mm});
            skLineSegment(sketch, "E5771", {"start": v(4.22, 3.02) * mm, "end": v(4.2, 3.03) * mm});
            skLineSegment(sketch, "E5772", {"start": v(4.2, 3.03) * mm, "end": v(4.19, 3.04) * mm});
            skLineSegment(sketch, "E5773", {"start": v(4.19, 3.04) * mm, "end": v(4.17, 3.05) * mm});
            skLineSegment(sketch, "E5774", {"start": v(4.17, 3.05) * mm, "end": v(4.16, 3.06) * mm});
            skLineSegment(sketch, "E5775", {"start": v(4.16, 3.06) * mm, "end": v(4.14, 3.07) * mm});
            skLineSegment(sketch, "E5776", {"start": v(4.14, 3.07) * mm, "end": v(4.12, 3.08) * mm});
            skLineSegment(sketch, "E5777", {"start": v(4.12, 3.08) * mm, "end": v(4.1, 3.09) * mm});
            skLineSegment(sketch, "E5778", {"start": v(4.1, 3.09) * mm, "end": v(4.09, 3.1) * mm});
            skLineSegment(sketch, "E5779", {"start": v(4.09, 3.1) * mm, "end": v(4.07, 3.1) * mm});
            skLineSegment(sketch, "E5780", {"start": v(4.07, 3.1) * mm, "end": v(4.05, 3.1) * mm});
            skLineSegment(sketch, "E5781", {"start": v(4.05, 3.1) * mm, "end": v(4.03, 3.11) * mm});
            skLineSegment(sketch, "E5782", {"start": v(4.03, 3.11) * mm, "end": v(4.02, 3.12) * mm});
            skLineSegment(sketch, "E5783", {"start": v(4.02, 3.12) * mm, "end": v(4, 3.12) * mm});
            skLineSegment(sketch, "E5784", {"start": v(4, 3.12) * mm, "end": v(3.98, 3.13) * mm});
            skLineSegment(sketch, "E5785", {"start": v(3.98, 3.13) * mm, "end": v(3.96, 3.13) * mm});
            skLineSegment(sketch, "E5786", {"start": v(3.96, 3.13) * mm, "end": v(3.94, 3.13) * mm});
            skLineSegment(sketch, "E5787", {"start": v(3.94, 3.13) * mm, "end": v(3.92, 3.14) * mm});
            skLineSegment(sketch, "E5788", {"start": v(3.92, 3.14) * mm, "end": v(3.9, 3.14) * mm});
            skLineSegment(sketch, "E5789", {"start": v(3.9, 3.14) * mm, "end": v(3.88, 3.14) * mm});
            skLineSegment(sketch, "E5790", {"start": v(3.88, 3.14) * mm, "end": v(3.86, 3.14) * mm});
            skLineSegment(sketch, "E5791", {"start": v(3.86, 3.14) * mm, "end": v(3.84, 3.14) * mm});
            skLineSegment(sketch, "E5792", {"start": v(3.84, 3.14) * mm, "end": v(3.82, 3.14) * mm});
            skLineSegment(sketch, "E5793", {"start": v(3.82, 3.14) * mm, "end": v(3.8, 3.14) * mm});
            skLineSegment(sketch, "E5794", {"start": v(3.8, 3.14) * mm, "end": v(3.79, 3.14) * mm});
            skLineSegment(sketch, "E5795", {"start": v(3.79, 3.14) * mm, "end": v(3.77, 3.14) * mm});
            skLineSegment(sketch, "E5796", {"start": v(3.77, 3.14) * mm, "end": v(3.75, 3.14) * mm});
            skLineSegment(sketch, "E5797", {"start": v(3.75, 3.14) * mm, "end": v(3.73, 3.14) * mm});
            skLineSegment(sketch, "E5798", {"start": v(3.73, 3.14) * mm, "end": v(3.71, 3.13) * mm});
            skLineSegment(sketch, "E5799", {"start": v(3.71, 3.13) * mm, "end": v(3.7, 3.13) * mm});
            skLineSegment(sketch, "E5800", {"start": v(3.7, 3.13) * mm, "end": v(3.68, 3.13) * mm});
            skLineSegment(sketch, "E5801", {"start": v(3.68, 3.13) * mm, "end": v(3.66, 3.12) * mm});
            skLineSegment(sketch, "E5802", {"start": v(3.66, 3.12) * mm, "end": v(3.64, 3.12) * mm});
            skLineSegment(sketch, "E5803", {"start": v(3.64, 3.12) * mm, "end": v(3.62, 3.11) * mm});
            skLineSegment(sketch, "E5804", {"start": v(3.62, 3.11) * mm, "end": v(3.6, 3.1) * mm});
            skLineSegment(sketch, "E5805", {"start": v(3.6, 3.1) * mm, "end": v(3.59, 3.1) * mm});
            skLineSegment(sketch, "E5806", {"start": v(3.59, 3.1) * mm, "end": v(3.57, 3.1) * mm});
            skLineSegment(sketch, "E5807", {"start": v(3.57, 3.1) * mm, "end": v(3.56, 3.09) * mm});
            skLineSegment(sketch, "E5808", {"start": v(3.56, 3.09) * mm, "end": v(3.54, 3.08) * mm});
            skLineSegment(sketch, "E5809", {"start": v(3.54, 3.08) * mm, "end": v(3.52, 3.07) * mm});
            skLineSegment(sketch, "E5810", {"start": v(3.52, 3.07) * mm, "end": v(3.5, 3.06) * mm});
            skLineSegment(sketch, "E5811", {"start": v(3.5, 3.06) * mm, "end": v(3.5, 3.05) * mm});
            skLineSegment(sketch, "E5812", {"start": v(3.5, 3.05) * mm, "end": v(3.47, 3.04) * mm});
            skLineSegment(sketch, "E5813", {"start": v(3.47, 3.04) * mm, "end": v(3.46, 3.03) * mm});
            skLineSegment(sketch, "E5814", {"start": v(3.46, 3.03) * mm, "end": v(3.44, 3.02) * mm});
            skLineSegment(sketch, "E5815", {"start": v(3.44, 3.02) * mm, "end": v(3.43, 3) * mm});
            skLineSegment(sketch, "E5816", {"start": v(3.43, 3) * mm, "end": v(3.42, 3) * mm});
            skLineSegment(sketch, "E5817", {"start": v(3.42, 3) * mm, "end": v(3.4, 2.98) * mm});
            skLineSegment(sketch, "E5818", {"start": v(3.4, 2.98) * mm, "end": v(3.39, 2.97) * mm});
            skLineSegment(sketch, "E5819", {"start": v(3.39, 2.97) * mm, "end": v(3.37, 2.95) * mm});
            skLineSegment(sketch, "E5820", {"start": v(3.37, 2.95) * mm, "end": v(3.36, 2.94) * mm});
            skLineSegment(sketch, "E5821", {"start": v(3.36, 2.94) * mm, "end": v(3.35, 2.93) * mm});
            skLineSegment(sketch, "E5822", {"start": v(3.35, 2.93) * mm, "end": v(3.34, 2.9) * mm});
            skLineSegment(sketch, "E5823", {"start": v(3.34, 2.9) * mm, "end": v(3.33, 2.9) * mm});
            skLineSegment(sketch, "E5824", {"start": v(3.33, 2.9) * mm, "end": v(3.32, 2.88) * mm});
            skLineSegment(sketch, "E5825", {"start": v(3.32, 2.88) * mm, "end": v(3.3, 2.86) * mm});
            skLineSegment(sketch, "E5826", {"start": v(3.3, 2.86) * mm, "end": v(3.3, 2.84) * mm});
            skLineSegment(sketch, "E5827", {"start": v(3.3, 2.84) * mm, "end": v(3.28, 2.82) * mm});
            skLineSegment(sketch, "E5828", {"start": v(3.28, 2.82) * mm, "end": v(3.28, 2.8) * mm});
            skLineSegment(sketch, "E5829", {"start": v(3.28, 2.8) * mm, "end": v(3.27, 2.79) * mm});
            skLineSegment(sketch, "E5830", {"start": v(3.27, 2.79) * mm, "end": v(3.26, 2.77) * mm});
            skLineSegment(sketch, "E5831", {"start": v(3.26, 2.77) * mm, "end": v(3.25, 2.75) * mm});
            skLineSegment(sketch, "E5832", {"start": v(3.25, 2.75) * mm, "end": v(3.24, 2.72) * mm});
            skLineSegment(sketch, "E5833", {"start": v(3.24, 2.72) * mm, "end": v(3.24, 2.7) * mm});
            skLineSegment(sketch, "E5834", {"start": v(3.24, 2.7) * mm, "end": v(3.23, 2.68) * mm});
            skLineSegment(sketch, "E5835", {"start": v(3.23, 2.68) * mm, "end": v(3.23, 2.66) * mm});
            skLineSegment(sketch, "E5836", {"start": v(3.23, 2.66) * mm, "end": v(3.22, 2.64) * mm});
            skLineSegment(sketch, "E5837", {"start": v(3.22, 2.64) * mm, "end": v(3.22, 2.61) * mm});
            skLineSegment(sketch, "E5838", {"start": v(3.22, 2.61) * mm, "end": v(3.22, 2.59) * mm});
            skLineSegment(sketch, "E5839", {"start": v(3.22, 2.59) * mm, "end": v(3.21, 2.56) * mm});
            skLineSegment(sketch, "E5840", {"start": v(3.21, 2.56) * mm, "end": v(3.21, 2.54) * mm});
            skLineSegment(sketch, "E5841", {"start": v(3.21, 2.54) * mm, "end": v(3.21, 2.51) * mm});
            skLineSegment(sketch, "E5842", {"start": v(3.21, 2.51) * mm, "end": v(3.21, 2.48) * mm});
            skLineSegment(sketch, "E5843", {"start": v(3.21, 2.48) * mm, "end": v(3.21, 2.48) * mm});
            skLineSegment(sketch, "E5844", {"start": v(3.21, 2.48) * mm, "end": v(3.21, 2.46) * mm});
            skLineSegment(sketch, "E5845", {"start": v(3.21, 2.46) * mm, "end": v(3.21, 2.43) * mm});
            skLineSegment(sketch, "E5846", {"start": v(3.21, 2.43) * mm, "end": v(3.21, 2.4) * mm});
            skLineSegment(sketch, "E5847", {"start": v(3.21, 2.4) * mm, "end": v(3.21, 2.35) * mm});
            skLineSegment(sketch, "E5848", {"start": v(3.21, 2.35) * mm, "end": v(3.21, 2.29) * mm});
            skLineSegment(sketch, "E5849", {"start": v(3.21, 2.29) * mm, "end": v(3.21, 2.22) * mm});
            skLineSegment(sketch, "E5850", {"start": v(3.21, 2.22) * mm, "end": v(3.21, 2.14) * mm});
            skLineSegment(sketch, "E5851", {"start": v(3.21, 2.14) * mm, "end": v(3.21, 2.06) * mm});
            skLineSegment(sketch, "E5852", {"start": v(3.21, 2.06) * mm, "end": v(3.21, 1.97) * mm});
            skLineSegment(sketch, "E5853", {"start": v(3.21, 1.97) * mm, "end": v(3.21, 1.87) * mm});
            skLineSegment(sketch, "E5854", {"start": v(3.21, 1.87) * mm, "end": v(3.21, 1.76) * mm});
            skLineSegment(sketch, "E5855", {"start": v(3.21, 1.76) * mm, "end": v(3.21, 1.65) * mm});
            skLineSegment(sketch, "E5856", {"start": v(3.21, 1.65) * mm, "end": v(3.21, 1.53) * mm});
            skLineSegment(sketch, "E5857", {"start": v(3.21, 1.53) * mm, "end": v(3.21, 1.41) * mm});
            skLineSegment(sketch, "E5858", {"start": v(3.21, 1.41) * mm, "end": v(3.21, 1.28) * mm});
            skLineSegment(sketch, "E5859", {"start": v(3.21, 1.28) * mm, "end": v(3.21, 1.15) * mm});
            skLineSegment(sketch, "E5860", {"start": v(3.21, 1.15) * mm, "end": v(3.21, 1.02) * mm});
            skLineSegment(sketch, "E5861", {"start": v(3.21, 1.02) * mm, "end": v(3.21, 0.88) * mm});
            skLineSegment(sketch, "E5862", {"start": v(3.21, 0.88) * mm, "end": v(3.21, 0.73) * mm});
            skLineSegment(sketch, "E5863", {"start": v(3.21, 0.73) * mm, "end": v(3.21, 0.6) * mm});
            skLineSegment(sketch, "E5864", {"start": v(3.21, 0.6) * mm, "end": v(3.21, 0.44) * mm});
            skLineSegment(sketch, "E5865", {"start": v(3.21, 0.44) * mm, "end": v(3.21, 0.3) * mm});
            skLineSegment(sketch, "E5866", {"start": v(3.21, 0.3) * mm, "end": v(3.21, 0.15) * mm});
            skLineSegment(sketch, "E5867", {"start": v(3.21, 0.15) * mm, "end": v(3.21, 0) * mm});
            skLineSegment(sketch, "E5868", {"start": v(3.21, 0) * mm, "end": v(3.21, -0.15) * mm});
            skLineSegment(sketch, "E5869", {"start": v(3.21, -0.15) * mm, "end": v(3.21, -0.3) * mm});
            skLineSegment(sketch, "E5870", {"start": v(3.21, -0.3) * mm, "end": v(3.21, -0.45) * mm});
            skLineSegment(sketch, "E5871", {"start": v(3.21, -0.45) * mm, "end": v(3.21, -0.6) * mm});
            skLineSegment(sketch, "E5872", {"start": v(3.21, -0.6) * mm, "end": v(3.21, -0.74) * mm});
            skLineSegment(sketch, "E5873", {"start": v(3.21, -0.74) * mm, "end": v(3.21, -0.88) * mm});
            skLineSegment(sketch, "E5874", {"start": v(3.21, -0.88) * mm, "end": v(3.21, -1.02) * mm});
            skLineSegment(sketch, "E5875", {"start": v(3.21, -1.02) * mm, "end": v(3.21, -1.15) * mm});
            skLineSegment(sketch, "E5876", {"start": v(3.21, -1.15) * mm, "end": v(3.21, -1.29) * mm});
            skLineSegment(sketch, "E5877", {"start": v(3.21, -1.29) * mm, "end": v(3.21, -1.41) * mm});
            skLineSegment(sketch, "E5878", {"start": v(3.21, -1.41) * mm, "end": v(3.21, -1.54) * mm});
            skLineSegment(sketch, "E5879", {"start": v(3.21, -1.54) * mm, "end": v(3.21, -1.65) * mm});
            skLineSegment(sketch, "E5880", {"start": v(3.21, -1.65) * mm, "end": v(3.21, -1.77) * mm});
            skLineSegment(sketch, "E5881", {"start": v(3.21, -1.77) * mm, "end": v(3.21, -1.87) * mm});
            skLineSegment(sketch, "E5882", {"start": v(3.21, -1.87) * mm, "end": v(3.21, -1.97) * mm});
            skLineSegment(sketch, "E5883", {"start": v(3.21, -1.97) * mm, "end": v(3.21, -2.06) * mm});
            skLineSegment(sketch, "E5884", {"start": v(3.21, -2.06) * mm, "end": v(3.21, -2.15) * mm});
            skLineSegment(sketch, "E5885", {"start": v(3.21, -2.15) * mm, "end": v(3.21, -2.22) * mm});
            skLineSegment(sketch, "E5886", {"start": v(3.21, -2.22) * mm, "end": v(3.21, -2.29) * mm});
            skLineSegment(sketch, "E5887", {"start": v(3.21, -2.29) * mm, "end": v(3.21, -2.35) * mm});
            skLineSegment(sketch, "E5888", {"start": v(3.21, -2.35) * mm, "end": v(3.21, -2.4) * mm});
            skLineSegment(sketch, "E5889", {"start": v(3.21, -2.4) * mm, "end": v(3.21, -2.44) * mm});
            skLineSegment(sketch, "E5890", {"start": v(3.21, -2.44) * mm, "end": v(3.21, -2.46) * mm});
            skLineSegment(sketch, "E5891", {"start": v(3.21, -2.46) * mm, "end": v(3.21, -2.48) * mm});
            skLineSegment(sketch, "E5892", {"start": v(3.21, -2.48) * mm, "end": v(3.21, -2.49) * mm});
            skLineSegment(sketch, "E5893", {"start": v(3.21, -2.49) * mm, "end": v(3.21, -2.52) * mm});
            skLineSegment(sketch, "E5894", {"start": v(3.21, -2.52) * mm, "end": v(3.21, -2.54) * mm});
            skLineSegment(sketch, "E5895", {"start": v(3.21, -2.54) * mm, "end": v(3.21, -2.57) * mm});
            skLineSegment(sketch, "E5896", {"start": v(3.21, -2.57) * mm, "end": v(3.22, -2.6) * mm});
            skLineSegment(sketch, "E5897", {"start": v(3.22, -2.6) * mm, "end": v(3.22, -2.62) * mm});
            skLineSegment(sketch, "E5898", {"start": v(3.22, -2.62) * mm, "end": v(3.22, -2.65) * mm});
            skLineSegment(sketch, "E5899", {"start": v(3.22, -2.65) * mm, "end": v(3.23, -2.67) * mm});
            skLineSegment(sketch, "E5900", {"start": v(3.23, -2.67) * mm, "end": v(3.23, -2.7) * mm});
            skLineSegment(sketch, "E5901", {"start": v(3.23, -2.7) * mm, "end": v(3.24, -2.72) * mm});
            skLineSegment(sketch, "E5902", {"start": v(3.24, -2.72) * mm, "end": v(3.25, -2.75) * mm});
            skLineSegment(sketch, "E5903", {"start": v(3.25, -2.75) * mm, "end": v(3.25, -2.77) * mm});
            skLineSegment(sketch, "E5904", {"start": v(3.25, -2.77) * mm, "end": v(3.26, -2.8) * mm});
            skLineSegment(sketch, "E5905", {"start": v(3.26, -2.8) * mm, "end": v(3.27, -2.81) * mm});
            skLineSegment(sketch, "E5906", {"start": v(3.27, -2.81) * mm, "end": v(3.28, -2.84) * mm});
            skLineSegment(sketch, "E5907", {"start": v(3.28, -2.84) * mm, "end": v(3.29, -2.86) * mm});
            skLineSegment(sketch, "E5908", {"start": v(3.29, -2.86) * mm, "end": v(3.3, -2.88) * mm});
            skLineSegment(sketch, "E5909", {"start": v(3.3, -2.88) * mm, "end": v(3.31, -2.9) * mm});
            skLineSegment(sketch, "E5910", {"start": v(3.31, -2.9) * mm, "end": v(3.32, -2.92) * mm});
            skLineSegment(sketch, "E5911", {"start": v(3.32, -2.92) * mm, "end": v(3.34, -2.94) * mm});
            skLineSegment(sketch, "E5912", {"start": v(3.34, -2.94) * mm, "end": v(3.35, -2.96) * mm});
            skLineSegment(sketch, "E5913", {"start": v(3.35, -2.96) * mm, "end": v(3.36, -2.97) * mm});
            skLineSegment(sketch, "E5914", {"start": v(3.36, -2.97) * mm, "end": v(3.38, -3) * mm});
            skLineSegment(sketch, "E5915", {"start": v(3.38, -3) * mm, "end": v(3.4, -3) * mm});
            skLineSegment(sketch, "E5916", {"start": v(3.4, -3) * mm, "end": v(3.4, -3.02) * mm});
            skLineSegment(sketch, "E5917", {"start": v(3.4, -3.02) * mm, "end": v(3.42, -3.04) * mm});
            skLineSegment(sketch, "E5918", {"start": v(3.42, -3.04) * mm, "end": v(3.44, -3.06) * mm});
            skLineSegment(sketch, "E5919", {"start": v(3.44, -3.06) * mm, "end": v(3.46, -3.07) * mm});
            skLineSegment(sketch, "E5920", {"start": v(3.46, -3.07) * mm, "end": v(3.47, -3.08) * mm});
            skLineSegment(sketch, "E5921", {"start": v(3.47, -3.08) * mm, "end": v(3.5, -3.1) * mm});
            skLineSegment(sketch, "E5922", {"start": v(3.5, -3.1) * mm, "end": v(3.51, -3.11) * mm});
            skLineSegment(sketch, "E5923", {"start": v(3.51, -3.11) * mm, "end": v(3.53, -3.12) * mm});
            skLineSegment(sketch, "E5924", {"start": v(3.53, -3.12) * mm, "end": v(3.55, -3.14) * mm});
            skLineSegment(sketch, "E5925", {"start": v(3.55, -3.14) * mm, "end": v(3.57, -3.15) * mm});
            skLineSegment(sketch, "E5926", {"start": v(3.57, -3.15) * mm, "end": v(3.6, -3.16) * mm});
            skLineSegment(sketch, "E5927", {"start": v(3.6, -3.16) * mm, "end": v(3.61, -3.17) * mm});
            skLineSegment(sketch, "E5928", {"start": v(3.61, -3.17) * mm, "end": v(3.63, -3.18) * mm});
            skLineSegment(sketch, "E5929", {"start": v(3.63, -3.18) * mm, "end": v(3.66, -3.19) * mm});
            skLineSegment(sketch, "E5930", {"start": v(3.66, -3.19) * mm, "end": v(3.68, -3.2) * mm});
            skLineSegment(sketch, "E5931", {"start": v(3.68, -3.2) * mm, "end": v(3.7, -3.2) * mm});
            skLineSegment(sketch, "E5932", {"start": v(3.7, -3.2) * mm, "end": v(3.73, -3.2) * mm});
            skLineSegment(sketch, "E5933", {"start": v(3.73, -3.2) * mm, "end": v(3.75, -3.21) * mm});
            skLineSegment(sketch, "E5934", {"start": v(3.75, -3.21) * mm, "end": v(3.77, -3.22) * mm});
            skLineSegment(sketch, "E5935", {"start": v(3.77, -3.22) * mm, "end": v(3.8, -3.22) * mm});
            skLineSegment(sketch, "E5936", {"start": v(3.8, -3.22) * mm, "end": v(3.83, -3.23) * mm});
            skLineSegment(sketch, "E5937", {"start": v(3.83, -3.23) * mm, "end": v(3.85, -3.23) * mm});
            skLineSegment(sketch, "E5938", {"start": v(3.85, -3.23) * mm, "end": v(3.88, -3.24) * mm});
            skLineSegment(sketch, "E5939", {"start": v(3.88, -3.24) * mm, "end": v(3.9, -3.24) * mm});
            skLineSegment(sketch, "E5940", {"start": v(3.9, -3.24) * mm, "end": v(3.93, -3.24) * mm});
            skLineSegment(sketch, "E5941", {"start": v(3.93, -3.24) * mm, "end": v(3.96, -3.24) * mm});
            skLineSegment(sketch, "E5942", {"start": v(3.96, -3.24) * mm, "end": v(3.99, -3.24) * mm});
            skLineSegment(sketch, "E5943", {"start": v(3.99, -3.24) * mm, "end": v(4, -3.24) * mm});
            skLineSegment(sketch, "E5944", {"start": v(4, -3.24) * mm, "end": v(4, -3.24) * mm});
            skLineSegment(sketch, "E5945", {"start": v(4, -3.24) * mm, "end": v(4.02, -3.24) * mm});
            skLineSegment(sketch, "E5946", {"start": v(4.02, -3.24) * mm, "end": v(4.05, -3.24) * mm});
            skLineSegment(sketch, "E5947", {"start": v(4.05, -3.24) * mm, "end": v(4.08, -3.24) * mm});
            skLineSegment(sketch, "E5948", {"start": v(4.08, -3.24) * mm, "end": v(4.12, -3.24) * mm});
            skLineSegment(sketch, "E5949", {"start": v(4.12, -3.24) * mm, "end": v(4.17, -3.24) * mm});
            skLineSegment(sketch, "E5950", {"start": v(4.17, -3.24) * mm, "end": v(4.22, -3.24) * mm});
            skLineSegment(sketch, "E5951", {"start": v(4.22, -3.24) * mm, "end": v(4.28, -3.24) * mm});
            skLineSegment(sketch, "E5952", {"start": v(4.28, -3.24) * mm, "end": v(4.34, -3.24) * mm});
            skLineSegment(sketch, "E5953", {"start": v(4.34, -3.24) * mm, "end": v(4.4, -3.24) * mm});
            skLineSegment(sketch, "E5954", {"start": v(4.4, -3.24) * mm, "end": v(4.48, -3.24) * mm});
            skLineSegment(sketch, "E5955", {"start": v(4.48, -3.24) * mm, "end": v(4.56, -3.24) * mm});
            skLineSegment(sketch, "E5956", {"start": v(4.56, -3.24) * mm, "end": v(4.64, -3.24) * mm});
            skLineSegment(sketch, "E5957", {"start": v(4.64, -3.24) * mm, "end": v(4.72, -3.24) * mm});
            skLineSegment(sketch, "E5958", {"start": v(4.72, -3.24) * mm, "end": v(4.8, -3.24) * mm});
            skLineSegment(sketch, "E5959", {"start": v(4.8, -3.24) * mm, "end": v(4.9, -3.24) * mm});
            skLineSegment(sketch, "E5960", {"start": v(4.9, -3.24) * mm, "end": v(5, -3.24) * mm});
            skLineSegment(sketch, "E5961", {"start": v(5, -3.24) * mm, "end": v(5.09, -3.24) * mm});
            skLineSegment(sketch, "E5962", {"start": v(5.09, -3.24) * mm, "end": v(5.18, -3.24) * mm});
            skLineSegment(sketch, "E5963", {"start": v(5.18, -3.24) * mm, "end": v(5.28, -3.24) * mm});
            skLineSegment(sketch, "E5964", {"start": v(5.28, -3.24) * mm, "end": v(5.38, -3.24) * mm});
            skLineSegment(sketch, "E5965", {"start": v(5.38, -3.24) * mm, "end": v(5.48, -3.24) * mm});
            skLineSegment(sketch, "E5966", {"start": v(5.48, -3.24) * mm, "end": v(5.58, -3.24) * mm});
            skLineSegment(sketch, "E5967", {"start": v(5.58, -3.24) * mm, "end": v(5.68, -3.24) * mm});
            skLineSegment(sketch, "E5968", {"start": v(5.68, -3.24) * mm, "end": v(5.79, -3.24) * mm});
            skLineSegment(sketch, "E5969", {"start": v(5.79, -3.24) * mm, "end": v(5.89, -3.24) * mm});
            skLineSegment(sketch, "E5970", {"start": v(5.89, -3.24) * mm, "end": v(5.99, -3.24) * mm});
            skLineSegment(sketch, "E5971", {"start": v(5.99, -3.24) * mm, "end": v(6.09, -3.24) * mm});
            skLineSegment(sketch, "E5972", {"start": v(6.09, -3.24) * mm, "end": v(6.19, -3.24) * mm});
            skLineSegment(sketch, "E5973", {"start": v(6.19, -3.24) * mm, "end": v(6.28, -3.24) * mm});
            skLineSegment(sketch, "E5974", {"start": v(6.28, -3.24) * mm, "end": v(6.38, -3.24) * mm});
            skLineSegment(sketch, "E5975", {"start": v(6.38, -3.24) * mm, "end": v(6.47, -3.24) * mm});
            skLineSegment(sketch, "E5976", {"start": v(6.47, -3.24) * mm, "end": v(6.56, -3.24) * mm});
            skLineSegment(sketch, "E5977", {"start": v(6.56, -3.24) * mm, "end": v(6.65, -3.24) * mm});
            skLineSegment(sketch, "E5978", {"start": v(6.65, -3.24) * mm, "end": v(6.73, -3.24) * mm});
            skLineSegment(sketch, "E5979", {"start": v(6.73, -3.24) * mm, "end": v(6.81, -3.24) * mm});
            skLineSegment(sketch, "E5980", {"start": v(6.81, -3.24) * mm, "end": v(6.89, -3.24) * mm});
            skLineSegment(sketch, "E5981", {"start": v(6.89, -3.24) * mm, "end": v(6.96, -3.24) * mm});
            skLineSegment(sketch, "E5982", {"start": v(6.96, -3.24) * mm, "end": v(7.03, -3.24) * mm});
            skLineSegment(sketch, "E5983", {"start": v(7.03, -3.24) * mm, "end": v(7.1, -3.24) * mm});
            skLineSegment(sketch, "E5984", {"start": v(7.1, -3.24) * mm, "end": v(7.15, -3.24) * mm});
            skLineSegment(sketch, "E5985", {"start": v(7.15, -3.24) * mm, "end": v(7.2, -3.24) * mm});
            skLineSegment(sketch, "E5986", {"start": v(7.2, -3.24) * mm, "end": v(7.25, -3.24) * mm});
            skLineSegment(sketch, "E5987", {"start": v(7.25, -3.24) * mm, "end": v(7.29, -3.24) * mm});
            skLineSegment(sketch, "E5988", {"start": v(7.29, -3.24) * mm, "end": v(7.32, -3.24) * mm});
            skLineSegment(sketch, "E5989", {"start": v(7.32, -3.24) * mm, "end": v(7.35, -3.24) * mm});
            skLineSegment(sketch, "E5990", {"start": v(7.35, -3.24) * mm, "end": v(7.36, -3.24) * mm});
            skLineSegment(sketch, "E5991", {"start": v(7.36, -3.24) * mm, "end": v(7.38, -3.24) * mm});
            skLineSegment(sketch, "E5992", {"start": v(7.38, -3.24) * mm, "end": v(7.38, -3.24) * mm});
            skLineSegment(sketch, "E5993", {"start": v(7.38, -3.24) * mm, "end": v(7.4, -3.24) * mm});
            skLineSegment(sketch, "E5994", {"start": v(7.4, -3.24) * mm, "end": v(7.43, -3.24) * mm});
            skLineSegment(sketch, "E5995", {"start": v(7.43, -3.24) * mm, "end": v(7.45, -3.24) * mm});
            skLineSegment(sketch, "E5996", {"start": v(7.45, -3.24) * mm, "end": v(7.47, -3.24) * mm});
            skLineSegment(sketch, "E5997", {"start": v(7.47, -3.24) * mm, "end": v(7.5, -3.23) * mm});
            skLineSegment(sketch, "E5998", {"start": v(7.5, -3.23) * mm, "end": v(7.52, -3.23) * mm});
            skLineSegment(sketch, "E5999", {"start": v(7.52, -3.23) * mm, "end": v(7.54, -3.22) * mm});
            skLineSegment(sketch, "E6000", {"start": v(7.54, -3.22) * mm, "end": v(7.56, -3.22) * mm});
            skLineSegment(sketch, "E6001", {"start": v(7.56, -3.22) * mm, "end": v(7.58, -3.21) * mm});
            skLineSegment(sketch, "E6002", {"start": v(7.58, -3.21) * mm, "end": v(7.6, -3.2) * mm});
            skLineSegment(sketch, "E6003", {"start": v(7.6, -3.2) * mm, "end": v(7.62, -3.2) * mm});
            skLineSegment(sketch, "E6004", {"start": v(7.62, -3.2) * mm, "end": v(7.64, -3.2) * mm});
            skLineSegment(sketch, "E6005", {"start": v(7.64, -3.2) * mm, "end": v(7.65, -3.19) * mm});
            skLineSegment(sketch, "E6006", {"start": v(7.65, -3.19) * mm, "end": v(7.67, -3.18) * mm});
            skLineSegment(sketch, "E6007", {"start": v(7.67, -3.18) * mm, "end": v(7.69, -3.17) * mm});
            skLineSegment(sketch, "E6008", {"start": v(7.69, -3.17) * mm, "end": v(7.7, -3.16) * mm});
            skLineSegment(sketch, "E6009", {"start": v(7.7, -3.16) * mm, "end": v(7.72, -3.15) * mm});
            skLineSegment(sketch, "E6010", {"start": v(7.72, -3.15) * mm, "end": v(7.74, -3.14) * mm});
            skLineSegment(sketch, "E6011", {"start": v(7.74, -3.14) * mm, "end": v(7.75, -3.13) * mm});
            skLineSegment(sketch, "E6012", {"start": v(7.75, -3.13) * mm, "end": v(7.77, -3.12) * mm});
            skLineSegment(sketch, "E6013", {"start": v(7.77, -3.12) * mm, "end": v(7.78, -3.1) * mm});
            skLineSegment(sketch, "E6014", {"start": v(7.78, -3.1) * mm, "end": v(7.8, -3.1) * mm});
            skLineSegment(sketch, "E6015", {"start": v(7.8, -3.1) * mm, "end": v(7.81, -3.08) * mm});
            skLineSegment(sketch, "E6016", {"start": v(7.81, -3.08) * mm, "end": v(7.82, -3.07) * mm});
            skLineSegment(sketch, "E6017", {"start": v(7.82, -3.07) * mm, "end": v(7.84, -3.06) * mm});
            skLineSegment(sketch, "E6018", {"start": v(7.84, -3.06) * mm, "end": v(7.85, -3.04) * mm});
            skLineSegment(sketch, "E6019", {"start": v(7.85, -3.04) * mm, "end": v(7.86, -3.03) * mm});
            skLineSegment(sketch, "E6020", {"start": v(7.86, -3.03) * mm, "end": v(7.87, -3.02) * mm});
            skLineSegment(sketch, "E6021", {"start": v(7.87, -3.02) * mm, "end": v(7.88, -3) * mm});
            skLineSegment(sketch, "E6022", {"start": v(7.88, -3) * mm, "end": v(7.9, -2.99) * mm});
            skLineSegment(sketch, "E6023", {"start": v(7.9, -2.99) * mm, "end": v(7.9, -2.97) * mm});
            skLineSegment(sketch, "E6024", {"start": v(7.9, -2.97) * mm, "end": v(7.91, -2.96) * mm});
            skLineSegment(sketch, "E6025", {"start": v(7.91, -2.96) * mm, "end": v(7.92, -2.94) * mm});
            skLineSegment(sketch, "E6026", {"start": v(7.92, -2.94) * mm, "end": v(7.93, -2.92) * mm});
            skLineSegment(sketch, "E6027", {"start": v(7.93, -2.92) * mm, "end": v(7.94, -2.9) * mm});
            skLineSegment(sketch, "E6028", {"start": v(7.94, -2.9) * mm, "end": v(7.94, -2.89) * mm});
            skLineSegment(sketch, "E6029", {"start": v(7.94, -2.89) * mm, "end": v(7.95, -2.87) * mm});
            skLineSegment(sketch, "E6030", {"start": v(7.95, -2.87) * mm, "end": v(7.96, -2.85) * mm});
            skLineSegment(sketch, "E6031", {"start": v(7.96, -2.85) * mm, "end": v(7.96, -2.84) * mm});
            skLineSegment(sketch, "E6032", {"start": v(7.96, -2.84) * mm, "end": v(7.97, -2.82) * mm});
            skLineSegment(sketch, "E6033", {"start": v(7.97, -2.82) * mm, "end": v(7.97, -2.8) * mm});
            skLineSegment(sketch, "E6034", {"start": v(7.97, -2.8) * mm, "end": v(7.98, -2.78) * mm});
            skLineSegment(sketch, "E6035", {"start": v(7.98, -2.78) * mm, "end": v(7.98, -2.76) * mm});
            skLineSegment(sketch, "E6036", {"start": v(7.98, -2.76) * mm, "end": v(7.98, -2.74) * mm});
            skLineSegment(sketch, "E6037", {"start": v(7.98, -2.74) * mm, "end": v(7.99, -2.73) * mm});
            skLineSegment(sketch, "E6038", {"start": v(7.99, -2.73) * mm, "end": v(7.99, -2.7) * mm});
            skLineSegment(sketch, "E6039", {"start": v(7.99, -2.7) * mm, "end": v(8, -2.69) * mm});
            skLineSegment(sketch, "E6040", {"start": v(8, -2.69) * mm, "end": v(8, -2.67) * mm});
            skLineSegment(sketch, "E6041", {"start": v(8, -2.67) * mm, "end": v(8, -2.65) * mm});
            skLineSegment(sketch, "E6042", {"start": v(8, -2.65) * mm, "end": v(8, -2.63) * mm});
            skLineSegment(sketch, "E6043", {"start": v(8, -2.63) * mm, "end": v(8, -2.6) * mm});
            skLineSegment(sketch, "E6044", {"start": v(8, -2.6) * mm, "end": v(8, -2.59) * mm});
            skLineSegment(sketch, "E6045", {"start": v(8, -2.59) * mm, "end": v(8, -2.57) * mm});
            skLineSegment(sketch, "E6046", {"start": v(8, -2.57) * mm, "end": v(7.99, -2.55) * mm});
            skLineSegment(sketch, "E6047", {"start": v(7.99, -2.55) * mm, "end": v(7.99, -2.53) * mm});
            skLineSegment(sketch, "E6048", {"start": v(7.99, -2.53) * mm, "end": v(7.98, -2.51) * mm});
            skLineSegment(sketch, "E6049", {"start": v(7.98, -2.51) * mm, "end": v(7.98, -2.5) * mm});
            skLineSegment(sketch, "E6050", {"start": v(7.98, -2.5) * mm, "end": v(7.98, -2.47) * mm});
            skLineSegment(sketch, "E6051", {"start": v(7.98, -2.47) * mm, "end": v(7.97, -2.45) * mm});
            skLineSegment(sketch, "E6052", {"start": v(7.97, -2.45) * mm, "end": v(7.97, -2.44) * mm});
            skLineSegment(sketch, "E6053", {"start": v(7.97, -2.44) * mm, "end": v(7.96, -2.42) * mm});
            skLineSegment(sketch, "E6054", {"start": v(7.96, -2.42) * mm, "end": v(7.96, -2.4) * mm});
            skLineSegment(sketch, "E6055", {"start": v(7.96, -2.4) * mm, "end": v(7.95, -2.38) * mm});
            skLineSegment(sketch, "E6056", {"start": v(7.95, -2.38) * mm, "end": v(7.94, -2.36) * mm});
            skLineSegment(sketch, "E6057", {"start": v(7.94, -2.36) * mm, "end": v(7.94, -2.35) * mm});
            skLineSegment(sketch, "E6058", {"start": v(7.94, -2.35) * mm, "end": v(7.93, -2.33) * mm});
            skLineSegment(sketch, "E6059", {"start": v(7.93, -2.33) * mm, "end": v(7.92, -2.31) * mm});
            skLineSegment(sketch, "E6060", {"start": v(7.92, -2.31) * mm, "end": v(7.9, -2.3) * mm});
            skLineSegment(sketch, "E6061", {"start": v(7.9, -2.3) * mm, "end": v(7.9, -2.28) * mm});
            skLineSegment(sketch, "E6062", {"start": v(7.9, -2.28) * mm, "end": v(7.89, -2.26) * mm});
            skLineSegment(sketch, "E6063", {"start": v(7.89, -2.26) * mm, "end": v(7.88, -2.25) * mm});
            skLineSegment(sketch, "E6064", {"start": v(7.88, -2.25) * mm, "end": v(7.87, -2.23) * mm});
            skLineSegment(sketch, "E6065", {"start": v(7.87, -2.23) * mm, "end": v(7.86, -2.22) * mm});
            skLineSegment(sketch, "E6066", {"start": v(7.86, -2.22) * mm, "end": v(7.84, -2.2) * mm});
            skLineSegment(sketch, "E6067", {"start": v(7.84, -2.2) * mm, "end": v(7.83, -2.19) * mm});
            skLineSegment(sketch, "E6068", {"start": v(7.83, -2.19) * mm, "end": v(7.82, -2.17) * mm});
            skLineSegment(sketch, "E6069", {"start": v(7.82, -2.17) * mm, "end": v(7.8, -2.16) * mm});
            skLineSegment(sketch, "E6070", {"start": v(7.8, -2.16) * mm, "end": v(7.79, -2.15) * mm});
            skLineSegment(sketch, "E6071", {"start": v(7.79, -2.15) * mm, "end": v(7.77, -2.13) * mm});
            skLineSegment(sketch, "E6072", {"start": v(7.77, -2.13) * mm, "end": v(7.76, -2.12) * mm});
            skLineSegment(sketch, "E6073", {"start": v(7.76, -2.12) * mm, "end": v(7.74, -2.1) * mm});
            skLineSegment(sketch, "E6074", {"start": v(7.74, -2.1) * mm, "end": v(7.73, -2.1) * mm});
            skLineSegment(sketch, "E6075", {"start": v(7.73, -2.1) * mm, "end": v(7.7, -2.09) * mm});
            skLineSegment(sketch, "E6076", {"start": v(7.7, -2.09) * mm, "end": v(7.7, -2.08) * mm});
            skLineSegment(sketch, "E6077", {"start": v(7.7, -2.08) * mm, "end": v(7.67, -2.07) * mm});
            skLineSegment(sketch, "E6078", {"start": v(7.67, -2.07) * mm, "end": v(7.65, -2.06) * mm});
            skLineSegment(sketch, "E6079", {"start": v(7.65, -2.06) * mm, "end": v(7.64, -2.05) * mm});
            skLineSegment(sketch, "E6080", {"start": v(7.64, -2.05) * mm, "end": v(7.62, -2.04) * mm});
            skLineSegment(sketch, "E6081", {"start": v(7.62, -2.04) * mm, "end": v(7.6, -2.03) * mm});
            skLineSegment(sketch, "E6082", {"start": v(7.6, -2.03) * mm, "end": v(7.57, -2.03) * mm});
            skLineSegment(sketch, "E6083", {"start": v(7.57, -2.03) * mm, "end": v(7.55, -2.02) * mm});
            skLineSegment(sketch, "E6084", {"start": v(7.55, -2.02) * mm, "end": v(7.53, -2.01) * mm});
            skLineSegment(sketch, "E6085", {"start": v(7.53, -2.01) * mm, "end": v(7.5, -2) * mm});
            skLineSegment(sketch, "E6086", {"start": v(7.5, -2) * mm, "end": v(7.48, -2) * mm});
            skLineSegment(sketch, "E6087", {"start": v(7.48, -2) * mm, "end": v(7.46, -2) * mm});
            skLineSegment(sketch, "E6088", {"start": v(7.46, -2) * mm, "end": v(7.44, -2) * mm});
            skLineSegment(sketch, "E6089", {"start": v(7.44, -2) * mm, "end": v(7.41, -2) * mm});
            skLineSegment(sketch, "E6090", {"start": v(7.41, -2) * mm, "end": v(7.39, -2) * mm});
            skLineSegment(sketch, "E6091", {"start": v(7.39, -2) * mm, "end": v(7.36, -2) * mm});
            skLineSegment(sketch, "E6092", {"start": v(7.36, -2) * mm, "end": v(7.33, -2) * mm});
            skLineSegment(sketch, "E6093", {"start": v(7.33, -2) * mm, "end": v(7.33, -2) * mm});
            skLineSegment(sketch, "E6094", {"start": v(7.33, -2) * mm, "end": v(7.32, -2) * mm});
            skLineSegment(sketch, "E6095", {"start": v(7.32, -2) * mm, "end": v(7.3, -2) * mm});
            skLineSegment(sketch, "E6096", {"start": v(7.3, -2) * mm, "end": v(7.29, -2) * mm});
            skLineSegment(sketch, "E6097", {"start": v(7.29, -2) * mm, "end": v(7.27, -2) * mm});
            skLineSegment(sketch, "E6098", {"start": v(7.27, -2) * mm, "end": v(7.24, -2) * mm});
            skLineSegment(sketch, "E6099", {"start": v(7.24, -2) * mm, "end": v(7.22, -2) * mm});
            skLineSegment(sketch, "E6100", {"start": v(7.22, -2) * mm, "end": v(7.19, -2) * mm});
            skLineSegment(sketch, "E6101", {"start": v(7.19, -2) * mm, "end": v(7.16, -2) * mm});
            skLineSegment(sketch, "E6102", {"start": v(7.16, -2) * mm, "end": v(7.12, -2) * mm});
            skLineSegment(sketch, "E6103", {"start": v(7.12, -2) * mm, "end": v(7.09, -2) * mm});
            skLineSegment(sketch, "E6104", {"start": v(7.09, -2) * mm, "end": v(7.05, -2) * mm});
            skLineSegment(sketch, "E6105", {"start": v(7.05, -2) * mm, "end": v(7, -2) * mm});
            skLineSegment(sketch, "E6106", {"start": v(7, -2) * mm, "end": v(6.97, -2) * mm});
            skLineSegment(sketch, "E6107", {"start": v(6.97, -2) * mm, "end": v(6.92, -2) * mm});
            skLineSegment(sketch, "E6108", {"start": v(6.92, -2) * mm, "end": v(6.88, -2) * mm});
            skLineSegment(sketch, "E6109", {"start": v(6.88, -2) * mm, "end": v(6.83, -2) * mm});
            skLineSegment(sketch, "E6110", {"start": v(6.83, -2) * mm, "end": v(6.78, -2) * mm});
            skLineSegment(sketch, "E6111", {"start": v(6.78, -2) * mm, "end": v(6.74, -2) * mm});
            skLineSegment(sketch, "E6112", {"start": v(6.74, -2) * mm, "end": v(6.69, -2) * mm});
            skLineSegment(sketch, "E6113", {"start": v(6.69, -2) * mm, "end": v(6.64, -2) * mm});
            skLineSegment(sketch, "E6114", {"start": v(6.64, -2) * mm, "end": v(6.59, -2) * mm});
            skLineSegment(sketch, "E6115", {"start": v(6.59, -2) * mm, "end": v(6.54, -2) * mm});
            skLineSegment(sketch, "E6116", {"start": v(6.54, -2) * mm, "end": v(6.49, -2) * mm});
            skLineSegment(sketch, "E6117", {"start": v(6.49, -2) * mm, "end": v(6.43, -2) * mm});
            skLineSegment(sketch, "E6118", {"start": v(6.43, -2) * mm, "end": v(6.38, -2) * mm});
            skLineSegment(sketch, "E6119", {"start": v(6.38, -2) * mm, "end": v(6.33, -2) * mm});
            skLineSegment(sketch, "E6120", {"start": v(6.33, -2) * mm, "end": v(6.28, -2) * mm});
            skLineSegment(sketch, "E6121", {"start": v(6.28, -2) * mm, "end": v(6.23, -2) * mm});
            skLineSegment(sketch, "E6122", {"start": v(6.23, -2) * mm, "end": v(6.19, -2) * mm});
            skLineSegment(sketch, "E6123", {"start": v(6.19, -2) * mm, "end": v(6.14, -2) * mm});
            skLineSegment(sketch, "E6124", {"start": v(6.14, -2) * mm, "end": v(6.1, -2) * mm});
            skLineSegment(sketch, "E6125", {"start": v(6.1, -2) * mm, "end": v(6.05, -2) * mm});
            skLineSegment(sketch, "E6126", {"start": v(6.05, -2) * mm, "end": v(6, -2) * mm});
            skLineSegment(sketch, "E6127", {"start": v(6, -2) * mm, "end": v(5.96, -2) * mm});
            skLineSegment(sketch, "E6128", {"start": v(5.96, -2) * mm, "end": v(5.92, -2) * mm});
            skLineSegment(sketch, "E6129", {"start": v(5.92, -2) * mm, "end": v(5.88, -2) * mm});
            skLineSegment(sketch, "E6130", {"start": v(5.88, -2) * mm, "end": v(5.85, -2) * mm});
            skLineSegment(sketch, "E6131", {"start": v(5.85, -2) * mm, "end": v(5.81, -2) * mm});
            skLineSegment(sketch, "E6132", {"start": v(5.81, -2) * mm, "end": v(5.78, -2) * mm});
            skLineSegment(sketch, "E6133", {"start": v(5.78, -2) * mm, "end": v(5.75, -2) * mm});
            skLineSegment(sketch, "E6134", {"start": v(5.75, -2) * mm, "end": v(5.73, -2) * mm});
            skLineSegment(sketch, "E6135", {"start": v(5.73, -2) * mm, "end": v(5.7, -2) * mm});
            skLineSegment(sketch, "E6136", {"start": v(5.7, -2) * mm, "end": v(5.68, -2) * mm});
            skLineSegment(sketch, "E6137", {"start": v(5.68, -2) * mm, "end": v(5.67, -2) * mm});
            skLineSegment(sketch, "E6138", {"start": v(5.67, -2) * mm, "end": v(5.65, -2) * mm});
            skLineSegment(sketch, "E6139", {"start": v(5.65, -2) * mm, "end": v(5.64, -2) * mm});
            skLineSegment(sketch, "E6140", {"start": v(5.64, -2) * mm, "end": v(5.64, -2) * mm});
            skLineSegment(sketch, "E6141", {"start": v(5.64, -2) * mm, "end": v(5.63, -2) * mm});
            skLineSegment(sketch, "E6142", {"start": v(5.63, -2) * mm, "end": v(5.61, -2) * mm});
            skLineSegment(sketch, "E6143", {"start": v(5.61, -2) * mm, "end": v(5.6, -2) * mm});
            skLineSegment(sketch, "E6144", {"start": v(5.6, -2) * mm, "end": v(5.6, -2) * mm});
            skLineSegment(sketch, "E6145", {"start": v(5.6, -2) * mm, "end": v(5.58, -2) * mm});
            skLineSegment(sketch, "E6146", {"start": v(5.58, -2) * mm, "end": v(5.57, -2) * mm});
            skLineSegment(sketch, "E6147", {"start": v(5.57, -2) * mm, "end": v(5.56, -2) * mm});
            skLineSegment(sketch, "E6148", {"start": v(5.56, -2) * mm, "end": v(5.55, -2) * mm});
            skLineSegment(sketch, "E6149", {"start": v(5.55, -2) * mm, "end": v(5.54, -2) * mm});
            skLineSegment(sketch, "E6150", {"start": v(5.54, -2) * mm, "end": v(5.54, -2) * mm});
            skLineSegment(sketch, "E6151", {"start": v(5.54, -2) * mm, "end": v(5.53, -2) * mm});
            skLineSegment(sketch, "E6152", {"start": v(5.53, -2) * mm, "end": v(5.52, -2) * mm});
            skLineSegment(sketch, "E6153", {"start": v(5.52, -2) * mm, "end": v(5.5, -2.01) * mm});
            skLineSegment(sketch, "E6154", {"start": v(5.5, -2.01) * mm, "end": v(5.5, -2.01) * mm});
            skLineSegment(sketch, "E6155", {"start": v(5.5, -2.01) * mm, "end": v(5.5, -2.02) * mm});
            skLineSegment(sketch, "E6156", {"start": v(5.5, -2.02) * mm, "end": v(5.48, -2.02) * mm});
            skLineSegment(sketch, "E6157", {"start": v(5.48, -2.02) * mm, "end": v(5.48, -2.02) * mm});
            skLineSegment(sketch, "E6158", {"start": v(5.48, -2.02) * mm, "end": v(5.47, -2.03) * mm});
            skLineSegment(sketch, "E6159", {"start": v(5.47, -2.03) * mm, "end": v(5.46, -2.03) * mm});
            skLineSegment(sketch, "E6160", {"start": v(5.46, -2.03) * mm, "end": v(5.45, -2.03) * mm});
            skLineSegment(sketch, "E6161", {"start": v(5.45, -2.03) * mm, "end": v(5.45, -2.04) * mm});
            skLineSegment(sketch, "E6162", {"start": v(5.45, -2.04) * mm, "end": v(5.44, -2.04) * mm});
            skLineSegment(sketch, "E6163", {"start": v(5.44, -2.04) * mm, "end": v(5.43, -2.05) * mm});
            skLineSegment(sketch, "E6164", {"start": v(5.43, -2.05) * mm, "end": v(5.43, -2.05) * mm});
            skLineSegment(sketch, "E6165", {"start": v(5.43, -2.05) * mm, "end": v(5.42, -2.05) * mm});
            skLineSegment(sketch, "E6166", {"start": v(5.42, -2.05) * mm, "end": v(5.42, -2.06) * mm});
            skLineSegment(sketch, "E6167", {"start": v(5.42, -2.06) * mm, "end": v(5.41, -2.06) * mm});
            skLineSegment(sketch, "E6168", {"start": v(5.41, -2.06) * mm, "end": v(5.4, -2.07) * mm});
            skLineSegment(sketch, "E6169", {"start": v(5.4, -2.07) * mm, "end": v(5.4, -2.07) * mm});
            skLineSegment(sketch, "E6170", {"start": v(5.4, -2.07) * mm, "end": v(5.4, -2.08) * mm});
            skLineSegment(sketch, "E6171", {"start": v(5.4, -2.08) * mm, "end": v(5.39, -2.08) * mm});
            skLineSegment(sketch, "E6172", {"start": v(5.39, -2.08) * mm, "end": v(5.38, -2.09) * mm});
            skLineSegment(sketch, "E6173", {"start": v(5.38, -2.09) * mm, "end": v(5.38, -2.1) * mm});
            skLineSegment(sketch, "E6174", {"start": v(5.38, -2.1) * mm, "end": v(5.38, -2.1) * mm});
            skLineSegment(sketch, "E6175", {"start": v(5.38, -2.1) * mm, "end": v(5.37, -2.1) * mm});
            skLineSegment(sketch, "E6176", {"start": v(5.37, -2.1) * mm, "end": v(5.37, -2.11) * mm});
            skLineSegment(sketch, "E6177", {"start": v(5.37, -2.11) * mm, "end": v(5.36, -2.12) * mm});
            skLineSegment(sketch, "E6178", {"start": v(5.36, -2.12) * mm, "end": v(5.36, -2.12) * mm});
            skLineSegment(sketch, "E6179", {"start": v(5.36, -2.12) * mm, "end": v(5.36, -2.13) * mm});
            skLineSegment(sketch, "E6180", {"start": v(5.36, -2.13) * mm, "end": v(5.35, -2.14) * mm});
            skLineSegment(sketch, "E6181", {"start": v(5.35, -2.14) * mm, "end": v(5.35, -2.14) * mm});
            skLineSegment(sketch, "E6182", {"start": v(5.35, -2.14) * mm, "end": v(5.35, -2.15) * mm});
            skLineSegment(sketch, "E6183", {"start": v(5.35, -2.15) * mm, "end": v(5.34, -2.16) * mm});
            skLineSegment(sketch, "E6184", {"start": v(5.34, -2.16) * mm, "end": v(5.34, -2.16) * mm});
            skLineSegment(sketch, "E6185", {"start": v(5.34, -2.16) * mm, "end": v(5.34, -2.17) * mm});
            skLineSegment(sketch, "E6186", {"start": v(5.34, -2.17) * mm, "end": v(5.34, -2.18) * mm});
            skLineSegment(sketch, "E6187", {"start": v(5.34, -2.18) * mm, "end": v(5.34, -2.18) * mm});
            skLineSegment(sketch, "E6188", {"start": v(5.34, -2.18) * mm, "end": v(5.33, -2.2) * mm});
            skLineSegment(sketch, "E6189", {"start": v(5.33, -2.2) * mm, "end": v(5.33, -2.2) * mm});
            skLineSegment(sketch, "E6190", {"start": v(5.33, -2.2) * mm, "end": v(5.33, -2.21) * mm});
            skLineSegment(sketch, "E6191", {"start": v(5.33, -2.21) * mm, "end": v(5.33, -2.22) * mm});
            skLineSegment(sketch, "E6192", {"start": v(5.33, -2.22) * mm, "end": v(5.34, -2.23) * mm});
            skLineSegment(sketch, "E6193", {"start": v(5.34, -2.23) * mm, "end": v(5.34, -2.24) * mm});
            skLineSegment(sketch, "E6194", {"start": v(5.34, -2.24) * mm, "end": v(5.34, -2.25) * mm});
            skLineSegment(sketch, "E6195", {"start": v(5.34, -2.25) * mm, "end": v(5.34, -2.25) * mm});
            skLineSegment(sketch, "E6196", {"start": v(5.34, -2.25) * mm, "end": v(5.34, -2.26) * mm});
            skLineSegment(sketch, "E6197", {"start": v(5.34, -2.26) * mm, "end": v(5.35, -2.27) * mm});
            skLineSegment(sketch, "E6198", {"start": v(5.35, -2.27) * mm, "end": v(5.35, -2.28) * mm});
            skLineSegment(sketch, "E6199", {"start": v(5.35, -2.28) * mm, "end": v(5.35, -2.29) * mm});
            skLineSegment(sketch, "E6200", {"start": v(5.35, -2.29) * mm, "end": v(5.36, -2.3) * mm});
            skLineSegment(sketch, "E6201", {"start": v(5.36, -2.3) * mm, "end": v(5.36, -2.3) * mm});
            skLineSegment(sketch, "E6202", {"start": v(5.36, -2.3) * mm, "end": v(5.37, -2.32) * mm});
            skLineSegment(sketch, "E6203", {"start": v(5.37, -2.32) * mm, "end": v(5.37, -2.32) * mm});
            skLineSegment(sketch, "E6204", {"start": v(5.37, -2.32) * mm, "end": v(5.38, -2.33) * mm});
            skLineSegment(sketch, "E6205", {"start": v(5.38, -2.33) * mm, "end": v(5.38, -2.34) * mm});
            skLineSegment(sketch, "E6206", {"start": v(5.38, -2.34) * mm, "end": v(5.39, -2.34) * mm});
            skLineSegment(sketch, "E6207", {"start": v(5.39, -2.34) * mm, "end": v(5.4, -2.35) * mm});
            skLineSegment(sketch, "E6208", {"start": v(5.4, -2.35) * mm, "end": v(5.4, -2.36) * mm});
            skLineSegment(sketch, "E6209", {"start": v(5.4, -2.36) * mm, "end": v(5.4, -2.36) * mm});
            skLineSegment(sketch, "E6210", {"start": v(5.4, -2.36) * mm, "end": v(5.4, -2.37) * mm});
            skLineSegment(sketch, "E6211", {"start": v(5.4, -2.37) * mm, "end": v(5.41, -2.38) * mm});
            skLineSegment(sketch, "E6212", {"start": v(5.41, -2.38) * mm, "end": v(5.42, -2.38) * mm});
            skLineSegment(sketch, "E6213", {"start": v(5.42, -2.38) * mm, "end": v(5.42, -2.39) * mm});
            skLineSegment(sketch, "E6214", {"start": v(5.42, -2.39) * mm, "end": v(5.43, -2.4) * mm});
            skLineSegment(sketch, "E6215", {"start": v(5.43, -2.4) * mm, "end": v(5.44, -2.4) * mm});
            skLineSegment(sketch, "E6216", {"start": v(5.44, -2.4) * mm, "end": v(5.45, -2.4) * mm});
            skLineSegment(sketch, "E6217", {"start": v(5.45, -2.4) * mm, "end": v(5.45, -2.4) * mm});
            skLineSegment(sketch, "E6218", {"start": v(5.45, -2.4) * mm, "end": v(5.46, -2.41) * mm});
            skLineSegment(sketch, "E6219", {"start": v(5.46, -2.41) * mm, "end": v(5.47, -2.42) * mm});
            skLineSegment(sketch, "E6220", {"start": v(5.47, -2.42) * mm, "end": v(5.48, -2.42) * mm});
            skLineSegment(sketch, "E6221", {"start": v(5.48, -2.42) * mm, "end": v(5.48, -2.43) * mm});
            skLineSegment(sketch, "E6222", {"start": v(5.48, -2.43) * mm, "end": v(5.5, -2.43) * mm});
            skLineSegment(sketch, "E6223", {"start": v(5.5, -2.43) * mm, "end": v(5.5, -2.43) * mm});
            skLineSegment(sketch, "E6224", {"start": v(5.5, -2.43) * mm, "end": v(5.5, -2.44) * mm});
            skLineSegment(sketch, "E6225", {"start": v(5.5, -2.44) * mm, "end": v(5.52, -2.44) * mm});
            skLineSegment(sketch, "E6226", {"start": v(5.52, -2.44) * mm, "end": v(5.53, -2.44) * mm});
            skLineSegment(sketch, "E6227", {"start": v(5.53, -2.44) * mm, "end": v(5.54, -2.45) * mm});
            skLineSegment(sketch, "E6228", {"start": v(5.54, -2.45) * mm, "end": v(5.55, -2.45) * mm});
            skLineSegment(sketch, "E6229", {"start": v(5.55, -2.45) * mm, "end": v(5.56, -2.45) * mm});
            skLineSegment(sketch, "E6230", {"start": v(5.56, -2.45) * mm, "end": v(5.57, -2.45) * mm});
            skLineSegment(sketch, "E6231", {"start": v(5.57, -2.45) * mm, "end": v(5.58, -2.46) * mm});
            skLineSegment(sketch, "E6232", {"start": v(5.58, -2.46) * mm, "end": v(5.59, -2.46) * mm});
            skLineSegment(sketch, "E6233", {"start": v(5.59, -2.46) * mm, "end": v(5.6, -2.46) * mm});
            skLineSegment(sketch, "E6234", {"start": v(5.6, -2.46) * mm, "end": v(5.61, -2.46) * mm});
            skLineSegment(sketch, "E6235", {"start": v(5.61, -2.46) * mm, "end": v(5.62, -2.46) * mm});
            skLineSegment(sketch, "E6236", {"start": v(5.62, -2.46) * mm, "end": v(5.64, -2.46) * mm});
            skLineSegment(sketch, "E6237", {"start": v(5.64, -2.46) * mm, "end": v(5.65, -2.46) * mm});
            skLineSegment(sketch, "E6238", {"start": v(5.65, -2.46) * mm, "end": v(5.66, -2.46) * mm});
            skLineSegment(sketch, "E6239", {"start": v(5.66, -2.46) * mm, "end": v(5.66, -2.46) * mm});
            skLineSegment(sketch, "E6240", {"start": v(5.66, -2.46) * mm, "end": v(5.67, -2.46) * mm});
            skLineSegment(sketch, "E6241", {"start": v(5.67, -2.46) * mm, "end": v(5.68, -2.46) * mm});
            skLineSegment(sketch, "E6242", {"start": v(5.68, -2.46) * mm, "end": v(5.7, -2.46) * mm});
            skLineSegment(sketch, "E6243", {"start": v(5.7, -2.46) * mm, "end": v(5.7, -2.46) * mm});
            skLineSegment(sketch, "E6244", {"start": v(5.7, -2.46) * mm, "end": v(5.73, -2.46) * mm});
            skLineSegment(sketch, "E6245", {"start": v(5.73, -2.46) * mm, "end": v(5.75, -2.46) * mm});
            skLineSegment(sketch, "E6246", {"start": v(5.75, -2.46) * mm, "end": v(5.78, -2.46) * mm});
            skLineSegment(sketch, "E6247", {"start": v(5.78, -2.46) * mm, "end": v(5.8, -2.46) * mm});
            skLineSegment(sketch, "E6248", {"start": v(5.8, -2.46) * mm, "end": v(5.83, -2.46) * mm});
            skLineSegment(sketch, "E6249", {"start": v(5.83, -2.46) * mm, "end": v(5.87, -2.46) * mm});
            skLineSegment(sketch, "E6250", {"start": v(5.87, -2.46) * mm, "end": v(5.9, -2.46) * mm});
            skLineSegment(sketch, "E6251", {"start": v(5.9, -2.46) * mm, "end": v(5.94, -2.46) * mm});
            skLineSegment(sketch, "E6252", {"start": v(5.94, -2.46) * mm, "end": v(5.98, -2.46) * mm});
            skLineSegment(sketch, "E6253", {"start": v(5.98, -2.46) * mm, "end": v(6.02, -2.46) * mm});
            skLineSegment(sketch, "E6254", {"start": v(6.02, -2.46) * mm, "end": v(6.06, -2.46) * mm});
            skLineSegment(sketch, "E6255", {"start": v(6.06, -2.46) * mm, "end": v(6.1, -2.46) * mm});
            skLineSegment(sketch, "E6256", {"start": v(6.1, -2.46) * mm, "end": v(6.15, -2.46) * mm});
            skLineSegment(sketch, "E6257", {"start": v(6.15, -2.46) * mm, "end": v(6.2, -2.46) * mm});
            skLineSegment(sketch, "E6258", {"start": v(6.2, -2.46) * mm, "end": v(6.25, -2.46) * mm});
            skLineSegment(sketch, "E6259", {"start": v(6.25, -2.46) * mm, "end": v(6.3, -2.46) * mm});
            skLineSegment(sketch, "E6260", {"start": v(6.3, -2.46) * mm, "end": v(6.35, -2.46) * mm});
            skLineSegment(sketch, "E6261", {"start": v(6.35, -2.46) * mm, "end": v(6.4, -2.46) * mm});
            skLineSegment(sketch, "E6262", {"start": v(6.4, -2.46) * mm, "end": v(6.45, -2.46) * mm});
            skLineSegment(sketch, "E6263", {"start": v(6.45, -2.46) * mm, "end": v(6.5, -2.46) * mm});
            skLineSegment(sketch, "E6264", {"start": v(6.5, -2.46) * mm, "end": v(6.55, -2.46) * mm});
            skLineSegment(sketch, "E6265", {"start": v(6.55, -2.46) * mm, "end": v(6.6, -2.46) * mm});
            skLineSegment(sketch, "E6266", {"start": v(6.6, -2.46) * mm, "end": v(6.65, -2.46) * mm});
            skLineSegment(sketch, "E6267", {"start": v(6.65, -2.46) * mm, "end": v(6.7, -2.46) * mm});
            skLineSegment(sketch, "E6268", {"start": v(6.7, -2.46) * mm, "end": v(6.74, -2.46) * mm});
            skLineSegment(sketch, "E6269", {"start": v(6.74, -2.46) * mm, "end": v(6.8, -2.46) * mm});
            skLineSegment(sketch, "E6270", {"start": v(6.8, -2.46) * mm, "end": v(6.84, -2.46) * mm});
            skLineSegment(sketch, "E6271", {"start": v(6.84, -2.46) * mm, "end": v(6.88, -2.46) * mm});
            skLineSegment(sketch, "E6272", {"start": v(6.88, -2.46) * mm, "end": v(6.93, -2.46) * mm});
            skLineSegment(sketch, "E6273", {"start": v(6.93, -2.46) * mm, "end": v(6.97, -2.46) * mm});
            skLineSegment(sketch, "E6274", {"start": v(6.97, -2.46) * mm, "end": v(7.01, -2.46) * mm});
            skLineSegment(sketch, "E6275", {"start": v(7.01, -2.46) * mm, "end": v(7.05, -2.46) * mm});
            skLineSegment(sketch, "E6276", {"start": v(7.05, -2.46) * mm, "end": v(7.1, -2.46) * mm});
            skLineSegment(sketch, "E6277", {"start": v(7.1, -2.46) * mm, "end": v(7.13, -2.46) * mm});
            skLineSegment(sketch, "E6278", {"start": v(7.13, -2.46) * mm, "end": v(7.16, -2.46) * mm});
            skLineSegment(sketch, "E6279", {"start": v(7.16, -2.46) * mm, "end": v(7.2, -2.46) * mm});
            skLineSegment(sketch, "E6280", {"start": v(7.2, -2.46) * mm, "end": v(7.22, -2.46) * mm});
            skLineSegment(sketch, "E6281", {"start": v(7.22, -2.46) * mm, "end": v(7.24, -2.46) * mm});
            skLineSegment(sketch, "E6282", {"start": v(7.24, -2.46) * mm, "end": v(7.27, -2.46) * mm});
            skLineSegment(sketch, "E6283", {"start": v(7.27, -2.46) * mm, "end": v(7.29, -2.46) * mm});
            skLineSegment(sketch, "E6284", {"start": v(7.29, -2.46) * mm, "end": v(7.3, -2.46) * mm});
            skLineSegment(sketch, "E6285", {"start": v(7.3, -2.46) * mm, "end": v(7.32, -2.46) * mm});
            skLineSegment(sketch, "E6286", {"start": v(7.32, -2.46) * mm, "end": v(7.33, -2.46) * mm});
            skLineSegment(sketch, "E6287", {"start": v(7.33, -2.46) * mm, "end": v(7.33, -2.46) * mm});
            skLineSegment(sketch, "E6288", {"start": v(7.33, -2.46) * mm, "end": v(7.34, -2.46) * mm});
            skLineSegment(sketch, "E6289", {"start": v(7.34, -2.46) * mm, "end": v(7.34, -2.46) * mm});
            skLineSegment(sketch, "E6290", {"start": v(7.34, -2.46) * mm, "end": v(7.35, -2.46) * mm});
            skLineSegment(sketch, "E6291", {"start": v(7.35, -2.46) * mm, "end": v(7.36, -2.46) * mm});
            skLineSegment(sketch, "E6292", {"start": v(7.36, -2.46) * mm, "end": v(7.36, -2.47) * mm});
            skLineSegment(sketch, "E6293", {"start": v(7.36, -2.47) * mm, "end": v(7.37, -2.47) * mm});
            skLineSegment(sketch, "E6294", {"start": v(7.37, -2.47) * mm, "end": v(7.37, -2.47) * mm});
            skLineSegment(sketch, "E6295", {"start": v(7.37, -2.47) * mm, "end": v(7.38, -2.47) * mm});
            skLineSegment(sketch, "E6296", {"start": v(7.38, -2.47) * mm, "end": v(7.38, -2.47) * mm});
            skLineSegment(sketch, "E6297", {"start": v(7.38, -2.47) * mm, "end": v(7.39, -2.47) * mm});
            skLineSegment(sketch, "E6298", {"start": v(7.39, -2.47) * mm, "end": v(7.4, -2.47) * mm});
            skLineSegment(sketch, "E6299", {"start": v(7.4, -2.47) * mm, "end": v(7.4, -2.48) * mm});
            skLineSegment(sketch, "E6300", {"start": v(7.4, -2.48) * mm, "end": v(7.4, -2.48) * mm});
            skLineSegment(sketch, "E6301", {"start": v(7.4, -2.48) * mm, "end": v(7.41, -2.49) * mm});
            skLineSegment(sketch, "E6302", {"start": v(7.41, -2.49) * mm, "end": v(7.42, -2.49) * mm});
            skLineSegment(sketch, "E6303", {"start": v(7.42, -2.49) * mm, "end": v(7.42, -2.5) * mm});
            skLineSegment(sketch, "E6304", {"start": v(7.42, -2.5) * mm, "end": v(7.42, -2.5) * mm});
            skLineSegment(sketch, "E6305", {"start": v(7.42, -2.5) * mm, "end": v(7.43, -2.5) * mm});
            skLineSegment(sketch, "E6306", {"start": v(7.43, -2.5) * mm, "end": v(7.43, -2.5) * mm});
            skLineSegment(sketch, "E6307", {"start": v(7.43, -2.5) * mm, "end": v(7.44, -2.5) * mm});
            skLineSegment(sketch, "E6308", {"start": v(7.44, -2.5) * mm, "end": v(7.44, -2.51) * mm});
            skLineSegment(sketch, "E6309", {"start": v(7.44, -2.51) * mm, "end": v(7.44, -2.51) * mm});
            skLineSegment(sketch, "E6310", {"start": v(7.44, -2.51) * mm, "end": v(7.44, -2.52) * mm});
            skLineSegment(sketch, "E6311", {"start": v(7.44, -2.52) * mm, "end": v(7.45, -2.52) * mm});
            skLineSegment(sketch, "E6312", {"start": v(7.45, -2.52) * mm, "end": v(7.45, -2.53) * mm});
            skLineSegment(sketch, "E6313", {"start": v(7.45, -2.53) * mm, "end": v(7.45, -2.53) * mm});
            skLineSegment(sketch, "E6314", {"start": v(7.45, -2.53) * mm, "end": v(7.46, -2.54) * mm});
            skLineSegment(sketch, "E6315", {"start": v(7.46, -2.54) * mm, "end": v(7.46, -2.54) * mm});
            skLineSegment(sketch, "E6316", {"start": v(7.46, -2.54) * mm, "end": v(7.46, -2.55) * mm});
            skLineSegment(sketch, "E6317", {"start": v(7.46, -2.55) * mm, "end": v(7.46, -2.55) * mm});
            skLineSegment(sketch, "E6318", {"start": v(7.46, -2.55) * mm, "end": v(7.46, -2.56) * mm});
            skLineSegment(sketch, "E6319", {"start": v(7.46, -2.56) * mm, "end": v(7.47, -2.56) * mm});
            skLineSegment(sketch, "E6320", {"start": v(7.47, -2.56) * mm, "end": v(7.47, -2.57) * mm});
            skLineSegment(sketch, "E6321", {"start": v(7.47, -2.57) * mm, "end": v(7.47, -2.57) * mm});
            skLineSegment(sketch, "E6322", {"start": v(7.47, -2.57) * mm, "end": v(7.47, -2.58) * mm});
            skLineSegment(sketch, "E6323", {"start": v(7.47, -2.58) * mm, "end": v(7.47, -2.58) * mm});
            skLineSegment(sketch, "E6324", {"start": v(7.47, -2.58) * mm, "end": v(7.47, -2.59) * mm});
            skLineSegment(sketch, "E6325", {"start": v(7.47, -2.59) * mm, "end": v(7.47, -2.6) * mm});
            skLineSegment(sketch, "E6326", {"start": v(7.47, -2.6) * mm, "end": v(7.47, -2.6) * mm});
            skLineSegment(sketch, "E6327", {"start": v(7.47, -2.6) * mm, "end": v(7.47, -2.61) * mm});
            skLineSegment(sketch, "E6328", {"start": v(7.47, -2.61) * mm, "end": v(7.47, -2.62) * mm});
            skLineSegment(sketch, "E6329", {"start": v(7.47, -2.62) * mm, "end": v(7.47, -2.62) * mm});
            skLineSegment(sketch, "E6330", {"start": v(7.47, -2.62) * mm, "end": v(7.47, -2.63) * mm});
            skLineSegment(sketch, "E6331", {"start": v(7.47, -2.63) * mm, "end": v(7.47, -2.63) * mm});
            skLineSegment(sketch, "E6332", {"start": v(7.47, -2.63) * mm, "end": v(7.47, -2.64) * mm});
            skLineSegment(sketch, "E6333", {"start": v(7.47, -2.64) * mm, "end": v(7.47, -2.64) * mm});
            skLineSegment(sketch, "E6334", {"start": v(7.47, -2.64) * mm, "end": v(7.47, -2.65) * mm});
            skLineSegment(sketch, "E6335", {"start": v(7.47, -2.65) * mm, "end": v(7.47, -2.65) * mm});
            skLineSegment(sketch, "E6336", {"start": v(7.47, -2.65) * mm, "end": v(7.47, -2.66) * mm});
            skLineSegment(sketch, "E6337", {"start": v(7.47, -2.66) * mm, "end": v(7.47, -2.66) * mm});
            skLineSegment(sketch, "E6338", {"start": v(7.47, -2.66) * mm, "end": v(7.47, -2.67) * mm});
            skLineSegment(sketch, "E6339", {"start": v(7.47, -2.67) * mm, "end": v(7.47, -2.67) * mm});
            skLineSegment(sketch, "E6340", {"start": v(7.47, -2.67) * mm, "end": v(7.46, -2.67) * mm});
            skLineSegment(sketch, "E6341", {"start": v(7.46, -2.67) * mm, "end": v(7.46, -2.68) * mm});
            skLineSegment(sketch, "E6342", {"start": v(7.46, -2.68) * mm, "end": v(7.46, -2.68) * mm});
            skLineSegment(sketch, "E6343", {"start": v(7.46, -2.68) * mm, "end": v(7.46, -2.69) * mm});
            skLineSegment(sketch, "E6344", {"start": v(7.46, -2.69) * mm, "end": v(7.46, -2.7) * mm});
            skLineSegment(sketch, "E6345", {"start": v(7.46, -2.7) * mm, "end": v(7.45, -2.7) * mm});
            skLineSegment(sketch, "E6346", {"start": v(7.45, -2.7) * mm, "end": v(7.45, -2.7) * mm});
            skLineSegment(sketch, "E6347", {"start": v(7.45, -2.7) * mm, "end": v(7.44, -2.7) * mm});
            skLineSegment(sketch, "E6348", {"start": v(7.44, -2.7) * mm, "end": v(7.44, -2.71) * mm});
            skLineSegment(sketch, "E6349", {"start": v(7.44, -2.71) * mm, "end": v(7.44, -2.72) * mm});
            skLineSegment(sketch, "E6350", {"start": v(7.44, -2.72) * mm, "end": v(7.43, -2.72) * mm});
            skLineSegment(sketch, "E6351", {"start": v(7.43, -2.72) * mm, "end": v(7.43, -2.72) * mm});
            skLineSegment(sketch, "E6352", {"start": v(7.43, -2.72) * mm, "end": v(7.43, -2.73) * mm});
            skLineSegment(sketch, "E6353", {"start": v(7.43, -2.73) * mm, "end": v(7.42, -2.73) * mm});
            skLineSegment(sketch, "E6354", {"start": v(7.42, -2.73) * mm, "end": v(7.42, -2.73) * mm});
            skLineSegment(sketch, "E6355", {"start": v(7.42, -2.73) * mm, "end": v(7.41, -2.74) * mm});
            skLineSegment(sketch, "E6356", {"start": v(7.41, -2.74) * mm, "end": v(7.4, -2.74) * mm});
            skLineSegment(sketch, "E6357", {"start": v(7.4, -2.74) * mm, "end": v(7.4, -2.74) * mm});
            skLineSegment(sketch, "E6358", {"start": v(7.4, -2.74) * mm, "end": v(7.4, -2.75) * mm});
            skLineSegment(sketch, "E6359", {"start": v(7.4, -2.75) * mm, "end": v(7.4, -2.75) * mm});
            skLineSegment(sketch, "E6360", {"start": v(7.4, -2.75) * mm, "end": v(7.39, -2.75) * mm});
            skLineSegment(sketch, "E6361", {"start": v(7.39, -2.75) * mm, "end": v(7.38, -2.75) * mm});
            skLineSegment(sketch, "E6362", {"start": v(7.38, -2.75) * mm, "end": v(7.38, -2.76) * mm});
            skLineSegment(sketch, "E6363", {"start": v(7.38, -2.76) * mm, "end": v(7.37, -2.76) * mm});
            skLineSegment(sketch, "E6364", {"start": v(7.37, -2.76) * mm, "end": v(7.37, -2.76) * mm});
            skLineSegment(sketch, "E6365", {"start": v(7.37, -2.76) * mm, "end": v(7.36, -2.76) * mm});
            skLineSegment(sketch, "E6366", {"start": v(7.36, -2.76) * mm, "end": v(7.36, -2.76) * mm});
            skLineSegment(sketch, "E6367", {"start": v(7.36, -2.76) * mm, "end": v(7.35, -2.76) * mm});
            skLineSegment(sketch, "E6368", {"start": v(7.35, -2.76) * mm, "end": v(7.35, -2.77) * mm});
            skLineSegment(sketch, "E6369", {"start": v(7.35, -2.77) * mm, "end": v(7.34, -2.77) * mm});
            skLineSegment(sketch, "E6370", {"start": v(7.34, -2.77) * mm, "end": v(7.34, -2.77) * mm});
            skLineSegment(sketch, "E6371", {"start": v(7.34, -2.77) * mm, "end": v(7.33, -2.77) * mm});
            skLineSegment(sketch, "E6372", {"start": v(7.33, -2.77) * mm, "end": v(7.33, -2.77) * mm});
            skLineSegment(sketch, "E6373", {"start": v(7.33, -2.77) * mm, "end": v(7.32, -2.77) * mm});
            skLineSegment(sketch, "E6374", {"start": v(7.32, -2.77) * mm, "end": v(7.32, -2.77) * mm});
            skLineSegment(sketch, "E6375", {"start": v(7.32, -2.77) * mm, "end": v(7.3, -2.77) * mm});
            skLineSegment(sketch, "E6376", {"start": v(7.3, -2.77) * mm, "end": v(7.3, -2.77) * mm});
            skLineSegment(sketch, "E6377", {"start": v(7.3, -2.77) * mm, "end": v(7.28, -2.77) * mm});
            skLineSegment(sketch, "E6378", {"start": v(7.28, -2.77) * mm, "end": v(7.25, -2.77) * mm});
            skLineSegment(sketch, "E6379", {"start": v(7.25, -2.77) * mm, "end": v(7.22, -2.77) * mm});
            skLineSegment(sketch, "E6380", {"start": v(7.22, -2.77) * mm, "end": v(7.18, -2.77) * mm});
            skLineSegment(sketch, "E6381", {"start": v(7.18, -2.77) * mm, "end": v(7.13, -2.77) * mm});
            skLineSegment(sketch, "E6382", {"start": v(7.13, -2.77) * mm, "end": v(7.08, -2.77) * mm});
            skLineSegment(sketch, "E6383", {"start": v(7.08, -2.77) * mm, "end": v(7.03, -2.77) * mm});
            skLineSegment(sketch, "E6384", {"start": v(7.03, -2.77) * mm, "end": v(6.97, -2.77) * mm});
            skLineSegment(sketch, "E6385", {"start": v(6.97, -2.77) * mm, "end": v(6.9, -2.77) * mm});
            skLineSegment(sketch, "E6386", {"start": v(6.9, -2.77) * mm, "end": v(6.83, -2.77) * mm});
            skLineSegment(sketch, "E6387", {"start": v(6.83, -2.77) * mm, "end": v(6.76, -2.77) * mm});
            skLineSegment(sketch, "E6388", {"start": v(6.76, -2.77) * mm, "end": v(6.68, -2.77) * mm});
            skLineSegment(sketch, "E6389", {"start": v(6.68, -2.77) * mm, "end": v(6.6, -2.77) * mm});
            skLineSegment(sketch, "E6390", {"start": v(6.6, -2.77) * mm, "end": v(6.51, -2.77) * mm});
            skLineSegment(sketch, "E6391", {"start": v(6.51, -2.77) * mm, "end": v(6.43, -2.77) * mm});
            skLineSegment(sketch, "E6392", {"start": v(6.43, -2.77) * mm, "end": v(6.34, -2.77) * mm});
            skLineSegment(sketch, "E6393", {"start": v(6.34, -2.77) * mm, "end": v(6.24, -2.77) * mm});
            skLineSegment(sketch, "E6394", {"start": v(6.24, -2.77) * mm, "end": v(6.15, -2.77) * mm});
            skLineSegment(sketch, "E6395", {"start": v(6.15, -2.77) * mm, "end": v(6.05, -2.77) * mm});
            skLineSegment(sketch, "E6396", {"start": v(6.05, -2.77) * mm, "end": v(5.96, -2.77) * mm});
            skLineSegment(sketch, "E6397", {"start": v(5.96, -2.77) * mm, "end": v(5.86, -2.77) * mm});
            skLineSegment(sketch, "E6398", {"start": v(5.86, -2.77) * mm, "end": v(5.76, -2.77) * mm});
            skLineSegment(sketch, "E6399", {"start": v(5.76, -2.77) * mm, "end": v(5.66, -2.77) * mm});
            skLineSegment(sketch, "E6400", {"start": v(5.66, -2.77) * mm, "end": v(5.56, -2.77) * mm});
            skLineSegment(sketch, "E6401", {"start": v(5.56, -2.77) * mm, "end": v(5.46, -2.77) * mm});
            skLineSegment(sketch, "E6402", {"start": v(5.46, -2.77) * mm, "end": v(5.37, -2.77) * mm});
            skLineSegment(sketch, "E6403", {"start": v(5.37, -2.77) * mm, "end": v(5.27, -2.77) * mm});
            skLineSegment(sketch, "E6404", {"start": v(5.27, -2.77) * mm, "end": v(5.17, -2.77) * mm});
            skLineSegment(sketch, "E6405", {"start": v(5.17, -2.77) * mm, "end": v(5.08, -2.77) * mm});
            skLineSegment(sketch, "E6406", {"start": v(5.08, -2.77) * mm, "end": v(4.99, -2.77) * mm});
            skLineSegment(sketch, "E6407", {"start": v(4.99, -2.77) * mm, "end": v(4.9, -2.77) * mm});
            skLineSegment(sketch, "E6408", {"start": v(4.9, -2.77) * mm, "end": v(4.8, -2.77) * mm});
            skLineSegment(sketch, "E6409", {"start": v(4.8, -2.77) * mm, "end": v(4.72, -2.77) * mm});
            skLineSegment(sketch, "E6410", {"start": v(4.72, -2.77) * mm, "end": v(4.64, -2.77) * mm});
            skLineSegment(sketch, "E6411", {"start": v(4.64, -2.77) * mm, "end": v(4.56, -2.77) * mm});
            skLineSegment(sketch, "E6412", {"start": v(4.56, -2.77) * mm, "end": v(4.5, -2.77) * mm});
            skLineSegment(sketch, "E6413", {"start": v(4.5, -2.77) * mm, "end": v(4.42, -2.77) * mm});
            skLineSegment(sketch, "E6414", {"start": v(4.42, -2.77) * mm, "end": v(4.35, -2.77) * mm});
            skLineSegment(sketch, "E6415", {"start": v(4.35, -2.77) * mm, "end": v(4.3, -2.77) * mm});
            skLineSegment(sketch, "E6416", {"start": v(4.3, -2.77) * mm, "end": v(4.24, -2.77) * mm});
            skLineSegment(sketch, "E6417", {"start": v(4.24, -2.77) * mm, "end": v(4.19, -2.77) * mm});
            skLineSegment(sketch, "E6418", {"start": v(4.19, -2.77) * mm, "end": v(4.14, -2.77) * mm});
            skLineSegment(sketch, "E6419", {"start": v(4.14, -2.77) * mm, "end": v(4.1, -2.77) * mm});
            skLineSegment(sketch, "E6420", {"start": v(4.1, -2.77) * mm, "end": v(4.07, -2.77) * mm});
            skLineSegment(sketch, "E6421", {"start": v(4.07, -2.77) * mm, "end": v(4.05, -2.77) * mm});
            skLineSegment(sketch, "E6422", {"start": v(4.05, -2.77) * mm, "end": v(4.03, -2.77) * mm});
            skLineSegment(sketch, "E6423", {"start": v(4.03, -2.77) * mm, "end": v(4.02, -2.77) * mm});
            skLineSegment(sketch, "E6424", {"start": v(4.02, -2.77) * mm, "end": v(4.01, -2.77) * mm});
            skSolve(sketch);
        }
        {
            var Q0;
            Q0 = qSketchRegion(id + "F0", true);
            extrude(context, id + "F1", {"entities" : qUnion([Q0]), "depth" : 2 * mm, "offsetDistance" : 25 * mm});
        }
        {
            var Q0;
            Q0=makeQuery(id+"F1.opExtrude","SWEPT_BODY",BODY,{"disambiguationData":[OSD([sQuery(id+"F0.wireOp",EDGE,"E0"),sQuery(id+"F0.wireOp",EDGE,"E1"),sQuery(id+"F0.wireOp",EDGE,"E2"),sQuery(id+"F0.wireOp",EDGE,"E3"),sQuery(id+"F0.wireOp",EDGE,"E4"),sQuery(id+"F0.wireOp",EDGE,"E5"),sQuery(id+"F0.wireOp",EDGE,"E6"),sQuery(id+"F0.wireOp",EDGE,"E7"),sQuery(id+"F0.wireOp",EDGE,"E8"),sQuery(id+"F0.wireOp",EDGE,"E9"),sQuery(id+"F0.wireOp",EDGE,"E10"),sQuery(id+"F0.wireOp",EDGE,"E11"),sQuery(id+"F0.wireOp",EDGE,"E12"),sQuery(id+"F0.wireOp",EDGE,"E13"),sQuery(id+"F0.wireOp",EDGE,"E14"),sQuery(id+"F0.wireOp",EDGE,"E15"),sQuery(id+"F0.wireOp",EDGE,"E16"),sQuery(id+"F0.wireOp",EDGE,"E17"),sQuery(id+"F0.wireOp",EDGE,"E18"),sQuery(id+"F0.wireOp",EDGE,"E19"),sQuery(id+"F0.wireOp",EDGE,"E20"),sQuery(id+"F0.wireOp",EDGE,"E21"),sQuery(id+"F0.wireOp",EDGE,"E22"),sQuery(id+"F0.wireOp",EDGE,"E23"),sQuery(id+"F0.wireOp",EDGE,"E24"),sQuery(id+"F0.wireOp",EDGE,"E25"),sQuery(id+"F0.wireOp",EDGE,"E26"),sQuery(id+"F0.wireOp",EDGE,"E27"),sQuery(id+"F0.wireOp",EDGE,"E28"),sQuery(id+"F0.wireOp",EDGE,"E29"),sQuery(id+"F0.wireOp",EDGE,"E30"),sQuery(id+"F0.wireOp",EDGE,"E31"),sQuery(id+"F0.wireOp",EDGE,"E32"),sQuery(id+"F0.wireOp",EDGE,"E33"),sQuery(id+"F0.wireOp",EDGE,"E34"),sQuery(id+"F0.wireOp",EDGE,"E35"),sQuery(id+"F0.wireOp",EDGE,"E36"),sQuery(id+"F0.wireOp",EDGE,"E37"),sQuery(id+"F0.wireOp",EDGE,"E38"),sQuery(id+"F0.wireOp",EDGE,"E39"),sQuery(id+"F0.wireOp",EDGE,"E40"),sQuery(id+"F0.wireOp",EDGE,"E41"),sQuery(id+"F0.wireOp",EDGE,"E42"),sQuery(id+"F0.wireOp",EDGE,"E43"),sQuery(id+"F0.wireOp",EDGE,"E44"),sQuery(id+"F0.wireOp",EDGE,"E45"),sQuery(id+"F0.wireOp",EDGE,"E46"),sQuery(id+"F0.wireOp",EDGE,"E47"),sQuery(id+"F0.wireOp",EDGE,"E48"),sQuery(id+"F0.wireOp",EDGE,"E49"),sQuery(id+"F0.wireOp",EDGE,"E50"),sQuery(id+"F0.wireOp",EDGE,"E50"),sQuery(id+"F0.wireOp",EDGE,"E51"),sQuery(id+"F0.wireOp",EDGE,"E52"),sQuery(id+"F0.wireOp",EDGE,"E53"),sQuery(id+"F0.wireOp",EDGE,"E54"),sQuery(id+"F0.wireOp",EDGE,"E54"),sQuery(id+"F0.wireOp",EDGE,"E54"),sQuery(id+"F0.wireOp",EDGE,"E55"),sQuery(id+"F0.wireOp",EDGE,"E56"),sQuery(id+"F0.wireOp",EDGE,"E56"),sQuery(id+"F0.wireOp",EDGE,"E56"),sQuery(id+"F0.wireOp",EDGE,"E56"),sQuery(id+"F0.wireOp",EDGE,"E57"),sQuery(id+"F0.wireOp",EDGE,"E58"),sQuery(id+"F0.wireOp",EDGE,"E58"),sQuery(id+"F0.wireOp",EDGE,"E58"),sQuery(id+"F0.wireOp",EDGE,"E59"),sQuery(id+"F0.wireOp",EDGE,"E60"),sQuery(id+"F0.wireOp",EDGE,"E60"),sQuery(id+"F0.wireOp",EDGE,"E60"),sQuery(id+"F0.wireOp",EDGE,"E60"),sQuery(id+"F0.wireOp",EDGE,"E61"),sQuery(id+"F0.wireOp",EDGE,"E62"),sQuery(id+"F0.wireOp",EDGE,"E62"),sQuery(id+"F0.wireOp",EDGE,"E62"),sQuery(id+"F0.wireOp",EDGE,"E63"),sQuery(id+"F0.wireOp",EDGE,"E64"),sQuery(id+"F0.wireOp",EDGE,"E64"),sQuery(id+"F0.wireOp",EDGE,"E64"),sQuery(id+"F0.wireOp",EDGE,"E64"),sQuery(id+"F0.wireOp",EDGE,"E65"),sQuery(id+"F0.wireOp",EDGE,"E66"),sQuery(id+"F0.wireOp",EDGE,"E66"),sQuery(id+"F0.wireOp",EDGE,"E66"),sQuery(id+"F0.wireOp",EDGE,"E66"),sQuery(id+"F0.wireOp",EDGE,"E67"),sQuery(id+"F0.wireOp",EDGE,"E68"),sQuery(id+"F0.wireOp",EDGE,"E69"),sQuery(id+"F0.wireOp",EDGE,"E70"),sQuery(id+"F0.wireOp",EDGE,"E70"),sQuery(id+"F0.wireOp",EDGE,"E70"),sQuery(id+"F0.wireOp",EDGE,"E70"),sQuery(id+"F0.wireOp",EDGE,"E70"),sQuery(id+"F0.wireOp",EDGE,"E70"),sQuery(id+"F0.wireOp",EDGE,"E70"),sQuery(id+"F0.wireOp",EDGE,"E71"),sQuery(id+"F0.wireOp",EDGE,"E72"),sQuery(id+"F0.wireOp",EDGE,"E73"),sQuery(id+"F0.wireOp",EDGE,"E74"),sQuery(id+"F0.wireOp",EDGE,"E74"),sQuery(id+"F0.wireOp",EDGE,"E75"),sQuery(id+"F0.wireOp",EDGE,"E76"),sQuery(id+"F0.wireOp",EDGE,"E77"),sQuery(id+"F0.wireOp",EDGE,"E78"),sQuery(id+"F0.wireOp",EDGE,"E78"),sQuery(id+"F0.wireOp",EDGE,"E79"),sQuery(id+"F0.wireOp",EDGE,"E80"),sQuery(id+"F0.wireOp",EDGE,"E81"),sQuery(id+"F0.wireOp",EDGE,"E82"),sQuery(id+"F0.wireOp",EDGE,"E82"),sQuery(id+"F0.wireOp",EDGE,"E83"),sQuery(id+"F0.wireOp",EDGE,"E84"),sQuery(id+"F0.wireOp",EDGE,"E85"),sQuery(id+"F0.wireOp",EDGE,"E86"),sQuery(id+"F0.wireOp",EDGE,"E87"),sQuery(id+"F0.wireOp",EDGE,"E88"),sQuery(id+"F0.wireOp",EDGE,"E89"),sQuery(id+"F0.wireOp",EDGE,"E90"),sQuery(id+"F0.wireOp",EDGE,"E91"),sQuery(id+"F0.wireOp",EDGE,"E92"),sQuery(id+"F0.wireOp",EDGE,"E92"),sQuery(id+"F0.wireOp",EDGE,"E93"),sQuery(id+"F0.wireOp",EDGE,"E94"),sQuery(id+"F0.wireOp",EDGE,"E94"),sQuery(id+"F0.wireOp",EDGE,"E95"),sQuery(id+"F0.wireOp",EDGE,"E96"),sQuery(id+"F0.wireOp",EDGE,"E97"),sQuery(id+"F0.wireOp",EDGE,"E98"),sQuery(id+"F0.wireOp",EDGE,"E99"),sQuery(id+"F0.wireOp",EDGE,"E100"),sQuery(id+"F0.wireOp",EDGE,"E101"),sQuery(id+"F0.wireOp",EDGE,"E101"),sQuery(id+"F0.wireOp",EDGE,"E102"),sQuery(id+"F0.wireOp",EDGE,"E103"),sQuery(id+"F0.wireOp",EDGE,"E104"),sQuery(id+"F0.wireOp",EDGE,"E105"),sQuery(id+"F0.wireOp",EDGE,"E106"),sQuery(id+"F0.wireOp",EDGE,"E107"),sQuery(id+"F0.wireOp",EDGE,"E107"),sQuery(id+"F0.wireOp",EDGE,"E107"),sQuery(id+"F0.wireOp",EDGE,"E107"),sQuery(id+"F0.wireOp",EDGE,"E108"),sQuery(id+"F0.wireOp",EDGE,"E109"),sQuery(id+"F0.wireOp",EDGE,"E110"),sQuery(id+"F0.wireOp",EDGE,"E111"),sQuery(id+"F0.wireOp",EDGE,"E111"),sQuery(id+"F0.wireOp",EDGE,"E112"),sQuery(id+"F0.wireOp",EDGE,"E113"),sQuery(id+"F0.wireOp",EDGE,"E113"),sQuery(id+"F0.wireOp",EDGE,"E114"),sQuery(id+"F0.wireOp",EDGE,"E115"),sQuery(id+"F0.wireOp",EDGE,"E116"),sQuery(id+"F0.wireOp",EDGE,"E117"),sQuery(id+"F0.wireOp",EDGE,"E117"),sQuery(id+"F0.wireOp",EDGE,"E118"),sQuery(id+"F0.wireOp",EDGE,"E119"),sQuery(id+"F0.wireOp",EDGE,"E120"),sQuery(id+"F0.wireOp",EDGE,"E121"),sQuery(id+"F0.wireOp",EDGE,"E122"),sQuery(id+"F0.wireOp",EDGE,"E123"),sQuery(id+"F0.wireOp",EDGE,"E123"),sQuery(id+"F0.wireOp",EDGE,"E124"),sQuery(id+"F0.wireOp",EDGE,"E125"),sQuery(id+"F0.wireOp",EDGE,"E126"),sQuery(id+"F0.wireOp",EDGE,"E127"),sQuery(id+"F0.wireOp",EDGE,"E127"),sQuery(id+"F0.wireOp",EDGE,"E128"),sQuery(id+"F0.wireOp",EDGE,"E129"),sQuery(id+"F0.wireOp",EDGE,"E130"),sQuery(id+"F0.wireOp",EDGE,"E131"),sQuery(id+"F0.wireOp",EDGE,"E132"),sQuery(id+"F0.wireOp",EDGE,"E133"),sQuery(id+"F0.wireOp",EDGE,"E134"),sQuery(id+"F0.wireOp",EDGE,"E135"),sQuery(id+"F0.wireOp",EDGE,"E136"),sQuery(id+"F0.wireOp",EDGE,"E137"),sQuery(id+"F0.wireOp",EDGE,"E138"),sQuery(id+"F0.wireOp",EDGE,"E139"),sQuery(id+"F0.wireOp",EDGE,"E140"),sQuery(id+"F0.wireOp",EDGE,"E141"),sQuery(id+"F0.wireOp",EDGE,"E142"),sQuery(id+"F0.wireOp",EDGE,"E143"),sQuery(id+"F0.wireOp",EDGE,"E144"),sQuery(id+"F0.wireOp",EDGE,"E145"),sQuery(id+"F0.wireOp",EDGE,"E146"),sQuery(id+"F0.wireOp",EDGE,"E147"),sQuery(id+"F0.wireOp",EDGE,"E148"),sQuery(id+"F0.wireOp",EDGE,"E149"),sQuery(id+"F0.wireOp",EDGE,"E150"),sQuery(id+"F0.wireOp",EDGE,"E151"),sQuery(id+"F0.wireOp",EDGE,"E152"),sQuery(id+"F0.wireOp",EDGE,"E153"),sQuery(id+"F0.wireOp",EDGE,"E154"),sQuery(id+"F0.wireOp",EDGE,"E155"),sQuery(id+"F0.wireOp",EDGE,"E156"),sQuery(id+"F0.wireOp",EDGE,"E157"),sQuery(id+"F0.wireOp",EDGE,"E158"),sQuery(id+"F0.wireOp",EDGE,"E159"),sQuery(id+"F0.wireOp",EDGE,"E160"),sQuery(id+"F0.wireOp",EDGE,"E161"),sQuery(id+"F0.wireOp",EDGE,"E162"),sQuery(id+"F0.wireOp",EDGE,"E163"),sQuery(id+"F0.wireOp",EDGE,"E164"),sQuery(id+"F0.wireOp",EDGE,"E165"),sQuery(id+"F0.wireOp",EDGE,"E166"),sQuery(id+"F0.wireOp",EDGE,"E167"),sQuery(id+"F0.wireOp",EDGE,"E168"),sQuery(id+"F0.wireOp",EDGE,"E169"),sQuery(id+"F0.wireOp",EDGE,"E170"),sQuery(id+"F0.wireOp",EDGE,"E171"),sQuery(id+"F0.wireOp",EDGE,"E172"),sQuery(id+"F0.wireOp",EDGE,"E173"),sQuery(id+"F0.wireOp",EDGE,"E174"),sQuery(id+"F0.wireOp",EDGE,"E175"),sQuery(id+"F0.wireOp",EDGE,"E176"),sQuery(id+"F0.wireOp",EDGE,"E177"),sQuery(id+"F0.wireOp",EDGE,"E178"),sQuery(id+"F0.wireOp",EDGE,"E179"),sQuery(id+"F0.wireOp",EDGE,"E180"),sQuery(id+"F0.wireOp",EDGE,"E181"),sQuery(id+"F0.wireOp",EDGE,"E182"),sQuery(id+"F0.wireOp",EDGE,"E183"),sQuery(id+"F0.wireOp",EDGE,"E184"),sQuery(id+"F0.wireOp",EDGE,"E185"),sQuery(id+"F0.wireOp",EDGE,"E186"),sQuery(id+"F0.wireOp",EDGE,"E187"),sQuery(id+"F0.wireOp",EDGE,"E188"),sQuery(id+"F0.wireOp",EDGE,"E189"),sQuery(id+"F0.wireOp",EDGE,"E190"),sQuery(id+"F0.wireOp",EDGE,"E191"),sQuery(id+"F0.wireOp",EDGE,"E192"),sQuery(id+"F0.wireOp",EDGE,"E193"),sQuery(id+"F0.wireOp",EDGE,"E194"),sQuery(id+"F0.wireOp",EDGE,"E195"),sQuery(id+"F0.wireOp",EDGE,"E196"),sQuery(id+"F0.wireOp",EDGE,"E197"),sQuery(id+"F0.wireOp",EDGE,"E198"),sQuery(id+"F0.wireOp",EDGE,"E199"),sQuery(id+"F0.wireOp",EDGE,"E200"),sQuery(id+"F0.wireOp",EDGE,"E201"),sQuery(id+"F0.wireOp",EDGE,"E202"),sQuery(id+"F0.wireOp",EDGE,"E203"),sQuery(id+"F0.wireOp",EDGE,"E204"),sQuery(id+"F0.wireOp",EDGE,"E205"),sQuery(id+"F0.wireOp",EDGE,"E206"),sQuery(id+"F0.wireOp",EDGE,"E207"),sQuery(id+"F0.wireOp",EDGE,"E208"),sQuery(id+"F0.wireOp",EDGE,"E209"),sQuery(id+"F0.wireOp",EDGE,"E210"),sQuery(id+"F0.wireOp",EDGE,"E211"),sQuery(id+"F0.wireOp",EDGE,"E211"),sQuery(id+"F0.wireOp",EDGE,"E211"),sQuery(id+"F0.wireOp",EDGE,"E211"),sQuery(id+"F0.wireOp",EDGE,"E212"),sQuery(id+"F0.wireOp",EDGE,"E213"),sQuery(id+"F0.wireOp",EDGE,"E214"),sQuery(id+"F0.wireOp",EDGE,"E215"),sQuery(id+"F0.wireOp",EDGE,"E216"),sQuery(id+"F0.wireOp",EDGE,"E217"),sQuery(id+"F0.wireOp",EDGE,"E218"),sQuery(id+"F0.wireOp",EDGE,"E219"),sQuery(id+"F0.wireOp",EDGE,"E220"),sQuery(id+"F0.wireOp",EDGE,"E221"),sQuery(id+"F0.wireOp",EDGE,"E222"),sQuery(id+"F0.wireOp",EDGE,"E223"),sQuery(id+"F0.wireOp",EDGE,"E224"),sQuery(id+"F0.wireOp",EDGE,"E225"),sQuery(id+"F0.wireOp",EDGE,"E226"),sQuery(id+"F0.wireOp",EDGE,"E227"),sQuery(id+"F0.wireOp",EDGE,"E228"),sQuery(id+"F0.wireOp",EDGE,"E229"),sQuery(id+"F0.wireOp",EDGE,"E230"),sQuery(id+"F0.wireOp",EDGE,"E231"),sQuery(id+"F0.wireOp",EDGE,"E232"),sQuery(id+"F0.wireOp",EDGE,"E233"),sQuery(id+"F0.wireOp",EDGE,"E234"),sQuery(id+"F0.wireOp",EDGE,"E235"),sQuery(id+"F0.wireOp",EDGE,"E236"),sQuery(id+"F0.wireOp",EDGE,"E237"),sQuery(id+"F0.wireOp",EDGE,"E238"),sQuery(id+"F0.wireOp",EDGE,"E239"),sQuery(id+"F0.wireOp",EDGE,"E240"),sQuery(id+"F0.wireOp",EDGE,"E241"),sQuery(id+"F0.wireOp",EDGE,"E242"),sQuery(id+"F0.wireOp",EDGE,"E243"),sQuery(id+"F0.wireOp",EDGE,"E244"),sQuery(id+"F0.wireOp",EDGE,"E245"),sQuery(id+"F0.wireOp",EDGE,"E246"),sQuery(id+"F0.wireOp",EDGE,"E247"),sQuery(id+"F0.wireOp",EDGE,"E248"),sQuery(id+"F0.wireOp",EDGE,"E249"),sQuery(id+"F0.wireOp",EDGE,"E250"),sQuery(id+"F0.wireOp",EDGE,"E251"),sQuery(id+"F0.wireOp",EDGE,"E252"),sQuery(id+"F0.wireOp",EDGE,"E253"),sQuery(id+"F0.wireOp",EDGE,"E254"),sQuery(id+"F0.wireOp",EDGE,"E254"),sQuery(id+"F0.wireOp",EDGE,"E254"),sQuery(id+"F0.wireOp",EDGE,"E254"),sQuery(id+"F0.wireOp",EDGE,"E255"),sQuery(id+"F0.wireOp",EDGE,"E256"),sQuery(id+"F0.wireOp",EDGE,"E257"),sQuery(id+"F0.wireOp",EDGE,"E258"),sQuery(id+"F0.wireOp",EDGE,"E259"),sQuery(id+"F0.wireOp",EDGE,"E260"),sQuery(id+"F0.wireOp",EDGE,"E261"),sQuery(id+"F0.wireOp",EDGE,"E262"),sQuery(id+"F0.wireOp",EDGE,"E263"),sQuery(id+"F0.wireOp",EDGE,"E264"),sQuery(id+"F0.wireOp",EDGE,"E265"),sQuery(id+"F0.wireOp",EDGE,"E266"),sQuery(id+"F0.wireOp",EDGE,"E267"),sQuery(id+"F0.wireOp",EDGE,"E268"),sQuery(id+"F0.wireOp",EDGE,"E269"),sQuery(id+"F0.wireOp",EDGE,"E270"),sQuery(id+"F0.wireOp",EDGE,"E271"),sQuery(id+"F0.wireOp",EDGE,"E272"),sQuery(id+"F0.wireOp",EDGE,"E273"),sQuery(id+"F0.wireOp",EDGE,"E274"),sQuery(id+"F0.wireOp",EDGE,"E275"),sQuery(id+"F0.wireOp",EDGE,"E276"),sQuery(id+"F0.wireOp",EDGE,"E277"),sQuery(id+"F0.wireOp",EDGE,"E278"),sQuery(id+"F0.wireOp",EDGE,"E279"),sQuery(id+"F0.wireOp",EDGE,"E280"),sQuery(id+"F0.wireOp",EDGE,"E281"),sQuery(id+"F0.wireOp",EDGE,"E282"),sQuery(id+"F0.wireOp",EDGE,"E283"),sQuery(id+"F0.wireOp",EDGE,"E284"),sQuery(id+"F0.wireOp",EDGE,"E285"),sQuery(id+"F0.wireOp",EDGE,"E286"),sQuery(id+"F0.wireOp",EDGE,"E287"),sQuery(id+"F0.wireOp",EDGE,"E288"),sQuery(id+"F0.wireOp",EDGE,"E289"),sQuery(id+"F0.wireOp",EDGE,"E290"),sQuery(id+"F0.wireOp",EDGE,"E291"),sQuery(id+"F0.wireOp",EDGE,"E292"),sQuery(id+"F0.wireOp",EDGE,"E293"),sQuery(id+"F0.wireOp",EDGE,"E294"),sQuery(id+"F0.wireOp",EDGE,"E295"),sQuery(id+"F0.wireOp",EDGE,"E296"),sQuery(id+"F0.wireOp",EDGE,"E297"),sQuery(id+"F0.wireOp",EDGE,"E298"),sQuery(id+"F0.wireOp",EDGE,"E299"),sQuery(id+"F0.wireOp",EDGE,"E300"),sQuery(id+"F0.wireOp",EDGE,"E301"),sQuery(id+"F0.wireOp",EDGE,"E302"),sQuery(id+"F0.wireOp",EDGE,"E303"),sQuery(id+"F0.wireOp",EDGE,"E304"),sQuery(id+"F0.wireOp",EDGE,"E305"),sQuery(id+"F0.wireOp",EDGE,"E306"),sQuery(id+"F0.wireOp",EDGE,"E307"),sQuery(id+"F0.wireOp",EDGE,"E308"),sQuery(id+"F0.wireOp",EDGE,"E309"),sQuery(id+"F0.wireOp",EDGE,"E310"),sQuery(id+"F0.wireOp",EDGE,"E311"),sQuery(id+"F0.wireOp",EDGE,"E312"),sQuery(id+"F0.wireOp",EDGE,"E313"),sQuery(id+"F0.wireOp",EDGE,"E314"),sQuery(id+"F0.wireOp",EDGE,"E315"),sQuery(id+"F0.wireOp",EDGE,"E316"),sQuery(id+"F0.wireOp",EDGE,"E317"),sQuery(id+"F0.wireOp",EDGE,"E318"),sQuery(id+"F0.wireOp",EDGE,"E319"),sQuery(id+"F0.wireOp",EDGE,"E320"),sQuery(id+"F0.wireOp",EDGE,"E321"),sQuery(id+"F0.wireOp",EDGE,"E322"),sQuery(id+"F0.wireOp",EDGE,"E323"),sQuery(id+"F0.wireOp",EDGE,"E324"),sQuery(id+"F0.wireOp",EDGE,"E325"),sQuery(id+"F0.wireOp",EDGE,"E326"),sQuery(id+"F0.wireOp",EDGE,"E327"),sQuery(id+"F0.wireOp",EDGE,"E328"),sQuery(id+"F0.wireOp",EDGE,"E329"),sQuery(id+"F0.wireOp",EDGE,"E330"),sQuery(id+"F0.wireOp",EDGE,"E331"),sQuery(id+"F0.wireOp",EDGE,"E332"),sQuery(id+"F0.wireOp",EDGE,"E333"),sQuery(id+"F0.wireOp",EDGE,"E334"),sQuery(id+"F0.wireOp",EDGE,"E335"),sQuery(id+"F0.wireOp",EDGE,"E336"),sQuery(id+"F0.wireOp",EDGE,"E337"),sQuery(id+"F0.wireOp",EDGE,"E338"),sQuery(id+"F0.wireOp",EDGE,"E339"),sQuery(id+"F0.wireOp",EDGE,"E340"),sQuery(id+"F0.wireOp",EDGE,"E341"),sQuery(id+"F0.wireOp",EDGE,"E342"),sQuery(id+"F0.wireOp",EDGE,"E343"),sQuery(id+"F0.wireOp",EDGE,"E344"),sQuery(id+"F0.wireOp",EDGE,"E345"),sQuery(id+"F0.wireOp",EDGE,"E346"),sQuery(id+"F0.wireOp",EDGE,"E347"),sQuery(id+"F0.wireOp",EDGE,"E348"),sQuery(id+"F0.wireOp",EDGE,"E349"),sQuery(id+"F0.wireOp",EDGE,"E350"),sQuery(id+"F0.wireOp",EDGE,"E351"),sQuery(id+"F0.wireOp",EDGE,"E352"),sQuery(id+"F0.wireOp",EDGE,"E353"),sQuery(id+"F0.wireOp",EDGE,"E354"),sQuery(id+"F0.wireOp",EDGE,"E355"),sQuery(id+"F0.wireOp",EDGE,"E355"),sQuery(id+"F0.wireOp",EDGE,"E356"),sQuery(id+"F0.wireOp",EDGE,"E357"),sQuery(id+"F0.wireOp",EDGE,"E358"),sQuery(id+"F0.wireOp",EDGE,"E359"),sQuery(id+"F0.wireOp",EDGE,"E360"),sQuery(id+"F0.wireOp",EDGE,"E361"),sQuery(id+"F0.wireOp",EDGE,"E362"),sQuery(id+"F0.wireOp",EDGE,"E363"),sQuery(id+"F0.wireOp",EDGE,"E364"),sQuery(id+"F0.wireOp",EDGE,"E365"),sQuery(id+"F0.wireOp",EDGE,"E366"),sQuery(id+"F0.wireOp",EDGE,"E367"),sQuery(id+"F0.wireOp",EDGE,"E368"),sQuery(id+"F0.wireOp",EDGE,"E369"),sQuery(id+"F0.wireOp",EDGE,"E370"),sQuery(id+"F0.wireOp",EDGE,"E371"),sQuery(id+"F0.wireOp",EDGE,"E372"),sQuery(id+"F0.wireOp",EDGE,"E373"),sQuery(id+"F0.wireOp",EDGE,"E374"),sQuery(id+"F0.wireOp",EDGE,"E375"),sQuery(id+"F0.wireOp",EDGE,"E376"),sQuery(id+"F0.wireOp",EDGE,"E377"),sQuery(id+"F0.wireOp",EDGE,"E378"),sQuery(id+"F0.wireOp",EDGE,"E379"),sQuery(id+"F0.wireOp",EDGE,"E380"),sQuery(id+"F0.wireOp",EDGE,"E381"),sQuery(id+"F0.wireOp",EDGE,"E382"),sQuery(id+"F0.wireOp",EDGE,"E383"),sQuery(id+"F0.wireOp",EDGE,"E384"),sQuery(id+"F0.wireOp",EDGE,"E385"),sQuery(id+"F0.wireOp",EDGE,"E386"),sQuery(id+"F0.wireOp",EDGE,"E387"),sQuery(id+"F0.wireOp",EDGE,"E388"),sQuery(id+"F0.wireOp",EDGE,"E389"),sQuery(id+"F0.wireOp",EDGE,"E390"),sQuery(id+"F0.wireOp",EDGE,"E391"),sQuery(id+"F0.wireOp",EDGE,"E392"),sQuery(id+"F0.wireOp",EDGE,"E393"),sQuery(id+"F0.wireOp",EDGE,"E394"),sQuery(id+"F0.wireOp",EDGE,"E395"),sQuery(id+"F0.wireOp",EDGE,"E396"),sQuery(id+"F0.wireOp",EDGE,"E397"),sQuery(id+"F0.wireOp",EDGE,"E398"),sQuery(id+"F0.wireOp",EDGE,"E399"),sQuery(id+"F0.wireOp",EDGE,"E400"),sQuery(id+"F0.wireOp",EDGE,"E401"),sQuery(id+"F0.wireOp",EDGE,"E401"),sQuery(id+"F0.wireOp",EDGE,"E402"),sQuery(id+"F0.wireOp",EDGE,"E403"),sQuery(id+"F0.wireOp",EDGE,"E404"),sQuery(id+"F0.wireOp",EDGE,"E405"),sQuery(id+"F0.wireOp",EDGE,"E406"),sQuery(id+"F0.wireOp",EDGE,"E407"),sQuery(id+"F0.wireOp",EDGE,"E408"),sQuery(id+"F0.wireOp",EDGE,"E409"),sQuery(id+"F0.wireOp",EDGE,"E410"),sQuery(id+"F0.wireOp",EDGE,"E411"),sQuery(id+"F0.wireOp",EDGE,"E412"),sQuery(id+"F0.wireOp",EDGE,"E413"),sQuery(id+"F0.wireOp",EDGE,"E414"),sQuery(id+"F0.wireOp",EDGE,"E415"),sQuery(id+"F0.wireOp",EDGE,"E416"),sQuery(id+"F0.wireOp",EDGE,"E417"),sQuery(id+"F0.wireOp",EDGE,"E418"),sQuery(id+"F0.wireOp",EDGE,"E419"),sQuery(id+"F0.wireOp",EDGE,"E420"),sQuery(id+"F0.wireOp",EDGE,"E421"),sQuery(id+"F0.wireOp",EDGE,"E422"),sQuery(id+"F0.wireOp",EDGE,"E423"),sQuery(id+"F0.wireOp",EDGE,"E424"),sQuery(id+"F0.wireOp",EDGE,"E425"),sQuery(id+"F0.wireOp",EDGE,"E426"),sQuery(id+"F0.wireOp",EDGE,"E427"),sQuery(id+"F0.wireOp",EDGE,"E428"),sQuery(id+"F0.wireOp",EDGE,"E429"),sQuery(id+"F0.wireOp",EDGE,"E430"),sQuery(id+"F0.wireOp",EDGE,"E431"),sQuery(id+"F0.wireOp",EDGE,"E432"),sQuery(id+"F0.wireOp",EDGE,"E433"),sQuery(id+"F0.wireOp",EDGE,"E434"),sQuery(id+"F0.wireOp",EDGE,"E435"),sQuery(id+"F0.wireOp",EDGE,"E436"),sQuery(id+"F0.wireOp",EDGE,"E437"),sQuery(id+"F0.wireOp",EDGE,"E438"),sQuery(id+"F0.wireOp",EDGE,"E439"),sQuery(id+"F0.wireOp",EDGE,"E439"),sQuery(id+"F0.wireOp",EDGE,"E440"),sQuery(id+"F0.wireOp",EDGE,"E441"),sQuery(id+"F0.wireOp",EDGE,"E442"),sQuery(id+"F0.wireOp",EDGE,"E443"),sQuery(id+"F0.wireOp",EDGE,"E444"),sQuery(id+"F0.wireOp",EDGE,"E445"),sQuery(id+"F0.wireOp",EDGE,"E446"),sQuery(id+"F0.wireOp",EDGE,"E447"),sQuery(id+"F0.wireOp",EDGE,"E448"),sQuery(id+"F0.wireOp",EDGE,"E449"),sQuery(id+"F0.wireOp",EDGE,"E450"),sQuery(id+"F0.wireOp",EDGE,"E451"),sQuery(id+"F0.wireOp",EDGE,"E452"),sQuery(id+"F0.wireOp",EDGE,"E453"),sQuery(id+"F0.wireOp",EDGE,"E454"),sQuery(id+"F0.wireOp",EDGE,"E455"),sQuery(id+"F0.wireOp",EDGE,"E456"),sQuery(id+"F0.wireOp",EDGE,"E457"),sQuery(id+"F0.wireOp",EDGE,"E458"),sQuery(id+"F0.wireOp",EDGE,"E459"),sQuery(id+"F0.wireOp",EDGE,"E460"),sQuery(id+"F0.wireOp",EDGE,"E461"),sQuery(id+"F0.wireOp",EDGE,"E462"),sQuery(id+"F0.wireOp",EDGE,"E463"),sQuery(id+"F0.wireOp",EDGE,"E464"),sQuery(id+"F0.wireOp",EDGE,"E465"),sQuery(id+"F0.wireOp",EDGE,"E466"),sQuery(id+"F0.wireOp",EDGE,"E467"),sQuery(id+"F0.wireOp",EDGE,"E468"),sQuery(id+"F0.wireOp",EDGE,"E469"),sQuery(id+"F0.wireOp",EDGE,"E470"),sQuery(id+"F0.wireOp",EDGE,"E471"),sQuery(id+"F0.wireOp",EDGE,"E472"),sQuery(id+"F0.wireOp",EDGE,"E473"),sQuery(id+"F0.wireOp",EDGE,"E474"),sQuery(id+"F0.wireOp",EDGE,"E475"),sQuery(id+"F0.wireOp",EDGE,"E476"),sQuery(id+"F0.wireOp",EDGE,"E477"),sQuery(id+"F0.wireOp",EDGE,"E478"),sQuery(id+"F0.wireOp",EDGE,"E479"),sQuery(id+"F0.wireOp",EDGE,"E480"),sQuery(id+"F0.wireOp",EDGE,"E481"),sQuery(id+"F0.wireOp",EDGE,"E482"),sQuery(id+"F0.wireOp",EDGE,"E483"),sQuery(id+"F0.wireOp",EDGE,"E484"),sQuery(id+"F0.wireOp",EDGE,"E485"),sQuery(id+"F0.wireOp",EDGE,"E486"),sQuery(id+"F0.wireOp",EDGE,"E487"),sQuery(id+"F0.wireOp",EDGE,"E488"),sQuery(id+"F0.wireOp",EDGE,"E489"),sQuery(id+"F0.wireOp",EDGE,"E490"),sQuery(id+"F0.wireOp",EDGE,"E491"),sQuery(id+"F0.wireOp",EDGE,"E492"),sQuery(id+"F0.wireOp",EDGE,"E493"),sQuery(id+"F0.wireOp",EDGE,"E494"),sQuery(id+"F0.wireOp",EDGE,"E495"),sQuery(id+"F0.wireOp",EDGE,"E496"),sQuery(id+"F0.wireOp",EDGE,"E497"),sQuery(id+"F0.wireOp",EDGE,"E498"),sQuery(id+"F0.wireOp",EDGE,"E499"),sQuery(id+"F0.wireOp",EDGE,"E500"),sQuery(id+"F0.wireOp",EDGE,"E501"),sQuery(id+"F0.wireOp",EDGE,"E502"),sQuery(id+"F0.wireOp",EDGE,"E503"),sQuery(id+"F0.wireOp",EDGE,"E503"),sQuery(id+"F0.wireOp",EDGE,"E504"),sQuery(id+"F0.wireOp",EDGE,"E505"),sQuery(id+"F0.wireOp",EDGE,"E506"),sQuery(id+"F0.wireOp",EDGE,"E507"),sQuery(id+"F0.wireOp",EDGE,"E508"),sQuery(id+"F0.wireOp",EDGE,"E509"),sQuery(id+"F0.wireOp",EDGE,"E510"),sQuery(id+"F0.wireOp",EDGE,"E511"),sQuery(id+"F0.wireOp",EDGE,"E512"),sQuery(id+"F0.wireOp",EDGE,"E513"),sQuery(id+"F0.wireOp",EDGE,"E514"),sQuery(id+"F0.wireOp",EDGE,"E515"),sQuery(id+"F0.wireOp",EDGE,"E516"),sQuery(id+"F0.wireOp",EDGE,"E517"),sQuery(id+"F0.wireOp",EDGE,"E518"),sQuery(id+"F0.wireOp",EDGE,"E519"),sQuery(id+"F0.wireOp",EDGE,"E520"),sQuery(id+"F0.wireOp",EDGE,"E521"),sQuery(id+"F0.wireOp",EDGE,"E522"),sQuery(id+"F0.wireOp",EDGE,"E523"),sQuery(id+"F0.wireOp",EDGE,"E524"),sQuery(id+"F0.wireOp",EDGE,"E525"),sQuery(id+"F0.wireOp",EDGE,"E526"),sQuery(id+"F0.wireOp",EDGE,"E527"),sQuery(id+"F0.wireOp",EDGE,"E528"),sQuery(id+"F0.wireOp",EDGE,"E529"),sQuery(id+"F0.wireOp",EDGE,"E530"),sQuery(id+"F0.wireOp",EDGE,"E531"),sQuery(id+"F0.wireOp",EDGE,"E532"),sQuery(id+"F0.wireOp",EDGE,"E533"),sQuery(id+"F0.wireOp",EDGE,"E534"),sQuery(id+"F0.wireOp",EDGE,"E535"),sQuery(id+"F0.wireOp",EDGE,"E536"),sQuery(id+"F0.wireOp",EDGE,"E537"),sQuery(id+"F0.wireOp",EDGE,"E538"),sQuery(id+"F0.wireOp",EDGE,"E539"),sQuery(id+"F0.wireOp",EDGE,"E540"),sQuery(id+"F0.wireOp",EDGE,"E541"),sQuery(id+"F0.wireOp",EDGE,"E542"),sQuery(id+"F0.wireOp",EDGE,"E543"),sQuery(id+"F0.wireOp",EDGE,"E544"),sQuery(id+"F0.wireOp",EDGE,"E545"),sQuery(id+"F0.wireOp",EDGE,"E546"),sQuery(id+"F0.wireOp",EDGE,"E547"),sQuery(id+"F0.wireOp",EDGE,"E548"),sQuery(id+"F0.wireOp",EDGE,"E549"),sQuery(id+"F0.wireOp",EDGE,"E549"),sQuery(id+"F0.wireOp",EDGE,"E550"),sQuery(id+"F0.wireOp",EDGE,"E551"),sQuery(id+"F0.wireOp",EDGE,"E552"),sQuery(id+"F0.wireOp",EDGE,"E553"),sQuery(id+"F0.wireOp",EDGE,"E554"),sQuery(id+"F0.wireOp",EDGE,"E555"),sQuery(id+"F0.wireOp",EDGE,"E556"),sQuery(id+"F0.wireOp",EDGE,"E557"),sQuery(id+"F0.wireOp",EDGE,"E558"),sQuery(id+"F0.wireOp",EDGE,"E559"),sQuery(id+"F0.wireOp",EDGE,"E560"),sQuery(id+"F0.wireOp",EDGE,"E561"),sQuery(id+"F0.wireOp",EDGE,"E562"),sQuery(id+"F0.wireOp",EDGE,"E563"),sQuery(id+"F0.wireOp",EDGE,"E564"),sQuery(id+"F0.wireOp",EDGE,"E565"),sQuery(id+"F0.wireOp",EDGE,"E566"),sQuery(id+"F0.wireOp",EDGE,"E567"),sQuery(id+"F0.wireOp",EDGE,"E568"),sQuery(id+"F0.wireOp",EDGE,"E569"),sQuery(id+"F0.wireOp",EDGE,"E570"),sQuery(id+"F0.wireOp",EDGE,"E571"),sQuery(id+"F0.wireOp",EDGE,"E572"),sQuery(id+"F0.wireOp",EDGE,"E573"),sQuery(id+"F0.wireOp",EDGE,"E574"),sQuery(id+"F0.wireOp",EDGE,"E575"),sQuery(id+"F0.wireOp",EDGE,"E576"),sQuery(id+"F0.wireOp",EDGE,"E577"),sQuery(id+"F0.wireOp",EDGE,"E578"),sQuery(id+"F0.wireOp",EDGE,"E579"),sQuery(id+"F0.wireOp",EDGE,"E580"),sQuery(id+"F0.wireOp",EDGE,"E581"),sQuery(id+"F0.wireOp",EDGE,"E582"),sQuery(id+"F0.wireOp",EDGE,"E583"),sQuery(id+"F0.wireOp",EDGE,"E584"),sQuery(id+"F0.wireOp",EDGE,"E585"),sQuery(id+"F0.wireOp",EDGE,"E586"),sQuery(id+"F0.wireOp",EDGE,"E587"),sQuery(id+"F0.wireOp",EDGE,"E588"),sQuery(id+"F0.wireOp",EDGE,"E589"),sQuery(id+"F0.wireOp",EDGE,"E590"),sQuery(id+"F0.wireOp",EDGE,"E591"),sQuery(id+"F0.wireOp",EDGE,"E592"),sQuery(id+"F0.wireOp",EDGE,"E593"),sQuery(id+"F0.wireOp",EDGE,"E594"),sQuery(id+"F0.wireOp",EDGE,"E595"),sQuery(id+"F0.wireOp",EDGE,"E596"),sQuery(id+"F0.wireOp",EDGE,"E597"),sQuery(id+"F0.wireOp",EDGE,"E598"),sQuery(id+"F0.wireOp",EDGE,"E599"),sQuery(id+"F0.wireOp",EDGE,"E600"),sQuery(id+"F0.wireOp",EDGE,"E601"),sQuery(id+"F0.wireOp",EDGE,"E602"),sQuery(id+"F0.wireOp",EDGE,"E603"),sQuery(id+"F0.wireOp",EDGE,"E604"),sQuery(id+"F0.wireOp",EDGE,"E605"),sQuery(id+"F0.wireOp",EDGE,"E606"),sQuery(id+"F0.wireOp",EDGE,"E607"),sQuery(id+"F0.wireOp",EDGE,"E608"),sQuery(id+"F0.wireOp",EDGE,"E609"),sQuery(id+"F0.wireOp",EDGE,"E610"),sQuery(id+"F0.wireOp",EDGE,"E611"),sQuery(id+"F0.wireOp",EDGE,"E612"),sQuery(id+"F0.wireOp",EDGE,"E613"),sQuery(id+"F0.wireOp",EDGE,"E614"),sQuery(id+"F0.wireOp",EDGE,"E615"),sQuery(id+"F0.wireOp",EDGE,"E616"),sQuery(id+"F0.wireOp",EDGE,"E617"),sQuery(id+"F0.wireOp",EDGE,"E618"),sQuery(id+"F0.wireOp",EDGE,"E619"),sQuery(id+"F0.wireOp",EDGE,"E620"),sQuery(id+"F0.wireOp",EDGE,"E621"),sQuery(id+"F0.wireOp",EDGE,"E622"),sQuery(id+"F0.wireOp",EDGE,"E623"),sQuery(id+"F0.wireOp",EDGE,"E624"),sQuery(id+"F0.wireOp",EDGE,"E625"),sQuery(id+"F0.wireOp",EDGE,"E626"),sQuery(id+"F0.wireOp",EDGE,"E627"),sQuery(id+"F0.wireOp",EDGE,"E628"),sQuery(id+"F0.wireOp",EDGE,"E629"),sQuery(id+"F0.wireOp",EDGE,"E630"),sQuery(id+"F0.wireOp",EDGE,"E631"),sQuery(id+"F0.wireOp",EDGE,"E632"),sQuery(id+"F0.wireOp",EDGE,"E633"),sQuery(id+"F0.wireOp",EDGE,"E634"),sQuery(id+"F0.wireOp",EDGE,"E635"),sQuery(id+"F0.wireOp",EDGE,"E636"),sQuery(id+"F0.wireOp",EDGE,"E637"),sQuery(id+"F0.wireOp",EDGE,"E638"),sQuery(id+"F0.wireOp",EDGE,"E639"),sQuery(id+"F0.wireOp",EDGE,"E640"),sQuery(id+"F0.wireOp",EDGE,"E641"),sQuery(id+"F0.wireOp",EDGE,"E642"),sQuery(id+"F0.wireOp",EDGE,"E643"),sQuery(id+"F0.wireOp",EDGE,"E644"),sQuery(id+"F0.wireOp",EDGE,"E645"),sQuery(id+"F0.wireOp",EDGE,"E646"),sQuery(id+"F0.wireOp",EDGE,"E647"),sQuery(id+"F0.wireOp",EDGE,"E648"),sQuery(id+"F0.wireOp",EDGE,"E649"),sQuery(id+"F0.wireOp",EDGE,"E650"),sQuery(id+"F0.wireOp",EDGE,"E650"),sQuery(id+"F0.wireOp",EDGE,"E651"),sQuery(id+"F0.wireOp",EDGE,"E652"),sQuery(id+"F0.wireOp",EDGE,"E653"),sQuery(id+"F0.wireOp",EDGE,"E653"),sQuery(id+"F0.wireOp",EDGE,"E653"),sQuery(id+"F0.wireOp",EDGE,"E654"),sQuery(id+"F0.wireOp",EDGE,"E655"),sQuery(id+"F0.wireOp",EDGE,"E656"),sQuery(id+"F0.wireOp",EDGE,"E657"),sQuery(id+"F0.wireOp",EDGE,"E658"),sQuery(id+"F0.wireOp",EDGE,"E659"),sQuery(id+"F0.wireOp",EDGE,"E660"),sQuery(id+"F0.wireOp",EDGE,"E661"),sQuery(id+"F0.wireOp",EDGE,"E662"),sQuery(id+"F0.wireOp",EDGE,"E663"),sQuery(id+"F0.wireOp",EDGE,"E664"),sQuery(id+"F0.wireOp",EDGE,"E665"),sQuery(id+"F0.wireOp",EDGE,"E666"),sQuery(id+"F0.wireOp",EDGE,"E667"),sQuery(id+"F0.wireOp",EDGE,"E668"),sQuery(id+"F0.wireOp",EDGE,"E669"),sQuery(id+"F0.wireOp",EDGE,"E670"),sQuery(id+"F0.wireOp",EDGE,"E671"),sQuery(id+"F0.wireOp",EDGE,"E672"),sQuery(id+"F0.wireOp",EDGE,"E673"),sQuery(id+"F0.wireOp",EDGE,"E674"),sQuery(id+"F0.wireOp",EDGE,"E675"),sQuery(id+"F0.wireOp",EDGE,"E676"),sQuery(id+"F0.wireOp",EDGE,"E677"),sQuery(id+"F0.wireOp",EDGE,"E678"),sQuery(id+"F0.wireOp",EDGE,"E679"),sQuery(id+"F0.wireOp",EDGE,"E680"),sQuery(id+"F0.wireOp",EDGE,"E681"),sQuery(id+"F0.wireOp",EDGE,"E682"),sQuery(id+"F0.wireOp",EDGE,"E683"),sQuery(id+"F0.wireOp",EDGE,"E684"),sQuery(id+"F0.wireOp",EDGE,"E685"),sQuery(id+"F0.wireOp",EDGE,"E686"),sQuery(id+"F0.wireOp",EDGE,"E687"),sQuery(id+"F0.wireOp",EDGE,"E688"),sQuery(id+"F0.wireOp",EDGE,"E689"),sQuery(id+"F0.wireOp",EDGE,"E690"),sQuery(id+"F0.wireOp",EDGE,"E691"),sQuery(id+"F0.wireOp",EDGE,"E692"),sQuery(id+"F0.wireOp",EDGE,"E693"),sQuery(id+"F0.wireOp",EDGE,"E693"),sQuery(id+"F0.wireOp",EDGE,"E693"),sQuery(id+"F0.wireOp",EDGE,"E693"),sQuery(id+"F0.wireOp",EDGE,"E694"),sQuery(id+"F0.wireOp",EDGE,"E695"),sQuery(id+"F0.wireOp",EDGE,"E696"),sQuery(id+"F0.wireOp",EDGE,"E697"),sQuery(id+"F0.wireOp",EDGE,"E698"),sQuery(id+"F0.wireOp",EDGE,"E699"),sQuery(id+"F0.wireOp",EDGE,"E700"),sQuery(id+"F0.wireOp",EDGE,"E701"),sQuery(id+"F0.wireOp",EDGE,"E702"),sQuery(id+"F0.wireOp",EDGE,"E703"),sQuery(id+"F0.wireOp",EDGE,"E704"),sQuery(id+"F0.wireOp",EDGE,"E705"),sQuery(id+"F0.wireOp",EDGE,"E706"),sQuery(id+"F0.wireOp",EDGE,"E707"),sQuery(id+"F0.wireOp",EDGE,"E708"),sQuery(id+"F0.wireOp",EDGE,"E709"),sQuery(id+"F0.wireOp",EDGE,"E710"),sQuery(id+"F0.wireOp",EDGE,"E711"),sQuery(id+"F0.wireOp",EDGE,"E712"),sQuery(id+"F0.wireOp",EDGE,"E713"),sQuery(id+"F0.wireOp",EDGE,"E714"),sQuery(id+"F0.wireOp",EDGE,"E715"),sQuery(id+"F0.wireOp",EDGE,"E716"),sQuery(id+"F0.wireOp",EDGE,"E717"),sQuery(id+"F0.wireOp",EDGE,"E718"),sQuery(id+"F0.wireOp",EDGE,"E719"),sQuery(id+"F0.wireOp",EDGE,"E720"),sQuery(id+"F0.wireOp",EDGE,"E721"),sQuery(id+"F0.wireOp",EDGE,"E722"),sQuery(id+"F0.wireOp",EDGE,"E723"),sQuery(id+"F0.wireOp",EDGE,"E724"),sQuery(id+"F0.wireOp",EDGE,"E725"),sQuery(id+"F0.wireOp",EDGE,"E726"),sQuery(id+"F0.wireOp",EDGE,"E727"),sQuery(id+"F0.wireOp",EDGE,"E728"),sQuery(id+"F0.wireOp",EDGE,"E729"),sQuery(id+"F0.wireOp",EDGE,"E730"),sQuery(id+"F0.wireOp",EDGE,"E731"),sQuery(id+"F0.wireOp",EDGE,"E732"),sQuery(id+"F0.wireOp",EDGE,"E733"),sQuery(id+"F0.wireOp",EDGE,"E734"),sQuery(id+"F0.wireOp",EDGE,"E734"),sQuery(id+"F0.wireOp",EDGE,"E735"),sQuery(id+"F0.wireOp",EDGE,"E736"),sQuery(id+"F0.wireOp",EDGE,"E737"),sQuery(id+"F0.wireOp",EDGE,"E738"),sQuery(id+"F0.wireOp",EDGE,"E739"),sQuery(id+"F0.wireOp",EDGE,"E740"),sQuery(id+"F0.wireOp",EDGE,"E741"),sQuery(id+"F0.wireOp",EDGE,"E742"),sQuery(id+"F0.wireOp",EDGE,"E743"),sQuery(id+"F0.wireOp",EDGE,"E744"),sQuery(id+"F0.wireOp",EDGE,"E745"),sQuery(id+"F0.wireOp",EDGE,"E746"),sQuery(id+"F0.wireOp",EDGE,"E747"),sQuery(id+"F0.wireOp",EDGE,"E748"),sQuery(id+"F0.wireOp",EDGE,"E749"),sQuery(id+"F0.wireOp",EDGE,"E750"),sQuery(id+"F0.wireOp",EDGE,"E751"),sQuery(id+"F0.wireOp",EDGE,"E752"),sQuery(id+"F0.wireOp",EDGE,"E753"),sQuery(id+"F0.wireOp",EDGE,"E754"),sQuery(id+"F0.wireOp",EDGE,"E755"),sQuery(id+"F0.wireOp",EDGE,"E756"),sQuery(id+"F0.wireOp",EDGE,"E757"),sQuery(id+"F0.wireOp",EDGE,"E758"),sQuery(id+"F0.wireOp",EDGE,"E759"),sQuery(id+"F0.wireOp",EDGE,"E760"),sQuery(id+"F0.wireOp",EDGE,"E761"),sQuery(id+"F0.wireOp",EDGE,"E762"),sQuery(id+"F0.wireOp",EDGE,"E763"),sQuery(id+"F0.wireOp",EDGE,"E764"),sQuery(id+"F0.wireOp",EDGE,"E764"),sQuery(id+"F0.wireOp",EDGE,"E765"),sQuery(id+"F0.wireOp",EDGE,"E766"),sQuery(id+"F0.wireOp",EDGE,"E767"),sQuery(id+"F0.wireOp",EDGE,"E768"),sQuery(id+"F0.wireOp",EDGE,"E769"),sQuery(id+"F0.wireOp",EDGE,"E770"),sQuery(id+"F0.wireOp",EDGE,"E771"),sQuery(id+"F0.wireOp",EDGE,"E772"),sQuery(id+"F0.wireOp",EDGE,"E773"),sQuery(id+"F0.wireOp",EDGE,"E774"),sQuery(id+"F0.wireOp",EDGE,"E775"),sQuery(id+"F0.wireOp",EDGE,"E776"),sQuery(id+"F0.wireOp",EDGE,"E777"),sQuery(id+"F0.wireOp",EDGE,"E778"),sQuery(id+"F0.wireOp",EDGE,"E779"),sQuery(id+"F0.wireOp",EDGE,"E780"),sQuery(id+"F0.wireOp",EDGE,"E781"),sQuery(id+"F0.wireOp",EDGE,"E781"),sQuery(id+"F0.wireOp",EDGE,"E782"),sQuery(id+"F0.wireOp",EDGE,"E783"),sQuery(id+"F0.wireOp",EDGE,"E784"),sQuery(id+"F0.wireOp",EDGE,"E785"),sQuery(id+"F0.wireOp",EDGE,"E786"),sQuery(id+"F0.wireOp",EDGE,"E787"),sQuery(id+"F0.wireOp",EDGE,"E788"),sQuery(id+"F0.wireOp",EDGE,"E789"),sQuery(id+"F0.wireOp",EDGE,"E790"),sQuery(id+"F0.wireOp",EDGE,"E791"),sQuery(id+"F0.wireOp",EDGE,"E792"),sQuery(id+"F0.wireOp",EDGE,"E793"),sQuery(id+"F0.wireOp",EDGE,"E794"),sQuery(id+"F0.wireOp",EDGE,"E795"),sQuery(id+"F0.wireOp",EDGE,"E796"),sQuery(id+"F0.wireOp",EDGE,"E797"),sQuery(id+"F0.wireOp",EDGE,"E798"),sQuery(id+"F0.wireOp",EDGE,"E799"),sQuery(id+"F0.wireOp",EDGE,"E800"),sQuery(id+"F0.wireOp",EDGE,"E801"),sQuery(id+"F0.wireOp",EDGE,"E802"),sQuery(id+"F0.wireOp",EDGE,"E803"),sQuery(id+"F0.wireOp",EDGE,"E804"),sQuery(id+"F0.wireOp",EDGE,"E805"),sQuery(id+"F0.wireOp",EDGE,"E806"),sQuery(id+"F0.wireOp",EDGE,"E807"),sQuery(id+"F0.wireOp",EDGE,"E808"),sQuery(id+"F0.wireOp",EDGE,"E809"),sQuery(id+"F0.wireOp",EDGE,"E810"),sQuery(id+"F0.wireOp",EDGE,"E811"),sQuery(id+"F0.wireOp",EDGE,"E812"),sQuery(id+"F0.wireOp",EDGE,"E813"),sQuery(id+"F0.wireOp",EDGE,"E814"),sQuery(id+"F0.wireOp",EDGE,"E815"),sQuery(id+"F0.wireOp",EDGE,"E816"),sQuery(id+"F0.wireOp",EDGE,"E817"),sQuery(id+"F0.wireOp",EDGE,"E818"),sQuery(id+"F0.wireOp",EDGE,"E819"),sQuery(id+"F0.wireOp",EDGE,"E820"),sQuery(id+"F0.wireOp",EDGE,"E821"),sQuery(id+"F0.wireOp",EDGE,"E822"),sQuery(id+"F0.wireOp",EDGE,"E823"),sQuery(id+"F0.wireOp",EDGE,"E824"),sQuery(id+"F0.wireOp",EDGE,"E825"),sQuery(id+"F0.wireOp",EDGE,"E826"),sQuery(id+"F0.wireOp",EDGE,"E827"),sQuery(id+"F0.wireOp",EDGE,"E828"),sQuery(id+"F0.wireOp",EDGE,"E829"),sQuery(id+"F0.wireOp",EDGE,"E830"),sQuery(id+"F0.wireOp",EDGE,"E831"),sQuery(id+"F0.wireOp",EDGE,"E832"),sQuery(id+"F0.wireOp",EDGE,"E833"),sQuery(id+"F0.wireOp",EDGE,"E834"),sQuery(id+"F0.wireOp",EDGE,"E835"),sQuery(id+"F0.wireOp",EDGE,"E836"),sQuery(id+"F0.wireOp",EDGE,"E837"),sQuery(id+"F0.wireOp",EDGE,"E838"),sQuery(id+"F0.wireOp",EDGE,"E839"),sQuery(id+"F0.wireOp",EDGE,"E840"),sQuery(id+"F0.wireOp",EDGE,"E841"),sQuery(id+"F0.wireOp",EDGE,"E842"),sQuery(id+"F0.wireOp",EDGE,"E843"),sQuery(id+"F0.wireOp",EDGE,"E844"),sQuery(id+"F0.wireOp",EDGE,"E845"),sQuery(id+"F0.wireOp",EDGE,"E846"),sQuery(id+"F0.wireOp",EDGE,"E847"),sQuery(id+"F0.wireOp",EDGE,"E848"),sQuery(id+"F0.wireOp",EDGE,"E849"),sQuery(id+"F0.wireOp",EDGE,"E850"),sQuery(id+"F0.wireOp",EDGE,"E851"),sQuery(id+"F0.wireOp",EDGE,"E852"),sQuery(id+"F0.wireOp",EDGE,"E853"),sQuery(id+"F0.wireOp",EDGE,"E854"),sQuery(id+"F0.wireOp",EDGE,"E855"),sQuery(id+"F0.wireOp",EDGE,"E856"),sQuery(id+"F0.wireOp",EDGE,"E857"),sQuery(id+"F0.wireOp",EDGE,"E858"),sQuery(id+"F0.wireOp",EDGE,"E859"),sQuery(id+"F0.wireOp",EDGE,"E860"),sQuery(id+"F0.wireOp",EDGE,"E861"),sQuery(id+"F0.wireOp",EDGE,"E862"),sQuery(id+"F0.wireOp",EDGE,"E863"),sQuery(id+"F0.wireOp",EDGE,"E864"),sQuery(id+"F0.wireOp",EDGE,"E865"),sQuery(id+"F0.wireOp",EDGE,"E866"),sQuery(id+"F0.wireOp",EDGE,"E867"),sQuery(id+"F0.wireOp",EDGE,"E868"),sQuery(id+"F0.wireOp",EDGE,"E869"),sQuery(id+"F0.wireOp",EDGE,"E870"),sQuery(id+"F0.wireOp",EDGE,"E871"),sQuery(id+"F0.wireOp",EDGE,"E872"),sQuery(id+"F0.wireOp",EDGE,"E873"),sQuery(id+"F0.wireOp",EDGE,"E874"),sQuery(id+"F0.wireOp",EDGE,"E875"),sQuery(id+"F0.wireOp",EDGE,"E876"),sQuery(id+"F0.wireOp",EDGE,"E877"),sQuery(id+"F0.wireOp",EDGE,"E878"),sQuery(id+"F0.wireOp",EDGE,"E879"),sQuery(id+"F0.wireOp",EDGE,"E880"),sQuery(id+"F0.wireOp",EDGE,"E881"),sQuery(id+"F0.wireOp",EDGE,"E882"),sQuery(id+"F0.wireOp",EDGE,"E883"),sQuery(id+"F0.wireOp",EDGE,"E884"),sQuery(id+"F0.wireOp",EDGE,"E885"),sQuery(id+"F0.wireOp",EDGE,"E886"),sQuery(id+"F0.wireOp",EDGE,"E887"),sQuery(id+"F0.wireOp",EDGE,"E888"),sQuery(id+"F0.wireOp",EDGE,"E889"),sQuery(id+"F0.wireOp",EDGE,"E890"),sQuery(id+"F0.wireOp",EDGE,"E891"),sQuery(id+"F0.wireOp",EDGE,"E892"),sQuery(id+"F0.wireOp",EDGE,"E893"),sQuery(id+"F0.wireOp",EDGE,"E894"),sQuery(id+"F0.wireOp",EDGE,"E895"),sQuery(id+"F0.wireOp",EDGE,"E896"),sQuery(id+"F0.wireOp",EDGE,"E897"),sQuery(id+"F0.wireOp",EDGE,"E898"),sQuery(id+"F0.wireOp",EDGE,"E899"),sQuery(id+"F0.wireOp",EDGE,"E900"),sQuery(id+"F0.wireOp",EDGE,"E901"),sQuery(id+"F0.wireOp",EDGE,"E902"),sQuery(id+"F0.wireOp",EDGE,"E903"),sQuery(id+"F0.wireOp",EDGE,"E904"),sQuery(id+"F0.wireOp",EDGE,"E905"),sQuery(id+"F0.wireOp",EDGE,"E906"),sQuery(id+"F0.wireOp",EDGE,"E907"),sQuery(id+"F0.wireOp",EDGE,"E908"),sQuery(id+"F0.wireOp",EDGE,"E909"),sQuery(id+"F0.wireOp",EDGE,"E910"),sQuery(id+"F0.wireOp",EDGE,"E911"),sQuery(id+"F0.wireOp",EDGE,"E912"),sQuery(id+"F0.wireOp",EDGE,"E913"),sQuery(id+"F0.wireOp",EDGE,"E914"),sQuery(id+"F0.wireOp",EDGE,"E915"),sQuery(id+"F0.wireOp",EDGE,"E916"),sQuery(id+"F0.wireOp",EDGE,"E917"),sQuery(id+"F0.wireOp",EDGE,"E918"),sQuery(id+"F0.wireOp",EDGE,"E919"),sQuery(id+"F0.wireOp",EDGE,"E920"),sQuery(id+"F0.wireOp",EDGE,"E921"),sQuery(id+"F0.wireOp",EDGE,"E922"),sQuery(id+"F0.wireOp",EDGE,"E923"),sQuery(id+"F0.wireOp",EDGE,"E924"),sQuery(id+"F0.wireOp",EDGE,"E925"),sQuery(id+"F0.wireOp",EDGE,"E926"),sQuery(id+"F0.wireOp",EDGE,"E927"),sQuery(id+"F0.wireOp",EDGE,"E928"),sQuery(id+"F0.wireOp",EDGE,"E929"),sQuery(id+"F0.wireOp",EDGE,"E930"),sQuery(id+"F0.wireOp",EDGE,"E931"),sQuery(id+"F0.wireOp",EDGE,"E932"),sQuery(id+"F0.wireOp",EDGE,"E933"),sQuery(id+"F0.wireOp",EDGE,"E934"),sQuery(id+"F0.wireOp",EDGE,"E935"),sQuery(id+"F0.wireOp",EDGE,"E936"),sQuery(id+"F0.wireOp",EDGE,"E937"),sQuery(id+"F0.wireOp",EDGE,"E938"),sQuery(id+"F0.wireOp",EDGE,"E939"),sQuery(id+"F0.wireOp",EDGE,"E940"),sQuery(id+"F0.wireOp",EDGE,"E941"),sQuery(id+"F0.wireOp",EDGE,"E942"),sQuery(id+"F0.wireOp",EDGE,"E943"),sQuery(id+"F0.wireOp",EDGE,"E943"),sQuery(id+"F0.wireOp",EDGE,"E943"),sQuery(id+"F0.wireOp",EDGE,"E944"),sQuery(id+"F0.wireOp",EDGE,"E945"),sQuery(id+"F0.wireOp",EDGE,"E946"),sQuery(id+"F0.wireOp",EDGE,"E947"),sQuery(id+"F0.wireOp",EDGE,"E948"),sQuery(id+"F0.wireOp",EDGE,"E949"),sQuery(id+"F0.wireOp",EDGE,"E950"),sQuery(id+"F0.wireOp",EDGE,"E951"),sQuery(id+"F0.wireOp",EDGE,"E952"),sQuery(id+"F0.wireOp",EDGE,"E953"),sQuery(id+"F0.wireOp",EDGE,"E954"),sQuery(id+"F0.wireOp",EDGE,"E955"),sQuery(id+"F0.wireOp",EDGE,"E956"),sQuery(id+"F0.wireOp",EDGE,"E957"),sQuery(id+"F0.wireOp",EDGE,"E958"),sQuery(id+"F0.wireOp",EDGE,"E958"),sQuery(id+"F0.wireOp",EDGE,"E959"),sQuery(id+"F0.wireOp",EDGE,"E960"),sQuery(id+"F0.wireOp",EDGE,"E961"),sQuery(id+"F0.wireOp",EDGE,"E962"),sQuery(id+"F0.wireOp",EDGE,"E963"),sQuery(id+"F0.wireOp",EDGE,"E964"),sQuery(id+"F0.wireOp",EDGE,"E965"),sQuery(id+"F0.wireOp",EDGE,"E966"),sQuery(id+"F0.wireOp",EDGE,"E967"),sQuery(id+"F0.wireOp",EDGE,"E968"),sQuery(id+"F0.wireOp",EDGE,"E969"),sQuery(id+"F0.wireOp",EDGE,"E970"),sQuery(id+"F0.wireOp",EDGE,"E971"),sQuery(id+"F0.wireOp",EDGE,"E972"),sQuery(id+"F0.wireOp",EDGE,"E973"),sQuery(id+"F0.wireOp",EDGE,"E973"),sQuery(id+"F0.wireOp",EDGE,"E974"),sQuery(id+"F0.wireOp",EDGE,"E975"),sQuery(id+"F0.wireOp",EDGE,"E976"),sQuery(id+"F0.wireOp",EDGE,"E977"),sQuery(id+"F0.wireOp",EDGE,"E978"),sQuery(id+"F0.wireOp",EDGE,"E979"),sQuery(id+"F0.wireOp",EDGE,"E980"),sQuery(id+"F0.wireOp",EDGE,"E981"),sQuery(id+"F0.wireOp",EDGE,"E982"),sQuery(id+"F0.wireOp",EDGE,"E983"),sQuery(id+"F0.wireOp",EDGE,"E984"),sQuery(id+"F0.wireOp",EDGE,"E985"),sQuery(id+"F0.wireOp",EDGE,"E986"),sQuery(id+"F0.wireOp",EDGE,"E987"),sQuery(id+"F0.wireOp",EDGE,"E988"),sQuery(id+"F0.wireOp",EDGE,"E989"),sQuery(id+"F0.wireOp",EDGE,"E990"),sQuery(id+"F0.wireOp",EDGE,"E991"),sQuery(id+"F0.wireOp",EDGE,"E992"),sQuery(id+"F0.wireOp",EDGE,"E993"),sQuery(id+"F0.wireOp",EDGE,"E994"),sQuery(id+"F0.wireOp",EDGE,"E995"),sQuery(id+"F0.wireOp",EDGE,"E996"),sQuery(id+"F0.wireOp",EDGE,"E997"),sQuery(id+"F0.wireOp",EDGE,"E998"),sQuery(id+"F0.wireOp",EDGE,"E999"),sQuery(id+"F0.wireOp",EDGE,"E1000"),sQuery(id+"F0.wireOp",EDGE,"E1001"),sQuery(id+"F0.wireOp",EDGE,"E1002"),sQuery(id+"F0.wireOp",EDGE,"E1003"),sQuery(id+"F0.wireOp",EDGE,"E1004"),sQuery(id+"F0.wireOp",EDGE,"E1005"),sQuery(id+"F0.wireOp",EDGE,"E1006"),sQuery(id+"F0.wireOp",EDGE,"E1007"),sQuery(id+"F0.wireOp",EDGE,"E1008"),sQuery(id+"F0.wireOp",EDGE,"E1009"),sQuery(id+"F0.wireOp",EDGE,"E1010"),sQuery(id+"F0.wireOp",EDGE,"E1011"),sQuery(id+"F0.wireOp",EDGE,"E1012"),sQuery(id+"F0.wireOp",EDGE,"E1013"),sQuery(id+"F0.wireOp",EDGE,"E1014"),sQuery(id+"F0.wireOp",EDGE,"E1015"),sQuery(id+"F0.wireOp",EDGE,"E1016"),sQuery(id+"F0.wireOp",EDGE,"E1017"),sQuery(id+"F0.wireOp",EDGE,"E1018"),sQuery(id+"F0.wireOp",EDGE,"E1019"),sQuery(id+"F0.wireOp",EDGE,"E1020"),sQuery(id+"F0.wireOp",EDGE,"E1021"),sQuery(id+"F0.wireOp",EDGE,"E1022"),sQuery(id+"F0.wireOp",EDGE,"E1023"),sQuery(id+"F0.wireOp",EDGE,"E1024"),sQuery(id+"F0.wireOp",EDGE,"E1025"),sQuery(id+"F0.wireOp",EDGE,"E1026"),sQuery(id+"F0.wireOp",EDGE,"E1027"),sQuery(id+"F0.wireOp",EDGE,"E1028"),sQuery(id+"F0.wireOp",EDGE,"E1029"),sQuery(id+"F0.wireOp",EDGE,"E1030"),sQuery(id+"F0.wireOp",EDGE,"E1031"),sQuery(id+"F0.wireOp",EDGE,"E1032"),sQuery(id+"F0.wireOp",EDGE,"E1033"),sQuery(id+"F0.wireOp",EDGE,"E1034"),sQuery(id+"F0.wireOp",EDGE,"E1035"),sQuery(id+"F0.wireOp",EDGE,"E1036"),sQuery(id+"F0.wireOp",EDGE,"E1037"),sQuery(id+"F0.wireOp",EDGE,"E1038"),sQuery(id+"F0.wireOp",EDGE,"E1039"),sQuery(id+"F0.wireOp",EDGE,"E1040"),sQuery(id+"F0.wireOp",EDGE,"E1041"),sQuery(id+"F0.wireOp",EDGE,"E1042"),sQuery(id+"F0.wireOp",EDGE,"E1043"),sQuery(id+"F0.wireOp",EDGE,"E1044"),sQuery(id+"F0.wireOp",EDGE,"E1045"),sQuery(id+"F0.wireOp",EDGE,"E1046"),sQuery(id+"F0.wireOp",EDGE,"E1047"),sQuery(id+"F0.wireOp",EDGE,"E1048"),sQuery(id+"F0.wireOp",EDGE,"E1049"),sQuery(id+"F0.wireOp",EDGE,"E1050"),sQuery(id+"F0.wireOp",EDGE,"E1051"),sQuery(id+"F0.wireOp",EDGE,"E1052"),sQuery(id+"F0.wireOp",EDGE,"E1053"),sQuery(id+"F0.wireOp",EDGE,"E1054"),sQuery(id+"F0.wireOp",EDGE,"E1055"),sQuery(id+"F0.wireOp",EDGE,"E1056"),sQuery(id+"F0.wireOp",EDGE,"E1057"),sQuery(id+"F0.wireOp",EDGE,"E1058"),sQuery(id+"F0.wireOp",EDGE,"E1059"),sQuery(id+"F0.wireOp",EDGE,"E1060"),sQuery(id+"F0.wireOp",EDGE,"E1061"),sQuery(id+"F0.wireOp",EDGE,"E1062"),sQuery(id+"F0.wireOp",EDGE,"E1063"),sQuery(id+"F0.wireOp",EDGE,"E1064"),sQuery(id+"F0.wireOp",EDGE,"E1065"),sQuery(id+"F0.wireOp",EDGE,"E1066"),sQuery(id+"F0.wireOp",EDGE,"E1067"),sQuery(id+"F0.wireOp",EDGE,"E1068"),sQuery(id+"F0.wireOp",EDGE,"E1069"),sQuery(id+"F0.wireOp",EDGE,"E1070"),sQuery(id+"F0.wireOp",EDGE,"E1071"),sQuery(id+"F0.wireOp",EDGE,"E1072"),sQuery(id+"F0.wireOp",EDGE,"E1073"),sQuery(id+"F0.wireOp",EDGE,"E1074"),sQuery(id+"F0.wireOp",EDGE,"E1075"),sQuery(id+"F0.wireOp",EDGE,"E1076"),sQuery(id+"F0.wireOp",EDGE,"E1077"),sQuery(id+"F0.wireOp",EDGE,"E1078"),sQuery(id+"F0.wireOp",EDGE,"E1079"),sQuery(id+"F0.wireOp",EDGE,"E1080"),sQuery(id+"F0.wireOp",EDGE,"E1081"),sQuery(id+"F0.wireOp",EDGE,"E1082"),sQuery(id+"F0.wireOp",EDGE,"E1083"),sQuery(id+"F0.wireOp",EDGE,"E1084"),sQuery(id+"F0.wireOp",EDGE,"E1085"),sQuery(id+"F0.wireOp",EDGE,"E1086"),sQuery(id+"F0.wireOp",EDGE,"E1087"),sQuery(id+"F0.wireOp",EDGE,"E1088"),sQuery(id+"F0.wireOp",EDGE,"E1089"),sQuery(id+"F0.wireOp",EDGE,"E1090"),sQuery(id+"F0.wireOp",EDGE,"E1091"),sQuery(id+"F0.wireOp",EDGE,"E1092"),sQuery(id+"F0.wireOp",EDGE,"E1093"),sQuery(id+"F0.wireOp",EDGE,"E1094"),sQuery(id+"F0.wireOp",EDGE,"E1095"),sQuery(id+"F0.wireOp",EDGE,"E1096"),sQuery(id+"F0.wireOp",EDGE,"E1097"),sQuery(id+"F0.wireOp",EDGE,"E1098"),sQuery(id+"F0.wireOp",EDGE,"E1099"),sQuery(id+"F0.wireOp",EDGE,"E1100"),sQuery(id+"F0.wireOp",EDGE,"E1101"),sQuery(id+"F0.wireOp",EDGE,"E1102"),sQuery(id+"F0.wireOp",EDGE,"E1103"),sQuery(id+"F0.wireOp",EDGE,"E1104"),sQuery(id+"F0.wireOp",EDGE,"E1105"),sQuery(id+"F0.wireOp",EDGE,"E1106"),sQuery(id+"F0.wireOp",EDGE,"E1107"),sQuery(id+"F0.wireOp",EDGE,"E1108"),sQuery(id+"F0.wireOp",EDGE,"E1109"),sQuery(id+"F0.wireOp",EDGE,"E1110"),sQuery(id+"F0.wireOp",EDGE,"E1111"),sQuery(id+"F0.wireOp",EDGE,"E1112"),sQuery(id+"F0.wireOp",EDGE,"E1113"),sQuery(id+"F0.wireOp",EDGE,"E1114"),sQuery(id+"F0.wireOp",EDGE,"E1115"),sQuery(id+"F0.wireOp",EDGE,"E1116"),sQuery(id+"F0.wireOp",EDGE,"E1117"),sQuery(id+"F0.wireOp",EDGE,"E1118"),sQuery(id+"F0.wireOp",EDGE,"E1119"),sQuery(id+"F0.wireOp",EDGE,"E1120"),sQuery(id+"F0.wireOp",EDGE,"E1121"),sQuery(id+"F0.wireOp",EDGE,"E1122"),sQuery(id+"F0.wireOp",EDGE,"E1123"),sQuery(id+"F0.wireOp",EDGE,"E1124"),sQuery(id+"F0.wireOp",EDGE,"E1125"),sQuery(id+"F0.wireOp",EDGE,"E1126"),sQuery(id+"F0.wireOp",EDGE,"E1127"),sQuery(id+"F0.wireOp",EDGE,"E1128"),sQuery(id+"F0.wireOp",EDGE,"E1129"),sQuery(id+"F0.wireOp",EDGE,"E1130"),sQuery(id+"F0.wireOp",EDGE,"E1131"),sQuery(id+"F0.wireOp",EDGE,"E1132"),sQuery(id+"F0.wireOp",EDGE,"E1133"),sQuery(id+"F0.wireOp",EDGE,"E1134"),sQuery(id+"F0.wireOp",EDGE,"E1135"),sQuery(id+"F0.wireOp",EDGE,"E1136"),sQuery(id+"F0.wireOp",EDGE,"E1137"),sQuery(id+"F0.wireOp",EDGE,"E1138"),sQuery(id+"F0.wireOp",EDGE,"E1139"),sQuery(id+"F0.wireOp",EDGE,"E1140"),sQuery(id+"F0.wireOp",EDGE,"E1141"),sQuery(id+"F0.wireOp",EDGE,"E1142"),sQuery(id+"F0.wireOp",EDGE,"E1143"),sQuery(id+"F0.wireOp",EDGE,"E1144"),sQuery(id+"F0.wireOp",EDGE,"E1145"),sQuery(id+"F0.wireOp",EDGE,"E1146"),sQuery(id+"F0.wireOp",EDGE,"E1147"),sQuery(id+"F0.wireOp",EDGE,"E1148"),sQuery(id+"F0.wireOp",EDGE,"E1149"),sQuery(id+"F0.wireOp",EDGE,"E1150"),sQuery(id+"F0.wireOp",EDGE,"E1151"),sQuery(id+"F0.wireOp",EDGE,"E1152"),sQuery(id+"F0.wireOp",EDGE,"E1153"),sQuery(id+"F0.wireOp",EDGE,"E1154"),sQuery(id+"F0.wireOp",EDGE,"E1155"),sQuery(id+"F0.wireOp",EDGE,"E1156"),sQuery(id+"F0.wireOp",EDGE,"E1157"),sQuery(id+"F0.wireOp",EDGE,"E1158"),sQuery(id+"F0.wireOp",EDGE,"E1159"),sQuery(id+"F0.wireOp",EDGE,"E1160"),sQuery(id+"F0.wireOp",EDGE,"E1161"),sQuery(id+"F0.wireOp",EDGE,"E1162"),sQuery(id+"F0.wireOp",EDGE,"E1163"),sQuery(id+"F0.wireOp",EDGE,"E1164"),sQuery(id+"F0.wireOp",EDGE,"E1165"),sQuery(id+"F0.wireOp",EDGE,"E1166"),sQuery(id+"F0.wireOp",EDGE,"E1167"),sQuery(id+"F0.wireOp",EDGE,"E1168"),sQuery(id+"F0.wireOp",EDGE,"E1169"),sQuery(id+"F0.wireOp",EDGE,"E1170"),sQuery(id+"F0.wireOp",EDGE,"E1171"),sQuery(id+"F0.wireOp",EDGE,"E1172"),sQuery(id+"F0.wireOp",EDGE,"E1173"),sQuery(id+"F0.wireOp",EDGE,"E1174"),sQuery(id+"F0.wireOp",EDGE,"E1175"),sQuery(id+"F0.wireOp",EDGE,"E1176"),sQuery(id+"F0.wireOp",EDGE,"E1177"),sQuery(id+"F0.wireOp",EDGE,"E1178"),sQuery(id+"F0.wireOp",EDGE,"E1179"),sQuery(id+"F0.wireOp",EDGE,"E1180"),sQuery(id+"F0.wireOp",EDGE,"E1181"),sQuery(id+"F0.wireOp",EDGE,"E1182"),sQuery(id+"F0.wireOp",EDGE,"E1183"),sQuery(id+"F0.wireOp",EDGE,"E1184"),sQuery(id+"F0.wireOp",EDGE,"E1185"),sQuery(id+"F0.wireOp",EDGE,"E1186"),sQuery(id+"F0.wireOp",EDGE,"E1187"),sQuery(id+"F0.wireOp",EDGE,"E1188"),sQuery(id+"F0.wireOp",EDGE,"E1189"),sQuery(id+"F0.wireOp",EDGE,"E1190"),sQuery(id+"F0.wireOp",EDGE,"E1191"),sQuery(id+"F0.wireOp",EDGE,"E1192"),sQuery(id+"F0.wireOp",EDGE,"E1193"),sQuery(id+"F0.wireOp",EDGE,"E1194"),sQuery(id+"F0.wireOp",EDGE,"E1195"),sQuery(id+"F0.wireOp",EDGE,"E1196"),sQuery(id+"F0.wireOp",EDGE,"E1197"),sQuery(id+"F0.wireOp",EDGE,"E1198"),sQuery(id+"F0.wireOp",EDGE,"E1199"),sQuery(id+"F0.wireOp",EDGE,"E1200"),sQuery(id+"F0.wireOp",EDGE,"E1201"),sQuery(id+"F0.wireOp",EDGE,"E1202"),sQuery(id+"F0.wireOp",EDGE,"E1203"),sQuery(id+"F0.wireOp",EDGE,"E1204"),sQuery(id+"F0.wireOp",EDGE,"E1205"),sQuery(id+"F0.wireOp",EDGE,"E1206"),sQuery(id+"F0.wireOp",EDGE,"E1207"),sQuery(id+"F0.wireOp",EDGE,"E1208"),sQuery(id+"F0.wireOp",EDGE,"E1209"),sQuery(id+"F0.wireOp",EDGE,"E1210"),sQuery(id+"F0.wireOp",EDGE,"E1211"),sQuery(id+"F0.wireOp",EDGE,"E1212"),sQuery(id+"F0.wireOp",EDGE,"E1213"),sQuery(id+"F0.wireOp",EDGE,"E1214"),sQuery(id+"F0.wireOp",EDGE,"E1215"),sQuery(id+"F0.wireOp",EDGE,"E1216"),sQuery(id+"F0.wireOp",EDGE,"E1217"),sQuery(id+"F0.wireOp",EDGE,"E1218"),sQuery(id+"F0.wireOp",EDGE,"E1219"),sQuery(id+"F0.wireOp",EDGE,"E1220"),sQuery(id+"F0.wireOp",EDGE,"E1221"),sQuery(id+"F0.wireOp",EDGE,"E1222"),sQuery(id+"F0.wireOp",EDGE,"E1223"),sQuery(id+"F0.wireOp",EDGE,"E1224"),sQuery(id+"F0.wireOp",EDGE,"E1225"),sQuery(id+"F0.wireOp",EDGE,"E1226"),sQuery(id+"F0.wireOp",EDGE,"E1227"),sQuery(id+"F0.wireOp",EDGE,"E1228"),sQuery(id+"F0.wireOp",EDGE,"E1229"),sQuery(id+"F0.wireOp",EDGE,"E1230"),sQuery(id+"F0.wireOp",EDGE,"E1231"),sQuery(id+"F0.wireOp",EDGE,"E1232"),sQuery(id+"F0.wireOp",EDGE,"E1233"),sQuery(id+"F0.wireOp",EDGE,"E1234"),sQuery(id+"F0.wireOp",EDGE,"E1235"),sQuery(id+"F0.wireOp",EDGE,"E1236"),sQuery(id+"F0.wireOp",EDGE,"E1237"),sQuery(id+"F0.wireOp",EDGE,"E1238"),sQuery(id+"F0.wireOp",EDGE,"E1239"),sQuery(id+"F0.wireOp",EDGE,"E1240"),sQuery(id+"F0.wireOp",EDGE,"E1241"),sQuery(id+"F0.wireOp",EDGE,"E1242"),sQuery(id+"F0.wireOp",EDGE,"E1243"),sQuery(id+"F0.wireOp",EDGE,"E1244"),sQuery(id+"F0.wireOp",EDGE,"E1245"),sQuery(id+"F0.wireOp",EDGE,"E1246"),sQuery(id+"F0.wireOp",EDGE,"E1247"),sQuery(id+"F0.wireOp",EDGE,"E1248"),sQuery(id+"F0.wireOp",EDGE,"E1249"),sQuery(id+"F0.wireOp",EDGE,"E1250"),sQuery(id+"F0.wireOp",EDGE,"E1251"),sQuery(id+"F0.wireOp",EDGE,"E1252"),sQuery(id+"F0.wireOp",EDGE,"E1253"),sQuery(id+"F0.wireOp",EDGE,"E1254"),sQuery(id+"F0.wireOp",EDGE,"E1255"),sQuery(id+"F0.wireOp",EDGE,"E1256"),sQuery(id+"F0.wireOp",EDGE,"E1257"),sQuery(id+"F0.wireOp",EDGE,"E1258"),sQuery(id+"F0.wireOp",EDGE,"E1259"),sQuery(id+"F0.wireOp",EDGE,"E1260"),sQuery(id+"F0.wireOp",EDGE,"E1261"),sQuery(id+"F0.wireOp",EDGE,"E1262"),sQuery(id+"F0.wireOp",EDGE,"E1263"),sQuery(id+"F0.wireOp",EDGE,"E1264"),sQuery(id+"F0.wireOp",EDGE,"E1265"),sQuery(id+"F0.wireOp",EDGE,"E1266"),sQuery(id+"F0.wireOp",EDGE,"E1267"),sQuery(id+"F0.wireOp",EDGE,"E1268"),sQuery(id+"F0.wireOp",EDGE,"E1269"),sQuery(id+"F0.wireOp",EDGE,"E1270"),sQuery(id+"F0.wireOp",EDGE,"E1271"),sQuery(id+"F0.wireOp",EDGE,"E1272"),sQuery(id+"F0.wireOp",EDGE,"E1273"),sQuery(id+"F0.wireOp",EDGE,"E1274"),sQuery(id+"F0.wireOp",EDGE,"E1275"),sQuery(id+"F0.wireOp",EDGE,"E1276"),sQuery(id+"F0.wireOp",EDGE,"E1277"),sQuery(id+"F0.wireOp",EDGE,"E1278"),sQuery(id+"F0.wireOp",EDGE,"E1279"),sQuery(id+"F0.wireOp",EDGE,"E1280"),sQuery(id+"F0.wireOp",EDGE,"E1281"),sQuery(id+"F0.wireOp",EDGE,"E1282"),sQuery(id+"F0.wireOp",EDGE,"E1283"),sQuery(id+"F0.wireOp",EDGE,"E1284"),sQuery(id+"F0.wireOp",EDGE,"E1285"),sQuery(id+"F0.wireOp",EDGE,"E1286"),sQuery(id+"F0.wireOp",EDGE,"E1287"),sQuery(id+"F0.wireOp",EDGE,"E1288"),sQuery(id+"F0.wireOp",EDGE,"E1289"),sQuery(id+"F0.wireOp",EDGE,"E1290"),sQuery(id+"F0.wireOp",EDGE,"E1291"),sQuery(id+"F0.wireOp",EDGE,"E1292"),sQuery(id+"F0.wireOp",EDGE,"E1293"),sQuery(id+"F0.wireOp",EDGE,"E1294"),sQuery(id+"F0.wireOp",EDGE,"E1295"),sQuery(id+"F0.wireOp",EDGE,"E1296"),sQuery(id+"F0.wireOp",EDGE,"E1297"),sQuery(id+"F0.wireOp",EDGE,"E1297"),sQuery(id+"F0.wireOp",EDGE,"E1297"),sQuery(id+"F0.wireOp",EDGE,"E1298"),sQuery(id+"F0.wireOp",EDGE,"E1299"),sQuery(id+"F0.wireOp",EDGE,"E1300"),sQuery(id+"F0.wireOp",EDGE,"E1300"),sQuery(id+"F0.wireOp",EDGE,"E1301"),sQuery(id+"F0.wireOp",EDGE,"E1302"),sQuery(id+"F0.wireOp",EDGE,"E1303"),sQuery(id+"F0.wireOp",EDGE,"E1304"),sQuery(id+"F0.wireOp",EDGE,"E1305"),sQuery(id+"F0.wireOp",EDGE,"E1306"),sQuery(id+"F0.wireOp",EDGE,"E1307"),sQuery(id+"F0.wireOp",EDGE,"E1308"),sQuery(id+"F0.wireOp",EDGE,"E1309"),sQuery(id+"F0.wireOp",EDGE,"E1310"),sQuery(id+"F0.wireOp",EDGE,"E1311"),sQuery(id+"F0.wireOp",EDGE,"E1312"),sQuery(id+"F0.wireOp",EDGE,"E1313"),sQuery(id+"F0.wireOp",EDGE,"E1314"),sQuery(id+"F0.wireOp",EDGE,"E1314"),sQuery(id+"F0.wireOp",EDGE,"E1315"),sQuery(id+"F0.wireOp",EDGE,"E1316"),sQuery(id+"F0.wireOp",EDGE,"E1317"),sQuery(id+"F0.wireOp",EDGE,"E1318"),sQuery(id+"F0.wireOp",EDGE,"E1319"),sQuery(id+"F0.wireOp",EDGE,"E1319"),sQuery(id+"F0.wireOp",EDGE,"E1320"),sQuery(id+"F0.wireOp",EDGE,"E1321"),sQuery(id+"F0.wireOp",EDGE,"E1322"),sQuery(id+"F0.wireOp",EDGE,"E1323"),sQuery(id+"F0.wireOp",EDGE,"E1324"),sQuery(id+"F0.wireOp",EDGE,"E1325"),sQuery(id+"F0.wireOp",EDGE,"E1326"),sQuery(id+"F0.wireOp",EDGE,"E1327"),sQuery(id+"F0.wireOp",EDGE,"E1328"),sQuery(id+"F0.wireOp",EDGE,"E1329"),sQuery(id+"F0.wireOp",EDGE,"E1330"),sQuery(id+"F0.wireOp",EDGE,"E1331"),sQuery(id+"F0.wireOp",EDGE,"E1332"),sQuery(id+"F0.wireOp",EDGE,"E1333"),sQuery(id+"F0.wireOp",EDGE,"E1334"),sQuery(id+"F0.wireOp",EDGE,"E1334"),sQuery(id+"F0.wireOp",EDGE,"E1335"),sQuery(id+"F0.wireOp",EDGE,"E1336"),sQuery(id+"F0.wireOp",EDGE,"E1337"),sQuery(id+"F0.wireOp",EDGE,"E1338"),sQuery(id+"F0.wireOp",EDGE,"E1339"),sQuery(id+"F0.wireOp",EDGE,"E1340"),sQuery(id+"F0.wireOp",EDGE,"E1341"),sQuery(id+"F0.wireOp",EDGE,"E1342"),sQuery(id+"F0.wireOp",EDGE,"E1343"),sQuery(id+"F0.wireOp",EDGE,"E1344"),sQuery(id+"F0.wireOp",EDGE,"E1345"),sQuery(id+"F0.wireOp",EDGE,"E1346"),sQuery(id+"F0.wireOp",EDGE,"E1347"),sQuery(id+"F0.wireOp",EDGE,"E1348"),sQuery(id+"F0.wireOp",EDGE,"E1349"),sQuery(id+"F0.wireOp",EDGE,"E1350"),sQuery(id+"F0.wireOp",EDGE,"E1351"),sQuery(id+"F0.wireOp",EDGE,"E1352"),sQuery(id+"F0.wireOp",EDGE,"E1353"),sQuery(id+"F0.wireOp",EDGE,"E1354"),sQuery(id+"F0.wireOp",EDGE,"E1354"),sQuery(id+"F0.wireOp",EDGE,"E1355"),sQuery(id+"F0.wireOp",EDGE,"E1356"),sQuery(id+"F0.wireOp",EDGE,"E1357"),sQuery(id+"F0.wireOp",EDGE,"E1358"),sQuery(id+"F0.wireOp",EDGE,"E1359"),sQuery(id+"F0.wireOp",EDGE,"E1360"),sQuery(id+"F0.wireOp",EDGE,"E1361"),sQuery(id+"F0.wireOp",EDGE,"E1362"),sQuery(id+"F0.wireOp",EDGE,"E1363"),sQuery(id+"F0.wireOp",EDGE,"E1364"),sQuery(id+"F0.wireOp",EDGE,"E1365"),sQuery(id+"F0.wireOp",EDGE,"E1366"),sQuery(id+"F0.wireOp",EDGE,"E1367"),sQuery(id+"F0.wireOp",EDGE,"E1368"),sQuery(id+"F0.wireOp",EDGE,"E1369"),sQuery(id+"F0.wireOp",EDGE,"E1370"),sQuery(id+"F0.wireOp",EDGE,"E1371"),sQuery(id+"F0.wireOp",EDGE,"E1372"),sQuery(id+"F0.wireOp",EDGE,"E1373"),sQuery(id+"F0.wireOp",EDGE,"E1374"),sQuery(id+"F0.wireOp",EDGE,"E1375"),sQuery(id+"F0.wireOp",EDGE,"E1376"),sQuery(id+"F0.wireOp",EDGE,"E1377"),sQuery(id+"F0.wireOp",EDGE,"E1378"),sQuery(id+"F0.wireOp",EDGE,"E1379"),sQuery(id+"F0.wireOp",EDGE,"E1380"),sQuery(id+"F0.wireOp",EDGE,"E1381"),sQuery(id+"F0.wireOp",EDGE,"E1382"),sQuery(id+"F0.wireOp",EDGE,"E1383"),sQuery(id+"F0.wireOp",EDGE,"E1384"),sQuery(id+"F0.wireOp",EDGE,"E1385"),sQuery(id+"F0.wireOp",EDGE,"E1386"),sQuery(id+"F0.wireOp",EDGE,"E1387"),sQuery(id+"F0.wireOp",EDGE,"E1388"),sQuery(id+"F0.wireOp",EDGE,"E1389"),sQuery(id+"F0.wireOp",EDGE,"E1390"),sQuery(id+"F0.wireOp",EDGE,"E1391"),sQuery(id+"F0.wireOp",EDGE,"E1392"),sQuery(id+"F0.wireOp",EDGE,"E1393"),sQuery(id+"F0.wireOp",EDGE,"E1394"),sQuery(id+"F0.wireOp",EDGE,"E1395"),sQuery(id+"F0.wireOp",EDGE,"E1396"),sQuery(id+"F0.wireOp",EDGE,"E1397"),sQuery(id+"F0.wireOp",EDGE,"E1398"),sQuery(id+"F0.wireOp",EDGE,"E1399"),sQuery(id+"F0.wireOp",EDGE,"E1400"),sQuery(id+"F0.wireOp",EDGE,"E1401"),sQuery(id+"F0.wireOp",EDGE,"E1402"),sQuery(id+"F0.wireOp",EDGE,"E1403"),sQuery(id+"F0.wireOp",EDGE,"E1404"),sQuery(id+"F0.wireOp",EDGE,"E1405"),sQuery(id+"F0.wireOp",EDGE,"E1406"),sQuery(id+"F0.wireOp",EDGE,"E1407"),sQuery(id+"F0.wireOp",EDGE,"E1408"),sQuery(id+"F0.wireOp",EDGE,"E1409"),sQuery(id+"F0.wireOp",EDGE,"E1410"),sQuery(id+"F0.wireOp",EDGE,"E1411"),sQuery(id+"F0.wireOp",EDGE,"E1412"),sQuery(id+"F0.wireOp",EDGE,"E1413"),sQuery(id+"F0.wireOp",EDGE,"E1414"),sQuery(id+"F0.wireOp",EDGE,"E1415"),sQuery(id+"F0.wireOp",EDGE,"E1416"),sQuery(id+"F0.wireOp",EDGE,"E1417"),sQuery(id+"F0.wireOp",EDGE,"E1418"),sQuery(id+"F0.wireOp",EDGE,"E1419"),sQuery(id+"F0.wireOp",EDGE,"E1420"),sQuery(id+"F0.wireOp",EDGE,"E1421"),sQuery(id+"F0.wireOp",EDGE,"E1422"),sQuery(id+"F0.wireOp",EDGE,"E1423"),sQuery(id+"F0.wireOp",EDGE,"E1424"),sQuery(id+"F0.wireOp",EDGE,"E1425"),sQuery(id+"F0.wireOp",EDGE,"E1426"),sQuery(id+"F0.wireOp",EDGE,"E1427"),sQuery(id+"F0.wireOp",EDGE,"E1428"),sQuery(id+"F0.wireOp",EDGE,"E1429"),sQuery(id+"F0.wireOp",EDGE,"E1430"),sQuery(id+"F0.wireOp",EDGE,"E1431"),sQuery(id+"F0.wireOp",EDGE,"E1432"),sQuery(id+"F0.wireOp",EDGE,"E1433"),sQuery(id+"F0.wireOp",EDGE,"E1434"),sQuery(id+"F0.wireOp",EDGE,"E1435"),sQuery(id+"F0.wireOp",EDGE,"E1436"),sQuery(id+"F0.wireOp",EDGE,"E1437"),sQuery(id+"F0.wireOp",EDGE,"E1438"),sQuery(id+"F0.wireOp",EDGE,"E1439"),sQuery(id+"F0.wireOp",EDGE,"E1440"),sQuery(id+"F0.wireOp",EDGE,"E1441"),sQuery(id+"F0.wireOp",EDGE,"E1442"),sQuery(id+"F0.wireOp",EDGE,"E1443"),sQuery(id+"F0.wireOp",EDGE,"E1444"),sQuery(id+"F0.wireOp",EDGE,"E1445"),sQuery(id+"F0.wireOp",EDGE,"E1446"),sQuery(id+"F0.wireOp",EDGE,"E1447"),sQuery(id+"F0.wireOp",EDGE,"E1448"),sQuery(id+"F0.wireOp",EDGE,"E1449"),sQuery(id+"F0.wireOp",EDGE,"E1450"),sQuery(id+"F0.wireOp",EDGE,"E1451"),sQuery(id+"F0.wireOp",EDGE,"E1452"),sQuery(id+"F0.wireOp",EDGE,"E1453"),sQuery(id+"F0.wireOp",EDGE,"E1454"),sQuery(id+"F0.wireOp",EDGE,"E1455"),sQuery(id+"F0.wireOp",EDGE,"E1456"),sQuery(id+"F0.wireOp",EDGE,"E1457"),sQuery(id+"F0.wireOp",EDGE,"E1458"),sQuery(id+"F0.wireOp",EDGE,"E1459"),sQuery(id+"F0.wireOp",EDGE,"E1460"),sQuery(id+"F0.wireOp",EDGE,"E1461"),sQuery(id+"F0.wireOp",EDGE,"E1462"),sQuery(id+"F0.wireOp",EDGE,"E1463"),sQuery(id+"F0.wireOp",EDGE,"E1464"),sQuery(id+"F0.wireOp",EDGE,"E1465"),sQuery(id+"F0.wireOp",EDGE,"E1466"),sQuery(id+"F0.wireOp",EDGE,"E1467"),sQuery(id+"F0.wireOp",EDGE,"E1468"),sQuery(id+"F0.wireOp",EDGE,"E1469"),sQuery(id+"F0.wireOp",EDGE,"E1470"),sQuery(id+"F0.wireOp",EDGE,"E1471"),sQuery(id+"F0.wireOp",EDGE,"E1472"),sQuery(id+"F0.wireOp",EDGE,"E1473"),sQuery(id+"F0.wireOp",EDGE,"E1474"),sQuery(id+"F0.wireOp",EDGE,"E1475"),sQuery(id+"F0.wireOp",EDGE,"E1476"),sQuery(id+"F0.wireOp",EDGE,"E1477"),sQuery(id+"F0.wireOp",EDGE,"E1478"),sQuery(id+"F0.wireOp",EDGE,"E1479"),sQuery(id+"F0.wireOp",EDGE,"E1480"),sQuery(id+"F0.wireOp",EDGE,"E1481"),sQuery(id+"F0.wireOp",EDGE,"E1482"),sQuery(id+"F0.wireOp",EDGE,"E1483"),sQuery(id+"F0.wireOp",EDGE,"E1484"),sQuery(id+"F0.wireOp",EDGE,"E1485"),sQuery(id+"F0.wireOp",EDGE,"E1486"),sQuery(id+"F0.wireOp",EDGE,"E1487"),sQuery(id+"F0.wireOp",EDGE,"E1488"),sQuery(id+"F0.wireOp",EDGE,"E1489"),sQuery(id+"F0.wireOp",EDGE,"E1490"),sQuery(id+"F0.wireOp",EDGE,"E1491"),sQuery(id+"F0.wireOp",EDGE,"E1492"),sQuery(id+"F0.wireOp",EDGE,"E1493"),sQuery(id+"F0.wireOp",EDGE,"E1494"),sQuery(id+"F0.wireOp",EDGE,"E1495"),sQuery(id+"F0.wireOp",EDGE,"E1496"),sQuery(id+"F0.wireOp",EDGE,"E1497"),sQuery(id+"F0.wireOp",EDGE,"E1498"),sQuery(id+"F0.wireOp",EDGE,"E1499"),sQuery(id+"F0.wireOp",EDGE,"E1500"),sQuery(id+"F0.wireOp",EDGE,"E1501"),sQuery(id+"F0.wireOp",EDGE,"E1502"),sQuery(id+"F0.wireOp",EDGE,"E1503"),sQuery(id+"F0.wireOp",EDGE,"E1504"),sQuery(id+"F0.wireOp",EDGE,"E1505"),sQuery(id+"F0.wireOp",EDGE,"E1506"),sQuery(id+"F0.wireOp",EDGE,"E1507"),sQuery(id+"F0.wireOp",EDGE,"E1508"),sQuery(id+"F0.wireOp",EDGE,"E1509"),sQuery(id+"F0.wireOp",EDGE,"E1510"),sQuery(id+"F0.wireOp",EDGE,"E1511"),sQuery(id+"F0.wireOp",EDGE,"E1512"),sQuery(id+"F0.wireOp",EDGE,"E1513"),sQuery(id+"F0.wireOp",EDGE,"E1514"),sQuery(id+"F0.wireOp",EDGE,"E1515"),sQuery(id+"F0.wireOp",EDGE,"E1516"),sQuery(id+"F0.wireOp",EDGE,"E1517"),sQuery(id+"F0.wireOp",EDGE,"E1518"),sQuery(id+"F0.wireOp",EDGE,"E1519"),sQuery(id+"F0.wireOp",EDGE,"E1520"),sQuery(id+"F0.wireOp",EDGE,"E1521"),sQuery(id+"F0.wireOp",EDGE,"E1522"),sQuery(id+"F0.wireOp",EDGE,"E1523"),sQuery(id+"F0.wireOp",EDGE,"E1524"),sQuery(id+"F0.wireOp",EDGE,"E1525"),sQuery(id+"F0.wireOp",EDGE,"E1526"),sQuery(id+"F0.wireOp",EDGE,"E1527"),sQuery(id+"F0.wireOp",EDGE,"E1528"),sQuery(id+"F0.wireOp",EDGE,"E1529"),sQuery(id+"F0.wireOp",EDGE,"E1530"),sQuery(id+"F0.wireOp",EDGE,"E1531"),sQuery(id+"F0.wireOp",EDGE,"E1532"),sQuery(id+"F0.wireOp",EDGE,"E1533"),sQuery(id+"F0.wireOp",EDGE,"E1534"),sQuery(id+"F0.wireOp",EDGE,"E1535"),sQuery(id+"F0.wireOp",EDGE,"E1536"),sQuery(id+"F0.wireOp",EDGE,"E1537"),sQuery(id+"F0.wireOp",EDGE,"E1538"),sQuery(id+"F0.wireOp",EDGE,"E1539"),sQuery(id+"F0.wireOp",EDGE,"E1540"),sQuery(id+"F0.wireOp",EDGE,"E1541"),sQuery(id+"F0.wireOp",EDGE,"E1542"),sQuery(id+"F0.wireOp",EDGE,"E1543"),sQuery(id+"F0.wireOp",EDGE,"E1544"),sQuery(id+"F0.wireOp",EDGE,"E1545"),sQuery(id+"F0.wireOp",EDGE,"E1546"),sQuery(id+"F0.wireOp",EDGE,"E1547"),sQuery(id+"F0.wireOp",EDGE,"E1548"),sQuery(id+"F0.wireOp",EDGE,"E1549"),sQuery(id+"F0.wireOp",EDGE,"E1550"),sQuery(id+"F0.wireOp",EDGE,"E1551"),sQuery(id+"F0.wireOp",EDGE,"E1552"),sQuery(id+"F0.wireOp",EDGE,"E1553"),sQuery(id+"F0.wireOp",EDGE,"E1554"),sQuery(id+"F0.wireOp",EDGE,"E1555"),sQuery(id+"F0.wireOp",EDGE,"E1556"),sQuery(id+"F0.wireOp",EDGE,"E1557"),sQuery(id+"F0.wireOp",EDGE,"E1558"),sQuery(id+"F0.wireOp",EDGE,"E1559"),sQuery(id+"F0.wireOp",EDGE,"E1560"),sQuery(id+"F0.wireOp",EDGE,"E1561"),sQuery(id+"F0.wireOp",EDGE,"E1562"),sQuery(id+"F0.wireOp",EDGE,"E1563"),sQuery(id+"F0.wireOp",EDGE,"E1564"),sQuery(id+"F0.wireOp",EDGE,"E1565"),sQuery(id+"F0.wireOp",EDGE,"E1566"),sQuery(id+"F0.wireOp",EDGE,"E1567"),sQuery(id+"F0.wireOp",EDGE,"E1568"),sQuery(id+"F0.wireOp",EDGE,"E1569"),sQuery(id+"F0.wireOp",EDGE,"E1570"),sQuery(id+"F0.wireOp",EDGE,"E1571"),sQuery(id+"F0.wireOp",EDGE,"E1572"),sQuery(id+"F0.wireOp",EDGE,"E1573"),sQuery(id+"F0.wireOp",EDGE,"E1574"),sQuery(id+"F0.wireOp",EDGE,"E1575"),sQuery(id+"F0.wireOp",EDGE,"E1576"),sQuery(id+"F0.wireOp",EDGE,"E1577"),sQuery(id+"F0.wireOp",EDGE,"E1578"),sQuery(id+"F0.wireOp",EDGE,"E1579"),sQuery(id+"F0.wireOp",EDGE,"E1580"),sQuery(id+"F0.wireOp",EDGE,"E1581"),sQuery(id+"F0.wireOp",EDGE,"E1582"),sQuery(id+"F0.wireOp",EDGE,"E1583"),sQuery(id+"F0.wireOp",EDGE,"E1584"),sQuery(id+"F0.wireOp",EDGE,"E1585"),sQuery(id+"F0.wireOp",EDGE,"E1586"),sQuery(id+"F0.wireOp",EDGE,"E1587"),sQuery(id+"F0.wireOp",EDGE,"E1588"),sQuery(id+"F0.wireOp",EDGE,"E1589"),sQuery(id+"F0.wireOp",EDGE,"E1590"),sQuery(id+"F0.wireOp",EDGE,"E1591"),sQuery(id+"F0.wireOp",EDGE,"E1592"),sQuery(id+"F0.wireOp",EDGE,"E1593"),sQuery(id+"F0.wireOp",EDGE,"E1594"),sQuery(id+"F0.wireOp",EDGE,"E1595"),sQuery(id+"F0.wireOp",EDGE,"E1595"),sQuery(id+"F0.wireOp",EDGE,"E1596"),sQuery(id+"F0.wireOp",EDGE,"E1597"),sQuery(id+"F0.wireOp",EDGE,"E1598"),sQuery(id+"F0.wireOp",EDGE,"E1599"),sQuery(id+"F0.wireOp",EDGE,"E1600"),sQuery(id+"F0.wireOp",EDGE,"E1601"),sQuery(id+"F0.wireOp",EDGE,"E1602"),sQuery(id+"F0.wireOp",EDGE,"E1603"),sQuery(id+"F0.wireOp",EDGE,"E1604"),sQuery(id+"F0.wireOp",EDGE,"E1605"),sQuery(id+"F0.wireOp",EDGE,"E1606"),sQuery(id+"F0.wireOp",EDGE,"E1607"),sQuery(id+"F0.wireOp",EDGE,"E1608"),sQuery(id+"F0.wireOp",EDGE,"E1609"),sQuery(id+"F0.wireOp",EDGE,"E1610"),sQuery(id+"F0.wireOp",EDGE,"E1610"),sQuery(id+"F0.wireOp",EDGE,"E1611"),sQuery(id+"F0.wireOp",EDGE,"E1612"),sQuery(id+"F0.wireOp",EDGE,"E1613"),sQuery(id+"F0.wireOp",EDGE,"E1614"),sQuery(id+"F0.wireOp",EDGE,"E1615"),sQuery(id+"F0.wireOp",EDGE,"E1616"),sQuery(id+"F0.wireOp",EDGE,"E1617"),sQuery(id+"F0.wireOp",EDGE,"E1618"),sQuery(id+"F0.wireOp",EDGE,"E1619"),sQuery(id+"F0.wireOp",EDGE,"E1620"),sQuery(id+"F0.wireOp",EDGE,"E1621"),sQuery(id+"F0.wireOp",EDGE,"E1622"),sQuery(id+"F0.wireOp",EDGE,"E1623"),sQuery(id+"F0.wireOp",EDGE,"E1624"),sQuery(id+"F0.wireOp",EDGE,"E1625"),sQuery(id+"F0.wireOp",EDGE,"E1625"),sQuery(id+"F0.wireOp",EDGE,"E1626"),sQuery(id+"F0.wireOp",EDGE,"E1627"),sQuery(id+"F0.wireOp",EDGE,"E1628"),sQuery(id+"F0.wireOp",EDGE,"E1629"),sQuery(id+"F0.wireOp",EDGE,"E1630"),sQuery(id+"F0.wireOp",EDGE,"E1631"),sQuery(id+"F0.wireOp",EDGE,"E1632"),sQuery(id+"F0.wireOp",EDGE,"E1633"),sQuery(id+"F0.wireOp",EDGE,"E1634"),sQuery(id+"F0.wireOp",EDGE,"E1635"),sQuery(id+"F0.wireOp",EDGE,"E1636"),sQuery(id+"F0.wireOp",EDGE,"E1637"),sQuery(id+"F0.wireOp",EDGE,"E1637"),sQuery(id+"F0.wireOp",EDGE,"E1638"),sQuery(id+"F0.wireOp",EDGE,"E1639"),sQuery(id+"F0.wireOp",EDGE,"E1640"),sQuery(id+"F0.wireOp",EDGE,"E1641"),sQuery(id+"F0.wireOp",EDGE,"E1642"),sQuery(id+"F0.wireOp",EDGE,"E1643"),sQuery(id+"F0.wireOp",EDGE,"E1644"),sQuery(id+"F0.wireOp",EDGE,"E1645"),sQuery(id+"F0.wireOp",EDGE,"E1646"),sQuery(id+"F0.wireOp",EDGE,"E1647"),sQuery(id+"F0.wireOp",EDGE,"E1648"),sQuery(id+"F0.wireOp",EDGE,"E1649"),sQuery(id+"F0.wireOp",EDGE,"E1650"),sQuery(id+"F0.wireOp",EDGE,"E1651"),sQuery(id+"F0.wireOp",EDGE,"E1652"),sQuery(id+"F0.wireOp",EDGE,"E1653"),sQuery(id+"F0.wireOp",EDGE,"E1654"),sQuery(id+"F0.wireOp",EDGE,"E1655"),sQuery(id+"F0.wireOp",EDGE,"E1656"),sQuery(id+"F0.wireOp",EDGE,"E1657"),sQuery(id+"F0.wireOp",EDGE,"E1658"),sQuery(id+"F0.wireOp",EDGE,"E1658"),sQuery(id+"F0.wireOp",EDGE,"E1659"),sQuery(id+"F0.wireOp",EDGE,"E1660"),sQuery(id+"F0.wireOp",EDGE,"E1661"),sQuery(id+"F0.wireOp",EDGE,"E1662"),sQuery(id+"F0.wireOp",EDGE,"E1663"),sQuery(id+"F0.wireOp",EDGE,"E1664"),sQuery(id+"F0.wireOp",EDGE,"E1665"),sQuery(id+"F0.wireOp",EDGE,"E1666"),sQuery(id+"F0.wireOp",EDGE,"E1667"),sQuery(id+"F0.wireOp",EDGE,"E1668"),sQuery(id+"F0.wireOp",EDGE,"E1669"),sQuery(id+"F0.wireOp",EDGE,"E1670"),sQuery(id+"F0.wireOp",EDGE,"E1671"),sQuery(id+"F0.wireOp",EDGE,"E1672"),sQuery(id+"F0.wireOp",EDGE,"E1673"),sQuery(id+"F0.wireOp",EDGE,"E1674"),sQuery(id+"F0.wireOp",EDGE,"E1675"),sQuery(id+"F0.wireOp",EDGE,"E1676"),sQuery(id+"F0.wireOp",EDGE,"E1677"),sQuery(id+"F0.wireOp",EDGE,"E1678"),sQuery(id+"F0.wireOp",EDGE,"E1679"),sQuery(id+"F0.wireOp",EDGE,"E1680"),sQuery(id+"F0.wireOp",EDGE,"E1681"),sQuery(id+"F0.wireOp",EDGE,"E1682"),sQuery(id+"F0.wireOp",EDGE,"E1683"),sQuery(id+"F0.wireOp",EDGE,"E1684"),sQuery(id+"F0.wireOp",EDGE,"E1685"),sQuery(id+"F0.wireOp",EDGE,"E1686"),sQuery(id+"F0.wireOp",EDGE,"E1687"),sQuery(id+"F0.wireOp",EDGE,"E1688"),sQuery(id+"F0.wireOp",EDGE,"E1689"),sQuery(id+"F0.wireOp",EDGE,"E1690"),sQuery(id+"F0.wireOp",EDGE,"E1691"),sQuery(id+"F0.wireOp",EDGE,"E1692"),sQuery(id+"F0.wireOp",EDGE,"E1693"),sQuery(id+"F0.wireOp",EDGE,"E1694"),sQuery(id+"F0.wireOp",EDGE,"E1695"),sQuery(id+"F0.wireOp",EDGE,"E1696"),sQuery(id+"F0.wireOp",EDGE,"E1697"),sQuery(id+"F0.wireOp",EDGE,"E1698"),sQuery(id+"F0.wireOp",EDGE,"E1699"),sQuery(id+"F0.wireOp",EDGE,"E1700"),sQuery(id+"F0.wireOp",EDGE,"E1701"),sQuery(id+"F0.wireOp",EDGE,"E1702"),sQuery(id+"F0.wireOp",EDGE,"E1703"),sQuery(id+"F0.wireOp",EDGE,"E1704"),sQuery(id+"F0.wireOp",EDGE,"E1705"),sQuery(id+"F0.wireOp",EDGE,"E1706"),sQuery(id+"F0.wireOp",EDGE,"E1707"),sQuery(id+"F0.wireOp",EDGE,"E1708"),sQuery(id+"F0.wireOp",EDGE,"E1709"),sQuery(id+"F0.wireOp",EDGE,"E1710"),sQuery(id+"F0.wireOp",EDGE,"E1711"),sQuery(id+"F0.wireOp",EDGE,"E1712"),sQuery(id+"F0.wireOp",EDGE,"E1713"),sQuery(id+"F0.wireOp",EDGE,"E1714"),sQuery(id+"F0.wireOp",EDGE,"E1715"),sQuery(id+"F0.wireOp",EDGE,"E1716"),sQuery(id+"F0.wireOp",EDGE,"E1717"),sQuery(id+"F0.wireOp",EDGE,"E1718"),sQuery(id+"F0.wireOp",EDGE,"E1719"),sQuery(id+"F0.wireOp",EDGE,"E1720"),sQuery(id+"F0.wireOp",EDGE,"E1721"),sQuery(id+"F0.wireOp",EDGE,"E1722"),sQuery(id+"F0.wireOp",EDGE,"E1723"),sQuery(id+"F0.wireOp",EDGE,"E1724"),sQuery(id+"F0.wireOp",EDGE,"E1725"),sQuery(id+"F0.wireOp",EDGE,"E1726"),sQuery(id+"F0.wireOp",EDGE,"E1727"),sQuery(id+"F0.wireOp",EDGE,"E1728"),sQuery(id+"F0.wireOp",EDGE,"E1729"),sQuery(id+"F0.wireOp",EDGE,"E1730"),sQuery(id+"F0.wireOp",EDGE,"E1731"),sQuery(id+"F0.wireOp",EDGE,"E1732"),sQuery(id+"F0.wireOp",EDGE,"E1733"),sQuery(id+"F0.wireOp",EDGE,"E1733"),sQuery(id+"F0.wireOp",EDGE,"E1734"),sQuery(id+"F0.wireOp",EDGE,"E1735"),sQuery(id+"F0.wireOp",EDGE,"E1736"),sQuery(id+"F0.wireOp",EDGE,"E1737"),sQuery(id+"F0.wireOp",EDGE,"E1738"),sQuery(id+"F0.wireOp",EDGE,"E1738"),sQuery(id+"F0.wireOp",EDGE,"E1739"),sQuery(id+"F0.wireOp",EDGE,"E1740"),sQuery(id+"F0.wireOp",EDGE,"E1741"),sQuery(id+"F0.wireOp",EDGE,"E1742"),sQuery(id+"F0.wireOp",EDGE,"E1743"),sQuery(id+"F0.wireOp",EDGE,"E1744"),sQuery(id+"F0.wireOp",EDGE,"E1745"),sQuery(id+"F0.wireOp",EDGE,"E1746"),sQuery(id+"F0.wireOp",EDGE,"E1746"),sQuery(id+"F0.wireOp",EDGE,"E1747"),sQuery(id+"F0.wireOp",EDGE,"E1748"),sQuery(id+"F0.wireOp",EDGE,"E1748"),sQuery(id+"F0.wireOp",EDGE,"E1749"),sQuery(id+"F0.wireOp",EDGE,"E1750"),sQuery(id+"F0.wireOp",EDGE,"E1751"),sQuery(id+"F0.wireOp",EDGE,"E1751"),sQuery(id+"F0.wireOp",EDGE,"E1752"),sQuery(id+"F0.wireOp",EDGE,"E1753"),sQuery(id+"F0.wireOp",EDGE,"E1754"),sQuery(id+"F0.wireOp",EDGE,"E1755"),sQuery(id+"F0.wireOp",EDGE,"E1756"),sQuery(id+"F0.wireOp",EDGE,"E1757"),sQuery(id+"F0.wireOp",EDGE,"E1758"),sQuery(id+"F0.wireOp",EDGE,"E1759"),sQuery(id+"F0.wireOp",EDGE,"E1760"),sQuery(id+"F0.wireOp",EDGE,"E1761"),sQuery(id+"F0.wireOp",EDGE,"E1762"),sQuery(id+"F0.wireOp",EDGE,"E1763"),sQuery(id+"F0.wireOp",EDGE,"E1764"),sQuery(id+"F0.wireOp",EDGE,"E1765"),sQuery(id+"F0.wireOp",EDGE,"E1766"),sQuery(id+"F0.wireOp",EDGE,"E1766"),sQuery(id+"F0.wireOp",EDGE,"E1766"),sQuery(id+"F0.wireOp",EDGE,"E1767"),sQuery(id+"F0.wireOp",EDGE,"E1768"),sQuery(id+"F0.wireOp",EDGE,"E1769"),sQuery(id+"F0.wireOp",EDGE,"E1770"),sQuery(id+"F0.wireOp",EDGE,"E1771"),sQuery(id+"F0.wireOp",EDGE,"E1772"),sQuery(id+"F0.wireOp",EDGE,"E1773"),sQuery(id+"F0.wireOp",EDGE,"E1774"),sQuery(id+"F0.wireOp",EDGE,"E1775"),sQuery(id+"F0.wireOp",EDGE,"E1776"),sQuery(id+"F0.wireOp",EDGE,"E1777"),sQuery(id+"F0.wireOp",EDGE,"E1778"),sQuery(id+"F0.wireOp",EDGE,"E1779"),sQuery(id+"F0.wireOp",EDGE,"E1780"),sQuery(id+"F0.wireOp",EDGE,"E1781"),sQuery(id+"F0.wireOp",EDGE,"E1782"),sQuery(id+"F0.wireOp",EDGE,"E1783"),sQuery(id+"F0.wireOp",EDGE,"E1784"),sQuery(id+"F0.wireOp",EDGE,"E1784"),sQuery(id+"F0.wireOp",EDGE,"E1784"),sQuery(id+"F0.wireOp",EDGE,"E1785"),sQuery(id+"F0.wireOp",EDGE,"E1786"),sQuery(id+"F0.wireOp",EDGE,"E1787"),sQuery(id+"F0.wireOp",EDGE,"E1788"),sQuery(id+"F0.wireOp",EDGE,"E1789"),sQuery(id+"F0.wireOp",EDGE,"E1790"),sQuery(id+"F0.wireOp",EDGE,"E1791"),sQuery(id+"F0.wireOp",EDGE,"E1792"),sQuery(id+"F0.wireOp",EDGE,"E1793"),sQuery(id+"F0.wireOp",EDGE,"E1794"),sQuery(id+"F0.wireOp",EDGE,"E1795"),sQuery(id+"F0.wireOp",EDGE,"E1796"),sQuery(id+"F0.wireOp",EDGE,"E1797"),sQuery(id+"F0.wireOp",EDGE,"E1798"),sQuery(id+"F0.wireOp",EDGE,"E1799"),sQuery(id+"F0.wireOp",EDGE,"E1800"),sQuery(id+"F0.wireOp",EDGE,"E1800"),sQuery(id+"F0.wireOp",EDGE,"E1801"),sQuery(id+"F0.wireOp",EDGE,"E1802"),sQuery(id+"F0.wireOp",EDGE,"E1803"),sQuery(id+"F0.wireOp",EDGE,"E1804"),sQuery(id+"F0.wireOp",EDGE,"E1805"),sQuery(id+"F0.wireOp",EDGE,"E1805"),sQuery(id+"F0.wireOp",EDGE,"E1806"),sQuery(id+"F0.wireOp",EDGE,"E1807"),sQuery(id+"F0.wireOp",EDGE,"E1808"),sQuery(id+"F0.wireOp",EDGE,"E1809"),sQuery(id+"F0.wireOp",EDGE,"E1810"),sQuery(id+"F0.wireOp",EDGE,"E1811"),sQuery(id+"F0.wireOp",EDGE,"E1812"),sQuery(id+"F0.wireOp",EDGE,"E1813"),sQuery(id+"F0.wireOp",EDGE,"E1814"),sQuery(id+"F0.wireOp",EDGE,"E1815"),sQuery(id+"F0.wireOp",EDGE,"E1816"),sQuery(id+"F0.wireOp",EDGE,"E1817"),sQuery(id+"F0.wireOp",EDGE,"E1818"),sQuery(id+"F0.wireOp",EDGE,"E1819"),sQuery(id+"F0.wireOp",EDGE,"E1820"),sQuery(id+"F0.wireOp",EDGE,"E1821"),sQuery(id+"F0.wireOp",EDGE,"E1822"),sQuery(id+"F0.wireOp",EDGE,"E1823"),sQuery(id+"F0.wireOp",EDGE,"E1824"),sQuery(id+"F0.wireOp",EDGE,"E1825"),sQuery(id+"F0.wireOp",EDGE,"E1826"),sQuery(id+"F0.wireOp",EDGE,"E1827"),sQuery(id+"F0.wireOp",EDGE,"E1828"),sQuery(id+"F0.wireOp",EDGE,"E1829"),sQuery(id+"F0.wireOp",EDGE,"E1830"),sQuery(id+"F0.wireOp",EDGE,"E1831"),sQuery(id+"F0.wireOp",EDGE,"E1832"),sQuery(id+"F0.wireOp",EDGE,"E1833"),sQuery(id+"F0.wireOp",EDGE,"E1834"),sQuery(id+"F0.wireOp",EDGE,"E1835"),sQuery(id+"F0.wireOp",EDGE,"E1836"),sQuery(id+"F0.wireOp",EDGE,"E1837"),sQuery(id+"F0.wireOp",EDGE,"E1838"),sQuery(id+"F0.wireOp",EDGE,"E1839"),sQuery(id+"F0.wireOp",EDGE,"E1840"),sQuery(id+"F0.wireOp",EDGE,"E1841"),sQuery(id+"F0.wireOp",EDGE,"E1842"),sQuery(id+"F0.wireOp",EDGE,"E1843"),sQuery(id+"F0.wireOp",EDGE,"E1844"),sQuery(id+"F0.wireOp",EDGE,"E1845"),sQuery(id+"F0.wireOp",EDGE,"E1846"),sQuery(id+"F0.wireOp",EDGE,"E1847"),sQuery(id+"F0.wireOp",EDGE,"E1848"),sQuery(id+"F0.wireOp",EDGE,"E1849"),sQuery(id+"F0.wireOp",EDGE,"E1850"),sQuery(id+"F0.wireOp",EDGE,"E1851"),sQuery(id+"F0.wireOp",EDGE,"E1852"),sQuery(id+"F0.wireOp",EDGE,"E1853"),sQuery(id+"F0.wireOp",EDGE,"E1854"),sQuery(id+"F0.wireOp",EDGE,"E1855"),sQuery(id+"F0.wireOp",EDGE,"E1856"),sQuery(id+"F0.wireOp",EDGE,"E1857"),sQuery(id+"F0.wireOp",EDGE,"E1858"),sQuery(id+"F0.wireOp",EDGE,"E1859"),sQuery(id+"F0.wireOp",EDGE,"E1860"),sQuery(id+"F0.wireOp",EDGE,"E1861"),sQuery(id+"F0.wireOp",EDGE,"E1862"),sQuery(id+"F0.wireOp",EDGE,"E1863"),sQuery(id+"F0.wireOp",EDGE,"E1864"),sQuery(id+"F0.wireOp",EDGE,"E1865"),sQuery(id+"F0.wireOp",EDGE,"E1866"),sQuery(id+"F0.wireOp",EDGE,"E1867"),sQuery(id+"F0.wireOp",EDGE,"E1868"),sQuery(id+"F0.wireOp",EDGE,"E1869"),sQuery(id+"F0.wireOp",EDGE,"E1870"),sQuery(id+"F0.wireOp",EDGE,"E1871"),sQuery(id+"F0.wireOp",EDGE,"E1872"),sQuery(id+"F0.wireOp",EDGE,"E1873"),sQuery(id+"F0.wireOp",EDGE,"E1874"),sQuery(id+"F0.wireOp",EDGE,"E1875"),sQuery(id+"F0.wireOp",EDGE,"E1876"),sQuery(id+"F0.wireOp",EDGE,"E1877"),sQuery(id+"F0.wireOp",EDGE,"E1878"),sQuery(id+"F0.wireOp",EDGE,"E1879"),sQuery(id+"F0.wireOp",EDGE,"E1880"),sQuery(id+"F0.wireOp",EDGE,"E1881"),sQuery(id+"F0.wireOp",EDGE,"E1882"),sQuery(id+"F0.wireOp",EDGE,"E1883"),sQuery(id+"F0.wireOp",EDGE,"E1884"),sQuery(id+"F0.wireOp",EDGE,"E1885"),sQuery(id+"F0.wireOp",EDGE,"E1886"),sQuery(id+"F0.wireOp",EDGE,"E1887"),sQuery(id+"F0.wireOp",EDGE,"E1888"),sQuery(id+"F0.wireOp",EDGE,"E1889"),sQuery(id+"F0.wireOp",EDGE,"E1890"),sQuery(id+"F0.wireOp",EDGE,"E1891"),sQuery(id+"F0.wireOp",EDGE,"E1892"),sQuery(id+"F0.wireOp",EDGE,"E1893"),sQuery(id+"F0.wireOp",EDGE,"E1894"),sQuery(id+"F0.wireOp",EDGE,"E1895"),sQuery(id+"F0.wireOp",EDGE,"E1896"),sQuery(id+"F0.wireOp",EDGE,"E1897"),sQuery(id+"F0.wireOp",EDGE,"E1898"),sQuery(id+"F0.wireOp",EDGE,"E1899"),sQuery(id+"F0.wireOp",EDGE,"E1900"),sQuery(id+"F0.wireOp",EDGE,"E1901"),sQuery(id+"F0.wireOp",EDGE,"E1902"),sQuery(id+"F0.wireOp",EDGE,"E1903"),sQuery(id+"F0.wireOp",EDGE,"E1904"),sQuery(id+"F0.wireOp",EDGE,"E1905"),sQuery(id+"F0.wireOp",EDGE,"E1906"),sQuery(id+"F0.wireOp",EDGE,"E1907"),sQuery(id+"F0.wireOp",EDGE,"E1908"),sQuery(id+"F0.wireOp",EDGE,"E1909"),sQuery(id+"F0.wireOp",EDGE,"E1910"),sQuery(id+"F0.wireOp",EDGE,"E1911"),sQuery(id+"F0.wireOp",EDGE,"E1912"),sQuery(id+"F0.wireOp",EDGE,"E1913"),sQuery(id+"F0.wireOp",EDGE,"E1914"),sQuery(id+"F0.wireOp",EDGE,"E1915"),sQuery(id+"F0.wireOp",EDGE,"E1916"),sQuery(id+"F0.wireOp",EDGE,"E1917"),sQuery(id+"F0.wireOp",EDGE,"E1918"),sQuery(id+"F0.wireOp",EDGE,"E1919"),sQuery(id+"F0.wireOp",EDGE,"E1920"),sQuery(id+"F0.wireOp",EDGE,"E1921"),sQuery(id+"F0.wireOp",EDGE,"E1922"),sQuery(id+"F0.wireOp",EDGE,"E1923"),sQuery(id+"F0.wireOp",EDGE,"E1924"),sQuery(id+"F0.wireOp",EDGE,"E1925"),sQuery(id+"F0.wireOp",EDGE,"E1926"),sQuery(id+"F0.wireOp",EDGE,"E1927"),sQuery(id+"F0.wireOp",EDGE,"E1928"),sQuery(id+"F0.wireOp",EDGE,"E1929"),sQuery(id+"F0.wireOp",EDGE,"E1930"),sQuery(id+"F0.wireOp",EDGE,"E1931"),sQuery(id+"F0.wireOp",EDGE,"E1932"),sQuery(id+"F0.wireOp",EDGE,"E1933"),sQuery(id+"F0.wireOp",EDGE,"E1934"),sQuery(id+"F0.wireOp",EDGE,"E1935"),sQuery(id+"F0.wireOp",EDGE,"E1936"),sQuery(id+"F0.wireOp",EDGE,"E1937"),sQuery(id+"F0.wireOp",EDGE,"E1938"),sQuery(id+"F0.wireOp",EDGE,"E1939"),sQuery(id+"F0.wireOp",EDGE,"E1940"),sQuery(id+"F0.wireOp",EDGE,"E1941"),sQuery(id+"F0.wireOp",EDGE,"E1942"),sQuery(id+"F0.wireOp",EDGE,"E1943"),sQuery(id+"F0.wireOp",EDGE,"E1944"),sQuery(id+"F0.wireOp",EDGE,"E1945"),sQuery(id+"F0.wireOp",EDGE,"E1946"),sQuery(id+"F0.wireOp",EDGE,"E1947"),sQuery(id+"F0.wireOp",EDGE,"E1948"),sQuery(id+"F0.wireOp",EDGE,"E1949"),sQuery(id+"F0.wireOp",EDGE,"E1950"),sQuery(id+"F0.wireOp",EDGE,"E1951"),sQuery(id+"F0.wireOp",EDGE,"E1952"),sQuery(id+"F0.wireOp",EDGE,"E1953"),sQuery(id+"F0.wireOp",EDGE,"E1954"),sQuery(id+"F0.wireOp",EDGE,"E1955"),sQuery(id+"F0.wireOp",EDGE,"E1956"),sQuery(id+"F0.wireOp",EDGE,"E1957"),sQuery(id+"F0.wireOp",EDGE,"E1958"),sQuery(id+"F0.wireOp",EDGE,"E1959"),sQuery(id+"F0.wireOp",EDGE,"E1960"),sQuery(id+"F0.wireOp",EDGE,"E1961"),sQuery(id+"F0.wireOp",EDGE,"E1962"),sQuery(id+"F0.wireOp",EDGE,"E1963"),sQuery(id+"F0.wireOp",EDGE,"E1964"),sQuery(id+"F0.wireOp",EDGE,"E1965"),sQuery(id+"F0.wireOp",EDGE,"E1966"),sQuery(id+"F0.wireOp",EDGE,"E1967"),sQuery(id+"F0.wireOp",EDGE,"E1968"),sQuery(id+"F0.wireOp",EDGE,"E1969"),sQuery(id+"F0.wireOp",EDGE,"E1970"),sQuery(id+"F0.wireOp",EDGE,"E1971"),sQuery(id+"F0.wireOp",EDGE,"E1972"),sQuery(id+"F0.wireOp",EDGE,"E1973"),sQuery(id+"F0.wireOp",EDGE,"E1974"),sQuery(id+"F0.wireOp",EDGE,"E1975"),sQuery(id+"F0.wireOp",EDGE,"E1976"),sQuery(id+"F0.wireOp",EDGE,"E1977"),sQuery(id+"F0.wireOp",EDGE,"E1978"),sQuery(id+"F0.wireOp",EDGE,"E1979"),sQuery(id+"F0.wireOp",EDGE,"E1980"),sQuery(id+"F0.wireOp",EDGE,"E1981"),sQuery(id+"F0.wireOp",EDGE,"E1982"),sQuery(id+"F0.wireOp",EDGE,"E1983"),sQuery(id+"F0.wireOp",EDGE,"E1984"),sQuery(id+"F0.wireOp",EDGE,"E1985"),sQuery(id+"F0.wireOp",EDGE,"E1986"),sQuery(id+"F0.wireOp",EDGE,"E1987"),sQuery(id+"F0.wireOp",EDGE,"E1988"),sQuery(id+"F0.wireOp",EDGE,"E1989"),sQuery(id+"F0.wireOp",EDGE,"E1990"),sQuery(id+"F0.wireOp",EDGE,"E1991"),sQuery(id+"F0.wireOp",EDGE,"E1992"),sQuery(id+"F0.wireOp",EDGE,"E1993"),sQuery(id+"F0.wireOp",EDGE,"E1994"),sQuery(id+"F0.wireOp",EDGE,"E1995"),sQuery(id+"F0.wireOp",EDGE,"E1996"),sQuery(id+"F0.wireOp",EDGE,"E1997"),sQuery(id+"F0.wireOp",EDGE,"E1998"),sQuery(id+"F0.wireOp",EDGE,"E1999"),sQuery(id+"F0.wireOp",EDGE,"E2000"),sQuery(id+"F0.wireOp",EDGE,"E2001"),sQuery(id+"F0.wireOp",EDGE,"E2002"),sQuery(id+"F0.wireOp",EDGE,"E2003"),sQuery(id+"F0.wireOp",EDGE,"E2004"),sQuery(id+"F0.wireOp",EDGE,"E2005"),sQuery(id+"F0.wireOp",EDGE,"E2006"),sQuery(id+"F0.wireOp",EDGE,"E2007"),sQuery(id+"F0.wireOp",EDGE,"E2008"),sQuery(id+"F0.wireOp",EDGE,"E2009"),sQuery(id+"F0.wireOp",EDGE,"E2010"),sQuery(id+"F0.wireOp",EDGE,"E2011"),sQuery(id+"F0.wireOp",EDGE,"E2012"),sQuery(id+"F0.wireOp",EDGE,"E2013"),sQuery(id+"F0.wireOp",EDGE,"E2014"),sQuery(id+"F0.wireOp",EDGE,"E2015"),sQuery(id+"F0.wireOp",EDGE,"E2016"),sQuery(id+"F0.wireOp",EDGE,"E2017"),sQuery(id+"F0.wireOp",EDGE,"E2018"),sQuery(id+"F0.wireOp",EDGE,"E2019"),sQuery(id+"F0.wireOp",EDGE,"E2020"),sQuery(id+"F0.wireOp",EDGE,"E2021"),sQuery(id+"F0.wireOp",EDGE,"E2022"),sQuery(id+"F0.wireOp",EDGE,"E2023"),sQuery(id+"F0.wireOp",EDGE,"E2024"),sQuery(id+"F0.wireOp",EDGE,"E2025"),sQuery(id+"F0.wireOp",EDGE,"E2026"),sQuery(id+"F0.wireOp",EDGE,"E2027"),sQuery(id+"F0.wireOp",EDGE,"E2028"),sQuery(id+"F0.wireOp",EDGE,"E2029"),sQuery(id+"F0.wireOp",EDGE,"E2030"),sQuery(id+"F0.wireOp",EDGE,"E2031"),sQuery(id+"F0.wireOp",EDGE,"E2032"),sQuery(id+"F0.wireOp",EDGE,"E2033"),sQuery(id+"F0.wireOp",EDGE,"E2034"),sQuery(id+"F0.wireOp",EDGE,"E2035"),sQuery(id+"F0.wireOp",EDGE,"E2036"),sQuery(id+"F0.wireOp",EDGE,"E2037"),sQuery(id+"F0.wireOp",EDGE,"E2038"),sQuery(id+"F0.wireOp",EDGE,"E2039"),sQuery(id+"F0.wireOp",EDGE,"E2040"),sQuery(id+"F0.wireOp",EDGE,"E2041"),sQuery(id+"F0.wireOp",EDGE,"E2042"),sQuery(id+"F0.wireOp",EDGE,"E2043"),sQuery(id+"F0.wireOp",EDGE,"E2044"),sQuery(id+"F0.wireOp",EDGE,"E2045"),sQuery(id+"F0.wireOp",EDGE,"E2046"),sQuery(id+"F0.wireOp",EDGE,"E2047"),sQuery(id+"F0.wireOp",EDGE,"E2048"),sQuery(id+"F0.wireOp",EDGE,"E2049"),sQuery(id+"F0.wireOp",EDGE,"E2050"),sQuery(id+"F0.wireOp",EDGE,"E2051"),sQuery(id+"F0.wireOp",EDGE,"E2052"),sQuery(id+"F0.wireOp",EDGE,"E2053"),sQuery(id+"F0.wireOp",EDGE,"E2054"),sQuery(id+"F0.wireOp",EDGE,"E2055"),sQuery(id+"F0.wireOp",EDGE,"E2056"),sQuery(id+"F0.wireOp",EDGE,"E2057"),sQuery(id+"F0.wireOp",EDGE,"E2058"),sQuery(id+"F0.wireOp",EDGE,"E2059"),sQuery(id+"F0.wireOp",EDGE,"E2060"),sQuery(id+"F0.wireOp",EDGE,"E2061"),sQuery(id+"F0.wireOp",EDGE,"E2062"),sQuery(id+"F0.wireOp",EDGE,"E2063"),sQuery(id+"F0.wireOp",EDGE,"E2063"),sQuery(id+"F0.wireOp",EDGE,"E2063"),sQuery(id+"F0.wireOp",EDGE,"E2064"),sQuery(id+"F0.wireOp",EDGE,"E2065"),sQuery(id+"F0.wireOp",EDGE,"E2066"),sQuery(id+"F0.wireOp",EDGE,"E2067"),sQuery(id+"F0.wireOp",EDGE,"E2068"),sQuery(id+"F0.wireOp",EDGE,"E2069"),sQuery(id+"F0.wireOp",EDGE,"E2070"),sQuery(id+"F0.wireOp",EDGE,"E2071"),sQuery(id+"F0.wireOp",EDGE,"E2072"),sQuery(id+"F0.wireOp",EDGE,"E2073"),sQuery(id+"F0.wireOp",EDGE,"E2074"),sQuery(id+"F0.wireOp",EDGE,"E2075"),sQuery(id+"F0.wireOp",EDGE,"E2076"),sQuery(id+"F0.wireOp",EDGE,"E2077"),sQuery(id+"F0.wireOp",EDGE,"E2078"),sQuery(id+"F0.wireOp",EDGE,"E2079"),sQuery(id+"F0.wireOp",EDGE,"E2080"),sQuery(id+"F0.wireOp",EDGE,"E2081"),sQuery(id+"F0.wireOp",EDGE,"E2082"),sQuery(id+"F0.wireOp",EDGE,"E2083"),sQuery(id+"F0.wireOp",EDGE,"E2084"),sQuery(id+"F0.wireOp",EDGE,"E2085"),sQuery(id+"F0.wireOp",EDGE,"E2086"),sQuery(id+"F0.wireOp",EDGE,"E2087"),sQuery(id+"F0.wireOp",EDGE,"E2088"),sQuery(id+"F0.wireOp",EDGE,"E2089"),sQuery(id+"F0.wireOp",EDGE,"E2090"),sQuery(id+"F0.wireOp",EDGE,"E2091"),sQuery(id+"F0.wireOp",EDGE,"E2092"),sQuery(id+"F0.wireOp",EDGE,"E2093"),sQuery(id+"F0.wireOp",EDGE,"E2094"),sQuery(id+"F0.wireOp",EDGE,"E2095"),sQuery(id+"F0.wireOp",EDGE,"E2096"),sQuery(id+"F0.wireOp",EDGE,"E2097"),sQuery(id+"F0.wireOp",EDGE,"E2098"),sQuery(id+"F0.wireOp",EDGE,"E2099"),sQuery(id+"F0.wireOp",EDGE,"E2100"),sQuery(id+"F0.wireOp",EDGE,"E2101"),sQuery(id+"F0.wireOp",EDGE,"E2102"),sQuery(id+"F0.wireOp",EDGE,"E2103"),sQuery(id+"F0.wireOp",EDGE,"E2104"),sQuery(id+"F0.wireOp",EDGE,"E2105"),sQuery(id+"F0.wireOp",EDGE,"E2106"),sQuery(id+"F0.wireOp",EDGE,"E2107"),sQuery(id+"F0.wireOp",EDGE,"E2108"),sQuery(id+"F0.wireOp",EDGE,"E2109"),sQuery(id+"F0.wireOp",EDGE,"E2109"),sQuery(id+"F0.wireOp",EDGE,"E2110"),sQuery(id+"F0.wireOp",EDGE,"E2111"),sQuery(id+"F0.wireOp",EDGE,"E2112"),sQuery(id+"F0.wireOp",EDGE,"E2113"),sQuery(id+"F0.wireOp",EDGE,"E2114"),sQuery(id+"F0.wireOp",EDGE,"E2115"),sQuery(id+"F0.wireOp",EDGE,"E2116"),sQuery(id+"F0.wireOp",EDGE,"E2117"),sQuery(id+"F0.wireOp",EDGE,"E2118"),sQuery(id+"F0.wireOp",EDGE,"E2119"),sQuery(id+"F0.wireOp",EDGE,"E2120"),sQuery(id+"F0.wireOp",EDGE,"E2121"),sQuery(id+"F0.wireOp",EDGE,"E2122"),sQuery(id+"F0.wireOp",EDGE,"E2123"),sQuery(id+"F0.wireOp",EDGE,"E2124"),sQuery(id+"F0.wireOp",EDGE,"E2125"),sQuery(id+"F0.wireOp",EDGE,"E2126"),sQuery(id+"F0.wireOp",EDGE,"E2127"),sQuery(id+"F0.wireOp",EDGE,"E2128"),sQuery(id+"F0.wireOp",EDGE,"E2129"),sQuery(id+"F0.wireOp",EDGE,"E2130"),sQuery(id+"F0.wireOp",EDGE,"E2131"),sQuery(id+"F0.wireOp",EDGE,"E2132"),sQuery(id+"F0.wireOp",EDGE,"E2133"),sQuery(id+"F0.wireOp",EDGE,"E2134"),sQuery(id+"F0.wireOp",EDGE,"E2135"),sQuery(id+"F0.wireOp",EDGE,"E2136"),sQuery(id+"F0.wireOp",EDGE,"E2137"),sQuery(id+"F0.wireOp",EDGE,"E2138"),sQuery(id+"F0.wireOp",EDGE,"E2139"),sQuery(id+"F0.wireOp",EDGE,"E2140"),sQuery(id+"F0.wireOp",EDGE,"E2141"),sQuery(id+"F0.wireOp",EDGE,"E2142"),sQuery(id+"F0.wireOp",EDGE,"E2143"),sQuery(id+"F0.wireOp",EDGE,"E2144"),sQuery(id+"F0.wireOp",EDGE,"E2145"),sQuery(id+"F0.wireOp",EDGE,"E2146"),sQuery(id+"F0.wireOp",EDGE,"E2147"),sQuery(id+"F0.wireOp",EDGE,"E2148"),sQuery(id+"F0.wireOp",EDGE,"E2149"),sQuery(id+"F0.wireOp",EDGE,"E2150"),sQuery(id+"F0.wireOp",EDGE,"E2151"),sQuery(id+"F0.wireOp",EDGE,"E2152"),sQuery(id+"F0.wireOp",EDGE,"E2153"),sQuery(id+"F0.wireOp",EDGE,"E2154"),sQuery(id+"F0.wireOp",EDGE,"E2155"),sQuery(id+"F0.wireOp",EDGE,"E2156"),sQuery(id+"F0.wireOp",EDGE,"E2157"),sQuery(id+"F0.wireOp",EDGE,"E2158"),sQuery(id+"F0.wireOp",EDGE,"E2159"),sQuery(id+"F0.wireOp",EDGE,"E2160"),sQuery(id+"F0.wireOp",EDGE,"E2161"),sQuery(id+"F0.wireOp",EDGE,"E2162"),sQuery(id+"F0.wireOp",EDGE,"E2163"),sQuery(id+"F0.wireOp",EDGE,"E2164"),sQuery(id+"F0.wireOp",EDGE,"E2165"),sQuery(id+"F0.wireOp",EDGE,"E2166"),sQuery(id+"F0.wireOp",EDGE,"E2167"),sQuery(id+"F0.wireOp",EDGE,"E2168"),sQuery(id+"F0.wireOp",EDGE,"E2169"),sQuery(id+"F0.wireOp",EDGE,"E2170"),sQuery(id+"F0.wireOp",EDGE,"E2171"),sQuery(id+"F0.wireOp",EDGE,"E2172"),sQuery(id+"F0.wireOp",EDGE,"E2173"),sQuery(id+"F0.wireOp",EDGE,"E2174"),sQuery(id+"F0.wireOp",EDGE,"E2175"),sQuery(id+"F0.wireOp",EDGE,"E2176"),sQuery(id+"F0.wireOp",EDGE,"E2177"),sQuery(id+"F0.wireOp",EDGE,"E2178"),sQuery(id+"F0.wireOp",EDGE,"E2179"),sQuery(id+"F0.wireOp",EDGE,"E2180"),sQuery(id+"F0.wireOp",EDGE,"E2181"),sQuery(id+"F0.wireOp",EDGE,"E2182"),sQuery(id+"F0.wireOp",EDGE,"E2183"),sQuery(id+"F0.wireOp",EDGE,"E2184"),sQuery(id+"F0.wireOp",EDGE,"E2185"),sQuery(id+"F0.wireOp",EDGE,"E2186"),sQuery(id+"F0.wireOp",EDGE,"E2187"),sQuery(id+"F0.wireOp",EDGE,"E2188"),sQuery(id+"F0.wireOp",EDGE,"E2189"),sQuery(id+"F0.wireOp",EDGE,"E2190"),sQuery(id+"F0.wireOp",EDGE,"E2191"),sQuery(id+"F0.wireOp",EDGE,"E2192"),sQuery(id+"F0.wireOp",EDGE,"E2193"),sQuery(id+"F0.wireOp",EDGE,"E2194"),sQuery(id+"F0.wireOp",EDGE,"E2195"),sQuery(id+"F0.wireOp",EDGE,"E2196"),sQuery(id+"F0.wireOp",EDGE,"E2197"),sQuery(id+"F0.wireOp",EDGE,"E2198"),sQuery(id+"F0.wireOp",EDGE,"E2199"),sQuery(id+"F0.wireOp",EDGE,"E2200"),sQuery(id+"F0.wireOp",EDGE,"E2201"),sQuery(id+"F0.wireOp",EDGE,"E2202"),sQuery(id+"F0.wireOp",EDGE,"E2203"),sQuery(id+"F0.wireOp",EDGE,"E2204"),sQuery(id+"F0.wireOp",EDGE,"E2205"),sQuery(id+"F0.wireOp",EDGE,"E2206"),sQuery(id+"F0.wireOp",EDGE,"E2207"),sQuery(id+"F0.wireOp",EDGE,"E2208"),sQuery(id+"F0.wireOp",EDGE,"E2209"),sQuery(id+"F0.wireOp",EDGE,"E2210"),sQuery(id+"F0.wireOp",EDGE,"E2211"),sQuery(id+"F0.wireOp",EDGE,"E2212"),sQuery(id+"F0.wireOp",EDGE,"E2213"),sQuery(id+"F0.wireOp",EDGE,"E2214"),sQuery(id+"F0.wireOp",EDGE,"E2214"),sQuery(id+"F0.wireOp",EDGE,"E2215"),sQuery(id+"F0.wireOp",EDGE,"E2216"),sQuery(id+"F0.wireOp",EDGE,"E2217"),sQuery(id+"F0.wireOp",EDGE,"E2218"),sQuery(id+"F0.wireOp",EDGE,"E2218"),sQuery(id+"F0.wireOp",EDGE,"E2219"),sQuery(id+"F0.wireOp",EDGE,"E2220"),sQuery(id+"F0.wireOp",EDGE,"E2221"),sQuery(id+"F0.wireOp",EDGE,"E2222"),sQuery(id+"F0.wireOp",EDGE,"E2223"),sQuery(id+"F0.wireOp",EDGE,"E2224"),sQuery(id+"F0.wireOp",EDGE,"E2224"),sQuery(id+"F0.wireOp",EDGE,"E2225"),sQuery(id+"F0.wireOp",EDGE,"E2226"),sQuery(id+"F0.wireOp",EDGE,"E2227"),sQuery(id+"F0.wireOp",EDGE,"E2227"),sQuery(id+"F0.wireOp",EDGE,"E2227"),sQuery(id+"F0.wireOp",EDGE,"E2228"),sQuery(id+"F0.wireOp",EDGE,"E2229"),sQuery(id+"F0.wireOp",EDGE,"E2230"),sQuery(id+"F0.wireOp",EDGE,"E2230"),sQuery(id+"F0.wireOp",EDGE,"E2231"),sQuery(id+"F0.wireOp",EDGE,"E2232"),sQuery(id+"F0.wireOp",EDGE,"E2232"),sQuery(id+"F0.wireOp",EDGE,"E2233"),sQuery(id+"F0.wireOp",EDGE,"E2234"),sQuery(id+"F0.wireOp",EDGE,"E2234"),sQuery(id+"F0.wireOp",EDGE,"E2234"),sQuery(id+"F0.wireOp",EDGE,"E2234"),sQuery(id+"F0.wireOp",EDGE,"E2235"),sQuery(id+"F0.wireOp",EDGE,"E2236"),sQuery(id+"F0.wireOp",EDGE,"E2237"),sQuery(id+"F0.wireOp",EDGE,"E2238"),sQuery(id+"F0.wireOp",EDGE,"E2238"),sQuery(id+"F0.wireOp",EDGE,"E2239"),sQuery(id+"F0.wireOp",EDGE,"E2240"),sQuery(id+"F0.wireOp",EDGE,"E2241"),sQuery(id+"F0.wireOp",EDGE,"E2242"),sQuery(id+"F0.wireOp",EDGE,"E2243"),sQuery(id+"F0.wireOp",EDGE,"E2244"),sQuery(id+"F0.wireOp",EDGE,"E2245"),sQuery(id+"F0.wireOp",EDGE,"E2246"),sQuery(id+"F0.wireOp",EDGE,"E2247"),sQuery(id+"F0.wireOp",EDGE,"E2248"),sQuery(id+"F0.wireOp",EDGE,"E2248"),sQuery(id+"F0.wireOp",EDGE,"E2249"),sQuery(id+"F0.wireOp",EDGE,"E2250"),sQuery(id+"F0.wireOp",EDGE,"E2250"),sQuery(id+"F0.wireOp",EDGE,"E2250"),sQuery(id+"F0.wireOp",EDGE,"E2250"),sQuery(id+"F0.wireOp",EDGE,"E2251"),sQuery(id+"F0.wireOp",EDGE,"E2252"),sQuery(id+"F0.wireOp",EDGE,"E2253"),sQuery(id+"F0.wireOp",EDGE,"E2254"),sQuery(id+"F0.wireOp",EDGE,"E2255"),sQuery(id+"F0.wireOp",EDGE,"E2256"),sQuery(id+"F0.wireOp",EDGE,"E2257"),sQuery(id+"F0.wireOp",EDGE,"E2258"),sQuery(id+"F0.wireOp",EDGE,"E2259"),sQuery(id+"F0.wireOp",EDGE,"E2259"),sQuery(id+"F0.wireOp",EDGE,"E2259"),sQuery(id+"F0.wireOp",EDGE,"E2259"),sQuery(id+"F0.wireOp",EDGE,"E2259"),sQuery(id+"F0.wireOp",EDGE,"E2259"),sQuery(id+"F0.wireOp",EDGE,"E2260"),sQuery(id+"F0.wireOp",EDGE,"E2261"),sQuery(id+"F0.wireOp",EDGE,"E2262"),sQuery(id+"F0.wireOp",EDGE,"E2263"),sQuery(id+"F0.wireOp",EDGE,"E2264"),sQuery(id+"F0.wireOp",EDGE,"E2265"),sQuery(id+"F0.wireOp",EDGE,"E2266"),sQuery(id+"F0.wireOp",EDGE,"E2267"),sQuery(id+"F0.wireOp",EDGE,"E2268"),sQuery(id+"F0.wireOp",EDGE,"E2268"),sQuery(id+"F0.wireOp",EDGE,"E2269"),sQuery(id+"F0.wireOp",EDGE,"E2270"),sQuery(id+"F0.wireOp",EDGE,"E2271"),sQuery(id+"F0.wireOp",EDGE,"E2272"),sQuery(id+"F0.wireOp",EDGE,"E2273"),sQuery(id+"F0.wireOp",EDGE,"E2274"),sQuery(id+"F0.wireOp",EDGE,"E2275"),sQuery(id+"F0.wireOp",EDGE,"E2276"),sQuery(id+"F0.wireOp",EDGE,"E2277"),sQuery(id+"F0.wireOp",EDGE,"E2278"),sQuery(id+"F0.wireOp",EDGE,"E2279"),sQuery(id+"F0.wireOp",EDGE,"E2280"),sQuery(id+"F0.wireOp",EDGE,"E2281"),sQuery(id+"F0.wireOp",EDGE,"E2281"),sQuery(id+"F0.wireOp",EDGE,"E2282"),sQuery(id+"F0.wireOp",EDGE,"E2283"),sQuery(id+"F0.wireOp",EDGE,"E2284"),sQuery(id+"F0.wireOp",EDGE,"E2285"),sQuery(id+"F0.wireOp",EDGE,"E2286"),sQuery(id+"F0.wireOp",EDGE,"E2287"),sQuery(id+"F0.wireOp",EDGE,"E2288")])]});
            var Q1;
            Q1=makeQuery(id+"F1.opExtrude","SWEPT_BODY",BODY,{"disambiguationData":[OSD([sQuery(id+"F0.wireOp",EDGE,"E2289"),sQuery(id+"F0.wireOp",EDGE,"E2290"),sQuery(id+"F0.wireOp",EDGE,"E2291"),sQuery(id+"F0.wireOp",EDGE,"E2292"),sQuery(id+"F0.wireOp",EDGE,"E2293"),sQuery(id+"F0.wireOp",EDGE,"E2294"),sQuery(id+"F0.wireOp",EDGE,"E2295"),sQuery(id+"F0.wireOp",EDGE,"E2296"),sQuery(id+"F0.wireOp",EDGE,"E2297"),sQuery(id+"F0.wireOp",EDGE,"E2298"),sQuery(id+"F0.wireOp",EDGE,"E2299"),sQuery(id+"F0.wireOp",EDGE,"E2300"),sQuery(id+"F0.wireOp",EDGE,"E2301"),sQuery(id+"F0.wireOp",EDGE,"E2302"),sQuery(id+"F0.wireOp",EDGE,"E2303"),sQuery(id+"F0.wireOp",EDGE,"E2304"),sQuery(id+"F0.wireOp",EDGE,"E2305"),sQuery(id+"F0.wireOp",EDGE,"E2306"),sQuery(id+"F0.wireOp",EDGE,"E2307"),sQuery(id+"F0.wireOp",EDGE,"E2308"),sQuery(id+"F0.wireOp",EDGE,"E2309"),sQuery(id+"F0.wireOp",EDGE,"E2310"),sQuery(id+"F0.wireOp",EDGE,"E2311"),sQuery(id+"F0.wireOp",EDGE,"E2312"),sQuery(id+"F0.wireOp",EDGE,"E2313"),sQuery(id+"F0.wireOp",EDGE,"E2314"),sQuery(id+"F0.wireOp",EDGE,"E2315"),sQuery(id+"F0.wireOp",EDGE,"E2316"),sQuery(id+"F0.wireOp",EDGE,"E2317"),sQuery(id+"F0.wireOp",EDGE,"E2318"),sQuery(id+"F0.wireOp",EDGE,"E2319"),sQuery(id+"F0.wireOp",EDGE,"E2320"),sQuery(id+"F0.wireOp",EDGE,"E2321"),sQuery(id+"F0.wireOp",EDGE,"E2322"),sQuery(id+"F0.wireOp",EDGE,"E2323"),sQuery(id+"F0.wireOp",EDGE,"E2324"),sQuery(id+"F0.wireOp",EDGE,"E2325"),sQuery(id+"F0.wireOp",EDGE,"E2326"),sQuery(id+"F0.wireOp",EDGE,"E2327"),sQuery(id+"F0.wireOp",EDGE,"E2328"),sQuery(id+"F0.wireOp",EDGE,"E2329"),sQuery(id+"F0.wireOp",EDGE,"E2330"),sQuery(id+"F0.wireOp",EDGE,"E2331"),sQuery(id+"F0.wireOp",EDGE,"E2332"),sQuery(id+"F0.wireOp",EDGE,"E2333"),sQuery(id+"F0.wireOp",EDGE,"E2334"),sQuery(id+"F0.wireOp",EDGE,"E2335"),sQuery(id+"F0.wireOp",EDGE,"E2336"),sQuery(id+"F0.wireOp",EDGE,"E2337"),sQuery(id+"F0.wireOp",EDGE,"E2338"),sQuery(id+"F0.wireOp",EDGE,"E2338"),sQuery(id+"F0.wireOp",EDGE,"E2339"),sQuery(id+"F0.wireOp",EDGE,"E2340"),sQuery(id+"F0.wireOp",EDGE,"E2341"),sQuery(id+"F0.wireOp",EDGE,"E2342"),sQuery(id+"F0.wireOp",EDGE,"E2343"),sQuery(id+"F0.wireOp",EDGE,"E2344"),sQuery(id+"F0.wireOp",EDGE,"E2345"),sQuery(id+"F0.wireOp",EDGE,"E2346"),sQuery(id+"F0.wireOp",EDGE,"E2347"),sQuery(id+"F0.wireOp",EDGE,"E2348"),sQuery(id+"F0.wireOp",EDGE,"E2349"),sQuery(id+"F0.wireOp",EDGE,"E2350"),sQuery(id+"F0.wireOp",EDGE,"E2350"),sQuery(id+"F0.wireOp",EDGE,"E2351"),sQuery(id+"F0.wireOp",EDGE,"E2352"),sQuery(id+"F0.wireOp",EDGE,"E2353"),sQuery(id+"F0.wireOp",EDGE,"E2354"),sQuery(id+"F0.wireOp",EDGE,"E2355"),sQuery(id+"F0.wireOp",EDGE,"E2356"),sQuery(id+"F0.wireOp",EDGE,"E2357"),sQuery(id+"F0.wireOp",EDGE,"E2358"),sQuery(id+"F0.wireOp",EDGE,"E2359"),sQuery(id+"F0.wireOp",EDGE,"E2359"),sQuery(id+"F0.wireOp",EDGE,"E2360"),sQuery(id+"F0.wireOp",EDGE,"E2361"),sQuery(id+"F0.wireOp",EDGE,"E2362"),sQuery(id+"F0.wireOp",EDGE,"E2363"),sQuery(id+"F0.wireOp",EDGE,"E2364"),sQuery(id+"F0.wireOp",EDGE,"E2365"),sQuery(id+"F0.wireOp",EDGE,"E2366"),sQuery(id+"F0.wireOp",EDGE,"E2367"),sQuery(id+"F0.wireOp",EDGE,"E2368"),sQuery(id+"F0.wireOp",EDGE,"E2368"),sQuery(id+"F0.wireOp",EDGE,"E2368"),sQuery(id+"F0.wireOp",EDGE,"E2369"),sQuery(id+"F0.wireOp",EDGE,"E2370"),sQuery(id+"F0.wireOp",EDGE,"E2371"),sQuery(id+"F0.wireOp",EDGE,"E2371"),sQuery(id+"F0.wireOp",EDGE,"E2372"),sQuery(id+"F0.wireOp",EDGE,"E2373"),sQuery(id+"F0.wireOp",EDGE,"E2374"),sQuery(id+"F0.wireOp",EDGE,"E2375"),sQuery(id+"F0.wireOp",EDGE,"E2376"),sQuery(id+"F0.wireOp",EDGE,"E2377"),sQuery(id+"F0.wireOp",EDGE,"E2378"),sQuery(id+"F0.wireOp",EDGE,"E2379"),sQuery(id+"F0.wireOp",EDGE,"E2380"),sQuery(id+"F0.wireOp",EDGE,"E2381"),sQuery(id+"F0.wireOp",EDGE,"E2382"),sQuery(id+"F0.wireOp",EDGE,"E2383"),sQuery(id+"F0.wireOp",EDGE,"E2384"),sQuery(id+"F0.wireOp",EDGE,"E2385"),sQuery(id+"F0.wireOp",EDGE,"E2385"),sQuery(id+"F0.wireOp",EDGE,"E2386"),sQuery(id+"F0.wireOp",EDGE,"E2387"),sQuery(id+"F0.wireOp",EDGE,"E2388"),sQuery(id+"F0.wireOp",EDGE,"E2389"),sQuery(id+"F0.wireOp",EDGE,"E2390"),sQuery(id+"F0.wireOp",EDGE,"E2391"),sQuery(id+"F0.wireOp",EDGE,"E2392"),sQuery(id+"F0.wireOp",EDGE,"E2393"),sQuery(id+"F0.wireOp",EDGE,"E2394"),sQuery(id+"F0.wireOp",EDGE,"E2395"),sQuery(id+"F0.wireOp",EDGE,"E2396"),sQuery(id+"F0.wireOp",EDGE,"E2397"),sQuery(id+"F0.wireOp",EDGE,"E2398"),sQuery(id+"F0.wireOp",EDGE,"E2399"),sQuery(id+"F0.wireOp",EDGE,"E2400"),sQuery(id+"F0.wireOp",EDGE,"E2401"),sQuery(id+"F0.wireOp",EDGE,"E2402"),sQuery(id+"F0.wireOp",EDGE,"E2403"),sQuery(id+"F0.wireOp",EDGE,"E2404"),sQuery(id+"F0.wireOp",EDGE,"E2405"),sQuery(id+"F0.wireOp",EDGE,"E2406"),sQuery(id+"F0.wireOp",EDGE,"E2407"),sQuery(id+"F0.wireOp",EDGE,"E2408"),sQuery(id+"F0.wireOp",EDGE,"E2409"),sQuery(id+"F0.wireOp",EDGE,"E2409"),sQuery(id+"F0.wireOp",EDGE,"E2410"),sQuery(id+"F0.wireOp",EDGE,"E2411"),sQuery(id+"F0.wireOp",EDGE,"E2412"),sQuery(id+"F0.wireOp",EDGE,"E2413"),sQuery(id+"F0.wireOp",EDGE,"E2414"),sQuery(id+"F0.wireOp",EDGE,"E2415"),sQuery(id+"F0.wireOp",EDGE,"E2416"),sQuery(id+"F0.wireOp",EDGE,"E2417"),sQuery(id+"F0.wireOp",EDGE,"E2418"),sQuery(id+"F0.wireOp",EDGE,"E2419"),sQuery(id+"F0.wireOp",EDGE,"E2420"),sQuery(id+"F0.wireOp",EDGE,"E2421"),sQuery(id+"F0.wireOp",EDGE,"E2422"),sQuery(id+"F0.wireOp",EDGE,"E2423"),sQuery(id+"F0.wireOp",EDGE,"E2424"),sQuery(id+"F0.wireOp",EDGE,"E2425"),sQuery(id+"F0.wireOp",EDGE,"E2426"),sQuery(id+"F0.wireOp",EDGE,"E2426"),sQuery(id+"F0.wireOp",EDGE,"E2427"),sQuery(id+"F0.wireOp",EDGE,"E2428"),sQuery(id+"F0.wireOp",EDGE,"E2429"),sQuery(id+"F0.wireOp",EDGE,"E2430"),sQuery(id+"F0.wireOp",EDGE,"E2431"),sQuery(id+"F0.wireOp",EDGE,"E2432"),sQuery(id+"F0.wireOp",EDGE,"E2433"),sQuery(id+"F0.wireOp",EDGE,"E2434"),sQuery(id+"F0.wireOp",EDGE,"E2435"),sQuery(id+"F0.wireOp",EDGE,"E2436"),sQuery(id+"F0.wireOp",EDGE,"E2437"),sQuery(id+"F0.wireOp",EDGE,"E2438"),sQuery(id+"F0.wireOp",EDGE,"E2439"),sQuery(id+"F0.wireOp",EDGE,"E2440"),sQuery(id+"F0.wireOp",EDGE,"E2441"),sQuery(id+"F0.wireOp",EDGE,"E2442"),sQuery(id+"F0.wireOp",EDGE,"E2443"),sQuery(id+"F0.wireOp",EDGE,"E2444"),sQuery(id+"F0.wireOp",EDGE,"E2445"),sQuery(id+"F0.wireOp",EDGE,"E2446"),sQuery(id+"F0.wireOp",EDGE,"E2447"),sQuery(id+"F0.wireOp",EDGE,"E2448"),sQuery(id+"F0.wireOp",EDGE,"E2449"),sQuery(id+"F0.wireOp",EDGE,"E2450"),sQuery(id+"F0.wireOp",EDGE,"E2451"),sQuery(id+"F0.wireOp",EDGE,"E2452"),sQuery(id+"F0.wireOp",EDGE,"E2453"),sQuery(id+"F0.wireOp",EDGE,"E2454"),sQuery(id+"F0.wireOp",EDGE,"E2455"),sQuery(id+"F0.wireOp",EDGE,"E2456"),sQuery(id+"F0.wireOp",EDGE,"E2457"),sQuery(id+"F0.wireOp",EDGE,"E2458"),sQuery(id+"F0.wireOp",EDGE,"E2459"),sQuery(id+"F0.wireOp",EDGE,"E2460"),sQuery(id+"F0.wireOp",EDGE,"E2461"),sQuery(id+"F0.wireOp",EDGE,"E2462"),sQuery(id+"F0.wireOp",EDGE,"E2463"),sQuery(id+"F0.wireOp",EDGE,"E2464"),sQuery(id+"F0.wireOp",EDGE,"E2465"),sQuery(id+"F0.wireOp",EDGE,"E2466"),sQuery(id+"F0.wireOp",EDGE,"E2467"),sQuery(id+"F0.wireOp",EDGE,"E2468"),sQuery(id+"F0.wireOp",EDGE,"E2469"),sQuery(id+"F0.wireOp",EDGE,"E2470"),sQuery(id+"F0.wireOp",EDGE,"E2471"),sQuery(id+"F0.wireOp",EDGE,"E2472"),sQuery(id+"F0.wireOp",EDGE,"E2473"),sQuery(id+"F0.wireOp",EDGE,"E2474"),sQuery(id+"F0.wireOp",EDGE,"E2475"),sQuery(id+"F0.wireOp",EDGE,"E2476"),sQuery(id+"F0.wireOp",EDGE,"E2477"),sQuery(id+"F0.wireOp",EDGE,"E2478"),sQuery(id+"F0.wireOp",EDGE,"E2479"),sQuery(id+"F0.wireOp",EDGE,"E2480"),sQuery(id+"F0.wireOp",EDGE,"E2481"),sQuery(id+"F0.wireOp",EDGE,"E2482"),sQuery(id+"F0.wireOp",EDGE,"E2483"),sQuery(id+"F0.wireOp",EDGE,"E2484"),sQuery(id+"F0.wireOp",EDGE,"E2485"),sQuery(id+"F0.wireOp",EDGE,"E2486"),sQuery(id+"F0.wireOp",EDGE,"E2487"),sQuery(id+"F0.wireOp",EDGE,"E2488"),sQuery(id+"F0.wireOp",EDGE,"E2489"),sQuery(id+"F0.wireOp",EDGE,"E2490"),sQuery(id+"F0.wireOp",EDGE,"E2491"),sQuery(id+"F0.wireOp",EDGE,"E2492"),sQuery(id+"F0.wireOp",EDGE,"E2493"),sQuery(id+"F0.wireOp",EDGE,"E2494"),sQuery(id+"F0.wireOp",EDGE,"E2495"),sQuery(id+"F0.wireOp",EDGE,"E2496"),sQuery(id+"F0.wireOp",EDGE,"E2497"),sQuery(id+"F0.wireOp",EDGE,"E2498"),sQuery(id+"F0.wireOp",EDGE,"E2499"),sQuery(id+"F0.wireOp",EDGE,"E2500"),sQuery(id+"F0.wireOp",EDGE,"E2501"),sQuery(id+"F0.wireOp",EDGE,"E2502"),sQuery(id+"F0.wireOp",EDGE,"E2503"),sQuery(id+"F0.wireOp",EDGE,"E2504"),sQuery(id+"F0.wireOp",EDGE,"E2505"),sQuery(id+"F0.wireOp",EDGE,"E2506"),sQuery(id+"F0.wireOp",EDGE,"E2507"),sQuery(id+"F0.wireOp",EDGE,"E2508"),sQuery(id+"F0.wireOp",EDGE,"E2509"),sQuery(id+"F0.wireOp",EDGE,"E2510"),sQuery(id+"F0.wireOp",EDGE,"E2511"),sQuery(id+"F0.wireOp",EDGE,"E2512"),sQuery(id+"F0.wireOp",EDGE,"E2513"),sQuery(id+"F0.wireOp",EDGE,"E2514"),sQuery(id+"F0.wireOp",EDGE,"E2515"),sQuery(id+"F0.wireOp",EDGE,"E2516"),sQuery(id+"F0.wireOp",EDGE,"E2517"),sQuery(id+"F0.wireOp",EDGE,"E2518"),sQuery(id+"F0.wireOp",EDGE,"E2519"),sQuery(id+"F0.wireOp",EDGE,"E2520"),sQuery(id+"F0.wireOp",EDGE,"E2521"),sQuery(id+"F0.wireOp",EDGE,"E2522"),sQuery(id+"F0.wireOp",EDGE,"E2523"),sQuery(id+"F0.wireOp",EDGE,"E2524"),sQuery(id+"F0.wireOp",EDGE,"E2525"),sQuery(id+"F0.wireOp",EDGE,"E2526"),sQuery(id+"F0.wireOp",EDGE,"E2527"),sQuery(id+"F0.wireOp",EDGE,"E2528"),sQuery(id+"F0.wireOp",EDGE,"E2529"),sQuery(id+"F0.wireOp",EDGE,"E2530"),sQuery(id+"F0.wireOp",EDGE,"E2531"),sQuery(id+"F0.wireOp",EDGE,"E2532"),sQuery(id+"F0.wireOp",EDGE,"E2533"),sQuery(id+"F0.wireOp",EDGE,"E2534"),sQuery(id+"F0.wireOp",EDGE,"E2535"),sQuery(id+"F0.wireOp",EDGE,"E2536"),sQuery(id+"F0.wireOp",EDGE,"E2537"),sQuery(id+"F0.wireOp",EDGE,"E2538"),sQuery(id+"F0.wireOp",EDGE,"E2539"),sQuery(id+"F0.wireOp",EDGE,"E2540"),sQuery(id+"F0.wireOp",EDGE,"E2541"),sQuery(id+"F0.wireOp",EDGE,"E2542"),sQuery(id+"F0.wireOp",EDGE,"E2543"),sQuery(id+"F0.wireOp",EDGE,"E2544"),sQuery(id+"F0.wireOp",EDGE,"E2545"),sQuery(id+"F0.wireOp",EDGE,"E2546"),sQuery(id+"F0.wireOp",EDGE,"E2547"),sQuery(id+"F0.wireOp",EDGE,"E2548"),sQuery(id+"F0.wireOp",EDGE,"E2549"),sQuery(id+"F0.wireOp",EDGE,"E2550"),sQuery(id+"F0.wireOp",EDGE,"E2551"),sQuery(id+"F0.wireOp",EDGE,"E2552"),sQuery(id+"F0.wireOp",EDGE,"E2553"),sQuery(id+"F0.wireOp",EDGE,"E2554"),sQuery(id+"F0.wireOp",EDGE,"E2555"),sQuery(id+"F0.wireOp",EDGE,"E2556"),sQuery(id+"F0.wireOp",EDGE,"E2557"),sQuery(id+"F0.wireOp",EDGE,"E2558"),sQuery(id+"F0.wireOp",EDGE,"E2559"),sQuery(id+"F0.wireOp",EDGE,"E2560"),sQuery(id+"F0.wireOp",EDGE,"E2561"),sQuery(id+"F0.wireOp",EDGE,"E2562"),sQuery(id+"F0.wireOp",EDGE,"E2563"),sQuery(id+"F0.wireOp",EDGE,"E2564"),sQuery(id+"F0.wireOp",EDGE,"E2565"),sQuery(id+"F0.wireOp",EDGE,"E2566"),sQuery(id+"F0.wireOp",EDGE,"E2567"),sQuery(id+"F0.wireOp",EDGE,"E2568"),sQuery(id+"F0.wireOp",EDGE,"E2569"),sQuery(id+"F0.wireOp",EDGE,"E2570"),sQuery(id+"F0.wireOp",EDGE,"E2571"),sQuery(id+"F0.wireOp",EDGE,"E2572"),sQuery(id+"F0.wireOp",EDGE,"E2573"),sQuery(id+"F0.wireOp",EDGE,"E2574"),sQuery(id+"F0.wireOp",EDGE,"E2575"),sQuery(id+"F0.wireOp",EDGE,"E2576"),sQuery(id+"F0.wireOp",EDGE,"E2577"),sQuery(id+"F0.wireOp",EDGE,"E2578"),sQuery(id+"F0.wireOp",EDGE,"E2579"),sQuery(id+"F0.wireOp",EDGE,"E2580"),sQuery(id+"F0.wireOp",EDGE,"E2581"),sQuery(id+"F0.wireOp",EDGE,"E2582"),sQuery(id+"F0.wireOp",EDGE,"E2583"),sQuery(id+"F0.wireOp",EDGE,"E2584"),sQuery(id+"F0.wireOp",EDGE,"E2585"),sQuery(id+"F0.wireOp",EDGE,"E2586"),sQuery(id+"F0.wireOp",EDGE,"E2587"),sQuery(id+"F0.wireOp",EDGE,"E2588"),sQuery(id+"F0.wireOp",EDGE,"E2589"),sQuery(id+"F0.wireOp",EDGE,"E2590"),sQuery(id+"F0.wireOp",EDGE,"E2591"),sQuery(id+"F0.wireOp",EDGE,"E2592"),sQuery(id+"F0.wireOp",EDGE,"E2593"),sQuery(id+"F0.wireOp",EDGE,"E2594"),sQuery(id+"F0.wireOp",EDGE,"E2595"),sQuery(id+"F0.wireOp",EDGE,"E2596"),sQuery(id+"F0.wireOp",EDGE,"E2597"),sQuery(id+"F0.wireOp",EDGE,"E2598"),sQuery(id+"F0.wireOp",EDGE,"E2599"),sQuery(id+"F0.wireOp",EDGE,"E2600"),sQuery(id+"F0.wireOp",EDGE,"E2601"),sQuery(id+"F0.wireOp",EDGE,"E2602"),sQuery(id+"F0.wireOp",EDGE,"E2603"),sQuery(id+"F0.wireOp",EDGE,"E2604"),sQuery(id+"F0.wireOp",EDGE,"E2605"),sQuery(id+"F0.wireOp",EDGE,"E2606"),sQuery(id+"F0.wireOp",EDGE,"E2607"),sQuery(id+"F0.wireOp",EDGE,"E2608"),sQuery(id+"F0.wireOp",EDGE,"E2609"),sQuery(id+"F0.wireOp",EDGE,"E2610"),sQuery(id+"F0.wireOp",EDGE,"E2611"),sQuery(id+"F0.wireOp",EDGE,"E2612"),sQuery(id+"F0.wireOp",EDGE,"E2613"),sQuery(id+"F0.wireOp",EDGE,"E2614"),sQuery(id+"F0.wireOp",EDGE,"E2615"),sQuery(id+"F0.wireOp",EDGE,"E2616"),sQuery(id+"F0.wireOp",EDGE,"E2617"),sQuery(id+"F0.wireOp",EDGE,"E2618"),sQuery(id+"F0.wireOp",EDGE,"E2619"),sQuery(id+"F0.wireOp",EDGE,"E2620"),sQuery(id+"F0.wireOp",EDGE,"E2621"),sQuery(id+"F0.wireOp",EDGE,"E2622"),sQuery(id+"F0.wireOp",EDGE,"E2623"),sQuery(id+"F0.wireOp",EDGE,"E2624"),sQuery(id+"F0.wireOp",EDGE,"E2625"),sQuery(id+"F0.wireOp",EDGE,"E2626"),sQuery(id+"F0.wireOp",EDGE,"E2627"),sQuery(id+"F0.wireOp",EDGE,"E2628"),sQuery(id+"F0.wireOp",EDGE,"E2629"),sQuery(id+"F0.wireOp",EDGE,"E2630"),sQuery(id+"F0.wireOp",EDGE,"E2631"),sQuery(id+"F0.wireOp",EDGE,"E2632"),sQuery(id+"F0.wireOp",EDGE,"E2633"),sQuery(id+"F0.wireOp",EDGE,"E2634"),sQuery(id+"F0.wireOp",EDGE,"E2635"),sQuery(id+"F0.wireOp",EDGE,"E2636"),sQuery(id+"F0.wireOp",EDGE,"E2637"),sQuery(id+"F0.wireOp",EDGE,"E2638"),sQuery(id+"F0.wireOp",EDGE,"E2639"),sQuery(id+"F0.wireOp",EDGE,"E2640"),sQuery(id+"F0.wireOp",EDGE,"E2641"),sQuery(id+"F0.wireOp",EDGE,"E2642"),sQuery(id+"F0.wireOp",EDGE,"E2643"),sQuery(id+"F0.wireOp",EDGE,"E2644"),sQuery(id+"F0.wireOp",EDGE,"E2645"),sQuery(id+"F0.wireOp",EDGE,"E2646"),sQuery(id+"F0.wireOp",EDGE,"E2647"),sQuery(id+"F0.wireOp",EDGE,"E2648"),sQuery(id+"F0.wireOp",EDGE,"E2649"),sQuery(id+"F0.wireOp",EDGE,"E2650"),sQuery(id+"F0.wireOp",EDGE,"E2651"),sQuery(id+"F0.wireOp",EDGE,"E2652"),sQuery(id+"F0.wireOp",EDGE,"E2652"),sQuery(id+"F0.wireOp",EDGE,"E2653"),sQuery(id+"F0.wireOp",EDGE,"E2654"),sQuery(id+"F0.wireOp",EDGE,"E2655"),sQuery(id+"F0.wireOp",EDGE,"E2656"),sQuery(id+"F0.wireOp",EDGE,"E2657"),sQuery(id+"F0.wireOp",EDGE,"E2658"),sQuery(id+"F0.wireOp",EDGE,"E2659"),sQuery(id+"F0.wireOp",EDGE,"E2660"),sQuery(id+"F0.wireOp",EDGE,"E2660"),sQuery(id+"F0.wireOp",EDGE,"E2661"),sQuery(id+"F0.wireOp",EDGE,"E2662"),sQuery(id+"F0.wireOp",EDGE,"E2663"),sQuery(id+"F0.wireOp",EDGE,"E2664"),sQuery(id+"F0.wireOp",EDGE,"E2665"),sQuery(id+"F0.wireOp",EDGE,"E2666"),sQuery(id+"F0.wireOp",EDGE,"E2667"),sQuery(id+"F0.wireOp",EDGE,"E2668"),sQuery(id+"F0.wireOp",EDGE,"E2669"),sQuery(id+"F0.wireOp",EDGE,"E2670"),sQuery(id+"F0.wireOp",EDGE,"E2671"),sQuery(id+"F0.wireOp",EDGE,"E2672"),sQuery(id+"F0.wireOp",EDGE,"E2673"),sQuery(id+"F0.wireOp",EDGE,"E2674"),sQuery(id+"F0.wireOp",EDGE,"E2674"),sQuery(id+"F0.wireOp",EDGE,"E2675"),sQuery(id+"F0.wireOp",EDGE,"E2676"),sQuery(id+"F0.wireOp",EDGE,"E2677"),sQuery(id+"F0.wireOp",EDGE,"E2678"),sQuery(id+"F0.wireOp",EDGE,"E2679"),sQuery(id+"F0.wireOp",EDGE,"E2680"),sQuery(id+"F0.wireOp",EDGE,"E2681"),sQuery(id+"F0.wireOp",EDGE,"E2682"),sQuery(id+"F0.wireOp",EDGE,"E2683"),sQuery(id+"F0.wireOp",EDGE,"E2684"),sQuery(id+"F0.wireOp",EDGE,"E2685"),sQuery(id+"F0.wireOp",EDGE,"E2686"),sQuery(id+"F0.wireOp",EDGE,"E2687"),sQuery(id+"F0.wireOp",EDGE,"E2688"),sQuery(id+"F0.wireOp",EDGE,"E2689"),sQuery(id+"F0.wireOp",EDGE,"E2690"),sQuery(id+"F0.wireOp",EDGE,"E2691"),sQuery(id+"F0.wireOp",EDGE,"E2692"),sQuery(id+"F0.wireOp",EDGE,"E2693"),sQuery(id+"F0.wireOp",EDGE,"E2694"),sQuery(id+"F0.wireOp",EDGE,"E2695"),sQuery(id+"F0.wireOp",EDGE,"E2696"),sQuery(id+"F0.wireOp",EDGE,"E2697"),sQuery(id+"F0.wireOp",EDGE,"E2698"),sQuery(id+"F0.wireOp",EDGE,"E2699"),sQuery(id+"F0.wireOp",EDGE,"E2700"),sQuery(id+"F0.wireOp",EDGE,"E2701"),sQuery(id+"F0.wireOp",EDGE,"E2702"),sQuery(id+"F0.wireOp",EDGE,"E2703"),sQuery(id+"F0.wireOp",EDGE,"E2704"),sQuery(id+"F0.wireOp",EDGE,"E2705"),sQuery(id+"F0.wireOp",EDGE,"E2706"),sQuery(id+"F0.wireOp",EDGE,"E2707"),sQuery(id+"F0.wireOp",EDGE,"E2708"),sQuery(id+"F0.wireOp",EDGE,"E2709"),sQuery(id+"F0.wireOp",EDGE,"E2710"),sQuery(id+"F0.wireOp",EDGE,"E2711"),sQuery(id+"F0.wireOp",EDGE,"E2712"),sQuery(id+"F0.wireOp",EDGE,"E2713"),sQuery(id+"F0.wireOp",EDGE,"E2714"),sQuery(id+"F0.wireOp",EDGE,"E2715"),sQuery(id+"F0.wireOp",EDGE,"E2716"),sQuery(id+"F0.wireOp",EDGE,"E2717"),sQuery(id+"F0.wireOp",EDGE,"E2718"),sQuery(id+"F0.wireOp",EDGE,"E2719"),sQuery(id+"F0.wireOp",EDGE,"E2720"),sQuery(id+"F0.wireOp",EDGE,"E2721"),sQuery(id+"F0.wireOp",EDGE,"E2722"),sQuery(id+"F0.wireOp",EDGE,"E2723"),sQuery(id+"F0.wireOp",EDGE,"E2724"),sQuery(id+"F0.wireOp",EDGE,"E2725"),sQuery(id+"F0.wireOp",EDGE,"E2726"),sQuery(id+"F0.wireOp",EDGE,"E2727"),sQuery(id+"F0.wireOp",EDGE,"E2728"),sQuery(id+"F0.wireOp",EDGE,"E2729"),sQuery(id+"F0.wireOp",EDGE,"E2730"),sQuery(id+"F0.wireOp",EDGE,"E2731"),sQuery(id+"F0.wireOp",EDGE,"E2732"),sQuery(id+"F0.wireOp",EDGE,"E2733"),sQuery(id+"F0.wireOp",EDGE,"E2734"),sQuery(id+"F0.wireOp",EDGE,"E2735"),sQuery(id+"F0.wireOp",EDGE,"E2736"),sQuery(id+"F0.wireOp",EDGE,"E2737"),sQuery(id+"F0.wireOp",EDGE,"E2738"),sQuery(id+"F0.wireOp",EDGE,"E2739"),sQuery(id+"F0.wireOp",EDGE,"E2740"),sQuery(id+"F0.wireOp",EDGE,"E2741"),sQuery(id+"F0.wireOp",EDGE,"E2742"),sQuery(id+"F0.wireOp",EDGE,"E2743"),sQuery(id+"F0.wireOp",EDGE,"E2744"),sQuery(id+"F0.wireOp",EDGE,"E2745"),sQuery(id+"F0.wireOp",EDGE,"E2746"),sQuery(id+"F0.wireOp",EDGE,"E2747"),sQuery(id+"F0.wireOp",EDGE,"E2748"),sQuery(id+"F0.wireOp",EDGE,"E2749"),sQuery(id+"F0.wireOp",EDGE,"E2750"),sQuery(id+"F0.wireOp",EDGE,"E2751"),sQuery(id+"F0.wireOp",EDGE,"E2752"),sQuery(id+"F0.wireOp",EDGE,"E2753"),sQuery(id+"F0.wireOp",EDGE,"E2754"),sQuery(id+"F0.wireOp",EDGE,"E2755"),sQuery(id+"F0.wireOp",EDGE,"E2756"),sQuery(id+"F0.wireOp",EDGE,"E2757"),sQuery(id+"F0.wireOp",EDGE,"E2758"),sQuery(id+"F0.wireOp",EDGE,"E2759"),sQuery(id+"F0.wireOp",EDGE,"E2760"),sQuery(id+"F0.wireOp",EDGE,"E2761"),sQuery(id+"F0.wireOp",EDGE,"E2762"),sQuery(id+"F0.wireOp",EDGE,"E2763"),sQuery(id+"F0.wireOp",EDGE,"E2764"),sQuery(id+"F0.wireOp",EDGE,"E2765"),sQuery(id+"F0.wireOp",EDGE,"E2766"),sQuery(id+"F0.wireOp",EDGE,"E2767"),sQuery(id+"F0.wireOp",EDGE,"E2768"),sQuery(id+"F0.wireOp",EDGE,"E2769"),sQuery(id+"F0.wireOp",EDGE,"E2770"),sQuery(id+"F0.wireOp",EDGE,"E2771"),sQuery(id+"F0.wireOp",EDGE,"E2772"),sQuery(id+"F0.wireOp",EDGE,"E2773"),sQuery(id+"F0.wireOp",EDGE,"E2774"),sQuery(id+"F0.wireOp",EDGE,"E2775"),sQuery(id+"F0.wireOp",EDGE,"E2776"),sQuery(id+"F0.wireOp",EDGE,"E2777"),sQuery(id+"F0.wireOp",EDGE,"E2778"),sQuery(id+"F0.wireOp",EDGE,"E2779"),sQuery(id+"F0.wireOp",EDGE,"E2780"),sQuery(id+"F0.wireOp",EDGE,"E2781"),sQuery(id+"F0.wireOp",EDGE,"E2782"),sQuery(id+"F0.wireOp",EDGE,"E2783"),sQuery(id+"F0.wireOp",EDGE,"E2784"),sQuery(id+"F0.wireOp",EDGE,"E2785"),sQuery(id+"F0.wireOp",EDGE,"E2786"),sQuery(id+"F0.wireOp",EDGE,"E2787"),sQuery(id+"F0.wireOp",EDGE,"E2788"),sQuery(id+"F0.wireOp",EDGE,"E2789"),sQuery(id+"F0.wireOp",EDGE,"E2790"),sQuery(id+"F0.wireOp",EDGE,"E2791"),sQuery(id+"F0.wireOp",EDGE,"E2792"),sQuery(id+"F0.wireOp",EDGE,"E2793"),sQuery(id+"F0.wireOp",EDGE,"E2794"),sQuery(id+"F0.wireOp",EDGE,"E2795"),sQuery(id+"F0.wireOp",EDGE,"E2796"),sQuery(id+"F0.wireOp",EDGE,"E2797"),sQuery(id+"F0.wireOp",EDGE,"E2798"),sQuery(id+"F0.wireOp",EDGE,"E2799"),sQuery(id+"F0.wireOp",EDGE,"E2799"),sQuery(id+"F0.wireOp",EDGE,"E2799"),sQuery(id+"F0.wireOp",EDGE,"E2800"),sQuery(id+"F0.wireOp",EDGE,"E2801"),sQuery(id+"F0.wireOp",EDGE,"E2802"),sQuery(id+"F0.wireOp",EDGE,"E2803"),sQuery(id+"F0.wireOp",EDGE,"E2804"),sQuery(id+"F0.wireOp",EDGE,"E2804"),sQuery(id+"F0.wireOp",EDGE,"E2805"),sQuery(id+"F0.wireOp",EDGE,"E2806"),sQuery(id+"F0.wireOp",EDGE,"E2807"),sQuery(id+"F0.wireOp",EDGE,"E2808"),sQuery(id+"F0.wireOp",EDGE,"E2809"),sQuery(id+"F0.wireOp",EDGE,"E2810"),sQuery(id+"F0.wireOp",EDGE,"E2811"),sQuery(id+"F0.wireOp",EDGE,"E2812"),sQuery(id+"F0.wireOp",EDGE,"E2813"),sQuery(id+"F0.wireOp",EDGE,"E2814"),sQuery(id+"F0.wireOp",EDGE,"E2815"),sQuery(id+"F0.wireOp",EDGE,"E2816"),sQuery(id+"F0.wireOp",EDGE,"E2817"),sQuery(id+"F0.wireOp",EDGE,"E2818"),sQuery(id+"F0.wireOp",EDGE,"E2819"),sQuery(id+"F0.wireOp",EDGE,"E2820"),sQuery(id+"F0.wireOp",EDGE,"E2820"),sQuery(id+"F0.wireOp",EDGE,"E2821"),sQuery(id+"F0.wireOp",EDGE,"E2822"),sQuery(id+"F0.wireOp",EDGE,"E2823"),sQuery(id+"F0.wireOp",EDGE,"E2824"),sQuery(id+"F0.wireOp",EDGE,"E2825"),sQuery(id+"F0.wireOp",EDGE,"E2826"),sQuery(id+"F0.wireOp",EDGE,"E2827"),sQuery(id+"F0.wireOp",EDGE,"E2828"),sQuery(id+"F0.wireOp",EDGE,"E2829"),sQuery(id+"F0.wireOp",EDGE,"E2830"),sQuery(id+"F0.wireOp",EDGE,"E2831"),sQuery(id+"F0.wireOp",EDGE,"E2832"),sQuery(id+"F0.wireOp",EDGE,"E2832"),sQuery(id+"F0.wireOp",EDGE,"E2833"),sQuery(id+"F0.wireOp",EDGE,"E2834"),sQuery(id+"F0.wireOp",EDGE,"E2835"),sQuery(id+"F0.wireOp",EDGE,"E2836"),sQuery(id+"F0.wireOp",EDGE,"E2837"),sQuery(id+"F0.wireOp",EDGE,"E2837"),sQuery(id+"F0.wireOp",EDGE,"E2837"),sQuery(id+"F0.wireOp",EDGE,"E2837"),sQuery(id+"F0.wireOp",EDGE,"E2838"),sQuery(id+"F0.wireOp",EDGE,"E2839"),sQuery(id+"F0.wireOp",EDGE,"E2840"),sQuery(id+"F0.wireOp",EDGE,"E2841"),sQuery(id+"F0.wireOp",EDGE,"E2842"),sQuery(id+"F0.wireOp",EDGE,"E2843"),sQuery(id+"F0.wireOp",EDGE,"E2844"),sQuery(id+"F0.wireOp",EDGE,"E2845"),sQuery(id+"F0.wireOp",EDGE,"E2845"),sQuery(id+"F0.wireOp",EDGE,"E2846"),sQuery(id+"F0.wireOp",EDGE,"E2847"),sQuery(id+"F0.wireOp",EDGE,"E2847"),sQuery(id+"F0.wireOp",EDGE,"E2848"),sQuery(id+"F0.wireOp",EDGE,"E2849"),sQuery(id+"F0.wireOp",EDGE,"E2850"),sQuery(id+"F0.wireOp",EDGE,"E2851"),sQuery(id+"F0.wireOp",EDGE,"E2852"),sQuery(id+"F0.wireOp",EDGE,"E2853"),sQuery(id+"F0.wireOp",EDGE,"E2854"),sQuery(id+"F0.wireOp",EDGE,"E2855"),sQuery(id+"F0.wireOp",EDGE,"E2856"),sQuery(id+"F0.wireOp",EDGE,"E2857"),sQuery(id+"F0.wireOp",EDGE,"E2858"),sQuery(id+"F0.wireOp",EDGE,"E2859"),sQuery(id+"F0.wireOp",EDGE,"E2860"),sQuery(id+"F0.wireOp",EDGE,"E2861"),sQuery(id+"F0.wireOp",EDGE,"E2862"),sQuery(id+"F0.wireOp",EDGE,"E2863"),sQuery(id+"F0.wireOp",EDGE,"E2864"),sQuery(id+"F0.wireOp",EDGE,"E2865"),sQuery(id+"F0.wireOp",EDGE,"E2866"),sQuery(id+"F0.wireOp",EDGE,"E2867"),sQuery(id+"F0.wireOp",EDGE,"E2868"),sQuery(id+"F0.wireOp",EDGE,"E2869"),sQuery(id+"F0.wireOp",EDGE,"E2870"),sQuery(id+"F0.wireOp",EDGE,"E2871"),sQuery(id+"F0.wireOp",EDGE,"E2872"),sQuery(id+"F0.wireOp",EDGE,"E2873"),sQuery(id+"F0.wireOp",EDGE,"E2874"),sQuery(id+"F0.wireOp",EDGE,"E2875"),sQuery(id+"F0.wireOp",EDGE,"E2876"),sQuery(id+"F0.wireOp",EDGE,"E2877"),sQuery(id+"F0.wireOp",EDGE,"E2878"),sQuery(id+"F0.wireOp",EDGE,"E2879"),sQuery(id+"F0.wireOp",EDGE,"E2880"),sQuery(id+"F0.wireOp",EDGE,"E2881"),sQuery(id+"F0.wireOp",EDGE,"E2882"),sQuery(id+"F0.wireOp",EDGE,"E2883"),sQuery(id+"F0.wireOp",EDGE,"E2884"),sQuery(id+"F0.wireOp",EDGE,"E2885"),sQuery(id+"F0.wireOp",EDGE,"E2886"),sQuery(id+"F0.wireOp",EDGE,"E2887"),sQuery(id+"F0.wireOp",EDGE,"E2888"),sQuery(id+"F0.wireOp",EDGE,"E2889"),sQuery(id+"F0.wireOp",EDGE,"E2890"),sQuery(id+"F0.wireOp",EDGE,"E2891"),sQuery(id+"F0.wireOp",EDGE,"E2892"),sQuery(id+"F0.wireOp",EDGE,"E2893"),sQuery(id+"F0.wireOp",EDGE,"E2894"),sQuery(id+"F0.wireOp",EDGE,"E2895"),sQuery(id+"F0.wireOp",EDGE,"E2896"),sQuery(id+"F0.wireOp",EDGE,"E2897"),sQuery(id+"F0.wireOp",EDGE,"E2898"),sQuery(id+"F0.wireOp",EDGE,"E2899"),sQuery(id+"F0.wireOp",EDGE,"E2900"),sQuery(id+"F0.wireOp",EDGE,"E2901"),sQuery(id+"F0.wireOp",EDGE,"E2902"),sQuery(id+"F0.wireOp",EDGE,"E2903"),sQuery(id+"F0.wireOp",EDGE,"E2904"),sQuery(id+"F0.wireOp",EDGE,"E2905"),sQuery(id+"F0.wireOp",EDGE,"E2906"),sQuery(id+"F0.wireOp",EDGE,"E2907"),sQuery(id+"F0.wireOp",EDGE,"E2908"),sQuery(id+"F0.wireOp",EDGE,"E2909"),sQuery(id+"F0.wireOp",EDGE,"E2910"),sQuery(id+"F0.wireOp",EDGE,"E2911"),sQuery(id+"F0.wireOp",EDGE,"E2912"),sQuery(id+"F0.wireOp",EDGE,"E2913"),sQuery(id+"F0.wireOp",EDGE,"E2914"),sQuery(id+"F0.wireOp",EDGE,"E2915"),sQuery(id+"F0.wireOp",EDGE,"E2916"),sQuery(id+"F0.wireOp",EDGE,"E2917"),sQuery(id+"F0.wireOp",EDGE,"E2918"),sQuery(id+"F0.wireOp",EDGE,"E2919"),sQuery(id+"F0.wireOp",EDGE,"E2920"),sQuery(id+"F0.wireOp",EDGE,"E2921"),sQuery(id+"F0.wireOp",EDGE,"E2922"),sQuery(id+"F0.wireOp",EDGE,"E2923"),sQuery(id+"F0.wireOp",EDGE,"E2924"),sQuery(id+"F0.wireOp",EDGE,"E2925"),sQuery(id+"F0.wireOp",EDGE,"E2926"),sQuery(id+"F0.wireOp",EDGE,"E2927"),sQuery(id+"F0.wireOp",EDGE,"E2928"),sQuery(id+"F0.wireOp",EDGE,"E2929"),sQuery(id+"F0.wireOp",EDGE,"E2930"),sQuery(id+"F0.wireOp",EDGE,"E2931"),sQuery(id+"F0.wireOp",EDGE,"E2932"),sQuery(id+"F0.wireOp",EDGE,"E2933"),sQuery(id+"F0.wireOp",EDGE,"E2934"),sQuery(id+"F0.wireOp",EDGE,"E2935"),sQuery(id+"F0.wireOp",EDGE,"E2936"),sQuery(id+"F0.wireOp",EDGE,"E2937"),sQuery(id+"F0.wireOp",EDGE,"E2938"),sQuery(id+"F0.wireOp",EDGE,"E2939"),sQuery(id+"F0.wireOp",EDGE,"E2940"),sQuery(id+"F0.wireOp",EDGE,"E2941"),sQuery(id+"F0.wireOp",EDGE,"E2942"),sQuery(id+"F0.wireOp",EDGE,"E2943"),sQuery(id+"F0.wireOp",EDGE,"E2944"),sQuery(id+"F0.wireOp",EDGE,"E2945"),sQuery(id+"F0.wireOp",EDGE,"E2946"),sQuery(id+"F0.wireOp",EDGE,"E2947"),sQuery(id+"F0.wireOp",EDGE,"E2948"),sQuery(id+"F0.wireOp",EDGE,"E2949"),sQuery(id+"F0.wireOp",EDGE,"E2950"),sQuery(id+"F0.wireOp",EDGE,"E2951"),sQuery(id+"F0.wireOp",EDGE,"E2952"),sQuery(id+"F0.wireOp",EDGE,"E2953"),sQuery(id+"F0.wireOp",EDGE,"E2954"),sQuery(id+"F0.wireOp",EDGE,"E2955"),sQuery(id+"F0.wireOp",EDGE,"E2956"),sQuery(id+"F0.wireOp",EDGE,"E2957"),sQuery(id+"F0.wireOp",EDGE,"E2958"),sQuery(id+"F0.wireOp",EDGE,"E2959"),sQuery(id+"F0.wireOp",EDGE,"E2960"),sQuery(id+"F0.wireOp",EDGE,"E2961"),sQuery(id+"F0.wireOp",EDGE,"E2962"),sQuery(id+"F0.wireOp",EDGE,"E2963"),sQuery(id+"F0.wireOp",EDGE,"E2964"),sQuery(id+"F0.wireOp",EDGE,"E2965"),sQuery(id+"F0.wireOp",EDGE,"E2966"),sQuery(id+"F0.wireOp",EDGE,"E2967"),sQuery(id+"F0.wireOp",EDGE,"E2968"),sQuery(id+"F0.wireOp",EDGE,"E2969"),sQuery(id+"F0.wireOp",EDGE,"E2970"),sQuery(id+"F0.wireOp",EDGE,"E2971"),sQuery(id+"F0.wireOp",EDGE,"E2972"),sQuery(id+"F0.wireOp",EDGE,"E2973"),sQuery(id+"F0.wireOp",EDGE,"E2974"),sQuery(id+"F0.wireOp",EDGE,"E2975"),sQuery(id+"F0.wireOp",EDGE,"E2976"),sQuery(id+"F0.wireOp",EDGE,"E2977"),sQuery(id+"F0.wireOp",EDGE,"E2978"),sQuery(id+"F0.wireOp",EDGE,"E2979"),sQuery(id+"F0.wireOp",EDGE,"E2980"),sQuery(id+"F0.wireOp",EDGE,"E2981"),sQuery(id+"F0.wireOp",EDGE,"E2982"),sQuery(id+"F0.wireOp",EDGE,"E2983"),sQuery(id+"F0.wireOp",EDGE,"E2984"),sQuery(id+"F0.wireOp",EDGE,"E2985"),sQuery(id+"F0.wireOp",EDGE,"E2986"),sQuery(id+"F0.wireOp",EDGE,"E2987"),sQuery(id+"F0.wireOp",EDGE,"E2988"),sQuery(id+"F0.wireOp",EDGE,"E2989"),sQuery(id+"F0.wireOp",EDGE,"E2990"),sQuery(id+"F0.wireOp",EDGE,"E2991"),sQuery(id+"F0.wireOp",EDGE,"E2992"),sQuery(id+"F0.wireOp",EDGE,"E2993"),sQuery(id+"F0.wireOp",EDGE,"E2994"),sQuery(id+"F0.wireOp",EDGE,"E2995"),sQuery(id+"F0.wireOp",EDGE,"E2996"),sQuery(id+"F0.wireOp",EDGE,"E2997"),sQuery(id+"F0.wireOp",EDGE,"E2998"),sQuery(id+"F0.wireOp",EDGE,"E2999"),sQuery(id+"F0.wireOp",EDGE,"E3000"),sQuery(id+"F0.wireOp",EDGE,"E3001"),sQuery(id+"F0.wireOp",EDGE,"E3002"),sQuery(id+"F0.wireOp",EDGE,"E3003"),sQuery(id+"F0.wireOp",EDGE,"E3004"),sQuery(id+"F0.wireOp",EDGE,"E3005"),sQuery(id+"F0.wireOp",EDGE,"E3006"),sQuery(id+"F0.wireOp",EDGE,"E3007"),sQuery(id+"F0.wireOp",EDGE,"E3008"),sQuery(id+"F0.wireOp",EDGE,"E3009"),sQuery(id+"F0.wireOp",EDGE,"E3010"),sQuery(id+"F0.wireOp",EDGE,"E3011"),sQuery(id+"F0.wireOp",EDGE,"E3012"),sQuery(id+"F0.wireOp",EDGE,"E3013"),sQuery(id+"F0.wireOp",EDGE,"E3014"),sQuery(id+"F0.wireOp",EDGE,"E3015"),sQuery(id+"F0.wireOp",EDGE,"E3016"),sQuery(id+"F0.wireOp",EDGE,"E3017"),sQuery(id+"F0.wireOp",EDGE,"E3018"),sQuery(id+"F0.wireOp",EDGE,"E3019"),sQuery(id+"F0.wireOp",EDGE,"E3020"),sQuery(id+"F0.wireOp",EDGE,"E3021"),sQuery(id+"F0.wireOp",EDGE,"E3022"),sQuery(id+"F0.wireOp",EDGE,"E3023"),sQuery(id+"F0.wireOp",EDGE,"E3024"),sQuery(id+"F0.wireOp",EDGE,"E3025"),sQuery(id+"F0.wireOp",EDGE,"E3026"),sQuery(id+"F0.wireOp",EDGE,"E3027"),sQuery(id+"F0.wireOp",EDGE,"E3028"),sQuery(id+"F0.wireOp",EDGE,"E3029"),sQuery(id+"F0.wireOp",EDGE,"E3030"),sQuery(id+"F0.wireOp",EDGE,"E3031"),sQuery(id+"F0.wireOp",EDGE,"E3032"),sQuery(id+"F0.wireOp",EDGE,"E3033"),sQuery(id+"F0.wireOp",EDGE,"E3034"),sQuery(id+"F0.wireOp",EDGE,"E3035"),sQuery(id+"F0.wireOp",EDGE,"E3036"),sQuery(id+"F0.wireOp",EDGE,"E3037"),sQuery(id+"F0.wireOp",EDGE,"E3038"),sQuery(id+"F0.wireOp",EDGE,"E3039"),sQuery(id+"F0.wireOp",EDGE,"E3040"),sQuery(id+"F0.wireOp",EDGE,"E3041"),sQuery(id+"F0.wireOp",EDGE,"E3042"),sQuery(id+"F0.wireOp",EDGE,"E3043"),sQuery(id+"F0.wireOp",EDGE,"E3044"),sQuery(id+"F0.wireOp",EDGE,"E3045"),sQuery(id+"F0.wireOp",EDGE,"E3046"),sQuery(id+"F0.wireOp",EDGE,"E3047"),sQuery(id+"F0.wireOp",EDGE,"E3048"),sQuery(id+"F0.wireOp",EDGE,"E3049"),sQuery(id+"F0.wireOp",EDGE,"E3050"),sQuery(id+"F0.wireOp",EDGE,"E3051"),sQuery(id+"F0.wireOp",EDGE,"E3052"),sQuery(id+"F0.wireOp",EDGE,"E3053"),sQuery(id+"F0.wireOp",EDGE,"E3054"),sQuery(id+"F0.wireOp",EDGE,"E3055"),sQuery(id+"F0.wireOp",EDGE,"E3056"),sQuery(id+"F0.wireOp",EDGE,"E3057"),sQuery(id+"F0.wireOp",EDGE,"E3058"),sQuery(id+"F0.wireOp",EDGE,"E3059"),sQuery(id+"F0.wireOp",EDGE,"E3060"),sQuery(id+"F0.wireOp",EDGE,"E3061"),sQuery(id+"F0.wireOp",EDGE,"E3062"),sQuery(id+"F0.wireOp",EDGE,"E3063"),sQuery(id+"F0.wireOp",EDGE,"E3064"),sQuery(id+"F0.wireOp",EDGE,"E3065"),sQuery(id+"F0.wireOp",EDGE,"E3066"),sQuery(id+"F0.wireOp",EDGE,"E3067"),sQuery(id+"F0.wireOp",EDGE,"E3068"),sQuery(id+"F0.wireOp",EDGE,"E3069"),sQuery(id+"F0.wireOp",EDGE,"E3070"),sQuery(id+"F0.wireOp",EDGE,"E3070"),sQuery(id+"F0.wireOp",EDGE,"E3071"),sQuery(id+"F0.wireOp",EDGE,"E3072"),sQuery(id+"F0.wireOp",EDGE,"E3073"),sQuery(id+"F0.wireOp",EDGE,"E3074"),sQuery(id+"F0.wireOp",EDGE,"E3075"),sQuery(id+"F0.wireOp",EDGE,"E3076"),sQuery(id+"F0.wireOp",EDGE,"E3077"),sQuery(id+"F0.wireOp",EDGE,"E3078"),sQuery(id+"F0.wireOp",EDGE,"E3079"),sQuery(id+"F0.wireOp",EDGE,"E3080"),sQuery(id+"F0.wireOp",EDGE,"E3081"),sQuery(id+"F0.wireOp",EDGE,"E3082"),sQuery(id+"F0.wireOp",EDGE,"E3083"),sQuery(id+"F0.wireOp",EDGE,"E3083"),sQuery(id+"F0.wireOp",EDGE,"E3084"),sQuery(id+"F0.wireOp",EDGE,"E3085"),sQuery(id+"F0.wireOp",EDGE,"E3086"),sQuery(id+"F0.wireOp",EDGE,"E3087"),sQuery(id+"F0.wireOp",EDGE,"E3088"),sQuery(id+"F0.wireOp",EDGE,"E3089"),sQuery(id+"F0.wireOp",EDGE,"E3090"),sQuery(id+"F0.wireOp",EDGE,"E3091"),sQuery(id+"F0.wireOp",EDGE,"E3092"),sQuery(id+"F0.wireOp",EDGE,"E3093"),sQuery(id+"F0.wireOp",EDGE,"E3094"),sQuery(id+"F0.wireOp",EDGE,"E3095"),sQuery(id+"F0.wireOp",EDGE,"E3096"),sQuery(id+"F0.wireOp",EDGE,"E3097"),sQuery(id+"F0.wireOp",EDGE,"E3098"),sQuery(id+"F0.wireOp",EDGE,"E3099"),sQuery(id+"F0.wireOp",EDGE,"E3100"),sQuery(id+"F0.wireOp",EDGE,"E3100"),sQuery(id+"F0.wireOp",EDGE,"E3101"),sQuery(id+"F0.wireOp",EDGE,"E3102"),sQuery(id+"F0.wireOp",EDGE,"E3103"),sQuery(id+"F0.wireOp",EDGE,"E3104"),sQuery(id+"F0.wireOp",EDGE,"E3105"),sQuery(id+"F0.wireOp",EDGE,"E3106"),sQuery(id+"F0.wireOp",EDGE,"E3107"),sQuery(id+"F0.wireOp",EDGE,"E3108"),sQuery(id+"F0.wireOp",EDGE,"E3109"),sQuery(id+"F0.wireOp",EDGE,"E3110"),sQuery(id+"F0.wireOp",EDGE,"E3111"),sQuery(id+"F0.wireOp",EDGE,"E3112"),sQuery(id+"F0.wireOp",EDGE,"E3113"),sQuery(id+"F0.wireOp",EDGE,"E3114"),sQuery(id+"F0.wireOp",EDGE,"E3114"),sQuery(id+"F0.wireOp",EDGE,"E3114"),sQuery(id+"F0.wireOp",EDGE,"E3115"),sQuery(id+"F0.wireOp",EDGE,"E3116"),sQuery(id+"F0.wireOp",EDGE,"E3117"),sQuery(id+"F0.wireOp",EDGE,"E3118"),sQuery(id+"F0.wireOp",EDGE,"E3119"),sQuery(id+"F0.wireOp",EDGE,"E3120"),sQuery(id+"F0.wireOp",EDGE,"E3121"),sQuery(id+"F0.wireOp",EDGE,"E3122"),sQuery(id+"F0.wireOp",EDGE,"E3123"),sQuery(id+"F0.wireOp",EDGE,"E3124"),sQuery(id+"F0.wireOp",EDGE,"E3125"),sQuery(id+"F0.wireOp",EDGE,"E3126"),sQuery(id+"F0.wireOp",EDGE,"E3127"),sQuery(id+"F0.wireOp",EDGE,"E3128"),sQuery(id+"F0.wireOp",EDGE,"E3129"),sQuery(id+"F0.wireOp",EDGE,"E3130"),sQuery(id+"F0.wireOp",EDGE,"E3131"),sQuery(id+"F0.wireOp",EDGE,"E3132"),sQuery(id+"F0.wireOp",EDGE,"E3133"),sQuery(id+"F0.wireOp",EDGE,"E3134"),sQuery(id+"F0.wireOp",EDGE,"E3135"),sQuery(id+"F0.wireOp",EDGE,"E3136"),sQuery(id+"F0.wireOp",EDGE,"E3137"),sQuery(id+"F0.wireOp",EDGE,"E3138"),sQuery(id+"F0.wireOp",EDGE,"E3139"),sQuery(id+"F0.wireOp",EDGE,"E3140"),sQuery(id+"F0.wireOp",EDGE,"E3141"),sQuery(id+"F0.wireOp",EDGE,"E3142"),sQuery(id+"F0.wireOp",EDGE,"E3143"),sQuery(id+"F0.wireOp",EDGE,"E3144"),sQuery(id+"F0.wireOp",EDGE,"E3145"),sQuery(id+"F0.wireOp",EDGE,"E3146"),sQuery(id+"F0.wireOp",EDGE,"E3147"),sQuery(id+"F0.wireOp",EDGE,"E3148"),sQuery(id+"F0.wireOp",EDGE,"E3149"),sQuery(id+"F0.wireOp",EDGE,"E3150"),sQuery(id+"F0.wireOp",EDGE,"E3151"),sQuery(id+"F0.wireOp",EDGE,"E3152"),sQuery(id+"F0.wireOp",EDGE,"E3153"),sQuery(id+"F0.wireOp",EDGE,"E3154"),sQuery(id+"F0.wireOp",EDGE,"E3155"),sQuery(id+"F0.wireOp",EDGE,"E3156"),sQuery(id+"F0.wireOp",EDGE,"E3157"),sQuery(id+"F0.wireOp",EDGE,"E3158"),sQuery(id+"F0.wireOp",EDGE,"E3159"),sQuery(id+"F0.wireOp",EDGE,"E3160"),sQuery(id+"F0.wireOp",EDGE,"E3160"),sQuery(id+"F0.wireOp",EDGE,"E3161"),sQuery(id+"F0.wireOp",EDGE,"E3162"),sQuery(id+"F0.wireOp",EDGE,"E3163"),sQuery(id+"F0.wireOp",EDGE,"E3164"),sQuery(id+"F0.wireOp",EDGE,"E3165"),sQuery(id+"F0.wireOp",EDGE,"E3166"),sQuery(id+"F0.wireOp",EDGE,"E3167"),sQuery(id+"F0.wireOp",EDGE,"E3168"),sQuery(id+"F0.wireOp",EDGE,"E3169"),sQuery(id+"F0.wireOp",EDGE,"E3170"),sQuery(id+"F0.wireOp",EDGE,"E3171"),sQuery(id+"F0.wireOp",EDGE,"E3172"),sQuery(id+"F0.wireOp",EDGE,"E3173"),sQuery(id+"F0.wireOp",EDGE,"E3174"),sQuery(id+"F0.wireOp",EDGE,"E3175"),sQuery(id+"F0.wireOp",EDGE,"E3176"),sQuery(id+"F0.wireOp",EDGE,"E3177"),sQuery(id+"F0.wireOp",EDGE,"E3178"),sQuery(id+"F0.wireOp",EDGE,"E3179"),sQuery(id+"F0.wireOp",EDGE,"E3180"),sQuery(id+"F0.wireOp",EDGE,"E3181"),sQuery(id+"F0.wireOp",EDGE,"E3182"),sQuery(id+"F0.wireOp",EDGE,"E3183"),sQuery(id+"F0.wireOp",EDGE,"E3184"),sQuery(id+"F0.wireOp",EDGE,"E3185"),sQuery(id+"F0.wireOp",EDGE,"E3186"),sQuery(id+"F0.wireOp",EDGE,"E3187"),sQuery(id+"F0.wireOp",EDGE,"E3188"),sQuery(id+"F0.wireOp",EDGE,"E3189"),sQuery(id+"F0.wireOp",EDGE,"E3190"),sQuery(id+"F0.wireOp",EDGE,"E3191"),sQuery(id+"F0.wireOp",EDGE,"E3192"),sQuery(id+"F0.wireOp",EDGE,"E3193"),sQuery(id+"F0.wireOp",EDGE,"E3194"),sQuery(id+"F0.wireOp",EDGE,"E3195"),sQuery(id+"F0.wireOp",EDGE,"E3196"),sQuery(id+"F0.wireOp",EDGE,"E3197"),sQuery(id+"F0.wireOp",EDGE,"E3198"),sQuery(id+"F0.wireOp",EDGE,"E3199"),sQuery(id+"F0.wireOp",EDGE,"E3200"),sQuery(id+"F0.wireOp",EDGE,"E3201"),sQuery(id+"F0.wireOp",EDGE,"E3202"),sQuery(id+"F0.wireOp",EDGE,"E3203"),sQuery(id+"F0.wireOp",EDGE,"E3204"),sQuery(id+"F0.wireOp",EDGE,"E3205"),sQuery(id+"F0.wireOp",EDGE,"E3206"),sQuery(id+"F0.wireOp",EDGE,"E3207"),sQuery(id+"F0.wireOp",EDGE,"E3208"),sQuery(id+"F0.wireOp",EDGE,"E3209"),sQuery(id+"F0.wireOp",EDGE,"E3210"),sQuery(id+"F0.wireOp",EDGE,"E3211"),sQuery(id+"F0.wireOp",EDGE,"E3212"),sQuery(id+"F0.wireOp",EDGE,"E3213"),sQuery(id+"F0.wireOp",EDGE,"E3214"),sQuery(id+"F0.wireOp",EDGE,"E3215"),sQuery(id+"F0.wireOp",EDGE,"E3216"),sQuery(id+"F0.wireOp",EDGE,"E3217"),sQuery(id+"F0.wireOp",EDGE,"E3218"),sQuery(id+"F0.wireOp",EDGE,"E3219"),sQuery(id+"F0.wireOp",EDGE,"E3220"),sQuery(id+"F0.wireOp",EDGE,"E3221"),sQuery(id+"F0.wireOp",EDGE,"E3222"),sQuery(id+"F0.wireOp",EDGE,"E3223"),sQuery(id+"F0.wireOp",EDGE,"E3224"),sQuery(id+"F0.wireOp",EDGE,"E3225"),sQuery(id+"F0.wireOp",EDGE,"E3226"),sQuery(id+"F0.wireOp",EDGE,"E3227"),sQuery(id+"F0.wireOp",EDGE,"E3228"),sQuery(id+"F0.wireOp",EDGE,"E3229"),sQuery(id+"F0.wireOp",EDGE,"E3230"),sQuery(id+"F0.wireOp",EDGE,"E3231"),sQuery(id+"F0.wireOp",EDGE,"E3232"),sQuery(id+"F0.wireOp",EDGE,"E3233"),sQuery(id+"F0.wireOp",EDGE,"E3234"),sQuery(id+"F0.wireOp",EDGE,"E3235"),sQuery(id+"F0.wireOp",EDGE,"E3236"),sQuery(id+"F0.wireOp",EDGE,"E3237"),sQuery(id+"F0.wireOp",EDGE,"E3238"),sQuery(id+"F0.wireOp",EDGE,"E3239"),sQuery(id+"F0.wireOp",EDGE,"E3240"),sQuery(id+"F0.wireOp",EDGE,"E3241"),sQuery(id+"F0.wireOp",EDGE,"E3242"),sQuery(id+"F0.wireOp",EDGE,"E3243"),sQuery(id+"F0.wireOp",EDGE,"E3244"),sQuery(id+"F0.wireOp",EDGE,"E3245"),sQuery(id+"F0.wireOp",EDGE,"E3246"),sQuery(id+"F0.wireOp",EDGE,"E3247"),sQuery(id+"F0.wireOp",EDGE,"E3248"),sQuery(id+"F0.wireOp",EDGE,"E3249"),sQuery(id+"F0.wireOp",EDGE,"E3250"),sQuery(id+"F0.wireOp",EDGE,"E3251"),sQuery(id+"F0.wireOp",EDGE,"E3252"),sQuery(id+"F0.wireOp",EDGE,"E3253"),sQuery(id+"F0.wireOp",EDGE,"E3254"),sQuery(id+"F0.wireOp",EDGE,"E3255"),sQuery(id+"F0.wireOp",EDGE,"E3256"),sQuery(id+"F0.wireOp",EDGE,"E3257"),sQuery(id+"F0.wireOp",EDGE,"E3258"),sQuery(id+"F0.wireOp",EDGE,"E3259"),sQuery(id+"F0.wireOp",EDGE,"E3260"),sQuery(id+"F0.wireOp",EDGE,"E3261"),sQuery(id+"F0.wireOp",EDGE,"E3262"),sQuery(id+"F0.wireOp",EDGE,"E3263"),sQuery(id+"F0.wireOp",EDGE,"E3264"),sQuery(id+"F0.wireOp",EDGE,"E3265"),sQuery(id+"F0.wireOp",EDGE,"E3266"),sQuery(id+"F0.wireOp",EDGE,"E3267"),sQuery(id+"F0.wireOp",EDGE,"E3268"),sQuery(id+"F0.wireOp",EDGE,"E3269"),sQuery(id+"F0.wireOp",EDGE,"E3270"),sQuery(id+"F0.wireOp",EDGE,"E3271"),sQuery(id+"F0.wireOp",EDGE,"E3272"),sQuery(id+"F0.wireOp",EDGE,"E3273"),sQuery(id+"F0.wireOp",EDGE,"E3274"),sQuery(id+"F0.wireOp",EDGE,"E3275"),sQuery(id+"F0.wireOp",EDGE,"E3276"),sQuery(id+"F0.wireOp",EDGE,"E3277"),sQuery(id+"F0.wireOp",EDGE,"E3278"),sQuery(id+"F0.wireOp",EDGE,"E3279"),sQuery(id+"F0.wireOp",EDGE,"E3280"),sQuery(id+"F0.wireOp",EDGE,"E3281"),sQuery(id+"F0.wireOp",EDGE,"E3282"),sQuery(id+"F0.wireOp",EDGE,"E3283"),sQuery(id+"F0.wireOp",EDGE,"E3284"),sQuery(id+"F0.wireOp",EDGE,"E3285"),sQuery(id+"F0.wireOp",EDGE,"E3286"),sQuery(id+"F0.wireOp",EDGE,"E3287"),sQuery(id+"F0.wireOp",EDGE,"E3288"),sQuery(id+"F0.wireOp",EDGE,"E3289"),sQuery(id+"F0.wireOp",EDGE,"E3290"),sQuery(id+"F0.wireOp",EDGE,"E3290"),sQuery(id+"F0.wireOp",EDGE,"E3290"),sQuery(id+"F0.wireOp",EDGE,"E3291"),sQuery(id+"F0.wireOp",EDGE,"E3292"),sQuery(id+"F0.wireOp",EDGE,"E3293"),sQuery(id+"F0.wireOp",EDGE,"E3294"),sQuery(id+"F0.wireOp",EDGE,"E3295"),sQuery(id+"F0.wireOp",EDGE,"E3296"),sQuery(id+"F0.wireOp",EDGE,"E3297"),sQuery(id+"F0.wireOp",EDGE,"E3298"),sQuery(id+"F0.wireOp",EDGE,"E3299"),sQuery(id+"F0.wireOp",EDGE,"E3300"),sQuery(id+"F0.wireOp",EDGE,"E3301"),sQuery(id+"F0.wireOp",EDGE,"E3302"),sQuery(id+"F0.wireOp",EDGE,"E3303"),sQuery(id+"F0.wireOp",EDGE,"E3304"),sQuery(id+"F0.wireOp",EDGE,"E3305"),sQuery(id+"F0.wireOp",EDGE,"E3306"),sQuery(id+"F0.wireOp",EDGE,"E3306"),sQuery(id+"F0.wireOp",EDGE,"E3307"),sQuery(id+"F0.wireOp",EDGE,"E3308"),sQuery(id+"F0.wireOp",EDGE,"E3309"),sQuery(id+"F0.wireOp",EDGE,"E3309"),sQuery(id+"F0.wireOp",EDGE,"E3310"),sQuery(id+"F0.wireOp",EDGE,"E3311"),sQuery(id+"F0.wireOp",EDGE,"E3312"),sQuery(id+"F0.wireOp",EDGE,"E3313"),sQuery(id+"F0.wireOp",EDGE,"E3314"),sQuery(id+"F0.wireOp",EDGE,"E3315"),sQuery(id+"F0.wireOp",EDGE,"E3316"),sQuery(id+"F0.wireOp",EDGE,"E3316"),sQuery(id+"F0.wireOp",EDGE,"E3317"),sQuery(id+"F0.wireOp",EDGE,"E3318"),sQuery(id+"F0.wireOp",EDGE,"E3319"),sQuery(id+"F0.wireOp",EDGE,"E3320"),sQuery(id+"F0.wireOp",EDGE,"E3321"),sQuery(id+"F0.wireOp",EDGE,"E3322"),sQuery(id+"F0.wireOp",EDGE,"E3322"),sQuery(id+"F0.wireOp",EDGE,"E3323"),sQuery(id+"F0.wireOp",EDGE,"E3324"),sQuery(id+"F0.wireOp",EDGE,"E3325"),sQuery(id+"F0.wireOp",EDGE,"E3326"),sQuery(id+"F0.wireOp",EDGE,"E3327"),sQuery(id+"F0.wireOp",EDGE,"E3328"),sQuery(id+"F0.wireOp",EDGE,"E3329"),sQuery(id+"F0.wireOp",EDGE,"E3330"),sQuery(id+"F0.wireOp",EDGE,"E3331"),sQuery(id+"F0.wireOp",EDGE,"E3332"),sQuery(id+"F0.wireOp",EDGE,"E3333"),sQuery(id+"F0.wireOp",EDGE,"E3334"),sQuery(id+"F0.wireOp",EDGE,"E3335"),sQuery(id+"F0.wireOp",EDGE,"E3336"),sQuery(id+"F0.wireOp",EDGE,"E3337"),sQuery(id+"F0.wireOp",EDGE,"E3338"),sQuery(id+"F0.wireOp",EDGE,"E3339"),sQuery(id+"F0.wireOp",EDGE,"E3339"),sQuery(id+"F0.wireOp",EDGE,"E3340"),sQuery(id+"F0.wireOp",EDGE,"E3341"),sQuery(id+"F0.wireOp",EDGE,"E3342"),sQuery(id+"F0.wireOp",EDGE,"E3343"),sQuery(id+"F0.wireOp",EDGE,"E3344"),sQuery(id+"F0.wireOp",EDGE,"E3345"),sQuery(id+"F0.wireOp",EDGE,"E3346"),sQuery(id+"F0.wireOp",EDGE,"E3347"),sQuery(id+"F0.wireOp",EDGE,"E3348"),sQuery(id+"F0.wireOp",EDGE,"E3349"),sQuery(id+"F0.wireOp",EDGE,"E3350"),sQuery(id+"F0.wireOp",EDGE,"E3351"),sQuery(id+"F0.wireOp",EDGE,"E3352"),sQuery(id+"F0.wireOp",EDGE,"E3353"),sQuery(id+"F0.wireOp",EDGE,"E3354"),sQuery(id+"F0.wireOp",EDGE,"E3355"),sQuery(id+"F0.wireOp",EDGE,"E3356"),sQuery(id+"F0.wireOp",EDGE,"E3357"),sQuery(id+"F0.wireOp",EDGE,"E3358"),sQuery(id+"F0.wireOp",EDGE,"E3359"),sQuery(id+"F0.wireOp",EDGE,"E3360"),sQuery(id+"F0.wireOp",EDGE,"E3361"),sQuery(id+"F0.wireOp",EDGE,"E3362"),sQuery(id+"F0.wireOp",EDGE,"E3363"),sQuery(id+"F0.wireOp",EDGE,"E3364"),sQuery(id+"F0.wireOp",EDGE,"E3365"),sQuery(id+"F0.wireOp",EDGE,"E3366"),sQuery(id+"F0.wireOp",EDGE,"E3367"),sQuery(id+"F0.wireOp",EDGE,"E3368"),sQuery(id+"F0.wireOp",EDGE,"E3369"),sQuery(id+"F0.wireOp",EDGE,"E3370"),sQuery(id+"F0.wireOp",EDGE,"E3371"),sQuery(id+"F0.wireOp",EDGE,"E3372"),sQuery(id+"F0.wireOp",EDGE,"E3373"),sQuery(id+"F0.wireOp",EDGE,"E3374"),sQuery(id+"F0.wireOp",EDGE,"E3375"),sQuery(id+"F0.wireOp",EDGE,"E3376"),sQuery(id+"F0.wireOp",EDGE,"E3377"),sQuery(id+"F0.wireOp",EDGE,"E3378"),sQuery(id+"F0.wireOp",EDGE,"E3379"),sQuery(id+"F0.wireOp",EDGE,"E3380"),sQuery(id+"F0.wireOp",EDGE,"E3381"),sQuery(id+"F0.wireOp",EDGE,"E3382"),sQuery(id+"F0.wireOp",EDGE,"E3383"),sQuery(id+"F0.wireOp",EDGE,"E3384"),sQuery(id+"F0.wireOp",EDGE,"E3385"),sQuery(id+"F0.wireOp",EDGE,"E3386"),sQuery(id+"F0.wireOp",EDGE,"E3387"),sQuery(id+"F0.wireOp",EDGE,"E3388"),sQuery(id+"F0.wireOp",EDGE,"E3389"),sQuery(id+"F0.wireOp",EDGE,"E3390"),sQuery(id+"F0.wireOp",EDGE,"E3391"),sQuery(id+"F0.wireOp",EDGE,"E3392"),sQuery(id+"F0.wireOp",EDGE,"E3393"),sQuery(id+"F0.wireOp",EDGE,"E3394"),sQuery(id+"F0.wireOp",EDGE,"E3395"),sQuery(id+"F0.wireOp",EDGE,"E3396"),sQuery(id+"F0.wireOp",EDGE,"E3397"),sQuery(id+"F0.wireOp",EDGE,"E3398"),sQuery(id+"F0.wireOp",EDGE,"E3399"),sQuery(id+"F0.wireOp",EDGE,"E3400"),sQuery(id+"F0.wireOp",EDGE,"E3401"),sQuery(id+"F0.wireOp",EDGE,"E3402"),sQuery(id+"F0.wireOp",EDGE,"E3403"),sQuery(id+"F0.wireOp",EDGE,"E3404"),sQuery(id+"F0.wireOp",EDGE,"E3405"),sQuery(id+"F0.wireOp",EDGE,"E3406"),sQuery(id+"F0.wireOp",EDGE,"E3407"),sQuery(id+"F0.wireOp",EDGE,"E3408"),sQuery(id+"F0.wireOp",EDGE,"E3409"),sQuery(id+"F0.wireOp",EDGE,"E3410"),sQuery(id+"F0.wireOp",EDGE,"E3411"),sQuery(id+"F0.wireOp",EDGE,"E3412"),sQuery(id+"F0.wireOp",EDGE,"E3413"),sQuery(id+"F0.wireOp",EDGE,"E3414"),sQuery(id+"F0.wireOp",EDGE,"E3415"),sQuery(id+"F0.wireOp",EDGE,"E3416"),sQuery(id+"F0.wireOp",EDGE,"E3417"),sQuery(id+"F0.wireOp",EDGE,"E3418"),sQuery(id+"F0.wireOp",EDGE,"E3419"),sQuery(id+"F0.wireOp",EDGE,"E3420"),sQuery(id+"F0.wireOp",EDGE,"E3421"),sQuery(id+"F0.wireOp",EDGE,"E3422"),sQuery(id+"F0.wireOp",EDGE,"E3423"),sQuery(id+"F0.wireOp",EDGE,"E3424"),sQuery(id+"F0.wireOp",EDGE,"E3425"),sQuery(id+"F0.wireOp",EDGE,"E3426"),sQuery(id+"F0.wireOp",EDGE,"E3427"),sQuery(id+"F0.wireOp",EDGE,"E3428"),sQuery(id+"F0.wireOp",EDGE,"E3429"),sQuery(id+"F0.wireOp",EDGE,"E3430"),sQuery(id+"F0.wireOp",EDGE,"E3431"),sQuery(id+"F0.wireOp",EDGE,"E3432"),sQuery(id+"F0.wireOp",EDGE,"E3433"),sQuery(id+"F0.wireOp",EDGE,"E3434"),sQuery(id+"F0.wireOp",EDGE,"E3435"),sQuery(id+"F0.wireOp",EDGE,"E3436"),sQuery(id+"F0.wireOp",EDGE,"E3437"),sQuery(id+"F0.wireOp",EDGE,"E3438"),sQuery(id+"F0.wireOp",EDGE,"E3439"),sQuery(id+"F0.wireOp",EDGE,"E3440"),sQuery(id+"F0.wireOp",EDGE,"E3441"),sQuery(id+"F0.wireOp",EDGE,"E3442"),sQuery(id+"F0.wireOp",EDGE,"E3443"),sQuery(id+"F0.wireOp",EDGE,"E3444"),sQuery(id+"F0.wireOp",EDGE,"E3445"),sQuery(id+"F0.wireOp",EDGE,"E3446"),sQuery(id+"F0.wireOp",EDGE,"E3447"),sQuery(id+"F0.wireOp",EDGE,"E3448"),sQuery(id+"F0.wireOp",EDGE,"E3449"),sQuery(id+"F0.wireOp",EDGE,"E3450"),sQuery(id+"F0.wireOp",EDGE,"E3451"),sQuery(id+"F0.wireOp",EDGE,"E3452"),sQuery(id+"F0.wireOp",EDGE,"E3453"),sQuery(id+"F0.wireOp",EDGE,"E3454"),sQuery(id+"F0.wireOp",EDGE,"E3454"),sQuery(id+"F0.wireOp",EDGE,"E3454"),sQuery(id+"F0.wireOp",EDGE,"E3455"),sQuery(id+"F0.wireOp",EDGE,"E3456"),sQuery(id+"F0.wireOp",EDGE,"E3457"),sQuery(id+"F0.wireOp",EDGE,"E3458"),sQuery(id+"F0.wireOp",EDGE,"E3459"),sQuery(id+"F0.wireOp",EDGE,"E3460"),sQuery(id+"F0.wireOp",EDGE,"E3461"),sQuery(id+"F0.wireOp",EDGE,"E3462"),sQuery(id+"F0.wireOp",EDGE,"E3463"),sQuery(id+"F0.wireOp",EDGE,"E3464"),sQuery(id+"F0.wireOp",EDGE,"E3465"),sQuery(id+"F0.wireOp",EDGE,"E3466"),sQuery(id+"F0.wireOp",EDGE,"E3467"),sQuery(id+"F0.wireOp",EDGE,"E3468"),sQuery(id+"F0.wireOp",EDGE,"E3469"),sQuery(id+"F0.wireOp",EDGE,"E3470"),sQuery(id+"F0.wireOp",EDGE,"E3471"),sQuery(id+"F0.wireOp",EDGE,"E3472"),sQuery(id+"F0.wireOp",EDGE,"E3473"),sQuery(id+"F0.wireOp",EDGE,"E3474"),sQuery(id+"F0.wireOp",EDGE,"E3475"),sQuery(id+"F0.wireOp",EDGE,"E3476"),sQuery(id+"F0.wireOp",EDGE,"E3477"),sQuery(id+"F0.wireOp",EDGE,"E3478"),sQuery(id+"F0.wireOp",EDGE,"E3479"),sQuery(id+"F0.wireOp",EDGE,"E3480"),sQuery(id+"F0.wireOp",EDGE,"E3481"),sQuery(id+"F0.wireOp",EDGE,"E3482"),sQuery(id+"F0.wireOp",EDGE,"E3483"),sQuery(id+"F0.wireOp",EDGE,"E3484"),sQuery(id+"F0.wireOp",EDGE,"E3485"),sQuery(id+"F0.wireOp",EDGE,"E3486"),sQuery(id+"F0.wireOp",EDGE,"E3487"),sQuery(id+"F0.wireOp",EDGE,"E3488"),sQuery(id+"F0.wireOp",EDGE,"E3489"),sQuery(id+"F0.wireOp",EDGE,"E3490"),sQuery(id+"F0.wireOp",EDGE,"E3491"),sQuery(id+"F0.wireOp",EDGE,"E3492"),sQuery(id+"F0.wireOp",EDGE,"E3493"),sQuery(id+"F0.wireOp",EDGE,"E3494"),sQuery(id+"F0.wireOp",EDGE,"E3495"),sQuery(id+"F0.wireOp",EDGE,"E3496"),sQuery(id+"F0.wireOp",EDGE,"E3497"),sQuery(id+"F0.wireOp",EDGE,"E3498"),sQuery(id+"F0.wireOp",EDGE,"E3499"),sQuery(id+"F0.wireOp",EDGE,"E3500"),sQuery(id+"F0.wireOp",EDGE,"E3500"),sQuery(id+"F0.wireOp",EDGE,"E3501"),sQuery(id+"F0.wireOp",EDGE,"E3502"),sQuery(id+"F0.wireOp",EDGE,"E3503"),sQuery(id+"F0.wireOp",EDGE,"E3504"),sQuery(id+"F0.wireOp",EDGE,"E3505"),sQuery(id+"F0.wireOp",EDGE,"E3506"),sQuery(id+"F0.wireOp",EDGE,"E3507"),sQuery(id+"F0.wireOp",EDGE,"E3508"),sQuery(id+"F0.wireOp",EDGE,"E3509"),sQuery(id+"F0.wireOp",EDGE,"E3510"),sQuery(id+"F0.wireOp",EDGE,"E3511"),sQuery(id+"F0.wireOp",EDGE,"E3512"),sQuery(id+"F0.wireOp",EDGE,"E3513"),sQuery(id+"F0.wireOp",EDGE,"E3514"),sQuery(id+"F0.wireOp",EDGE,"E3515"),sQuery(id+"F0.wireOp",EDGE,"E3516"),sQuery(id+"F0.wireOp",EDGE,"E3517"),sQuery(id+"F0.wireOp",EDGE,"E3518"),sQuery(id+"F0.wireOp",EDGE,"E3519"),sQuery(id+"F0.wireOp",EDGE,"E3520"),sQuery(id+"F0.wireOp",EDGE,"E3521"),sQuery(id+"F0.wireOp",EDGE,"E3522"),sQuery(id+"F0.wireOp",EDGE,"E3523"),sQuery(id+"F0.wireOp",EDGE,"E3524"),sQuery(id+"F0.wireOp",EDGE,"E3524"),sQuery(id+"F0.wireOp",EDGE,"E3524"),sQuery(id+"F0.wireOp",EDGE,"E3525"),sQuery(id+"F0.wireOp",EDGE,"E3526"),sQuery(id+"F0.wireOp",EDGE,"E3527"),sQuery(id+"F0.wireOp",EDGE,"E3528"),sQuery(id+"F0.wireOp",EDGE,"E3529"),sQuery(id+"F0.wireOp",EDGE,"E3530"),sQuery(id+"F0.wireOp",EDGE,"E3531"),sQuery(id+"F0.wireOp",EDGE,"E3532"),sQuery(id+"F0.wireOp",EDGE,"E3533"),sQuery(id+"F0.wireOp",EDGE,"E3534"),sQuery(id+"F0.wireOp",EDGE,"E3535"),sQuery(id+"F0.wireOp",EDGE,"E3536"),sQuery(id+"F0.wireOp",EDGE,"E3537"),sQuery(id+"F0.wireOp",EDGE,"E3538"),sQuery(id+"F0.wireOp",EDGE,"E3539"),sQuery(id+"F0.wireOp",EDGE,"E3540"),sQuery(id+"F0.wireOp",EDGE,"E3541"),sQuery(id+"F0.wireOp",EDGE,"E3542"),sQuery(id+"F0.wireOp",EDGE,"E3543"),sQuery(id+"F0.wireOp",EDGE,"E3544"),sQuery(id+"F0.wireOp",EDGE,"E3545"),sQuery(id+"F0.wireOp",EDGE,"E3546"),sQuery(id+"F0.wireOp",EDGE,"E3547"),sQuery(id+"F0.wireOp",EDGE,"E3548"),sQuery(id+"F0.wireOp",EDGE,"E3549"),sQuery(id+"F0.wireOp",EDGE,"E3550"),sQuery(id+"F0.wireOp",EDGE,"E3551"),sQuery(id+"F0.wireOp",EDGE,"E3552"),sQuery(id+"F0.wireOp",EDGE,"E3553"),sQuery(id+"F0.wireOp",EDGE,"E3553"),sQuery(id+"F0.wireOp",EDGE,"E3554"),sQuery(id+"F0.wireOp",EDGE,"E3555"),sQuery(id+"F0.wireOp",EDGE,"E3556"),sQuery(id+"F0.wireOp",EDGE,"E3557"),sQuery(id+"F0.wireOp",EDGE,"E3558"),sQuery(id+"F0.wireOp",EDGE,"E3559"),sQuery(id+"F0.wireOp",EDGE,"E3560"),sQuery(id+"F0.wireOp",EDGE,"E3561"),sQuery(id+"F0.wireOp",EDGE,"E3562"),sQuery(id+"F0.wireOp",EDGE,"E3563"),sQuery(id+"F0.wireOp",EDGE,"E3564"),sQuery(id+"F0.wireOp",EDGE,"E3565"),sQuery(id+"F0.wireOp",EDGE,"E3566"),sQuery(id+"F0.wireOp",EDGE,"E3567"),sQuery(id+"F0.wireOp",EDGE,"E3568"),sQuery(id+"F0.wireOp",EDGE,"E3569"),sQuery(id+"F0.wireOp",EDGE,"E3570"),sQuery(id+"F0.wireOp",EDGE,"E3571"),sQuery(id+"F0.wireOp",EDGE,"E3572"),sQuery(id+"F0.wireOp",EDGE,"E3573"),sQuery(id+"F0.wireOp",EDGE,"E3574"),sQuery(id+"F0.wireOp",EDGE,"E3575"),sQuery(id+"F0.wireOp",EDGE,"E3576"),sQuery(id+"F0.wireOp",EDGE,"E3577"),sQuery(id+"F0.wireOp",EDGE,"E3578"),sQuery(id+"F0.wireOp",EDGE,"E3579"),sQuery(id+"F0.wireOp",EDGE,"E3580"),sQuery(id+"F0.wireOp",EDGE,"E3581"),sQuery(id+"F0.wireOp",EDGE,"E3582"),sQuery(id+"F0.wireOp",EDGE,"E3583"),sQuery(id+"F0.wireOp",EDGE,"E3584"),sQuery(id+"F0.wireOp",EDGE,"E3585"),sQuery(id+"F0.wireOp",EDGE,"E3586"),sQuery(id+"F0.wireOp",EDGE,"E3587"),sQuery(id+"F0.wireOp",EDGE,"E3588"),sQuery(id+"F0.wireOp",EDGE,"E3589"),sQuery(id+"F0.wireOp",EDGE,"E3589"),sQuery(id+"F0.wireOp",EDGE,"E3590"),sQuery(id+"F0.wireOp",EDGE,"E3591"),sQuery(id+"F0.wireOp",EDGE,"E3592"),sQuery(id+"F0.wireOp",EDGE,"E3593"),sQuery(id+"F0.wireOp",EDGE,"E3594"),sQuery(id+"F0.wireOp",EDGE,"E3595"),sQuery(id+"F0.wireOp",EDGE,"E3596"),sQuery(id+"F0.wireOp",EDGE,"E3597"),sQuery(id+"F0.wireOp",EDGE,"E3598"),sQuery(id+"F0.wireOp",EDGE,"E3599"),sQuery(id+"F0.wireOp",EDGE,"E3599"),sQuery(id+"F0.wireOp",EDGE,"E3600"),sQuery(id+"F0.wireOp",EDGE,"E3601"),sQuery(id+"F0.wireOp",EDGE,"E3602"),sQuery(id+"F0.wireOp",EDGE,"E3603"),sQuery(id+"F0.wireOp",EDGE,"E3604"),sQuery(id+"F0.wireOp",EDGE,"E3605"),sQuery(id+"F0.wireOp",EDGE,"E3606"),sQuery(id+"F0.wireOp",EDGE,"E3607"),sQuery(id+"F0.wireOp",EDGE,"E3608"),sQuery(id+"F0.wireOp",EDGE,"E3609"),sQuery(id+"F0.wireOp",EDGE,"E3610"),sQuery(id+"F0.wireOp",EDGE,"E3611"),sQuery(id+"F0.wireOp",EDGE,"E3612"),sQuery(id+"F0.wireOp",EDGE,"E3613"),sQuery(id+"F0.wireOp",EDGE,"E3614"),sQuery(id+"F0.wireOp",EDGE,"E3615"),sQuery(id+"F0.wireOp",EDGE,"E3616"),sQuery(id+"F0.wireOp",EDGE,"E3617"),sQuery(id+"F0.wireOp",EDGE,"E3618"),sQuery(id+"F0.wireOp",EDGE,"E3619"),sQuery(id+"F0.wireOp",EDGE,"E3620"),sQuery(id+"F0.wireOp",EDGE,"E3621"),sQuery(id+"F0.wireOp",EDGE,"E3622"),sQuery(id+"F0.wireOp",EDGE,"E3623"),sQuery(id+"F0.wireOp",EDGE,"E3624"),sQuery(id+"F0.wireOp",EDGE,"E3625"),sQuery(id+"F0.wireOp",EDGE,"E3626"),sQuery(id+"F0.wireOp",EDGE,"E3627"),sQuery(id+"F0.wireOp",EDGE,"E3628"),sQuery(id+"F0.wireOp",EDGE,"E3629"),sQuery(id+"F0.wireOp",EDGE,"E3630"),sQuery(id+"F0.wireOp",EDGE,"E3631"),sQuery(id+"F0.wireOp",EDGE,"E3632"),sQuery(id+"F0.wireOp",EDGE,"E3633"),sQuery(id+"F0.wireOp",EDGE,"E3634"),sQuery(id+"F0.wireOp",EDGE,"E3635"),sQuery(id+"F0.wireOp",EDGE,"E3636"),sQuery(id+"F0.wireOp",EDGE,"E3637"),sQuery(id+"F0.wireOp",EDGE,"E3638"),sQuery(id+"F0.wireOp",EDGE,"E3639"),sQuery(id+"F0.wireOp",EDGE,"E3640"),sQuery(id+"F0.wireOp",EDGE,"E3641"),sQuery(id+"F0.wireOp",EDGE,"E3642"),sQuery(id+"F0.wireOp",EDGE,"E3643"),sQuery(id+"F0.wireOp",EDGE,"E3643"),sQuery(id+"F0.wireOp",EDGE,"E3644"),sQuery(id+"F0.wireOp",EDGE,"E3645"),sQuery(id+"F0.wireOp",EDGE,"E3646"),sQuery(id+"F0.wireOp",EDGE,"E3647"),sQuery(id+"F0.wireOp",EDGE,"E3648"),sQuery(id+"F0.wireOp",EDGE,"E3649"),sQuery(id+"F0.wireOp",EDGE,"E3650"),sQuery(id+"F0.wireOp",EDGE,"E3651"),sQuery(id+"F0.wireOp",EDGE,"E3652"),sQuery(id+"F0.wireOp",EDGE,"E3653"),sQuery(id+"F0.wireOp",EDGE,"E3654"),sQuery(id+"F0.wireOp",EDGE,"E3655"),sQuery(id+"F0.wireOp",EDGE,"E3656"),sQuery(id+"F0.wireOp",EDGE,"E3657"),sQuery(id+"F0.wireOp",EDGE,"E3658"),sQuery(id+"F0.wireOp",EDGE,"E3659"),sQuery(id+"F0.wireOp",EDGE,"E3660"),sQuery(id+"F0.wireOp",EDGE,"E3661"),sQuery(id+"F0.wireOp",EDGE,"E3662"),sQuery(id+"F0.wireOp",EDGE,"E3663"),sQuery(id+"F0.wireOp",EDGE,"E3664"),sQuery(id+"F0.wireOp",EDGE,"E3665"),sQuery(id+"F0.wireOp",EDGE,"E3666"),sQuery(id+"F0.wireOp",EDGE,"E3667"),sQuery(id+"F0.wireOp",EDGE,"E3668"),sQuery(id+"F0.wireOp",EDGE,"E3669"),sQuery(id+"F0.wireOp",EDGE,"E3670"),sQuery(id+"F0.wireOp",EDGE,"E3671"),sQuery(id+"F0.wireOp",EDGE,"E3672"),sQuery(id+"F0.wireOp",EDGE,"E3673"),sQuery(id+"F0.wireOp",EDGE,"E3674"),sQuery(id+"F0.wireOp",EDGE,"E3675"),sQuery(id+"F0.wireOp",EDGE,"E3676"),sQuery(id+"F0.wireOp",EDGE,"E3677"),sQuery(id+"F0.wireOp",EDGE,"E3678"),sQuery(id+"F0.wireOp",EDGE,"E3679"),sQuery(id+"F0.wireOp",EDGE,"E3680"),sQuery(id+"F0.wireOp",EDGE,"E3681"),sQuery(id+"F0.wireOp",EDGE,"E3682"),sQuery(id+"F0.wireOp",EDGE,"E3683"),sQuery(id+"F0.wireOp",EDGE,"E3684"),sQuery(id+"F0.wireOp",EDGE,"E3685"),sQuery(id+"F0.wireOp",EDGE,"E3686"),sQuery(id+"F0.wireOp",EDGE,"E3687"),sQuery(id+"F0.wireOp",EDGE,"E3688"),sQuery(id+"F0.wireOp",EDGE,"E3689"),sQuery(id+"F0.wireOp",EDGE,"E3690"),sQuery(id+"F0.wireOp",EDGE,"E3691"),sQuery(id+"F0.wireOp",EDGE,"E3692"),sQuery(id+"F0.wireOp",EDGE,"E3693"),sQuery(id+"F0.wireOp",EDGE,"E3694"),sQuery(id+"F0.wireOp",EDGE,"E3695"),sQuery(id+"F0.wireOp",EDGE,"E3696"),sQuery(id+"F0.wireOp",EDGE,"E3697"),sQuery(id+"F0.wireOp",EDGE,"E3698"),sQuery(id+"F0.wireOp",EDGE,"E3699"),sQuery(id+"F0.wireOp",EDGE,"E3700"),sQuery(id+"F0.wireOp",EDGE,"E3701"),sQuery(id+"F0.wireOp",EDGE,"E3702"),sQuery(id+"F0.wireOp",EDGE,"E3703"),sQuery(id+"F0.wireOp",EDGE,"E3704"),sQuery(id+"F0.wireOp",EDGE,"E3705"),sQuery(id+"F0.wireOp",EDGE,"E3706"),sQuery(id+"F0.wireOp",EDGE,"E3707"),sQuery(id+"F0.wireOp",EDGE,"E3708"),sQuery(id+"F0.wireOp",EDGE,"E3709"),sQuery(id+"F0.wireOp",EDGE,"E3710"),sQuery(id+"F0.wireOp",EDGE,"E3711"),sQuery(id+"F0.wireOp",EDGE,"E3712"),sQuery(id+"F0.wireOp",EDGE,"E3713"),sQuery(id+"F0.wireOp",EDGE,"E3714"),sQuery(id+"F0.wireOp",EDGE,"E3715"),sQuery(id+"F0.wireOp",EDGE,"E3716"),sQuery(id+"F0.wireOp",EDGE,"E3717"),sQuery(id+"F0.wireOp",EDGE,"E3718"),sQuery(id+"F0.wireOp",EDGE,"E3719"),sQuery(id+"F0.wireOp",EDGE,"E3720"),sQuery(id+"F0.wireOp",EDGE,"E3721"),sQuery(id+"F0.wireOp",EDGE,"E3722"),sQuery(id+"F0.wireOp",EDGE,"E3723"),sQuery(id+"F0.wireOp",EDGE,"E3724"),sQuery(id+"F0.wireOp",EDGE,"E3725"),sQuery(id+"F0.wireOp",EDGE,"E3726"),sQuery(id+"F0.wireOp",EDGE,"E3727"),sQuery(id+"F0.wireOp",EDGE,"E3728"),sQuery(id+"F0.wireOp",EDGE,"E3729"),sQuery(id+"F0.wireOp",EDGE,"E3730"),sQuery(id+"F0.wireOp",EDGE,"E3731"),sQuery(id+"F0.wireOp",EDGE,"E3732"),sQuery(id+"F0.wireOp",EDGE,"E3733"),sQuery(id+"F0.wireOp",EDGE,"E3734"),sQuery(id+"F0.wireOp",EDGE,"E3735"),sQuery(id+"F0.wireOp",EDGE,"E3736"),sQuery(id+"F0.wireOp",EDGE,"E3737"),sQuery(id+"F0.wireOp",EDGE,"E3738"),sQuery(id+"F0.wireOp",EDGE,"E3739"),sQuery(id+"F0.wireOp",EDGE,"E3740"),sQuery(id+"F0.wireOp",EDGE,"E3741"),sQuery(id+"F0.wireOp",EDGE,"E3742"),sQuery(id+"F0.wireOp",EDGE,"E3743"),sQuery(id+"F0.wireOp",EDGE,"E3744"),sQuery(id+"F0.wireOp",EDGE,"E3745"),sQuery(id+"F0.wireOp",EDGE,"E3746"),sQuery(id+"F0.wireOp",EDGE,"E3747"),sQuery(id+"F0.wireOp",EDGE,"E3748"),sQuery(id+"F0.wireOp",EDGE,"E3749"),sQuery(id+"F0.wireOp",EDGE,"E3750"),sQuery(id+"F0.wireOp",EDGE,"E3751"),sQuery(id+"F0.wireOp",EDGE,"E3752"),sQuery(id+"F0.wireOp",EDGE,"E3753"),sQuery(id+"F0.wireOp",EDGE,"E3754"),sQuery(id+"F0.wireOp",EDGE,"E3755"),sQuery(id+"F0.wireOp",EDGE,"E3756"),sQuery(id+"F0.wireOp",EDGE,"E3757"),sQuery(id+"F0.wireOp",EDGE,"E3758"),sQuery(id+"F0.wireOp",EDGE,"E3759"),sQuery(id+"F0.wireOp",EDGE,"E3760"),sQuery(id+"F0.wireOp",EDGE,"E3761"),sQuery(id+"F0.wireOp",EDGE,"E3762"),sQuery(id+"F0.wireOp",EDGE,"E3763"),sQuery(id+"F0.wireOp",EDGE,"E3764"),sQuery(id+"F0.wireOp",EDGE,"E3765"),sQuery(id+"F0.wireOp",EDGE,"E3766"),sQuery(id+"F0.wireOp",EDGE,"E3767"),sQuery(id+"F0.wireOp",EDGE,"E3768"),sQuery(id+"F0.wireOp",EDGE,"E3769"),sQuery(id+"F0.wireOp",EDGE,"E3770"),sQuery(id+"F0.wireOp",EDGE,"E3771"),sQuery(id+"F0.wireOp",EDGE,"E3772"),sQuery(id+"F0.wireOp",EDGE,"E3773"),sQuery(id+"F0.wireOp",EDGE,"E3774"),sQuery(id+"F0.wireOp",EDGE,"E3775"),sQuery(id+"F0.wireOp",EDGE,"E3776"),sQuery(id+"F0.wireOp",EDGE,"E3777"),sQuery(id+"F0.wireOp",EDGE,"E3778"),sQuery(id+"F0.wireOp",EDGE,"E3779"),sQuery(id+"F0.wireOp",EDGE,"E3780"),sQuery(id+"F0.wireOp",EDGE,"E3781"),sQuery(id+"F0.wireOp",EDGE,"E3782"),sQuery(id+"F0.wireOp",EDGE,"E3783"),sQuery(id+"F0.wireOp",EDGE,"E3784"),sQuery(id+"F0.wireOp",EDGE,"E3785"),sQuery(id+"F0.wireOp",EDGE,"E3786"),sQuery(id+"F0.wireOp",EDGE,"E3787"),sQuery(id+"F0.wireOp",EDGE,"E3788"),sQuery(id+"F0.wireOp",EDGE,"E3789"),sQuery(id+"F0.wireOp",EDGE,"E3790"),sQuery(id+"F0.wireOp",EDGE,"E3791"),sQuery(id+"F0.wireOp",EDGE,"E3792"),sQuery(id+"F0.wireOp",EDGE,"E3793"),sQuery(id+"F0.wireOp",EDGE,"E3794"),sQuery(id+"F0.wireOp",EDGE,"E3795"),sQuery(id+"F0.wireOp",EDGE,"E3796"),sQuery(id+"F0.wireOp",EDGE,"E3797"),sQuery(id+"F0.wireOp",EDGE,"E3798"),sQuery(id+"F0.wireOp",EDGE,"E3799"),sQuery(id+"F0.wireOp",EDGE,"E3800"),sQuery(id+"F0.wireOp",EDGE,"E3801"),sQuery(id+"F0.wireOp",EDGE,"E3802"),sQuery(id+"F0.wireOp",EDGE,"E3803"),sQuery(id+"F0.wireOp",EDGE,"E3804"),sQuery(id+"F0.wireOp",EDGE,"E3805"),sQuery(id+"F0.wireOp",EDGE,"E3806"),sQuery(id+"F0.wireOp",EDGE,"E3807"),sQuery(id+"F0.wireOp",EDGE,"E3808"),sQuery(id+"F0.wireOp",EDGE,"E3809"),sQuery(id+"F0.wireOp",EDGE,"E3810"),sQuery(id+"F0.wireOp",EDGE,"E3811"),sQuery(id+"F0.wireOp",EDGE,"E3812"),sQuery(id+"F0.wireOp",EDGE,"E3813"),sQuery(id+"F0.wireOp",EDGE,"E3814"),sQuery(id+"F0.wireOp",EDGE,"E3815"),sQuery(id+"F0.wireOp",EDGE,"E3816"),sQuery(id+"F0.wireOp",EDGE,"E3817"),sQuery(id+"F0.wireOp",EDGE,"E3818"),sQuery(id+"F0.wireOp",EDGE,"E3819"),sQuery(id+"F0.wireOp",EDGE,"E3820"),sQuery(id+"F0.wireOp",EDGE,"E3821"),sQuery(id+"F0.wireOp",EDGE,"E3822"),sQuery(id+"F0.wireOp",EDGE,"E3823"),sQuery(id+"F0.wireOp",EDGE,"E3824"),sQuery(id+"F0.wireOp",EDGE,"E3825"),sQuery(id+"F0.wireOp",EDGE,"E3826"),sQuery(id+"F0.wireOp",EDGE,"E3827"),sQuery(id+"F0.wireOp",EDGE,"E3828"),sQuery(id+"F0.wireOp",EDGE,"E3829"),sQuery(id+"F0.wireOp",EDGE,"E3830"),sQuery(id+"F0.wireOp",EDGE,"E3831"),sQuery(id+"F0.wireOp",EDGE,"E3832"),sQuery(id+"F0.wireOp",EDGE,"E3833"),sQuery(id+"F0.wireOp",EDGE,"E3834"),sQuery(id+"F0.wireOp",EDGE,"E3835"),sQuery(id+"F0.wireOp",EDGE,"E3836"),sQuery(id+"F0.wireOp",EDGE,"E3837"),sQuery(id+"F0.wireOp",EDGE,"E3838"),sQuery(id+"F0.wireOp",EDGE,"E3839"),sQuery(id+"F0.wireOp",EDGE,"E3840"),sQuery(id+"F0.wireOp",EDGE,"E3841"),sQuery(id+"F0.wireOp",EDGE,"E3842"),sQuery(id+"F0.wireOp",EDGE,"E3843"),sQuery(id+"F0.wireOp",EDGE,"E3844"),sQuery(id+"F0.wireOp",EDGE,"E3845"),sQuery(id+"F0.wireOp",EDGE,"E3846"),sQuery(id+"F0.wireOp",EDGE,"E3847"),sQuery(id+"F0.wireOp",EDGE,"E3848"),sQuery(id+"F0.wireOp",EDGE,"E3849"),sQuery(id+"F0.wireOp",EDGE,"E3850"),sQuery(id+"F0.wireOp",EDGE,"E3851"),sQuery(id+"F0.wireOp",EDGE,"E3852"),sQuery(id+"F0.wireOp",EDGE,"E3853"),sQuery(id+"F0.wireOp",EDGE,"E3854"),sQuery(id+"F0.wireOp",EDGE,"E3855"),sQuery(id+"F0.wireOp",EDGE,"E3856"),sQuery(id+"F0.wireOp",EDGE,"E3857"),sQuery(id+"F0.wireOp",EDGE,"E3858"),sQuery(id+"F0.wireOp",EDGE,"E3859"),sQuery(id+"F0.wireOp",EDGE,"E3860"),sQuery(id+"F0.wireOp",EDGE,"E3861"),sQuery(id+"F0.wireOp",EDGE,"E3862"),sQuery(id+"F0.wireOp",EDGE,"E3863"),sQuery(id+"F0.wireOp",EDGE,"E3864"),sQuery(id+"F0.wireOp",EDGE,"E3865"),sQuery(id+"F0.wireOp",EDGE,"E3866"),sQuery(id+"F0.wireOp",EDGE,"E3867"),sQuery(id+"F0.wireOp",EDGE,"E3868"),sQuery(id+"F0.wireOp",EDGE,"E3869"),sQuery(id+"F0.wireOp",EDGE,"E3870"),sQuery(id+"F0.wireOp",EDGE,"E3871"),sQuery(id+"F0.wireOp",EDGE,"E3872"),sQuery(id+"F0.wireOp",EDGE,"E3873"),sQuery(id+"F0.wireOp",EDGE,"E3874"),sQuery(id+"F0.wireOp",EDGE,"E3875"),sQuery(id+"F0.wireOp",EDGE,"E3876"),sQuery(id+"F0.wireOp",EDGE,"E3877"),sQuery(id+"F0.wireOp",EDGE,"E3878"),sQuery(id+"F0.wireOp",EDGE,"E3879"),sQuery(id+"F0.wireOp",EDGE,"E3880"),sQuery(id+"F0.wireOp",EDGE,"E3881"),sQuery(id+"F0.wireOp",EDGE,"E3882"),sQuery(id+"F0.wireOp",EDGE,"E3883"),sQuery(id+"F0.wireOp",EDGE,"E3884"),sQuery(id+"F0.wireOp",EDGE,"E3885"),sQuery(id+"F0.wireOp",EDGE,"E3886"),sQuery(id+"F0.wireOp",EDGE,"E3887"),sQuery(id+"F0.wireOp",EDGE,"E3888"),sQuery(id+"F0.wireOp",EDGE,"E3889"),sQuery(id+"F0.wireOp",EDGE,"E3890"),sQuery(id+"F0.wireOp",EDGE,"E3891"),sQuery(id+"F0.wireOp",EDGE,"E3892"),sQuery(id+"F0.wireOp",EDGE,"E3893"),sQuery(id+"F0.wireOp",EDGE,"E3894"),sQuery(id+"F0.wireOp",EDGE,"E3895"),sQuery(id+"F0.wireOp",EDGE,"E3896"),sQuery(id+"F0.wireOp",EDGE,"E3897"),sQuery(id+"F0.wireOp",EDGE,"E3898"),sQuery(id+"F0.wireOp",EDGE,"E3899"),sQuery(id+"F0.wireOp",EDGE,"E3900"),sQuery(id+"F0.wireOp",EDGE,"E3901"),sQuery(id+"F0.wireOp",EDGE,"E3902"),sQuery(id+"F0.wireOp",EDGE,"E3903"),sQuery(id+"F0.wireOp",EDGE,"E3904"),sQuery(id+"F0.wireOp",EDGE,"E3905"),sQuery(id+"F0.wireOp",EDGE,"E3906"),sQuery(id+"F0.wireOp",EDGE,"E3907"),sQuery(id+"F0.wireOp",EDGE,"E3908"),sQuery(id+"F0.wireOp",EDGE,"E3909"),sQuery(id+"F0.wireOp",EDGE,"E3910"),sQuery(id+"F0.wireOp",EDGE,"E3911"),sQuery(id+"F0.wireOp",EDGE,"E3912"),sQuery(id+"F0.wireOp",EDGE,"E3913"),sQuery(id+"F0.wireOp",EDGE,"E3914"),sQuery(id+"F0.wireOp",EDGE,"E3915"),sQuery(id+"F0.wireOp",EDGE,"E3916"),sQuery(id+"F0.wireOp",EDGE,"E3917"),sQuery(id+"F0.wireOp",EDGE,"E3918"),sQuery(id+"F0.wireOp",EDGE,"E3919"),sQuery(id+"F0.wireOp",EDGE,"E3920"),sQuery(id+"F0.wireOp",EDGE,"E3921"),sQuery(id+"F0.wireOp",EDGE,"E3922"),sQuery(id+"F0.wireOp",EDGE,"E3923"),sQuery(id+"F0.wireOp",EDGE,"E3924"),sQuery(id+"F0.wireOp",EDGE,"E3925"),sQuery(id+"F0.wireOp",EDGE,"E3926"),sQuery(id+"F0.wireOp",EDGE,"E3927"),sQuery(id+"F0.wireOp",EDGE,"E3928"),sQuery(id+"F0.wireOp",EDGE,"E3929"),sQuery(id+"F0.wireOp",EDGE,"E3930"),sQuery(id+"F0.wireOp",EDGE,"E3931"),sQuery(id+"F0.wireOp",EDGE,"E3932"),sQuery(id+"F0.wireOp",EDGE,"E3933"),sQuery(id+"F0.wireOp",EDGE,"E3934"),sQuery(id+"F0.wireOp",EDGE,"E3935"),sQuery(id+"F0.wireOp",EDGE,"E3936"),sQuery(id+"F0.wireOp",EDGE,"E3937"),sQuery(id+"F0.wireOp",EDGE,"E3938"),sQuery(id+"F0.wireOp",EDGE,"E3939"),sQuery(id+"F0.wireOp",EDGE,"E3940"),sQuery(id+"F0.wireOp",EDGE,"E3941"),sQuery(id+"F0.wireOp",EDGE,"E3942"),sQuery(id+"F0.wireOp",EDGE,"E3943"),sQuery(id+"F0.wireOp",EDGE,"E3944"),sQuery(id+"F0.wireOp",EDGE,"E3945"),sQuery(id+"F0.wireOp",EDGE,"E3946"),sQuery(id+"F0.wireOp",EDGE,"E3947"),sQuery(id+"F0.wireOp",EDGE,"E3948"),sQuery(id+"F0.wireOp",EDGE,"E3949"),sQuery(id+"F0.wireOp",EDGE,"E3950"),sQuery(id+"F0.wireOp",EDGE,"E3951"),sQuery(id+"F0.wireOp",EDGE,"E3952"),sQuery(id+"F0.wireOp",EDGE,"E3953"),sQuery(id+"F0.wireOp",EDGE,"E3954"),sQuery(id+"F0.wireOp",EDGE,"E3955"),sQuery(id+"F0.wireOp",EDGE,"E3956"),sQuery(id+"F0.wireOp",EDGE,"E3957"),sQuery(id+"F0.wireOp",EDGE,"E3958"),sQuery(id+"F0.wireOp",EDGE,"E3959"),sQuery(id+"F0.wireOp",EDGE,"E3960"),sQuery(id+"F0.wireOp",EDGE,"E3961"),sQuery(id+"F0.wireOp",EDGE,"E3962"),sQuery(id+"F0.wireOp",EDGE,"E3963"),sQuery(id+"F0.wireOp",EDGE,"E3964"),sQuery(id+"F0.wireOp",EDGE,"E3965"),sQuery(id+"F0.wireOp",EDGE,"E3966"),sQuery(id+"F0.wireOp",EDGE,"E3967"),sQuery(id+"F0.wireOp",EDGE,"E3968"),sQuery(id+"F0.wireOp",EDGE,"E3969"),sQuery(id+"F0.wireOp",EDGE,"E3970"),sQuery(id+"F0.wireOp",EDGE,"E3971"),sQuery(id+"F0.wireOp",EDGE,"E3972"),sQuery(id+"F0.wireOp",EDGE,"E3973"),sQuery(id+"F0.wireOp",EDGE,"E3974"),sQuery(id+"F0.wireOp",EDGE,"E3975"),sQuery(id+"F0.wireOp",EDGE,"E3976"),sQuery(id+"F0.wireOp",EDGE,"E3977"),sQuery(id+"F0.wireOp",EDGE,"E3978"),sQuery(id+"F0.wireOp",EDGE,"E3979"),sQuery(id+"F0.wireOp",EDGE,"E3980"),sQuery(id+"F0.wireOp",EDGE,"E3981"),sQuery(id+"F0.wireOp",EDGE,"E3982"),sQuery(id+"F0.wireOp",EDGE,"E3983"),sQuery(id+"F0.wireOp",EDGE,"E3984"),sQuery(id+"F0.wireOp",EDGE,"E3985"),sQuery(id+"F0.wireOp",EDGE,"E3986"),sQuery(id+"F0.wireOp",EDGE,"E3987"),sQuery(id+"F0.wireOp",EDGE,"E3988"),sQuery(id+"F0.wireOp",EDGE,"E3989"),sQuery(id+"F0.wireOp",EDGE,"E3990"),sQuery(id+"F0.wireOp",EDGE,"E3991"),sQuery(id+"F0.wireOp",EDGE,"E3992"),sQuery(id+"F0.wireOp",EDGE,"E3993"),sQuery(id+"F0.wireOp",EDGE,"E3993"),sQuery(id+"F0.wireOp",EDGE,"E3994"),sQuery(id+"F0.wireOp",EDGE,"E3995"),sQuery(id+"F0.wireOp",EDGE,"E3996"),sQuery(id+"F0.wireOp",EDGE,"E3997"),sQuery(id+"F0.wireOp",EDGE,"E3998"),sQuery(id+"F0.wireOp",EDGE,"E3999"),sQuery(id+"F0.wireOp",EDGE,"E4000"),sQuery(id+"F0.wireOp",EDGE,"E4001"),sQuery(id+"F0.wireOp",EDGE,"E4002"),sQuery(id+"F0.wireOp",EDGE,"E4003"),sQuery(id+"F0.wireOp",EDGE,"E4004"),sQuery(id+"F0.wireOp",EDGE,"E4005"),sQuery(id+"F0.wireOp",EDGE,"E4006"),sQuery(id+"F0.wireOp",EDGE,"E4007"),sQuery(id+"F0.wireOp",EDGE,"E4008"),sQuery(id+"F0.wireOp",EDGE,"E4009"),sQuery(id+"F0.wireOp",EDGE,"E4010"),sQuery(id+"F0.wireOp",EDGE,"E4011"),sQuery(id+"F0.wireOp",EDGE,"E4012"),sQuery(id+"F0.wireOp",EDGE,"E4013"),sQuery(id+"F0.wireOp",EDGE,"E4014"),sQuery(id+"F0.wireOp",EDGE,"E4015"),sQuery(id+"F0.wireOp",EDGE,"E4016"),sQuery(id+"F0.wireOp",EDGE,"E4017"),sQuery(id+"F0.wireOp",EDGE,"E4018"),sQuery(id+"F0.wireOp",EDGE,"E4019"),sQuery(id+"F0.wireOp",EDGE,"E4020"),sQuery(id+"F0.wireOp",EDGE,"E4021"),sQuery(id+"F0.wireOp",EDGE,"E4022"),sQuery(id+"F0.wireOp",EDGE,"E4023"),sQuery(id+"F0.wireOp",EDGE,"E4024"),sQuery(id+"F0.wireOp",EDGE,"E4025"),sQuery(id+"F0.wireOp",EDGE,"E4026"),sQuery(id+"F0.wireOp",EDGE,"E4027"),sQuery(id+"F0.wireOp",EDGE,"E4028"),sQuery(id+"F0.wireOp",EDGE,"E4029"),sQuery(id+"F0.wireOp",EDGE,"E4030"),sQuery(id+"F0.wireOp",EDGE,"E4031"),sQuery(id+"F0.wireOp",EDGE,"E4032"),sQuery(id+"F0.wireOp",EDGE,"E4033"),sQuery(id+"F0.wireOp",EDGE,"E4034"),sQuery(id+"F0.wireOp",EDGE,"E4035"),sQuery(id+"F0.wireOp",EDGE,"E4036"),sQuery(id+"F0.wireOp",EDGE,"E4037"),sQuery(id+"F0.wireOp",EDGE,"E4038"),sQuery(id+"F0.wireOp",EDGE,"E4039"),sQuery(id+"F0.wireOp",EDGE,"E4040"),sQuery(id+"F0.wireOp",EDGE,"E4041"),sQuery(id+"F0.wireOp",EDGE,"E4042"),sQuery(id+"F0.wireOp",EDGE,"E4043")])]});
            var Q2;
            Q2=makeQuery(id+"F1.opExtrude","SWEPT_BODY",BODY,{"disambiguationData":[OSD([sQuery(id+"F0.wireOp",EDGE,"E4044"),sQuery(id+"F0.wireOp",EDGE,"E4045"),sQuery(id+"F0.wireOp",EDGE,"E4046"),sQuery(id+"F0.wireOp",EDGE,"E4047"),sQuery(id+"F0.wireOp",EDGE,"E4048"),sQuery(id+"F0.wireOp",EDGE,"E4049"),sQuery(id+"F0.wireOp",EDGE,"E4050"),sQuery(id+"F0.wireOp",EDGE,"E4051"),sQuery(id+"F0.wireOp",EDGE,"E4052"),sQuery(id+"F0.wireOp",EDGE,"E4053"),sQuery(id+"F0.wireOp",EDGE,"E4054"),sQuery(id+"F0.wireOp",EDGE,"E4055"),sQuery(id+"F0.wireOp",EDGE,"E4056"),sQuery(id+"F0.wireOp",EDGE,"E4057"),sQuery(id+"F0.wireOp",EDGE,"E4058"),sQuery(id+"F0.wireOp",EDGE,"E4059"),sQuery(id+"F0.wireOp",EDGE,"E4060"),sQuery(id+"F0.wireOp",EDGE,"E4061"),sQuery(id+"F0.wireOp",EDGE,"E4062"),sQuery(id+"F0.wireOp",EDGE,"E4063"),sQuery(id+"F0.wireOp",EDGE,"E4064"),sQuery(id+"F0.wireOp",EDGE,"E4065"),sQuery(id+"F0.wireOp",EDGE,"E4066"),sQuery(id+"F0.wireOp",EDGE,"E4067"),sQuery(id+"F0.wireOp",EDGE,"E4068"),sQuery(id+"F0.wireOp",EDGE,"E4069"),sQuery(id+"F0.wireOp",EDGE,"E4070"),sQuery(id+"F0.wireOp",EDGE,"E4071"),sQuery(id+"F0.wireOp",EDGE,"E4072"),sQuery(id+"F0.wireOp",EDGE,"E4073"),sQuery(id+"F0.wireOp",EDGE,"E4074"),sQuery(id+"F0.wireOp",EDGE,"E4075"),sQuery(id+"F0.wireOp",EDGE,"E4076"),sQuery(id+"F0.wireOp",EDGE,"E4077"),sQuery(id+"F0.wireOp",EDGE,"E4078"),sQuery(id+"F0.wireOp",EDGE,"E4079"),sQuery(id+"F0.wireOp",EDGE,"E4080"),sQuery(id+"F0.wireOp",EDGE,"E4081"),sQuery(id+"F0.wireOp",EDGE,"E4082"),sQuery(id+"F0.wireOp",EDGE,"E4083"),sQuery(id+"F0.wireOp",EDGE,"E4084"),sQuery(id+"F0.wireOp",EDGE,"E4085"),sQuery(id+"F0.wireOp",EDGE,"E4086"),sQuery(id+"F0.wireOp",EDGE,"E4087"),sQuery(id+"F0.wireOp",EDGE,"E4088"),sQuery(id+"F0.wireOp",EDGE,"E4089"),sQuery(id+"F0.wireOp",EDGE,"E4090"),sQuery(id+"F0.wireOp",EDGE,"E4091"),sQuery(id+"F0.wireOp",EDGE,"E4092"),sQuery(id+"F0.wireOp",EDGE,"E4093"),sQuery(id+"F0.wireOp",EDGE,"E4094"),sQuery(id+"F0.wireOp",EDGE,"E4095"),sQuery(id+"F0.wireOp",EDGE,"E4096"),sQuery(id+"F0.wireOp",EDGE,"E4097"),sQuery(id+"F0.wireOp",EDGE,"E4098"),sQuery(id+"F0.wireOp",EDGE,"E4099"),sQuery(id+"F0.wireOp",EDGE,"E4100"),sQuery(id+"F0.wireOp",EDGE,"E4101"),sQuery(id+"F0.wireOp",EDGE,"E4102"),sQuery(id+"F0.wireOp",EDGE,"E4103"),sQuery(id+"F0.wireOp",EDGE,"E4104"),sQuery(id+"F0.wireOp",EDGE,"E4105"),sQuery(id+"F0.wireOp",EDGE,"E4106"),sQuery(id+"F0.wireOp",EDGE,"E4107"),sQuery(id+"F0.wireOp",EDGE,"E4108"),sQuery(id+"F0.wireOp",EDGE,"E4109"),sQuery(id+"F0.wireOp",EDGE,"E4110"),sQuery(id+"F0.wireOp",EDGE,"E4111"),sQuery(id+"F0.wireOp",EDGE,"E4112"),sQuery(id+"F0.wireOp",EDGE,"E4113"),sQuery(id+"F0.wireOp",EDGE,"E4114"),sQuery(id+"F0.wireOp",EDGE,"E4115"),sQuery(id+"F0.wireOp",EDGE,"E4116"),sQuery(id+"F0.wireOp",EDGE,"E4117"),sQuery(id+"F0.wireOp",EDGE,"E4118"),sQuery(id+"F0.wireOp",EDGE,"E4119"),sQuery(id+"F0.wireOp",EDGE,"E4120"),sQuery(id+"F0.wireOp",EDGE,"E4121"),sQuery(id+"F0.wireOp",EDGE,"E4122"),sQuery(id+"F0.wireOp",EDGE,"E4123"),sQuery(id+"F0.wireOp",EDGE,"E4124"),sQuery(id+"F0.wireOp",EDGE,"E4125"),sQuery(id+"F0.wireOp",EDGE,"E4126"),sQuery(id+"F0.wireOp",EDGE,"E4127"),sQuery(id+"F0.wireOp",EDGE,"E4128"),sQuery(id+"F0.wireOp",EDGE,"E4129"),sQuery(id+"F0.wireOp",EDGE,"E4130"),sQuery(id+"F0.wireOp",EDGE,"E4131"),sQuery(id+"F0.wireOp",EDGE,"E4132"),sQuery(id+"F0.wireOp",EDGE,"E4133"),sQuery(id+"F0.wireOp",EDGE,"E4134"),sQuery(id+"F0.wireOp",EDGE,"E4135"),sQuery(id+"F0.wireOp",EDGE,"E4136"),sQuery(id+"F0.wireOp",EDGE,"E4137"),sQuery(id+"F0.wireOp",EDGE,"E4138"),sQuery(id+"F0.wireOp",EDGE,"E4139"),sQuery(id+"F0.wireOp",EDGE,"E4140"),sQuery(id+"F0.wireOp",EDGE,"E4141"),sQuery(id+"F0.wireOp",EDGE,"E4142"),sQuery(id+"F0.wireOp",EDGE,"E4143"),sQuery(id+"F0.wireOp",EDGE,"E4144"),sQuery(id+"F0.wireOp",EDGE,"E4145"),sQuery(id+"F0.wireOp",EDGE,"E4146"),sQuery(id+"F0.wireOp",EDGE,"E4146"),sQuery(id+"F0.wireOp",EDGE,"E4147"),sQuery(id+"F0.wireOp",EDGE,"E4148"),sQuery(id+"F0.wireOp",EDGE,"E4149"),sQuery(id+"F0.wireOp",EDGE,"E4150"),sQuery(id+"F0.wireOp",EDGE,"E4151"),sQuery(id+"F0.wireOp",EDGE,"E4152"),sQuery(id+"F0.wireOp",EDGE,"E4153"),sQuery(id+"F0.wireOp",EDGE,"E4154"),sQuery(id+"F0.wireOp",EDGE,"E4155"),sQuery(id+"F0.wireOp",EDGE,"E4156"),sQuery(id+"F0.wireOp",EDGE,"E4157"),sQuery(id+"F0.wireOp",EDGE,"E4158"),sQuery(id+"F0.wireOp",EDGE,"E4159"),sQuery(id+"F0.wireOp",EDGE,"E4160"),sQuery(id+"F0.wireOp",EDGE,"E4161"),sQuery(id+"F0.wireOp",EDGE,"E4162"),sQuery(id+"F0.wireOp",EDGE,"E4163"),sQuery(id+"F0.wireOp",EDGE,"E4164"),sQuery(id+"F0.wireOp",EDGE,"E4165"),sQuery(id+"F0.wireOp",EDGE,"E4166"),sQuery(id+"F0.wireOp",EDGE,"E4167"),sQuery(id+"F0.wireOp",EDGE,"E4167"),sQuery(id+"F0.wireOp",EDGE,"E4168"),sQuery(id+"F0.wireOp",EDGE,"E4169"),sQuery(id+"F0.wireOp",EDGE,"E4170"),sQuery(id+"F0.wireOp",EDGE,"E4171"),sQuery(id+"F0.wireOp",EDGE,"E4172"),sQuery(id+"F0.wireOp",EDGE,"E4173"),sQuery(id+"F0.wireOp",EDGE,"E4174"),sQuery(id+"F0.wireOp",EDGE,"E4175"),sQuery(id+"F0.wireOp",EDGE,"E4176"),sQuery(id+"F0.wireOp",EDGE,"E4177"),sQuery(id+"F0.wireOp",EDGE,"E4178"),sQuery(id+"F0.wireOp",EDGE,"E4179"),sQuery(id+"F0.wireOp",EDGE,"E4179"),sQuery(id+"F0.wireOp",EDGE,"E4180"),sQuery(id+"F0.wireOp",EDGE,"E4181"),sQuery(id+"F0.wireOp",EDGE,"E4182"),sQuery(id+"F0.wireOp",EDGE,"E4183"),sQuery(id+"F0.wireOp",EDGE,"E4184"),sQuery(id+"F0.wireOp",EDGE,"E4185"),sQuery(id+"F0.wireOp",EDGE,"E4186"),sQuery(id+"F0.wireOp",EDGE,"E4187"),sQuery(id+"F0.wireOp",EDGE,"E4188"),sQuery(id+"F0.wireOp",EDGE,"E4189"),sQuery(id+"F0.wireOp",EDGE,"E4190"),sQuery(id+"F0.wireOp",EDGE,"E4191"),sQuery(id+"F0.wireOp",EDGE,"E4192"),sQuery(id+"F0.wireOp",EDGE,"E4193"),sQuery(id+"F0.wireOp",EDGE,"E4194"),sQuery(id+"F0.wireOp",EDGE,"E4195"),sQuery(id+"F0.wireOp",EDGE,"E4196"),sQuery(id+"F0.wireOp",EDGE,"E4196"),sQuery(id+"F0.wireOp",EDGE,"E4196"),sQuery(id+"F0.wireOp",EDGE,"E4197"),sQuery(id+"F0.wireOp",EDGE,"E4198"),sQuery(id+"F0.wireOp",EDGE,"E4199"),sQuery(id+"F0.wireOp",EDGE,"E4200"),sQuery(id+"F0.wireOp",EDGE,"E4201"),sQuery(id+"F0.wireOp",EDGE,"E4201"),sQuery(id+"F0.wireOp",EDGE,"E4202"),sQuery(id+"F0.wireOp",EDGE,"E4203"),sQuery(id+"F0.wireOp",EDGE,"E4204"),sQuery(id+"F0.wireOp",EDGE,"E4205"),sQuery(id+"F0.wireOp",EDGE,"E4206"),sQuery(id+"F0.wireOp",EDGE,"E4206"),sQuery(id+"F0.wireOp",EDGE,"E4207"),sQuery(id+"F0.wireOp",EDGE,"E4208"),sQuery(id+"F0.wireOp",EDGE,"E4209"),sQuery(id+"F0.wireOp",EDGE,"E4209"),sQuery(id+"F0.wireOp",EDGE,"E4210"),sQuery(id+"F0.wireOp",EDGE,"E4211"),sQuery(id+"F0.wireOp",EDGE,"E4212"),sQuery(id+"F0.wireOp",EDGE,"E4213"),sQuery(id+"F0.wireOp",EDGE,"E4213"),sQuery(id+"F0.wireOp",EDGE,"E4214"),sQuery(id+"F0.wireOp",EDGE,"E4215"),sQuery(id+"F0.wireOp",EDGE,"E4215"),sQuery(id+"F0.wireOp",EDGE,"E4216"),sQuery(id+"F0.wireOp",EDGE,"E4217"),sQuery(id+"F0.wireOp",EDGE,"E4218"),sQuery(id+"F0.wireOp",EDGE,"E4219"),sQuery(id+"F0.wireOp",EDGE,"E4220"),sQuery(id+"F0.wireOp",EDGE,"E4221"),sQuery(id+"F0.wireOp",EDGE,"E4222"),sQuery(id+"F0.wireOp",EDGE,"E4223"),sQuery(id+"F0.wireOp",EDGE,"E4224"),sQuery(id+"F0.wireOp",EDGE,"E4225"),sQuery(id+"F0.wireOp",EDGE,"E4226"),sQuery(id+"F0.wireOp",EDGE,"E4227"),sQuery(id+"F0.wireOp",EDGE,"E4228"),sQuery(id+"F0.wireOp",EDGE,"E4229"),sQuery(id+"F0.wireOp",EDGE,"E4230"),sQuery(id+"F0.wireOp",EDGE,"E4231"),sQuery(id+"F0.wireOp",EDGE,"E4232"),sQuery(id+"F0.wireOp",EDGE,"E4233"),sQuery(id+"F0.wireOp",EDGE,"E4234"),sQuery(id+"F0.wireOp",EDGE,"E4235"),sQuery(id+"F0.wireOp",EDGE,"E4236"),sQuery(id+"F0.wireOp",EDGE,"E4237"),sQuery(id+"F0.wireOp",EDGE,"E4238"),sQuery(id+"F0.wireOp",EDGE,"E4239"),sQuery(id+"F0.wireOp",EDGE,"E4240"),sQuery(id+"F0.wireOp",EDGE,"E4241"),sQuery(id+"F0.wireOp",EDGE,"E4242"),sQuery(id+"F0.wireOp",EDGE,"E4243"),sQuery(id+"F0.wireOp",EDGE,"E4244"),sQuery(id+"F0.wireOp",EDGE,"E4245"),sQuery(id+"F0.wireOp",EDGE,"E4246"),sQuery(id+"F0.wireOp",EDGE,"E4247"),sQuery(id+"F0.wireOp",EDGE,"E4248"),sQuery(id+"F0.wireOp",EDGE,"E4249"),sQuery(id+"F0.wireOp",EDGE,"E4250"),sQuery(id+"F0.wireOp",EDGE,"E4251"),sQuery(id+"F0.wireOp",EDGE,"E4252"),sQuery(id+"F0.wireOp",EDGE,"E4253"),sQuery(id+"F0.wireOp",EDGE,"E4254"),sQuery(id+"F0.wireOp",EDGE,"E4255"),sQuery(id+"F0.wireOp",EDGE,"E4256"),sQuery(id+"F0.wireOp",EDGE,"E4257"),sQuery(id+"F0.wireOp",EDGE,"E4258"),sQuery(id+"F0.wireOp",EDGE,"E4259"),sQuery(id+"F0.wireOp",EDGE,"E4260"),sQuery(id+"F0.wireOp",EDGE,"E4261"),sQuery(id+"F0.wireOp",EDGE,"E4262"),sQuery(id+"F0.wireOp",EDGE,"E4263"),sQuery(id+"F0.wireOp",EDGE,"E4264"),sQuery(id+"F0.wireOp",EDGE,"E4265"),sQuery(id+"F0.wireOp",EDGE,"E4266"),sQuery(id+"F0.wireOp",EDGE,"E4267"),sQuery(id+"F0.wireOp",EDGE,"E4268"),sQuery(id+"F0.wireOp",EDGE,"E4269"),sQuery(id+"F0.wireOp",EDGE,"E4270"),sQuery(id+"F0.wireOp",EDGE,"E4271"),sQuery(id+"F0.wireOp",EDGE,"E4272"),sQuery(id+"F0.wireOp",EDGE,"E4273"),sQuery(id+"F0.wireOp",EDGE,"E4274"),sQuery(id+"F0.wireOp",EDGE,"E4275"),sQuery(id+"F0.wireOp",EDGE,"E4276"),sQuery(id+"F0.wireOp",EDGE,"E4277"),sQuery(id+"F0.wireOp",EDGE,"E4278"),sQuery(id+"F0.wireOp",EDGE,"E4279"),sQuery(id+"F0.wireOp",EDGE,"E4280"),sQuery(id+"F0.wireOp",EDGE,"E4281"),sQuery(id+"F0.wireOp",EDGE,"E4282"),sQuery(id+"F0.wireOp",EDGE,"E4283"),sQuery(id+"F0.wireOp",EDGE,"E4284"),sQuery(id+"F0.wireOp",EDGE,"E4285"),sQuery(id+"F0.wireOp",EDGE,"E4286"),sQuery(id+"F0.wireOp",EDGE,"E4287"),sQuery(id+"F0.wireOp",EDGE,"E4288"),sQuery(id+"F0.wireOp",EDGE,"E4289"),sQuery(id+"F0.wireOp",EDGE,"E4290"),sQuery(id+"F0.wireOp",EDGE,"E4291"),sQuery(id+"F0.wireOp",EDGE,"E4292"),sQuery(id+"F0.wireOp",EDGE,"E4293"),sQuery(id+"F0.wireOp",EDGE,"E4294"),sQuery(id+"F0.wireOp",EDGE,"E4295"),sQuery(id+"F0.wireOp",EDGE,"E4296"),sQuery(id+"F0.wireOp",EDGE,"E4297"),sQuery(id+"F0.wireOp",EDGE,"E4298"),sQuery(id+"F0.wireOp",EDGE,"E4299"),sQuery(id+"F0.wireOp",EDGE,"E4300"),sQuery(id+"F0.wireOp",EDGE,"E4301"),sQuery(id+"F0.wireOp",EDGE,"E4302"),sQuery(id+"F0.wireOp",EDGE,"E4303"),sQuery(id+"F0.wireOp",EDGE,"E4304"),sQuery(id+"F0.wireOp",EDGE,"E4305"),sQuery(id+"F0.wireOp",EDGE,"E4306"),sQuery(id+"F0.wireOp",EDGE,"E4307"),sQuery(id+"F0.wireOp",EDGE,"E4308"),sQuery(id+"F0.wireOp",EDGE,"E4309"),sQuery(id+"F0.wireOp",EDGE,"E4310"),sQuery(id+"F0.wireOp",EDGE,"E4311"),sQuery(id+"F0.wireOp",EDGE,"E4312"),sQuery(id+"F0.wireOp",EDGE,"E4313"),sQuery(id+"F0.wireOp",EDGE,"E4314"),sQuery(id+"F0.wireOp",EDGE,"E4315"),sQuery(id+"F0.wireOp",EDGE,"E4316"),sQuery(id+"F0.wireOp",EDGE,"E4317"),sQuery(id+"F0.wireOp",EDGE,"E4318"),sQuery(id+"F0.wireOp",EDGE,"E4319"),sQuery(id+"F0.wireOp",EDGE,"E4320"),sQuery(id+"F0.wireOp",EDGE,"E4321"),sQuery(id+"F0.wireOp",EDGE,"E4322"),sQuery(id+"F0.wireOp",EDGE,"E4323"),sQuery(id+"F0.wireOp",EDGE,"E4324"),sQuery(id+"F0.wireOp",EDGE,"E4325"),sQuery(id+"F0.wireOp",EDGE,"E4326"),sQuery(id+"F0.wireOp",EDGE,"E4327"),sQuery(id+"F0.wireOp",EDGE,"E4328"),sQuery(id+"F0.wireOp",EDGE,"E4329"),sQuery(id+"F0.wireOp",EDGE,"E4330"),sQuery(id+"F0.wireOp",EDGE,"E4331"),sQuery(id+"F0.wireOp",EDGE,"E4332"),sQuery(id+"F0.wireOp",EDGE,"E4333"),sQuery(id+"F0.wireOp",EDGE,"E4334"),sQuery(id+"F0.wireOp",EDGE,"E4335"),sQuery(id+"F0.wireOp",EDGE,"E4336"),sQuery(id+"F0.wireOp",EDGE,"E4337"),sQuery(id+"F0.wireOp",EDGE,"E4338"),sQuery(id+"F0.wireOp",EDGE,"E4339"),sQuery(id+"F0.wireOp",EDGE,"E4340"),sQuery(id+"F0.wireOp",EDGE,"E4341"),sQuery(id+"F0.wireOp",EDGE,"E4342"),sQuery(id+"F0.wireOp",EDGE,"E4343"),sQuery(id+"F0.wireOp",EDGE,"E4344"),sQuery(id+"F0.wireOp",EDGE,"E4345"),sQuery(id+"F0.wireOp",EDGE,"E4346"),sQuery(id+"F0.wireOp",EDGE,"E4347"),sQuery(id+"F0.wireOp",EDGE,"E4348"),sQuery(id+"F0.wireOp",EDGE,"E4349"),sQuery(id+"F0.wireOp",EDGE,"E4350"),sQuery(id+"F0.wireOp",EDGE,"E4351"),sQuery(id+"F0.wireOp",EDGE,"E4352"),sQuery(id+"F0.wireOp",EDGE,"E4353"),sQuery(id+"F0.wireOp",EDGE,"E4354"),sQuery(id+"F0.wireOp",EDGE,"E4355"),sQuery(id+"F0.wireOp",EDGE,"E4356"),sQuery(id+"F0.wireOp",EDGE,"E4357"),sQuery(id+"F0.wireOp",EDGE,"E4358"),sQuery(id+"F0.wireOp",EDGE,"E4359"),sQuery(id+"F0.wireOp",EDGE,"E4360"),sQuery(id+"F0.wireOp",EDGE,"E4361"),sQuery(id+"F0.wireOp",EDGE,"E4362"),sQuery(id+"F0.wireOp",EDGE,"E4363"),sQuery(id+"F0.wireOp",EDGE,"E4364"),sQuery(id+"F0.wireOp",EDGE,"E4365"),sQuery(id+"F0.wireOp",EDGE,"E4366"),sQuery(id+"F0.wireOp",EDGE,"E4367"),sQuery(id+"F0.wireOp",EDGE,"E4368"),sQuery(id+"F0.wireOp",EDGE,"E4369"),sQuery(id+"F0.wireOp",EDGE,"E4370"),sQuery(id+"F0.wireOp",EDGE,"E4371"),sQuery(id+"F0.wireOp",EDGE,"E4372"),sQuery(id+"F0.wireOp",EDGE,"E4373"),sQuery(id+"F0.wireOp",EDGE,"E4374"),sQuery(id+"F0.wireOp",EDGE,"E4375"),sQuery(id+"F0.wireOp",EDGE,"E4376"),sQuery(id+"F0.wireOp",EDGE,"E4377"),sQuery(id+"F0.wireOp",EDGE,"E4378"),sQuery(id+"F0.wireOp",EDGE,"E4379"),sQuery(id+"F0.wireOp",EDGE,"E4380"),sQuery(id+"F0.wireOp",EDGE,"E4381"),sQuery(id+"F0.wireOp",EDGE,"E4382"),sQuery(id+"F0.wireOp",EDGE,"E4383"),sQuery(id+"F0.wireOp",EDGE,"E4384"),sQuery(id+"F0.wireOp",EDGE,"E4385"),sQuery(id+"F0.wireOp",EDGE,"E4386"),sQuery(id+"F0.wireOp",EDGE,"E4387"),sQuery(id+"F0.wireOp",EDGE,"E4388"),sQuery(id+"F0.wireOp",EDGE,"E4389"),sQuery(id+"F0.wireOp",EDGE,"E4390"),sQuery(id+"F0.wireOp",EDGE,"E4391"),sQuery(id+"F0.wireOp",EDGE,"E4392"),sQuery(id+"F0.wireOp",EDGE,"E4393"),sQuery(id+"F0.wireOp",EDGE,"E4394"),sQuery(id+"F0.wireOp",EDGE,"E4395"),sQuery(id+"F0.wireOp",EDGE,"E4396"),sQuery(id+"F0.wireOp",EDGE,"E4397"),sQuery(id+"F0.wireOp",EDGE,"E4398"),sQuery(id+"F0.wireOp",EDGE,"E4399"),sQuery(id+"F0.wireOp",EDGE,"E4400"),sQuery(id+"F0.wireOp",EDGE,"E4401"),sQuery(id+"F0.wireOp",EDGE,"E4402"),sQuery(id+"F0.wireOp",EDGE,"E4403"),sQuery(id+"F0.wireOp",EDGE,"E4404"),sQuery(id+"F0.wireOp",EDGE,"E4405"),sQuery(id+"F0.wireOp",EDGE,"E4406"),sQuery(id+"F0.wireOp",EDGE,"E4407"),sQuery(id+"F0.wireOp",EDGE,"E4408"),sQuery(id+"F0.wireOp",EDGE,"E4409"),sQuery(id+"F0.wireOp",EDGE,"E4410"),sQuery(id+"F0.wireOp",EDGE,"E4411"),sQuery(id+"F0.wireOp",EDGE,"E4412"),sQuery(id+"F0.wireOp",EDGE,"E4413"),sQuery(id+"F0.wireOp",EDGE,"E4414"),sQuery(id+"F0.wireOp",EDGE,"E4415"),sQuery(id+"F0.wireOp",EDGE,"E4416"),sQuery(id+"F0.wireOp",EDGE,"E4417"),sQuery(id+"F0.wireOp",EDGE,"E4418"),sQuery(id+"F0.wireOp",EDGE,"E4419"),sQuery(id+"F0.wireOp",EDGE,"E4420"),sQuery(id+"F0.wireOp",EDGE,"E4421"),sQuery(id+"F0.wireOp",EDGE,"E4422"),sQuery(id+"F0.wireOp",EDGE,"E4423"),sQuery(id+"F0.wireOp",EDGE,"E4424"),sQuery(id+"F0.wireOp",EDGE,"E4425"),sQuery(id+"F0.wireOp",EDGE,"E4426"),sQuery(id+"F0.wireOp",EDGE,"E4427"),sQuery(id+"F0.wireOp",EDGE,"E4428"),sQuery(id+"F0.wireOp",EDGE,"E4429"),sQuery(id+"F0.wireOp",EDGE,"E4430"),sQuery(id+"F0.wireOp",EDGE,"E4431"),sQuery(id+"F0.wireOp",EDGE,"E4432"),sQuery(id+"F0.wireOp",EDGE,"E4433"),sQuery(id+"F0.wireOp",EDGE,"E4433"),sQuery(id+"F0.wireOp",EDGE,"E4434"),sQuery(id+"F0.wireOp",EDGE,"E4435"),sQuery(id+"F0.wireOp",EDGE,"E4436"),sQuery(id+"F0.wireOp",EDGE,"E4437"),sQuery(id+"F0.wireOp",EDGE,"E4438"),sQuery(id+"F0.wireOp",EDGE,"E4439"),sQuery(id+"F0.wireOp",EDGE,"E4440"),sQuery(id+"F0.wireOp",EDGE,"E4441"),sQuery(id+"F0.wireOp",EDGE,"E4442"),sQuery(id+"F0.wireOp",EDGE,"E4443"),sQuery(id+"F0.wireOp",EDGE,"E4444"),sQuery(id+"F0.wireOp",EDGE,"E4445"),sQuery(id+"F0.wireOp",EDGE,"E4446"),sQuery(id+"F0.wireOp",EDGE,"E4447"),sQuery(id+"F0.wireOp",EDGE,"E4448"),sQuery(id+"F0.wireOp",EDGE,"E4449"),sQuery(id+"F0.wireOp",EDGE,"E4450"),sQuery(id+"F0.wireOp",EDGE,"E4451"),sQuery(id+"F0.wireOp",EDGE,"E4452"),sQuery(id+"F0.wireOp",EDGE,"E4453"),sQuery(id+"F0.wireOp",EDGE,"E4454"),sQuery(id+"F0.wireOp",EDGE,"E4455"),sQuery(id+"F0.wireOp",EDGE,"E4456"),sQuery(id+"F0.wireOp",EDGE,"E4457"),sQuery(id+"F0.wireOp",EDGE,"E4458"),sQuery(id+"F0.wireOp",EDGE,"E4459"),sQuery(id+"F0.wireOp",EDGE,"E4460"),sQuery(id+"F0.wireOp",EDGE,"E4461"),sQuery(id+"F0.wireOp",EDGE,"E4462"),sQuery(id+"F0.wireOp",EDGE,"E4463"),sQuery(id+"F0.wireOp",EDGE,"E4464"),sQuery(id+"F0.wireOp",EDGE,"E4465"),sQuery(id+"F0.wireOp",EDGE,"E4466"),sQuery(id+"F0.wireOp",EDGE,"E4467"),sQuery(id+"F0.wireOp",EDGE,"E4468"),sQuery(id+"F0.wireOp",EDGE,"E4469"),sQuery(id+"F0.wireOp",EDGE,"E4470"),sQuery(id+"F0.wireOp",EDGE,"E4471"),sQuery(id+"F0.wireOp",EDGE,"E4472"),sQuery(id+"F0.wireOp",EDGE,"E4473"),sQuery(id+"F0.wireOp",EDGE,"E4474"),sQuery(id+"F0.wireOp",EDGE,"E4475"),sQuery(id+"F0.wireOp",EDGE,"E4476"),sQuery(id+"F0.wireOp",EDGE,"E4477"),sQuery(id+"F0.wireOp",EDGE,"E4478"),sQuery(id+"F0.wireOp",EDGE,"E4479"),sQuery(id+"F0.wireOp",EDGE,"E4480"),sQuery(id+"F0.wireOp",EDGE,"E4481"),sQuery(id+"F0.wireOp",EDGE,"E4482"),sQuery(id+"F0.wireOp",EDGE,"E4483"),sQuery(id+"F0.wireOp",EDGE,"E4484"),sQuery(id+"F0.wireOp",EDGE,"E4485"),sQuery(id+"F0.wireOp",EDGE,"E4486"),sQuery(id+"F0.wireOp",EDGE,"E4487"),sQuery(id+"F0.wireOp",EDGE,"E4488"),sQuery(id+"F0.wireOp",EDGE,"E4489"),sQuery(id+"F0.wireOp",EDGE,"E4490"),sQuery(id+"F0.wireOp",EDGE,"E4491"),sQuery(id+"F0.wireOp",EDGE,"E4492"),sQuery(id+"F0.wireOp",EDGE,"E4493"),sQuery(id+"F0.wireOp",EDGE,"E4494"),sQuery(id+"F0.wireOp",EDGE,"E4495"),sQuery(id+"F0.wireOp",EDGE,"E4496"),sQuery(id+"F0.wireOp",EDGE,"E4497"),sQuery(id+"F0.wireOp",EDGE,"E4498"),sQuery(id+"F0.wireOp",EDGE,"E4499"),sQuery(id+"F0.wireOp",EDGE,"E4500"),sQuery(id+"F0.wireOp",EDGE,"E4501"),sQuery(id+"F0.wireOp",EDGE,"E4502"),sQuery(id+"F0.wireOp",EDGE,"E4503"),sQuery(id+"F0.wireOp",EDGE,"E4504"),sQuery(id+"F0.wireOp",EDGE,"E4505"),sQuery(id+"F0.wireOp",EDGE,"E4506"),sQuery(id+"F0.wireOp",EDGE,"E4507"),sQuery(id+"F0.wireOp",EDGE,"E4508"),sQuery(id+"F0.wireOp",EDGE,"E4509"),sQuery(id+"F0.wireOp",EDGE,"E4510"),sQuery(id+"F0.wireOp",EDGE,"E4511"),sQuery(id+"F0.wireOp",EDGE,"E4512"),sQuery(id+"F0.wireOp",EDGE,"E4513"),sQuery(id+"F0.wireOp",EDGE,"E4514"),sQuery(id+"F0.wireOp",EDGE,"E4515"),sQuery(id+"F0.wireOp",EDGE,"E4516"),sQuery(id+"F0.wireOp",EDGE,"E4517"),sQuery(id+"F0.wireOp",EDGE,"E4518"),sQuery(id+"F0.wireOp",EDGE,"E4519"),sQuery(id+"F0.wireOp",EDGE,"E4520"),sQuery(id+"F0.wireOp",EDGE,"E4521"),sQuery(id+"F0.wireOp",EDGE,"E4522"),sQuery(id+"F0.wireOp",EDGE,"E4523"),sQuery(id+"F0.wireOp",EDGE,"E4524"),sQuery(id+"F0.wireOp",EDGE,"E4525"),sQuery(id+"F0.wireOp",EDGE,"E4526"),sQuery(id+"F0.wireOp",EDGE,"E4527"),sQuery(id+"F0.wireOp",EDGE,"E4528"),sQuery(id+"F0.wireOp",EDGE,"E4529"),sQuery(id+"F0.wireOp",EDGE,"E4530"),sQuery(id+"F0.wireOp",EDGE,"E4531"),sQuery(id+"F0.wireOp",EDGE,"E4532"),sQuery(id+"F0.wireOp",EDGE,"E4533"),sQuery(id+"F0.wireOp",EDGE,"E4534"),sQuery(id+"F0.wireOp",EDGE,"E4535"),sQuery(id+"F0.wireOp",EDGE,"E4536"),sQuery(id+"F0.wireOp",EDGE,"E4537"),sQuery(id+"F0.wireOp",EDGE,"E4538"),sQuery(id+"F0.wireOp",EDGE,"E4539"),sQuery(id+"F0.wireOp",EDGE,"E4540"),sQuery(id+"F0.wireOp",EDGE,"E4541"),sQuery(id+"F0.wireOp",EDGE,"E4542"),sQuery(id+"F0.wireOp",EDGE,"E4543"),sQuery(id+"F0.wireOp",EDGE,"E4544"),sQuery(id+"F0.wireOp",EDGE,"E4545"),sQuery(id+"F0.wireOp",EDGE,"E4546"),sQuery(id+"F0.wireOp",EDGE,"E4547"),sQuery(id+"F0.wireOp",EDGE,"E4548"),sQuery(id+"F0.wireOp",EDGE,"E4549"),sQuery(id+"F0.wireOp",EDGE,"E4550"),sQuery(id+"F0.wireOp",EDGE,"E4551"),sQuery(id+"F0.wireOp",EDGE,"E4552"),sQuery(id+"F0.wireOp",EDGE,"E4553"),sQuery(id+"F0.wireOp",EDGE,"E4554"),sQuery(id+"F0.wireOp",EDGE,"E4555"),sQuery(id+"F0.wireOp",EDGE,"E4556"),sQuery(id+"F0.wireOp",EDGE,"E4557"),sQuery(id+"F0.wireOp",EDGE,"E4558"),sQuery(id+"F0.wireOp",EDGE,"E4559"),sQuery(id+"F0.wireOp",EDGE,"E4560"),sQuery(id+"F0.wireOp",EDGE,"E4561"),sQuery(id+"F0.wireOp",EDGE,"E4562"),sQuery(id+"F0.wireOp",EDGE,"E4563"),sQuery(id+"F0.wireOp",EDGE,"E4564"),sQuery(id+"F0.wireOp",EDGE,"E4565"),sQuery(id+"F0.wireOp",EDGE,"E4566"),sQuery(id+"F0.wireOp",EDGE,"E4567"),sQuery(id+"F0.wireOp",EDGE,"E4568"),sQuery(id+"F0.wireOp",EDGE,"E4569"),sQuery(id+"F0.wireOp",EDGE,"E4570"),sQuery(id+"F0.wireOp",EDGE,"E4571"),sQuery(id+"F0.wireOp",EDGE,"E4572"),sQuery(id+"F0.wireOp",EDGE,"E4573"),sQuery(id+"F0.wireOp",EDGE,"E4574"),sQuery(id+"F0.wireOp",EDGE,"E4575"),sQuery(id+"F0.wireOp",EDGE,"E4576"),sQuery(id+"F0.wireOp",EDGE,"E4577"),sQuery(id+"F0.wireOp",EDGE,"E4578"),sQuery(id+"F0.wireOp",EDGE,"E4579"),sQuery(id+"F0.wireOp",EDGE,"E4580"),sQuery(id+"F0.wireOp",EDGE,"E4581"),sQuery(id+"F0.wireOp",EDGE,"E4582"),sQuery(id+"F0.wireOp",EDGE,"E4583"),sQuery(id+"F0.wireOp",EDGE,"E4584"),sQuery(id+"F0.wireOp",EDGE,"E4585"),sQuery(id+"F0.wireOp",EDGE,"E4586"),sQuery(id+"F0.wireOp",EDGE,"E4587"),sQuery(id+"F0.wireOp",EDGE,"E4588"),sQuery(id+"F0.wireOp",EDGE,"E4589"),sQuery(id+"F0.wireOp",EDGE,"E4590"),sQuery(id+"F0.wireOp",EDGE,"E4591"),sQuery(id+"F0.wireOp",EDGE,"E4592"),sQuery(id+"F0.wireOp",EDGE,"E4593"),sQuery(id+"F0.wireOp",EDGE,"E4594"),sQuery(id+"F0.wireOp",EDGE,"E4595"),sQuery(id+"F0.wireOp",EDGE,"E4596"),sQuery(id+"F0.wireOp",EDGE,"E4597"),sQuery(id+"F0.wireOp",EDGE,"E4598"),sQuery(id+"F0.wireOp",EDGE,"E4599"),sQuery(id+"F0.wireOp",EDGE,"E4600"),sQuery(id+"F0.wireOp",EDGE,"E4601"),sQuery(id+"F0.wireOp",EDGE,"E4602"),sQuery(id+"F0.wireOp",EDGE,"E4603"),sQuery(id+"F0.wireOp",EDGE,"E4604"),sQuery(id+"F0.wireOp",EDGE,"E4605"),sQuery(id+"F0.wireOp",EDGE,"E4606"),sQuery(id+"F0.wireOp",EDGE,"E4607"),sQuery(id+"F0.wireOp",EDGE,"E4608"),sQuery(id+"F0.wireOp",EDGE,"E4609"),sQuery(id+"F0.wireOp",EDGE,"E4610"),sQuery(id+"F0.wireOp",EDGE,"E4611"),sQuery(id+"F0.wireOp",EDGE,"E4612"),sQuery(id+"F0.wireOp",EDGE,"E4613"),sQuery(id+"F0.wireOp",EDGE,"E4614"),sQuery(id+"F0.wireOp",EDGE,"E4615"),sQuery(id+"F0.wireOp",EDGE,"E4616"),sQuery(id+"F0.wireOp",EDGE,"E4617"),sQuery(id+"F0.wireOp",EDGE,"E4618"),sQuery(id+"F0.wireOp",EDGE,"E4619"),sQuery(id+"F0.wireOp",EDGE,"E4620"),sQuery(id+"F0.wireOp",EDGE,"E4621"),sQuery(id+"F0.wireOp",EDGE,"E4622"),sQuery(id+"F0.wireOp",EDGE,"E4623"),sQuery(id+"F0.wireOp",EDGE,"E4624"),sQuery(id+"F0.wireOp",EDGE,"E4625"),sQuery(id+"F0.wireOp",EDGE,"E4626"),sQuery(id+"F0.wireOp",EDGE,"E4627"),sQuery(id+"F0.wireOp",EDGE,"E4628"),sQuery(id+"F0.wireOp",EDGE,"E4629"),sQuery(id+"F0.wireOp",EDGE,"E4630"),sQuery(id+"F0.wireOp",EDGE,"E4631"),sQuery(id+"F0.wireOp",EDGE,"E4632"),sQuery(id+"F0.wireOp",EDGE,"E4632"),sQuery(id+"F0.wireOp",EDGE,"E4632"),sQuery(id+"F0.wireOp",EDGE,"E4633"),sQuery(id+"F0.wireOp",EDGE,"E4634"),sQuery(id+"F0.wireOp",EDGE,"E4635"),sQuery(id+"F0.wireOp",EDGE,"E4636"),sQuery(id+"F0.wireOp",EDGE,"E4637"),sQuery(id+"F0.wireOp",EDGE,"E4638"),sQuery(id+"F0.wireOp",EDGE,"E4639"),sQuery(id+"F0.wireOp",EDGE,"E4640"),sQuery(id+"F0.wireOp",EDGE,"E4641"),sQuery(id+"F0.wireOp",EDGE,"E4642"),sQuery(id+"F0.wireOp",EDGE,"E4643"),sQuery(id+"F0.wireOp",EDGE,"E4644"),sQuery(id+"F0.wireOp",EDGE,"E4645"),sQuery(id+"F0.wireOp",EDGE,"E4646"),sQuery(id+"F0.wireOp",EDGE,"E4647"),sQuery(id+"F0.wireOp",EDGE,"E4648"),sQuery(id+"F0.wireOp",EDGE,"E4649"),sQuery(id+"F0.wireOp",EDGE,"E4650"),sQuery(id+"F0.wireOp",EDGE,"E4651"),sQuery(id+"F0.wireOp",EDGE,"E4652"),sQuery(id+"F0.wireOp",EDGE,"E4653"),sQuery(id+"F0.wireOp",EDGE,"E4654"),sQuery(id+"F0.wireOp",EDGE,"E4655"),sQuery(id+"F0.wireOp",EDGE,"E4656"),sQuery(id+"F0.wireOp",EDGE,"E4657"),sQuery(id+"F0.wireOp",EDGE,"E4658"),sQuery(id+"F0.wireOp",EDGE,"E4659"),sQuery(id+"F0.wireOp",EDGE,"E4660"),sQuery(id+"F0.wireOp",EDGE,"E4661"),sQuery(id+"F0.wireOp",EDGE,"E4662"),sQuery(id+"F0.wireOp",EDGE,"E4663"),sQuery(id+"F0.wireOp",EDGE,"E4664"),sQuery(id+"F0.wireOp",EDGE,"E4665"),sQuery(id+"F0.wireOp",EDGE,"E4666"),sQuery(id+"F0.wireOp",EDGE,"E4667"),sQuery(id+"F0.wireOp",EDGE,"E4668"),sQuery(id+"F0.wireOp",EDGE,"E4669"),sQuery(id+"F0.wireOp",EDGE,"E4670"),sQuery(id+"F0.wireOp",EDGE,"E4671"),sQuery(id+"F0.wireOp",EDGE,"E4672"),sQuery(id+"F0.wireOp",EDGE,"E4673"),sQuery(id+"F0.wireOp",EDGE,"E4674"),sQuery(id+"F0.wireOp",EDGE,"E4675"),sQuery(id+"F0.wireOp",EDGE,"E4676"),sQuery(id+"F0.wireOp",EDGE,"E4677"),sQuery(id+"F0.wireOp",EDGE,"E4678"),sQuery(id+"F0.wireOp",EDGE,"E4679"),sQuery(id+"F0.wireOp",EDGE,"E4679"),sQuery(id+"F0.wireOp",EDGE,"E4679"),sQuery(id+"F0.wireOp",EDGE,"E4680"),sQuery(id+"F0.wireOp",EDGE,"E4681"),sQuery(id+"F0.wireOp",EDGE,"E4682"),sQuery(id+"F0.wireOp",EDGE,"E4683"),sQuery(id+"F0.wireOp",EDGE,"E4684"),sQuery(id+"F0.wireOp",EDGE,"E4685"),sQuery(id+"F0.wireOp",EDGE,"E4686"),sQuery(id+"F0.wireOp",EDGE,"E4687"),sQuery(id+"F0.wireOp",EDGE,"E4688"),sQuery(id+"F0.wireOp",EDGE,"E4689"),sQuery(id+"F0.wireOp",EDGE,"E4690"),sQuery(id+"F0.wireOp",EDGE,"E4691"),sQuery(id+"F0.wireOp",EDGE,"E4692"),sQuery(id+"F0.wireOp",EDGE,"E4693"),sQuery(id+"F0.wireOp",EDGE,"E4694"),sQuery(id+"F0.wireOp",EDGE,"E4695"),sQuery(id+"F0.wireOp",EDGE,"E4696"),sQuery(id+"F0.wireOp",EDGE,"E4697"),sQuery(id+"F0.wireOp",EDGE,"E4698"),sQuery(id+"F0.wireOp",EDGE,"E4699"),sQuery(id+"F0.wireOp",EDGE,"E4700"),sQuery(id+"F0.wireOp",EDGE,"E4701"),sQuery(id+"F0.wireOp",EDGE,"E4702"),sQuery(id+"F0.wireOp",EDGE,"E4703"),sQuery(id+"F0.wireOp",EDGE,"E4704"),sQuery(id+"F0.wireOp",EDGE,"E4705"),sQuery(id+"F0.wireOp",EDGE,"E4706"),sQuery(id+"F0.wireOp",EDGE,"E4707"),sQuery(id+"F0.wireOp",EDGE,"E4708"),sQuery(id+"F0.wireOp",EDGE,"E4709"),sQuery(id+"F0.wireOp",EDGE,"E4710"),sQuery(id+"F0.wireOp",EDGE,"E4711"),sQuery(id+"F0.wireOp",EDGE,"E4712"),sQuery(id+"F0.wireOp",EDGE,"E4713"),sQuery(id+"F0.wireOp",EDGE,"E4714"),sQuery(id+"F0.wireOp",EDGE,"E4715"),sQuery(id+"F0.wireOp",EDGE,"E4716"),sQuery(id+"F0.wireOp",EDGE,"E4717"),sQuery(id+"F0.wireOp",EDGE,"E4718"),sQuery(id+"F0.wireOp",EDGE,"E4719"),sQuery(id+"F0.wireOp",EDGE,"E4720"),sQuery(id+"F0.wireOp",EDGE,"E4721"),sQuery(id+"F0.wireOp",EDGE,"E4722"),sQuery(id+"F0.wireOp",EDGE,"E4723"),sQuery(id+"F0.wireOp",EDGE,"E4724"),sQuery(id+"F0.wireOp",EDGE,"E4725"),sQuery(id+"F0.wireOp",EDGE,"E4726"),sQuery(id+"F0.wireOp",EDGE,"E4727"),sQuery(id+"F0.wireOp",EDGE,"E4728"),sQuery(id+"F0.wireOp",EDGE,"E4729"),sQuery(id+"F0.wireOp",EDGE,"E4730"),sQuery(id+"F0.wireOp",EDGE,"E4731"),sQuery(id+"F0.wireOp",EDGE,"E4732"),sQuery(id+"F0.wireOp",EDGE,"E4733"),sQuery(id+"F0.wireOp",EDGE,"E4734"),sQuery(id+"F0.wireOp",EDGE,"E4735"),sQuery(id+"F0.wireOp",EDGE,"E4736"),sQuery(id+"F0.wireOp",EDGE,"E4737"),sQuery(id+"F0.wireOp",EDGE,"E4738"),sQuery(id+"F0.wireOp",EDGE,"E4739"),sQuery(id+"F0.wireOp",EDGE,"E4740"),sQuery(id+"F0.wireOp",EDGE,"E4741"),sQuery(id+"F0.wireOp",EDGE,"E4742"),sQuery(id+"F0.wireOp",EDGE,"E4743"),sQuery(id+"F0.wireOp",EDGE,"E4744"),sQuery(id+"F0.wireOp",EDGE,"E4745"),sQuery(id+"F0.wireOp",EDGE,"E4746"),sQuery(id+"F0.wireOp",EDGE,"E4747"),sQuery(id+"F0.wireOp",EDGE,"E4748"),sQuery(id+"F0.wireOp",EDGE,"E4749"),sQuery(id+"F0.wireOp",EDGE,"E4750"),sQuery(id+"F0.wireOp",EDGE,"E4751"),sQuery(id+"F0.wireOp",EDGE,"E4752"),sQuery(id+"F0.wireOp",EDGE,"E4753"),sQuery(id+"F0.wireOp",EDGE,"E4754"),sQuery(id+"F0.wireOp",EDGE,"E4755"),sQuery(id+"F0.wireOp",EDGE,"E4756"),sQuery(id+"F0.wireOp",EDGE,"E4757"),sQuery(id+"F0.wireOp",EDGE,"E4758"),sQuery(id+"F0.wireOp",EDGE,"E4759"),sQuery(id+"F0.wireOp",EDGE,"E4760"),sQuery(id+"F0.wireOp",EDGE,"E4761"),sQuery(id+"F0.wireOp",EDGE,"E4762"),sQuery(id+"F0.wireOp",EDGE,"E4763"),sQuery(id+"F0.wireOp",EDGE,"E4764"),sQuery(id+"F0.wireOp",EDGE,"E4765"),sQuery(id+"F0.wireOp",EDGE,"E4766"),sQuery(id+"F0.wireOp",EDGE,"E4767"),sQuery(id+"F0.wireOp",EDGE,"E4768"),sQuery(id+"F0.wireOp",EDGE,"E4769"),sQuery(id+"F0.wireOp",EDGE,"E4770"),sQuery(id+"F0.wireOp",EDGE,"E4771"),sQuery(id+"F0.wireOp",EDGE,"E4772"),sQuery(id+"F0.wireOp",EDGE,"E4773"),sQuery(id+"F0.wireOp",EDGE,"E4774"),sQuery(id+"F0.wireOp",EDGE,"E4775"),sQuery(id+"F0.wireOp",EDGE,"E4776"),sQuery(id+"F0.wireOp",EDGE,"E4777"),sQuery(id+"F0.wireOp",EDGE,"E4778"),sQuery(id+"F0.wireOp",EDGE,"E4779"),sQuery(id+"F0.wireOp",EDGE,"E4780"),sQuery(id+"F0.wireOp",EDGE,"E4781"),sQuery(id+"F0.wireOp",EDGE,"E4782"),sQuery(id+"F0.wireOp",EDGE,"E4783"),sQuery(id+"F0.wireOp",EDGE,"E4784"),sQuery(id+"F0.wireOp",EDGE,"E4785"),sQuery(id+"F0.wireOp",EDGE,"E4786"),sQuery(id+"F0.wireOp",EDGE,"E4787"),sQuery(id+"F0.wireOp",EDGE,"E4788"),sQuery(id+"F0.wireOp",EDGE,"E4789"),sQuery(id+"F0.wireOp",EDGE,"E4790"),sQuery(id+"F0.wireOp",EDGE,"E4791"),sQuery(id+"F0.wireOp",EDGE,"E4792"),sQuery(id+"F0.wireOp",EDGE,"E4793"),sQuery(id+"F0.wireOp",EDGE,"E4794"),sQuery(id+"F0.wireOp",EDGE,"E4795"),sQuery(id+"F0.wireOp",EDGE,"E4796"),sQuery(id+"F0.wireOp",EDGE,"E4797"),sQuery(id+"F0.wireOp",EDGE,"E4798"),sQuery(id+"F0.wireOp",EDGE,"E4799"),sQuery(id+"F0.wireOp",EDGE,"E4800"),sQuery(id+"F0.wireOp",EDGE,"E4801"),sQuery(id+"F0.wireOp",EDGE,"E4802"),sQuery(id+"F0.wireOp",EDGE,"E4803"),sQuery(id+"F0.wireOp",EDGE,"E4804"),sQuery(id+"F0.wireOp",EDGE,"E4805"),sQuery(id+"F0.wireOp",EDGE,"E4806"),sQuery(id+"F0.wireOp",EDGE,"E4807"),sQuery(id+"F0.wireOp",EDGE,"E4808"),sQuery(id+"F0.wireOp",EDGE,"E4809"),sQuery(id+"F0.wireOp",EDGE,"E4810"),sQuery(id+"F0.wireOp",EDGE,"E4811"),sQuery(id+"F0.wireOp",EDGE,"E4812"),sQuery(id+"F0.wireOp",EDGE,"E4813"),sQuery(id+"F0.wireOp",EDGE,"E4814"),sQuery(id+"F0.wireOp",EDGE,"E4815"),sQuery(id+"F0.wireOp",EDGE,"E4816"),sQuery(id+"F0.wireOp",EDGE,"E4817"),sQuery(id+"F0.wireOp",EDGE,"E4818"),sQuery(id+"F0.wireOp",EDGE,"E4819"),sQuery(id+"F0.wireOp",EDGE,"E4820"),sQuery(id+"F0.wireOp",EDGE,"E4821"),sQuery(id+"F0.wireOp",EDGE,"E4822"),sQuery(id+"F0.wireOp",EDGE,"E4823"),sQuery(id+"F0.wireOp",EDGE,"E4824"),sQuery(id+"F0.wireOp",EDGE,"E4825"),sQuery(id+"F0.wireOp",EDGE,"E4826"),sQuery(id+"F0.wireOp",EDGE,"E4827"),sQuery(id+"F0.wireOp",EDGE,"E4828"),sQuery(id+"F0.wireOp",EDGE,"E4829"),sQuery(id+"F0.wireOp",EDGE,"E4830"),sQuery(id+"F0.wireOp",EDGE,"E4831"),sQuery(id+"F0.wireOp",EDGE,"E4832"),sQuery(id+"F0.wireOp",EDGE,"E4833"),sQuery(id+"F0.wireOp",EDGE,"E4834"),sQuery(id+"F0.wireOp",EDGE,"E4835"),sQuery(id+"F0.wireOp",EDGE,"E4836"),sQuery(id+"F0.wireOp",EDGE,"E4837"),sQuery(id+"F0.wireOp",EDGE,"E4838"),sQuery(id+"F0.wireOp",EDGE,"E4839"),sQuery(id+"F0.wireOp",EDGE,"E4840"),sQuery(id+"F0.wireOp",EDGE,"E4841"),sQuery(id+"F0.wireOp",EDGE,"E4842"),sQuery(id+"F0.wireOp",EDGE,"E4843"),sQuery(id+"F0.wireOp",EDGE,"E4844"),sQuery(id+"F0.wireOp",EDGE,"E4845"),sQuery(id+"F0.wireOp",EDGE,"E4846"),sQuery(id+"F0.wireOp",EDGE,"E4847"),sQuery(id+"F0.wireOp",EDGE,"E4848"),sQuery(id+"F0.wireOp",EDGE,"E4849"),sQuery(id+"F0.wireOp",EDGE,"E4850"),sQuery(id+"F0.wireOp",EDGE,"E4851"),sQuery(id+"F0.wireOp",EDGE,"E4852"),sQuery(id+"F0.wireOp",EDGE,"E4853"),sQuery(id+"F0.wireOp",EDGE,"E4854"),sQuery(id+"F0.wireOp",EDGE,"E4855"),sQuery(id+"F0.wireOp",EDGE,"E4856"),sQuery(id+"F0.wireOp",EDGE,"E4857"),sQuery(id+"F0.wireOp",EDGE,"E4858"),sQuery(id+"F0.wireOp",EDGE,"E4859"),sQuery(id+"F0.wireOp",EDGE,"E4860"),sQuery(id+"F0.wireOp",EDGE,"E4861"),sQuery(id+"F0.wireOp",EDGE,"E4862"),sQuery(id+"F0.wireOp",EDGE,"E4863"),sQuery(id+"F0.wireOp",EDGE,"E4864"),sQuery(id+"F0.wireOp",EDGE,"E4865"),sQuery(id+"F0.wireOp",EDGE,"E4866"),sQuery(id+"F0.wireOp",EDGE,"E4867"),sQuery(id+"F0.wireOp",EDGE,"E4868"),sQuery(id+"F0.wireOp",EDGE,"E4869"),sQuery(id+"F0.wireOp",EDGE,"E4870"),sQuery(id+"F0.wireOp",EDGE,"E4871"),sQuery(id+"F0.wireOp",EDGE,"E4872"),sQuery(id+"F0.wireOp",EDGE,"E4873"),sQuery(id+"F0.wireOp",EDGE,"E4874"),sQuery(id+"F0.wireOp",EDGE,"E4875"),sQuery(id+"F0.wireOp",EDGE,"E4876"),sQuery(id+"F0.wireOp",EDGE,"E4877"),sQuery(id+"F0.wireOp",EDGE,"E4878"),sQuery(id+"F0.wireOp",EDGE,"E4879"),sQuery(id+"F0.wireOp",EDGE,"E4880"),sQuery(id+"F0.wireOp",EDGE,"E4881"),sQuery(id+"F0.wireOp",EDGE,"E4882"),sQuery(id+"F0.wireOp",EDGE,"E4883"),sQuery(id+"F0.wireOp",EDGE,"E4884"),sQuery(id+"F0.wireOp",EDGE,"E4885"),sQuery(id+"F0.wireOp",EDGE,"E4886"),sQuery(id+"F0.wireOp",EDGE,"E4887"),sQuery(id+"F0.wireOp",EDGE,"E4888"),sQuery(id+"F0.wireOp",EDGE,"E4889"),sQuery(id+"F0.wireOp",EDGE,"E4890"),sQuery(id+"F0.wireOp",EDGE,"E4891"),sQuery(id+"F0.wireOp",EDGE,"E4892"),sQuery(id+"F0.wireOp",EDGE,"E4893"),sQuery(id+"F0.wireOp",EDGE,"E4894"),sQuery(id+"F0.wireOp",EDGE,"E4895"),sQuery(id+"F0.wireOp",EDGE,"E4896"),sQuery(id+"F0.wireOp",EDGE,"E4897"),sQuery(id+"F0.wireOp",EDGE,"E4898"),sQuery(id+"F0.wireOp",EDGE,"E4899"),sQuery(id+"F0.wireOp",EDGE,"E4900"),sQuery(id+"F0.wireOp",EDGE,"E4901"),sQuery(id+"F0.wireOp",EDGE,"E4902"),sQuery(id+"F0.wireOp",EDGE,"E4903"),sQuery(id+"F0.wireOp",EDGE,"E4904"),sQuery(id+"F0.wireOp",EDGE,"E4905"),sQuery(id+"F0.wireOp",EDGE,"E4906"),sQuery(id+"F0.wireOp",EDGE,"E4907"),sQuery(id+"F0.wireOp",EDGE,"E4908"),sQuery(id+"F0.wireOp",EDGE,"E4909"),sQuery(id+"F0.wireOp",EDGE,"E4910"),sQuery(id+"F0.wireOp",EDGE,"E4911"),sQuery(id+"F0.wireOp",EDGE,"E4912"),sQuery(id+"F0.wireOp",EDGE,"E4913"),sQuery(id+"F0.wireOp",EDGE,"E4914"),sQuery(id+"F0.wireOp",EDGE,"E4914"),sQuery(id+"F0.wireOp",EDGE,"E4915"),sQuery(id+"F0.wireOp",EDGE,"E4916"),sQuery(id+"F0.wireOp",EDGE,"E4917"),sQuery(id+"F0.wireOp",EDGE,"E4918"),sQuery(id+"F0.wireOp",EDGE,"E4919"),sQuery(id+"F0.wireOp",EDGE,"E4920"),sQuery(id+"F0.wireOp",EDGE,"E4921"),sQuery(id+"F0.wireOp",EDGE,"E4922"),sQuery(id+"F0.wireOp",EDGE,"E4923"),sQuery(id+"F0.wireOp",EDGE,"E4924"),sQuery(id+"F0.wireOp",EDGE,"E4925"),sQuery(id+"F0.wireOp",EDGE,"E4926"),sQuery(id+"F0.wireOp",EDGE,"E4926"),sQuery(id+"F0.wireOp",EDGE,"E4927"),sQuery(id+"F0.wireOp",EDGE,"E4928"),sQuery(id+"F0.wireOp",EDGE,"E4929"),sQuery(id+"F0.wireOp",EDGE,"E4930"),sQuery(id+"F0.wireOp",EDGE,"E4931"),sQuery(id+"F0.wireOp",EDGE,"E4932"),sQuery(id+"F0.wireOp",EDGE,"E4933"),sQuery(id+"F0.wireOp",EDGE,"E4934"),sQuery(id+"F0.wireOp",EDGE,"E4935"),sQuery(id+"F0.wireOp",EDGE,"E4936"),sQuery(id+"F0.wireOp",EDGE,"E4937"),sQuery(id+"F0.wireOp",EDGE,"E4938"),sQuery(id+"F0.wireOp",EDGE,"E4939"),sQuery(id+"F0.wireOp",EDGE,"E4940"),sQuery(id+"F0.wireOp",EDGE,"E4940"),sQuery(id+"F0.wireOp",EDGE,"E4941"),sQuery(id+"F0.wireOp",EDGE,"E4942"),sQuery(id+"F0.wireOp",EDGE,"E4943"),sQuery(id+"F0.wireOp",EDGE,"E4944"),sQuery(id+"F0.wireOp",EDGE,"E4945"),sQuery(id+"F0.wireOp",EDGE,"E4946"),sQuery(id+"F0.wireOp",EDGE,"E4947"),sQuery(id+"F0.wireOp",EDGE,"E4948"),sQuery(id+"F0.wireOp",EDGE,"E4949"),sQuery(id+"F0.wireOp",EDGE,"E4950"),sQuery(id+"F0.wireOp",EDGE,"E4951"),sQuery(id+"F0.wireOp",EDGE,"E4952"),sQuery(id+"F0.wireOp",EDGE,"E4953"),sQuery(id+"F0.wireOp",EDGE,"E4954"),sQuery(id+"F0.wireOp",EDGE,"E4955"),sQuery(id+"F0.wireOp",EDGE,"E4956"),sQuery(id+"F0.wireOp",EDGE,"E4957"),sQuery(id+"F0.wireOp",EDGE,"E4958"),sQuery(id+"F0.wireOp",EDGE,"E4959"),sQuery(id+"F0.wireOp",EDGE,"E4960"),sQuery(id+"F0.wireOp",EDGE,"E4961"),sQuery(id+"F0.wireOp",EDGE,"E4962"),sQuery(id+"F0.wireOp",EDGE,"E4963"),sQuery(id+"F0.wireOp",EDGE,"E4964"),sQuery(id+"F0.wireOp",EDGE,"E4965"),sQuery(id+"F0.wireOp",EDGE,"E4966"),sQuery(id+"F0.wireOp",EDGE,"E4967"),sQuery(id+"F0.wireOp",EDGE,"E4968"),sQuery(id+"F0.wireOp",EDGE,"E4969"),sQuery(id+"F0.wireOp",EDGE,"E4970"),sQuery(id+"F0.wireOp",EDGE,"E4971"),sQuery(id+"F0.wireOp",EDGE,"E4972"),sQuery(id+"F0.wireOp",EDGE,"E4973"),sQuery(id+"F0.wireOp",EDGE,"E4974"),sQuery(id+"F0.wireOp",EDGE,"E4975"),sQuery(id+"F0.wireOp",EDGE,"E4976"),sQuery(id+"F0.wireOp",EDGE,"E4977"),sQuery(id+"F0.wireOp",EDGE,"E4978"),sQuery(id+"F0.wireOp",EDGE,"E4979"),sQuery(id+"F0.wireOp",EDGE,"E4980"),sQuery(id+"F0.wireOp",EDGE,"E4981"),sQuery(id+"F0.wireOp",EDGE,"E4982"),sQuery(id+"F0.wireOp",EDGE,"E4983"),sQuery(id+"F0.wireOp",EDGE,"E4984"),sQuery(id+"F0.wireOp",EDGE,"E4985"),sQuery(id+"F0.wireOp",EDGE,"E4986"),sQuery(id+"F0.wireOp",EDGE,"E4987"),sQuery(id+"F0.wireOp",EDGE,"E4988"),sQuery(id+"F0.wireOp",EDGE,"E4989"),sQuery(id+"F0.wireOp",EDGE,"E4990"),sQuery(id+"F0.wireOp",EDGE,"E4991"),sQuery(id+"F0.wireOp",EDGE,"E4992"),sQuery(id+"F0.wireOp",EDGE,"E4993"),sQuery(id+"F0.wireOp",EDGE,"E4994"),sQuery(id+"F0.wireOp",EDGE,"E4995"),sQuery(id+"F0.wireOp",EDGE,"E4996"),sQuery(id+"F0.wireOp",EDGE,"E4997"),sQuery(id+"F0.wireOp",EDGE,"E4998"),sQuery(id+"F0.wireOp",EDGE,"E4999"),sQuery(id+"F0.wireOp",EDGE,"E5000"),sQuery(id+"F0.wireOp",EDGE,"E5001"),sQuery(id+"F0.wireOp",EDGE,"E5002"),sQuery(id+"F0.wireOp",EDGE,"E5003"),sQuery(id+"F0.wireOp",EDGE,"E5004"),sQuery(id+"F0.wireOp",EDGE,"E5005"),sQuery(id+"F0.wireOp",EDGE,"E5006"),sQuery(id+"F0.wireOp",EDGE,"E5007"),sQuery(id+"F0.wireOp",EDGE,"E5008"),sQuery(id+"F0.wireOp",EDGE,"E5009"),sQuery(id+"F0.wireOp",EDGE,"E5010"),sQuery(id+"F0.wireOp",EDGE,"E5011"),sQuery(id+"F0.wireOp",EDGE,"E5012"),sQuery(id+"F0.wireOp",EDGE,"E5013"),sQuery(id+"F0.wireOp",EDGE,"E5014"),sQuery(id+"F0.wireOp",EDGE,"E5015"),sQuery(id+"F0.wireOp",EDGE,"E5016"),sQuery(id+"F0.wireOp",EDGE,"E5017"),sQuery(id+"F0.wireOp",EDGE,"E5018"),sQuery(id+"F0.wireOp",EDGE,"E5019"),sQuery(id+"F0.wireOp",EDGE,"E5020"),sQuery(id+"F0.wireOp",EDGE,"E5021"),sQuery(id+"F0.wireOp",EDGE,"E5022"),sQuery(id+"F0.wireOp",EDGE,"E5023"),sQuery(id+"F0.wireOp",EDGE,"E5024"),sQuery(id+"F0.wireOp",EDGE,"E5025"),sQuery(id+"F0.wireOp",EDGE,"E5025"),sQuery(id+"F0.wireOp",EDGE,"E5026"),sQuery(id+"F0.wireOp",EDGE,"E5027"),sQuery(id+"F0.wireOp",EDGE,"E5028"),sQuery(id+"F0.wireOp",EDGE,"E5029"),sQuery(id+"F0.wireOp",EDGE,"E5030"),sQuery(id+"F0.wireOp",EDGE,"E5031"),sQuery(id+"F0.wireOp",EDGE,"E5032"),sQuery(id+"F0.wireOp",EDGE,"E5033"),sQuery(id+"F0.wireOp",EDGE,"E5034"),sQuery(id+"F0.wireOp",EDGE,"E5035"),sQuery(id+"F0.wireOp",EDGE,"E5035"),sQuery(id+"F0.wireOp",EDGE,"E5035"),sQuery(id+"F0.wireOp",EDGE,"E5036"),sQuery(id+"F0.wireOp",EDGE,"E5037"),sQuery(id+"F0.wireOp",EDGE,"E5038"),sQuery(id+"F0.wireOp",EDGE,"E5039"),sQuery(id+"F0.wireOp",EDGE,"E5040"),sQuery(id+"F0.wireOp",EDGE,"E5041"),sQuery(id+"F0.wireOp",EDGE,"E5042"),sQuery(id+"F0.wireOp",EDGE,"E5043"),sQuery(id+"F0.wireOp",EDGE,"E5044"),sQuery(id+"F0.wireOp",EDGE,"E5045"),sQuery(id+"F0.wireOp",EDGE,"E5045"),sQuery(id+"F0.wireOp",EDGE,"E5046"),sQuery(id+"F0.wireOp",EDGE,"E5047"),sQuery(id+"F0.wireOp",EDGE,"E5047"),sQuery(id+"F0.wireOp",EDGE,"E5048"),sQuery(id+"F0.wireOp",EDGE,"E5049"),sQuery(id+"F0.wireOp",EDGE,"E5049"),sQuery(id+"F0.wireOp",EDGE,"E5050"),sQuery(id+"F0.wireOp",EDGE,"E5051"),sQuery(id+"F0.wireOp",EDGE,"E5052"),sQuery(id+"F0.wireOp",EDGE,"E5053"),sQuery(id+"F0.wireOp",EDGE,"E5054"),sQuery(id+"F0.wireOp",EDGE,"E5055"),sQuery(id+"F0.wireOp",EDGE,"E5056"),sQuery(id+"F0.wireOp",EDGE,"E5057"),sQuery(id+"F0.wireOp",EDGE,"E5058"),sQuery(id+"F0.wireOp",EDGE,"E5059"),sQuery(id+"F0.wireOp",EDGE,"E5060"),sQuery(id+"F0.wireOp",EDGE,"E5061"),sQuery(id+"F0.wireOp",EDGE,"E5061"),sQuery(id+"F0.wireOp",EDGE,"E5062"),sQuery(id+"F0.wireOp",EDGE,"E5063"),sQuery(id+"F0.wireOp",EDGE,"E5064"),sQuery(id+"F0.wireOp",EDGE,"E5065"),sQuery(id+"F0.wireOp",EDGE,"E5065"),sQuery(id+"F0.wireOp",EDGE,"E5066"),sQuery(id+"F0.wireOp",EDGE,"E5067"),sQuery(id+"F0.wireOp",EDGE,"E5068"),sQuery(id+"F0.wireOp",EDGE,"E5069"),sQuery(id+"F0.wireOp",EDGE,"E5070"),sQuery(id+"F0.wireOp",EDGE,"E5071"),sQuery(id+"F0.wireOp",EDGE,"E5071"),sQuery(id+"F0.wireOp",EDGE,"E5072"),sQuery(id+"F0.wireOp",EDGE,"E5073"),sQuery(id+"F0.wireOp",EDGE,"E5074"),sQuery(id+"F0.wireOp",EDGE,"E5074"),sQuery(id+"F0.wireOp",EDGE,"E5074"),sQuery(id+"F0.wireOp",EDGE,"E5075"),sQuery(id+"F0.wireOp",EDGE,"E5076"),sQuery(id+"F0.wireOp",EDGE,"E5077"),sQuery(id+"F0.wireOp",EDGE,"E5078"),sQuery(id+"F0.wireOp",EDGE,"E5079"),sQuery(id+"F0.wireOp",EDGE,"E5080"),sQuery(id+"F0.wireOp",EDGE,"E5081"),sQuery(id+"F0.wireOp",EDGE,"E5082"),sQuery(id+"F0.wireOp",EDGE,"E5083"),sQuery(id+"F0.wireOp",EDGE,"E5084"),sQuery(id+"F0.wireOp",EDGE,"E5085"),sQuery(id+"F0.wireOp",EDGE,"E5086"),sQuery(id+"F0.wireOp",EDGE,"E5087"),sQuery(id+"F0.wireOp",EDGE,"E5088"),sQuery(id+"F0.wireOp",EDGE,"E5089"),sQuery(id+"F0.wireOp",EDGE,"E5090"),sQuery(id+"F0.wireOp",EDGE,"E5091"),sQuery(id+"F0.wireOp",EDGE,"E5092"),sQuery(id+"F0.wireOp",EDGE,"E5093"),sQuery(id+"F0.wireOp",EDGE,"E5094"),sQuery(id+"F0.wireOp",EDGE,"E5095"),sQuery(id+"F0.wireOp",EDGE,"E5096"),sQuery(id+"F0.wireOp",EDGE,"E5097"),sQuery(id+"F0.wireOp",EDGE,"E5098"),sQuery(id+"F0.wireOp",EDGE,"E5099"),sQuery(id+"F0.wireOp",EDGE,"E5099"),sQuery(id+"F0.wireOp",EDGE,"E5100"),sQuery(id+"F0.wireOp",EDGE,"E5101"),sQuery(id+"F0.wireOp",EDGE,"E5102"),sQuery(id+"F0.wireOp",EDGE,"E5103"),sQuery(id+"F0.wireOp",EDGE,"E5104"),sQuery(id+"F0.wireOp",EDGE,"E5105"),sQuery(id+"F0.wireOp",EDGE,"E5106"),sQuery(id+"F0.wireOp",EDGE,"E5107"),sQuery(id+"F0.wireOp",EDGE,"E5108"),sQuery(id+"F0.wireOp",EDGE,"E5109"),sQuery(id+"F0.wireOp",EDGE,"E5110"),sQuery(id+"F0.wireOp",EDGE,"E5111"),sQuery(id+"F0.wireOp",EDGE,"E5112"),sQuery(id+"F0.wireOp",EDGE,"E5112"),sQuery(id+"F0.wireOp",EDGE,"E5113"),sQuery(id+"F0.wireOp",EDGE,"E5114"),sQuery(id+"F0.wireOp",EDGE,"E5115"),sQuery(id+"F0.wireOp",EDGE,"E5116"),sQuery(id+"F0.wireOp",EDGE,"E5117"),sQuery(id+"F0.wireOp",EDGE,"E5118"),sQuery(id+"F0.wireOp",EDGE,"E5119"),sQuery(id+"F0.wireOp",EDGE,"E5120"),sQuery(id+"F0.wireOp",EDGE,"E5121"),sQuery(id+"F0.wireOp",EDGE,"E5122"),sQuery(id+"F0.wireOp",EDGE,"E5123"),sQuery(id+"F0.wireOp",EDGE,"E5124"),sQuery(id+"F0.wireOp",EDGE,"E5125"),sQuery(id+"F0.wireOp",EDGE,"E5126"),sQuery(id+"F0.wireOp",EDGE,"E5127"),sQuery(id+"F0.wireOp",EDGE,"E5128"),sQuery(id+"F0.wireOp",EDGE,"E5129"),sQuery(id+"F0.wireOp",EDGE,"E5130"),sQuery(id+"F0.wireOp",EDGE,"E5131"),sQuery(id+"F0.wireOp",EDGE,"E5132"),sQuery(id+"F0.wireOp",EDGE,"E5133"),sQuery(id+"F0.wireOp",EDGE,"E5134"),sQuery(id+"F0.wireOp",EDGE,"E5135"),sQuery(id+"F0.wireOp",EDGE,"E5136"),sQuery(id+"F0.wireOp",EDGE,"E5137"),sQuery(id+"F0.wireOp",EDGE,"E5138"),sQuery(id+"F0.wireOp",EDGE,"E5139"),sQuery(id+"F0.wireOp",EDGE,"E5140"),sQuery(id+"F0.wireOp",EDGE,"E5141"),sQuery(id+"F0.wireOp",EDGE,"E5142"),sQuery(id+"F0.wireOp",EDGE,"E5143"),sQuery(id+"F0.wireOp",EDGE,"E5144"),sQuery(id+"F0.wireOp",EDGE,"E5145"),sQuery(id+"F0.wireOp",EDGE,"E5146"),sQuery(id+"F0.wireOp",EDGE,"E5147"),sQuery(id+"F0.wireOp",EDGE,"E5148"),sQuery(id+"F0.wireOp",EDGE,"E5149"),sQuery(id+"F0.wireOp",EDGE,"E5150"),sQuery(id+"F0.wireOp",EDGE,"E5151"),sQuery(id+"F0.wireOp",EDGE,"E5152"),sQuery(id+"F0.wireOp",EDGE,"E5153"),sQuery(id+"F0.wireOp",EDGE,"E5154"),sQuery(id+"F0.wireOp",EDGE,"E5155"),sQuery(id+"F0.wireOp",EDGE,"E5156"),sQuery(id+"F0.wireOp",EDGE,"E5157"),sQuery(id+"F0.wireOp",EDGE,"E5158"),sQuery(id+"F0.wireOp",EDGE,"E5159"),sQuery(id+"F0.wireOp",EDGE,"E5160"),sQuery(id+"F0.wireOp",EDGE,"E5161"),sQuery(id+"F0.wireOp",EDGE,"E5162"),sQuery(id+"F0.wireOp",EDGE,"E5163"),sQuery(id+"F0.wireOp",EDGE,"E5164"),sQuery(id+"F0.wireOp",EDGE,"E5165"),sQuery(id+"F0.wireOp",EDGE,"E5166"),sQuery(id+"F0.wireOp",EDGE,"E5167"),sQuery(id+"F0.wireOp",EDGE,"E5168"),sQuery(id+"F0.wireOp",EDGE,"E5169"),sQuery(id+"F0.wireOp",EDGE,"E5170"),sQuery(id+"F0.wireOp",EDGE,"E5171"),sQuery(id+"F0.wireOp",EDGE,"E5172"),sQuery(id+"F0.wireOp",EDGE,"E5173"),sQuery(id+"F0.wireOp",EDGE,"E5174"),sQuery(id+"F0.wireOp",EDGE,"E5175"),sQuery(id+"F0.wireOp",EDGE,"E5176"),sQuery(id+"F0.wireOp",EDGE,"E5177"),sQuery(id+"F0.wireOp",EDGE,"E5178"),sQuery(id+"F0.wireOp",EDGE,"E5179"),sQuery(id+"F0.wireOp",EDGE,"E5180"),sQuery(id+"F0.wireOp",EDGE,"E5181"),sQuery(id+"F0.wireOp",EDGE,"E5182"),sQuery(id+"F0.wireOp",EDGE,"E5183"),sQuery(id+"F0.wireOp",EDGE,"E5184"),sQuery(id+"F0.wireOp",EDGE,"E5185"),sQuery(id+"F0.wireOp",EDGE,"E5186"),sQuery(id+"F0.wireOp",EDGE,"E5187"),sQuery(id+"F0.wireOp",EDGE,"E5188"),sQuery(id+"F0.wireOp",EDGE,"E5189"),sQuery(id+"F0.wireOp",EDGE,"E5190"),sQuery(id+"F0.wireOp",EDGE,"E5191"),sQuery(id+"F0.wireOp",EDGE,"E5192"),sQuery(id+"F0.wireOp",EDGE,"E5193"),sQuery(id+"F0.wireOp",EDGE,"E5194"),sQuery(id+"F0.wireOp",EDGE,"E5195"),sQuery(id+"F0.wireOp",EDGE,"E5196"),sQuery(id+"F0.wireOp",EDGE,"E5197"),sQuery(id+"F0.wireOp",EDGE,"E5198"),sQuery(id+"F0.wireOp",EDGE,"E5199"),sQuery(id+"F0.wireOp",EDGE,"E5200"),sQuery(id+"F0.wireOp",EDGE,"E5201"),sQuery(id+"F0.wireOp",EDGE,"E5202"),sQuery(id+"F0.wireOp",EDGE,"E5203"),sQuery(id+"F0.wireOp",EDGE,"E5204"),sQuery(id+"F0.wireOp",EDGE,"E5205"),sQuery(id+"F0.wireOp",EDGE,"E5206"),sQuery(id+"F0.wireOp",EDGE,"E5207"),sQuery(id+"F0.wireOp",EDGE,"E5208"),sQuery(id+"F0.wireOp",EDGE,"E5209"),sQuery(id+"F0.wireOp",EDGE,"E5210"),sQuery(id+"F0.wireOp",EDGE,"E5211"),sQuery(id+"F0.wireOp",EDGE,"E5212"),sQuery(id+"F0.wireOp",EDGE,"E5213"),sQuery(id+"F0.wireOp",EDGE,"E5214"),sQuery(id+"F0.wireOp",EDGE,"E5215"),sQuery(id+"F0.wireOp",EDGE,"E5216"),sQuery(id+"F0.wireOp",EDGE,"E5217"),sQuery(id+"F0.wireOp",EDGE,"E5218"),sQuery(id+"F0.wireOp",EDGE,"E5219"),sQuery(id+"F0.wireOp",EDGE,"E5220"),sQuery(id+"F0.wireOp",EDGE,"E5221"),sQuery(id+"F0.wireOp",EDGE,"E5222"),sQuery(id+"F0.wireOp",EDGE,"E5223"),sQuery(id+"F0.wireOp",EDGE,"E5224"),sQuery(id+"F0.wireOp",EDGE,"E5225"),sQuery(id+"F0.wireOp",EDGE,"E5226"),sQuery(id+"F0.wireOp",EDGE,"E5227"),sQuery(id+"F0.wireOp",EDGE,"E5228"),sQuery(id+"F0.wireOp",EDGE,"E5229"),sQuery(id+"F0.wireOp",EDGE,"E5230"),sQuery(id+"F0.wireOp",EDGE,"E5231"),sQuery(id+"F0.wireOp",EDGE,"E5232"),sQuery(id+"F0.wireOp",EDGE,"E5233"),sQuery(id+"F0.wireOp",EDGE,"E5234"),sQuery(id+"F0.wireOp",EDGE,"E5235"),sQuery(id+"F0.wireOp",EDGE,"E5236"),sQuery(id+"F0.wireOp",EDGE,"E5237"),sQuery(id+"F0.wireOp",EDGE,"E5238"),sQuery(id+"F0.wireOp",EDGE,"E5239"),sQuery(id+"F0.wireOp",EDGE,"E5240"),sQuery(id+"F0.wireOp",EDGE,"E5241"),sQuery(id+"F0.wireOp",EDGE,"E5242"),sQuery(id+"F0.wireOp",EDGE,"E5243"),sQuery(id+"F0.wireOp",EDGE,"E5244"),sQuery(id+"F0.wireOp",EDGE,"E5245"),sQuery(id+"F0.wireOp",EDGE,"E5246"),sQuery(id+"F0.wireOp",EDGE,"E5247"),sQuery(id+"F0.wireOp",EDGE,"E5248"),sQuery(id+"F0.wireOp",EDGE,"E5249"),sQuery(id+"F0.wireOp",EDGE,"E5250"),sQuery(id+"F0.wireOp",EDGE,"E5251"),sQuery(id+"F0.wireOp",EDGE,"E5252"),sQuery(id+"F0.wireOp",EDGE,"E5253"),sQuery(id+"F0.wireOp",EDGE,"E5254"),sQuery(id+"F0.wireOp",EDGE,"E5255"),sQuery(id+"F0.wireOp",EDGE,"E5256"),sQuery(id+"F0.wireOp",EDGE,"E5257"),sQuery(id+"F0.wireOp",EDGE,"E5258"),sQuery(id+"F0.wireOp",EDGE,"E5259"),sQuery(id+"F0.wireOp",EDGE,"E5260"),sQuery(id+"F0.wireOp",EDGE,"E5261"),sQuery(id+"F0.wireOp",EDGE,"E5262"),sQuery(id+"F0.wireOp",EDGE,"E5263"),sQuery(id+"F0.wireOp",EDGE,"E5264"),sQuery(id+"F0.wireOp",EDGE,"E5265"),sQuery(id+"F0.wireOp",EDGE,"E5266"),sQuery(id+"F0.wireOp",EDGE,"E5267"),sQuery(id+"F0.wireOp",EDGE,"E5268"),sQuery(id+"F0.wireOp",EDGE,"E5269"),sQuery(id+"F0.wireOp",EDGE,"E5270"),sQuery(id+"F0.wireOp",EDGE,"E5271"),sQuery(id+"F0.wireOp",EDGE,"E5272"),sQuery(id+"F0.wireOp",EDGE,"E5273"),sQuery(id+"F0.wireOp",EDGE,"E5274"),sQuery(id+"F0.wireOp",EDGE,"E5275"),sQuery(id+"F0.wireOp",EDGE,"E5276"),sQuery(id+"F0.wireOp",EDGE,"E5277"),sQuery(id+"F0.wireOp",EDGE,"E5278"),sQuery(id+"F0.wireOp",EDGE,"E5279"),sQuery(id+"F0.wireOp",EDGE,"E5280"),sQuery(id+"F0.wireOp",EDGE,"E5281"),sQuery(id+"F0.wireOp",EDGE,"E5282"),sQuery(id+"F0.wireOp",EDGE,"E5283"),sQuery(id+"F0.wireOp",EDGE,"E5284"),sQuery(id+"F0.wireOp",EDGE,"E5285"),sQuery(id+"F0.wireOp",EDGE,"E5286"),sQuery(id+"F0.wireOp",EDGE,"E5287"),sQuery(id+"F0.wireOp",EDGE,"E5288"),sQuery(id+"F0.wireOp",EDGE,"E5289"),sQuery(id+"F0.wireOp",EDGE,"E5290"),sQuery(id+"F0.wireOp",EDGE,"E5291"),sQuery(id+"F0.wireOp",EDGE,"E5292"),sQuery(id+"F0.wireOp",EDGE,"E5293"),sQuery(id+"F0.wireOp",EDGE,"E5294"),sQuery(id+"F0.wireOp",EDGE,"E5295"),sQuery(id+"F0.wireOp",EDGE,"E5296"),sQuery(id+"F0.wireOp",EDGE,"E5297"),sQuery(id+"F0.wireOp",EDGE,"E5298"),sQuery(id+"F0.wireOp",EDGE,"E5299"),sQuery(id+"F0.wireOp",EDGE,"E5300"),sQuery(id+"F0.wireOp",EDGE,"E5301"),sQuery(id+"F0.wireOp",EDGE,"E5302"),sQuery(id+"F0.wireOp",EDGE,"E5303"),sQuery(id+"F0.wireOp",EDGE,"E5304"),sQuery(id+"F0.wireOp",EDGE,"E5305"),sQuery(id+"F0.wireOp",EDGE,"E5306"),sQuery(id+"F0.wireOp",EDGE,"E5307"),sQuery(id+"F0.wireOp",EDGE,"E5308"),sQuery(id+"F0.wireOp",EDGE,"E5309"),sQuery(id+"F0.wireOp",EDGE,"E5310"),sQuery(id+"F0.wireOp",EDGE,"E5311"),sQuery(id+"F0.wireOp",EDGE,"E5312"),sQuery(id+"F0.wireOp",EDGE,"E5313"),sQuery(id+"F0.wireOp",EDGE,"E5314"),sQuery(id+"F0.wireOp",EDGE,"E5315"),sQuery(id+"F0.wireOp",EDGE,"E5316"),sQuery(id+"F0.wireOp",EDGE,"E5317"),sQuery(id+"F0.wireOp",EDGE,"E5318"),sQuery(id+"F0.wireOp",EDGE,"E5319"),sQuery(id+"F0.wireOp",EDGE,"E5320"),sQuery(id+"F0.wireOp",EDGE,"E5321"),sQuery(id+"F0.wireOp",EDGE,"E5322"),sQuery(id+"F0.wireOp",EDGE,"E5323"),sQuery(id+"F0.wireOp",EDGE,"E5324"),sQuery(id+"F0.wireOp",EDGE,"E5325"),sQuery(id+"F0.wireOp",EDGE,"E5326"),sQuery(id+"F0.wireOp",EDGE,"E5327"),sQuery(id+"F0.wireOp",EDGE,"E5328"),sQuery(id+"F0.wireOp",EDGE,"E5329"),sQuery(id+"F0.wireOp",EDGE,"E5330"),sQuery(id+"F0.wireOp",EDGE,"E5331"),sQuery(id+"F0.wireOp",EDGE,"E5332"),sQuery(id+"F0.wireOp",EDGE,"E5333"),sQuery(id+"F0.wireOp",EDGE,"E5334"),sQuery(id+"F0.wireOp",EDGE,"E5335"),sQuery(id+"F0.wireOp",EDGE,"E5336"),sQuery(id+"F0.wireOp",EDGE,"E5337"),sQuery(id+"F0.wireOp",EDGE,"E5338"),sQuery(id+"F0.wireOp",EDGE,"E5339"),sQuery(id+"F0.wireOp",EDGE,"E5340"),sQuery(id+"F0.wireOp",EDGE,"E5341"),sQuery(id+"F0.wireOp",EDGE,"E5342"),sQuery(id+"F0.wireOp",EDGE,"E5343"),sQuery(id+"F0.wireOp",EDGE,"E5344"),sQuery(id+"F0.wireOp",EDGE,"E5345"),sQuery(id+"F0.wireOp",EDGE,"E5346"),sQuery(id+"F0.wireOp",EDGE,"E5347"),sQuery(id+"F0.wireOp",EDGE,"E5348"),sQuery(id+"F0.wireOp",EDGE,"E5349"),sQuery(id+"F0.wireOp",EDGE,"E5350"),sQuery(id+"F0.wireOp",EDGE,"E5351"),sQuery(id+"F0.wireOp",EDGE,"E5352"),sQuery(id+"F0.wireOp",EDGE,"E5353"),sQuery(id+"F0.wireOp",EDGE,"E5354"),sQuery(id+"F0.wireOp",EDGE,"E5355"),sQuery(id+"F0.wireOp",EDGE,"E5356"),sQuery(id+"F0.wireOp",EDGE,"E5357"),sQuery(id+"F0.wireOp",EDGE,"E5358"),sQuery(id+"F0.wireOp",EDGE,"E5359"),sQuery(id+"F0.wireOp",EDGE,"E5360"),sQuery(id+"F0.wireOp",EDGE,"E5361"),sQuery(id+"F0.wireOp",EDGE,"E5362"),sQuery(id+"F0.wireOp",EDGE,"E5363"),sQuery(id+"F0.wireOp",EDGE,"E5364"),sQuery(id+"F0.wireOp",EDGE,"E5365"),sQuery(id+"F0.wireOp",EDGE,"E5366"),sQuery(id+"F0.wireOp",EDGE,"E5367"),sQuery(id+"F0.wireOp",EDGE,"E5368"),sQuery(id+"F0.wireOp",EDGE,"E5369"),sQuery(id+"F0.wireOp",EDGE,"E5370"),sQuery(id+"F0.wireOp",EDGE,"E5371"),sQuery(id+"F0.wireOp",EDGE,"E5372"),sQuery(id+"F0.wireOp",EDGE,"E5373"),sQuery(id+"F0.wireOp",EDGE,"E5374"),sQuery(id+"F0.wireOp",EDGE,"E5375"),sQuery(id+"F0.wireOp",EDGE,"E5376"),sQuery(id+"F0.wireOp",EDGE,"E5376"),sQuery(id+"F0.wireOp",EDGE,"E5377"),sQuery(id+"F0.wireOp",EDGE,"E5378"),sQuery(id+"F0.wireOp",EDGE,"E5379"),sQuery(id+"F0.wireOp",EDGE,"E5380"),sQuery(id+"F0.wireOp",EDGE,"E5381"),sQuery(id+"F0.wireOp",EDGE,"E5382"),sQuery(id+"F0.wireOp",EDGE,"E5382"),sQuery(id+"F0.wireOp",EDGE,"E5383"),sQuery(id+"F0.wireOp",EDGE,"E5384"),sQuery(id+"F0.wireOp",EDGE,"E5385"),sQuery(id+"F0.wireOp",EDGE,"E5386"),sQuery(id+"F0.wireOp",EDGE,"E5387"),sQuery(id+"F0.wireOp",EDGE,"E5388"),sQuery(id+"F0.wireOp",EDGE,"E5388"),sQuery(id+"F0.wireOp",EDGE,"E5389"),sQuery(id+"F0.wireOp",EDGE,"E5390"),sQuery(id+"F0.wireOp",EDGE,"E5391"),sQuery(id+"F0.wireOp",EDGE,"E5392"),sQuery(id+"F0.wireOp",EDGE,"E5393"),sQuery(id+"F0.wireOp",EDGE,"E5394"),sQuery(id+"F0.wireOp",EDGE,"E5395"),sQuery(id+"F0.wireOp",EDGE,"E5396"),sQuery(id+"F0.wireOp",EDGE,"E5397"),sQuery(id+"F0.wireOp",EDGE,"E5398"),sQuery(id+"F0.wireOp",EDGE,"E5399"),sQuery(id+"F0.wireOp",EDGE,"E5400"),sQuery(id+"F0.wireOp",EDGE,"E5401"),sQuery(id+"F0.wireOp",EDGE,"E5402"),sQuery(id+"F0.wireOp",EDGE,"E5403"),sQuery(id+"F0.wireOp",EDGE,"E5403"),sQuery(id+"F0.wireOp",EDGE,"E5404"),sQuery(id+"F0.wireOp",EDGE,"E5405"),sQuery(id+"F0.wireOp",EDGE,"E5406"),sQuery(id+"F0.wireOp",EDGE,"E5407"),sQuery(id+"F0.wireOp",EDGE,"E5408"),sQuery(id+"F0.wireOp",EDGE,"E5409"),sQuery(id+"F0.wireOp",EDGE,"E5410"),sQuery(id+"F0.wireOp",EDGE,"E5411"),sQuery(id+"F0.wireOp",EDGE,"E5411"),sQuery(id+"F0.wireOp",EDGE,"E5412"),sQuery(id+"F0.wireOp",EDGE,"E5413"),sQuery(id+"F0.wireOp",EDGE,"E5414"),sQuery(id+"F0.wireOp",EDGE,"E5415"),sQuery(id+"F0.wireOp",EDGE,"E5415"),sQuery(id+"F0.wireOp",EDGE,"E5416"),sQuery(id+"F0.wireOp",EDGE,"E5417"),sQuery(id+"F0.wireOp",EDGE,"E5418"),sQuery(id+"F0.wireOp",EDGE,"E5419"),sQuery(id+"F0.wireOp",EDGE,"E5420"),sQuery(id+"F0.wireOp",EDGE,"E5420"),sQuery(id+"F0.wireOp",EDGE,"E5420"),sQuery(id+"F0.wireOp",EDGE,"E5421"),sQuery(id+"F0.wireOp",EDGE,"E5422"),sQuery(id+"F0.wireOp",EDGE,"E5423"),sQuery(id+"F0.wireOp",EDGE,"E5424"),sQuery(id+"F0.wireOp",EDGE,"E5425"),sQuery(id+"F0.wireOp",EDGE,"E5425"),sQuery(id+"F0.wireOp",EDGE,"E5426"),sQuery(id+"F0.wireOp",EDGE,"E5427"),sQuery(id+"F0.wireOp",EDGE,"E5427"),sQuery(id+"F0.wireOp",EDGE,"E5428"),sQuery(id+"F0.wireOp",EDGE,"E5429"),sQuery(id+"F0.wireOp",EDGE,"E5430"),sQuery(id+"F0.wireOp",EDGE,"E5431"),sQuery(id+"F0.wireOp",EDGE,"E5432"),sQuery(id+"F0.wireOp",EDGE,"E5433"),sQuery(id+"F0.wireOp",EDGE,"E5434"),sQuery(id+"F0.wireOp",EDGE,"E5435"),sQuery(id+"F0.wireOp",EDGE,"E5436"),sQuery(id+"F0.wireOp",EDGE,"E5437"),sQuery(id+"F0.wireOp",EDGE,"E5438"),sQuery(id+"F0.wireOp",EDGE,"E5439"),sQuery(id+"F0.wireOp",EDGE,"E5440"),sQuery(id+"F0.wireOp",EDGE,"E5441"),sQuery(id+"F0.wireOp",EDGE,"E5442"),sQuery(id+"F0.wireOp",EDGE,"E5443"),sQuery(id+"F0.wireOp",EDGE,"E5444"),sQuery(id+"F0.wireOp",EDGE,"E5445"),sQuery(id+"F0.wireOp",EDGE,"E5446"),sQuery(id+"F0.wireOp",EDGE,"E5447"),sQuery(id+"F0.wireOp",EDGE,"E5448"),sQuery(id+"F0.wireOp",EDGE,"E5449"),sQuery(id+"F0.wireOp",EDGE,"E5450"),sQuery(id+"F0.wireOp",EDGE,"E5451"),sQuery(id+"F0.wireOp",EDGE,"E5452"),sQuery(id+"F0.wireOp",EDGE,"E5453"),sQuery(id+"F0.wireOp",EDGE,"E5454"),sQuery(id+"F0.wireOp",EDGE,"E5455"),sQuery(id+"F0.wireOp",EDGE,"E5456"),sQuery(id+"F0.wireOp",EDGE,"E5457"),sQuery(id+"F0.wireOp",EDGE,"E5458"),sQuery(id+"F0.wireOp",EDGE,"E5459"),sQuery(id+"F0.wireOp",EDGE,"E5460"),sQuery(id+"F0.wireOp",EDGE,"E5461"),sQuery(id+"F0.wireOp",EDGE,"E5462"),sQuery(id+"F0.wireOp",EDGE,"E5463"),sQuery(id+"F0.wireOp",EDGE,"E5464"),sQuery(id+"F0.wireOp",EDGE,"E5465"),sQuery(id+"F0.wireOp",EDGE,"E5466"),sQuery(id+"F0.wireOp",EDGE,"E5467"),sQuery(id+"F0.wireOp",EDGE,"E5468"),sQuery(id+"F0.wireOp",EDGE,"E5469"),sQuery(id+"F0.wireOp",EDGE,"E5470"),sQuery(id+"F0.wireOp",EDGE,"E5471"),sQuery(id+"F0.wireOp",EDGE,"E5472"),sQuery(id+"F0.wireOp",EDGE,"E5473"),sQuery(id+"F0.wireOp",EDGE,"E5474"),sQuery(id+"F0.wireOp",EDGE,"E5475"),sQuery(id+"F0.wireOp",EDGE,"E5476"),sQuery(id+"F0.wireOp",EDGE,"E5477"),sQuery(id+"F0.wireOp",EDGE,"E5478"),sQuery(id+"F0.wireOp",EDGE,"E5479"),sQuery(id+"F0.wireOp",EDGE,"E5480"),sQuery(id+"F0.wireOp",EDGE,"E5481"),sQuery(id+"F0.wireOp",EDGE,"E5482"),sQuery(id+"F0.wireOp",EDGE,"E5483"),sQuery(id+"F0.wireOp",EDGE,"E5484"),sQuery(id+"F0.wireOp",EDGE,"E5485"),sQuery(id+"F0.wireOp",EDGE,"E5486"),sQuery(id+"F0.wireOp",EDGE,"E5487"),sQuery(id+"F0.wireOp",EDGE,"E5488"),sQuery(id+"F0.wireOp",EDGE,"E5489"),sQuery(id+"F0.wireOp",EDGE,"E5490"),sQuery(id+"F0.wireOp",EDGE,"E5491"),sQuery(id+"F0.wireOp",EDGE,"E5492"),sQuery(id+"F0.wireOp",EDGE,"E5493"),sQuery(id+"F0.wireOp",EDGE,"E5494"),sQuery(id+"F0.wireOp",EDGE,"E5495"),sQuery(id+"F0.wireOp",EDGE,"E5496"),sQuery(id+"F0.wireOp",EDGE,"E5497"),sQuery(id+"F0.wireOp",EDGE,"E5498"),sQuery(id+"F0.wireOp",EDGE,"E5499"),sQuery(id+"F0.wireOp",EDGE,"E5500"),sQuery(id+"F0.wireOp",EDGE,"E5501"),sQuery(id+"F0.wireOp",EDGE,"E5502"),sQuery(id+"F0.wireOp",EDGE,"E5503"),sQuery(id+"F0.wireOp",EDGE,"E5504"),sQuery(id+"F0.wireOp",EDGE,"E5505"),sQuery(id+"F0.wireOp",EDGE,"E5506"),sQuery(id+"F0.wireOp",EDGE,"E5507"),sQuery(id+"F0.wireOp",EDGE,"E5508"),sQuery(id+"F0.wireOp",EDGE,"E5509"),sQuery(id+"F0.wireOp",EDGE,"E5510"),sQuery(id+"F0.wireOp",EDGE,"E5511"),sQuery(id+"F0.wireOp",EDGE,"E5512"),sQuery(id+"F0.wireOp",EDGE,"E5513"),sQuery(id+"F0.wireOp",EDGE,"E5514"),sQuery(id+"F0.wireOp",EDGE,"E5515"),sQuery(id+"F0.wireOp",EDGE,"E5516"),sQuery(id+"F0.wireOp",EDGE,"E5517"),sQuery(id+"F0.wireOp",EDGE,"E5518"),sQuery(id+"F0.wireOp",EDGE,"E5519"),sQuery(id+"F0.wireOp",EDGE,"E5520"),sQuery(id+"F0.wireOp",EDGE,"E5521"),sQuery(id+"F0.wireOp",EDGE,"E5522"),sQuery(id+"F0.wireOp",EDGE,"E5523"),sQuery(id+"F0.wireOp",EDGE,"E5524"),sQuery(id+"F0.wireOp",EDGE,"E5525"),sQuery(id+"F0.wireOp",EDGE,"E5526"),sQuery(id+"F0.wireOp",EDGE,"E5527"),sQuery(id+"F0.wireOp",EDGE,"E5528"),sQuery(id+"F0.wireOp",EDGE,"E5529"),sQuery(id+"F0.wireOp",EDGE,"E5530"),sQuery(id+"F0.wireOp",EDGE,"E5531"),sQuery(id+"F0.wireOp",EDGE,"E5532"),sQuery(id+"F0.wireOp",EDGE,"E5533"),sQuery(id+"F0.wireOp",EDGE,"E5534"),sQuery(id+"F0.wireOp",EDGE,"E5535"),sQuery(id+"F0.wireOp",EDGE,"E5536"),sQuery(id+"F0.wireOp",EDGE,"E5537"),sQuery(id+"F0.wireOp",EDGE,"E5538"),sQuery(id+"F0.wireOp",EDGE,"E5539"),sQuery(id+"F0.wireOp",EDGE,"E5540"),sQuery(id+"F0.wireOp",EDGE,"E5541"),sQuery(id+"F0.wireOp",EDGE,"E5542"),sQuery(id+"F0.wireOp",EDGE,"E5543"),sQuery(id+"F0.wireOp",EDGE,"E5544"),sQuery(id+"F0.wireOp",EDGE,"E5545"),sQuery(id+"F0.wireOp",EDGE,"E5546"),sQuery(id+"F0.wireOp",EDGE,"E5547"),sQuery(id+"F0.wireOp",EDGE,"E5548"),sQuery(id+"F0.wireOp",EDGE,"E5549"),sQuery(id+"F0.wireOp",EDGE,"E5550"),sQuery(id+"F0.wireOp",EDGE,"E5551"),sQuery(id+"F0.wireOp",EDGE,"E5552"),sQuery(id+"F0.wireOp",EDGE,"E5553"),sQuery(id+"F0.wireOp",EDGE,"E5553"),sQuery(id+"F0.wireOp",EDGE,"E5554"),sQuery(id+"F0.wireOp",EDGE,"E5555"),sQuery(id+"F0.wireOp",EDGE,"E5556"),sQuery(id+"F0.wireOp",EDGE,"E5557"),sQuery(id+"F0.wireOp",EDGE,"E5558"),sQuery(id+"F0.wireOp",EDGE,"E5559"),sQuery(id+"F0.wireOp",EDGE,"E5560"),sQuery(id+"F0.wireOp",EDGE,"E5561"),sQuery(id+"F0.wireOp",EDGE,"E5562"),sQuery(id+"F0.wireOp",EDGE,"E5563"),sQuery(id+"F0.wireOp",EDGE,"E5564"),sQuery(id+"F0.wireOp",EDGE,"E5565"),sQuery(id+"F0.wireOp",EDGE,"E5566"),sQuery(id+"F0.wireOp",EDGE,"E5567"),sQuery(id+"F0.wireOp",EDGE,"E5568"),sQuery(id+"F0.wireOp",EDGE,"E5569"),sQuery(id+"F0.wireOp",EDGE,"E5570"),sQuery(id+"F0.wireOp",EDGE,"E5571"),sQuery(id+"F0.wireOp",EDGE,"E5572"),sQuery(id+"F0.wireOp",EDGE,"E5573"),sQuery(id+"F0.wireOp",EDGE,"E5574"),sQuery(id+"F0.wireOp",EDGE,"E5575"),sQuery(id+"F0.wireOp",EDGE,"E5576"),sQuery(id+"F0.wireOp",EDGE,"E5577"),sQuery(id+"F0.wireOp",EDGE,"E5578"),sQuery(id+"F0.wireOp",EDGE,"E5579"),sQuery(id+"F0.wireOp",EDGE,"E5580"),sQuery(id+"F0.wireOp",EDGE,"E5581"),sQuery(id+"F0.wireOp",EDGE,"E5582"),sQuery(id+"F0.wireOp",EDGE,"E5583"),sQuery(id+"F0.wireOp",EDGE,"E5584"),sQuery(id+"F0.wireOp",EDGE,"E5585"),sQuery(id+"F0.wireOp",EDGE,"E5586"),sQuery(id+"F0.wireOp",EDGE,"E5587"),sQuery(id+"F0.wireOp",EDGE,"E5588"),sQuery(id+"F0.wireOp",EDGE,"E5589"),sQuery(id+"F0.wireOp",EDGE,"E5590"),sQuery(id+"F0.wireOp",EDGE,"E5591"),sQuery(id+"F0.wireOp",EDGE,"E5592"),sQuery(id+"F0.wireOp",EDGE,"E5593"),sQuery(id+"F0.wireOp",EDGE,"E5594"),sQuery(id+"F0.wireOp",EDGE,"E5595"),sQuery(id+"F0.wireOp",EDGE,"E5596"),sQuery(id+"F0.wireOp",EDGE,"E5597"),sQuery(id+"F0.wireOp",EDGE,"E5598"),sQuery(id+"F0.wireOp",EDGE,"E5599"),sQuery(id+"F0.wireOp",EDGE,"E5600"),sQuery(id+"F0.wireOp",EDGE,"E5600"),sQuery(id+"F0.wireOp",EDGE,"E5601"),sQuery(id+"F0.wireOp",EDGE,"E5602"),sQuery(id+"F0.wireOp",EDGE,"E5603"),sQuery(id+"F0.wireOp",EDGE,"E5604"),sQuery(id+"F0.wireOp",EDGE,"E5605"),sQuery(id+"F0.wireOp",EDGE,"E5606"),sQuery(id+"F0.wireOp",EDGE,"E5606"),sQuery(id+"F0.wireOp",EDGE,"E5606"),sQuery(id+"F0.wireOp",EDGE,"E5607"),sQuery(id+"F0.wireOp",EDGE,"E5608"),sQuery(id+"F0.wireOp",EDGE,"E5609"),sQuery(id+"F0.wireOp",EDGE,"E5610"),sQuery(id+"F0.wireOp",EDGE,"E5611"),sQuery(id+"F0.wireOp",EDGE,"E5612"),sQuery(id+"F0.wireOp",EDGE,"E5613"),sQuery(id+"F0.wireOp",EDGE,"E5614"),sQuery(id+"F0.wireOp",EDGE,"E5615"),sQuery(id+"F0.wireOp",EDGE,"E5616"),sQuery(id+"F0.wireOp",EDGE,"E5617"),sQuery(id+"F0.wireOp",EDGE,"E5618"),sQuery(id+"F0.wireOp",EDGE,"E5619"),sQuery(id+"F0.wireOp",EDGE,"E5620"),sQuery(id+"F0.wireOp",EDGE,"E5621"),sQuery(id+"F0.wireOp",EDGE,"E5622"),sQuery(id+"F0.wireOp",EDGE,"E5623"),sQuery(id+"F0.wireOp",EDGE,"E5624"),sQuery(id+"F0.wireOp",EDGE,"E5625"),sQuery(id+"F0.wireOp",EDGE,"E5626"),sQuery(id+"F0.wireOp",EDGE,"E5627"),sQuery(id+"F0.wireOp",EDGE,"E5628"),sQuery(id+"F0.wireOp",EDGE,"E5629"),sQuery(id+"F0.wireOp",EDGE,"E5630"),sQuery(id+"F0.wireOp",EDGE,"E5631"),sQuery(id+"F0.wireOp",EDGE,"E5632"),sQuery(id+"F0.wireOp",EDGE,"E5633"),sQuery(id+"F0.wireOp",EDGE,"E5634"),sQuery(id+"F0.wireOp",EDGE,"E5635"),sQuery(id+"F0.wireOp",EDGE,"E5636"),sQuery(id+"F0.wireOp",EDGE,"E5637"),sQuery(id+"F0.wireOp",EDGE,"E5638"),sQuery(id+"F0.wireOp",EDGE,"E5639"),sQuery(id+"F0.wireOp",EDGE,"E5640"),sQuery(id+"F0.wireOp",EDGE,"E5641"),sQuery(id+"F0.wireOp",EDGE,"E5642"),sQuery(id+"F0.wireOp",EDGE,"E5643"),sQuery(id+"F0.wireOp",EDGE,"E5644"),sQuery(id+"F0.wireOp",EDGE,"E5645"),sQuery(id+"F0.wireOp",EDGE,"E5646"),sQuery(id+"F0.wireOp",EDGE,"E5647"),sQuery(id+"F0.wireOp",EDGE,"E5648"),sQuery(id+"F0.wireOp",EDGE,"E5648"),sQuery(id+"F0.wireOp",EDGE,"E5648"),sQuery(id+"F0.wireOp",EDGE,"E5649"),sQuery(id+"F0.wireOp",EDGE,"E5650"),sQuery(id+"F0.wireOp",EDGE,"E5651"),sQuery(id+"F0.wireOp",EDGE,"E5651"),sQuery(id+"F0.wireOp",EDGE,"E5652"),sQuery(id+"F0.wireOp",EDGE,"E5653"),sQuery(id+"F0.wireOp",EDGE,"E5654"),sQuery(id+"F0.wireOp",EDGE,"E5655"),sQuery(id+"F0.wireOp",EDGE,"E5656"),sQuery(id+"F0.wireOp",EDGE,"E5657"),sQuery(id+"F0.wireOp",EDGE,"E5658"),sQuery(id+"F0.wireOp",EDGE,"E5659"),sQuery(id+"F0.wireOp",EDGE,"E5660"),sQuery(id+"F0.wireOp",EDGE,"E5661"),sQuery(id+"F0.wireOp",EDGE,"E5662"),sQuery(id+"F0.wireOp",EDGE,"E5663"),sQuery(id+"F0.wireOp",EDGE,"E5664"),sQuery(id+"F0.wireOp",EDGE,"E5665"),sQuery(id+"F0.wireOp",EDGE,"E5666"),sQuery(id+"F0.wireOp",EDGE,"E5667"),sQuery(id+"F0.wireOp",EDGE,"E5668"),sQuery(id+"F0.wireOp",EDGE,"E5669"),sQuery(id+"F0.wireOp",EDGE,"E5669"),sQuery(id+"F0.wireOp",EDGE,"E5670"),sQuery(id+"F0.wireOp",EDGE,"E5671"),sQuery(id+"F0.wireOp",EDGE,"E5672"),sQuery(id+"F0.wireOp",EDGE,"E5673"),sQuery(id+"F0.wireOp",EDGE,"E5674"),sQuery(id+"F0.wireOp",EDGE,"E5675"),sQuery(id+"F0.wireOp",EDGE,"E5676"),sQuery(id+"F0.wireOp",EDGE,"E5677"),sQuery(id+"F0.wireOp",EDGE,"E5678"),sQuery(id+"F0.wireOp",EDGE,"E5679"),sQuery(id+"F0.wireOp",EDGE,"E5680"),sQuery(id+"F0.wireOp",EDGE,"E5681"),sQuery(id+"F0.wireOp",EDGE,"E5682"),sQuery(id+"F0.wireOp",EDGE,"E5683"),sQuery(id+"F0.wireOp",EDGE,"E5684"),sQuery(id+"F0.wireOp",EDGE,"E5685"),sQuery(id+"F0.wireOp",EDGE,"E5686"),sQuery(id+"F0.wireOp",EDGE,"E5687"),sQuery(id+"F0.wireOp",EDGE,"E5687"),sQuery(id+"F0.wireOp",EDGE,"E5687"),sQuery(id+"F0.wireOp",EDGE,"E5688"),sQuery(id+"F0.wireOp",EDGE,"E5689"),sQuery(id+"F0.wireOp",EDGE,"E5690"),sQuery(id+"F0.wireOp",EDGE,"E5691"),sQuery(id+"F0.wireOp",EDGE,"E5692"),sQuery(id+"F0.wireOp",EDGE,"E5693"),sQuery(id+"F0.wireOp",EDGE,"E5694"),sQuery(id+"F0.wireOp",EDGE,"E5695"),sQuery(id+"F0.wireOp",EDGE,"E5696"),sQuery(id+"F0.wireOp",EDGE,"E5697"),sQuery(id+"F0.wireOp",EDGE,"E5698"),sQuery(id+"F0.wireOp",EDGE,"E5699"),sQuery(id+"F0.wireOp",EDGE,"E5700"),sQuery(id+"F0.wireOp",EDGE,"E5701"),sQuery(id+"F0.wireOp",EDGE,"E5702"),sQuery(id+"F0.wireOp",EDGE,"E5703"),sQuery(id+"F0.wireOp",EDGE,"E5704"),sQuery(id+"F0.wireOp",EDGE,"E5705"),sQuery(id+"F0.wireOp",EDGE,"E5706"),sQuery(id+"F0.wireOp",EDGE,"E5707"),sQuery(id+"F0.wireOp",EDGE,"E5708"),sQuery(id+"F0.wireOp",EDGE,"E5709"),sQuery(id+"F0.wireOp",EDGE,"E5710"),sQuery(id+"F0.wireOp",EDGE,"E5711"),sQuery(id+"F0.wireOp",EDGE,"E5712"),sQuery(id+"F0.wireOp",EDGE,"E5713"),sQuery(id+"F0.wireOp",EDGE,"E5714"),sQuery(id+"F0.wireOp",EDGE,"E5715"),sQuery(id+"F0.wireOp",EDGE,"E5716"),sQuery(id+"F0.wireOp",EDGE,"E5717"),sQuery(id+"F0.wireOp",EDGE,"E5718"),sQuery(id+"F0.wireOp",EDGE,"E5719"),sQuery(id+"F0.wireOp",EDGE,"E5720"),sQuery(id+"F0.wireOp",EDGE,"E5721"),sQuery(id+"F0.wireOp",EDGE,"E5722"),sQuery(id+"F0.wireOp",EDGE,"E5723"),sQuery(id+"F0.wireOp",EDGE,"E5724"),sQuery(id+"F0.wireOp",EDGE,"E5725"),sQuery(id+"F0.wireOp",EDGE,"E5726"),sQuery(id+"F0.wireOp",EDGE,"E5727"),sQuery(id+"F0.wireOp",EDGE,"E5728"),sQuery(id+"F0.wireOp",EDGE,"E5729"),sQuery(id+"F0.wireOp",EDGE,"E5730"),sQuery(id+"F0.wireOp",EDGE,"E5731"),sQuery(id+"F0.wireOp",EDGE,"E5732"),sQuery(id+"F0.wireOp",EDGE,"E5733"),sQuery(id+"F0.wireOp",EDGE,"E5734"),sQuery(id+"F0.wireOp",EDGE,"E5735"),sQuery(id+"F0.wireOp",EDGE,"E5736"),sQuery(id+"F0.wireOp",EDGE,"E5737"),sQuery(id+"F0.wireOp",EDGE,"E5738"),sQuery(id+"F0.wireOp",EDGE,"E5739"),sQuery(id+"F0.wireOp",EDGE,"E5740"),sQuery(id+"F0.wireOp",EDGE,"E5741"),sQuery(id+"F0.wireOp",EDGE,"E5742"),sQuery(id+"F0.wireOp",EDGE,"E5743"),sQuery(id+"F0.wireOp",EDGE,"E5744"),sQuery(id+"F0.wireOp",EDGE,"E5745"),sQuery(id+"F0.wireOp",EDGE,"E5746"),sQuery(id+"F0.wireOp",EDGE,"E5747"),sQuery(id+"F0.wireOp",EDGE,"E5748"),sQuery(id+"F0.wireOp",EDGE,"E5749"),sQuery(id+"F0.wireOp",EDGE,"E5750"),sQuery(id+"F0.wireOp",EDGE,"E5751"),sQuery(id+"F0.wireOp",EDGE,"E5752"),sQuery(id+"F0.wireOp",EDGE,"E5753"),sQuery(id+"F0.wireOp",EDGE,"E5754"),sQuery(id+"F0.wireOp",EDGE,"E5755"),sQuery(id+"F0.wireOp",EDGE,"E5756"),sQuery(id+"F0.wireOp",EDGE,"E5757"),sQuery(id+"F0.wireOp",EDGE,"E5758"),sQuery(id+"F0.wireOp",EDGE,"E5759"),sQuery(id+"F0.wireOp",EDGE,"E5760"),sQuery(id+"F0.wireOp",EDGE,"E5761"),sQuery(id+"F0.wireOp",EDGE,"E5762"),sQuery(id+"F0.wireOp",EDGE,"E5763"),sQuery(id+"F0.wireOp",EDGE,"E5764"),sQuery(id+"F0.wireOp",EDGE,"E5765"),sQuery(id+"F0.wireOp",EDGE,"E5766"),sQuery(id+"F0.wireOp",EDGE,"E5767"),sQuery(id+"F0.wireOp",EDGE,"E5768"),sQuery(id+"F0.wireOp",EDGE,"E5769"),sQuery(id+"F0.wireOp",EDGE,"E5770"),sQuery(id+"F0.wireOp",EDGE,"E5771"),sQuery(id+"F0.wireOp",EDGE,"E5772"),sQuery(id+"F0.wireOp",EDGE,"E5773"),sQuery(id+"F0.wireOp",EDGE,"E5774"),sQuery(id+"F0.wireOp",EDGE,"E5775"),sQuery(id+"F0.wireOp",EDGE,"E5776"),sQuery(id+"F0.wireOp",EDGE,"E5777"),sQuery(id+"F0.wireOp",EDGE,"E5778"),sQuery(id+"F0.wireOp",EDGE,"E5779"),sQuery(id+"F0.wireOp",EDGE,"E5780"),sQuery(id+"F0.wireOp",EDGE,"E5781"),sQuery(id+"F0.wireOp",EDGE,"E5782"),sQuery(id+"F0.wireOp",EDGE,"E5783"),sQuery(id+"F0.wireOp",EDGE,"E5784"),sQuery(id+"F0.wireOp",EDGE,"E5785"),sQuery(id+"F0.wireOp",EDGE,"E5786"),sQuery(id+"F0.wireOp",EDGE,"E5787"),sQuery(id+"F0.wireOp",EDGE,"E5788"),sQuery(id+"F0.wireOp",EDGE,"E5789"),sQuery(id+"F0.wireOp",EDGE,"E5790"),sQuery(id+"F0.wireOp",EDGE,"E5791"),sQuery(id+"F0.wireOp",EDGE,"E5792"),sQuery(id+"F0.wireOp",EDGE,"E5793"),sQuery(id+"F0.wireOp",EDGE,"E5794"),sQuery(id+"F0.wireOp",EDGE,"E5795"),sQuery(id+"F0.wireOp",EDGE,"E5796"),sQuery(id+"F0.wireOp",EDGE,"E5797"),sQuery(id+"F0.wireOp",EDGE,"E5798"),sQuery(id+"F0.wireOp",EDGE,"E5799"),sQuery(id+"F0.wireOp",EDGE,"E5800"),sQuery(id+"F0.wireOp",EDGE,"E5801"),sQuery(id+"F0.wireOp",EDGE,"E5802"),sQuery(id+"F0.wireOp",EDGE,"E5803"),sQuery(id+"F0.wireOp",EDGE,"E5804"),sQuery(id+"F0.wireOp",EDGE,"E5805"),sQuery(id+"F0.wireOp",EDGE,"E5806"),sQuery(id+"F0.wireOp",EDGE,"E5807"),sQuery(id+"F0.wireOp",EDGE,"E5808"),sQuery(id+"F0.wireOp",EDGE,"E5809"),sQuery(id+"F0.wireOp",EDGE,"E5810"),sQuery(id+"F0.wireOp",EDGE,"E5811"),sQuery(id+"F0.wireOp",EDGE,"E5812"),sQuery(id+"F0.wireOp",EDGE,"E5813"),sQuery(id+"F0.wireOp",EDGE,"E5814"),sQuery(id+"F0.wireOp",EDGE,"E5815"),sQuery(id+"F0.wireOp",EDGE,"E5816"),sQuery(id+"F0.wireOp",EDGE,"E5817"),sQuery(id+"F0.wireOp",EDGE,"E5818"),sQuery(id+"F0.wireOp",EDGE,"E5819"),sQuery(id+"F0.wireOp",EDGE,"E5820"),sQuery(id+"F0.wireOp",EDGE,"E5821"),sQuery(id+"F0.wireOp",EDGE,"E5822"),sQuery(id+"F0.wireOp",EDGE,"E5823"),sQuery(id+"F0.wireOp",EDGE,"E5824"),sQuery(id+"F0.wireOp",EDGE,"E5825"),sQuery(id+"F0.wireOp",EDGE,"E5826"),sQuery(id+"F0.wireOp",EDGE,"E5827"),sQuery(id+"F0.wireOp",EDGE,"E5828"),sQuery(id+"F0.wireOp",EDGE,"E5829"),sQuery(id+"F0.wireOp",EDGE,"E5830"),sQuery(id+"F0.wireOp",EDGE,"E5831"),sQuery(id+"F0.wireOp",EDGE,"E5832"),sQuery(id+"F0.wireOp",EDGE,"E5833"),sQuery(id+"F0.wireOp",EDGE,"E5834"),sQuery(id+"F0.wireOp",EDGE,"E5835"),sQuery(id+"F0.wireOp",EDGE,"E5836"),sQuery(id+"F0.wireOp",EDGE,"E5837"),sQuery(id+"F0.wireOp",EDGE,"E5838"),sQuery(id+"F0.wireOp",EDGE,"E5839"),sQuery(id+"F0.wireOp",EDGE,"E5840"),sQuery(id+"F0.wireOp",EDGE,"E5841"),sQuery(id+"F0.wireOp",EDGE,"E5842"),sQuery(id+"F0.wireOp",EDGE,"E5843"),sQuery(id+"F0.wireOp",EDGE,"E5844"),sQuery(id+"F0.wireOp",EDGE,"E5845"),sQuery(id+"F0.wireOp",EDGE,"E5846"),sQuery(id+"F0.wireOp",EDGE,"E5847"),sQuery(id+"F0.wireOp",EDGE,"E5848"),sQuery(id+"F0.wireOp",EDGE,"E5849"),sQuery(id+"F0.wireOp",EDGE,"E5850"),sQuery(id+"F0.wireOp",EDGE,"E5851"),sQuery(id+"F0.wireOp",EDGE,"E5852"),sQuery(id+"F0.wireOp",EDGE,"E5853"),sQuery(id+"F0.wireOp",EDGE,"E5854"),sQuery(id+"F0.wireOp",EDGE,"E5855"),sQuery(id+"F0.wireOp",EDGE,"E5856"),sQuery(id+"F0.wireOp",EDGE,"E5857"),sQuery(id+"F0.wireOp",EDGE,"E5858"),sQuery(id+"F0.wireOp",EDGE,"E5859"),sQuery(id+"F0.wireOp",EDGE,"E5860"),sQuery(id+"F0.wireOp",EDGE,"E5861"),sQuery(id+"F0.wireOp",EDGE,"E5862"),sQuery(id+"F0.wireOp",EDGE,"E5863"),sQuery(id+"F0.wireOp",EDGE,"E5864"),sQuery(id+"F0.wireOp",EDGE,"E5865"),sQuery(id+"F0.wireOp",EDGE,"E5866"),sQuery(id+"F0.wireOp",EDGE,"E5867"),sQuery(id+"F0.wireOp",EDGE,"E5868"),sQuery(id+"F0.wireOp",EDGE,"E5869"),sQuery(id+"F0.wireOp",EDGE,"E5870"),sQuery(id+"F0.wireOp",EDGE,"E5871"),sQuery(id+"F0.wireOp",EDGE,"E5872"),sQuery(id+"F0.wireOp",EDGE,"E5873"),sQuery(id+"F0.wireOp",EDGE,"E5874"),sQuery(id+"F0.wireOp",EDGE,"E5875"),sQuery(id+"F0.wireOp",EDGE,"E5876"),sQuery(id+"F0.wireOp",EDGE,"E5877"),sQuery(id+"F0.wireOp",EDGE,"E5878"),sQuery(id+"F0.wireOp",EDGE,"E5879"),sQuery(id+"F0.wireOp",EDGE,"E5880"),sQuery(id+"F0.wireOp",EDGE,"E5881"),sQuery(id+"F0.wireOp",EDGE,"E5882"),sQuery(id+"F0.wireOp",EDGE,"E5883"),sQuery(id+"F0.wireOp",EDGE,"E5884"),sQuery(id+"F0.wireOp",EDGE,"E5885"),sQuery(id+"F0.wireOp",EDGE,"E5886"),sQuery(id+"F0.wireOp",EDGE,"E5887"),sQuery(id+"F0.wireOp",EDGE,"E5888"),sQuery(id+"F0.wireOp",EDGE,"E5889"),sQuery(id+"F0.wireOp",EDGE,"E5890"),sQuery(id+"F0.wireOp",EDGE,"E5891"),sQuery(id+"F0.wireOp",EDGE,"E5892"),sQuery(id+"F0.wireOp",EDGE,"E5893"),sQuery(id+"F0.wireOp",EDGE,"E5894"),sQuery(id+"F0.wireOp",EDGE,"E5895"),sQuery(id+"F0.wireOp",EDGE,"E5896"),sQuery(id+"F0.wireOp",EDGE,"E5897"),sQuery(id+"F0.wireOp",EDGE,"E5898"),sQuery(id+"F0.wireOp",EDGE,"E5899"),sQuery(id+"F0.wireOp",EDGE,"E5900"),sQuery(id+"F0.wireOp",EDGE,"E5901"),sQuery(id+"F0.wireOp",EDGE,"E5902"),sQuery(id+"F0.wireOp",EDGE,"E5903"),sQuery(id+"F0.wireOp",EDGE,"E5904"),sQuery(id+"F0.wireOp",EDGE,"E5905"),sQuery(id+"F0.wireOp",EDGE,"E5906"),sQuery(id+"F0.wireOp",EDGE,"E5907"),sQuery(id+"F0.wireOp",EDGE,"E5908"),sQuery(id+"F0.wireOp",EDGE,"E5909"),sQuery(id+"F0.wireOp",EDGE,"E5910"),sQuery(id+"F0.wireOp",EDGE,"E5911"),sQuery(id+"F0.wireOp",EDGE,"E5912"),sQuery(id+"F0.wireOp",EDGE,"E5913"),sQuery(id+"F0.wireOp",EDGE,"E5914"),sQuery(id+"F0.wireOp",EDGE,"E5915"),sQuery(id+"F0.wireOp",EDGE,"E5916"),sQuery(id+"F0.wireOp",EDGE,"E5917"),sQuery(id+"F0.wireOp",EDGE,"E5918"),sQuery(id+"F0.wireOp",EDGE,"E5919"),sQuery(id+"F0.wireOp",EDGE,"E5920"),sQuery(id+"F0.wireOp",EDGE,"E5921"),sQuery(id+"F0.wireOp",EDGE,"E5922"),sQuery(id+"F0.wireOp",EDGE,"E5923"),sQuery(id+"F0.wireOp",EDGE,"E5924"),sQuery(id+"F0.wireOp",EDGE,"E5925"),sQuery(id+"F0.wireOp",EDGE,"E5926"),sQuery(id+"F0.wireOp",EDGE,"E5927"),sQuery(id+"F0.wireOp",EDGE,"E5928"),sQuery(id+"F0.wireOp",EDGE,"E5929"),sQuery(id+"F0.wireOp",EDGE,"E5930"),sQuery(id+"F0.wireOp",EDGE,"E5931"),sQuery(id+"F0.wireOp",EDGE,"E5932"),sQuery(id+"F0.wireOp",EDGE,"E5933"),sQuery(id+"F0.wireOp",EDGE,"E5934"),sQuery(id+"F0.wireOp",EDGE,"E5935"),sQuery(id+"F0.wireOp",EDGE,"E5936"),sQuery(id+"F0.wireOp",EDGE,"E5937"),sQuery(id+"F0.wireOp",EDGE,"E5938"),sQuery(id+"F0.wireOp",EDGE,"E5939"),sQuery(id+"F0.wireOp",EDGE,"E5940"),sQuery(id+"F0.wireOp",EDGE,"E5941"),sQuery(id+"F0.wireOp",EDGE,"E5942"),sQuery(id+"F0.wireOp",EDGE,"E5943"),sQuery(id+"F0.wireOp",EDGE,"E5944"),sQuery(id+"F0.wireOp",EDGE,"E5945"),sQuery(id+"F0.wireOp",EDGE,"E5946"),sQuery(id+"F0.wireOp",EDGE,"E5947"),sQuery(id+"F0.wireOp",EDGE,"E5948"),sQuery(id+"F0.wireOp",EDGE,"E5949"),sQuery(id+"F0.wireOp",EDGE,"E5950"),sQuery(id+"F0.wireOp",EDGE,"E5951"),sQuery(id+"F0.wireOp",EDGE,"E5952"),sQuery(id+"F0.wireOp",EDGE,"E5953"),sQuery(id+"F0.wireOp",EDGE,"E5954"),sQuery(id+"F0.wireOp",EDGE,"E5955"),sQuery(id+"F0.wireOp",EDGE,"E5956"),sQuery(id+"F0.wireOp",EDGE,"E5957"),sQuery(id+"F0.wireOp",EDGE,"E5958"),sQuery(id+"F0.wireOp",EDGE,"E5959"),sQuery(id+"F0.wireOp",EDGE,"E5960"),sQuery(id+"F0.wireOp",EDGE,"E5961"),sQuery(id+"F0.wireOp",EDGE,"E5962"),sQuery(id+"F0.wireOp",EDGE,"E5963"),sQuery(id+"F0.wireOp",EDGE,"E5964"),sQuery(id+"F0.wireOp",EDGE,"E5965"),sQuery(id+"F0.wireOp",EDGE,"E5966"),sQuery(id+"F0.wireOp",EDGE,"E5967"),sQuery(id+"F0.wireOp",EDGE,"E5968"),sQuery(id+"F0.wireOp",EDGE,"E5969"),sQuery(id+"F0.wireOp",EDGE,"E5970"),sQuery(id+"F0.wireOp",EDGE,"E5971"),sQuery(id+"F0.wireOp",EDGE,"E5972"),sQuery(id+"F0.wireOp",EDGE,"E5973"),sQuery(id+"F0.wireOp",EDGE,"E5974"),sQuery(id+"F0.wireOp",EDGE,"E5975"),sQuery(id+"F0.wireOp",EDGE,"E5976"),sQuery(id+"F0.wireOp",EDGE,"E5977"),sQuery(id+"F0.wireOp",EDGE,"E5978"),sQuery(id+"F0.wireOp",EDGE,"E5979"),sQuery(id+"F0.wireOp",EDGE,"E5980"),sQuery(id+"F0.wireOp",EDGE,"E5981"),sQuery(id+"F0.wireOp",EDGE,"E5982"),sQuery(id+"F0.wireOp",EDGE,"E5983"),sQuery(id+"F0.wireOp",EDGE,"E5984"),sQuery(id+"F0.wireOp",EDGE,"E5985"),sQuery(id+"F0.wireOp",EDGE,"E5986"),sQuery(id+"F0.wireOp",EDGE,"E5987"),sQuery(id+"F0.wireOp",EDGE,"E5988"),sQuery(id+"F0.wireOp",EDGE,"E5989"),sQuery(id+"F0.wireOp",EDGE,"E5990"),sQuery(id+"F0.wireOp",EDGE,"E5991"),sQuery(id+"F0.wireOp",EDGE,"E5992"),sQuery(id+"F0.wireOp",EDGE,"E5993"),sQuery(id+"F0.wireOp",EDGE,"E5994"),sQuery(id+"F0.wireOp",EDGE,"E5995"),sQuery(id+"F0.wireOp",EDGE,"E5996"),sQuery(id+"F0.wireOp",EDGE,"E5997"),sQuery(id+"F0.wireOp",EDGE,"E5998"),sQuery(id+"F0.wireOp",EDGE,"E5999"),sQuery(id+"F0.wireOp",EDGE,"E6000"),sQuery(id+"F0.wireOp",EDGE,"E6001"),sQuery(id+"F0.wireOp",EDGE,"E6002"),sQuery(id+"F0.wireOp",EDGE,"E6003"),sQuery(id+"F0.wireOp",EDGE,"E6004"),sQuery(id+"F0.wireOp",EDGE,"E6005"),sQuery(id+"F0.wireOp",EDGE,"E6006"),sQuery(id+"F0.wireOp",EDGE,"E6007"),sQuery(id+"F0.wireOp",EDGE,"E6008"),sQuery(id+"F0.wireOp",EDGE,"E6009"),sQuery(id+"F0.wireOp",EDGE,"E6010"),sQuery(id+"F0.wireOp",EDGE,"E6011"),sQuery(id+"F0.wireOp",EDGE,"E6012"),sQuery(id+"F0.wireOp",EDGE,"E6013"),sQuery(id+"F0.wireOp",EDGE,"E6014"),sQuery(id+"F0.wireOp",EDGE,"E6015"),sQuery(id+"F0.wireOp",EDGE,"E6016"),sQuery(id+"F0.wireOp",EDGE,"E6017"),sQuery(id+"F0.wireOp",EDGE,"E6018"),sQuery(id+"F0.wireOp",EDGE,"E6019"),sQuery(id+"F0.wireOp",EDGE,"E6020"),sQuery(id+"F0.wireOp",EDGE,"E6021"),sQuery(id+"F0.wireOp",EDGE,"E6022"),sQuery(id+"F0.wireOp",EDGE,"E6023"),sQuery(id+"F0.wireOp",EDGE,"E6024"),sQuery(id+"F0.wireOp",EDGE,"E6025"),sQuery(id+"F0.wireOp",EDGE,"E6026"),sQuery(id+"F0.wireOp",EDGE,"E6027"),sQuery(id+"F0.wireOp",EDGE,"E6028"),sQuery(id+"F0.wireOp",EDGE,"E6029"),sQuery(id+"F0.wireOp",EDGE,"E6030"),sQuery(id+"F0.wireOp",EDGE,"E6031"),sQuery(id+"F0.wireOp",EDGE,"E6032"),sQuery(id+"F0.wireOp",EDGE,"E6033"),sQuery(id+"F0.wireOp",EDGE,"E6034"),sQuery(id+"F0.wireOp",EDGE,"E6035"),sQuery(id+"F0.wireOp",EDGE,"E6036"),sQuery(id+"F0.wireOp",EDGE,"E6037"),sQuery(id+"F0.wireOp",EDGE,"E6038"),sQuery(id+"F0.wireOp",EDGE,"E6039"),sQuery(id+"F0.wireOp",EDGE,"E6040"),sQuery(id+"F0.wireOp",EDGE,"E6041"),sQuery(id+"F0.wireOp",EDGE,"E6042"),sQuery(id+"F0.wireOp",EDGE,"E6043"),sQuery(id+"F0.wireOp",EDGE,"E6044"),sQuery(id+"F0.wireOp",EDGE,"E6045"),sQuery(id+"F0.wireOp",EDGE,"E6046"),sQuery(id+"F0.wireOp",EDGE,"E6047"),sQuery(id+"F0.wireOp",EDGE,"E6048"),sQuery(id+"F0.wireOp",EDGE,"E6049"),sQuery(id+"F0.wireOp",EDGE,"E6050"),sQuery(id+"F0.wireOp",EDGE,"E6051"),sQuery(id+"F0.wireOp",EDGE,"E6052"),sQuery(id+"F0.wireOp",EDGE,"E6053"),sQuery(id+"F0.wireOp",EDGE,"E6054"),sQuery(id+"F0.wireOp",EDGE,"E6055"),sQuery(id+"F0.wireOp",EDGE,"E6056"),sQuery(id+"F0.wireOp",EDGE,"E6057"),sQuery(id+"F0.wireOp",EDGE,"E6058"),sQuery(id+"F0.wireOp",EDGE,"E6059"),sQuery(id+"F0.wireOp",EDGE,"E6060"),sQuery(id+"F0.wireOp",EDGE,"E6061"),sQuery(id+"F0.wireOp",EDGE,"E6062"),sQuery(id+"F0.wireOp",EDGE,"E6063"),sQuery(id+"F0.wireOp",EDGE,"E6064"),sQuery(id+"F0.wireOp",EDGE,"E6065"),sQuery(id+"F0.wireOp",EDGE,"E6066"),sQuery(id+"F0.wireOp",EDGE,"E6067"),sQuery(id+"F0.wireOp",EDGE,"E6068"),sQuery(id+"F0.wireOp",EDGE,"E6069"),sQuery(id+"F0.wireOp",EDGE,"E6070"),sQuery(id+"F0.wireOp",EDGE,"E6071"),sQuery(id+"F0.wireOp",EDGE,"E6072"),sQuery(id+"F0.wireOp",EDGE,"E6073"),sQuery(id+"F0.wireOp",EDGE,"E6074"),sQuery(id+"F0.wireOp",EDGE,"E6075"),sQuery(id+"F0.wireOp",EDGE,"E6076"),sQuery(id+"F0.wireOp",EDGE,"E6077"),sQuery(id+"F0.wireOp",EDGE,"E6078"),sQuery(id+"F0.wireOp",EDGE,"E6079"),sQuery(id+"F0.wireOp",EDGE,"E6080"),sQuery(id+"F0.wireOp",EDGE,"E6081"),sQuery(id+"F0.wireOp",EDGE,"E6082"),sQuery(id+"F0.wireOp",EDGE,"E6083"),sQuery(id+"F0.wireOp",EDGE,"E6084"),sQuery(id+"F0.wireOp",EDGE,"E6085"),sQuery(id+"F0.wireOp",EDGE,"E6086"),sQuery(id+"F0.wireOp",EDGE,"E6087"),sQuery(id+"F0.wireOp",EDGE,"E6088"),sQuery(id+"F0.wireOp",EDGE,"E6089"),sQuery(id+"F0.wireOp",EDGE,"E6090"),sQuery(id+"F0.wireOp",EDGE,"E6091"),sQuery(id+"F0.wireOp",EDGE,"E6092"),sQuery(id+"F0.wireOp",EDGE,"E6093"),sQuery(id+"F0.wireOp",EDGE,"E6093"),sQuery(id+"F0.wireOp",EDGE,"E6094"),sQuery(id+"F0.wireOp",EDGE,"E6095"),sQuery(id+"F0.wireOp",EDGE,"E6096"),sQuery(id+"F0.wireOp",EDGE,"E6097"),sQuery(id+"F0.wireOp",EDGE,"E6098"),sQuery(id+"F0.wireOp",EDGE,"E6099"),sQuery(id+"F0.wireOp",EDGE,"E6100"),sQuery(id+"F0.wireOp",EDGE,"E6101"),sQuery(id+"F0.wireOp",EDGE,"E6102"),sQuery(id+"F0.wireOp",EDGE,"E6103"),sQuery(id+"F0.wireOp",EDGE,"E6104"),sQuery(id+"F0.wireOp",EDGE,"E6105"),sQuery(id+"F0.wireOp",EDGE,"E6106"),sQuery(id+"F0.wireOp",EDGE,"E6107"),sQuery(id+"F0.wireOp",EDGE,"E6108"),sQuery(id+"F0.wireOp",EDGE,"E6109"),sQuery(id+"F0.wireOp",EDGE,"E6110"),sQuery(id+"F0.wireOp",EDGE,"E6111"),sQuery(id+"F0.wireOp",EDGE,"E6112"),sQuery(id+"F0.wireOp",EDGE,"E6113"),sQuery(id+"F0.wireOp",EDGE,"E6114"),sQuery(id+"F0.wireOp",EDGE,"E6115"),sQuery(id+"F0.wireOp",EDGE,"E6116"),sQuery(id+"F0.wireOp",EDGE,"E6117"),sQuery(id+"F0.wireOp",EDGE,"E6118"),sQuery(id+"F0.wireOp",EDGE,"E6119"),sQuery(id+"F0.wireOp",EDGE,"E6120"),sQuery(id+"F0.wireOp",EDGE,"E6121"),sQuery(id+"F0.wireOp",EDGE,"E6122"),sQuery(id+"F0.wireOp",EDGE,"E6123"),sQuery(id+"F0.wireOp",EDGE,"E6124"),sQuery(id+"F0.wireOp",EDGE,"E6125"),sQuery(id+"F0.wireOp",EDGE,"E6126"),sQuery(id+"F0.wireOp",EDGE,"E6127"),sQuery(id+"F0.wireOp",EDGE,"E6128"),sQuery(id+"F0.wireOp",EDGE,"E6129"),sQuery(id+"F0.wireOp",EDGE,"E6130"),sQuery(id+"F0.wireOp",EDGE,"E6131"),sQuery(id+"F0.wireOp",EDGE,"E6132"),sQuery(id+"F0.wireOp",EDGE,"E6133"),sQuery(id+"F0.wireOp",EDGE,"E6134"),sQuery(id+"F0.wireOp",EDGE,"E6135"),sQuery(id+"F0.wireOp",EDGE,"E6136"),sQuery(id+"F0.wireOp",EDGE,"E6137"),sQuery(id+"F0.wireOp",EDGE,"E6138"),sQuery(id+"F0.wireOp",EDGE,"E6139"),sQuery(id+"F0.wireOp",EDGE,"E6140"),sQuery(id+"F0.wireOp",EDGE,"E6140"),sQuery(id+"F0.wireOp",EDGE,"E6141"),sQuery(id+"F0.wireOp",EDGE,"E6142"),sQuery(id+"F0.wireOp",EDGE,"E6143"),sQuery(id+"F0.wireOp",EDGE,"E6144"),sQuery(id+"F0.wireOp",EDGE,"E6145"),sQuery(id+"F0.wireOp",EDGE,"E6146"),sQuery(id+"F0.wireOp",EDGE,"E6147"),sQuery(id+"F0.wireOp",EDGE,"E6148"),sQuery(id+"F0.wireOp",EDGE,"E6149"),sQuery(id+"F0.wireOp",EDGE,"E6150"),sQuery(id+"F0.wireOp",EDGE,"E6151"),sQuery(id+"F0.wireOp",EDGE,"E6152"),sQuery(id+"F0.wireOp",EDGE,"E6153"),sQuery(id+"F0.wireOp",EDGE,"E6154"),sQuery(id+"F0.wireOp",EDGE,"E6155"),sQuery(id+"F0.wireOp",EDGE,"E6156"),sQuery(id+"F0.wireOp",EDGE,"E6157"),sQuery(id+"F0.wireOp",EDGE,"E6158"),sQuery(id+"F0.wireOp",EDGE,"E6159"),sQuery(id+"F0.wireOp",EDGE,"E6160"),sQuery(id+"F0.wireOp",EDGE,"E6161"),sQuery(id+"F0.wireOp",EDGE,"E6162"),sQuery(id+"F0.wireOp",EDGE,"E6163"),sQuery(id+"F0.wireOp",EDGE,"E6164"),sQuery(id+"F0.wireOp",EDGE,"E6165"),sQuery(id+"F0.wireOp",EDGE,"E6166"),sQuery(id+"F0.wireOp",EDGE,"E6167"),sQuery(id+"F0.wireOp",EDGE,"E6168"),sQuery(id+"F0.wireOp",EDGE,"E6169"),sQuery(id+"F0.wireOp",EDGE,"E6170"),sQuery(id+"F0.wireOp",EDGE,"E6171"),sQuery(id+"F0.wireOp",EDGE,"E6172"),sQuery(id+"F0.wireOp",EDGE,"E6173"),sQuery(id+"F0.wireOp",EDGE,"E6174"),sQuery(id+"F0.wireOp",EDGE,"E6175"),sQuery(id+"F0.wireOp",EDGE,"E6176"),sQuery(id+"F0.wireOp",EDGE,"E6177"),sQuery(id+"F0.wireOp",EDGE,"E6178"),sQuery(id+"F0.wireOp",EDGE,"E6179"),sQuery(id+"F0.wireOp",EDGE,"E6180"),sQuery(id+"F0.wireOp",EDGE,"E6181"),sQuery(id+"F0.wireOp",EDGE,"E6182"),sQuery(id+"F0.wireOp",EDGE,"E6183"),sQuery(id+"F0.wireOp",EDGE,"E6184"),sQuery(id+"F0.wireOp",EDGE,"E6185"),sQuery(id+"F0.wireOp",EDGE,"E6186"),sQuery(id+"F0.wireOp",EDGE,"E6187"),sQuery(id+"F0.wireOp",EDGE,"E6188"),sQuery(id+"F0.wireOp",EDGE,"E6189"),sQuery(id+"F0.wireOp",EDGE,"E6189"),sQuery(id+"F0.wireOp",EDGE,"E6190"),sQuery(id+"F0.wireOp",EDGE,"E6191"),sQuery(id+"F0.wireOp",EDGE,"E6192"),sQuery(id+"F0.wireOp",EDGE,"E6193"),sQuery(id+"F0.wireOp",EDGE,"E6194"),sQuery(id+"F0.wireOp",EDGE,"E6195"),sQuery(id+"F0.wireOp",EDGE,"E6196"),sQuery(id+"F0.wireOp",EDGE,"E6197"),sQuery(id+"F0.wireOp",EDGE,"E6198"),sQuery(id+"F0.wireOp",EDGE,"E6199"),sQuery(id+"F0.wireOp",EDGE,"E6200"),sQuery(id+"F0.wireOp",EDGE,"E6201"),sQuery(id+"F0.wireOp",EDGE,"E6201"),sQuery(id+"F0.wireOp",EDGE,"E6202"),sQuery(id+"F0.wireOp",EDGE,"E6203"),sQuery(id+"F0.wireOp",EDGE,"E6204"),sQuery(id+"F0.wireOp",EDGE,"E6205"),sQuery(id+"F0.wireOp",EDGE,"E6206"),sQuery(id+"F0.wireOp",EDGE,"E6207"),sQuery(id+"F0.wireOp",EDGE,"E6208"),sQuery(id+"F0.wireOp",EDGE,"E6209"),sQuery(id+"F0.wireOp",EDGE,"E6210"),sQuery(id+"F0.wireOp",EDGE,"E6211"),sQuery(id+"F0.wireOp",EDGE,"E6212"),sQuery(id+"F0.wireOp",EDGE,"E6213"),sQuery(id+"F0.wireOp",EDGE,"E6214"),sQuery(id+"F0.wireOp",EDGE,"E6215"),sQuery(id+"F0.wireOp",EDGE,"E6216"),sQuery(id+"F0.wireOp",EDGE,"E6217"),sQuery(id+"F0.wireOp",EDGE,"E6218"),sQuery(id+"F0.wireOp",EDGE,"E6219"),sQuery(id+"F0.wireOp",EDGE,"E6220"),sQuery(id+"F0.wireOp",EDGE,"E6221"),sQuery(id+"F0.wireOp",EDGE,"E6222"),sQuery(id+"F0.wireOp",EDGE,"E6223"),sQuery(id+"F0.wireOp",EDGE,"E6224"),sQuery(id+"F0.wireOp",EDGE,"E6225"),sQuery(id+"F0.wireOp",EDGE,"E6226"),sQuery(id+"F0.wireOp",EDGE,"E6227"),sQuery(id+"F0.wireOp",EDGE,"E6228"),sQuery(id+"F0.wireOp",EDGE,"E6229"),sQuery(id+"F0.wireOp",EDGE,"E6230"),sQuery(id+"F0.wireOp",EDGE,"E6231"),sQuery(id+"F0.wireOp",EDGE,"E6232"),sQuery(id+"F0.wireOp",EDGE,"E6233"),sQuery(id+"F0.wireOp",EDGE,"E6234"),sQuery(id+"F0.wireOp",EDGE,"E6235"),sQuery(id+"F0.wireOp",EDGE,"E6236"),sQuery(id+"F0.wireOp",EDGE,"E6237"),sQuery(id+"F0.wireOp",EDGE,"E6238"),sQuery(id+"F0.wireOp",EDGE,"E6239"),sQuery(id+"F0.wireOp",EDGE,"E6240"),sQuery(id+"F0.wireOp",EDGE,"E6241"),sQuery(id+"F0.wireOp",EDGE,"E6242"),sQuery(id+"F0.wireOp",EDGE,"E6243"),sQuery(id+"F0.wireOp",EDGE,"E6244"),sQuery(id+"F0.wireOp",EDGE,"E6245"),sQuery(id+"F0.wireOp",EDGE,"E6246"),sQuery(id+"F0.wireOp",EDGE,"E6247"),sQuery(id+"F0.wireOp",EDGE,"E6248"),sQuery(id+"F0.wireOp",EDGE,"E6249"),sQuery(id+"F0.wireOp",EDGE,"E6250"),sQuery(id+"F0.wireOp",EDGE,"E6251"),sQuery(id+"F0.wireOp",EDGE,"E6252"),sQuery(id+"F0.wireOp",EDGE,"E6253"),sQuery(id+"F0.wireOp",EDGE,"E6254"),sQuery(id+"F0.wireOp",EDGE,"E6255"),sQuery(id+"F0.wireOp",EDGE,"E6256"),sQuery(id+"F0.wireOp",EDGE,"E6257"),sQuery(id+"F0.wireOp",EDGE,"E6258"),sQuery(id+"F0.wireOp",EDGE,"E6259"),sQuery(id+"F0.wireOp",EDGE,"E6260"),sQuery(id+"F0.wireOp",EDGE,"E6261"),sQuery(id+"F0.wireOp",EDGE,"E6262"),sQuery(id+"F0.wireOp",EDGE,"E6263"),sQuery(id+"F0.wireOp",EDGE,"E6264"),sQuery(id+"F0.wireOp",EDGE,"E6265"),sQuery(id+"F0.wireOp",EDGE,"E6266"),sQuery(id+"F0.wireOp",EDGE,"E6267"),sQuery(id+"F0.wireOp",EDGE,"E6268"),sQuery(id+"F0.wireOp",EDGE,"E6269"),sQuery(id+"F0.wireOp",EDGE,"E6270"),sQuery(id+"F0.wireOp",EDGE,"E6271"),sQuery(id+"F0.wireOp",EDGE,"E6272"),sQuery(id+"F0.wireOp",EDGE,"E6273"),sQuery(id+"F0.wireOp",EDGE,"E6274"),sQuery(id+"F0.wireOp",EDGE,"E6275"),sQuery(id+"F0.wireOp",EDGE,"E6276"),sQuery(id+"F0.wireOp",EDGE,"E6277"),sQuery(id+"F0.wireOp",EDGE,"E6278"),sQuery(id+"F0.wireOp",EDGE,"E6279"),sQuery(id+"F0.wireOp",EDGE,"E6280"),sQuery(id+"F0.wireOp",EDGE,"E6281"),sQuery(id+"F0.wireOp",EDGE,"E6282"),sQuery(id+"F0.wireOp",EDGE,"E6283"),sQuery(id+"F0.wireOp",EDGE,"E6284"),sQuery(id+"F0.wireOp",EDGE,"E6285"),sQuery(id+"F0.wireOp",EDGE,"E6286"),sQuery(id+"F0.wireOp",EDGE,"E6287"),sQuery(id+"F0.wireOp",EDGE,"E6287"),sQuery(id+"F0.wireOp",EDGE,"E6288"),sQuery(id+"F0.wireOp",EDGE,"E6289"),sQuery(id+"F0.wireOp",EDGE,"E6290"),sQuery(id+"F0.wireOp",EDGE,"E6291"),sQuery(id+"F0.wireOp",EDGE,"E6292"),sQuery(id+"F0.wireOp",EDGE,"E6293"),sQuery(id+"F0.wireOp",EDGE,"E6294"),sQuery(id+"F0.wireOp",EDGE,"E6294"),sQuery(id+"F0.wireOp",EDGE,"E6295"),sQuery(id+"F0.wireOp",EDGE,"E6296"),sQuery(id+"F0.wireOp",EDGE,"E6297"),sQuery(id+"F0.wireOp",EDGE,"E6298"),sQuery(id+"F0.wireOp",EDGE,"E6299"),sQuery(id+"F0.wireOp",EDGE,"E6300"),sQuery(id+"F0.wireOp",EDGE,"E6300"),sQuery(id+"F0.wireOp",EDGE,"E6300"),sQuery(id+"F0.wireOp",EDGE,"E6301"),sQuery(id+"F0.wireOp",EDGE,"E6302"),sQuery(id+"F0.wireOp",EDGE,"E6303"),sQuery(id+"F0.wireOp",EDGE,"E6304"),sQuery(id+"F0.wireOp",EDGE,"E6305"),sQuery(id+"F0.wireOp",EDGE,"E6306"),sQuery(id+"F0.wireOp",EDGE,"E6306"),sQuery(id+"F0.wireOp",EDGE,"E6307"),sQuery(id+"F0.wireOp",EDGE,"E6308"),sQuery(id+"F0.wireOp",EDGE,"E6309"),sQuery(id+"F0.wireOp",EDGE,"E6310"),sQuery(id+"F0.wireOp",EDGE,"E6311"),sQuery(id+"F0.wireOp",EDGE,"E6312"),sQuery(id+"F0.wireOp",EDGE,"E6313"),sQuery(id+"F0.wireOp",EDGE,"E6313"),sQuery(id+"F0.wireOp",EDGE,"E6314"),sQuery(id+"F0.wireOp",EDGE,"E6315"),sQuery(id+"F0.wireOp",EDGE,"E6316"),sQuery(id+"F0.wireOp",EDGE,"E6317"),sQuery(id+"F0.wireOp",EDGE,"E6318"),sQuery(id+"F0.wireOp",EDGE,"E6319"),sQuery(id+"F0.wireOp",EDGE,"E6320"),sQuery(id+"F0.wireOp",EDGE,"E6321"),sQuery(id+"F0.wireOp",EDGE,"E6322"),sQuery(id+"F0.wireOp",EDGE,"E6323"),sQuery(id+"F0.wireOp",EDGE,"E6324"),sQuery(id+"F0.wireOp",EDGE,"E6325"),sQuery(id+"F0.wireOp",EDGE,"E6326"),sQuery(id+"F0.wireOp",EDGE,"E6326"),sQuery(id+"F0.wireOp",EDGE,"E6326"),sQuery(id+"F0.wireOp",EDGE,"E6327"),sQuery(id+"F0.wireOp",EDGE,"E6328"),sQuery(id+"F0.wireOp",EDGE,"E6329"),sQuery(id+"F0.wireOp",EDGE,"E6330"),sQuery(id+"F0.wireOp",EDGE,"E6331"),sQuery(id+"F0.wireOp",EDGE,"E6332"),sQuery(id+"F0.wireOp",EDGE,"E6333"),sQuery(id+"F0.wireOp",EDGE,"E6334"),sQuery(id+"F0.wireOp",EDGE,"E6335"),sQuery(id+"F0.wireOp",EDGE,"E6335"),sQuery(id+"F0.wireOp",EDGE,"E6336"),sQuery(id+"F0.wireOp",EDGE,"E6337"),sQuery(id+"F0.wireOp",EDGE,"E6338"),sQuery(id+"F0.wireOp",EDGE,"E6339"),sQuery(id+"F0.wireOp",EDGE,"E6340"),sQuery(id+"F0.wireOp",EDGE,"E6341"),sQuery(id+"F0.wireOp",EDGE,"E6342"),sQuery(id+"F0.wireOp",EDGE,"E6343"),sQuery(id+"F0.wireOp",EDGE,"E6344"),sQuery(id+"F0.wireOp",EDGE,"E6345"),sQuery(id+"F0.wireOp",EDGE,"E6346"),sQuery(id+"F0.wireOp",EDGE,"E6346"),sQuery(id+"F0.wireOp",EDGE,"E6346"),sQuery(id+"F0.wireOp",EDGE,"E6347"),sQuery(id+"F0.wireOp",EDGE,"E6348"),sQuery(id+"F0.wireOp",EDGE,"E6349"),sQuery(id+"F0.wireOp",EDGE,"E6350"),sQuery(id+"F0.wireOp",EDGE,"E6351"),sQuery(id+"F0.wireOp",EDGE,"E6352"),sQuery(id+"F0.wireOp",EDGE,"E6353"),sQuery(id+"F0.wireOp",EDGE,"E6354"),sQuery(id+"F0.wireOp",EDGE,"E6354"),sQuery(id+"F0.wireOp",EDGE,"E6355"),sQuery(id+"F0.wireOp",EDGE,"E6356"),sQuery(id+"F0.wireOp",EDGE,"E6357"),sQuery(id+"F0.wireOp",EDGE,"E6358"),sQuery(id+"F0.wireOp",EDGE,"E6359"),sQuery(id+"F0.wireOp",EDGE,"E6359"),sQuery(id+"F0.wireOp",EDGE,"E6360"),sQuery(id+"F0.wireOp",EDGE,"E6361"),sQuery(id+"F0.wireOp",EDGE,"E6362"),sQuery(id+"F0.wireOp",EDGE,"E6363"),sQuery(id+"F0.wireOp",EDGE,"E6364"),sQuery(id+"F0.wireOp",EDGE,"E6365"),sQuery(id+"F0.wireOp",EDGE,"E6366"),sQuery(id+"F0.wireOp",EDGE,"E6367"),sQuery(id+"F0.wireOp",EDGE,"E6368"),sQuery(id+"F0.wireOp",EDGE,"E6369"),sQuery(id+"F0.wireOp",EDGE,"E6370"),sQuery(id+"F0.wireOp",EDGE,"E6371"),sQuery(id+"F0.wireOp",EDGE,"E6372"),sQuery(id+"F0.wireOp",EDGE,"E6373"),sQuery(id+"F0.wireOp",EDGE,"E6374"),sQuery(id+"F0.wireOp",EDGE,"E6375"),sQuery(id+"F0.wireOp",EDGE,"E6376"),sQuery(id+"F0.wireOp",EDGE,"E6376"),sQuery(id+"F0.wireOp",EDGE,"E6377"),sQuery(id+"F0.wireOp",EDGE,"E6378"),sQuery(id+"F0.wireOp",EDGE,"E6379"),sQuery(id+"F0.wireOp",EDGE,"E6380"),sQuery(id+"F0.wireOp",EDGE,"E6381"),sQuery(id+"F0.wireOp",EDGE,"E6382"),sQuery(id+"F0.wireOp",EDGE,"E6383"),sQuery(id+"F0.wireOp",EDGE,"E6384"),sQuery(id+"F0.wireOp",EDGE,"E6385"),sQuery(id+"F0.wireOp",EDGE,"E6386"),sQuery(id+"F0.wireOp",EDGE,"E6387"),sQuery(id+"F0.wireOp",EDGE,"E6388"),sQuery(id+"F0.wireOp",EDGE,"E6389"),sQuery(id+"F0.wireOp",EDGE,"E6390"),sQuery(id+"F0.wireOp",EDGE,"E6391"),sQuery(id+"F0.wireOp",EDGE,"E6392"),sQuery(id+"F0.wireOp",EDGE,"E6393"),sQuery(id+"F0.wireOp",EDGE,"E6394"),sQuery(id+"F0.wireOp",EDGE,"E6395"),sQuery(id+"F0.wireOp",EDGE,"E6396"),sQuery(id+"F0.wireOp",EDGE,"E6397"),sQuery(id+"F0.wireOp",EDGE,"E6398"),sQuery(id+"F0.wireOp",EDGE,"E6399"),sQuery(id+"F0.wireOp",EDGE,"E6400"),sQuery(id+"F0.wireOp",EDGE,"E6401"),sQuery(id+"F0.wireOp",EDGE,"E6402"),sQuery(id+"F0.wireOp",EDGE,"E6403"),sQuery(id+"F0.wireOp",EDGE,"E6404"),sQuery(id+"F0.wireOp",EDGE,"E6405"),sQuery(id+"F0.wireOp",EDGE,"E6406"),sQuery(id+"F0.wireOp",EDGE,"E6407"),sQuery(id+"F0.wireOp",EDGE,"E6408"),sQuery(id+"F0.wireOp",EDGE,"E6409"),sQuery(id+"F0.wireOp",EDGE,"E6410"),sQuery(id+"F0.wireOp",EDGE,"E6411"),sQuery(id+"F0.wireOp",EDGE,"E6412"),sQuery(id+"F0.wireOp",EDGE,"E6413"),sQuery(id+"F0.wireOp",EDGE,"E6414"),sQuery(id+"F0.wireOp",EDGE,"E6415"),sQuery(id+"F0.wireOp",EDGE,"E6416"),sQuery(id+"F0.wireOp",EDGE,"E6417"),sQuery(id+"F0.wireOp",EDGE,"E6418"),sQuery(id+"F0.wireOp",EDGE,"E6419"),sQuery(id+"F0.wireOp",EDGE,"E6420"),sQuery(id+"F0.wireOp",EDGE,"E6421"),sQuery(id+"F0.wireOp",EDGE,"E6422"),sQuery(id+"F0.wireOp",EDGE,"E6423"),sQuery(id+"F0.wireOp",EDGE,"E6424")])]});
            var Q3;
            Q3=makeQuery(id+"F1.opExtrude","SWEPT_EDGE",EDGE,{"disambiguationData":[OSD([sQuery(id+"F0.wireOp",EDGE,"E808"),sQuery(id+"F0.wireOp",EDGE,"E809")])]});
            transform(context, id + "F2", {"entities" : qUnion([Q0, Q1, Q2]), "transformType" : TransformType.ROTATION, "transformAxis" : qUnion([Q3]), "angle" : 180 * degree, "makeCopy" : false});
        }
        {
            var Q0;
            Q0=makeQuery(id+"F1.opExtrude","CAP_FACE",FACE,{"disambiguationData":[OSD([sQuery(id+"F0.wireOp",EDGE,"E0"),sQuery(id+"F0.wireOp",EDGE,"E1"),sQuery(id+"F0.wireOp",EDGE,"E2"),sQuery(id+"F0.wireOp",EDGE,"E3"),sQuery(id+"F0.wireOp",EDGE,"E4"),sQuery(id+"F0.wireOp",EDGE,"E5"),sQuery(id+"F0.wireOp",EDGE,"E6"),sQuery(id+"F0.wireOp",EDGE,"E7"),sQuery(id+"F0.wireOp",EDGE,"E8"),sQuery(id+"F0.wireOp",EDGE,"E9"),sQuery(id+"F0.wireOp",EDGE,"E10"),sQuery(id+"F0.wireOp",EDGE,"E11"),sQuery(id+"F0.wireOp",EDGE,"E12"),sQuery(id+"F0.wireOp",EDGE,"E13"),sQuery(id+"F0.wireOp",EDGE,"E14"),sQuery(id+"F0.wireOp",EDGE,"E15"),sQuery(id+"F0.wireOp",EDGE,"E16"),sQuery(id+"F0.wireOp",EDGE,"E17"),sQuery(id+"F0.wireOp",EDGE,"E18"),sQuery(id+"F0.wireOp",EDGE,"E19"),sQuery(id+"F0.wireOp",EDGE,"E20"),sQuery(id+"F0.wireOp",EDGE,"E21"),sQuery(id+"F0.wireOp",EDGE,"E22"),sQuery(id+"F0.wireOp",EDGE,"E23"),sQuery(id+"F0.wireOp",EDGE,"E24"),sQuery(id+"F0.wireOp",EDGE,"E25"),sQuery(id+"F0.wireOp",EDGE,"E26"),sQuery(id+"F0.wireOp",EDGE,"E27"),sQuery(id+"F0.wireOp",EDGE,"E28"),sQuery(id+"F0.wireOp",EDGE,"E29"),sQuery(id+"F0.wireOp",EDGE,"E30"),sQuery(id+"F0.wireOp",EDGE,"E31"),sQuery(id+"F0.wireOp",EDGE,"E32"),sQuery(id+"F0.wireOp",EDGE,"E33"),sQuery(id+"F0.wireOp",EDGE,"E34"),sQuery(id+"F0.wireOp",EDGE,"E35"),sQuery(id+"F0.wireOp",EDGE,"E36"),sQuery(id+"F0.wireOp",EDGE,"E37"),sQuery(id+"F0.wireOp",EDGE,"E38"),sQuery(id+"F0.wireOp",EDGE,"E39"),sQuery(id+"F0.wireOp",EDGE,"E40"),sQuery(id+"F0.wireOp",EDGE,"E41"),sQuery(id+"F0.wireOp",EDGE,"E42"),sQuery(id+"F0.wireOp",EDGE,"E43"),sQuery(id+"F0.wireOp",EDGE,"E44"),sQuery(id+"F0.wireOp",EDGE,"E45"),sQuery(id+"F0.wireOp",EDGE,"E46"),sQuery(id+"F0.wireOp",EDGE,"E47"),sQuery(id+"F0.wireOp",EDGE,"E48"),sQuery(id+"F0.wireOp",EDGE,"E49"),sQuery(id+"F0.wireOp",EDGE,"E50"),sQuery(id+"F0.wireOp",EDGE,"E50"),sQuery(id+"F0.wireOp",EDGE,"E51"),sQuery(id+"F0.wireOp",EDGE,"E52"),sQuery(id+"F0.wireOp",EDGE,"E53"),sQuery(id+"F0.wireOp",EDGE,"E54"),sQuery(id+"F0.wireOp",EDGE,"E54"),sQuery(id+"F0.wireOp",EDGE,"E54"),sQuery(id+"F0.wireOp",EDGE,"E55"),sQuery(id+"F0.wireOp",EDGE,"E56"),sQuery(id+"F0.wireOp",EDGE,"E56"),sQuery(id+"F0.wireOp",EDGE,"E56"),sQuery(id+"F0.wireOp",EDGE,"E56"),sQuery(id+"F0.wireOp",EDGE,"E57"),sQuery(id+"F0.wireOp",EDGE,"E58"),sQuery(id+"F0.wireOp",EDGE,"E58"),sQuery(id+"F0.wireOp",EDGE,"E58"),sQuery(id+"F0.wireOp",EDGE,"E59"),sQuery(id+"F0.wireOp",EDGE,"E60"),sQuery(id+"F0.wireOp",EDGE,"E60"),sQuery(id+"F0.wireOp",EDGE,"E60"),sQuery(id+"F0.wireOp",EDGE,"E60"),sQuery(id+"F0.wireOp",EDGE,"E61"),sQuery(id+"F0.wireOp",EDGE,"E62"),sQuery(id+"F0.wireOp",EDGE,"E62"),sQuery(id+"F0.wireOp",EDGE,"E62"),sQuery(id+"F0.wireOp",EDGE,"E63"),sQuery(id+"F0.wireOp",EDGE,"E64"),sQuery(id+"F0.wireOp",EDGE,"E64"),sQuery(id+"F0.wireOp",EDGE,"E64"),sQuery(id+"F0.wireOp",EDGE,"E64"),sQuery(id+"F0.wireOp",EDGE,"E65"),sQuery(id+"F0.wireOp",EDGE,"E66"),sQuery(id+"F0.wireOp",EDGE,"E66"),sQuery(id+"F0.wireOp",EDGE,"E66"),sQuery(id+"F0.wireOp",EDGE,"E66"),sQuery(id+"F0.wireOp",EDGE,"E67"),sQuery(id+"F0.wireOp",EDGE,"E68"),sQuery(id+"F0.wireOp",EDGE,"E69"),sQuery(id+"F0.wireOp",EDGE,"E70"),sQuery(id+"F0.wireOp",EDGE,"E70"),sQuery(id+"F0.wireOp",EDGE,"E70"),sQuery(id+"F0.wireOp",EDGE,"E70"),sQuery(id+"F0.wireOp",EDGE,"E70"),sQuery(id+"F0.wireOp",EDGE,"E70"),sQuery(id+"F0.wireOp",EDGE,"E70"),sQuery(id+"F0.wireOp",EDGE,"E71"),sQuery(id+"F0.wireOp",EDGE,"E72"),sQuery(id+"F0.wireOp",EDGE,"E73"),sQuery(id+"F0.wireOp",EDGE,"E74"),sQuery(id+"F0.wireOp",EDGE,"E74"),sQuery(id+"F0.wireOp",EDGE,"E75"),sQuery(id+"F0.wireOp",EDGE,"E76"),sQuery(id+"F0.wireOp",EDGE,"E77"),sQuery(id+"F0.wireOp",EDGE,"E78"),sQuery(id+"F0.wireOp",EDGE,"E78"),sQuery(id+"F0.wireOp",EDGE,"E79"),sQuery(id+"F0.wireOp",EDGE,"E80"),sQuery(id+"F0.wireOp",EDGE,"E81"),sQuery(id+"F0.wireOp",EDGE,"E82"),sQuery(id+"F0.wireOp",EDGE,"E82"),sQuery(id+"F0.wireOp",EDGE,"E83"),sQuery(id+"F0.wireOp",EDGE,"E84"),sQuery(id+"F0.wireOp",EDGE,"E85"),sQuery(id+"F0.wireOp",EDGE,"E86"),sQuery(id+"F0.wireOp",EDGE,"E87"),sQuery(id+"F0.wireOp",EDGE,"E88"),sQuery(id+"F0.wireOp",EDGE,"E89"),sQuery(id+"F0.wireOp",EDGE,"E90"),sQuery(id+"F0.wireOp",EDGE,"E91"),sQuery(id+"F0.wireOp",EDGE,"E92"),sQuery(id+"F0.wireOp",EDGE,"E92"),sQuery(id+"F0.wireOp",EDGE,"E93"),sQuery(id+"F0.wireOp",EDGE,"E94"),sQuery(id+"F0.wireOp",EDGE,"E94"),sQuery(id+"F0.wireOp",EDGE,"E95"),sQuery(id+"F0.wireOp",EDGE,"E96"),sQuery(id+"F0.wireOp",EDGE,"E97"),sQuery(id+"F0.wireOp",EDGE,"E98"),sQuery(id+"F0.wireOp",EDGE,"E99"),sQuery(id+"F0.wireOp",EDGE,"E100"),sQuery(id+"F0.wireOp",EDGE,"E101"),sQuery(id+"F0.wireOp",EDGE,"E101"),sQuery(id+"F0.wireOp",EDGE,"E102"),sQuery(id+"F0.wireOp",EDGE,"E103"),sQuery(id+"F0.wireOp",EDGE,"E104"),sQuery(id+"F0.wireOp",EDGE,"E105"),sQuery(id+"F0.wireOp",EDGE,"E106"),sQuery(id+"F0.wireOp",EDGE,"E107"),sQuery(id+"F0.wireOp",EDGE,"E107"),sQuery(id+"F0.wireOp",EDGE,"E107"),sQuery(id+"F0.wireOp",EDGE,"E107"),sQuery(id+"F0.wireOp",EDGE,"E108"),sQuery(id+"F0.wireOp",EDGE,"E109"),sQuery(id+"F0.wireOp",EDGE,"E110"),sQuery(id+"F0.wireOp",EDGE,"E111"),sQuery(id+"F0.wireOp",EDGE,"E111"),sQuery(id+"F0.wireOp",EDGE,"E112"),sQuery(id+"F0.wireOp",EDGE,"E113"),sQuery(id+"F0.wireOp",EDGE,"E113"),sQuery(id+"F0.wireOp",EDGE,"E114"),sQuery(id+"F0.wireOp",EDGE,"E115"),sQuery(id+"F0.wireOp",EDGE,"E116"),sQuery(id+"F0.wireOp",EDGE,"E117"),sQuery(id+"F0.wireOp",EDGE,"E117"),sQuery(id+"F0.wireOp",EDGE,"E118"),sQuery(id+"F0.wireOp",EDGE,"E119"),sQuery(id+"F0.wireOp",EDGE,"E120"),sQuery(id+"F0.wireOp",EDGE,"E121"),sQuery(id+"F0.wireOp",EDGE,"E122"),sQuery(id+"F0.wireOp",EDGE,"E123"),sQuery(id+"F0.wireOp",EDGE,"E123"),sQuery(id+"F0.wireOp",EDGE,"E124"),sQuery(id+"F0.wireOp",EDGE,"E125"),sQuery(id+"F0.wireOp",EDGE,"E126"),sQuery(id+"F0.wireOp",EDGE,"E127"),sQuery(id+"F0.wireOp",EDGE,"E127"),sQuery(id+"F0.wireOp",EDGE,"E128"),sQuery(id+"F0.wireOp",EDGE,"E129"),sQuery(id+"F0.wireOp",EDGE,"E130"),sQuery(id+"F0.wireOp",EDGE,"E131"),sQuery(id+"F0.wireOp",EDGE,"E132"),sQuery(id+"F0.wireOp",EDGE,"E133"),sQuery(id+"F0.wireOp",EDGE,"E134"),sQuery(id+"F0.wireOp",EDGE,"E135"),sQuery(id+"F0.wireOp",EDGE,"E136"),sQuery(id+"F0.wireOp",EDGE,"E137"),sQuery(id+"F0.wireOp",EDGE,"E138"),sQuery(id+"F0.wireOp",EDGE,"E139"),sQuery(id+"F0.wireOp",EDGE,"E140"),sQuery(id+"F0.wireOp",EDGE,"E141"),sQuery(id+"F0.wireOp",EDGE,"E142"),sQuery(id+"F0.wireOp",EDGE,"E143"),sQuery(id+"F0.wireOp",EDGE,"E144"),sQuery(id+"F0.wireOp",EDGE,"E145"),sQuery(id+"F0.wireOp",EDGE,"E146"),sQuery(id+"F0.wireOp",EDGE,"E147"),sQuery(id+"F0.wireOp",EDGE,"E148"),sQuery(id+"F0.wireOp",EDGE,"E149"),sQuery(id+"F0.wireOp",EDGE,"E150"),sQuery(id+"F0.wireOp",EDGE,"E151"),sQuery(id+"F0.wireOp",EDGE,"E152"),sQuery(id+"F0.wireOp",EDGE,"E153"),sQuery(id+"F0.wireOp",EDGE,"E154"),sQuery(id+"F0.wireOp",EDGE,"E155"),sQuery(id+"F0.wireOp",EDGE,"E156"),sQuery(id+"F0.wireOp",EDGE,"E157"),sQuery(id+"F0.wireOp",EDGE,"E158"),sQuery(id+"F0.wireOp",EDGE,"E159"),sQuery(id+"F0.wireOp",EDGE,"E160"),sQuery(id+"F0.wireOp",EDGE,"E161"),sQuery(id+"F0.wireOp",EDGE,"E162"),sQuery(id+"F0.wireOp",EDGE,"E163"),sQuery(id+"F0.wireOp",EDGE,"E164"),sQuery(id+"F0.wireOp",EDGE,"E165"),sQuery(id+"F0.wireOp",EDGE,"E166"),sQuery(id+"F0.wireOp",EDGE,"E167"),sQuery(id+"F0.wireOp",EDGE,"E168"),sQuery(id+"F0.wireOp",EDGE,"E169"),sQuery(id+"F0.wireOp",EDGE,"E170"),sQuery(id+"F0.wireOp",EDGE,"E171"),sQuery(id+"F0.wireOp",EDGE,"E172"),sQuery(id+"F0.wireOp",EDGE,"E173"),sQuery(id+"F0.wireOp",EDGE,"E174"),sQuery(id+"F0.wireOp",EDGE,"E175"),sQuery(id+"F0.wireOp",EDGE,"E176"),sQuery(id+"F0.wireOp",EDGE,"E177"),sQuery(id+"F0.wireOp",EDGE,"E178"),sQuery(id+"F0.wireOp",EDGE,"E179"),sQuery(id+"F0.wireOp",EDGE,"E180"),sQuery(id+"F0.wireOp",EDGE,"E181"),sQuery(id+"F0.wireOp",EDGE,"E182"),sQuery(id+"F0.wireOp",EDGE,"E183"),sQuery(id+"F0.wireOp",EDGE,"E184"),sQuery(id+"F0.wireOp",EDGE,"E185"),sQuery(id+"F0.wireOp",EDGE,"E186"),sQuery(id+"F0.wireOp",EDGE,"E187"),sQuery(id+"F0.wireOp",EDGE,"E188"),sQuery(id+"F0.wireOp",EDGE,"E189"),sQuery(id+"F0.wireOp",EDGE,"E190"),sQuery(id+"F0.wireOp",EDGE,"E191"),sQuery(id+"F0.wireOp",EDGE,"E192"),sQuery(id+"F0.wireOp",EDGE,"E193"),sQuery(id+"F0.wireOp",EDGE,"E194"),sQuery(id+"F0.wireOp",EDGE,"E195"),sQuery(id+"F0.wireOp",EDGE,"E196"),sQuery(id+"F0.wireOp",EDGE,"E197"),sQuery(id+"F0.wireOp",EDGE,"E198"),sQuery(id+"F0.wireOp",EDGE,"E199"),sQuery(id+"F0.wireOp",EDGE,"E200"),sQuery(id+"F0.wireOp",EDGE,"E201"),sQuery(id+"F0.wireOp",EDGE,"E202"),sQuery(id+"F0.wireOp",EDGE,"E203"),sQuery(id+"F0.wireOp",EDGE,"E204"),sQuery(id+"F0.wireOp",EDGE,"E205"),sQuery(id+"F0.wireOp",EDGE,"E206"),sQuery(id+"F0.wireOp",EDGE,"E207"),sQuery(id+"F0.wireOp",EDGE,"E208"),sQuery(id+"F0.wireOp",EDGE,"E209"),sQuery(id+"F0.wireOp",EDGE,"E210"),sQuery(id+"F0.wireOp",EDGE,"E211"),sQuery(id+"F0.wireOp",EDGE,"E211"),sQuery(id+"F0.wireOp",EDGE,"E211"),sQuery(id+"F0.wireOp",EDGE,"E211"),sQuery(id+"F0.wireOp",EDGE,"E212"),sQuery(id+"F0.wireOp",EDGE,"E213"),sQuery(id+"F0.wireOp",EDGE,"E214"),sQuery(id+"F0.wireOp",EDGE,"E215"),sQuery(id+"F0.wireOp",EDGE,"E216"),sQuery(id+"F0.wireOp",EDGE,"E217"),sQuery(id+"F0.wireOp",EDGE,"E218"),sQuery(id+"F0.wireOp",EDGE,"E219"),sQuery(id+"F0.wireOp",EDGE,"E220"),sQuery(id+"F0.wireOp",EDGE,"E221"),sQuery(id+"F0.wireOp",EDGE,"E222"),sQuery(id+"F0.wireOp",EDGE,"E223"),sQuery(id+"F0.wireOp",EDGE,"E224"),sQuery(id+"F0.wireOp",EDGE,"E225"),sQuery(id+"F0.wireOp",EDGE,"E226"),sQuery(id+"F0.wireOp",EDGE,"E227"),sQuery(id+"F0.wireOp",EDGE,"E228"),sQuery(id+"F0.wireOp",EDGE,"E229"),sQuery(id+"F0.wireOp",EDGE,"E230"),sQuery(id+"F0.wireOp",EDGE,"E231"),sQuery(id+"F0.wireOp",EDGE,"E232"),sQuery(id+"F0.wireOp",EDGE,"E233"),sQuery(id+"F0.wireOp",EDGE,"E234"),sQuery(id+"F0.wireOp",EDGE,"E235"),sQuery(id+"F0.wireOp",EDGE,"E236"),sQuery(id+"F0.wireOp",EDGE,"E237"),sQuery(id+"F0.wireOp",EDGE,"E238"),sQuery(id+"F0.wireOp",EDGE,"E239"),sQuery(id+"F0.wireOp",EDGE,"E240"),sQuery(id+"F0.wireOp",EDGE,"E241"),sQuery(id+"F0.wireOp",EDGE,"E242"),sQuery(id+"F0.wireOp",EDGE,"E243"),sQuery(id+"F0.wireOp",EDGE,"E244"),sQuery(id+"F0.wireOp",EDGE,"E245"),sQuery(id+"F0.wireOp",EDGE,"E246"),sQuery(id+"F0.wireOp",EDGE,"E247"),sQuery(id+"F0.wireOp",EDGE,"E248"),sQuery(id+"F0.wireOp",EDGE,"E249"),sQuery(id+"F0.wireOp",EDGE,"E250"),sQuery(id+"F0.wireOp",EDGE,"E251"),sQuery(id+"F0.wireOp",EDGE,"E252"),sQuery(id+"F0.wireOp",EDGE,"E253"),sQuery(id+"F0.wireOp",EDGE,"E254"),sQuery(id+"F0.wireOp",EDGE,"E254"),sQuery(id+"F0.wireOp",EDGE,"E254"),sQuery(id+"F0.wireOp",EDGE,"E254"),sQuery(id+"F0.wireOp",EDGE,"E255"),sQuery(id+"F0.wireOp",EDGE,"E256"),sQuery(id+"F0.wireOp",EDGE,"E257"),sQuery(id+"F0.wireOp",EDGE,"E258"),sQuery(id+"F0.wireOp",EDGE,"E259"),sQuery(id+"F0.wireOp",EDGE,"E260"),sQuery(id+"F0.wireOp",EDGE,"E261"),sQuery(id+"F0.wireOp",EDGE,"E262"),sQuery(id+"F0.wireOp",EDGE,"E263"),sQuery(id+"F0.wireOp",EDGE,"E264"),sQuery(id+"F0.wireOp",EDGE,"E265"),sQuery(id+"F0.wireOp",EDGE,"E266"),sQuery(id+"F0.wireOp",EDGE,"E267"),sQuery(id+"F0.wireOp",EDGE,"E268"),sQuery(id+"F0.wireOp",EDGE,"E269"),sQuery(id+"F0.wireOp",EDGE,"E270"),sQuery(id+"F0.wireOp",EDGE,"E271"),sQuery(id+"F0.wireOp",EDGE,"E272"),sQuery(id+"F0.wireOp",EDGE,"E273"),sQuery(id+"F0.wireOp",EDGE,"E274"),sQuery(id+"F0.wireOp",EDGE,"E275"),sQuery(id+"F0.wireOp",EDGE,"E276"),sQuery(id+"F0.wireOp",EDGE,"E277"),sQuery(id+"F0.wireOp",EDGE,"E278"),sQuery(id+"F0.wireOp",EDGE,"E279"),sQuery(id+"F0.wireOp",EDGE,"E280"),sQuery(id+"F0.wireOp",EDGE,"E281"),sQuery(id+"F0.wireOp",EDGE,"E282"),sQuery(id+"F0.wireOp",EDGE,"E283"),sQuery(id+"F0.wireOp",EDGE,"E284"),sQuery(id+"F0.wireOp",EDGE,"E285"),sQuery(id+"F0.wireOp",EDGE,"E286"),sQuery(id+"F0.wireOp",EDGE,"E287"),sQuery(id+"F0.wireOp",EDGE,"E288"),sQuery(id+"F0.wireOp",EDGE,"E289"),sQuery(id+"F0.wireOp",EDGE,"E290"),sQuery(id+"F0.wireOp",EDGE,"E291"),sQuery(id+"F0.wireOp",EDGE,"E292"),sQuery(id+"F0.wireOp",EDGE,"E293"),sQuery(id+"F0.wireOp",EDGE,"E294"),sQuery(id+"F0.wireOp",EDGE,"E295"),sQuery(id+"F0.wireOp",EDGE,"E296"),sQuery(id+"F0.wireOp",EDGE,"E297"),sQuery(id+"F0.wireOp",EDGE,"E298"),sQuery(id+"F0.wireOp",EDGE,"E299"),sQuery(id+"F0.wireOp",EDGE,"E300"),sQuery(id+"F0.wireOp",EDGE,"E301"),sQuery(id+"F0.wireOp",EDGE,"E302"),sQuery(id+"F0.wireOp",EDGE,"E303"),sQuery(id+"F0.wireOp",EDGE,"E304"),sQuery(id+"F0.wireOp",EDGE,"E305"),sQuery(id+"F0.wireOp",EDGE,"E306"),sQuery(id+"F0.wireOp",EDGE,"E307"),sQuery(id+"F0.wireOp",EDGE,"E308"),sQuery(id+"F0.wireOp",EDGE,"E309"),sQuery(id+"F0.wireOp",EDGE,"E310"),sQuery(id+"F0.wireOp",EDGE,"E311"),sQuery(id+"F0.wireOp",EDGE,"E312"),sQuery(id+"F0.wireOp",EDGE,"E313"),sQuery(id+"F0.wireOp",EDGE,"E314"),sQuery(id+"F0.wireOp",EDGE,"E315"),sQuery(id+"F0.wireOp",EDGE,"E316"),sQuery(id+"F0.wireOp",EDGE,"E317"),sQuery(id+"F0.wireOp",EDGE,"E318"),sQuery(id+"F0.wireOp",EDGE,"E319"),sQuery(id+"F0.wireOp",EDGE,"E320"),sQuery(id+"F0.wireOp",EDGE,"E321"),sQuery(id+"F0.wireOp",EDGE,"E322"),sQuery(id+"F0.wireOp",EDGE,"E323"),sQuery(id+"F0.wireOp",EDGE,"E324"),sQuery(id+"F0.wireOp",EDGE,"E325"),sQuery(id+"F0.wireOp",EDGE,"E326"),sQuery(id+"F0.wireOp",EDGE,"E327"),sQuery(id+"F0.wireOp",EDGE,"E328"),sQuery(id+"F0.wireOp",EDGE,"E329"),sQuery(id+"F0.wireOp",EDGE,"E330"),sQuery(id+"F0.wireOp",EDGE,"E331"),sQuery(id+"F0.wireOp",EDGE,"E332"),sQuery(id+"F0.wireOp",EDGE,"E333"),sQuery(id+"F0.wireOp",EDGE,"E334"),sQuery(id+"F0.wireOp",EDGE,"E335"),sQuery(id+"F0.wireOp",EDGE,"E336"),sQuery(id+"F0.wireOp",EDGE,"E337"),sQuery(id+"F0.wireOp",EDGE,"E338"),sQuery(id+"F0.wireOp",EDGE,"E339"),sQuery(id+"F0.wireOp",EDGE,"E340"),sQuery(id+"F0.wireOp",EDGE,"E341"),sQuery(id+"F0.wireOp",EDGE,"E342"),sQuery(id+"F0.wireOp",EDGE,"E343"),sQuery(id+"F0.wireOp",EDGE,"E344"),sQuery(id+"F0.wireOp",EDGE,"E345"),sQuery(id+"F0.wireOp",EDGE,"E346"),sQuery(id+"F0.wireOp",EDGE,"E347"),sQuery(id+"F0.wireOp",EDGE,"E348"),sQuery(id+"F0.wireOp",EDGE,"E349"),sQuery(id+"F0.wireOp",EDGE,"E350"),sQuery(id+"F0.wireOp",EDGE,"E351"),sQuery(id+"F0.wireOp",EDGE,"E352"),sQuery(id+"F0.wireOp",EDGE,"E353"),sQuery(id+"F0.wireOp",EDGE,"E354"),sQuery(id+"F0.wireOp",EDGE,"E355"),sQuery(id+"F0.wireOp",EDGE,"E355"),sQuery(id+"F0.wireOp",EDGE,"E356"),sQuery(id+"F0.wireOp",EDGE,"E357"),sQuery(id+"F0.wireOp",EDGE,"E358"),sQuery(id+"F0.wireOp",EDGE,"E359"),sQuery(id+"F0.wireOp",EDGE,"E360"),sQuery(id+"F0.wireOp",EDGE,"E361"),sQuery(id+"F0.wireOp",EDGE,"E362"),sQuery(id+"F0.wireOp",EDGE,"E363"),sQuery(id+"F0.wireOp",EDGE,"E364"),sQuery(id+"F0.wireOp",EDGE,"E365"),sQuery(id+"F0.wireOp",EDGE,"E366"),sQuery(id+"F0.wireOp",EDGE,"E367"),sQuery(id+"F0.wireOp",EDGE,"E368"),sQuery(id+"F0.wireOp",EDGE,"E369"),sQuery(id+"F0.wireOp",EDGE,"E370"),sQuery(id+"F0.wireOp",EDGE,"E371"),sQuery(id+"F0.wireOp",EDGE,"E372"),sQuery(id+"F0.wireOp",EDGE,"E373"),sQuery(id+"F0.wireOp",EDGE,"E374"),sQuery(id+"F0.wireOp",EDGE,"E375"),sQuery(id+"F0.wireOp",EDGE,"E376"),sQuery(id+"F0.wireOp",EDGE,"E377"),sQuery(id+"F0.wireOp",EDGE,"E378"),sQuery(id+"F0.wireOp",EDGE,"E379"),sQuery(id+"F0.wireOp",EDGE,"E380"),sQuery(id+"F0.wireOp",EDGE,"E381"),sQuery(id+"F0.wireOp",EDGE,"E382"),sQuery(id+"F0.wireOp",EDGE,"E383"),sQuery(id+"F0.wireOp",EDGE,"E384"),sQuery(id+"F0.wireOp",EDGE,"E385"),sQuery(id+"F0.wireOp",EDGE,"E386"),sQuery(id+"F0.wireOp",EDGE,"E387"),sQuery(id+"F0.wireOp",EDGE,"E388"),sQuery(id+"F0.wireOp",EDGE,"E389"),sQuery(id+"F0.wireOp",EDGE,"E390"),sQuery(id+"F0.wireOp",EDGE,"E391"),sQuery(id+"F0.wireOp",EDGE,"E392"),sQuery(id+"F0.wireOp",EDGE,"E393"),sQuery(id+"F0.wireOp",EDGE,"E394"),sQuery(id+"F0.wireOp",EDGE,"E395"),sQuery(id+"F0.wireOp",EDGE,"E396"),sQuery(id+"F0.wireOp",EDGE,"E397"),sQuery(id+"F0.wireOp",EDGE,"E398"),sQuery(id+"F0.wireOp",EDGE,"E399"),sQuery(id+"F0.wireOp",EDGE,"E400"),sQuery(id+"F0.wireOp",EDGE,"E401"),sQuery(id+"F0.wireOp",EDGE,"E401"),sQuery(id+"F0.wireOp",EDGE,"E402"),sQuery(id+"F0.wireOp",EDGE,"E403"),sQuery(id+"F0.wireOp",EDGE,"E404"),sQuery(id+"F0.wireOp",EDGE,"E405"),sQuery(id+"F0.wireOp",EDGE,"E406"),sQuery(id+"F0.wireOp",EDGE,"E407"),sQuery(id+"F0.wireOp",EDGE,"E408"),sQuery(id+"F0.wireOp",EDGE,"E409"),sQuery(id+"F0.wireOp",EDGE,"E410"),sQuery(id+"F0.wireOp",EDGE,"E411"),sQuery(id+"F0.wireOp",EDGE,"E412"),sQuery(id+"F0.wireOp",EDGE,"E413"),sQuery(id+"F0.wireOp",EDGE,"E414"),sQuery(id+"F0.wireOp",EDGE,"E415"),sQuery(id+"F0.wireOp",EDGE,"E416"),sQuery(id+"F0.wireOp",EDGE,"E417"),sQuery(id+"F0.wireOp",EDGE,"E418"),sQuery(id+"F0.wireOp",EDGE,"E419"),sQuery(id+"F0.wireOp",EDGE,"E420"),sQuery(id+"F0.wireOp",EDGE,"E421"),sQuery(id+"F0.wireOp",EDGE,"E422"),sQuery(id+"F0.wireOp",EDGE,"E423"),sQuery(id+"F0.wireOp",EDGE,"E424"),sQuery(id+"F0.wireOp",EDGE,"E425"),sQuery(id+"F0.wireOp",EDGE,"E426"),sQuery(id+"F0.wireOp",EDGE,"E427"),sQuery(id+"F0.wireOp",EDGE,"E428"),sQuery(id+"F0.wireOp",EDGE,"E429"),sQuery(id+"F0.wireOp",EDGE,"E430"),sQuery(id+"F0.wireOp",EDGE,"E431"),sQuery(id+"F0.wireOp",EDGE,"E432"),sQuery(id+"F0.wireOp",EDGE,"E433"),sQuery(id+"F0.wireOp",EDGE,"E434"),sQuery(id+"F0.wireOp",EDGE,"E435"),sQuery(id+"F0.wireOp",EDGE,"E436"),sQuery(id+"F0.wireOp",EDGE,"E437"),sQuery(id+"F0.wireOp",EDGE,"E438"),sQuery(id+"F0.wireOp",EDGE,"E439"),sQuery(id+"F0.wireOp",EDGE,"E439"),sQuery(id+"F0.wireOp",EDGE,"E440"),sQuery(id+"F0.wireOp",EDGE,"E441"),sQuery(id+"F0.wireOp",EDGE,"E442"),sQuery(id+"F0.wireOp",EDGE,"E443"),sQuery(id+"F0.wireOp",EDGE,"E444"),sQuery(id+"F0.wireOp",EDGE,"E445"),sQuery(id+"F0.wireOp",EDGE,"E446"),sQuery(id+"F0.wireOp",EDGE,"E447"),sQuery(id+"F0.wireOp",EDGE,"E448"),sQuery(id+"F0.wireOp",EDGE,"E449"),sQuery(id+"F0.wireOp",EDGE,"E450"),sQuery(id+"F0.wireOp",EDGE,"E451"),sQuery(id+"F0.wireOp",EDGE,"E452"),sQuery(id+"F0.wireOp",EDGE,"E453"),sQuery(id+"F0.wireOp",EDGE,"E454"),sQuery(id+"F0.wireOp",EDGE,"E455"),sQuery(id+"F0.wireOp",EDGE,"E456"),sQuery(id+"F0.wireOp",EDGE,"E457"),sQuery(id+"F0.wireOp",EDGE,"E458"),sQuery(id+"F0.wireOp",EDGE,"E459"),sQuery(id+"F0.wireOp",EDGE,"E460"),sQuery(id+"F0.wireOp",EDGE,"E461"),sQuery(id+"F0.wireOp",EDGE,"E462"),sQuery(id+"F0.wireOp",EDGE,"E463"),sQuery(id+"F0.wireOp",EDGE,"E464"),sQuery(id+"F0.wireOp",EDGE,"E465"),sQuery(id+"F0.wireOp",EDGE,"E466"),sQuery(id+"F0.wireOp",EDGE,"E467"),sQuery(id+"F0.wireOp",EDGE,"E468"),sQuery(id+"F0.wireOp",EDGE,"E469"),sQuery(id+"F0.wireOp",EDGE,"E470"),sQuery(id+"F0.wireOp",EDGE,"E471"),sQuery(id+"F0.wireOp",EDGE,"E472"),sQuery(id+"F0.wireOp",EDGE,"E473"),sQuery(id+"F0.wireOp",EDGE,"E474"),sQuery(id+"F0.wireOp",EDGE,"E475"),sQuery(id+"F0.wireOp",EDGE,"E476"),sQuery(id+"F0.wireOp",EDGE,"E477"),sQuery(id+"F0.wireOp",EDGE,"E478"),sQuery(id+"F0.wireOp",EDGE,"E479"),sQuery(id+"F0.wireOp",EDGE,"E480"),sQuery(id+"F0.wireOp",EDGE,"E481"),sQuery(id+"F0.wireOp",EDGE,"E482"),sQuery(id+"F0.wireOp",EDGE,"E483"),sQuery(id+"F0.wireOp",EDGE,"E484"),sQuery(id+"F0.wireOp",EDGE,"E485"),sQuery(id+"F0.wireOp",EDGE,"E486"),sQuery(id+"F0.wireOp",EDGE,"E487"),sQuery(id+"F0.wireOp",EDGE,"E488"),sQuery(id+"F0.wireOp",EDGE,"E489"),sQuery(id+"F0.wireOp",EDGE,"E490"),sQuery(id+"F0.wireOp",EDGE,"E491"),sQuery(id+"F0.wireOp",EDGE,"E492"),sQuery(id+"F0.wireOp",EDGE,"E493"),sQuery(id+"F0.wireOp",EDGE,"E494"),sQuery(id+"F0.wireOp",EDGE,"E495"),sQuery(id+"F0.wireOp",EDGE,"E496"),sQuery(id+"F0.wireOp",EDGE,"E497"),sQuery(id+"F0.wireOp",EDGE,"E498"),sQuery(id+"F0.wireOp",EDGE,"E499"),sQuery(id+"F0.wireOp",EDGE,"E500"),sQuery(id+"F0.wireOp",EDGE,"E501"),sQuery(id+"F0.wireOp",EDGE,"E502"),sQuery(id+"F0.wireOp",EDGE,"E503"),sQuery(id+"F0.wireOp",EDGE,"E503"),sQuery(id+"F0.wireOp",EDGE,"E504"),sQuery(id+"F0.wireOp",EDGE,"E505"),sQuery(id+"F0.wireOp",EDGE,"E506"),sQuery(id+"F0.wireOp",EDGE,"E507"),sQuery(id+"F0.wireOp",EDGE,"E508"),sQuery(id+"F0.wireOp",EDGE,"E509"),sQuery(id+"F0.wireOp",EDGE,"E510"),sQuery(id+"F0.wireOp",EDGE,"E511"),sQuery(id+"F0.wireOp",EDGE,"E512"),sQuery(id+"F0.wireOp",EDGE,"E513"),sQuery(id+"F0.wireOp",EDGE,"E514"),sQuery(id+"F0.wireOp",EDGE,"E515"),sQuery(id+"F0.wireOp",EDGE,"E516"),sQuery(id+"F0.wireOp",EDGE,"E517"),sQuery(id+"F0.wireOp",EDGE,"E518"),sQuery(id+"F0.wireOp",EDGE,"E519"),sQuery(id+"F0.wireOp",EDGE,"E520"),sQuery(id+"F0.wireOp",EDGE,"E521"),sQuery(id+"F0.wireOp",EDGE,"E522"),sQuery(id+"F0.wireOp",EDGE,"E523"),sQuery(id+"F0.wireOp",EDGE,"E524"),sQuery(id+"F0.wireOp",EDGE,"E525"),sQuery(id+"F0.wireOp",EDGE,"E526"),sQuery(id+"F0.wireOp",EDGE,"E527"),sQuery(id+"F0.wireOp",EDGE,"E528"),sQuery(id+"F0.wireOp",EDGE,"E529"),sQuery(id+"F0.wireOp",EDGE,"E530"),sQuery(id+"F0.wireOp",EDGE,"E531"),sQuery(id+"F0.wireOp",EDGE,"E532"),sQuery(id+"F0.wireOp",EDGE,"E533"),sQuery(id+"F0.wireOp",EDGE,"E534"),sQuery(id+"F0.wireOp",EDGE,"E535"),sQuery(id+"F0.wireOp",EDGE,"E536"),sQuery(id+"F0.wireOp",EDGE,"E537"),sQuery(id+"F0.wireOp",EDGE,"E538"),sQuery(id+"F0.wireOp",EDGE,"E539"),sQuery(id+"F0.wireOp",EDGE,"E540"),sQuery(id+"F0.wireOp",EDGE,"E541"),sQuery(id+"F0.wireOp",EDGE,"E542"),sQuery(id+"F0.wireOp",EDGE,"E543"),sQuery(id+"F0.wireOp",EDGE,"E544"),sQuery(id+"F0.wireOp",EDGE,"E545"),sQuery(id+"F0.wireOp",EDGE,"E546"),sQuery(id+"F0.wireOp",EDGE,"E547"),sQuery(id+"F0.wireOp",EDGE,"E548"),sQuery(id+"F0.wireOp",EDGE,"E549"),sQuery(id+"F0.wireOp",EDGE,"E549"),sQuery(id+"F0.wireOp",EDGE,"E550"),sQuery(id+"F0.wireOp",EDGE,"E551"),sQuery(id+"F0.wireOp",EDGE,"E552"),sQuery(id+"F0.wireOp",EDGE,"E553"),sQuery(id+"F0.wireOp",EDGE,"E554"),sQuery(id+"F0.wireOp",EDGE,"E555"),sQuery(id+"F0.wireOp",EDGE,"E556"),sQuery(id+"F0.wireOp",EDGE,"E557"),sQuery(id+"F0.wireOp",EDGE,"E558"),sQuery(id+"F0.wireOp",EDGE,"E559"),sQuery(id+"F0.wireOp",EDGE,"E560"),sQuery(id+"F0.wireOp",EDGE,"E561"),sQuery(id+"F0.wireOp",EDGE,"E562"),sQuery(id+"F0.wireOp",EDGE,"E563"),sQuery(id+"F0.wireOp",EDGE,"E564"),sQuery(id+"F0.wireOp",EDGE,"E565"),sQuery(id+"F0.wireOp",EDGE,"E566"),sQuery(id+"F0.wireOp",EDGE,"E567"),sQuery(id+"F0.wireOp",EDGE,"E568"),sQuery(id+"F0.wireOp",EDGE,"E569"),sQuery(id+"F0.wireOp",EDGE,"E570"),sQuery(id+"F0.wireOp",EDGE,"E571"),sQuery(id+"F0.wireOp",EDGE,"E572"),sQuery(id+"F0.wireOp",EDGE,"E573"),sQuery(id+"F0.wireOp",EDGE,"E574"),sQuery(id+"F0.wireOp",EDGE,"E575"),sQuery(id+"F0.wireOp",EDGE,"E576"),sQuery(id+"F0.wireOp",EDGE,"E577"),sQuery(id+"F0.wireOp",EDGE,"E578"),sQuery(id+"F0.wireOp",EDGE,"E579"),sQuery(id+"F0.wireOp",EDGE,"E580"),sQuery(id+"F0.wireOp",EDGE,"E581"),sQuery(id+"F0.wireOp",EDGE,"E582"),sQuery(id+"F0.wireOp",EDGE,"E583"),sQuery(id+"F0.wireOp",EDGE,"E584"),sQuery(id+"F0.wireOp",EDGE,"E585"),sQuery(id+"F0.wireOp",EDGE,"E586"),sQuery(id+"F0.wireOp",EDGE,"E587"),sQuery(id+"F0.wireOp",EDGE,"E588"),sQuery(id+"F0.wireOp",EDGE,"E589"),sQuery(id+"F0.wireOp",EDGE,"E590"),sQuery(id+"F0.wireOp",EDGE,"E591"),sQuery(id+"F0.wireOp",EDGE,"E592"),sQuery(id+"F0.wireOp",EDGE,"E593"),sQuery(id+"F0.wireOp",EDGE,"E594"),sQuery(id+"F0.wireOp",EDGE,"E595"),sQuery(id+"F0.wireOp",EDGE,"E596"),sQuery(id+"F0.wireOp",EDGE,"E597"),sQuery(id+"F0.wireOp",EDGE,"E598"),sQuery(id+"F0.wireOp",EDGE,"E599"),sQuery(id+"F0.wireOp",EDGE,"E600"),sQuery(id+"F0.wireOp",EDGE,"E601"),sQuery(id+"F0.wireOp",EDGE,"E602"),sQuery(id+"F0.wireOp",EDGE,"E603"),sQuery(id+"F0.wireOp",EDGE,"E604"),sQuery(id+"F0.wireOp",EDGE,"E605"),sQuery(id+"F0.wireOp",EDGE,"E606"),sQuery(id+"F0.wireOp",EDGE,"E607"),sQuery(id+"F0.wireOp",EDGE,"E608"),sQuery(id+"F0.wireOp",EDGE,"E609"),sQuery(id+"F0.wireOp",EDGE,"E610"),sQuery(id+"F0.wireOp",EDGE,"E611"),sQuery(id+"F0.wireOp",EDGE,"E612"),sQuery(id+"F0.wireOp",EDGE,"E613"),sQuery(id+"F0.wireOp",EDGE,"E614"),sQuery(id+"F0.wireOp",EDGE,"E615"),sQuery(id+"F0.wireOp",EDGE,"E616"),sQuery(id+"F0.wireOp",EDGE,"E617"),sQuery(id+"F0.wireOp",EDGE,"E618"),sQuery(id+"F0.wireOp",EDGE,"E619"),sQuery(id+"F0.wireOp",EDGE,"E620"),sQuery(id+"F0.wireOp",EDGE,"E621"),sQuery(id+"F0.wireOp",EDGE,"E622"),sQuery(id+"F0.wireOp",EDGE,"E623"),sQuery(id+"F0.wireOp",EDGE,"E624"),sQuery(id+"F0.wireOp",EDGE,"E625"),sQuery(id+"F0.wireOp",EDGE,"E626"),sQuery(id+"F0.wireOp",EDGE,"E627"),sQuery(id+"F0.wireOp",EDGE,"E628"),sQuery(id+"F0.wireOp",EDGE,"E629"),sQuery(id+"F0.wireOp",EDGE,"E630"),sQuery(id+"F0.wireOp",EDGE,"E631"),sQuery(id+"F0.wireOp",EDGE,"E632"),sQuery(id+"F0.wireOp",EDGE,"E633"),sQuery(id+"F0.wireOp",EDGE,"E634"),sQuery(id+"F0.wireOp",EDGE,"E635"),sQuery(id+"F0.wireOp",EDGE,"E636"),sQuery(id+"F0.wireOp",EDGE,"E637"),sQuery(id+"F0.wireOp",EDGE,"E638"),sQuery(id+"F0.wireOp",EDGE,"E639"),sQuery(id+"F0.wireOp",EDGE,"E640"),sQuery(id+"F0.wireOp",EDGE,"E641"),sQuery(id+"F0.wireOp",EDGE,"E642"),sQuery(id+"F0.wireOp",EDGE,"E643"),sQuery(id+"F0.wireOp",EDGE,"E644"),sQuery(id+"F0.wireOp",EDGE,"E645"),sQuery(id+"F0.wireOp",EDGE,"E646"),sQuery(id+"F0.wireOp",EDGE,"E647"),sQuery(id+"F0.wireOp",EDGE,"E648"),sQuery(id+"F0.wireOp",EDGE,"E649"),sQuery(id+"F0.wireOp",EDGE,"E650"),sQuery(id+"F0.wireOp",EDGE,"E650"),sQuery(id+"F0.wireOp",EDGE,"E651"),sQuery(id+"F0.wireOp",EDGE,"E652"),sQuery(id+"F0.wireOp",EDGE,"E653"),sQuery(id+"F0.wireOp",EDGE,"E653"),sQuery(id+"F0.wireOp",EDGE,"E653"),sQuery(id+"F0.wireOp",EDGE,"E654"),sQuery(id+"F0.wireOp",EDGE,"E655"),sQuery(id+"F0.wireOp",EDGE,"E656"),sQuery(id+"F0.wireOp",EDGE,"E657"),sQuery(id+"F0.wireOp",EDGE,"E658"),sQuery(id+"F0.wireOp",EDGE,"E659"),sQuery(id+"F0.wireOp",EDGE,"E660"),sQuery(id+"F0.wireOp",EDGE,"E661"),sQuery(id+"F0.wireOp",EDGE,"E662"),sQuery(id+"F0.wireOp",EDGE,"E663"),sQuery(id+"F0.wireOp",EDGE,"E664"),sQuery(id+"F0.wireOp",EDGE,"E665"),sQuery(id+"F0.wireOp",EDGE,"E666"),sQuery(id+"F0.wireOp",EDGE,"E667"),sQuery(id+"F0.wireOp",EDGE,"E668"),sQuery(id+"F0.wireOp",EDGE,"E669"),sQuery(id+"F0.wireOp",EDGE,"E670"),sQuery(id+"F0.wireOp",EDGE,"E671"),sQuery(id+"F0.wireOp",EDGE,"E672"),sQuery(id+"F0.wireOp",EDGE,"E673"),sQuery(id+"F0.wireOp",EDGE,"E674"),sQuery(id+"F0.wireOp",EDGE,"E675"),sQuery(id+"F0.wireOp",EDGE,"E676"),sQuery(id+"F0.wireOp",EDGE,"E677"),sQuery(id+"F0.wireOp",EDGE,"E678"),sQuery(id+"F0.wireOp",EDGE,"E679"),sQuery(id+"F0.wireOp",EDGE,"E680"),sQuery(id+"F0.wireOp",EDGE,"E681"),sQuery(id+"F0.wireOp",EDGE,"E682"),sQuery(id+"F0.wireOp",EDGE,"E683"),sQuery(id+"F0.wireOp",EDGE,"E684"),sQuery(id+"F0.wireOp",EDGE,"E685"),sQuery(id+"F0.wireOp",EDGE,"E686"),sQuery(id+"F0.wireOp",EDGE,"E687"),sQuery(id+"F0.wireOp",EDGE,"E688"),sQuery(id+"F0.wireOp",EDGE,"E689"),sQuery(id+"F0.wireOp",EDGE,"E690"),sQuery(id+"F0.wireOp",EDGE,"E691"),sQuery(id+"F0.wireOp",EDGE,"E692"),sQuery(id+"F0.wireOp",EDGE,"E693"),sQuery(id+"F0.wireOp",EDGE,"E693"),sQuery(id+"F0.wireOp",EDGE,"E693"),sQuery(id+"F0.wireOp",EDGE,"E693"),sQuery(id+"F0.wireOp",EDGE,"E694"),sQuery(id+"F0.wireOp",EDGE,"E695"),sQuery(id+"F0.wireOp",EDGE,"E696"),sQuery(id+"F0.wireOp",EDGE,"E697"),sQuery(id+"F0.wireOp",EDGE,"E698"),sQuery(id+"F0.wireOp",EDGE,"E699"),sQuery(id+"F0.wireOp",EDGE,"E700"),sQuery(id+"F0.wireOp",EDGE,"E701"),sQuery(id+"F0.wireOp",EDGE,"E702"),sQuery(id+"F0.wireOp",EDGE,"E703"),sQuery(id+"F0.wireOp",EDGE,"E704"),sQuery(id+"F0.wireOp",EDGE,"E705"),sQuery(id+"F0.wireOp",EDGE,"E706"),sQuery(id+"F0.wireOp",EDGE,"E707"),sQuery(id+"F0.wireOp",EDGE,"E708"),sQuery(id+"F0.wireOp",EDGE,"E709"),sQuery(id+"F0.wireOp",EDGE,"E710"),sQuery(id+"F0.wireOp",EDGE,"E711"),sQuery(id+"F0.wireOp",EDGE,"E712"),sQuery(id+"F0.wireOp",EDGE,"E713"),sQuery(id+"F0.wireOp",EDGE,"E714"),sQuery(id+"F0.wireOp",EDGE,"E715"),sQuery(id+"F0.wireOp",EDGE,"E716"),sQuery(id+"F0.wireOp",EDGE,"E717"),sQuery(id+"F0.wireOp",EDGE,"E718"),sQuery(id+"F0.wireOp",EDGE,"E719"),sQuery(id+"F0.wireOp",EDGE,"E720"),sQuery(id+"F0.wireOp",EDGE,"E721"),sQuery(id+"F0.wireOp",EDGE,"E722"),sQuery(id+"F0.wireOp",EDGE,"E723"),sQuery(id+"F0.wireOp",EDGE,"E724"),sQuery(id+"F0.wireOp",EDGE,"E725"),sQuery(id+"F0.wireOp",EDGE,"E726"),sQuery(id+"F0.wireOp",EDGE,"E727"),sQuery(id+"F0.wireOp",EDGE,"E728"),sQuery(id+"F0.wireOp",EDGE,"E729"),sQuery(id+"F0.wireOp",EDGE,"E730"),sQuery(id+"F0.wireOp",EDGE,"E731"),sQuery(id+"F0.wireOp",EDGE,"E732"),sQuery(id+"F0.wireOp",EDGE,"E733"),sQuery(id+"F0.wireOp",EDGE,"E734"),sQuery(id+"F0.wireOp",EDGE,"E734"),sQuery(id+"F0.wireOp",EDGE,"E735"),sQuery(id+"F0.wireOp",EDGE,"E736"),sQuery(id+"F0.wireOp",EDGE,"E737"),sQuery(id+"F0.wireOp",EDGE,"E738"),sQuery(id+"F0.wireOp",EDGE,"E739"),sQuery(id+"F0.wireOp",EDGE,"E740"),sQuery(id+"F0.wireOp",EDGE,"E741"),sQuery(id+"F0.wireOp",EDGE,"E742"),sQuery(id+"F0.wireOp",EDGE,"E743"),sQuery(id+"F0.wireOp",EDGE,"E744"),sQuery(id+"F0.wireOp",EDGE,"E745"),sQuery(id+"F0.wireOp",EDGE,"E746"),sQuery(id+"F0.wireOp",EDGE,"E747"),sQuery(id+"F0.wireOp",EDGE,"E748"),sQuery(id+"F0.wireOp",EDGE,"E749"),sQuery(id+"F0.wireOp",EDGE,"E750"),sQuery(id+"F0.wireOp",EDGE,"E751"),sQuery(id+"F0.wireOp",EDGE,"E752"),sQuery(id+"F0.wireOp",EDGE,"E753"),sQuery(id+"F0.wireOp",EDGE,"E754"),sQuery(id+"F0.wireOp",EDGE,"E755"),sQuery(id+"F0.wireOp",EDGE,"E756"),sQuery(id+"F0.wireOp",EDGE,"E757"),sQuery(id+"F0.wireOp",EDGE,"E758"),sQuery(id+"F0.wireOp",EDGE,"E759"),sQuery(id+"F0.wireOp",EDGE,"E760"),sQuery(id+"F0.wireOp",EDGE,"E761"),sQuery(id+"F0.wireOp",EDGE,"E762"),sQuery(id+"F0.wireOp",EDGE,"E763"),sQuery(id+"F0.wireOp",EDGE,"E764"),sQuery(id+"F0.wireOp",EDGE,"E764"),sQuery(id+"F0.wireOp",EDGE,"E765"),sQuery(id+"F0.wireOp",EDGE,"E766"),sQuery(id+"F0.wireOp",EDGE,"E767"),sQuery(id+"F0.wireOp",EDGE,"E768"),sQuery(id+"F0.wireOp",EDGE,"E769"),sQuery(id+"F0.wireOp",EDGE,"E770"),sQuery(id+"F0.wireOp",EDGE,"E771"),sQuery(id+"F0.wireOp",EDGE,"E772"),sQuery(id+"F0.wireOp",EDGE,"E773"),sQuery(id+"F0.wireOp",EDGE,"E774"),sQuery(id+"F0.wireOp",EDGE,"E775"),sQuery(id+"F0.wireOp",EDGE,"E776"),sQuery(id+"F0.wireOp",EDGE,"E777"),sQuery(id+"F0.wireOp",EDGE,"E778"),sQuery(id+"F0.wireOp",EDGE,"E779"),sQuery(id+"F0.wireOp",EDGE,"E780"),sQuery(id+"F0.wireOp",EDGE,"E781"),sQuery(id+"F0.wireOp",EDGE,"E781"),sQuery(id+"F0.wireOp",EDGE,"E782"),sQuery(id+"F0.wireOp",EDGE,"E783"),sQuery(id+"F0.wireOp",EDGE,"E784"),sQuery(id+"F0.wireOp",EDGE,"E785"),sQuery(id+"F0.wireOp",EDGE,"E786"),sQuery(id+"F0.wireOp",EDGE,"E787"),sQuery(id+"F0.wireOp",EDGE,"E788"),sQuery(id+"F0.wireOp",EDGE,"E789"),sQuery(id+"F0.wireOp",EDGE,"E790"),sQuery(id+"F0.wireOp",EDGE,"E791"),sQuery(id+"F0.wireOp",EDGE,"E792"),sQuery(id+"F0.wireOp",EDGE,"E793"),sQuery(id+"F0.wireOp",EDGE,"E794"),sQuery(id+"F0.wireOp",EDGE,"E795"),sQuery(id+"F0.wireOp",EDGE,"E796"),sQuery(id+"F0.wireOp",EDGE,"E797"),sQuery(id+"F0.wireOp",EDGE,"E798"),sQuery(id+"F0.wireOp",EDGE,"E799"),sQuery(id+"F0.wireOp",EDGE,"E800"),sQuery(id+"F0.wireOp",EDGE,"E801"),sQuery(id+"F0.wireOp",EDGE,"E802"),sQuery(id+"F0.wireOp",EDGE,"E803"),sQuery(id+"F0.wireOp",EDGE,"E804"),sQuery(id+"F0.wireOp",EDGE,"E805"),sQuery(id+"F0.wireOp",EDGE,"E806"),sQuery(id+"F0.wireOp",EDGE,"E807"),sQuery(id+"F0.wireOp",EDGE,"E808"),sQuery(id+"F0.wireOp",EDGE,"E809"),sQuery(id+"F0.wireOp",EDGE,"E810"),sQuery(id+"F0.wireOp",EDGE,"E811"),sQuery(id+"F0.wireOp",EDGE,"E812"),sQuery(id+"F0.wireOp",EDGE,"E813"),sQuery(id+"F0.wireOp",EDGE,"E814"),sQuery(id+"F0.wireOp",EDGE,"E815"),sQuery(id+"F0.wireOp",EDGE,"E816"),sQuery(id+"F0.wireOp",EDGE,"E817"),sQuery(id+"F0.wireOp",EDGE,"E818"),sQuery(id+"F0.wireOp",EDGE,"E819"),sQuery(id+"F0.wireOp",EDGE,"E820"),sQuery(id+"F0.wireOp",EDGE,"E821"),sQuery(id+"F0.wireOp",EDGE,"E822"),sQuery(id+"F0.wireOp",EDGE,"E823"),sQuery(id+"F0.wireOp",EDGE,"E824"),sQuery(id+"F0.wireOp",EDGE,"E825"),sQuery(id+"F0.wireOp",EDGE,"E826"),sQuery(id+"F0.wireOp",EDGE,"E827"),sQuery(id+"F0.wireOp",EDGE,"E828"),sQuery(id+"F0.wireOp",EDGE,"E829"),sQuery(id+"F0.wireOp",EDGE,"E830"),sQuery(id+"F0.wireOp",EDGE,"E831"),sQuery(id+"F0.wireOp",EDGE,"E832"),sQuery(id+"F0.wireOp",EDGE,"E833"),sQuery(id+"F0.wireOp",EDGE,"E834"),sQuery(id+"F0.wireOp",EDGE,"E835"),sQuery(id+"F0.wireOp",EDGE,"E836"),sQuery(id+"F0.wireOp",EDGE,"E837"),sQuery(id+"F0.wireOp",EDGE,"E838"),sQuery(id+"F0.wireOp",EDGE,"E839"),sQuery(id+"F0.wireOp",EDGE,"E840"),sQuery(id+"F0.wireOp",EDGE,"E841"),sQuery(id+"F0.wireOp",EDGE,"E842"),sQuery(id+"F0.wireOp",EDGE,"E843"),sQuery(id+"F0.wireOp",EDGE,"E844"),sQuery(id+"F0.wireOp",EDGE,"E845"),sQuery(id+"F0.wireOp",EDGE,"E846"),sQuery(id+"F0.wireOp",EDGE,"E847"),sQuery(id+"F0.wireOp",EDGE,"E848"),sQuery(id+"F0.wireOp",EDGE,"E849"),sQuery(id+"F0.wireOp",EDGE,"E850"),sQuery(id+"F0.wireOp",EDGE,"E851"),sQuery(id+"F0.wireOp",EDGE,"E852"),sQuery(id+"F0.wireOp",EDGE,"E853"),sQuery(id+"F0.wireOp",EDGE,"E854"),sQuery(id+"F0.wireOp",EDGE,"E855"),sQuery(id+"F0.wireOp",EDGE,"E856"),sQuery(id+"F0.wireOp",EDGE,"E857"),sQuery(id+"F0.wireOp",EDGE,"E858"),sQuery(id+"F0.wireOp",EDGE,"E859"),sQuery(id+"F0.wireOp",EDGE,"E860"),sQuery(id+"F0.wireOp",EDGE,"E861"),sQuery(id+"F0.wireOp",EDGE,"E862"),sQuery(id+"F0.wireOp",EDGE,"E863"),sQuery(id+"F0.wireOp",EDGE,"E864"),sQuery(id+"F0.wireOp",EDGE,"E865"),sQuery(id+"F0.wireOp",EDGE,"E866"),sQuery(id+"F0.wireOp",EDGE,"E867"),sQuery(id+"F0.wireOp",EDGE,"E868"),sQuery(id+"F0.wireOp",EDGE,"E869"),sQuery(id+"F0.wireOp",EDGE,"E870"),sQuery(id+"F0.wireOp",EDGE,"E871"),sQuery(id+"F0.wireOp",EDGE,"E872"),sQuery(id+"F0.wireOp",EDGE,"E873"),sQuery(id+"F0.wireOp",EDGE,"E874"),sQuery(id+"F0.wireOp",EDGE,"E875"),sQuery(id+"F0.wireOp",EDGE,"E876"),sQuery(id+"F0.wireOp",EDGE,"E877"),sQuery(id+"F0.wireOp",EDGE,"E878"),sQuery(id+"F0.wireOp",EDGE,"E879"),sQuery(id+"F0.wireOp",EDGE,"E880"),sQuery(id+"F0.wireOp",EDGE,"E881"),sQuery(id+"F0.wireOp",EDGE,"E882"),sQuery(id+"F0.wireOp",EDGE,"E883"),sQuery(id+"F0.wireOp",EDGE,"E884"),sQuery(id+"F0.wireOp",EDGE,"E885"),sQuery(id+"F0.wireOp",EDGE,"E886"),sQuery(id+"F0.wireOp",EDGE,"E887"),sQuery(id+"F0.wireOp",EDGE,"E888"),sQuery(id+"F0.wireOp",EDGE,"E889"),sQuery(id+"F0.wireOp",EDGE,"E890"),sQuery(id+"F0.wireOp",EDGE,"E891"),sQuery(id+"F0.wireOp",EDGE,"E892"),sQuery(id+"F0.wireOp",EDGE,"E893"),sQuery(id+"F0.wireOp",EDGE,"E894"),sQuery(id+"F0.wireOp",EDGE,"E895"),sQuery(id+"F0.wireOp",EDGE,"E896"),sQuery(id+"F0.wireOp",EDGE,"E897"),sQuery(id+"F0.wireOp",EDGE,"E898"),sQuery(id+"F0.wireOp",EDGE,"E899"),sQuery(id+"F0.wireOp",EDGE,"E900"),sQuery(id+"F0.wireOp",EDGE,"E901"),sQuery(id+"F0.wireOp",EDGE,"E902"),sQuery(id+"F0.wireOp",EDGE,"E903"),sQuery(id+"F0.wireOp",EDGE,"E904"),sQuery(id+"F0.wireOp",EDGE,"E905"),sQuery(id+"F0.wireOp",EDGE,"E906"),sQuery(id+"F0.wireOp",EDGE,"E907"),sQuery(id+"F0.wireOp",EDGE,"E908"),sQuery(id+"F0.wireOp",EDGE,"E909"),sQuery(id+"F0.wireOp",EDGE,"E910"),sQuery(id+"F0.wireOp",EDGE,"E911"),sQuery(id+"F0.wireOp",EDGE,"E912"),sQuery(id+"F0.wireOp",EDGE,"E913"),sQuery(id+"F0.wireOp",EDGE,"E914"),sQuery(id+"F0.wireOp",EDGE,"E915"),sQuery(id+"F0.wireOp",EDGE,"E916"),sQuery(id+"F0.wireOp",EDGE,"E917"),sQuery(id+"F0.wireOp",EDGE,"E918"),sQuery(id+"F0.wireOp",EDGE,"E919"),sQuery(id+"F0.wireOp",EDGE,"E920"),sQuery(id+"F0.wireOp",EDGE,"E921"),sQuery(id+"F0.wireOp",EDGE,"E922"),sQuery(id+"F0.wireOp",EDGE,"E923"),sQuery(id+"F0.wireOp",EDGE,"E924"),sQuery(id+"F0.wireOp",EDGE,"E925"),sQuery(id+"F0.wireOp",EDGE,"E926"),sQuery(id+"F0.wireOp",EDGE,"E927"),sQuery(id+"F0.wireOp",EDGE,"E928"),sQuery(id+"F0.wireOp",EDGE,"E929"),sQuery(id+"F0.wireOp",EDGE,"E930"),sQuery(id+"F0.wireOp",EDGE,"E931"),sQuery(id+"F0.wireOp",EDGE,"E932"),sQuery(id+"F0.wireOp",EDGE,"E933"),sQuery(id+"F0.wireOp",EDGE,"E934"),sQuery(id+"F0.wireOp",EDGE,"E935"),sQuery(id+"F0.wireOp",EDGE,"E936"),sQuery(id+"F0.wireOp",EDGE,"E937"),sQuery(id+"F0.wireOp",EDGE,"E938"),sQuery(id+"F0.wireOp",EDGE,"E939"),sQuery(id+"F0.wireOp",EDGE,"E940"),sQuery(id+"F0.wireOp",EDGE,"E941"),sQuery(id+"F0.wireOp",EDGE,"E942"),sQuery(id+"F0.wireOp",EDGE,"E943"),sQuery(id+"F0.wireOp",EDGE,"E943"),sQuery(id+"F0.wireOp",EDGE,"E943"),sQuery(id+"F0.wireOp",EDGE,"E944"),sQuery(id+"F0.wireOp",EDGE,"E945"),sQuery(id+"F0.wireOp",EDGE,"E946"),sQuery(id+"F0.wireOp",EDGE,"E947"),sQuery(id+"F0.wireOp",EDGE,"E948"),sQuery(id+"F0.wireOp",EDGE,"E949"),sQuery(id+"F0.wireOp",EDGE,"E950"),sQuery(id+"F0.wireOp",EDGE,"E951"),sQuery(id+"F0.wireOp",EDGE,"E952"),sQuery(id+"F0.wireOp",EDGE,"E953"),sQuery(id+"F0.wireOp",EDGE,"E954"),sQuery(id+"F0.wireOp",EDGE,"E955"),sQuery(id+"F0.wireOp",EDGE,"E956"),sQuery(id+"F0.wireOp",EDGE,"E957"),sQuery(id+"F0.wireOp",EDGE,"E958"),sQuery(id+"F0.wireOp",EDGE,"E958"),sQuery(id+"F0.wireOp",EDGE,"E959"),sQuery(id+"F0.wireOp",EDGE,"E960"),sQuery(id+"F0.wireOp",EDGE,"E961"),sQuery(id+"F0.wireOp",EDGE,"E962"),sQuery(id+"F0.wireOp",EDGE,"E963"),sQuery(id+"F0.wireOp",EDGE,"E964"),sQuery(id+"F0.wireOp",EDGE,"E965"),sQuery(id+"F0.wireOp",EDGE,"E966"),sQuery(id+"F0.wireOp",EDGE,"E967"),sQuery(id+"F0.wireOp",EDGE,"E968"),sQuery(id+"F0.wireOp",EDGE,"E969"),sQuery(id+"F0.wireOp",EDGE,"E970"),sQuery(id+"F0.wireOp",EDGE,"E971"),sQuery(id+"F0.wireOp",EDGE,"E972"),sQuery(id+"F0.wireOp",EDGE,"E973"),sQuery(id+"F0.wireOp",EDGE,"E973"),sQuery(id+"F0.wireOp",EDGE,"E974"),sQuery(id+"F0.wireOp",EDGE,"E975"),sQuery(id+"F0.wireOp",EDGE,"E976"),sQuery(id+"F0.wireOp",EDGE,"E977"),sQuery(id+"F0.wireOp",EDGE,"E978"),sQuery(id+"F0.wireOp",EDGE,"E979"),sQuery(id+"F0.wireOp",EDGE,"E980"),sQuery(id+"F0.wireOp",EDGE,"E981"),sQuery(id+"F0.wireOp",EDGE,"E982"),sQuery(id+"F0.wireOp",EDGE,"E983"),sQuery(id+"F0.wireOp",EDGE,"E984"),sQuery(id+"F0.wireOp",EDGE,"E985"),sQuery(id+"F0.wireOp",EDGE,"E986"),sQuery(id+"F0.wireOp",EDGE,"E987"),sQuery(id+"F0.wireOp",EDGE,"E988"),sQuery(id+"F0.wireOp",EDGE,"E989"),sQuery(id+"F0.wireOp",EDGE,"E990"),sQuery(id+"F0.wireOp",EDGE,"E991"),sQuery(id+"F0.wireOp",EDGE,"E992"),sQuery(id+"F0.wireOp",EDGE,"E993"),sQuery(id+"F0.wireOp",EDGE,"E994"),sQuery(id+"F0.wireOp",EDGE,"E995"),sQuery(id+"F0.wireOp",EDGE,"E996"),sQuery(id+"F0.wireOp",EDGE,"E997"),sQuery(id+"F0.wireOp",EDGE,"E998"),sQuery(id+"F0.wireOp",EDGE,"E999"),sQuery(id+"F0.wireOp",EDGE,"E1000"),sQuery(id+"F0.wireOp",EDGE,"E1001"),sQuery(id+"F0.wireOp",EDGE,"E1002"),sQuery(id+"F0.wireOp",EDGE,"E1003"),sQuery(id+"F0.wireOp",EDGE,"E1004"),sQuery(id+"F0.wireOp",EDGE,"E1005"),sQuery(id+"F0.wireOp",EDGE,"E1006"),sQuery(id+"F0.wireOp",EDGE,"E1007"),sQuery(id+"F0.wireOp",EDGE,"E1008"),sQuery(id+"F0.wireOp",EDGE,"E1009"),sQuery(id+"F0.wireOp",EDGE,"E1010"),sQuery(id+"F0.wireOp",EDGE,"E1011"),sQuery(id+"F0.wireOp",EDGE,"E1012"),sQuery(id+"F0.wireOp",EDGE,"E1013"),sQuery(id+"F0.wireOp",EDGE,"E1014"),sQuery(id+"F0.wireOp",EDGE,"E1015"),sQuery(id+"F0.wireOp",EDGE,"E1016"),sQuery(id+"F0.wireOp",EDGE,"E1017"),sQuery(id+"F0.wireOp",EDGE,"E1018"),sQuery(id+"F0.wireOp",EDGE,"E1019"),sQuery(id+"F0.wireOp",EDGE,"E1020"),sQuery(id+"F0.wireOp",EDGE,"E1021"),sQuery(id+"F0.wireOp",EDGE,"E1022"),sQuery(id+"F0.wireOp",EDGE,"E1023"),sQuery(id+"F0.wireOp",EDGE,"E1024"),sQuery(id+"F0.wireOp",EDGE,"E1025"),sQuery(id+"F0.wireOp",EDGE,"E1026"),sQuery(id+"F0.wireOp",EDGE,"E1027"),sQuery(id+"F0.wireOp",EDGE,"E1028"),sQuery(id+"F0.wireOp",EDGE,"E1029"),sQuery(id+"F0.wireOp",EDGE,"E1030"),sQuery(id+"F0.wireOp",EDGE,"E1031"),sQuery(id+"F0.wireOp",EDGE,"E1032"),sQuery(id+"F0.wireOp",EDGE,"E1033"),sQuery(id+"F0.wireOp",EDGE,"E1034"),sQuery(id+"F0.wireOp",EDGE,"E1035"),sQuery(id+"F0.wireOp",EDGE,"E1036"),sQuery(id+"F0.wireOp",EDGE,"E1037"),sQuery(id+"F0.wireOp",EDGE,"E1038"),sQuery(id+"F0.wireOp",EDGE,"E1039"),sQuery(id+"F0.wireOp",EDGE,"E1040"),sQuery(id+"F0.wireOp",EDGE,"E1041"),sQuery(id+"F0.wireOp",EDGE,"E1042"),sQuery(id+"F0.wireOp",EDGE,"E1043"),sQuery(id+"F0.wireOp",EDGE,"E1044"),sQuery(id+"F0.wireOp",EDGE,"E1045"),sQuery(id+"F0.wireOp",EDGE,"E1046"),sQuery(id+"F0.wireOp",EDGE,"E1047"),sQuery(id+"F0.wireOp",EDGE,"E1048"),sQuery(id+"F0.wireOp",EDGE,"E1049"),sQuery(id+"F0.wireOp",EDGE,"E1050"),sQuery(id+"F0.wireOp",EDGE,"E1051"),sQuery(id+"F0.wireOp",EDGE,"E1052"),sQuery(id+"F0.wireOp",EDGE,"E1053"),sQuery(id+"F0.wireOp",EDGE,"E1054"),sQuery(id+"F0.wireOp",EDGE,"E1055"),sQuery(id+"F0.wireOp",EDGE,"E1056"),sQuery(id+"F0.wireOp",EDGE,"E1057"),sQuery(id+"F0.wireOp",EDGE,"E1058"),sQuery(id+"F0.wireOp",EDGE,"E1059"),sQuery(id+"F0.wireOp",EDGE,"E1060"),sQuery(id+"F0.wireOp",EDGE,"E1061"),sQuery(id+"F0.wireOp",EDGE,"E1062"),sQuery(id+"F0.wireOp",EDGE,"E1063"),sQuery(id+"F0.wireOp",EDGE,"E1064"),sQuery(id+"F0.wireOp",EDGE,"E1065"),sQuery(id+"F0.wireOp",EDGE,"E1066"),sQuery(id+"F0.wireOp",EDGE,"E1067"),sQuery(id+"F0.wireOp",EDGE,"E1068"),sQuery(id+"F0.wireOp",EDGE,"E1069"),sQuery(id+"F0.wireOp",EDGE,"E1070"),sQuery(id+"F0.wireOp",EDGE,"E1071"),sQuery(id+"F0.wireOp",EDGE,"E1072"),sQuery(id+"F0.wireOp",EDGE,"E1073"),sQuery(id+"F0.wireOp",EDGE,"E1074"),sQuery(id+"F0.wireOp",EDGE,"E1075"),sQuery(id+"F0.wireOp",EDGE,"E1076"),sQuery(id+"F0.wireOp",EDGE,"E1077"),sQuery(id+"F0.wireOp",EDGE,"E1078"),sQuery(id+"F0.wireOp",EDGE,"E1079"),sQuery(id+"F0.wireOp",EDGE,"E1080"),sQuery(id+"F0.wireOp",EDGE,"E1081"),sQuery(id+"F0.wireOp",EDGE,"E1082"),sQuery(id+"F0.wireOp",EDGE,"E1083"),sQuery(id+"F0.wireOp",EDGE,"E1084"),sQuery(id+"F0.wireOp",EDGE,"E1085"),sQuery(id+"F0.wireOp",EDGE,"E1086"),sQuery(id+"F0.wireOp",EDGE,"E1087"),sQuery(id+"F0.wireOp",EDGE,"E1088"),sQuery(id+"F0.wireOp",EDGE,"E1089"),sQuery(id+"F0.wireOp",EDGE,"E1090"),sQuery(id+"F0.wireOp",EDGE,"E1091"),sQuery(id+"F0.wireOp",EDGE,"E1092"),sQuery(id+"F0.wireOp",EDGE,"E1093"),sQuery(id+"F0.wireOp",EDGE,"E1094"),sQuery(id+"F0.wireOp",EDGE,"E1095"),sQuery(id+"F0.wireOp",EDGE,"E1096"),sQuery(id+"F0.wireOp",EDGE,"E1097"),sQuery(id+"F0.wireOp",EDGE,"E1098"),sQuery(id+"F0.wireOp",EDGE,"E1099"),sQuery(id+"F0.wireOp",EDGE,"E1100"),sQuery(id+"F0.wireOp",EDGE,"E1101"),sQuery(id+"F0.wireOp",EDGE,"E1102"),sQuery(id+"F0.wireOp",EDGE,"E1103"),sQuery(id+"F0.wireOp",EDGE,"E1104"),sQuery(id+"F0.wireOp",EDGE,"E1105"),sQuery(id+"F0.wireOp",EDGE,"E1106"),sQuery(id+"F0.wireOp",EDGE,"E1107"),sQuery(id+"F0.wireOp",EDGE,"E1108"),sQuery(id+"F0.wireOp",EDGE,"E1109"),sQuery(id+"F0.wireOp",EDGE,"E1110"),sQuery(id+"F0.wireOp",EDGE,"E1111"),sQuery(id+"F0.wireOp",EDGE,"E1112"),sQuery(id+"F0.wireOp",EDGE,"E1113"),sQuery(id+"F0.wireOp",EDGE,"E1114"),sQuery(id+"F0.wireOp",EDGE,"E1115"),sQuery(id+"F0.wireOp",EDGE,"E1116"),sQuery(id+"F0.wireOp",EDGE,"E1117"),sQuery(id+"F0.wireOp",EDGE,"E1118"),sQuery(id+"F0.wireOp",EDGE,"E1119"),sQuery(id+"F0.wireOp",EDGE,"E1120"),sQuery(id+"F0.wireOp",EDGE,"E1121"),sQuery(id+"F0.wireOp",EDGE,"E1122"),sQuery(id+"F0.wireOp",EDGE,"E1123"),sQuery(id+"F0.wireOp",EDGE,"E1124"),sQuery(id+"F0.wireOp",EDGE,"E1125"),sQuery(id+"F0.wireOp",EDGE,"E1126"),sQuery(id+"F0.wireOp",EDGE,"E1127"),sQuery(id+"F0.wireOp",EDGE,"E1128"),sQuery(id+"F0.wireOp",EDGE,"E1129"),sQuery(id+"F0.wireOp",EDGE,"E1130"),sQuery(id+"F0.wireOp",EDGE,"E1131"),sQuery(id+"F0.wireOp",EDGE,"E1132"),sQuery(id+"F0.wireOp",EDGE,"E1133"),sQuery(id+"F0.wireOp",EDGE,"E1134"),sQuery(id+"F0.wireOp",EDGE,"E1135"),sQuery(id+"F0.wireOp",EDGE,"E1136"),sQuery(id+"F0.wireOp",EDGE,"E1137"),sQuery(id+"F0.wireOp",EDGE,"E1138"),sQuery(id+"F0.wireOp",EDGE,"E1139"),sQuery(id+"F0.wireOp",EDGE,"E1140"),sQuery(id+"F0.wireOp",EDGE,"E1141"),sQuery(id+"F0.wireOp",EDGE,"E1142"),sQuery(id+"F0.wireOp",EDGE,"E1143"),sQuery(id+"F0.wireOp",EDGE,"E1144"),sQuery(id+"F0.wireOp",EDGE,"E1145"),sQuery(id+"F0.wireOp",EDGE,"E1146"),sQuery(id+"F0.wireOp",EDGE,"E1147"),sQuery(id+"F0.wireOp",EDGE,"E1148"),sQuery(id+"F0.wireOp",EDGE,"E1149"),sQuery(id+"F0.wireOp",EDGE,"E1150"),sQuery(id+"F0.wireOp",EDGE,"E1151"),sQuery(id+"F0.wireOp",EDGE,"E1152"),sQuery(id+"F0.wireOp",EDGE,"E1153"),sQuery(id+"F0.wireOp",EDGE,"E1154"),sQuery(id+"F0.wireOp",EDGE,"E1155"),sQuery(id+"F0.wireOp",EDGE,"E1156"),sQuery(id+"F0.wireOp",EDGE,"E1157"),sQuery(id+"F0.wireOp",EDGE,"E1158"),sQuery(id+"F0.wireOp",EDGE,"E1159"),sQuery(id+"F0.wireOp",EDGE,"E1160"),sQuery(id+"F0.wireOp",EDGE,"E1161"),sQuery(id+"F0.wireOp",EDGE,"E1162"),sQuery(id+"F0.wireOp",EDGE,"E1163"),sQuery(id+"F0.wireOp",EDGE,"E1164"),sQuery(id+"F0.wireOp",EDGE,"E1165"),sQuery(id+"F0.wireOp",EDGE,"E1166"),sQuery(id+"F0.wireOp",EDGE,"E1167"),sQuery(id+"F0.wireOp",EDGE,"E1168"),sQuery(id+"F0.wireOp",EDGE,"E1169"),sQuery(id+"F0.wireOp",EDGE,"E1170"),sQuery(id+"F0.wireOp",EDGE,"E1171"),sQuery(id+"F0.wireOp",EDGE,"E1172"),sQuery(id+"F0.wireOp",EDGE,"E1173"),sQuery(id+"F0.wireOp",EDGE,"E1174"),sQuery(id+"F0.wireOp",EDGE,"E1175"),sQuery(id+"F0.wireOp",EDGE,"E1176"),sQuery(id+"F0.wireOp",EDGE,"E1177"),sQuery(id+"F0.wireOp",EDGE,"E1178"),sQuery(id+"F0.wireOp",EDGE,"E1179"),sQuery(id+"F0.wireOp",EDGE,"E1180"),sQuery(id+"F0.wireOp",EDGE,"E1181"),sQuery(id+"F0.wireOp",EDGE,"E1182"),sQuery(id+"F0.wireOp",EDGE,"E1183"),sQuery(id+"F0.wireOp",EDGE,"E1184"),sQuery(id+"F0.wireOp",EDGE,"E1185"),sQuery(id+"F0.wireOp",EDGE,"E1186"),sQuery(id+"F0.wireOp",EDGE,"E1187"),sQuery(id+"F0.wireOp",EDGE,"E1188"),sQuery(id+"F0.wireOp",EDGE,"E1189"),sQuery(id+"F0.wireOp",EDGE,"E1190"),sQuery(id+"F0.wireOp",EDGE,"E1191"),sQuery(id+"F0.wireOp",EDGE,"E1192"),sQuery(id+"F0.wireOp",EDGE,"E1193"),sQuery(id+"F0.wireOp",EDGE,"E1194"),sQuery(id+"F0.wireOp",EDGE,"E1195"),sQuery(id+"F0.wireOp",EDGE,"E1196"),sQuery(id+"F0.wireOp",EDGE,"E1197"),sQuery(id+"F0.wireOp",EDGE,"E1198"),sQuery(id+"F0.wireOp",EDGE,"E1199"),sQuery(id+"F0.wireOp",EDGE,"E1200"),sQuery(id+"F0.wireOp",EDGE,"E1201"),sQuery(id+"F0.wireOp",EDGE,"E1202"),sQuery(id+"F0.wireOp",EDGE,"E1203"),sQuery(id+"F0.wireOp",EDGE,"E1204"),sQuery(id+"F0.wireOp",EDGE,"E1205"),sQuery(id+"F0.wireOp",EDGE,"E1206"),sQuery(id+"F0.wireOp",EDGE,"E1207"),sQuery(id+"F0.wireOp",EDGE,"E1208"),sQuery(id+"F0.wireOp",EDGE,"E1209"),sQuery(id+"F0.wireOp",EDGE,"E1210"),sQuery(id+"F0.wireOp",EDGE,"E1211"),sQuery(id+"F0.wireOp",EDGE,"E1212"),sQuery(id+"F0.wireOp",EDGE,"E1213"),sQuery(id+"F0.wireOp",EDGE,"E1214"),sQuery(id+"F0.wireOp",EDGE,"E1215"),sQuery(id+"F0.wireOp",EDGE,"E1216"),sQuery(id+"F0.wireOp",EDGE,"E1217"),sQuery(id+"F0.wireOp",EDGE,"E1218"),sQuery(id+"F0.wireOp",EDGE,"E1219"),sQuery(id+"F0.wireOp",EDGE,"E1220"),sQuery(id+"F0.wireOp",EDGE,"E1221"),sQuery(id+"F0.wireOp",EDGE,"E1222"),sQuery(id+"F0.wireOp",EDGE,"E1223"),sQuery(id+"F0.wireOp",EDGE,"E1224"),sQuery(id+"F0.wireOp",EDGE,"E1225"),sQuery(id+"F0.wireOp",EDGE,"E1226"),sQuery(id+"F0.wireOp",EDGE,"E1227"),sQuery(id+"F0.wireOp",EDGE,"E1228"),sQuery(id+"F0.wireOp",EDGE,"E1229"),sQuery(id+"F0.wireOp",EDGE,"E1230"),sQuery(id+"F0.wireOp",EDGE,"E1231"),sQuery(id+"F0.wireOp",EDGE,"E1232"),sQuery(id+"F0.wireOp",EDGE,"E1233"),sQuery(id+"F0.wireOp",EDGE,"E1234"),sQuery(id+"F0.wireOp",EDGE,"E1235"),sQuery(id+"F0.wireOp",EDGE,"E1236"),sQuery(id+"F0.wireOp",EDGE,"E1237"),sQuery(id+"F0.wireOp",EDGE,"E1238"),sQuery(id+"F0.wireOp",EDGE,"E1239"),sQuery(id+"F0.wireOp",EDGE,"E1240"),sQuery(id+"F0.wireOp",EDGE,"E1241"),sQuery(id+"F0.wireOp",EDGE,"E1242"),sQuery(id+"F0.wireOp",EDGE,"E1243"),sQuery(id+"F0.wireOp",EDGE,"E1244"),sQuery(id+"F0.wireOp",EDGE,"E1245"),sQuery(id+"F0.wireOp",EDGE,"E1246"),sQuery(id+"F0.wireOp",EDGE,"E1247"),sQuery(id+"F0.wireOp",EDGE,"E1248"),sQuery(id+"F0.wireOp",EDGE,"E1249"),sQuery(id+"F0.wireOp",EDGE,"E1250"),sQuery(id+"F0.wireOp",EDGE,"E1251"),sQuery(id+"F0.wireOp",EDGE,"E1252"),sQuery(id+"F0.wireOp",EDGE,"E1253"),sQuery(id+"F0.wireOp",EDGE,"E1254"),sQuery(id+"F0.wireOp",EDGE,"E1255"),sQuery(id+"F0.wireOp",EDGE,"E1256"),sQuery(id+"F0.wireOp",EDGE,"E1257"),sQuery(id+"F0.wireOp",EDGE,"E1258"),sQuery(id+"F0.wireOp",EDGE,"E1259"),sQuery(id+"F0.wireOp",EDGE,"E1260"),sQuery(id+"F0.wireOp",EDGE,"E1261"),sQuery(id+"F0.wireOp",EDGE,"E1262"),sQuery(id+"F0.wireOp",EDGE,"E1263"),sQuery(id+"F0.wireOp",EDGE,"E1264"),sQuery(id+"F0.wireOp",EDGE,"E1265"),sQuery(id+"F0.wireOp",EDGE,"E1266"),sQuery(id+"F0.wireOp",EDGE,"E1267"),sQuery(id+"F0.wireOp",EDGE,"E1268"),sQuery(id+"F0.wireOp",EDGE,"E1269"),sQuery(id+"F0.wireOp",EDGE,"E1270"),sQuery(id+"F0.wireOp",EDGE,"E1271"),sQuery(id+"F0.wireOp",EDGE,"E1272"),sQuery(id+"F0.wireOp",EDGE,"E1273"),sQuery(id+"F0.wireOp",EDGE,"E1274"),sQuery(id+"F0.wireOp",EDGE,"E1275"),sQuery(id+"F0.wireOp",EDGE,"E1276"),sQuery(id+"F0.wireOp",EDGE,"E1277"),sQuery(id+"F0.wireOp",EDGE,"E1278"),sQuery(id+"F0.wireOp",EDGE,"E1279"),sQuery(id+"F0.wireOp",EDGE,"E1280"),sQuery(id+"F0.wireOp",EDGE,"E1281"),sQuery(id+"F0.wireOp",EDGE,"E1282"),sQuery(id+"F0.wireOp",EDGE,"E1283"),sQuery(id+"F0.wireOp",EDGE,"E1284"),sQuery(id+"F0.wireOp",EDGE,"E1285"),sQuery(id+"F0.wireOp",EDGE,"E1286"),sQuery(id+"F0.wireOp",EDGE,"E1287"),sQuery(id+"F0.wireOp",EDGE,"E1288"),sQuery(id+"F0.wireOp",EDGE,"E1289"),sQuery(id+"F0.wireOp",EDGE,"E1290"),sQuery(id+"F0.wireOp",EDGE,"E1291"),sQuery(id+"F0.wireOp",EDGE,"E1292"),sQuery(id+"F0.wireOp",EDGE,"E1293"),sQuery(id+"F0.wireOp",EDGE,"E1294"),sQuery(id+"F0.wireOp",EDGE,"E1295"),sQuery(id+"F0.wireOp",EDGE,"E1296"),sQuery(id+"F0.wireOp",EDGE,"E1297"),sQuery(id+"F0.wireOp",EDGE,"E1297"),sQuery(id+"F0.wireOp",EDGE,"E1297"),sQuery(id+"F0.wireOp",EDGE,"E1298"),sQuery(id+"F0.wireOp",EDGE,"E1299"),sQuery(id+"F0.wireOp",EDGE,"E1300"),sQuery(id+"F0.wireOp",EDGE,"E1300"),sQuery(id+"F0.wireOp",EDGE,"E1301"),sQuery(id+"F0.wireOp",EDGE,"E1302"),sQuery(id+"F0.wireOp",EDGE,"E1303"),sQuery(id+"F0.wireOp",EDGE,"E1304"),sQuery(id+"F0.wireOp",EDGE,"E1305"),sQuery(id+"F0.wireOp",EDGE,"E1306"),sQuery(id+"F0.wireOp",EDGE,"E1307"),sQuery(id+"F0.wireOp",EDGE,"E1308"),sQuery(id+"F0.wireOp",EDGE,"E1309"),sQuery(id+"F0.wireOp",EDGE,"E1310"),sQuery(id+"F0.wireOp",EDGE,"E1311"),sQuery(id+"F0.wireOp",EDGE,"E1312"),sQuery(id+"F0.wireOp",EDGE,"E1313"),sQuery(id+"F0.wireOp",EDGE,"E1314"),sQuery(id+"F0.wireOp",EDGE,"E1314"),sQuery(id+"F0.wireOp",EDGE,"E1315"),sQuery(id+"F0.wireOp",EDGE,"E1316"),sQuery(id+"F0.wireOp",EDGE,"E1317"),sQuery(id+"F0.wireOp",EDGE,"E1318"),sQuery(id+"F0.wireOp",EDGE,"E1319"),sQuery(id+"F0.wireOp",EDGE,"E1319"),sQuery(id+"F0.wireOp",EDGE,"E1320"),sQuery(id+"F0.wireOp",EDGE,"E1321"),sQuery(id+"F0.wireOp",EDGE,"E1322"),sQuery(id+"F0.wireOp",EDGE,"E1323"),sQuery(id+"F0.wireOp",EDGE,"E1324"),sQuery(id+"F0.wireOp",EDGE,"E1325"),sQuery(id+"F0.wireOp",EDGE,"E1326"),sQuery(id+"F0.wireOp",EDGE,"E1327"),sQuery(id+"F0.wireOp",EDGE,"E1328"),sQuery(id+"F0.wireOp",EDGE,"E1329"),sQuery(id+"F0.wireOp",EDGE,"E1330"),sQuery(id+"F0.wireOp",EDGE,"E1331"),sQuery(id+"F0.wireOp",EDGE,"E1332"),sQuery(id+"F0.wireOp",EDGE,"E1333"),sQuery(id+"F0.wireOp",EDGE,"E1334"),sQuery(id+"F0.wireOp",EDGE,"E1334"),sQuery(id+"F0.wireOp",EDGE,"E1335"),sQuery(id+"F0.wireOp",EDGE,"E1336"),sQuery(id+"F0.wireOp",EDGE,"E1337"),sQuery(id+"F0.wireOp",EDGE,"E1338"),sQuery(id+"F0.wireOp",EDGE,"E1339"),sQuery(id+"F0.wireOp",EDGE,"E1340"),sQuery(id+"F0.wireOp",EDGE,"E1341"),sQuery(id+"F0.wireOp",EDGE,"E1342"),sQuery(id+"F0.wireOp",EDGE,"E1343"),sQuery(id+"F0.wireOp",EDGE,"E1344"),sQuery(id+"F0.wireOp",EDGE,"E1345"),sQuery(id+"F0.wireOp",EDGE,"E1346"),sQuery(id+"F0.wireOp",EDGE,"E1347"),sQuery(id+"F0.wireOp",EDGE,"E1348"),sQuery(id+"F0.wireOp",EDGE,"E1349"),sQuery(id+"F0.wireOp",EDGE,"E1350"),sQuery(id+"F0.wireOp",EDGE,"E1351"),sQuery(id+"F0.wireOp",EDGE,"E1352"),sQuery(id+"F0.wireOp",EDGE,"E1353"),sQuery(id+"F0.wireOp",EDGE,"E1354"),sQuery(id+"F0.wireOp",EDGE,"E1354"),sQuery(id+"F0.wireOp",EDGE,"E1355"),sQuery(id+"F0.wireOp",EDGE,"E1356"),sQuery(id+"F0.wireOp",EDGE,"E1357"),sQuery(id+"F0.wireOp",EDGE,"E1358"),sQuery(id+"F0.wireOp",EDGE,"E1359"),sQuery(id+"F0.wireOp",EDGE,"E1360"),sQuery(id+"F0.wireOp",EDGE,"E1361"),sQuery(id+"F0.wireOp",EDGE,"E1362"),sQuery(id+"F0.wireOp",EDGE,"E1363"),sQuery(id+"F0.wireOp",EDGE,"E1364"),sQuery(id+"F0.wireOp",EDGE,"E1365"),sQuery(id+"F0.wireOp",EDGE,"E1366"),sQuery(id+"F0.wireOp",EDGE,"E1367"),sQuery(id+"F0.wireOp",EDGE,"E1368"),sQuery(id+"F0.wireOp",EDGE,"E1369"),sQuery(id+"F0.wireOp",EDGE,"E1370"),sQuery(id+"F0.wireOp",EDGE,"E1371"),sQuery(id+"F0.wireOp",EDGE,"E1372"),sQuery(id+"F0.wireOp",EDGE,"E1373"),sQuery(id+"F0.wireOp",EDGE,"E1374"),sQuery(id+"F0.wireOp",EDGE,"E1375"),sQuery(id+"F0.wireOp",EDGE,"E1376"),sQuery(id+"F0.wireOp",EDGE,"E1377"),sQuery(id+"F0.wireOp",EDGE,"E1378"),sQuery(id+"F0.wireOp",EDGE,"E1379"),sQuery(id+"F0.wireOp",EDGE,"E1380"),sQuery(id+"F0.wireOp",EDGE,"E1381"),sQuery(id+"F0.wireOp",EDGE,"E1382"),sQuery(id+"F0.wireOp",EDGE,"E1383"),sQuery(id+"F0.wireOp",EDGE,"E1384"),sQuery(id+"F0.wireOp",EDGE,"E1385"),sQuery(id+"F0.wireOp",EDGE,"E1386"),sQuery(id+"F0.wireOp",EDGE,"E1387"),sQuery(id+"F0.wireOp",EDGE,"E1388"),sQuery(id+"F0.wireOp",EDGE,"E1389"),sQuery(id+"F0.wireOp",EDGE,"E1390"),sQuery(id+"F0.wireOp",EDGE,"E1391"),sQuery(id+"F0.wireOp",EDGE,"E1392"),sQuery(id+"F0.wireOp",EDGE,"E1393"),sQuery(id+"F0.wireOp",EDGE,"E1394"),sQuery(id+"F0.wireOp",EDGE,"E1395"),sQuery(id+"F0.wireOp",EDGE,"E1396"),sQuery(id+"F0.wireOp",EDGE,"E1397"),sQuery(id+"F0.wireOp",EDGE,"E1398"),sQuery(id+"F0.wireOp",EDGE,"E1399"),sQuery(id+"F0.wireOp",EDGE,"E1400"),sQuery(id+"F0.wireOp",EDGE,"E1401"),sQuery(id+"F0.wireOp",EDGE,"E1402"),sQuery(id+"F0.wireOp",EDGE,"E1403"),sQuery(id+"F0.wireOp",EDGE,"E1404"),sQuery(id+"F0.wireOp",EDGE,"E1405"),sQuery(id+"F0.wireOp",EDGE,"E1406"),sQuery(id+"F0.wireOp",EDGE,"E1407"),sQuery(id+"F0.wireOp",EDGE,"E1408"),sQuery(id+"F0.wireOp",EDGE,"E1409"),sQuery(id+"F0.wireOp",EDGE,"E1410"),sQuery(id+"F0.wireOp",EDGE,"E1411"),sQuery(id+"F0.wireOp",EDGE,"E1412"),sQuery(id+"F0.wireOp",EDGE,"E1413"),sQuery(id+"F0.wireOp",EDGE,"E1414"),sQuery(id+"F0.wireOp",EDGE,"E1415"),sQuery(id+"F0.wireOp",EDGE,"E1416"),sQuery(id+"F0.wireOp",EDGE,"E1417"),sQuery(id+"F0.wireOp",EDGE,"E1418"),sQuery(id+"F0.wireOp",EDGE,"E1419"),sQuery(id+"F0.wireOp",EDGE,"E1420"),sQuery(id+"F0.wireOp",EDGE,"E1421"),sQuery(id+"F0.wireOp",EDGE,"E1422"),sQuery(id+"F0.wireOp",EDGE,"E1423"),sQuery(id+"F0.wireOp",EDGE,"E1424"),sQuery(id+"F0.wireOp",EDGE,"E1425"),sQuery(id+"F0.wireOp",EDGE,"E1426"),sQuery(id+"F0.wireOp",EDGE,"E1427"),sQuery(id+"F0.wireOp",EDGE,"E1428"),sQuery(id+"F0.wireOp",EDGE,"E1429"),sQuery(id+"F0.wireOp",EDGE,"E1430"),sQuery(id+"F0.wireOp",EDGE,"E1431"),sQuery(id+"F0.wireOp",EDGE,"E1432"),sQuery(id+"F0.wireOp",EDGE,"E1433"),sQuery(id+"F0.wireOp",EDGE,"E1434"),sQuery(id+"F0.wireOp",EDGE,"E1435"),sQuery(id+"F0.wireOp",EDGE,"E1436"),sQuery(id+"F0.wireOp",EDGE,"E1437"),sQuery(id+"F0.wireOp",EDGE,"E1438"),sQuery(id+"F0.wireOp",EDGE,"E1439"),sQuery(id+"F0.wireOp",EDGE,"E1440"),sQuery(id+"F0.wireOp",EDGE,"E1441"),sQuery(id+"F0.wireOp",EDGE,"E1442"),sQuery(id+"F0.wireOp",EDGE,"E1443"),sQuery(id+"F0.wireOp",EDGE,"E1444"),sQuery(id+"F0.wireOp",EDGE,"E1445"),sQuery(id+"F0.wireOp",EDGE,"E1446"),sQuery(id+"F0.wireOp",EDGE,"E1447"),sQuery(id+"F0.wireOp",EDGE,"E1448"),sQuery(id+"F0.wireOp",EDGE,"E1449"),sQuery(id+"F0.wireOp",EDGE,"E1450"),sQuery(id+"F0.wireOp",EDGE,"E1451"),sQuery(id+"F0.wireOp",EDGE,"E1452"),sQuery(id+"F0.wireOp",EDGE,"E1453"),sQuery(id+"F0.wireOp",EDGE,"E1454"),sQuery(id+"F0.wireOp",EDGE,"E1455"),sQuery(id+"F0.wireOp",EDGE,"E1456"),sQuery(id+"F0.wireOp",EDGE,"E1457"),sQuery(id+"F0.wireOp",EDGE,"E1458"),sQuery(id+"F0.wireOp",EDGE,"E1459"),sQuery(id+"F0.wireOp",EDGE,"E1460"),sQuery(id+"F0.wireOp",EDGE,"E1461"),sQuery(id+"F0.wireOp",EDGE,"E1462"),sQuery(id+"F0.wireOp",EDGE,"E1463"),sQuery(id+"F0.wireOp",EDGE,"E1464"),sQuery(id+"F0.wireOp",EDGE,"E1465"),sQuery(id+"F0.wireOp",EDGE,"E1466"),sQuery(id+"F0.wireOp",EDGE,"E1467"),sQuery(id+"F0.wireOp",EDGE,"E1468"),sQuery(id+"F0.wireOp",EDGE,"E1469"),sQuery(id+"F0.wireOp",EDGE,"E1470"),sQuery(id+"F0.wireOp",EDGE,"E1471"),sQuery(id+"F0.wireOp",EDGE,"E1472"),sQuery(id+"F0.wireOp",EDGE,"E1473"),sQuery(id+"F0.wireOp",EDGE,"E1474"),sQuery(id+"F0.wireOp",EDGE,"E1475"),sQuery(id+"F0.wireOp",EDGE,"E1476"),sQuery(id+"F0.wireOp",EDGE,"E1477"),sQuery(id+"F0.wireOp",EDGE,"E1478"),sQuery(id+"F0.wireOp",EDGE,"E1479"),sQuery(id+"F0.wireOp",EDGE,"E1480"),sQuery(id+"F0.wireOp",EDGE,"E1481"),sQuery(id+"F0.wireOp",EDGE,"E1482"),sQuery(id+"F0.wireOp",EDGE,"E1483"),sQuery(id+"F0.wireOp",EDGE,"E1484"),sQuery(id+"F0.wireOp",EDGE,"E1485"),sQuery(id+"F0.wireOp",EDGE,"E1486"),sQuery(id+"F0.wireOp",EDGE,"E1487"),sQuery(id+"F0.wireOp",EDGE,"E1488"),sQuery(id+"F0.wireOp",EDGE,"E1489"),sQuery(id+"F0.wireOp",EDGE,"E1490"),sQuery(id+"F0.wireOp",EDGE,"E1491"),sQuery(id+"F0.wireOp",EDGE,"E1492"),sQuery(id+"F0.wireOp",EDGE,"E1493"),sQuery(id+"F0.wireOp",EDGE,"E1494"),sQuery(id+"F0.wireOp",EDGE,"E1495"),sQuery(id+"F0.wireOp",EDGE,"E1496"),sQuery(id+"F0.wireOp",EDGE,"E1497"),sQuery(id+"F0.wireOp",EDGE,"E1498"),sQuery(id+"F0.wireOp",EDGE,"E1499"),sQuery(id+"F0.wireOp",EDGE,"E1500"),sQuery(id+"F0.wireOp",EDGE,"E1501"),sQuery(id+"F0.wireOp",EDGE,"E1502"),sQuery(id+"F0.wireOp",EDGE,"E1503"),sQuery(id+"F0.wireOp",EDGE,"E1504"),sQuery(id+"F0.wireOp",EDGE,"E1505"),sQuery(id+"F0.wireOp",EDGE,"E1506"),sQuery(id+"F0.wireOp",EDGE,"E1507"),sQuery(id+"F0.wireOp",EDGE,"E1508"),sQuery(id+"F0.wireOp",EDGE,"E1509"),sQuery(id+"F0.wireOp",EDGE,"E1510"),sQuery(id+"F0.wireOp",EDGE,"E1511"),sQuery(id+"F0.wireOp",EDGE,"E1512"),sQuery(id+"F0.wireOp",EDGE,"E1513"),sQuery(id+"F0.wireOp",EDGE,"E1514"),sQuery(id+"F0.wireOp",EDGE,"E1515"),sQuery(id+"F0.wireOp",EDGE,"E1516"),sQuery(id+"F0.wireOp",EDGE,"E1517"),sQuery(id+"F0.wireOp",EDGE,"E1518"),sQuery(id+"F0.wireOp",EDGE,"E1519"),sQuery(id+"F0.wireOp",EDGE,"E1520"),sQuery(id+"F0.wireOp",EDGE,"E1521"),sQuery(id+"F0.wireOp",EDGE,"E1522"),sQuery(id+"F0.wireOp",EDGE,"E1523"),sQuery(id+"F0.wireOp",EDGE,"E1524"),sQuery(id+"F0.wireOp",EDGE,"E1525"),sQuery(id+"F0.wireOp",EDGE,"E1526"),sQuery(id+"F0.wireOp",EDGE,"E1527"),sQuery(id+"F0.wireOp",EDGE,"E1528"),sQuery(id+"F0.wireOp",EDGE,"E1529"),sQuery(id+"F0.wireOp",EDGE,"E1530"),sQuery(id+"F0.wireOp",EDGE,"E1531"),sQuery(id+"F0.wireOp",EDGE,"E1532"),sQuery(id+"F0.wireOp",EDGE,"E1533"),sQuery(id+"F0.wireOp",EDGE,"E1534"),sQuery(id+"F0.wireOp",EDGE,"E1535"),sQuery(id+"F0.wireOp",EDGE,"E1536"),sQuery(id+"F0.wireOp",EDGE,"E1537"),sQuery(id+"F0.wireOp",EDGE,"E1538"),sQuery(id+"F0.wireOp",EDGE,"E1539"),sQuery(id+"F0.wireOp",EDGE,"E1540"),sQuery(id+"F0.wireOp",EDGE,"E1541"),sQuery(id+"F0.wireOp",EDGE,"E1542"),sQuery(id+"F0.wireOp",EDGE,"E1543"),sQuery(id+"F0.wireOp",EDGE,"E1544"),sQuery(id+"F0.wireOp",EDGE,"E1545"),sQuery(id+"F0.wireOp",EDGE,"E1546"),sQuery(id+"F0.wireOp",EDGE,"E1547"),sQuery(id+"F0.wireOp",EDGE,"E1548"),sQuery(id+"F0.wireOp",EDGE,"E1549"),sQuery(id+"F0.wireOp",EDGE,"E1550"),sQuery(id+"F0.wireOp",EDGE,"E1551"),sQuery(id+"F0.wireOp",EDGE,"E1552"),sQuery(id+"F0.wireOp",EDGE,"E1553"),sQuery(id+"F0.wireOp",EDGE,"E1554"),sQuery(id+"F0.wireOp",EDGE,"E1555"),sQuery(id+"F0.wireOp",EDGE,"E1556"),sQuery(id+"F0.wireOp",EDGE,"E1557"),sQuery(id+"F0.wireOp",EDGE,"E1558"),sQuery(id+"F0.wireOp",EDGE,"E1559"),sQuery(id+"F0.wireOp",EDGE,"E1560"),sQuery(id+"F0.wireOp",EDGE,"E1561"),sQuery(id+"F0.wireOp",EDGE,"E1562"),sQuery(id+"F0.wireOp",EDGE,"E1563"),sQuery(id+"F0.wireOp",EDGE,"E1564"),sQuery(id+"F0.wireOp",EDGE,"E1565"),sQuery(id+"F0.wireOp",EDGE,"E1566"),sQuery(id+"F0.wireOp",EDGE,"E1567"),sQuery(id+"F0.wireOp",EDGE,"E1568"),sQuery(id+"F0.wireOp",EDGE,"E1569"),sQuery(id+"F0.wireOp",EDGE,"E1570"),sQuery(id+"F0.wireOp",EDGE,"E1571"),sQuery(id+"F0.wireOp",EDGE,"E1572"),sQuery(id+"F0.wireOp",EDGE,"E1573"),sQuery(id+"F0.wireOp",EDGE,"E1574"),sQuery(id+"F0.wireOp",EDGE,"E1575"),sQuery(id+"F0.wireOp",EDGE,"E1576"),sQuery(id+"F0.wireOp",EDGE,"E1577"),sQuery(id+"F0.wireOp",EDGE,"E1578"),sQuery(id+"F0.wireOp",EDGE,"E1579"),sQuery(id+"F0.wireOp",EDGE,"E1580"),sQuery(id+"F0.wireOp",EDGE,"E1581"),sQuery(id+"F0.wireOp",EDGE,"E1582"),sQuery(id+"F0.wireOp",EDGE,"E1583"),sQuery(id+"F0.wireOp",EDGE,"E1584"),sQuery(id+"F0.wireOp",EDGE,"E1585"),sQuery(id+"F0.wireOp",EDGE,"E1586"),sQuery(id+"F0.wireOp",EDGE,"E1587"),sQuery(id+"F0.wireOp",EDGE,"E1588"),sQuery(id+"F0.wireOp",EDGE,"E1589"),sQuery(id+"F0.wireOp",EDGE,"E1590"),sQuery(id+"F0.wireOp",EDGE,"E1591"),sQuery(id+"F0.wireOp",EDGE,"E1592"),sQuery(id+"F0.wireOp",EDGE,"E1593"),sQuery(id+"F0.wireOp",EDGE,"E1594"),sQuery(id+"F0.wireOp",EDGE,"E1595"),sQuery(id+"F0.wireOp",EDGE,"E1595"),sQuery(id+"F0.wireOp",EDGE,"E1596"),sQuery(id+"F0.wireOp",EDGE,"E1597"),sQuery(id+"F0.wireOp",EDGE,"E1598"),sQuery(id+"F0.wireOp",EDGE,"E1599"),sQuery(id+"F0.wireOp",EDGE,"E1600"),sQuery(id+"F0.wireOp",EDGE,"E1601"),sQuery(id+"F0.wireOp",EDGE,"E1602"),sQuery(id+"F0.wireOp",EDGE,"E1603"),sQuery(id+"F0.wireOp",EDGE,"E1604"),sQuery(id+"F0.wireOp",EDGE,"E1605"),sQuery(id+"F0.wireOp",EDGE,"E1606"),sQuery(id+"F0.wireOp",EDGE,"E1607"),sQuery(id+"F0.wireOp",EDGE,"E1608"),sQuery(id+"F0.wireOp",EDGE,"E1609"),sQuery(id+"F0.wireOp",EDGE,"E1610"),sQuery(id+"F0.wireOp",EDGE,"E1610"),sQuery(id+"F0.wireOp",EDGE,"E1611"),sQuery(id+"F0.wireOp",EDGE,"E1612"),sQuery(id+"F0.wireOp",EDGE,"E1613"),sQuery(id+"F0.wireOp",EDGE,"E1614"),sQuery(id+"F0.wireOp",EDGE,"E1615"),sQuery(id+"F0.wireOp",EDGE,"E1616"),sQuery(id+"F0.wireOp",EDGE,"E1617"),sQuery(id+"F0.wireOp",EDGE,"E1618"),sQuery(id+"F0.wireOp",EDGE,"E1619"),sQuery(id+"F0.wireOp",EDGE,"E1620"),sQuery(id+"F0.wireOp",EDGE,"E1621"),sQuery(id+"F0.wireOp",EDGE,"E1622"),sQuery(id+"F0.wireOp",EDGE,"E1623"),sQuery(id+"F0.wireOp",EDGE,"E1624"),sQuery(id+"F0.wireOp",EDGE,"E1625"),sQuery(id+"F0.wireOp",EDGE,"E1625"),sQuery(id+"F0.wireOp",EDGE,"E1626"),sQuery(id+"F0.wireOp",EDGE,"E1627"),sQuery(id+"F0.wireOp",EDGE,"E1628"),sQuery(id+"F0.wireOp",EDGE,"E1629"),sQuery(id+"F0.wireOp",EDGE,"E1630"),sQuery(id+"F0.wireOp",EDGE,"E1631"),sQuery(id+"F0.wireOp",EDGE,"E1632"),sQuery(id+"F0.wireOp",EDGE,"E1633"),sQuery(id+"F0.wireOp",EDGE,"E1634"),sQuery(id+"F0.wireOp",EDGE,"E1635"),sQuery(id+"F0.wireOp",EDGE,"E1636"),sQuery(id+"F0.wireOp",EDGE,"E1637"),sQuery(id+"F0.wireOp",EDGE,"E1637"),sQuery(id+"F0.wireOp",EDGE,"E1638"),sQuery(id+"F0.wireOp",EDGE,"E1639"),sQuery(id+"F0.wireOp",EDGE,"E1640"),sQuery(id+"F0.wireOp",EDGE,"E1641"),sQuery(id+"F0.wireOp",EDGE,"E1642"),sQuery(id+"F0.wireOp",EDGE,"E1643"),sQuery(id+"F0.wireOp",EDGE,"E1644"),sQuery(id+"F0.wireOp",EDGE,"E1645"),sQuery(id+"F0.wireOp",EDGE,"E1646"),sQuery(id+"F0.wireOp",EDGE,"E1647"),sQuery(id+"F0.wireOp",EDGE,"E1648"),sQuery(id+"F0.wireOp",EDGE,"E1649"),sQuery(id+"F0.wireOp",EDGE,"E1650"),sQuery(id+"F0.wireOp",EDGE,"E1651"),sQuery(id+"F0.wireOp",EDGE,"E1652"),sQuery(id+"F0.wireOp",EDGE,"E1653"),sQuery(id+"F0.wireOp",EDGE,"E1654"),sQuery(id+"F0.wireOp",EDGE,"E1655"),sQuery(id+"F0.wireOp",EDGE,"E1656"),sQuery(id+"F0.wireOp",EDGE,"E1657"),sQuery(id+"F0.wireOp",EDGE,"E1658"),sQuery(id+"F0.wireOp",EDGE,"E1658"),sQuery(id+"F0.wireOp",EDGE,"E1659"),sQuery(id+"F0.wireOp",EDGE,"E1660"),sQuery(id+"F0.wireOp",EDGE,"E1661"),sQuery(id+"F0.wireOp",EDGE,"E1662"),sQuery(id+"F0.wireOp",EDGE,"E1663"),sQuery(id+"F0.wireOp",EDGE,"E1664"),sQuery(id+"F0.wireOp",EDGE,"E1665"),sQuery(id+"F0.wireOp",EDGE,"E1666"),sQuery(id+"F0.wireOp",EDGE,"E1667"),sQuery(id+"F0.wireOp",EDGE,"E1668"),sQuery(id+"F0.wireOp",EDGE,"E1669"),sQuery(id+"F0.wireOp",EDGE,"E1670"),sQuery(id+"F0.wireOp",EDGE,"E1671"),sQuery(id+"F0.wireOp",EDGE,"E1672"),sQuery(id+"F0.wireOp",EDGE,"E1673"),sQuery(id+"F0.wireOp",EDGE,"E1674"),sQuery(id+"F0.wireOp",EDGE,"E1675"),sQuery(id+"F0.wireOp",EDGE,"E1676"),sQuery(id+"F0.wireOp",EDGE,"E1677"),sQuery(id+"F0.wireOp",EDGE,"E1678"),sQuery(id+"F0.wireOp",EDGE,"E1679"),sQuery(id+"F0.wireOp",EDGE,"E1680"),sQuery(id+"F0.wireOp",EDGE,"E1681"),sQuery(id+"F0.wireOp",EDGE,"E1682"),sQuery(id+"F0.wireOp",EDGE,"E1683"),sQuery(id+"F0.wireOp",EDGE,"E1684"),sQuery(id+"F0.wireOp",EDGE,"E1685"),sQuery(id+"F0.wireOp",EDGE,"E1686"),sQuery(id+"F0.wireOp",EDGE,"E1687"),sQuery(id+"F0.wireOp",EDGE,"E1688"),sQuery(id+"F0.wireOp",EDGE,"E1689"),sQuery(id+"F0.wireOp",EDGE,"E1690"),sQuery(id+"F0.wireOp",EDGE,"E1691"),sQuery(id+"F0.wireOp",EDGE,"E1692"),sQuery(id+"F0.wireOp",EDGE,"E1693"),sQuery(id+"F0.wireOp",EDGE,"E1694"),sQuery(id+"F0.wireOp",EDGE,"E1695"),sQuery(id+"F0.wireOp",EDGE,"E1696"),sQuery(id+"F0.wireOp",EDGE,"E1697"),sQuery(id+"F0.wireOp",EDGE,"E1698"),sQuery(id+"F0.wireOp",EDGE,"E1699"),sQuery(id+"F0.wireOp",EDGE,"E1700"),sQuery(id+"F0.wireOp",EDGE,"E1701"),sQuery(id+"F0.wireOp",EDGE,"E1702"),sQuery(id+"F0.wireOp",EDGE,"E1703"),sQuery(id+"F0.wireOp",EDGE,"E1704"),sQuery(id+"F0.wireOp",EDGE,"E1705"),sQuery(id+"F0.wireOp",EDGE,"E1706"),sQuery(id+"F0.wireOp",EDGE,"E1707"),sQuery(id+"F0.wireOp",EDGE,"E1708"),sQuery(id+"F0.wireOp",EDGE,"E1709"),sQuery(id+"F0.wireOp",EDGE,"E1710"),sQuery(id+"F0.wireOp",EDGE,"E1711"),sQuery(id+"F0.wireOp",EDGE,"E1712"),sQuery(id+"F0.wireOp",EDGE,"E1713"),sQuery(id+"F0.wireOp",EDGE,"E1714"),sQuery(id+"F0.wireOp",EDGE,"E1715"),sQuery(id+"F0.wireOp",EDGE,"E1716"),sQuery(id+"F0.wireOp",EDGE,"E1717"),sQuery(id+"F0.wireOp",EDGE,"E1718"),sQuery(id+"F0.wireOp",EDGE,"E1719"),sQuery(id+"F0.wireOp",EDGE,"E1720"),sQuery(id+"F0.wireOp",EDGE,"E1721"),sQuery(id+"F0.wireOp",EDGE,"E1722"),sQuery(id+"F0.wireOp",EDGE,"E1723"),sQuery(id+"F0.wireOp",EDGE,"E1724"),sQuery(id+"F0.wireOp",EDGE,"E1725"),sQuery(id+"F0.wireOp",EDGE,"E1726"),sQuery(id+"F0.wireOp",EDGE,"E1727"),sQuery(id+"F0.wireOp",EDGE,"E1728"),sQuery(id+"F0.wireOp",EDGE,"E1729"),sQuery(id+"F0.wireOp",EDGE,"E1730"),sQuery(id+"F0.wireOp",EDGE,"E1731"),sQuery(id+"F0.wireOp",EDGE,"E1732"),sQuery(id+"F0.wireOp",EDGE,"E1733"),sQuery(id+"F0.wireOp",EDGE,"E1733"),sQuery(id+"F0.wireOp",EDGE,"E1734"),sQuery(id+"F0.wireOp",EDGE,"E1735"),sQuery(id+"F0.wireOp",EDGE,"E1736"),sQuery(id+"F0.wireOp",EDGE,"E1737"),sQuery(id+"F0.wireOp",EDGE,"E1738"),sQuery(id+"F0.wireOp",EDGE,"E1738"),sQuery(id+"F0.wireOp",EDGE,"E1739"),sQuery(id+"F0.wireOp",EDGE,"E1740"),sQuery(id+"F0.wireOp",EDGE,"E1741"),sQuery(id+"F0.wireOp",EDGE,"E1742"),sQuery(id+"F0.wireOp",EDGE,"E1743"),sQuery(id+"F0.wireOp",EDGE,"E1744"),sQuery(id+"F0.wireOp",EDGE,"E1745"),sQuery(id+"F0.wireOp",EDGE,"E1746"),sQuery(id+"F0.wireOp",EDGE,"E1746"),sQuery(id+"F0.wireOp",EDGE,"E1747"),sQuery(id+"F0.wireOp",EDGE,"E1748"),sQuery(id+"F0.wireOp",EDGE,"E1748"),sQuery(id+"F0.wireOp",EDGE,"E1749"),sQuery(id+"F0.wireOp",EDGE,"E1750"),sQuery(id+"F0.wireOp",EDGE,"E1751"),sQuery(id+"F0.wireOp",EDGE,"E1751"),sQuery(id+"F0.wireOp",EDGE,"E1752"),sQuery(id+"F0.wireOp",EDGE,"E1753"),sQuery(id+"F0.wireOp",EDGE,"E1754"),sQuery(id+"F0.wireOp",EDGE,"E1755"),sQuery(id+"F0.wireOp",EDGE,"E1756"),sQuery(id+"F0.wireOp",EDGE,"E1757"),sQuery(id+"F0.wireOp",EDGE,"E1758"),sQuery(id+"F0.wireOp",EDGE,"E1759"),sQuery(id+"F0.wireOp",EDGE,"E1760"),sQuery(id+"F0.wireOp",EDGE,"E1761"),sQuery(id+"F0.wireOp",EDGE,"E1762"),sQuery(id+"F0.wireOp",EDGE,"E1763"),sQuery(id+"F0.wireOp",EDGE,"E1764"),sQuery(id+"F0.wireOp",EDGE,"E1765"),sQuery(id+"F0.wireOp",EDGE,"E1766"),sQuery(id+"F0.wireOp",EDGE,"E1766"),sQuery(id+"F0.wireOp",EDGE,"E1766"),sQuery(id+"F0.wireOp",EDGE,"E1767"),sQuery(id+"F0.wireOp",EDGE,"E1768"),sQuery(id+"F0.wireOp",EDGE,"E1769"),sQuery(id+"F0.wireOp",EDGE,"E1770"),sQuery(id+"F0.wireOp",EDGE,"E1771"),sQuery(id+"F0.wireOp",EDGE,"E1772"),sQuery(id+"F0.wireOp",EDGE,"E1773"),sQuery(id+"F0.wireOp",EDGE,"E1774"),sQuery(id+"F0.wireOp",EDGE,"E1775"),sQuery(id+"F0.wireOp",EDGE,"E1776"),sQuery(id+"F0.wireOp",EDGE,"E1777"),sQuery(id+"F0.wireOp",EDGE,"E1778"),sQuery(id+"F0.wireOp",EDGE,"E1779"),sQuery(id+"F0.wireOp",EDGE,"E1780"),sQuery(id+"F0.wireOp",EDGE,"E1781"),sQuery(id+"F0.wireOp",EDGE,"E1782"),sQuery(id+"F0.wireOp",EDGE,"E1783"),sQuery(id+"F0.wireOp",EDGE,"E1784"),sQuery(id+"F0.wireOp",EDGE,"E1784"),sQuery(id+"F0.wireOp",EDGE,"E1784"),sQuery(id+"F0.wireOp",EDGE,"E1785"),sQuery(id+"F0.wireOp",EDGE,"E1786"),sQuery(id+"F0.wireOp",EDGE,"E1787"),sQuery(id+"F0.wireOp",EDGE,"E1788"),sQuery(id+"F0.wireOp",EDGE,"E1789"),sQuery(id+"F0.wireOp",EDGE,"E1790"),sQuery(id+"F0.wireOp",EDGE,"E1791"),sQuery(id+"F0.wireOp",EDGE,"E1792"),sQuery(id+"F0.wireOp",EDGE,"E1793"),sQuery(id+"F0.wireOp",EDGE,"E1794"),sQuery(id+"F0.wireOp",EDGE,"E1795"),sQuery(id+"F0.wireOp",EDGE,"E1796"),sQuery(id+"F0.wireOp",EDGE,"E1797"),sQuery(id+"F0.wireOp",EDGE,"E1798"),sQuery(id+"F0.wireOp",EDGE,"E1799"),sQuery(id+"F0.wireOp",EDGE,"E1800"),sQuery(id+"F0.wireOp",EDGE,"E1800"),sQuery(id+"F0.wireOp",EDGE,"E1801"),sQuery(id+"F0.wireOp",EDGE,"E1802"),sQuery(id+"F0.wireOp",EDGE,"E1803"),sQuery(id+"F0.wireOp",EDGE,"E1804"),sQuery(id+"F0.wireOp",EDGE,"E1805"),sQuery(id+"F0.wireOp",EDGE,"E1805"),sQuery(id+"F0.wireOp",EDGE,"E1806"),sQuery(id+"F0.wireOp",EDGE,"E1807"),sQuery(id+"F0.wireOp",EDGE,"E1808"),sQuery(id+"F0.wireOp",EDGE,"E1809"),sQuery(id+"F0.wireOp",EDGE,"E1810"),sQuery(id+"F0.wireOp",EDGE,"E1811"),sQuery(id+"F0.wireOp",EDGE,"E1812"),sQuery(id+"F0.wireOp",EDGE,"E1813"),sQuery(id+"F0.wireOp",EDGE,"E1814"),sQuery(id+"F0.wireOp",EDGE,"E1815"),sQuery(id+"F0.wireOp",EDGE,"E1816"),sQuery(id+"F0.wireOp",EDGE,"E1817"),sQuery(id+"F0.wireOp",EDGE,"E1818"),sQuery(id+"F0.wireOp",EDGE,"E1819"),sQuery(id+"F0.wireOp",EDGE,"E1820"),sQuery(id+"F0.wireOp",EDGE,"E1821"),sQuery(id+"F0.wireOp",EDGE,"E1822"),sQuery(id+"F0.wireOp",EDGE,"E1823"),sQuery(id+"F0.wireOp",EDGE,"E1824"),sQuery(id+"F0.wireOp",EDGE,"E1825"),sQuery(id+"F0.wireOp",EDGE,"E1826"),sQuery(id+"F0.wireOp",EDGE,"E1827"),sQuery(id+"F0.wireOp",EDGE,"E1828"),sQuery(id+"F0.wireOp",EDGE,"E1829"),sQuery(id+"F0.wireOp",EDGE,"E1830"),sQuery(id+"F0.wireOp",EDGE,"E1831"),sQuery(id+"F0.wireOp",EDGE,"E1832"),sQuery(id+"F0.wireOp",EDGE,"E1833"),sQuery(id+"F0.wireOp",EDGE,"E1834"),sQuery(id+"F0.wireOp",EDGE,"E1835"),sQuery(id+"F0.wireOp",EDGE,"E1836"),sQuery(id+"F0.wireOp",EDGE,"E1837"),sQuery(id+"F0.wireOp",EDGE,"E1838"),sQuery(id+"F0.wireOp",EDGE,"E1839"),sQuery(id+"F0.wireOp",EDGE,"E1840"),sQuery(id+"F0.wireOp",EDGE,"E1841"),sQuery(id+"F0.wireOp",EDGE,"E1842"),sQuery(id+"F0.wireOp",EDGE,"E1843"),sQuery(id+"F0.wireOp",EDGE,"E1844"),sQuery(id+"F0.wireOp",EDGE,"E1845"),sQuery(id+"F0.wireOp",EDGE,"E1846"),sQuery(id+"F0.wireOp",EDGE,"E1847"),sQuery(id+"F0.wireOp",EDGE,"E1848"),sQuery(id+"F0.wireOp",EDGE,"E1849"),sQuery(id+"F0.wireOp",EDGE,"E1850"),sQuery(id+"F0.wireOp",EDGE,"E1851"),sQuery(id+"F0.wireOp",EDGE,"E1852"),sQuery(id+"F0.wireOp",EDGE,"E1853"),sQuery(id+"F0.wireOp",EDGE,"E1854"),sQuery(id+"F0.wireOp",EDGE,"E1855"),sQuery(id+"F0.wireOp",EDGE,"E1856"),sQuery(id+"F0.wireOp",EDGE,"E1857"),sQuery(id+"F0.wireOp",EDGE,"E1858"),sQuery(id+"F0.wireOp",EDGE,"E1859"),sQuery(id+"F0.wireOp",EDGE,"E1860"),sQuery(id+"F0.wireOp",EDGE,"E1861"),sQuery(id+"F0.wireOp",EDGE,"E1862"),sQuery(id+"F0.wireOp",EDGE,"E1863"),sQuery(id+"F0.wireOp",EDGE,"E1864"),sQuery(id+"F0.wireOp",EDGE,"E1865"),sQuery(id+"F0.wireOp",EDGE,"E1866"),sQuery(id+"F0.wireOp",EDGE,"E1867"),sQuery(id+"F0.wireOp",EDGE,"E1868"),sQuery(id+"F0.wireOp",EDGE,"E1869"),sQuery(id+"F0.wireOp",EDGE,"E1870"),sQuery(id+"F0.wireOp",EDGE,"E1871"),sQuery(id+"F0.wireOp",EDGE,"E1872"),sQuery(id+"F0.wireOp",EDGE,"E1873"),sQuery(id+"F0.wireOp",EDGE,"E1874"),sQuery(id+"F0.wireOp",EDGE,"E1875"),sQuery(id+"F0.wireOp",EDGE,"E1876"),sQuery(id+"F0.wireOp",EDGE,"E1877"),sQuery(id+"F0.wireOp",EDGE,"E1878"),sQuery(id+"F0.wireOp",EDGE,"E1879"),sQuery(id+"F0.wireOp",EDGE,"E1880"),sQuery(id+"F0.wireOp",EDGE,"E1881"),sQuery(id+"F0.wireOp",EDGE,"E1882"),sQuery(id+"F0.wireOp",EDGE,"E1883"),sQuery(id+"F0.wireOp",EDGE,"E1884"),sQuery(id+"F0.wireOp",EDGE,"E1885"),sQuery(id+"F0.wireOp",EDGE,"E1886"),sQuery(id+"F0.wireOp",EDGE,"E1887"),sQuery(id+"F0.wireOp",EDGE,"E1888"),sQuery(id+"F0.wireOp",EDGE,"E1889"),sQuery(id+"F0.wireOp",EDGE,"E1890"),sQuery(id+"F0.wireOp",EDGE,"E1891"),sQuery(id+"F0.wireOp",EDGE,"E1892"),sQuery(id+"F0.wireOp",EDGE,"E1893"),sQuery(id+"F0.wireOp",EDGE,"E1894"),sQuery(id+"F0.wireOp",EDGE,"E1895"),sQuery(id+"F0.wireOp",EDGE,"E1896"),sQuery(id+"F0.wireOp",EDGE,"E1897"),sQuery(id+"F0.wireOp",EDGE,"E1898"),sQuery(id+"F0.wireOp",EDGE,"E1899"),sQuery(id+"F0.wireOp",EDGE,"E1900"),sQuery(id+"F0.wireOp",EDGE,"E1901"),sQuery(id+"F0.wireOp",EDGE,"E1902"),sQuery(id+"F0.wireOp",EDGE,"E1903"),sQuery(id+"F0.wireOp",EDGE,"E1904"),sQuery(id+"F0.wireOp",EDGE,"E1905"),sQuery(id+"F0.wireOp",EDGE,"E1906"),sQuery(id+"F0.wireOp",EDGE,"E1907"),sQuery(id+"F0.wireOp",EDGE,"E1908"),sQuery(id+"F0.wireOp",EDGE,"E1909"),sQuery(id+"F0.wireOp",EDGE,"E1910"),sQuery(id+"F0.wireOp",EDGE,"E1911"),sQuery(id+"F0.wireOp",EDGE,"E1912"),sQuery(id+"F0.wireOp",EDGE,"E1913"),sQuery(id+"F0.wireOp",EDGE,"E1914"),sQuery(id+"F0.wireOp",EDGE,"E1915"),sQuery(id+"F0.wireOp",EDGE,"E1916"),sQuery(id+"F0.wireOp",EDGE,"E1917"),sQuery(id+"F0.wireOp",EDGE,"E1918"),sQuery(id+"F0.wireOp",EDGE,"E1919"),sQuery(id+"F0.wireOp",EDGE,"E1920"),sQuery(id+"F0.wireOp",EDGE,"E1921"),sQuery(id+"F0.wireOp",EDGE,"E1922"),sQuery(id+"F0.wireOp",EDGE,"E1923"),sQuery(id+"F0.wireOp",EDGE,"E1924"),sQuery(id+"F0.wireOp",EDGE,"E1925"),sQuery(id+"F0.wireOp",EDGE,"E1926"),sQuery(id+"F0.wireOp",EDGE,"E1927"),sQuery(id+"F0.wireOp",EDGE,"E1928"),sQuery(id+"F0.wireOp",EDGE,"E1929"),sQuery(id+"F0.wireOp",EDGE,"E1930"),sQuery(id+"F0.wireOp",EDGE,"E1931"),sQuery(id+"F0.wireOp",EDGE,"E1932"),sQuery(id+"F0.wireOp",EDGE,"E1933"),sQuery(id+"F0.wireOp",EDGE,"E1934"),sQuery(id+"F0.wireOp",EDGE,"E1935"),sQuery(id+"F0.wireOp",EDGE,"E1936"),sQuery(id+"F0.wireOp",EDGE,"E1937"),sQuery(id+"F0.wireOp",EDGE,"E1938"),sQuery(id+"F0.wireOp",EDGE,"E1939"),sQuery(id+"F0.wireOp",EDGE,"E1940"),sQuery(id+"F0.wireOp",EDGE,"E1941"),sQuery(id+"F0.wireOp",EDGE,"E1942"),sQuery(id+"F0.wireOp",EDGE,"E1943"),sQuery(id+"F0.wireOp",EDGE,"E1944"),sQuery(id+"F0.wireOp",EDGE,"E1945"),sQuery(id+"F0.wireOp",EDGE,"E1946"),sQuery(id+"F0.wireOp",EDGE,"E1947"),sQuery(id+"F0.wireOp",EDGE,"E1948"),sQuery(id+"F0.wireOp",EDGE,"E1949"),sQuery(id+"F0.wireOp",EDGE,"E1950"),sQuery(id+"F0.wireOp",EDGE,"E1951"),sQuery(id+"F0.wireOp",EDGE,"E1952"),sQuery(id+"F0.wireOp",EDGE,"E1953"),sQuery(id+"F0.wireOp",EDGE,"E1954"),sQuery(id+"F0.wireOp",EDGE,"E1955"),sQuery(id+"F0.wireOp",EDGE,"E1956"),sQuery(id+"F0.wireOp",EDGE,"E1957"),sQuery(id+"F0.wireOp",EDGE,"E1958"),sQuery(id+"F0.wireOp",EDGE,"E1959"),sQuery(id+"F0.wireOp",EDGE,"E1960"),sQuery(id+"F0.wireOp",EDGE,"E1961"),sQuery(id+"F0.wireOp",EDGE,"E1962"),sQuery(id+"F0.wireOp",EDGE,"E1963"),sQuery(id+"F0.wireOp",EDGE,"E1964"),sQuery(id+"F0.wireOp",EDGE,"E1965"),sQuery(id+"F0.wireOp",EDGE,"E1966"),sQuery(id+"F0.wireOp",EDGE,"E1967"),sQuery(id+"F0.wireOp",EDGE,"E1968"),sQuery(id+"F0.wireOp",EDGE,"E1969"),sQuery(id+"F0.wireOp",EDGE,"E1970"),sQuery(id+"F0.wireOp",EDGE,"E1971"),sQuery(id+"F0.wireOp",EDGE,"E1972"),sQuery(id+"F0.wireOp",EDGE,"E1973"),sQuery(id+"F0.wireOp",EDGE,"E1974"),sQuery(id+"F0.wireOp",EDGE,"E1975"),sQuery(id+"F0.wireOp",EDGE,"E1976"),sQuery(id+"F0.wireOp",EDGE,"E1977"),sQuery(id+"F0.wireOp",EDGE,"E1978"),sQuery(id+"F0.wireOp",EDGE,"E1979"),sQuery(id+"F0.wireOp",EDGE,"E1980"),sQuery(id+"F0.wireOp",EDGE,"E1981"),sQuery(id+"F0.wireOp",EDGE,"E1982"),sQuery(id+"F0.wireOp",EDGE,"E1983"),sQuery(id+"F0.wireOp",EDGE,"E1984"),sQuery(id+"F0.wireOp",EDGE,"E1985"),sQuery(id+"F0.wireOp",EDGE,"E1986"),sQuery(id+"F0.wireOp",EDGE,"E1987"),sQuery(id+"F0.wireOp",EDGE,"E1988"),sQuery(id+"F0.wireOp",EDGE,"E1989"),sQuery(id+"F0.wireOp",EDGE,"E1990"),sQuery(id+"F0.wireOp",EDGE,"E1991"),sQuery(id+"F0.wireOp",EDGE,"E1992"),sQuery(id+"F0.wireOp",EDGE,"E1993"),sQuery(id+"F0.wireOp",EDGE,"E1994"),sQuery(id+"F0.wireOp",EDGE,"E1995"),sQuery(id+"F0.wireOp",EDGE,"E1996"),sQuery(id+"F0.wireOp",EDGE,"E1997"),sQuery(id+"F0.wireOp",EDGE,"E1998"),sQuery(id+"F0.wireOp",EDGE,"E1999"),sQuery(id+"F0.wireOp",EDGE,"E2000"),sQuery(id+"F0.wireOp",EDGE,"E2001"),sQuery(id+"F0.wireOp",EDGE,"E2002"),sQuery(id+"F0.wireOp",EDGE,"E2003"),sQuery(id+"F0.wireOp",EDGE,"E2004"),sQuery(id+"F0.wireOp",EDGE,"E2005"),sQuery(id+"F0.wireOp",EDGE,"E2006"),sQuery(id+"F0.wireOp",EDGE,"E2007"),sQuery(id+"F0.wireOp",EDGE,"E2008"),sQuery(id+"F0.wireOp",EDGE,"E2009"),sQuery(id+"F0.wireOp",EDGE,"E2010"),sQuery(id+"F0.wireOp",EDGE,"E2011"),sQuery(id+"F0.wireOp",EDGE,"E2012"),sQuery(id+"F0.wireOp",EDGE,"E2013"),sQuery(id+"F0.wireOp",EDGE,"E2014"),sQuery(id+"F0.wireOp",EDGE,"E2015"),sQuery(id+"F0.wireOp",EDGE,"E2016"),sQuery(id+"F0.wireOp",EDGE,"E2017"),sQuery(id+"F0.wireOp",EDGE,"E2018"),sQuery(id+"F0.wireOp",EDGE,"E2019"),sQuery(id+"F0.wireOp",EDGE,"E2020"),sQuery(id+"F0.wireOp",EDGE,"E2021"),sQuery(id+"F0.wireOp",EDGE,"E2022"),sQuery(id+"F0.wireOp",EDGE,"E2023"),sQuery(id+"F0.wireOp",EDGE,"E2024"),sQuery(id+"F0.wireOp",EDGE,"E2025"),sQuery(id+"F0.wireOp",EDGE,"E2026"),sQuery(id+"F0.wireOp",EDGE,"E2027"),sQuery(id+"F0.wireOp",EDGE,"E2028"),sQuery(id+"F0.wireOp",EDGE,"E2029"),sQuery(id+"F0.wireOp",EDGE,"E2030"),sQuery(id+"F0.wireOp",EDGE,"E2031"),sQuery(id+"F0.wireOp",EDGE,"E2032"),sQuery(id+"F0.wireOp",EDGE,"E2033"),sQuery(id+"F0.wireOp",EDGE,"E2034"),sQuery(id+"F0.wireOp",EDGE,"E2035"),sQuery(id+"F0.wireOp",EDGE,"E2036"),sQuery(id+"F0.wireOp",EDGE,"E2037"),sQuery(id+"F0.wireOp",EDGE,"E2038"),sQuery(id+"F0.wireOp",EDGE,"E2039"),sQuery(id+"F0.wireOp",EDGE,"E2040"),sQuery(id+"F0.wireOp",EDGE,"E2041"),sQuery(id+"F0.wireOp",EDGE,"E2042"),sQuery(id+"F0.wireOp",EDGE,"E2043"),sQuery(id+"F0.wireOp",EDGE,"E2044"),sQuery(id+"F0.wireOp",EDGE,"E2045"),sQuery(id+"F0.wireOp",EDGE,"E2046"),sQuery(id+"F0.wireOp",EDGE,"E2047"),sQuery(id+"F0.wireOp",EDGE,"E2048"),sQuery(id+"F0.wireOp",EDGE,"E2049"),sQuery(id+"F0.wireOp",EDGE,"E2050"),sQuery(id+"F0.wireOp",EDGE,"E2051"),sQuery(id+"F0.wireOp",EDGE,"E2052"),sQuery(id+"F0.wireOp",EDGE,"E2053"),sQuery(id+"F0.wireOp",EDGE,"E2054"),sQuery(id+"F0.wireOp",EDGE,"E2055"),sQuery(id+"F0.wireOp",EDGE,"E2056"),sQuery(id+"F0.wireOp",EDGE,"E2057"),sQuery(id+"F0.wireOp",EDGE,"E2058"),sQuery(id+"F0.wireOp",EDGE,"E2059"),sQuery(id+"F0.wireOp",EDGE,"E2060"),sQuery(id+"F0.wireOp",EDGE,"E2061"),sQuery(id+"F0.wireOp",EDGE,"E2062"),sQuery(id+"F0.wireOp",EDGE,"E2063"),sQuery(id+"F0.wireOp",EDGE,"E2063"),sQuery(id+"F0.wireOp",EDGE,"E2063"),sQuery(id+"F0.wireOp",EDGE,"E2064"),sQuery(id+"F0.wireOp",EDGE,"E2065"),sQuery(id+"F0.wireOp",EDGE,"E2066"),sQuery(id+"F0.wireOp",EDGE,"E2067"),sQuery(id+"F0.wireOp",EDGE,"E2068"),sQuery(id+"F0.wireOp",EDGE,"E2069"),sQuery(id+"F0.wireOp",EDGE,"E2070"),sQuery(id+"F0.wireOp",EDGE,"E2071"),sQuery(id+"F0.wireOp",EDGE,"E2072"),sQuery(id+"F0.wireOp",EDGE,"E2073"),sQuery(id+"F0.wireOp",EDGE,"E2074"),sQuery(id+"F0.wireOp",EDGE,"E2075"),sQuery(id+"F0.wireOp",EDGE,"E2076"),sQuery(id+"F0.wireOp",EDGE,"E2077"),sQuery(id+"F0.wireOp",EDGE,"E2078"),sQuery(id+"F0.wireOp",EDGE,"E2079"),sQuery(id+"F0.wireOp",EDGE,"E2080"),sQuery(id+"F0.wireOp",EDGE,"E2081"),sQuery(id+"F0.wireOp",EDGE,"E2082"),sQuery(id+"F0.wireOp",EDGE,"E2083"),sQuery(id+"F0.wireOp",EDGE,"E2084"),sQuery(id+"F0.wireOp",EDGE,"E2085"),sQuery(id+"F0.wireOp",EDGE,"E2086"),sQuery(id+"F0.wireOp",EDGE,"E2087"),sQuery(id+"F0.wireOp",EDGE,"E2088"),sQuery(id+"F0.wireOp",EDGE,"E2089"),sQuery(id+"F0.wireOp",EDGE,"E2090"),sQuery(id+"F0.wireOp",EDGE,"E2091"),sQuery(id+"F0.wireOp",EDGE,"E2092"),sQuery(id+"F0.wireOp",EDGE,"E2093"),sQuery(id+"F0.wireOp",EDGE,"E2094"),sQuery(id+"F0.wireOp",EDGE,"E2095"),sQuery(id+"F0.wireOp",EDGE,"E2096"),sQuery(id+"F0.wireOp",EDGE,"E2097"),sQuery(id+"F0.wireOp",EDGE,"E2098"),sQuery(id+"F0.wireOp",EDGE,"E2099"),sQuery(id+"F0.wireOp",EDGE,"E2100"),sQuery(id+"F0.wireOp",EDGE,"E2101"),sQuery(id+"F0.wireOp",EDGE,"E2102"),sQuery(id+"F0.wireOp",EDGE,"E2103"),sQuery(id+"F0.wireOp",EDGE,"E2104"),sQuery(id+"F0.wireOp",EDGE,"E2105"),sQuery(id+"F0.wireOp",EDGE,"E2106"),sQuery(id+"F0.wireOp",EDGE,"E2107"),sQuery(id+"F0.wireOp",EDGE,"E2108"),sQuery(id+"F0.wireOp",EDGE,"E2109"),sQuery(id+"F0.wireOp",EDGE,"E2109"),sQuery(id+"F0.wireOp",EDGE,"E2110"),sQuery(id+"F0.wireOp",EDGE,"E2111"),sQuery(id+"F0.wireOp",EDGE,"E2112"),sQuery(id+"F0.wireOp",EDGE,"E2113"),sQuery(id+"F0.wireOp",EDGE,"E2114"),sQuery(id+"F0.wireOp",EDGE,"E2115"),sQuery(id+"F0.wireOp",EDGE,"E2116"),sQuery(id+"F0.wireOp",EDGE,"E2117"),sQuery(id+"F0.wireOp",EDGE,"E2118"),sQuery(id+"F0.wireOp",EDGE,"E2119"),sQuery(id+"F0.wireOp",EDGE,"E2120"),sQuery(id+"F0.wireOp",EDGE,"E2121"),sQuery(id+"F0.wireOp",EDGE,"E2122"),sQuery(id+"F0.wireOp",EDGE,"E2123"),sQuery(id+"F0.wireOp",EDGE,"E2124"),sQuery(id+"F0.wireOp",EDGE,"E2125"),sQuery(id+"F0.wireOp",EDGE,"E2126"),sQuery(id+"F0.wireOp",EDGE,"E2127"),sQuery(id+"F0.wireOp",EDGE,"E2128"),sQuery(id+"F0.wireOp",EDGE,"E2129"),sQuery(id+"F0.wireOp",EDGE,"E2130"),sQuery(id+"F0.wireOp",EDGE,"E2131"),sQuery(id+"F0.wireOp",EDGE,"E2132"),sQuery(id+"F0.wireOp",EDGE,"E2133"),sQuery(id+"F0.wireOp",EDGE,"E2134"),sQuery(id+"F0.wireOp",EDGE,"E2135"),sQuery(id+"F0.wireOp",EDGE,"E2136"),sQuery(id+"F0.wireOp",EDGE,"E2137"),sQuery(id+"F0.wireOp",EDGE,"E2138"),sQuery(id+"F0.wireOp",EDGE,"E2139"),sQuery(id+"F0.wireOp",EDGE,"E2140"),sQuery(id+"F0.wireOp",EDGE,"E2141"),sQuery(id+"F0.wireOp",EDGE,"E2142"),sQuery(id+"F0.wireOp",EDGE,"E2143"),sQuery(id+"F0.wireOp",EDGE,"E2144"),sQuery(id+"F0.wireOp",EDGE,"E2145"),sQuery(id+"F0.wireOp",EDGE,"E2146"),sQuery(id+"F0.wireOp",EDGE,"E2147"),sQuery(id+"F0.wireOp",EDGE,"E2148"),sQuery(id+"F0.wireOp",EDGE,"E2149"),sQuery(id+"F0.wireOp",EDGE,"E2150"),sQuery(id+"F0.wireOp",EDGE,"E2151"),sQuery(id+"F0.wireOp",EDGE,"E2152"),sQuery(id+"F0.wireOp",EDGE,"E2153"),sQuery(id+"F0.wireOp",EDGE,"E2154"),sQuery(id+"F0.wireOp",EDGE,"E2155"),sQuery(id+"F0.wireOp",EDGE,"E2156"),sQuery(id+"F0.wireOp",EDGE,"E2157"),sQuery(id+"F0.wireOp",EDGE,"E2158"),sQuery(id+"F0.wireOp",EDGE,"E2159"),sQuery(id+"F0.wireOp",EDGE,"E2160"),sQuery(id+"F0.wireOp",EDGE,"E2161"),sQuery(id+"F0.wireOp",EDGE,"E2162"),sQuery(id+"F0.wireOp",EDGE,"E2163"),sQuery(id+"F0.wireOp",EDGE,"E2164"),sQuery(id+"F0.wireOp",EDGE,"E2165"),sQuery(id+"F0.wireOp",EDGE,"E2166"),sQuery(id+"F0.wireOp",EDGE,"E2167"),sQuery(id+"F0.wireOp",EDGE,"E2168"),sQuery(id+"F0.wireOp",EDGE,"E2169"),sQuery(id+"F0.wireOp",EDGE,"E2170"),sQuery(id+"F0.wireOp",EDGE,"E2171"),sQuery(id+"F0.wireOp",EDGE,"E2172"),sQuery(id+"F0.wireOp",EDGE,"E2173"),sQuery(id+"F0.wireOp",EDGE,"E2174"),sQuery(id+"F0.wireOp",EDGE,"E2175"),sQuery(id+"F0.wireOp",EDGE,"E2176"),sQuery(id+"F0.wireOp",EDGE,"E2177"),sQuery(id+"F0.wireOp",EDGE,"E2178"),sQuery(id+"F0.wireOp",EDGE,"E2179"),sQuery(id+"F0.wireOp",EDGE,"E2180"),sQuery(id+"F0.wireOp",EDGE,"E2181"),sQuery(id+"F0.wireOp",EDGE,"E2182"),sQuery(id+"F0.wireOp",EDGE,"E2183"),sQuery(id+"F0.wireOp",EDGE,"E2184"),sQuery(id+"F0.wireOp",EDGE,"E2185"),sQuery(id+"F0.wireOp",EDGE,"E2186"),sQuery(id+"F0.wireOp",EDGE,"E2187"),sQuery(id+"F0.wireOp",EDGE,"E2188"),sQuery(id+"F0.wireOp",EDGE,"E2189"),sQuery(id+"F0.wireOp",EDGE,"E2190"),sQuery(id+"F0.wireOp",EDGE,"E2191"),sQuery(id+"F0.wireOp",EDGE,"E2192"),sQuery(id+"F0.wireOp",EDGE,"E2193"),sQuery(id+"F0.wireOp",EDGE,"E2194"),sQuery(id+"F0.wireOp",EDGE,"E2195"),sQuery(id+"F0.wireOp",EDGE,"E2196"),sQuery(id+"F0.wireOp",EDGE,"E2197"),sQuery(id+"F0.wireOp",EDGE,"E2198"),sQuery(id+"F0.wireOp",EDGE,"E2199"),sQuery(id+"F0.wireOp",EDGE,"E2200"),sQuery(id+"F0.wireOp",EDGE,"E2201"),sQuery(id+"F0.wireOp",EDGE,"E2202"),sQuery(id+"F0.wireOp",EDGE,"E2203"),sQuery(id+"F0.wireOp",EDGE,"E2204"),sQuery(id+"F0.wireOp",EDGE,"E2205"),sQuery(id+"F0.wireOp",EDGE,"E2206"),sQuery(id+"F0.wireOp",EDGE,"E2207"),sQuery(id+"F0.wireOp",EDGE,"E2208"),sQuery(id+"F0.wireOp",EDGE,"E2209"),sQuery(id+"F0.wireOp",EDGE,"E2210"),sQuery(id+"F0.wireOp",EDGE,"E2211"),sQuery(id+"F0.wireOp",EDGE,"E2212"),sQuery(id+"F0.wireOp",EDGE,"E2213"),sQuery(id+"F0.wireOp",EDGE,"E2214"),sQuery(id+"F0.wireOp",EDGE,"E2214"),sQuery(id+"F0.wireOp",EDGE,"E2215"),sQuery(id+"F0.wireOp",EDGE,"E2216"),sQuery(id+"F0.wireOp",EDGE,"E2217"),sQuery(id+"F0.wireOp",EDGE,"E2218"),sQuery(id+"F0.wireOp",EDGE,"E2218"),sQuery(id+"F0.wireOp",EDGE,"E2219"),sQuery(id+"F0.wireOp",EDGE,"E2220"),sQuery(id+"F0.wireOp",EDGE,"E2221"),sQuery(id+"F0.wireOp",EDGE,"E2222"),sQuery(id+"F0.wireOp",EDGE,"E2223"),sQuery(id+"F0.wireOp",EDGE,"E2224"),sQuery(id+"F0.wireOp",EDGE,"E2224"),sQuery(id+"F0.wireOp",EDGE,"E2225"),sQuery(id+"F0.wireOp",EDGE,"E2226"),sQuery(id+"F0.wireOp",EDGE,"E2227"),sQuery(id+"F0.wireOp",EDGE,"E2227"),sQuery(id+"F0.wireOp",EDGE,"E2227"),sQuery(id+"F0.wireOp",EDGE,"E2228"),sQuery(id+"F0.wireOp",EDGE,"E2229"),sQuery(id+"F0.wireOp",EDGE,"E2230"),sQuery(id+"F0.wireOp",EDGE,"E2230"),sQuery(id+"F0.wireOp",EDGE,"E2231"),sQuery(id+"F0.wireOp",EDGE,"E2232"),sQuery(id+"F0.wireOp",EDGE,"E2232"),sQuery(id+"F0.wireOp",EDGE,"E2233"),sQuery(id+"F0.wireOp",EDGE,"E2234"),sQuery(id+"F0.wireOp",EDGE,"E2234"),sQuery(id+"F0.wireOp",EDGE,"E2234"),sQuery(id+"F0.wireOp",EDGE,"E2234"),sQuery(id+"F0.wireOp",EDGE,"E2235"),sQuery(id+"F0.wireOp",EDGE,"E2236"),sQuery(id+"F0.wireOp",EDGE,"E2237"),sQuery(id+"F0.wireOp",EDGE,"E2238"),sQuery(id+"F0.wireOp",EDGE,"E2238"),sQuery(id+"F0.wireOp",EDGE,"E2239"),sQuery(id+"F0.wireOp",EDGE,"E2240"),sQuery(id+"F0.wireOp",EDGE,"E2241"),sQuery(id+"F0.wireOp",EDGE,"E2242"),sQuery(id+"F0.wireOp",EDGE,"E2243"),sQuery(id+"F0.wireOp",EDGE,"E2244"),sQuery(id+"F0.wireOp",EDGE,"E2245"),sQuery(id+"F0.wireOp",EDGE,"E2246"),sQuery(id+"F0.wireOp",EDGE,"E2247"),sQuery(id+"F0.wireOp",EDGE,"E2248"),sQuery(id+"F0.wireOp",EDGE,"E2248"),sQuery(id+"F0.wireOp",EDGE,"E2249"),sQuery(id+"F0.wireOp",EDGE,"E2250"),sQuery(id+"F0.wireOp",EDGE,"E2250"),sQuery(id+"F0.wireOp",EDGE,"E2250"),sQuery(id+"F0.wireOp",EDGE,"E2250"),sQuery(id+"F0.wireOp",EDGE,"E2251"),sQuery(id+"F0.wireOp",EDGE,"E2252"),sQuery(id+"F0.wireOp",EDGE,"E2253"),sQuery(id+"F0.wireOp",EDGE,"E2254"),sQuery(id+"F0.wireOp",EDGE,"E2255"),sQuery(id+"F0.wireOp",EDGE,"E2256"),sQuery(id+"F0.wireOp",EDGE,"E2257"),sQuery(id+"F0.wireOp",EDGE,"E2258"),sQuery(id+"F0.wireOp",EDGE,"E2259"),sQuery(id+"F0.wireOp",EDGE,"E2259"),sQuery(id+"F0.wireOp",EDGE,"E2259"),sQuery(id+"F0.wireOp",EDGE,"E2259"),sQuery(id+"F0.wireOp",EDGE,"E2259"),sQuery(id+"F0.wireOp",EDGE,"E2259"),sQuery(id+"F0.wireOp",EDGE,"E2260"),sQuery(id+"F0.wireOp",EDGE,"E2261"),sQuery(id+"F0.wireOp",EDGE,"E2262"),sQuery(id+"F0.wireOp",EDGE,"E2263"),sQuery(id+"F0.wireOp",EDGE,"E2264"),sQuery(id+"F0.wireOp",EDGE,"E2265"),sQuery(id+"F0.wireOp",EDGE,"E2266"),sQuery(id+"F0.wireOp",EDGE,"E2267"),sQuery(id+"F0.wireOp",EDGE,"E2268"),sQuery(id+"F0.wireOp",EDGE,"E2268"),sQuery(id+"F0.wireOp",EDGE,"E2269"),sQuery(id+"F0.wireOp",EDGE,"E2270"),sQuery(id+"F0.wireOp",EDGE,"E2271"),sQuery(id+"F0.wireOp",EDGE,"E2272"),sQuery(id+"F0.wireOp",EDGE,"E2273"),sQuery(id+"F0.wireOp",EDGE,"E2274"),sQuery(id+"F0.wireOp",EDGE,"E2275"),sQuery(id+"F0.wireOp",EDGE,"E2276"),sQuery(id+"F0.wireOp",EDGE,"E2277"),sQuery(id+"F0.wireOp",EDGE,"E2278"),sQuery(id+"F0.wireOp",EDGE,"E2279"),sQuery(id+"F0.wireOp",EDGE,"E2280"),sQuery(id+"F0.wireOp",EDGE,"E2281"),sQuery(id+"F0.wireOp",EDGE,"E2281"),sQuery(id+"F0.wireOp",EDGE,"E2282"),sQuery(id+"F0.wireOp",EDGE,"E2283"),sQuery(id+"F0.wireOp",EDGE,"E2284"),sQuery(id+"F0.wireOp",EDGE,"E2285"),sQuery(id+"F0.wireOp",EDGE,"E2286"),sQuery(id+"F0.wireOp",EDGE,"E2287"),sQuery(id+"F0.wireOp",EDGE,"E2288")])],"isStart":false});
            var sketch = newSketch(context, id + "F3", { "sketchPlane" : qUnion([Q0])});
            skLineSegment(sketch, "E6425.bottom", {"start": v(8.5, -5.2) * mm, "end": v(-7.99, -5.2) * mm});
            skLineSegment(sketch, "E6425.top", {"start": v(8.5, 1.66) * mm, "end": v(-7.99, 1.66) * mm});
            skLineSegment(sketch, "E6425.left", {"start": v(8.5, -5.2) * mm, "end": v(8.5, 1.66) * mm});
            skLineSegment(sketch, "E6425.right", {"start": v(-7.99, -5.2) * mm, "end": v(-7.99, 1.66) * mm});
            skSolve(sketch);
        }
        {
            var Q0;
            Q0 = qSketchRegion(id + "F3", true);
            extrude(context, id + "F4", {"entities" : qUnion([Q0]), "depth" : 1 * mm, "offsetDistance" : 25 * mm});
        }
    });
